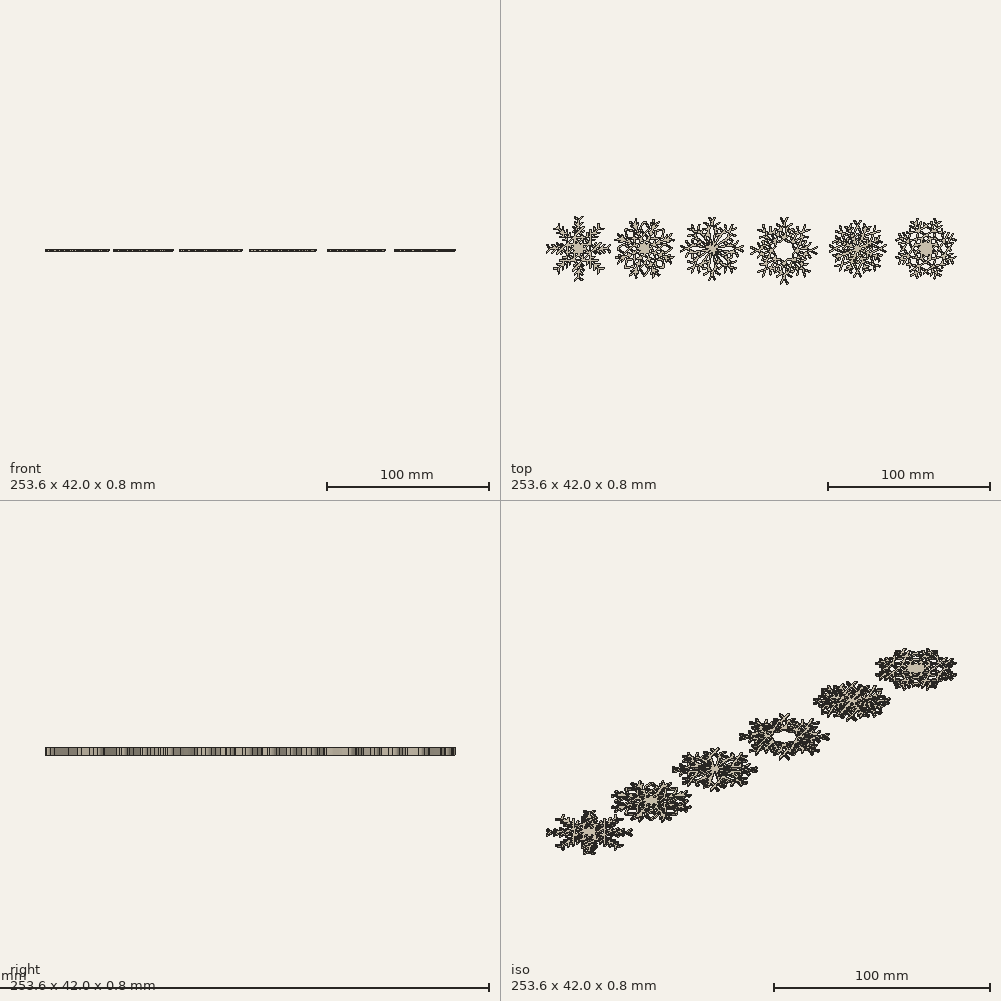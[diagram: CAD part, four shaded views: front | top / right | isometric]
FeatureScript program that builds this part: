
annotation { "Feature Type Name" : "Feature", "Feature Type Description" : "" }
export const myFeature = defineFeature(function(context is Context, id is Id, definition is map)
    precondition{}
    {
        {
            var Q0;
            Q0=qCreatedBy(makeId("Top.planeOp"),FACE);
            var sketch = newSketch(context, id + "F0", { "sketchPlane" : qUnion([Q0])});
            skFitSpline(sketch, "E0", {"points": [v(9.25, 5.53) * mm, v(8.92, 5.5) * mm, v(7.79, 5.23) * mm, v(7.5, 5.1) * mm]});
            skFitSpline(sketch, "E1", {"points": [v(7.5, 5.1) * mm, v(7.78, 4.57) * mm, v(8.1, 4.08) * mm, v(8.43, 3.59) * mm]});
            skFitSpline(sketch, "E2", {"points": [v(8.43, 3.59) * mm, v(8.94, 3.76) * mm, v(9.43, 3.93) * mm, v(9.95, 4.1) * mm]});
            skFitSpline(sketch, "E3", {"points": [v(9.95, 4.1) * mm, v(9.7, 4.6) * mm, v(9.47, 5.07) * mm, v(9.25, 5.53) * mm]});
            skFitSpline(sketch, "E4", {"points": [v(15.97, -10.43) * mm, v(15.7, -10.56) * mm, v(15.46, -10.66) * mm, v(15.23, -10.77) * mm]});
            skFitSpline(sketch, "E5", {"points": [v(15.23, -10.77) * mm, v(15, -10.88) * mm, v(14.77, -11.01) * mm, v(14.52, -11.14) * mm]});
            skFitSpline(sketch, "E6", {"points": [v(14.52, -11.14) * mm, v(14.65, -11.71) * mm, v(14.75, -12.3) * mm, v(14.96, -12.89) * mm]});
            skFitSpline(sketch, "E7", {"points": [v(14.96, -12.89) * mm, v(15.5, -12.56) * mm, v(15.99, -12.25) * mm, v(16.48, -11.95) * mm]});
            skFitSpline(sketch, "E8", {"points": [v(16.48, -11.95) * mm, v(16.3, -11.43) * mm, v(16.14, -10.94) * mm, v(15.97, -10.43) * mm]});
            skFitSpline(sketch, "E9", {"points": [v(32, 3.59) * mm, v(32.33, 4.1) * mm, v(32.66, 4.58) * mm, v(32.95, 5.14) * mm]});
            skFitSpline(sketch, "E10", {"points": [v(32.95, 5.14) * mm, v(32.34, 5.29) * mm, v(31.77, 5.42) * mm, v(31.2, 5.56) * mm]});
            skFitSpline(sketch, "E11", {"points": [v(31.2, 5.56) * mm, v(30.96, 5.06) * mm, v(30.73, 4.6) * mm, v(30.49, 4.1) * mm]});
            skFitSpline(sketch, "E12", {"points": [v(30.49, 4.1) * mm, v(31, 3.93) * mm, v(31.5, 3.76) * mm, v(32, 3.59) * mm]});
            skFitSpline(sketch, "E13", {"points": [v(32.98, -5.43) * mm, v(32.63, -4.88) * mm, v(32.33, -4.39) * mm, v(32.02, -3.88) * mm]});
            skFitSpline(sketch, "E14", {"points": [v(32.02, -3.88) * mm, v(31.5, -4.06) * mm, v(31.01, -4.22) * mm, v(30.49, -4.4) * mm]});
            skFitSpline(sketch, "E15", {"points": [v(30.49, -4.4) * mm, v(30.73, -4.9) * mm, v(30.96, -5.36) * mm, v(31.2, -5.85) * mm]});
            skFitSpline(sketch, "E16", {"points": [v(31.2, -5.85) * mm, v(31.78, -5.72) * mm, v(32.35, -5.58) * mm, v(32.98, -5.43) * mm]});
            skFitSpline(sketch, "E17", {"points": [v(25.9, 10.83) * mm, v(25.8, 11.42) * mm, v(25.67, 12) * mm, v(25.49, 12.57) * mm]});
            skFitSpline(sketch, "E18", {"points": [v(25.49, 12.57) * mm, v(24.94, 12.3) * mm, v(24.45, 11.97) * mm, v(23.96, 11.64) * mm]});
            skFitSpline(sketch, "E19", {"points": [v(23.96, 11.64) * mm, v(24.14, 11.14) * mm, v(24.24, 10.62) * mm, v(24.5, 10.14) * mm]});
            skFitSpline(sketch, "E20", {"points": [v(24.5, 10.14) * mm, v(24.97, 10.37) * mm, v(25.44, 10.6) * mm, v(25.9, 10.83) * mm]});
            skFitSpline(sketch, "E21", {"points": [v(9.23, -5.86) * mm, v(9.48, -5.36) * mm, v(9.7, -4.9) * mm, v(9.95, -4.4) * mm]});
            skFitSpline(sketch, "E22", {"points": [v(9.95, -4.4) * mm, v(9.42, -4.22) * mm, v(8.92, -4.05) * mm, v(8.42, -3.89) * mm]});
            skFitSpline(sketch, "E23", {"points": [v(8.42, -3.89) * mm, v(8.1, -4.4) * mm, v(7.76, -4.88) * mm, v(7.48, -5.44) * mm]});
            skFitSpline(sketch, "E24", {"points": [v(7.48, -5.44) * mm, v(8.09, -5.58) * mm, v(8.65, -5.72) * mm, v(9.23, -5.86) * mm]});
            skFitSpline(sketch, "E25", {"points": [v(16.48, 11.64) * mm, v(15.98, 11.96) * mm, v(15.5, 12.3) * mm, v(14.92, 12.58) * mm]});
            skFitSpline(sketch, "E26", {"points": [v(14.92, 12.58) * mm, v(14.78, 11.97) * mm, v(14.64, 11.4) * mm, v(14.51, 10.83) * mm]});
            skFitSpline(sketch, "E27", {"points": [v(14.51, 10.83) * mm, v(15, 10.6) * mm, v(15.46, 10.37) * mm, v(15.96, 10.12) * mm]});
            skFitSpline(sketch, "E28", {"points": [v(15.96, 10.12) * mm, v(16.14, 10.64) * mm, v(16.3, 11.14) * mm, v(16.48, 11.64) * mm]});
            skFitSpline(sketch, "E29", {"points": [v(25.48, -12.9) * mm, v(25.67, -12.28) * mm, v(25.8, -11.7) * mm, v(25.9, -11.13) * mm]});
            skFitSpline(sketch, "E30", {"points": [v(25.9, -11.13) * mm, v(25.42, -10.89) * mm, v(24.96, -10.66) * mm, v(24.47, -10.42) * mm]});
            skFitSpline(sketch, "E31", {"points": [v(24.47, -10.42) * mm, v(24.3, -10.95) * mm, v(24.12, -11.44) * mm, v(23.95, -11.95) * mm]});
            skFitSpline(sketch, "E32", {"points": [v(23.95, -11.95) * mm, v(24.46, -12.26) * mm, v(24.95, -12.57) * mm, v(25.48, -12.9) * mm]});
            skLineSegment(sketch, "E33", {"start": v(31, -7.7) * mm, "end": v(31.03, -7.68) * mm});
            skFitSpline(sketch, "E34", {"points": [v(31.03, -7.68) * mm, v(30.53, -6.7) * mm, v(30.04, -5.7) * mm, v(29.54, -4.7) * mm]});
            skFitSpline(sketch, "E35", {"points": [v(29.54, -4.7) * mm, v(28.68, -4.98) * mm, v(27.82, -5.24) * mm, v(26.95, -5.5) * mm]});
            skFitSpline(sketch, "E36", {"points": [v(26.95, -5.5) * mm, v(28.31, -6.25) * mm, v(29.65, -6.98) * mm, v(31, -7.7) * mm]});
            skFitSpline(sketch, "E37", {"points": [v(30.04, -3.52) * mm, v(31.1, -3.16) * mm, v(32.16, -2.81) * mm, v(33.26, -2.45) * mm]});
            skFitSpline(sketch, "E38", {"points": [v(33.26, -2.45) * mm, v(31.74, -2) * mm, v(30.27, -1.56) * mm, v(28.77, -1.12) * mm]});
            skFitSpline(sketch, "E39", {"points": [v(28.77, -1.12) * mm, v(29.2, -1.94) * mm, v(29.61, -2.72) * mm, v(30.04, -3.52) * mm]});
            skFitSpline(sketch, "E40", {"points": [v(7.17, -2.45) * mm, v(8.28, -2.82) * mm, v(9.34, -3.17) * mm, v(10.4, -3.52) * mm]});
            skFitSpline(sketch, "E41", {"points": [v(10.4, -3.52) * mm, v(10.82, -2.73) * mm, v(11.23, -1.94) * mm, v(11.66, -1.12) * mm]});
            skFitSpline(sketch, "E42", {"points": [v(11.66, -1.12) * mm, v(10.16, -1.57) * mm, v(8.69, -2) * mm, v(7.17, -2.45) * mm]});
            skFitSpline(sketch, "E43", {"points": [v(25.58, 6.58) * mm, v(26.33, 7.96) * mm, v(27.06, 9.3) * mm, v(27.81, 10.7) * mm]});
            skFitSpline(sketch, "E44", {"points": [v(27.81, 10.7) * mm, v(26.77, 10.17) * mm, v(25.77, 9.68) * mm, v(24.78, 9.18) * mm]});
            skFitSpline(sketch, "E45", {"points": [v(24.78, 9.18) * mm, v(25.04, 8.32) * mm, v(25.3, 7.47) * mm, v(25.58, 6.58) * mm]});
            skFitSpline(sketch, "E46", {"points": [v(23.59, 9.67) * mm, v(23.23, 10.73) * mm, v(22.88, 11.79) * mm, v(22.51, 12.9) * mm]});
            skFitSpline(sketch, "E47", {"points": [v(22.51, 12.9) * mm, v(22.06, 11.37) * mm, v(21.63, 9.9) * mm, v(21.19, 8.4) * mm]});
            skFitSpline(sketch, "E48", {"points": [v(21.19, 8.4) * mm, v(22, 8.83) * mm, v(22.8, 9.25) * mm, v(23.59, 9.67) * mm]});
            skFitSpline(sketch, "E49", {"points": [v(15.66, -9.47) * mm, v(15.39, -8.61) * mm, v(15.13, -7.76) * mm, v(14.86, -6.88) * mm]});
            skFitSpline(sketch, "E50", {"points": [v(14.86, -6.88) * mm, v(14.1, -8.26) * mm, v(13.38, -9.6) * mm, v(12.62, -11) * mm]});
            skFitSpline(sketch, "E51", {"points": [v(12.62, -11) * mm, v(13.67, -10.47) * mm, v(14.66, -9.97) * mm, v(15.66, -9.47) * mm]});
            skFitSpline(sketch, "E52", {"points": [v(28.76, 0.8) * mm, v(29.1, 0.9) * mm, v(29.4, 1) * mm, v(29.7, 1.09) * mm]});
            skFitSpline(sketch, "E53", {"points": [v(29.7, 1.09) * mm, v(29.99, 1.18) * mm, v(30.28, 1.28) * mm, v(30.58, 1.36) * mm]});
            skFitSpline(sketch, "E54", {"points": [v(30.58, 1.36) * mm, v(30.87, 1.45) * mm, v(31.16, 1.53) * mm, v(31.46, 1.61) * mm]});
            skFitSpline(sketch, "E55", {"points": [v(31.46, 1.61) * mm, v(31.75, 1.7) * mm, v(32.05, 1.78) * mm, v(32.35, 1.87) * mm]});
            skFitSpline(sketch, "E56", {"points": [v(32.35, 1.87) * mm, v(32.64, 1.96) * mm, v(32.93, 2.05) * mm, v(33.25, 2.15) * mm]});
            skFitSpline(sketch, "E57", {"points": [v(33.25, 2.15) * mm, v(32.15, 2.52) * mm, v(31.1, 2.87) * mm, v(30.04, 3.22) * mm]});
            skFitSpline(sketch, "E58", {"points": [v(30.04, 3.22) * mm, v(29.62, 2.43) * mm, v(29.2, 1.65) * mm, v(28.76, 0.8) * mm]});
            skFitSpline(sketch, "E59", {"points": [v(13.49, 5.21) * mm, v(12.1, 5.96) * mm, v(10.76, 6.7) * mm, v(9.37, 7.45) * mm]});
            skFitSpline(sketch, "E60", {"points": [v(9.37, 7.45) * mm, v(9.9, 6.4) * mm, v(10.4, 5.4) * mm, v(10.9, 4.41) * mm]});
            skFitSpline(sketch, "E61", {"points": [v(10.9, 4.41) * mm, v(11.76, 4.68) * mm, v(12.6, 4.94) * mm, v(13.49, 5.21) * mm]});
            skFitSpline(sketch, "E62", {"points": [v(31.03, 7.38) * mm, v(31.02, 7.4) * mm, v(31, 7.4) * mm, v(31, 7.41) * mm]});
            skFitSpline(sketch, "E63", {"points": [v(31, 7.41) * mm, v(29.66, 6.68) * mm, v(28.32, 5.95) * mm, v(26.95, 5.2) * mm]});
            skFitSpline(sketch, "E64", {"points": [v(26.95, 5.2) * mm, v(27.83, 4.94) * mm, v(28.68, 4.68) * mm, v(29.54, 4.41) * mm]});
            skFitSpline(sketch, "E65", {"points": [v(29.54, 4.41) * mm, v(30.04, 5.4) * mm, v(30.53, 6.4) * mm, v(31.03, 7.38) * mm]});
            skFitSpline(sketch, "E66", {"points": [v(17.9, -13.13) * mm, v(17.91, -13.13) * mm, v(17.93, -13.13) * mm, v(17.94, -13.13) * mm]});
            skFitSpline(sketch, "E67", {"points": [v(17.94, -13.13) * mm, v(18.16, -12.4) * mm, v(18.37, -11.67) * mm, v(18.58, -10.94) * mm]});
            skFitSpline(sketch, "E68", {"points": [v(18.58, -10.94) * mm, v(18.8, -10.2) * mm, v(19.02, -9.47) * mm, v(19.25, -8.7) * mm]});
            skFitSpline(sketch, "E69", {"points": [v(19.25, -8.7) * mm, v(18.42, -9.14) * mm, v(17.63, -9.56) * mm, v(16.85, -9.97) * mm]});
            skFitSpline(sketch, "E70", {"points": [v(16.85, -9.97) * mm, v(17.2, -11.03) * mm, v(17.55, -12.08) * mm, v(17.9, -13.13) * mm]});
            skFitSpline(sketch, "E71", {"points": [v(13.48, -5.5) * mm, v(12.6, -5.24) * mm, v(11.75, -4.97) * mm, v(10.9, -4.7) * mm]});
            skFitSpline(sketch, "E72", {"points": [v(10.9, -4.7) * mm, v(10.39, -5.71) * mm, v(9.9, -6.7) * mm, v(9.37, -7.75) * mm]});
            skFitSpline(sketch, "E73", {"points": [v(9.37, -7.75) * mm, v(10.77, -6.99) * mm, v(12.1, -6.26) * mm, v(13.48, -5.5) * mm]});
            skFitSpline(sketch, "E74", {"points": [v(15.66, 9.18) * mm, v(14.66, 9.68) * mm, v(13.66, 10.17) * mm, v(12.62, 10.7) * mm]});
            skFitSpline(sketch, "E75", {"points": [v(12.62, 10.7) * mm, v(13.38, 9.3) * mm, v(14.1, 7.96) * mm, v(14.86, 6.58) * mm]});
            skFitSpline(sketch, "E76", {"points": [v(14.86, 6.58) * mm, v(15.13, 7.46) * mm, v(15.39, 8.3) * mm, v(15.66, 9.18) * mm]});
            skFitSpline(sketch, "E77", {"points": [v(22.51, -13.19) * mm, v(22.88, -12.08) * mm, v(23.23, -11.02) * mm, v(23.59, -9.97) * mm]});
            skFitSpline(sketch, "E78", {"points": [v(23.59, -9.97) * mm, v(22.79, -9.55) * mm, v(22, -9.13) * mm, v(21.19, -8.7) * mm]});
            skFitSpline(sketch, "E79", {"points": [v(21.19, -8.7) * mm, v(21.63, -10.2) * mm, v(22.07, -11.67) * mm, v(22.51, -13.19) * mm]});
            skFitSpline(sketch, "E80", {"points": [v(7.22, 2.16) * mm, v(7.22, 2.15) * mm, v(7.22, 2.14) * mm, v(7.22, 2.13) * mm]});
            skFitSpline(sketch, "E81", {"points": [v(7.22, 2.13) * mm, v(7.95, 1.91) * mm, v(8.7, 1.7) * mm, v(9.42, 1.49) * mm]});
            skFitSpline(sketch, "E82", {"points": [v(9.42, 1.49) * mm, v(10.16, 1.27) * mm, v(10.9, 1.05) * mm, v(11.67, 0.81) * mm]});
            skFitSpline(sketch, "E83", {"points": [v(11.67, 0.81) * mm, v(11.23, 1.65) * mm, v(10.81, 2.44) * mm, v(10.4, 3.22) * mm]});
            skFitSpline(sketch, "E84", {"points": [v(10.4, 3.22) * mm, v(9.33, 2.87) * mm, v(8.28, 2.52) * mm, v(7.22, 2.16) * mm]});
            skFitSpline(sketch, "E85", {"points": [v(27.81, -11) * mm, v(27.05, -9.6) * mm, v(26.32, -8.25) * mm, v(25.58, -6.88) * mm]});
            skFitSpline(sketch, "E86", {"points": [v(25.58, -6.88) * mm, v(25.3, -7.77) * mm, v(25.04, -8.62) * mm, v(24.78, -9.47) * mm]});
            skFitSpline(sketch, "E87", {"points": [v(24.78, -9.47) * mm, v(25.78, -9.98) * mm, v(26.77, -10.47) * mm, v(27.81, -11) * mm]});
            skFitSpline(sketch, "E88", {"points": [v(17.94, 12.83) * mm, v(17.92, 12.83) * mm, v(17.91, 12.83) * mm, v(17.9, 12.83) * mm]});
            skFitSpline(sketch, "E89", {"points": [v(17.9, 12.83) * mm, v(17.55, 11.78) * mm, v(17.2, 10.72) * mm, v(16.85, 9.67) * mm]});
            skFitSpline(sketch, "E90", {"points": [v(16.85, 9.67) * mm, v(17.64, 9.25) * mm, v(18.43, 8.84) * mm, v(19.25, 8.4) * mm]});
            skFitSpline(sketch, "E91", {"points": [v(19.25, 8.4) * mm, v(18.8, 9.9) * mm, v(18.37, 11.37) * mm, v(17.94, 12.83) * mm]});
            skFitSpline(sketch, "E92", {"points": [v(12.85, 0.75) * mm, v(13.06, 1) * mm, v(13.24, 1.21) * mm, v(13.4, 1.44) * mm]});
            skFitSpline(sketch, "E93", {"points": [v(13.4, 1.44) * mm, v(13.61, 1.73) * mm, v(13.83, 2.02) * mm, v(14.1, 2.26) * mm]});
            skFitSpline(sketch, "E94", {"points": [v(14.1, 2.26) * mm, v(14.18, 2.33) * mm, v(14.19, 2.42) * mm, v(14.2, 2.51) * mm]});
            skFitSpline(sketch, "E95", {"points": [v(14.2, 2.51) * mm, v(14.2, 2.77) * mm, v(14.21, 3.02) * mm, v(14.23, 3.28) * mm]});
            skFitSpline(sketch, "E96", {"points": [v(14.23, 3.28) * mm, v(14.25, 3.45) * mm, v(14.3, 3.62) * mm, v(14.31, 3.8) * mm]});
            skFitSpline(sketch, "E97", {"points": [v(14.31, 3.8) * mm, v(14.33, 4) * mm, v(14.34, 4.2) * mm, v(14.36, 4.42) * mm]});
            skFitSpline(sketch, "E98", {"points": [v(14.36, 4.42) * mm, v(13.34, 4.14) * mm, v(12.35, 3.88) * mm, v(11.36, 3.52) * mm]});
            skFitSpline(sketch, "E99", {"points": [v(11.36, 3.52) * mm, v(11.81, 2.56) * mm, v(12.33, 1.67) * mm, v(12.85, 0.75) * mm]});
            skFitSpline(sketch, "E100", {"points": [v(15.68, -6) * mm, v(15.7, -6.37) * mm, v(16.4, -8.68) * mm, v(16.58, -8.99) * mm]});
            skFitSpline(sketch, "E101", {"points": [v(16.58, -8.99) * mm, v(17.5, -8.55) * mm, v(18.4, -8.04) * mm, v(19.31, -7.51) * mm]});
            skFitSpline(sketch, "E102", {"points": [v(19.31, -7.51) * mm, v(19.1, -7.34) * mm, v(18.93, -7.2) * mm, v(18.74, -7.05) * mm]});
            skFitSpline(sketch, "E103", {"points": [v(18.74, -7.05) * mm, v(18.41, -6.8) * mm, v(18.07, -6.57) * mm, v(17.8, -6.25) * mm]});
            skFitSpline(sketch, "E104", {"points": [v(17.8, -6.25) * mm, v(17.72, -6.16) * mm, v(17.63, -6.17) * mm, v(17.53, -6.17) * mm]});
            skFitSpline(sketch, "E105", {"points": [v(17.53, -6.17) * mm, v(17.19, -6.18) * mm, v(16.85, -6.15) * mm, v(16.5, -6.09) * mm]});
            skFitSpline(sketch, "E106", {"points": [v(16.5, -6.09) * mm, v(16.24, -6.03) * mm, v(15.96, -6.03) * mm, v(15.68, -6) * mm]});
            skFitSpline(sketch, "E107", {"points": [v(11.39, -3.82) * mm, v(12.36, -4.18) * mm, v(13.35, -4.44) * mm, v(14.37, -4.72) * mm]});
            skFitSpline(sketch, "E108", {"points": [v(14.37, -4.72) * mm, v(14.34, -4.49) * mm, v(14.33, -4.27) * mm, v(14.3, -4.06) * mm]});
            skFitSpline(sketch, "E109", {"points": [v(14.3, -4.06) * mm, v(14.25, -3.65) * mm, v(14.16, -3.24) * mm, v(14.2, -2.83) * mm]});
            skFitSpline(sketch, "E110", {"points": [v(14.2, -2.83) * mm, v(14.2, -2.7) * mm, v(14.14, -2.6) * mm, v(14.06, -2.52) * mm]});
            skFitSpline(sketch, "E111", {"points": [v(14.06, -2.52) * mm, v(13.85, -2.28) * mm, v(13.64, -2.03) * mm, v(13.44, -1.78) * mm]});
            skFitSpline(sketch, "E112", {"points": [v(13.44, -1.78) * mm, v(13.25, -1.55) * mm, v(13.06, -1.3) * mm, v(12.86, -1.06) * mm]});
            skFitSpline(sketch, "E113", {"points": [v(12.86, -1.06) * mm, v(12.52, -1.56) * mm, v(11.5, -3.47) * mm, v(11.39, -3.82) * mm]});
            skFitSpline(sketch, "E114", {"points": [v(27.58, 0.75) * mm, v(28.1, 1.67) * mm, v(28.62, 2.56) * mm, v(29.07, 3.52) * mm]});
            skFitSpline(sketch, "E115", {"points": [v(29.07, 3.52) * mm, v(28.08, 3.88) * mm, v(27.09, 4.15) * mm, v(26.07, 4.42) * mm]});
            skFitSpline(sketch, "E116", {"points": [v(26.07, 4.42) * mm, v(26.09, 4.2) * mm, v(26.1, 4.02) * mm, v(26.12, 3.84) * mm]});
            skFitSpline(sketch, "E117", {"points": [v(26.12, 3.84) * mm, v(26.17, 3.4) * mm, v(26.27, 2.97) * mm, v(26.23, 2.53) * mm]});
            skFitSpline(sketch, "E118", {"points": [v(26.23, 2.53) * mm, v(26.22, 2.4) * mm, v(26.27, 2.33) * mm, v(26.36, 2.24) * mm]});
            skFitSpline(sketch, "E119", {"points": [v(26.36, 2.24) * mm, v(26.56, 2) * mm, v(26.77, 1.77) * mm, v(26.96, 1.53) * mm]});
            skFitSpline(sketch, "E120", {"points": [v(26.96, 1.53) * mm, v(27.16, 1.29) * mm, v(27.35, 1.03) * mm, v(27.58, 0.75) * mm]});
            skFitSpline(sketch, "E121", {"points": [v(23.88, 8.7) * mm, v(22.91, 8.25) * mm, v(22.03, 7.74) * mm, v(21.12, 7.22) * mm]});
            skFitSpline(sketch, "E122", {"points": [v(21.12, 7.22) * mm, v(21.31, 7.06) * mm, v(21.47, 6.92) * mm, v(21.64, 6.79) * mm]});
            skFitSpline(sketch, "E123", {"points": [v(21.64, 6.79) * mm, v(21.98, 6.53) * mm, v(22.35, 6.3) * mm, v(22.63, 5.96) * mm]});
            skFitSpline(sketch, "E124", {"points": [v(22.63, 5.96) * mm, v(22.7, 5.88) * mm, v(22.8, 5.87) * mm, v(22.9, 5.87) * mm]});
            skFitSpline(sketch, "E125", {"points": [v(22.9, 5.87) * mm, v(23.23, 5.88) * mm, v(23.56, 5.85) * mm, v(23.9, 5.8) * mm]});
            skFitSpline(sketch, "E126", {"points": [v(23.9, 5.8) * mm, v(24.18, 5.74) * mm, v(24.47, 5.73) * mm, v(24.79, 5.7) * mm]});
            skFitSpline(sketch, "E127", {"points": [v(24.79, 5.7) * mm, v(24.51, 6.71) * mm, v(24.25, 7.7) * mm, v(23.88, 8.7) * mm]});
            skFitSpline(sketch, "E128", {"points": [v(24.79, -6) * mm, v(24.57, -6.02) * mm, v(24.38, -6.03) * mm, v(24.2, -6.05) * mm]});
            skFitSpline(sketch, "E129", {"points": [v(24.2, -6.05) * mm, v(23.76, -6.1) * mm, v(23.33, -6.2) * mm, v(22.88, -6.17) * mm]});
            skFitSpline(sketch, "E130", {"points": [v(22.88, -6.17) * mm, v(22.77, -6.16) * mm, v(22.7, -6.2) * mm, v(22.61, -6.28) * mm]});
            skFitSpline(sketch, "E131", {"points": [v(22.61, -6.28) * mm, v(22.36, -6.5) * mm, v(22.1, -6.72) * mm, v(21.85, -6.93) * mm]});
            skFitSpline(sketch, "E132", {"points": [v(21.85, -6.93) * mm, v(21.61, -7.12) * mm, v(21.38, -7.3) * mm, v(21.14, -7.5) * mm]});
            skFitSpline(sketch, "E133", {"points": [v(21.14, -7.5) * mm, v(21.53, -7.81) * mm, v(23.61, -8.92) * mm, v(23.9, -8.96) * mm]});
            skFitSpline(sketch, "E134", {"points": [v(23.9, -8.96) * mm, v(24.24, -8) * mm, v(24.51, -7.01) * mm, v(24.79, -6) * mm]});
            skFitSpline(sketch, "E135", {"points": [v(26.05, -4.7) * mm, v(26.82, -4.57) * mm, v(28.83, -3.95) * mm, v(29.05, -3.77) * mm]});
            skFitSpline(sketch, "E136", {"points": [v(29.05, -3.77) * mm, v(28.6, -2.85) * mm, v(28.11, -1.96) * mm, v(27.58, -1.06) * mm]});
            skFitSpline(sketch, "E137", {"points": [v(27.58, -1.06) * mm, v(27.42, -1.25) * mm, v(27.28, -1.4) * mm, v(27.15, -1.58) * mm]});
            skFitSpline(sketch, "E138", {"points": [v(27.15, -1.58) * mm, v(26.9, -1.92) * mm, v(26.65, -2.28) * mm, v(26.33, -2.57) * mm]});
            skFitSpline(sketch, "E139", {"points": [v(26.33, -2.57) * mm, v(26.24, -2.64) * mm, v(26.24, -2.73) * mm, v(26.23, -2.83) * mm]});
            skFitSpline(sketch, "E140", {"points": [v(26.23, -2.83) * mm, v(26.22, -3.14) * mm, v(26.2, -3.45) * mm, v(26.17, -3.75) * mm]});
            skFitSpline(sketch, "E141", {"points": [v(26.17, -3.75) * mm, v(26.14, -4.06) * mm, v(26.1, -4.37) * mm, v(26.05, -4.7) * mm]});
            skFitSpline(sketch, "E142", {"points": [v(16.58, 8.7) * mm, v(16.37, 8.34) * mm, v(15.67, 5.97) * mm, v(15.7, 5.7) * mm]});
            skFitSpline(sketch, "E143", {"points": [v(15.7, 5.7) * mm, v(15.9, 5.72) * mm, v(16.1, 5.74) * mm, v(16.3, 5.76) * mm]});
            skFitSpline(sketch, "E144", {"points": [v(16.3, 5.76) * mm, v(16.72, 5.81) * mm, v(17.13, 5.9) * mm, v(17.54, 5.87) * mm]});
            skFitSpline(sketch, "E145", {"points": [v(17.54, 5.87) * mm, v(17.67, 5.86) * mm, v(17.75, 5.92) * mm, v(17.83, 6) * mm]});
            skFitSpline(sketch, "E146", {"points": [v(17.83, 6) * mm, v(18.08, 6.21) * mm, v(18.33, 6.42) * mm, v(18.58, 6.63) * mm]});
            skFitSpline(sketch, "E147", {"points": [v(18.58, 6.63) * mm, v(18.82, 6.82) * mm, v(19.06, 7.01) * mm, v(19.32, 7.22) * mm]});
            skFitSpline(sketch, "E148", {"points": [v(19.32, 7.22) * mm, v(18.39, 7.74) * mm, v(17.5, 8.26) * mm, v(16.58, 8.7) * mm]});
            skFitSpline(sketch, "E149", {"points": [v(9.52, 10.58) * mm, v(9.5, 10.54) * mm, v(9.5, 10.53) * mm, v(9.5, 10.53) * mm]});
            skFitSpline(sketch, "E150", {"points": [v(9.5, 10.53) * mm, v(9.81, 9.7) * mm, v(10.12, 8.89) * mm, v(10.43, 8.07) * mm]});
            skFitSpline(sketch, "E151", {"points": [v(10.43, 8.07) * mm, v(10.46, 8) * mm, v(10.52, 7.95) * mm, v(10.57, 7.92) * mm]});
            skFitSpline(sketch, "E152", {"points": [v(10.57, 7.92) * mm, v(11.48, 7.45) * mm, v(12.33, 6.88) * mm, v(13.27, 6.46) * mm]});
            skFitSpline(sketch, "E153", {"points": [v(13.27, 6.46) * mm, v(13.36, 6.42) * mm, v(13.45, 6.36) * mm, v(13.54, 6.3) * mm]});
            skFitSpline(sketch, "E154", {"points": [v(13.54, 6.3) * mm, v(13.67, 6.23) * mm, v(13.81, 6.16) * mm, v(14, 6.07) * mm]});
            skFitSpline(sketch, "E155", {"points": [v(14, 6.07) * mm, v(13.95, 6.16) * mm, v(13.94, 6.2) * mm, v(13.92, 6.23) * mm]});
            skFitSpline(sketch, "E156", {"points": [v(13.92, 6.23) * mm, v(13.75, 6.57) * mm, v(13.58, 6.91) * mm, v(13.41, 7.25) * mm]});
            skFitSpline(sketch, "E157", {"points": [v(13.41, 7.25) * mm, v(13.4, 7.29) * mm, v(13.37, 7.32) * mm, v(13.35, 7.36) * mm]});
            skFitSpline(sketch, "E158", {"points": [v(13.35, 7.36) * mm, v(12.97, 8.04) * mm, v(12.58, 8.72) * mm, v(12.2, 9.4) * mm]});
            skFitSpline(sketch, "E159", {"points": [v(12.2, 9.4) * mm, v(12.13, 9.55) * mm, v(12.03, 9.64) * mm, v(11.88, 9.7) * mm]});
            skFitSpline(sketch, "E160", {"points": [v(11.88, 9.7) * mm, v(11.41, 9.86) * mm, v(10.95, 10.03) * mm, v(10.49, 10.2) * mm]});
            skFitSpline(sketch, "E161", {"points": [v(10.49, 10.2) * mm, v(10.17, 10.33) * mm, v(9.85, 10.45) * mm, v(9.52, 10.58) * mm]});
            skFitSpline(sketch, "E162", {"points": [v(29.01, -0.14) * mm, v(29.09, -0.17) * mm, v(29.13, -0.2) * mm, v(29.17, -0.2) * mm]});
            skFitSpline(sketch, "E163", {"points": [v(29.17, -0.2) * mm, v(29.69, -0.37) * mm, v(30.2, -0.53) * mm, v(30.72, -0.69) * mm]});
            skFitSpline(sketch, "E164", {"points": [v(30.72, -0.69) * mm, v(31.36, -0.87) * mm, v(32, -1.04) * mm, v(32.63, -1.24) * mm]});
            skFitSpline(sketch, "E165", {"points": [v(32.63, -1.24) * mm, v(32.8, -1.3) * mm, v(32.94, -1.28) * mm, v(33.09, -1.2) * mm]});
            skFitSpline(sketch, "E166", {"points": [v(33.09, -1.2) * mm, v(33.46, -1.02) * mm, v(33.84, -0.85) * mm, v(34.22, -0.68) * mm]});
            skFitSpline(sketch, "E167", {"points": [v(34.22, -0.68) * mm, v(34.55, -0.53) * mm, v(34.89, -0.38) * mm, v(35.22, -0.24) * mm]});
            skFitSpline(sketch, "E168", {"points": [v(35.22, -0.24) * mm, v(35.28, -0.21) * mm, v(35.32, -0.18) * mm, v(35.4, -0.14) * mm]});
            skFitSpline(sketch, "E169", {"points": [v(35.4, -0.14) * mm, v(35.29, -0.1) * mm, v(35.22, -0.06) * mm, v(35.15, -0.03) * mm]});
            skFitSpline(sketch, "E170", {"points": [v(35.15, -0.03) * mm, v(34.7, 0.17) * mm, v(34.27, 0.35) * mm, v(33.83, 0.55) * mm]});
            skFitSpline(sketch, "E171", {"points": [v(33.83, 0.55) * mm, v(33.55, 0.67) * mm, v(33.28, 0.81) * mm, v(33, 0.93) * mm]});
            skFitSpline(sketch, "E172", {"points": [v(33, 0.93) * mm, v(32.92, 0.97) * mm, v(32.81, 0.99) * mm, v(32.73, 0.96) * mm]});
            skFitSpline(sketch, "E173", {"points": [v(32.73, 0.96) * mm, v(31.77, 0.66) * mm, v(30.77, 0.46) * mm, v(29.82, 0.1) * mm]});
            skFitSpline(sketch, "E174", {"points": [v(29.82, 0.1) * mm, v(29.74, 0.07) * mm, v(29.64, 0.05) * mm, v(29.55, 0.02) * mm]});
            skFitSpline(sketch, "E175", {"points": [v(29.55, 0.02) * mm, v(29.38, -0.03) * mm, v(29.21, -0.08) * mm, v(29.01, -0.14) * mm]});
            skFitSpline(sketch, "E176", {"points": [v(5.06, -0.14) * mm, v(5.09, -0.17) * mm, v(5.1, -0.19) * mm, v(5.12, -0.2) * mm]});
            skFitSpline(sketch, "E177", {"points": [v(5.12, -0.2) * mm, v(5.9, -0.55) * mm, v(6.68, -0.9) * mm, v(7.46, -1.25) * mm]});
            skFitSpline(sketch, "E178", {"points": [v(7.46, -1.25) * mm, v(7.53, -1.28) * mm, v(7.63, -1.28) * mm, v(7.71, -1.26) * mm]});
            skFitSpline(sketch, "E179", {"points": [v(7.71, -1.26) * mm, v(8.68, -0.95) * mm, v(9.67, -0.76) * mm, v(10.62, -0.4) * mm]});
            skFitSpline(sketch, "E180", {"points": [v(10.62, -0.4) * mm, v(10.72, -0.36) * mm, v(10.82, -0.34) * mm, v(10.92, -0.31) * mm]});
            skFitSpline(sketch, "E181", {"points": [v(10.92, -0.31) * mm, v(11.07, -0.26) * mm, v(11.23, -0.21) * mm, v(11.38, -0.16) * mm]});
            skFitSpline(sketch, "E182", {"points": [v(11.38, -0.16) * mm, v(11.12, -0.05) * mm, v(10.87, 0.02) * mm, v(10.62, 0.1) * mm]});
            skFitSpline(sketch, "E183", {"points": [v(10.62, 0.1) * mm, v(10.44, 0.15) * mm, v(10.27, 0.25) * mm, v(10.08, 0.3) * mm]});
            skFitSpline(sketch, "E184", {"points": [v(10.08, 0.3) * mm, v(9.32, 0.52) * mm, v(8.56, 0.72) * mm, v(7.8, 0.94) * mm]});
            skFitSpline(sketch, "E185", {"points": [v(7.8, 0.94) * mm, v(7.64, 0.99) * mm, v(7.5, 0.98) * mm, v(7.35, 0.9) * mm]});
            skFitSpline(sketch, "E186", {"points": [v(7.35, 0.9) * mm, v(6.64, 0.58) * mm, v(5.94, 0.27) * mm, v(5.23, -0.05) * mm]});
            skFitSpline(sketch, "E187", {"points": [v(5.23, -0.05) * mm, v(5.17, -0.08) * mm, v(5.12, -0.1) * mm, v(5.06, -0.14) * mm]});
            skFitSpline(sketch, "E188", {"points": [v(30.95, 10.59) * mm, v(30.86, 10.56) * mm, v(30.8, 10.54) * mm, v(30.77, 10.53) * mm]});
            skFitSpline(sketch, "E189", {"points": [v(30.77, 10.53) * mm, v(30.3, 10.34) * mm, v(29.82, 10.15) * mm, v(29.34, 9.97) * mm]});
            skFitSpline(sketch, "E190", {"points": [v(29.34, 9.97) * mm, v(29.07, 9.86) * mm, v(28.79, 9.77) * mm, v(28.5, 9.67) * mm]});
            skFitSpline(sketch, "E191", {"points": [v(28.5, 9.67) * mm, v(28.39, 9.63) * mm, v(28.3, 9.56) * mm, v(28.25, 9.44) * mm]});
            skFitSpline(sketch, "E192", {"points": [v(28.25, 9.44) * mm, v(27.92, 8.84) * mm, v(27.59, 8.24) * mm, v(27.26, 7.64) * mm]});
            skFitSpline(sketch, "E193", {"points": [v(27.26, 7.64) * mm, v(27.16, 7.46) * mm, v(27.06, 7.3) * mm, v(26.97, 7.12) * mm]});
            skFitSpline(sketch, "E194", {"points": [v(26.97, 7.12) * mm, v(26.86, 6.92) * mm, v(26.76, 6.72) * mm, v(26.66, 6.52) * mm]});
            skFitSpline(sketch, "E195", {"points": [v(26.66, 6.52) * mm, v(26.6, 6.39) * mm, v(26.5, 6.26) * mm, v(26.47, 6.1) * mm]});
            skFitSpline(sketch, "E196", {"points": [v(26.47, 6.1) * mm, v(26.5, 6.1) * mm, v(26.52, 6.1) * mm, v(26.54, 6.12) * mm]});
            skFitSpline(sketch, "E197", {"points": [v(26.54, 6.12) * mm, v(26.9, 6.3) * mm, v(27.26, 6.48) * mm, v(27.63, 6.66) * mm]});
            skFitSpline(sketch, "E198", {"points": [v(27.63, 6.66) * mm, v(27.66, 6.68) * mm, v(27.7, 6.7) * mm, v(27.73, 6.72) * mm]});
            skFitSpline(sketch, "E199", {"points": [v(27.73, 6.72) * mm, v(28.41, 7.1) * mm, v(29.1, 7.5) * mm, v(29.78, 7.87) * mm]});
            skFitSpline(sketch, "E200", {"points": [v(29.78, 7.87) * mm, v(29.92, 7.95) * mm, v(30, 8.05) * mm, v(30.06, 8.2) * mm]});
            skFitSpline(sketch, "E201", {"points": [v(30.06, 8.2) * mm, v(30.33, 8.92) * mm, v(30.6, 9.64) * mm, v(30.88, 10.37) * mm]});
            skFitSpline(sketch, "E202", {"points": [v(30.88, 10.37) * mm, v(30.9, 10.43) * mm, v(30.92, 10.48) * mm, v(30.95, 10.59) * mm]});
            skFitSpline(sketch, "E203", {"points": [v(30.94, -10.88) * mm, v(30.91, -10.78) * mm, v(30.9, -10.71) * mm, v(30.87, -10.65) * mm]});
            skFitSpline(sketch, "E204", {"points": [v(30.87, -10.65) * mm, v(30.62, -9.97) * mm, v(30.36, -9.3) * mm, v(30.1, -8.61) * mm]});
            skFitSpline(sketch, "E205", {"points": [v(30.1, -8.61) * mm, v(30.07, -8.53) * mm, v(30.05, -8.44) * mm, v(30, -8.37) * mm]});
            skFitSpline(sketch, "E206", {"points": [v(30, -8.37) * mm, v(29.97, -8.31) * mm, v(29.92, -8.25) * mm, v(29.86, -8.22) * mm]});
            skFitSpline(sketch, "E207", {"points": [v(29.86, -8.22) * mm, v(28.97, -7.75) * mm, v(28.12, -7.18) * mm, v(27.2, -6.77) * mm]});
            skFitSpline(sketch, "E208", {"points": [v(27.2, -6.77) * mm, v(27.09, -6.72) * mm, v(26.99, -6.65) * mm, v(26.88, -6.6) * mm]});
            skFitSpline(sketch, "E209", {"points": [v(26.88, -6.6) * mm, v(26.75, -6.53) * mm, v(26.62, -6.46) * mm, v(26.46, -6.38) * mm]});
            skFitSpline(sketch, "E210", {"points": [v(26.46, -6.38) * mm, v(26.48, -6.45) * mm, v(26.48, -6.47) * mm, v(26.5, -6.5) * mm]});
            skFitSpline(sketch, "E211", {"points": [v(26.5, -6.5) * mm, v(26.75, -6.97) * mm, v(27, -7.45) * mm, v(27.25, -7.93) * mm]});
            skFitSpline(sketch, "E212", {"points": [v(27.25, -7.93) * mm, v(27.58, -8.53) * mm, v(27.92, -9.11) * mm, v(28.23, -9.71) * mm]});
            skFitSpline(sketch, "E213", {"points": [v(28.23, -9.71) * mm, v(28.31, -9.86) * mm, v(28.42, -9.94) * mm, v(28.56, -10) * mm]});
            skFitSpline(sketch, "E214", {"points": [v(28.56, -10) * mm, v(29.3, -10.27) * mm, v(30.03, -10.55) * mm, v(30.76, -10.82) * mm]});
            skFitSpline(sketch, "E215", {"points": [v(30.76, -10.82) * mm, v(30.8, -10.84) * mm, v(30.86, -10.85) * mm, v(30.94, -10.88) * mm]});
            skFitSpline(sketch, "E216", {"points": [v(20.2, 8.64) * mm, v(20.24, 8.73) * mm, v(20.26, 8.77) * mm, v(20.27, 8.8) * mm]});
            skFitSpline(sketch, "E217", {"points": [v(20.27, 8.8) * mm, v(20.36, 9.07) * mm, v(20.43, 9.34) * mm, v(20.52, 9.6) * mm]});
            skFitSpline(sketch, "E218", {"points": [v(20.52, 9.6) * mm, v(20.56, 9.74) * mm, v(20.63, 9.87) * mm, v(20.67, 10) * mm]});
            skFitSpline(sketch, "E219", {"points": [v(20.67, 10) * mm, v(20.88, 10.76) * mm, v(21.08, 11.51) * mm, v(21.3, 12.26) * mm]});
            skFitSpline(sketch, "E220", {"points": [v(21.3, 12.26) * mm, v(21.36, 12.43) * mm, v(21.34, 12.56) * mm, v(21.27, 12.71) * mm]});
            skFitSpline(sketch, "E221", {"points": [v(21.27, 12.71) * mm, v(21.04, 13.22) * mm, v(20.8, 13.73) * mm, v(20.58, 14.24) * mm]});
            skFitSpline(sketch, "E222", {"points": [v(20.58, 14.24) * mm, v(20.48, 14.45) * mm, v(20.4, 14.66) * mm, v(20.3, 14.87) * mm]});
            skFitSpline(sketch, "E223", {"points": [v(20.3, 14.87) * mm, v(20.28, 14.92) * mm, v(20.24, 14.95) * mm, v(20.2, 15) * mm]});
            skFitSpline(sketch, "E224", {"points": [v(20.2, 15) * mm, v(19.83, 14.18) * mm, v(19.47, 13.39) * mm, v(19.11, 12.59) * mm]});
            skFitSpline(sketch, "E225", {"points": [v(19.11, 12.59) * mm, v(19.08, 12.52) * mm, v(19.1, 12.41) * mm, v(19.11, 12.34) * mm]});
            skFitSpline(sketch, "E226", {"points": [v(19.11, 12.34) * mm, v(19.41, 11.36) * mm, v(19.63, 10.35) * mm, v(20, 9.38) * mm]});
            skFitSpline(sketch, "E227", {"points": [v(20, 9.38) * mm, v(20.07, 9.16) * mm, v(20.12, 8.93) * mm, v(20.2, 8.64) * mm]});
            skFitSpline(sketch, "E228", {"points": [v(20.22, -8.96) * mm, v(20.06, -9.42) * mm, v(19.92, -9.84) * mm, v(19.77, -10.27) * mm]});
            skFitSpline(sketch, "E229", {"points": [v(19.77, -10.27) * mm, v(19.77, -10.28) * mm, v(19.76, -10.3) * mm, v(19.76, -10.31) * mm]});
            skFitSpline(sketch, "E230", {"points": [v(19.76, -10.31) * mm, v(19.55, -11.06) * mm, v(19.35, -11.82) * mm, v(19.12, -12.57) * mm]});
            skFitSpline(sketch, "E231", {"points": [v(19.12, -12.57) * mm, v(19.07, -12.73) * mm, v(19.1, -12.87) * mm, v(19.16, -13.02) * mm]});
            skFitSpline(sketch, "E232", {"points": [v(19.16, -13.02) * mm, v(19.5, -13.74) * mm, v(19.81, -14.46) * mm, v(20.14, -15.18) * mm]});
            skFitSpline(sketch, "E233", {"points": [v(20.14, -15.18) * mm, v(20.16, -15.22) * mm, v(20.18, -15.26) * mm, v(20.22, -15.32) * mm]});
            skFitSpline(sketch, "E234", {"points": [v(20.22, -15.32) * mm, v(20.26, -15.25) * mm, v(20.29, -15.2) * mm, v(20.3, -15.15) * mm]});
            skFitSpline(sketch, "E235", {"points": [v(20.3, -15.15) * mm, v(20.6, -14.48) * mm, v(20.91, -13.81) * mm, v(21.21, -13.14) * mm]});
            skFitSpline(sketch, "E236", {"points": [v(21.21, -13.14) * mm, v(21.25, -13.07) * mm, v(21.28, -13) * mm, v(21.31, -12.93) * mm]});
            skFitSpline(sketch, "E237", {"points": [v(21.31, -12.93) * mm, v(21.36, -12.83) * mm, v(21.36, -12.73) * mm, v(21.33, -12.63) * mm]});
            skFitSpline(sketch, "E238", {"points": [v(21.33, -12.63) * mm, v(21.24, -12.38) * mm, v(21.16, -12.13) * mm, v(21.1, -11.87) * mm]});
            skFitSpline(sketch, "E239", {"points": [v(21.1, -11.87) * mm, v(20.87, -10.96) * mm, v(20.57, -10.07) * mm, v(20.3, -9.17) * mm]});
            skFitSpline(sketch, "E240", {"points": [v(20.3, -9.17) * mm, v(20.27, -9.11) * mm, v(20.25, -9.05) * mm, v(20.22, -8.96) * mm]});
            skFitSpline(sketch, "E241", {"points": [v(9.49, -10.84) * mm, v(9.5, -10.85) * mm, v(9.52, -10.86) * mm, v(9.53, -10.88) * mm]});
            skFitSpline(sketch, "E242", {"points": [v(9.53, -10.88) * mm, v(9.65, -10.83) * mm, v(9.78, -10.78) * mm, v(9.9, -10.73) * mm]});
            skFitSpline(sketch, "E243", {"points": [v(9.9, -10.73) * mm, v(10.56, -10.48) * mm, v(11.22, -10.24) * mm, v(11.87, -9.99) * mm]});
            skFitSpline(sketch, "E244", {"points": [v(11.87, -9.99) * mm, v(11.98, -9.95) * mm, v(12.1, -9.92) * mm, v(12.16, -9.8) * mm]});
            skFitSpline(sketch, "E245", {"points": [v(12.16, -9.8) * mm, v(12.62, -8.88) * mm, v(13.2, -8.03) * mm, v(13.6, -7.1) * mm]});
            skFitSpline(sketch, "E246", {"points": [v(13.6, -7.1) * mm, v(13.65, -7) * mm, v(13.7, -6.93) * mm, v(13.75, -6.85) * mm]});
            skFitSpline(sketch, "E247", {"points": [v(13.75, -6.85) * mm, v(13.83, -6.7) * mm, v(13.9, -6.56) * mm, v(13.98, -6.42) * mm]});
            skFitSpline(sketch, "E248", {"points": [v(13.98, -6.42) * mm, v(13.9, -6.41) * mm, v(13.87, -6.43) * mm, v(13.84, -6.45) * mm]});
            skFitSpline(sketch, "E249", {"points": [v(13.84, -6.45) * mm, v(13.5, -6.62) * mm, v(13.15, -6.78) * mm, v(12.81, -6.95) * mm]});
            skFitSpline(sketch, "E250", {"points": [v(12.81, -6.95) * mm, v(12.78, -6.97) * mm, v(12.74, -7) * mm, v(12.7, -7.01) * mm]});
            skFitSpline(sketch, "E251", {"points": [v(12.7, -7.01) * mm, v(12.02, -7.4) * mm, v(11.33, -7.8) * mm, v(10.64, -8.17) * mm]});
            skFitSpline(sketch, "E252", {"points": [v(10.64, -8.17) * mm, v(10.5, -8.24) * mm, v(10.43, -8.33) * mm, v(10.39, -8.47) * mm]});
            skFitSpline(sketch, "E253", {"points": [v(10.39, -8.47) * mm, v(10.2, -8.98) * mm, v(10, -9.5) * mm, v(9.8, -10.01) * mm]});
            skFitSpline(sketch, "E254", {"points": [v(9.8, -10.01) * mm, v(9.7, -10.29) * mm, v(9.6, -10.56) * mm, v(9.49, -10.84) * mm]});
            skFitSpline(sketch, "E255", {"points": [v(20.2, 6.64) * mm, v(19.93, 6.43) * mm, v(19.66, 6.23) * mm, v(19.4, 6.03) * mm]});
            skFitSpline(sketch, "E256", {"points": [v(19.4, 6.03) * mm, v(19.03, 5.75) * mm, v(18.64, 5.49) * mm, v(18.34, 5.12) * mm]});
            skFitSpline(sketch, "E257", {"points": [v(18.34, 5.12) * mm, v(18.23, 4.98) * mm, v(18.06, 4.9) * mm, v(17.88, 4.92) * mm]});
            skFitSpline(sketch, "E258", {"points": [v(17.88, 4.92) * mm, v(17.43, 4.93) * mm, v(16.98, 4.89) * mm, v(16.54, 4.82) * mm]});
            skFitSpline(sketch, "E259", {"points": [v(16.54, 4.82) * mm, v(16.23, 4.77) * mm, v(15.91, 4.72) * mm, v(15.6, 4.68) * mm]});
            skFitSpline(sketch, "E260", {"points": [v(15.6, 4.68) * mm, v(15.46, 4.66) * mm, v(15.4, 4.6) * mm, v(15.39, 4.47) * mm]});
            skFitSpline(sketch, "E261", {"points": [v(15.39, 4.47) * mm, v(15.35, 4.2) * mm, v(15.32, 3.93) * mm, v(15.28, 3.67) * mm]});
            skFitSpline(sketch, "E262", {"points": [v(15.28, 3.67) * mm, v(15.2, 3.19) * mm, v(15.12, 2.7) * mm, v(15.15, 2.22) * mm]});
            skFitSpline(sketch, "E263", {"points": [v(15.15, 2.22) * mm, v(15.16, 2.02) * mm, v(15.09, 1.85) * mm, v(14.94, 1.72) * mm]});
            skFitSpline(sketch, "E264", {"points": [v(14.94, 1.72) * mm, v(14.58, 1.42) * mm, v(14.32, 1.04) * mm, v(14.04, 0.67) * mm]});
            skFitSpline(sketch, "E265", {"points": [v(14.04, 0.67) * mm, v(13.84, 0.4) * mm, v(13.64, 0.14) * mm, v(13.44, -0.12) * mm]});
            skFitSpline(sketch, "E266", {"points": [v(13.44, -0.12) * mm, v(13.47, -0.19) * mm, v(13.5, -0.23) * mm, v(13.52, -0.27) * mm]});
            skFitSpline(sketch, "E267", {"points": [v(13.52, -0.27) * mm, v(13.73, -0.55) * mm, v(13.94, -0.82) * mm, v(14.14, -1.1) * mm]});
            skFitSpline(sketch, "E268", {"points": [v(14.14, -1.1) * mm, v(14.38, -1.43) * mm, v(14.63, -1.76) * mm, v(14.95, -2.03) * mm]});
            skFitSpline(sketch, "E269", {"points": [v(14.95, -2.03) * mm, v(15.08, -2.14) * mm, v(15.15, -2.3) * mm, v(15.15, -2.48) * mm]});
            skFitSpline(sketch, "E270", {"points": [v(15.15, -2.48) * mm, v(15.14, -2.91) * mm, v(15.17, -3.34) * mm, v(15.24, -3.77) * mm]});
            skFitSpline(sketch, "E271", {"points": [v(15.24, -3.77) * mm, v(15.3, -4.1) * mm, v(15.34, -4.43) * mm, v(15.38, -4.76) * mm]});
            skFitSpline(sketch, "E272", {"points": [v(15.38, -4.76) * mm, v(15.4, -4.9) * mm, v(15.46, -4.97) * mm, v(15.6, -4.98) * mm]});
            skFitSpline(sketch, "E273", {"points": [v(15.6, -4.98) * mm, v(15.87, -5) * mm, v(16.13, -5.06) * mm, v(16.39, -5.1) * mm]});
            skFitSpline(sketch, "E274", {"points": [v(16.39, -5.1) * mm, v(16.86, -5.16) * mm, v(17.32, -5.24) * mm, v(17.8, -5.21) * mm]});
            skFitSpline(sketch, "E275", {"points": [v(17.8, -5.21) * mm, v(18.04, -5.2) * mm, v(18.23, -5.3) * mm, v(18.4, -5.48) * mm]});
            skFitSpline(sketch, "E276", {"points": [v(18.4, -5.48) * mm, v(18.61, -5.69) * mm, v(18.84, -5.88) * mm, v(19.06, -6.07) * mm]});
            skFitSpline(sketch, "E277", {"points": [v(19.06, -6.07) * mm, v(19.27, -6.25) * mm, v(19.49, -6.41) * mm, v(19.7, -6.58) * mm]});
            skFitSpline(sketch, "E278", {"points": [v(19.7, -6.58) * mm, v(19.87, -6.7) * mm, v(20.04, -6.8) * mm, v(20.23, -6.94) * mm]});
            skFitSpline(sketch, "E279", {"points": [v(20.23, -6.94) * mm, v(20.52, -6.72) * mm, v(20.8, -6.5) * mm, v(21.08, -6.3) * mm]});
            skFitSpline(sketch, "E280", {"points": [v(21.08, -6.3) * mm, v(21.4, -6.04) * mm, v(21.76, -5.82) * mm, v(22.03, -5.49) * mm]});
            skFitSpline(sketch, "E281", {"points": [v(22.03, -5.49) * mm, v(22.19, -5.29) * mm, v(22.4, -5.2) * mm, v(22.66, -5.2) * mm]});
            skFitSpline(sketch, "E282", {"points": [v(22.66, -5.2) * mm, v(23.03, -5.22) * mm, v(23.4, -5.2) * mm, v(23.78, -5.12) * mm]});
            skFitSpline(sketch, "E283", {"points": [v(23.78, -5.12) * mm, v(23.94, -5.09) * mm, v(24.1, -5.09) * mm, v(24.27, -5.06) * mm]});
            skFitSpline(sketch, "E284", {"points": [v(24.27, -5.06) * mm, v(24.52, -5.03) * mm, v(24.76, -5) * mm, v(25.03, -4.95) * mm]});
            skFitSpline(sketch, "E285", {"points": [v(25.03, -4.95) * mm, v(25.07, -4.62) * mm, v(25.11, -4.32) * mm, v(25.15, -4.01) * mm]});
            skFitSpline(sketch, "E286", {"points": [v(25.15, -4.01) * mm, v(25.22, -3.54) * mm, v(25.3, -3.07) * mm, v(25.28, -2.58) * mm]});
            skFitSpline(sketch, "E287", {"points": [v(25.28, -2.58) * mm, v(25.26, -2.33) * mm, v(25.37, -2.13) * mm, v(25.56, -1.95) * mm]});
            skFitSpline(sketch, "E288", {"points": [v(25.56, -1.95) * mm, v(25.76, -1.76) * mm, v(25.94, -1.55) * mm, v(26.12, -1.33) * mm]});
            skFitSpline(sketch, "E289", {"points": [v(26.12, -1.33) * mm, v(26.3, -1.11) * mm, v(26.48, -0.88) * mm, v(26.65, -0.65) * mm]});
            skFitSpline(sketch, "E290", {"points": [v(26.65, -0.65) * mm, v(26.77, -0.49) * mm, v(26.88, -0.31) * mm, v(27, -0.13) * mm]});
            skFitSpline(sketch, "E291", {"points": [v(27, -0.13) * mm, v(26.74, 0.21) * mm, v(26.48, 0.54) * mm, v(26.24, 0.87) * mm]});
            skFitSpline(sketch, "E292", {"points": [v(26.24, 0.87) * mm, v(26.04, 1.15) * mm, v(25.83, 1.43) * mm, v(25.57, 1.65) * mm]});
            skFitSpline(sketch, "E293", {"points": [v(25.57, 1.65) * mm, v(25.36, 1.82) * mm, v(25.27, 2.03) * mm, v(25.27, 2.3) * mm]});
            skFitSpline(sketch, "E294", {"points": [v(25.27, 2.3) * mm, v(25.28, 2.67) * mm, v(25.28, 3.05) * mm, v(25.19, 3.42) * mm]});
            skFitSpline(sketch, "E295", {"points": [v(25.19, 3.42) * mm, v(25.15, 3.59) * mm, v(25.15, 3.77) * mm, v(25.13, 3.94) * mm]});
            skFitSpline(sketch, "E296", {"points": [v(25.13, 3.94) * mm, v(25.1, 4.17) * mm, v(25.06, 4.4) * mm, v(25.02, 4.63) * mm]});
            skFitSpline(sketch, "E297", {"points": [v(25.02, 4.63) * mm, v(24.95, 4.65) * mm, v(24.91, 4.67) * mm, v(24.87, 4.67) * mm]});
            skFitSpline(sketch, "E298", {"points": [v(24.87, 4.67) * mm, v(24.57, 4.72) * mm, v(24.27, 4.76) * mm, v(23.98, 4.8) * mm]});
            skFitSpline(sketch, "E299", {"points": [v(23.98, 4.8) * mm, v(23.53, 4.87) * mm, v(23.1, 4.94) * mm, v(22.64, 4.91) * mm]});
            skFitSpline(sketch, "E300", {"points": [v(22.64, 4.91) * mm, v(22.38, 4.9) * mm, v(22.2, 5.01) * mm, v(22.01, 5.2) * mm]});
            skFitSpline(sketch, "E301", {"points": [v(22.01, 5.2) * mm, v(21.81, 5.4) * mm, v(21.6, 5.59) * mm, v(21.37, 5.77) * mm]});
            skFitSpline(sketch, "E302", {"points": [v(21.37, 5.77) * mm, v(21.16, 5.95) * mm, v(20.95, 6.11) * mm, v(20.73, 6.27) * mm]});
            skFitSpline(sketch, "E303", {"points": [v(20.73, 6.27) * mm, v(20.57, 6.4) * mm, v(20.4, 6.51) * mm, v(20.2, 6.64) * mm]});
            skFitSpline(sketch, "E304", {"points": [v(6.1, 1.4) * mm, v(5.9, 1.51) * mm, v(5.71, 1.56) * mm, v(5.52, 1.6) * mm]});
            skFitSpline(sketch, "E305", {"points": [v(5.52, 1.6) * mm, v(5.26, 1.65) * mm, v(5.08, 1.77) * mm, v(5, 2.03) * mm]});
            skFitSpline(sketch, "E306", {"points": [v(5, 2.03) * mm, v(4.98, 2.1) * mm, v(4.93, 2.14) * mm, v(4.9, 2.2) * mm]});
            skFitSpline(sketch, "E307", {"points": [v(4.9, 2.2) * mm, v(4.53, 2.72) * mm, v(4.16, 3.24) * mm, v(3.8, 3.76) * mm]});
            skFitSpline(sketch, "E308", {"points": [v(3.8, 3.76) * mm, v(3.72, 3.86) * mm, v(3.66, 3.96) * mm, v(3.6, 4.06) * mm]});
            skFitSpline(sketch, "E309", {"points": [v(3.6, 4.06) * mm, v(3.43, 4.35) * mm, v(3.5, 4.64) * mm, v(3.76, 4.78) * mm]});
            skFitSpline(sketch, "E310", {"points": [v(3.76, 4.78) * mm, v(4.02, 4.92) * mm, v(4.3, 4.8) * mm, v(4.47, 4.54) * mm]});
            skFitSpline(sketch, "E311", {"points": [v(4.47, 4.54) * mm, v(4.86, 3.93) * mm, v(5.28, 3.34) * mm, v(5.7, 2.73) * mm]});
            skFitSpline(sketch, "E312", {"points": [v(5.7, 2.73) * mm, v(6.3, 2.85) * mm, v(6.85, 3.1) * mm, v(7.45, 3.26) * mm]});
            skFitSpline(sketch, "E313", {"points": [v(7.45, 3.26) * mm, v(7.41, 3.33) * mm, v(7.4, 3.39) * mm, v(7.36, 3.44) * mm]});
            skFitSpline(sketch, "E314", {"points": [v(7.36, 3.44) * mm, v(7.01, 3.98) * mm, v(6.68, 4.52) * mm, v(6.42, 5.1) * mm]});
            skFitSpline(sketch, "E315", {"points": [v(6.42, 5.1) * mm, v(6.26, 5.45) * mm, v(6.42, 5.78) * mm, v(6.74, 5.9) * mm]});
            skFitSpline(sketch, "E316", {"points": [v(6.74, 5.9) * mm, v(7.34, 6.1) * mm, v(7.94, 6.27) * mm, v(8.56, 6.4) * mm]});
            skFitSpline(sketch, "E317", {"points": [v(8.56, 6.4) * mm, v(8.62, 6.41) * mm, v(8.68, 6.43) * mm, v(8.78, 6.46) * mm]});
            skFitSpline(sketch, "E318", {"points": [v(8.78, 6.46) * mm, v(8.5, 7) * mm, v(8.22, 7.54) * mm, v(7.95, 8.08) * mm]});
            skFitSpline(sketch, "E319", {"points": [v(7.95, 8.08) * mm, v(7.53, 8) * mm, v(7.15, 7.94) * mm, v(6.76, 7.87) * mm]});
            skFitSpline(sketch, "E320", {"points": [v(6.76, 7.87) * mm, v(6.4, 7.8) * mm, v(6.03, 7.72) * mm, v(5.67, 7.64) * mm]});
            skFitSpline(sketch, "E321", {"points": [v(5.67, 7.64) * mm, v(5.43, 7.6) * mm, v(5.16, 7.76) * mm, v(5.09, 8) * mm]});
            skFitSpline(sketch, "E322", {"points": [v(5.09, 8) * mm, v(5.02, 8.25) * mm, v(5.15, 8.52) * mm, v(5.4, 8.6) * mm]});
            skFitSpline(sketch, "E323", {"points": [v(5.4, 8.6) * mm, v(5.65, 8.67) * mm, v(5.9, 8.72) * mm, v(6.15, 8.76) * mm]});
            skFitSpline(sketch, "E324", {"points": [v(6.15, 8.76) * mm, v(6.7, 8.86) * mm, v(7.25, 8.95) * mm, v(7.8, 9.04) * mm]});
            skFitSpline(sketch, "E325", {"points": [v(7.8, 9.04) * mm, v(7.85, 9.05) * mm, v(7.9, 9.06) * mm, v(7.94, 9.08) * mm]});
            skFitSpline(sketch, "E326", {"points": [v(7.94, 9.08) * mm, v(8.17, 9.2) * mm, v(8.36, 9.15) * mm, v(8.57, 9.02) * mm]});
            skFitSpline(sketch, "E327", {"points": [v(8.57, 9.02) * mm, v(8.73, 8.9) * mm, v(8.92, 8.83) * mm, v(9.13, 8.71) * mm]});
            skFitSpline(sketch, "E328", {"points": [v(9.13, 8.71) * mm, v(9.11, 8.8) * mm, v(9.1, 8.85) * mm, v(9.09, 8.9) * mm]});
            skFitSpline(sketch, "E329", {"points": [v(9.09, 8.9) * mm, v(8.85, 9.55) * mm, v(8.6, 10.2) * mm, v(8.36, 10.85) * mm]});
            skFitSpline(sketch, "E330", {"points": [v(8.36, 10.85) * mm, v(8.31, 10.97) * mm, v(8.24, 11.04) * mm, v(8.12, 11.08) * mm]});
            skFitSpline(sketch, "E331", {"points": [v(8.12, 11.08) * mm, v(7.41, 11.31) * mm, v(6.7, 11.55) * mm, v(6, 11.78) * mm]});
            skFitSpline(sketch, "E332", {"points": [v(6, 11.78) * mm, v(5.48, 11.95) * mm, v(4.95, 12.12) * mm, v(4.43, 12.29) * mm]});
            skFitSpline(sketch, "E333", {"points": [v(4.43, 12.29) * mm, v(4.35, 12.31) * mm, v(4.27, 12.35) * mm, v(4.2, 12.4) * mm]});
            skFitSpline(sketch, "E334", {"points": [v(4.2, 12.4) * mm, v(4, 12.53) * mm, v(3.93, 12.76) * mm, v(4, 12.97) * mm]});
            skFitSpline(sketch, "E335", {"points": [v(4, 12.97) * mm, v(4.08, 13.18) * mm, v(4.28, 13.3) * mm, v(4.51, 13.27) * mm]});
            skFitSpline(sketch, "E336", {"points": [v(4.51, 13.27) * mm, v(4.58, 13.27) * mm, v(4.64, 13.25) * mm, v(4.7, 13.23) * mm]});
            skFitSpline(sketch, "E337", {"points": [v(4.7, 13.23) * mm, v(5.69, 12.9) * mm, v(6.67, 12.58) * mm, v(7.66, 12.26) * mm]});
            skFitSpline(sketch, "E338", {"points": [v(7.66, 12.26) * mm, v(7.71, 12.24) * mm, v(7.76, 12.23) * mm, v(7.86, 12.2) * mm]});
            skFitSpline(sketch, "E339", {"points": [v(7.86, 12.2) * mm, v(7.83, 12.3) * mm, v(7.82, 12.38) * mm, v(7.8, 12.46) * mm]});
            skFitSpline(sketch, "E340", {"points": [v(7.8, 12.46) * mm, v(7.59, 13.07) * mm, v(7.38, 13.67) * mm, v(7.18, 14.28) * mm]});
            skFitSpline(sketch, "E341", {"points": [v(7.18, 14.28) * mm, v(7.05, 14.66) * mm, v(6.93, 15.05) * mm, v(6.81, 15.44) * mm]});
            skFitSpline(sketch, "E342", {"points": [v(6.81, 15.44) * mm, v(6.7, 15.81) * mm, v(6.97, 16.15) * mm, v(7.34, 16.09) * mm]});
            skFitSpline(sketch, "E343", {"points": [v(7.34, 16.09) * mm, v(7.55, 16.05) * mm, v(7.68, 15.91) * mm, v(7.75, 15.72) * mm]});
            skFitSpline(sketch, "E344", {"points": [v(7.75, 15.72) * mm, v(7.83, 15.5) * mm, v(7.9, 15.27) * mm, v(7.97, 15.04) * mm]});
            skFitSpline(sketch, "E345", {"points": [v(7.97, 15.04) * mm, v(8.26, 14.15) * mm, v(8.55, 13.27) * mm, v(8.84, 12.38) * mm]});
            skFitSpline(sketch, "E346", {"points": [v(8.84, 12.38) * mm, v(8.9, 12.22) * mm, v(8.94, 12.06) * mm, v(9, 11.9) * mm]});
            skFitSpline(sketch, "E347", {"points": [v(9, 11.9) * mm, v(9.04, 11.84) * mm, v(9.1, 11.76) * mm, v(9.16, 11.74) * mm]});
            skFitSpline(sketch, "E348", {"points": [v(9.16, 11.74) * mm, v(9.84, 11.48) * mm, v(10.53, 11.22) * mm, v(11.22, 10.96) * mm]});
            skFitSpline(sketch, "E349", {"points": [v(11.22, 10.96) * mm, v(11.24, 10.95) * mm, v(11.27, 10.96) * mm, v(11.32, 10.95) * mm]});
            skFitSpline(sketch, "E350", {"points": [v(11.32, 10.95) * mm, v(11.26, 11.16) * mm, v(11.16, 11.33) * mm, v(11.06, 11.5) * mm]});
            skFitSpline(sketch, "E351", {"points": [v(11.06, 11.5) * mm, v(10.91, 11.7) * mm, v(10.9, 11.9) * mm, v(10.99, 12.14) * mm]});
            skFitSpline(sketch, "E352", {"points": [v(10.99, 12.14) * mm, v(11.09, 12.43) * mm, v(11.1, 12.75) * mm, v(11.17, 13.06) * mm]});
            skFitSpline(sketch, "E353", {"points": [v(11.17, 13.06) * mm, v(11.26, 13.56) * mm, v(11.34, 14.08) * mm, v(11.45, 14.58) * mm]});
            skFitSpline(sketch, "E354", {"points": [v(11.45, 14.58) * mm, v(11.51, 14.88) * mm, v(11.73, 15.02) * mm, v(12, 14.99) * mm]});
            skFitSpline(sketch, "E355", {"points": [v(12, 14.99) * mm, v(12.28, 14.96) * mm, v(12.48, 14.65) * mm, v(12.43, 14.4) * mm]});
            skFitSpline(sketch, "E356", {"points": [v(12.43, 14.4) * mm, v(12.34, 13.98) * mm, v(12.25, 13.57) * mm, v(12.17, 13.15) * mm]});
            skFitSpline(sketch, "E357", {"points": [v(12.17, 13.15) * mm, v(12.1, 12.82) * mm, v(12.05, 12.5) * mm, v(11.99, 12.15) * mm]});
            skFitSpline(sketch, "E358", {"points": [v(11.99, 12.15) * mm, v(12.5, 11.8) * mm, v(13.07, 11.6) * mm, v(13.61, 11.29) * mm]});
            skFitSpline(sketch, "E359", {"points": [v(13.61, 11.29) * mm, v(13.67, 11.55) * mm, v(13.72, 11.78) * mm, v(13.79, 12) * mm]});
            skFitSpline(sketch, "E360", {"points": [v(13.79, 12) * mm, v(13.91, 12.44) * mm, v(14.04, 12.88) * mm, v(14.18, 13.31) * mm]});
            skFitSpline(sketch, "E361", {"points": [v(14.18, 13.31) * mm, v(14.3, 13.7) * mm, v(14.61, 13.83) * mm, v(14.97, 13.64) * mm]});
            skFitSpline(sketch, "E362", {"points": [v(14.97, 13.64) * mm, v(15.48, 13.37) * mm, v(15.98, 13.09) * mm, v(16.48, 12.8) * mm]});
            skFitSpline(sketch, "E363", {"points": [v(16.48, 12.8) * mm, v(16.57, 12.75) * mm, v(16.66, 12.69) * mm, v(16.79, 12.6) * mm]});
            skFitSpline(sketch, "E364", {"points": [v(16.79, 12.6) * mm, v(16.98, 13.2) * mm, v(17.2, 13.75) * mm, v(17.35, 14.34) * mm]});
            skFitSpline(sketch, "E365", {"points": [v(17.35, 14.34) * mm, v(17.27, 14.4) * mm, v(17.2, 14.46) * mm, v(17.12, 14.51) * mm]});
            skFitSpline(sketch, "E366", {"points": [v(17.12, 14.51) * mm, v(16.68, 14.83) * mm, v(16.23, 15.14) * mm, v(15.79, 15.45) * mm]});
            skFitSpline(sketch, "E367", {"points": [v(15.79, 15.45) * mm, v(15.69, 15.51) * mm, v(15.58, 15.57) * mm, v(15.48, 15.63) * mm]});
            skFitSpline(sketch, "E368", {"points": [v(15.48, 15.63) * mm, v(15.27, 15.75) * mm, v(15.2, 15.93) * mm, v(15.23, 16.16) * mm]});
            skFitSpline(sketch, "E369", {"points": [v(15.23, 16.16) * mm, v(15.26, 16.35) * mm, v(15.4, 16.5) * mm, v(15.6, 16.55) * mm]});
            skFitSpline(sketch, "E370", {"points": [v(15.6, 16.55) * mm, v(15.75, 16.6) * mm, v(15.87, 16.55) * mm, v(16, 16.47) * mm]});
            skFitSpline(sketch, "E371", {"points": [v(16, 16.47) * mm, v(16.2, 16.35) * mm, v(16.4, 16.22) * mm, v(16.6, 16.08) * mm]});
            skFitSpline(sketch, "E372", {"points": [v(16.6, 16.08) * mm, v(17.04, 15.77) * mm, v(17.48, 15.45) * mm, v(17.92, 15.14) * mm]});
            skFitSpline(sketch, "E373", {"points": [v(17.92, 15.14) * mm, v(17.98, 15.1) * mm, v(18.04, 15.06) * mm, v(18.11, 15.04) * mm]});
            skFitSpline(sketch, "E374", {"points": [v(18.11, 15.04) * mm, v(18.3, 14.97) * mm, v(18.4, 14.83) * mm, v(18.45, 14.63) * mm]});
            skFitSpline(sketch, "E375", {"points": [v(18.45, 14.63) * mm, v(18.5, 14.42) * mm, v(18.57, 14.2) * mm, v(18.64, 13.94) * mm]});
            skFitSpline(sketch, "E376", {"points": [v(18.64, 13.94) * mm, v(18.7, 14.03) * mm, v(18.72, 14.07) * mm, v(18.74, 14.12) * mm]});
            skFitSpline(sketch, "E377", {"points": [v(18.74, 14.12) * mm, v(19.03, 14.75) * mm, v(19.31, 15.38) * mm, v(19.6, 16.01) * mm]});
            skFitSpline(sketch, "E378", {"points": [v(19.6, 16.01) * mm, v(19.66, 16.13) * mm, v(19.66, 16.23) * mm, v(19.6, 16.35) * mm]});
            skFitSpline(sketch, "E379", {"points": [v(19.6, 16.35) * mm, v(19.26, 17.03) * mm, v(18.92, 17.7) * mm, v(18.57, 18.38) * mm]});
            skFitSpline(sketch, "E380", {"points": [v(18.57, 18.38) * mm, v(18.33, 18.87) * mm, v(18.08, 19.35) * mm, v(17.84, 19.83) * mm]});
            skFitSpline(sketch, "E381", {"points": [v(17.84, 19.83) * mm, v(17.76, 19.98) * mm, v(17.71, 20.12) * mm, v(17.77, 20.3) * mm]});
            skFitSpline(sketch, "E382", {"points": [v(17.77, 20.3) * mm, v(17.84, 20.5) * mm, v(17.97, 20.6) * mm, v(18.16, 20.64) * mm]});
            skFitSpline(sketch, "E383", {"points": [v(18.16, 20.64) * mm, v(18.35, 20.67) * mm, v(18.5, 20.58) * mm, v(18.62, 20.43) * mm]});
            skFitSpline(sketch, "E384", {"points": [v(18.62, 20.43) * mm, v(18.66, 20.38) * mm, v(18.69, 20.3) * mm, v(18.72, 20.24) * mm]});
            skFitSpline(sketch, "E385", {"points": [v(18.72, 20.24) * mm, v(19.19, 19.32) * mm, v(19.65, 18.4) * mm, v(20.12, 17.49) * mm]});
            skFitSpline(sketch, "E386", {"points": [v(20.12, 17.49) * mm, v(20.15, 17.44) * mm, v(20.18, 17.4) * mm, v(20.22, 17.32) * mm]});
            skFitSpline(sketch, "E387", {"points": [v(20.22, 17.32) * mm, v(20.28, 17.43) * mm, v(20.33, 17.51) * mm, v(20.37, 17.6) * mm]});
            skFitSpline(sketch, "E388", {"points": [v(20.37, 17.6) * mm, v(20.83, 18.5) * mm, v(21.28, 19.4) * mm, v(21.74, 20.31) * mm]});
            skFitSpline(sketch, "E389", {"points": [v(21.74, 20.31) * mm, v(21.9, 20.62) * mm, v(22.17, 20.72) * mm, v(22.43, 20.58) * mm]});
            skFitSpline(sketch, "E390", {"points": [v(22.43, 20.58) * mm, v(22.66, 20.46) * mm, v(22.75, 20.2) * mm, v(22.64, 19.94) * mm]});
            skFitSpline(sketch, "E391", {"points": [v(22.64, 19.94) * mm, v(22.57, 19.75) * mm, v(22.47, 19.58) * mm, v(22.38, 19.4) * mm]});
            skFitSpline(sketch, "E392", {"points": [v(22.38, 19.4) * mm, v(21.88, 18.41) * mm, v(21.38, 17.42) * mm, v(20.87, 16.43) * mm]});
            skFitSpline(sketch, "E393", {"points": [v(20.87, 16.43) * mm, v(20.77, 16.25) * mm, v(20.78, 16.1) * mm, v(20.87, 15.92) * mm]});
            skFitSpline(sketch, "E394", {"points": [v(20.87, 15.92) * mm, v(21.14, 15.36) * mm, v(21.39, 14.8) * mm, v(21.64, 14.22) * mm]});
            skFitSpline(sketch, "E395", {"points": [v(21.64, 14.22) * mm, v(21.68, 14.15) * mm, v(21.72, 14.07) * mm, v(21.8, 14) * mm]});
            skFitSpline(sketch, "E396", {"points": [v(21.8, 14) * mm, v(21.86, 14.2) * mm, v(21.94, 14.42) * mm, v(22, 14.64) * mm]});
            skFitSpline(sketch, "E397", {"points": [v(22, 14.64) * mm, v(22.04, 14.84) * mm, v(22.14, 14.97) * mm, v(22.33, 15.04) * mm]});
            skFitSpline(sketch, "E398", {"points": [v(22.33, 15.04) * mm, v(22.38, 15.06) * mm, v(22.44, 15.09) * mm, v(22.48, 15.12) * mm]});
            skFitSpline(sketch, "E399", {"points": [v(22.48, 15.12) * mm, v(22.92, 15.43) * mm, v(23.35, 15.74) * mm, v(23.8, 16.05) * mm]});
            skFitSpline(sketch, "E400", {"points": [v(23.8, 16.05) * mm, v(24, 16.2) * mm, v(24.23, 16.34) * mm, v(24.45, 16.48) * mm]});
            skFitSpline(sketch, "E401", {"points": [v(24.45, 16.48) * mm, v(24.72, 16.64) * mm, v(25.02, 16.56) * mm, v(25.15, 16.3) * mm]});
            skFitSpline(sketch, "E402", {"points": [v(25.15, 16.3) * mm, v(25.29, 16.05) * mm, v(25.19, 15.76) * mm, v(24.93, 15.61) * mm]});
            skFitSpline(sketch, "E403", {"points": [v(24.93, 15.61) * mm, v(24.7, 15.48) * mm, v(24.48, 15.33) * mm, v(24.27, 15.18) * mm]});
            skFitSpline(sketch, "E404", {"points": [v(24.27, 15.18) * mm, v(24, 15) * mm, v(23.74, 14.82) * mm, v(23.48, 14.63) * mm]});
            skFitSpline(sketch, "E405", {"points": [v(23.48, 14.63) * mm, v(23.36, 14.55) * mm, v(23.23, 14.46) * mm, v(23.1, 14.36) * mm]});
            skFitSpline(sketch, "E406", {"points": [v(23.1, 14.36) * mm, v(23.22, 13.76) * mm, v(23.46, 13.2) * mm, v(23.64, 12.6) * mm]});
            skFitSpline(sketch, "E407", {"points": [v(23.64, 12.6) * mm, v(23.88, 12.76) * mm, v(24.1, 12.9) * mm, v(24.33, 13.04) * mm]});
            skFitSpline(sketch, "E408", {"points": [v(24.33, 13.04) * mm, v(24.72, 13.25) * mm, v(25.1, 13.46) * mm, v(25.5, 13.66) * mm]});
            skFitSpline(sketch, "E409", {"points": [v(25.5, 13.66) * mm, v(25.82, 13.82) * mm, v(26.13, 13.68) * mm, v(26.26, 13.33) * mm]});
            skFitSpline(sketch, "E410", {"points": [v(26.26, 13.33) * mm, v(26.48, 12.74) * mm, v(26.63, 12.14) * mm, v(26.76, 11.53) * mm]});
            skFitSpline(sketch, "E411", {"points": [v(26.76, 11.53) * mm, v(26.77, 11.46) * mm, v(26.8, 11.4) * mm, v(26.82, 11.3) * mm]});
            skFitSpline(sketch, "E412", {"points": [v(26.82, 11.3) * mm, v(27.36, 11.57) * mm, v(27.9, 11.84) * mm, v(28.44, 12.1) * mm]});
            skFitSpline(sketch, "E413", {"points": [v(28.44, 12.1) * mm, v(28.41, 12.27) * mm, v(28.4, 12.42) * mm, v(28.37, 12.57) * mm]});
            skFitSpline(sketch, "E414", {"points": [v(28.37, 12.57) * mm, v(28.29, 13.06) * mm, v(28.2, 13.54) * mm, v(28.1, 14.03) * mm]});
            skFitSpline(sketch, "E415", {"points": [v(28.1, 14.03) * mm, v(28.09, 14.13) * mm, v(28.06, 14.23) * mm, v(28.03, 14.33) * mm]});
            skFitSpline(sketch, "E416", {"points": [v(28.03, 14.33) * mm, v(27.95, 14.6) * mm, v(28.08, 14.88) * mm, v(28.34, 14.97) * mm]});
            skFitSpline(sketch, "E417", {"points": [v(28.34, 14.97) * mm, v(28.6, 15.06) * mm, v(28.88, 14.93) * mm, v(28.96, 14.64) * mm]});
            skFitSpline(sketch, "E418", {"points": [v(28.96, 14.64) * mm, v(29.04, 14.36) * mm, v(29.1, 14.07) * mm, v(29.14, 13.78) * mm]});
            skFitSpline(sketch, "E419", {"points": [v(29.14, 13.78) * mm, v(29.24, 13.26) * mm, v(29.32, 12.74) * mm, v(29.41, 12.22) * mm]});
            skFitSpline(sketch, "E420", {"points": [v(29.41, 12.22) * mm, v(29.41, 12.22) * mm, v(29.42, 12.2) * mm, v(29.42, 12.2) * mm]});
            skFitSpline(sketch, "E421", {"points": [v(29.42, 12.2) * mm, v(29.58, 11.92) * mm, v(29.52, 11.67) * mm, v(29.34, 11.42) * mm]});
            skFitSpline(sketch, "E422", {"points": [v(29.34, 11.42) * mm, v(29.24, 11.29) * mm, v(29.18, 11.12) * mm, v(29.07, 10.92) * mm]});
            skFitSpline(sketch, "E423", {"points": [v(29.07, 10.92) * mm, v(29.2, 10.96) * mm, v(29.26, 10.98) * mm, v(29.33, 11) * mm]});
            skFitSpline(sketch, "E424", {"points": [v(29.33, 11) * mm, v(29.94, 11.24) * mm, v(30.55, 11.47) * mm, v(31.17, 11.7) * mm]});
            skFitSpline(sketch, "E425", {"points": [v(31.17, 11.7) * mm, v(31.32, 11.75) * mm, v(31.41, 11.83) * mm, v(31.47, 12) * mm]});
            skFitSpline(sketch, "E426", {"points": [v(31.47, 12) * mm, v(31.7, 12.73) * mm, v(31.94, 13.47) * mm, v(32.18, 14.2) * mm]});
            skFitSpline(sketch, "E427", {"points": [v(32.18, 14.2) * mm, v(32.34, 14.68) * mm, v(32.5, 15.16) * mm, v(32.65, 15.64) * mm]});
            skFitSpline(sketch, "E428", {"points": [v(32.65, 15.64) * mm, v(32.68, 15.72) * mm, v(32.71, 15.8) * mm, v(32.76, 15.87) * mm]});
            skFitSpline(sketch, "E429", {"points": [v(32.76, 15.87) * mm, v(32.9, 16.07) * mm, v(33.14, 16.15) * mm, v(33.35, 16.06) * mm]});
            skFitSpline(sketch, "E430", {"points": [v(33.35, 16.06) * mm, v(33.58, 15.96) * mm, v(33.7, 15.73) * mm, v(33.63, 15.49) * mm]});
            skFitSpline(sketch, "E431", {"points": [v(33.63, 15.49) * mm, v(33.5, 15.04) * mm, v(33.35, 14.59) * mm, v(33.2, 14.14) * mm]});
            skFitSpline(sketch, "E432", {"points": [v(33.2, 14.14) * mm, v(33, 13.53) * mm, v(32.8, 12.93) * mm, v(32.6, 12.32) * mm]});
            skFitSpline(sketch, "E433", {"points": [v(32.6, 12.32) * mm, v(32.6, 12.3) * mm, v(32.59, 12.26) * mm, v(32.57, 12.2) * mm]});
            skFitSpline(sketch, "E434", {"points": [v(32.57, 12.2) * mm, v(32.67, 12.23) * mm, v(32.75, 12.25) * mm, v(32.82, 12.27) * mm]});
            skFitSpline(sketch, "E435", {"points": [v(32.82, 12.27) * mm, v(33.8, 12.6) * mm, v(34.78, 12.91) * mm, v(35.75, 13.24) * mm]});
            skFitSpline(sketch, "E436", {"points": [v(35.75, 13.24) * mm, v(35.9, 13.29) * mm, v(36.05, 13.3) * mm, v(36.2, 13.23) * mm]});
            skFitSpline(sketch, "E437", {"points": [v(36.2, 13.23) * mm, v(36.52, 13.07) * mm, v(36.55, 12.6) * mm, v(36.24, 12.4) * mm]});
            skFitSpline(sketch, "E438", {"points": [v(36.24, 12.4) * mm, v(36.14, 12.33) * mm, v(36.02, 12.3) * mm, v(35.91, 12.26) * mm]});
            skFitSpline(sketch, "E439", {"points": [v(35.91, 12.26) * mm, v(34.74, 11.87) * mm, v(33.58, 11.49) * mm, v(32.4, 11.12) * mm]});
            skFitSpline(sketch, "E440", {"points": [v(32.4, 11.12) * mm, v(32.2, 11.05) * mm, v(32.11, 10.95) * mm, v(32.04, 10.76) * mm]});
            skFitSpline(sketch, "E441", {"points": [v(32.04, 10.76) * mm, v(31.83, 10.16) * mm, v(31.6, 9.57) * mm, v(31.38, 8.98) * mm]});
            skFitSpline(sketch, "E442", {"points": [v(31.38, 8.98) * mm, v(31.35, 8.91) * mm, v(31.33, 8.84) * mm, v(31.34, 8.74) * mm]});
            skFitSpline(sketch, "E443", {"points": [v(31.34, 8.74) * mm, v(31.53, 8.84) * mm, v(31.72, 8.93) * mm, v(31.9, 9.04) * mm]});
            skFitSpline(sketch, "E444", {"points": [v(31.9, 9.04) * mm, v(32.08, 9.16) * mm, v(32.26, 9.18) * mm, v(32.47, 9.1) * mm]});
            skFitSpline(sketch, "E445", {"points": [v(32.47, 9.1) * mm, v(32.6, 9.04) * mm, v(32.76, 9.02) * mm, v(32.9, 9) * mm]});
            skFitSpline(sketch, "E446", {"points": [v(32.9, 9) * mm, v(33.54, 8.88) * mm, v(34.18, 8.77) * mm, v(34.82, 8.65) * mm]});
            skFitSpline(sketch, "E447", {"points": [v(34.82, 8.65) * mm, v(34.88, 8.64) * mm, v(34.94, 8.63) * mm, v(35, 8.6) * mm]});
            skFitSpline(sketch, "E448", {"points": [v(35, 8.6) * mm, v(35.31, 8.5) * mm, v(35.4, 8.27) * mm, v(35.33, 7.98) * mm]});
            skFitSpline(sketch, "E449", {"points": [v(35.33, 7.98) * mm, v(35.27, 7.73) * mm, v(34.95, 7.58) * mm, v(34.7, 7.65) * mm]});
            skFitSpline(sketch, "E450", {"points": [v(34.7, 7.65) * mm, v(34.37, 7.75) * mm, v(34.03, 7.8) * mm, v(33.7, 7.86) * mm]});
            skFitSpline(sketch, "E451", {"points": [v(33.7, 7.86) * mm, v(33.3, 7.94) * mm, v(32.91, 8) * mm, v(32.5, 8.08) * mm]});
            skFitSpline(sketch, "E452", {"points": [v(32.5, 8.08) * mm, v(32.18, 7.57) * mm, v(31.97, 7) * mm, v(31.65, 6.46) * mm]});
            skFitSpline(sketch, "E453", {"points": [v(31.65, 6.46) * mm, v(31.74, 6.44) * mm, v(31.8, 6.42) * mm, v(31.87, 6.4) * mm]});
            skFitSpline(sketch, "E454", {"points": [v(31.87, 6.4) * mm, v(32.49, 6.27) * mm, v(33.1, 6.1) * mm, v(33.7, 5.9) * mm]});
            skFitSpline(sketch, "E455", {"points": [v(33.7, 5.9) * mm, v(34.03, 5.78) * mm, v(34.18, 5.4) * mm, v(34.02, 5.1) * mm]});
            skFitSpline(sketch, "E456", {"points": [v(34.02, 5.1) * mm, v(33.73, 4.6) * mm, v(33.45, 4.1) * mm, v(33.17, 3.58) * mm]});
            skFitSpline(sketch, "E457", {"points": [v(33.17, 3.58) * mm, v(33.11, 3.49) * mm, v(33.05, 3.4) * mm, v(32.97, 3.27) * mm]});
            skFitSpline(sketch, "E458", {"points": [v(32.97, 3.27) * mm, v(33.57, 3.1) * mm, v(34.12, 2.86) * mm, v(34.71, 2.72) * mm]});
            skFitSpline(sketch, "E459", {"points": [v(34.71, 2.72) * mm, v(34.78, 2.81) * mm, v(34.83, 2.88) * mm, v(34.88, 2.95) * mm]});
            skFitSpline(sketch, "E460", {"points": [v(34.88, 2.95) * mm, v(35.2, 3.4) * mm, v(35.5, 3.84) * mm, v(35.82, 4.29) * mm]});
            skFitSpline(sketch, "E461", {"points": [v(35.82, 4.29) * mm, v(35.88, 4.38) * mm, v(35.93, 4.48) * mm, v(35.98, 4.58) * mm]});
            skFitSpline(sketch, "E462", {"points": [v(35.98, 4.58) * mm, v(36.12, 4.82) * mm, v(36.42, 4.91) * mm, v(36.67, 4.79) * mm]});
            skFitSpline(sketch, "E463", {"points": [v(36.67, 4.79) * mm, v(36.91, 4.66) * mm, v(37, 4.37) * mm, v(36.86, 4.11) * mm]});
            skFitSpline(sketch, "E464", {"points": [v(36.86, 4.11) * mm, v(36.74, 3.9) * mm, v(36.6, 3.69) * mm, v(36.46, 3.49) * mm]});
            skFitSpline(sketch, "E465", {"points": [v(36.46, 3.49) * mm, v(36.15, 3.04) * mm, v(35.83, 2.6) * mm, v(35.51, 2.16) * mm]});
            skFitSpline(sketch, "E466", {"points": [v(35.51, 2.16) * mm, v(35.47, 2.1) * mm, v(35.43, 2.04) * mm, v(35.4, 1.97) * mm]});
            skFitSpline(sketch, "E467", {"points": [v(35.4, 1.97) * mm, v(35.34, 1.77) * mm, v(35.2, 1.67) * mm, v(34.99, 1.62) * mm]});
            skFitSpline(sketch, "E468", {"points": [v(34.99, 1.62) * mm, v(34.78, 1.57) * mm, v(34.57, 1.5) * mm, v(34.3, 1.42) * mm]});
            skFitSpline(sketch, "E469", {"points": [v(34.3, 1.42) * mm, v(34.42, 1.36) * mm, v(34.5, 1.32) * mm, v(34.56, 1.3) * mm]});
            skFitSpline(sketch, "E470", {"points": [v(34.56, 1.3) * mm, v(35.15, 1.02) * mm, v(35.74, 0.77) * mm, v(36.33, 0.49) * mm]});
            skFitSpline(sketch, "E471", {"points": [v(36.33, 0.49) * mm, v(36.49, 0.4) * mm, v(36.61, 0.4) * mm, v(36.77, 0.5) * mm]});
            skFitSpline(sketch, "E472", {"points": [v(36.77, 0.5) * mm, v(37.45, 0.84) * mm, v(38.12, 1.18) * mm, v(38.8, 1.52) * mm]});
            skFitSpline(sketch, "E473", {"points": [v(38.8, 1.52) * mm, v(39.26, 1.75) * mm, v(39.7, 1.99) * mm, v(40.17, 2.22) * mm]});
            skFitSpline(sketch, "E474", {"points": [v(40.17, 2.22) * mm, v(40.24, 2.26) * mm, v(40.33, 2.3) * mm, v(40.41, 2.31) * mm]});
            skFitSpline(sketch, "E475", {"points": [v(40.41, 2.31) * mm, v(40.64, 2.36) * mm, v(40.86, 2.24) * mm, v(40.96, 2.03) * mm]});
            skFitSpline(sketch, "E476", {"points": [v(40.96, 2.03) * mm, v(41.06, 1.82) * mm, v(41, 1.6) * mm, v(40.8, 1.45) * mm]});
            skFitSpline(sketch, "E477", {"points": [v(40.8, 1.45) * mm, v(40.79, 1.44) * mm, v(40.77, 1.42) * mm, v(40.75, 1.41) * mm]});
            skFitSpline(sketch, "E478", {"points": [v(40.75, 1.41) * mm, v(40.31, 1.2) * mm, v(39.88, 0.97) * mm, v(39.44, 0.75) * mm]});
            skFitSpline(sketch, "E479", {"points": [v(39.44, 0.75) * mm, v(38.87, 0.46) * mm, v(38.3, 0.17) * mm, v(37.69, -0.14) * mm]});
            skFitSpline(sketch, "E480", {"points": [v(37.69, -0.14) * mm, v(37.76, -0.19) * mm, v(37.82, -0.23) * mm, v(37.88, -0.26) * mm]});
            skFitSpline(sketch, "E481", {"points": [v(37.88, -0.26) * mm, v(38.8, -0.73) * mm, v(39.73, -1.2) * mm, v(40.65, -1.66) * mm]});
            skFitSpline(sketch, "E482", {"points": [v(40.65, -1.66) * mm, v(40.9, -1.79) * mm, v(41.03, -1.97) * mm, v(41, -2.18) * mm]});
            skFitSpline(sketch, "E483", {"points": [v(41, -2.18) * mm, v(40.97, -2.5) * mm, v(40.66, -2.7) * mm, v(40.35, -2.59) * mm]});
            skFitSpline(sketch, "E484", {"points": [v(40.35, -2.59) * mm, v(40.16, -2.52) * mm, v(39.97, -2.42) * mm, v(39.79, -2.32) * mm]});
            skFitSpline(sketch, "E485", {"points": [v(39.79, -2.32) * mm, v(38.8, -1.82) * mm, v(37.8, -1.31) * mm, v(36.8, -0.8) * mm]});
            skFitSpline(sketch, "E486", {"points": [v(36.8, -0.8) * mm, v(36.62, -0.7) * mm, v(36.47, -0.71) * mm, v(36.29, -0.8) * mm]});
            skFitSpline(sketch, "E487", {"points": [v(36.29, -0.8) * mm, v(35.72, -1.07) * mm, v(35.14, -1.32) * mm, v(34.57, -1.58) * mm]});
            skFitSpline(sketch, "E488", {"points": [v(34.57, -1.58) * mm, v(34.5, -1.62) * mm, v(34.43, -1.65) * mm, v(34.3, -1.71) * mm]});
            skFitSpline(sketch, "E489", {"points": [v(34.3, -1.71) * mm, v(34.56, -1.8) * mm, v(34.76, -1.87) * mm, v(34.96, -1.91) * mm]});
            skFitSpline(sketch, "E490", {"points": [v(34.96, -1.91) * mm, v(35.18, -1.96) * mm, v(35.34, -2.06) * mm, v(35.42, -2.29) * mm]});
            skFitSpline(sketch, "E491", {"points": [v(35.42, -2.29) * mm, v(35.43, -2.33) * mm, v(35.46, -2.37) * mm, v(35.48, -2.41) * mm]});
            skFitSpline(sketch, "E492", {"points": [v(35.48, -2.41) * mm, v(35.8, -2.85) * mm, v(36.1, -3.28) * mm, v(36.41, -3.72) * mm]});
            skFitSpline(sketch, "E493", {"points": [v(36.41, -3.72) * mm, v(36.56, -3.94) * mm, v(36.7, -4.16) * mm, v(36.84, -4.38) * mm]});
            skFitSpline(sketch, "E494", {"points": [v(36.84, -4.38) * mm, v(37, -4.66) * mm, v(36.93, -4.95) * mm, v(36.67, -5.08) * mm]});
            skFitSpline(sketch, "E495", {"points": [v(36.67, -5.08) * mm, v(36.42, -5.22) * mm, v(36.13, -5.1) * mm, v(35.97, -4.86) * mm]});
            skFitSpline(sketch, "E496", {"points": [v(35.97, -4.86) * mm, v(35.57, -4.24) * mm, v(35.15, -3.64) * mm, v(34.74, -3.02) * mm]});
            skFitSpline(sketch, "E497", {"points": [v(34.74, -3.02) * mm, v(34.12, -3.15) * mm, v(33.57, -3.4) * mm, v(32.97, -3.56) * mm]});
            skFitSpline(sketch, "E498", {"points": [v(32.97, -3.56) * mm, v(33.12, -3.81) * mm, v(33.27, -4.03) * mm, v(33.39, -4.25) * mm]});
            skFitSpline(sketch, "E499", {"points": [v(33.39, -4.25) * mm, v(33.6, -4.63) * mm, v(33.8, -5.02) * mm, v(34.02, -5.4) * mm]});
            skFitSpline(sketch, "E500", {"points": [v(34.02, -5.4) * mm, v(34.17, -5.67) * mm, v(34.06, -6.07) * mm, v(33.7, -6.2) * mm]});
            skFitSpline(sketch, "E501", {"points": [v(33.7, -6.2) * mm, v(33.1, -6.4) * mm, v(32.5, -6.56) * mm, v(31.9, -6.7) * mm]});
            skFitSpline(sketch, "E502", {"points": [v(31.9, -6.7) * mm, v(31.83, -6.7) * mm, v(31.76, -6.73) * mm, v(31.66, -6.75) * mm]});
            skFitSpline(sketch, "E503", {"points": [v(31.66, -6.75) * mm, v(31.94, -7.3) * mm, v(32.21, -7.84) * mm, v(32.49, -8.38) * mm]});
            skFitSpline(sketch, "E504", {"points": [v(32.49, -8.38) * mm, v(32.9, -8.3) * mm, v(33.27, -8.24) * mm, v(33.65, -8.17) * mm]});
            skFitSpline(sketch, "E505", {"points": [v(33.65, -8.17) * mm, v(34.01, -8.1) * mm, v(34.38, -8.02) * mm, v(34.74, -7.94) * mm]});
            skFitSpline(sketch, "E506", {"points": [v(34.74, -7.94) * mm, v(34.98, -7.9) * mm, v(35.26, -8.03) * mm, v(35.33, -8.26) * mm]});
            skFitSpline(sketch, "E507", {"points": [v(35.33, -8.26) * mm, v(35.4, -8.5) * mm, v(35.36, -8.74) * mm, v(35.07, -8.88) * mm]});
            skFitSpline(sketch, "E508", {"points": [v(35.07, -8.88) * mm, v(34.94, -8.93) * mm, v(34.8, -8.97) * mm, v(34.65, -9) * mm]});
            skFitSpline(sketch, "E509", {"points": [v(34.65, -9) * mm, v(34.02, -9.1) * mm, v(33.38, -9.2) * mm, v(32.74, -9.32) * mm]});
            skFitSpline(sketch, "E510", {"points": [v(32.74, -9.32) * mm, v(32.64, -9.34) * mm, v(32.54, -9.36) * mm, v(32.45, -9.4) * mm]});
            skFitSpline(sketch, "E511", {"points": [v(32.45, -9.4) * mm, v(32.26, -9.49) * mm, v(32.1, -9.45) * mm, v(31.92, -9.35) * mm]});
            skFitSpline(sketch, "E512", {"points": [v(31.92, -9.35) * mm, v(31.74, -9.24) * mm, v(31.54, -9.14) * mm, v(31.3, -9) * mm]});
            skFitSpline(sketch, "E513", {"points": [v(31.3, -9) * mm, v(31.33, -9.12) * mm, v(31.34, -9.17) * mm, v(31.36, -9.23) * mm]});
            skFitSpline(sketch, "E514", {"points": [v(31.36, -9.23) * mm, v(31.6, -9.87) * mm, v(31.84, -10.5) * mm, v(32.07, -11.14) * mm]});
            skFitSpline(sketch, "E515", {"points": [v(32.07, -11.14) * mm, v(32.12, -11.27) * mm, v(32.2, -11.35) * mm, v(32.33, -11.39) * mm]});
            skFitSpline(sketch, "E516", {"points": [v(32.33, -11.39) * mm, v(33.04, -11.62) * mm, v(33.76, -11.85) * mm, v(34.47, -12.09) * mm]});
            skFitSpline(sketch, "E517", {"points": [v(34.47, -12.09) * mm, v(35, -12.26) * mm, v(35.52, -12.42) * mm, v(36.04, -12.6) * mm]});
            skFitSpline(sketch, "E518", {"points": [v(36.04, -12.6) * mm, v(36.33, -12.7) * mm, v(36.46, -12.87) * mm, v(36.45, -13.12) * mm]});
            skFitSpline(sketch, "E519", {"points": [v(36.45, -13.12) * mm, v(36.45, -13.38) * mm, v(36.24, -13.58) * mm, v(35.97, -13.58) * mm]});
            skFitSpline(sketch, "E520", {"points": [v(35.97, -13.58) * mm, v(35.92, -13.58) * mm, v(35.86, -13.57) * mm, v(35.8, -13.55) * mm]});
            skFitSpline(sketch, "E521", {"points": [v(35.8, -13.55) * mm, v(35.34, -13.4) * mm, v(34.88, -13.25) * mm, v(34.42, -13.1) * mm]});
            skFitSpline(sketch, "E522", {"points": [v(34.42, -13.1) * mm, v(33.83, -12.9) * mm, v(33.24, -12.71) * mm, v(32.65, -12.52) * mm]});
            skFitSpline(sketch, "E523", {"points": [v(32.65, -12.52) * mm, v(32.63, -12.51) * mm, v(32.62, -12.52) * mm, v(32.58, -12.53) * mm]});
            skFitSpline(sketch, "E524", {"points": [v(32.58, -12.53) * mm, v(32.6, -12.6) * mm, v(32.62, -12.68) * mm, v(32.64, -12.75) * mm]});
            skFitSpline(sketch, "E525", {"points": [v(32.64, -12.75) * mm, v(32.96, -13.73) * mm, v(33.28, -14.7) * mm, v(33.6, -15.68) * mm]});
            skFitSpline(sketch, "E526", {"points": [v(33.6, -15.68) * mm, v(33.63, -15.78) * mm, v(33.65, -15.89) * mm, v(33.64, -15.99) * mm]});
            skFitSpline(sketch, "E527", {"points": [v(33.64, -15.99) * mm, v(33.61, -16.19) * mm, v(33.49, -16.32) * mm, v(33.3, -16.38) * mm]});
            skFitSpline(sketch, "E528", {"points": [v(33.3, -16.38) * mm, v(33.1, -16.43) * mm, v(32.88, -16.35) * mm, v(32.77, -16.18) * mm]});
            skFitSpline(sketch, "E529", {"points": [v(32.77, -16.18) * mm, v(32.7, -16.08) * mm, v(32.67, -15.98) * mm, v(32.63, -15.87) * mm]});
            skFitSpline(sketch, "E530", {"points": [v(32.63, -15.87) * mm, v(32.26, -14.74) * mm, v(31.89, -13.6) * mm, v(31.52, -12.46) * mm]});
            skFitSpline(sketch, "E531", {"points": [v(31.52, -12.46) * mm, v(31.5, -12.38) * mm, v(31.46, -12.3) * mm, v(31.44, -12.23) * mm]});
            skFitSpline(sketch, "E532", {"points": [v(31.44, -12.23) * mm, v(31.41, -12.1) * mm, v(31.33, -12.05) * mm, v(31.22, -12.01) * mm]});
            skFitSpline(sketch, "E533", {"points": [v(31.22, -12.01) * mm, v(30.57, -11.77) * mm, v(29.92, -11.52) * mm, v(29.27, -11.28) * mm]});
            skFitSpline(sketch, "E534", {"points": [v(29.27, -11.28) * mm, v(29.22, -11.26) * mm, v(29.18, -11.25) * mm, v(29.1, -11.23) * mm]});
            skFitSpline(sketch, "E535", {"points": [v(29.1, -11.23) * mm, v(29.18, -11.46) * mm, v(29.28, -11.64) * mm, v(29.4, -11.82) * mm]});
            skFitSpline(sketch, "E536", {"points": [v(29.4, -11.82) * mm, v(29.52, -12) * mm, v(29.54, -12.18) * mm, v(29.46, -12.4) * mm]});
            skFitSpline(sketch, "E537", {"points": [v(29.46, -12.4) * mm, v(29.37, -12.66) * mm, v(29.35, -12.93) * mm, v(29.3, -13.2) * mm]});
            skFitSpline(sketch, "E538", {"points": [v(29.3, -13.2) * mm, v(29.2, -13.73) * mm, v(29.1, -14.27) * mm, v(29, -14.8) * mm]});
            skFitSpline(sketch, "E539", {"points": [v(29, -14.8) * mm, v(29, -14.87) * mm, v(28.97, -14.94) * mm, v(28.95, -15) * mm]});
            skFitSpline(sketch, "E540", {"points": [v(28.95, -15) * mm, v(28.84, -15.23) * mm, v(28.58, -15.35) * mm, v(28.34, -15.27) * mm]});
            skFitSpline(sketch, "E541", {"points": [v(28.34, -15.27) * mm, v(28.12, -15.2) * mm, v(27.93, -14.92) * mm, v(28, -14.7) * mm]});
            skFitSpline(sketch, "E542", {"points": [v(28, -14.7) * mm, v(28.18, -14.23) * mm, v(28.2, -13.73) * mm, v(28.3, -13.25) * mm]});
            skFitSpline(sketch, "E543", {"points": [v(28.3, -13.25) * mm, v(28.35, -12.98) * mm, v(28.4, -12.72) * mm, v(28.44, -12.44) * mm]});
            skFitSpline(sketch, "E544", {"points": [v(28.44, -12.44) * mm, v(27.93, -12.1) * mm, v(27.37, -11.9) * mm, v(26.83, -11.59) * mm]});
            skFitSpline(sketch, "E545", {"points": [v(26.83, -11.59) * mm, v(26.8, -11.68) * mm, v(26.77, -11.75) * mm, v(26.76, -11.82) * mm]});
            skFitSpline(sketch, "E546", {"points": [v(26.76, -11.82) * mm, v(26.63, -12.43) * mm, v(26.48, -13.04) * mm, v(26.26, -13.62) * mm]});
            skFitSpline(sketch, "E547", {"points": [v(26.26, -13.62) * mm, v(26.13, -13.98) * mm, v(25.82, -14.12) * mm, v(25.48, -13.95) * mm]});
            skFitSpline(sketch, "E548", {"points": [v(25.48, -13.95) * mm, v(24.96, -13.67) * mm, v(24.46, -13.38) * mm, v(23.95, -13.1) * mm]});
            skFitSpline(sketch, "E549", {"points": [v(23.95, -13.1) * mm, v(23.85, -13.05) * mm, v(23.76, -12.98) * mm, v(23.64, -12.9) * mm]});
            skFitSpline(sketch, "E550", {"points": [v(23.64, -12.9) * mm, v(23.46, -13.5) * mm, v(23.23, -14.06) * mm, v(23.09, -14.64) * mm]});
            skFitSpline(sketch, "E551", {"points": [v(23.09, -14.64) * mm, v(23.18, -14.71) * mm, v(23.25, -14.77) * mm, v(23.32, -14.82) * mm]});
            skFitSpline(sketch, "E552", {"points": [v(23.32, -14.82) * mm, v(23.76, -15.13) * mm, v(24.2, -15.44) * mm, v(24.65, -15.75) * mm]});
            skFitSpline(sketch, "E553", {"points": [v(24.65, -15.75) * mm, v(24.75, -15.82) * mm, v(24.86, -15.87) * mm, v(24.96, -15.93) * mm]});
            skFitSpline(sketch, "E554", {"points": [v(24.96, -15.93) * mm, v(25.15, -16.05) * mm, v(25.23, -16.22) * mm, v(25.2, -16.44) * mm]});
            skFitSpline(sketch, "E555", {"points": [v(25.2, -16.44) * mm, v(25.18, -16.65) * mm, v(25.05, -16.78) * mm, v(24.85, -16.85) * mm]});
            skFitSpline(sketch, "E556", {"points": [v(24.85, -16.85) * mm, v(24.7, -16.9) * mm, v(24.56, -16.85) * mm, v(24.44, -16.77) * mm]});
            skFitSpline(sketch, "E557", {"points": [v(24.44, -16.77) * mm, v(24.24, -16.65) * mm, v(24.04, -16.52) * mm, v(23.85, -16.4) * mm]});
            skFitSpline(sketch, "E558", {"points": [v(23.85, -16.4) * mm, v(23.4, -16.08) * mm, v(22.97, -15.76) * mm, v(22.53, -15.45) * mm]});
            skFitSpline(sketch, "E559", {"points": [v(22.53, -15.45) * mm, v(22.45, -15.4) * mm, v(22.37, -15.36) * mm, v(22.3, -15.33) * mm]});
            skFitSpline(sketch, "E560", {"points": [v(22.3, -15.33) * mm, v(22.14, -15.25) * mm, v(22.04, -15.14) * mm, v(22, -14.97) * mm]});
            skFitSpline(sketch, "E561", {"points": [v(22, -14.97) * mm, v(21.94, -14.74) * mm, v(21.87, -14.52) * mm, v(21.79, -14.24) * mm]});
            skFitSpline(sketch, "E562", {"points": [v(21.79, -14.24) * mm, v(21.73, -14.35) * mm, v(21.7, -14.4) * mm, v(21.67, -14.47) * mm]});
            skFitSpline(sketch, "E563", {"points": [v(21.67, -14.47) * mm, v(21.39, -15.08) * mm, v(21.12, -15.7) * mm, v(20.83, -16.3) * mm]});
            skFitSpline(sketch, "E564", {"points": [v(20.83, -16.3) * mm, v(20.77, -16.43) * mm, v(20.77, -16.53) * mm, v(20.84, -16.66) * mm]});
            skFitSpline(sketch, "E565", {"points": [v(20.84, -16.66) * mm, v(21.19, -17.34) * mm, v(21.53, -18.03) * mm, v(21.87, -18.7) * mm]});
            skFitSpline(sketch, "E566", {"points": [v(21.87, -18.7) * mm, v(22.11, -19.18) * mm, v(22.36, -19.65) * mm, v(22.59, -20.12) * mm]});
            skFitSpline(sketch, "E567", {"points": [v(22.59, -20.12) * mm, v(22.64, -20.22) * mm, v(22.67, -20.35) * mm, v(22.68, -20.46) * mm]});
            skFitSpline(sketch, "E568", {"points": [v(22.68, -20.46) * mm, v(22.69, -20.68) * mm, v(22.56, -20.83) * mm, v(22.35, -20.91) * mm]});
            skFitSpline(sketch, "E569", {"points": [v(22.35, -20.91) * mm, v(22.17, -20.98) * mm, v(21.97, -20.92) * mm, v(21.83, -20.76) * mm]});
            skFitSpline(sketch, "E570", {"points": [v(21.83, -20.76) * mm, v(21.81, -20.73) * mm, v(21.8, -20.7) * mm, v(21.78, -20.68) * mm]});
            skFitSpline(sketch, "E571", {"points": [v(21.78, -20.68) * mm, v(21.56, -20.25) * mm, v(21.34, -19.83) * mm, v(21.13, -19.4) * mm]});
            skFitSpline(sketch, "E572", {"points": [v(21.13, -19.4) * mm, v(20.84, -18.83) * mm, v(20.55, -18.26) * mm, v(20.26, -17.69) * mm]});
            skFitSpline(sketch, "E573", {"points": [v(20.26, -17.69) * mm, v(20.25, -17.68) * mm, v(20.24, -17.67) * mm, v(20.2, -17.65) * mm]});
            skFitSpline(sketch, "E574", {"points": [v(20.2, -17.65) * mm, v(20.17, -17.71) * mm, v(20.13, -17.77) * mm, v(20.1, -17.84) * mm]});
            skFitSpline(sketch, "E575", {"points": [v(20.1, -17.84) * mm, v(19.63, -18.76) * mm, v(19.16, -19.68) * mm, v(18.7, -20.6) * mm]});
            skFitSpline(sketch, "E576", {"points": [v(18.7, -20.6) * mm, v(18.54, -20.9) * mm, v(18.28, -21.02) * mm, v(18.01, -20.88) * mm]});
            skFitSpline(sketch, "E577", {"points": [v(18.01, -20.88) * mm, v(17.8, -20.78) * mm, v(17.7, -20.54) * mm, v(17.77, -20.32) * mm]});
            skFitSpline(sketch, "E578", {"points": [v(17.77, -20.32) * mm, v(17.84, -20.11) * mm, v(17.95, -19.91) * mm, v(18.05, -19.71) * mm]});
            skFitSpline(sketch, "E579", {"points": [v(18.05, -19.71) * mm, v(18.55, -18.72) * mm, v(19.05, -17.73) * mm, v(19.56, -16.74) * mm]});
            skFitSpline(sketch, "E580", {"points": [v(19.56, -16.74) * mm, v(19.66, -16.55) * mm, v(19.65, -16.4) * mm, v(19.56, -16.2) * mm]});
            skFitSpline(sketch, "E581", {"points": [v(19.56, -16.2) * mm, v(19.29, -15.65) * mm, v(19.04, -15.08) * mm, v(18.78, -14.5) * mm]});
            skFitSpline(sketch, "E582", {"points": [v(18.78, -14.5) * mm, v(18.75, -14.44) * mm, v(18.72, -14.36) * mm, v(18.67, -14.26) * mm]});
            skFitSpline(sketch, "E583", {"points": [v(18.67, -14.26) * mm, v(18.55, -14.47) * mm, v(18.5, -14.67) * mm, v(18.46, -14.88) * mm]});
            skFitSpline(sketch, "E584", {"points": [v(18.46, -14.88) * mm, v(18.4, -15.1) * mm, v(18.31, -15.28) * mm, v(18.07, -15.35) * mm]});
            skFitSpline(sketch, "E585", {"points": [v(18.07, -15.35) * mm, v(18.04, -15.36) * mm, v(18, -15.38) * mm, v(17.97, -15.4) * mm]});
            skFitSpline(sketch, "E586", {"points": [v(17.97, -15.4) * mm, v(17.55, -15.7) * mm, v(17.13, -16) * mm, v(16.71, -16.29) * mm]});
            skFitSpline(sketch, "E587", {"points": [v(16.71, -16.29) * mm, v(16.48, -16.45) * mm, v(16.24, -16.62) * mm, v(16, -16.77) * mm]});
            skFitSpline(sketch, "E588", {"points": [v(16, -16.77) * mm, v(15.71, -16.94) * mm, v(15.42, -16.86) * mm, v(15.28, -16.6) * mm]});
            skFitSpline(sketch, "E589", {"points": [v(15.28, -16.6) * mm, v(15.14, -16.33) * mm, v(15.25, -16.05) * mm, v(15.53, -15.9) * mm]});
            skFitSpline(sketch, "E590", {"points": [v(15.53, -15.9) * mm, v(15.66, -15.83) * mm, v(15.78, -15.75) * mm, v(15.9, -15.67) * mm]});
            skFitSpline(sketch, "E591", {"points": [v(15.9, -15.67) * mm, v(15.95, -15.64) * mm, v(16, -15.61) * mm, v(16.04, -15.58) * mm]});
            skFitSpline(sketch, "E592", {"points": [v(16.04, -15.58) * mm, v(16.47, -15.27) * mm, v(16.9, -14.97) * mm, v(17.34, -14.65) * mm]});
            skFitSpline(sketch, "E593", {"points": [v(17.34, -14.65) * mm, v(17.22, -14.06) * mm, v(16.97, -13.52) * mm, v(16.8, -12.9) * mm]});
            skFitSpline(sketch, "E594", {"points": [v(16.8, -12.9) * mm, v(16.71, -12.96) * mm, v(16.64, -13) * mm, v(16.57, -13.05) * mm]});
            skFitSpline(sketch, "E595", {"points": [v(16.57, -13.05) * mm, v(16.06, -13.38) * mm, v(15.54, -13.69) * mm, v(14.98, -13.94) * mm]});
            skFitSpline(sketch, "E596", {"points": [v(14.98, -13.94) * mm, v(14.6, -14.11) * mm, v(14.32, -13.99) * mm, v(14.17, -13.6) * mm]});
            skFitSpline(sketch, "E597", {"points": [v(14.17, -13.6) * mm, v(13.94, -13) * mm, v(13.8, -12.38) * mm, v(13.66, -11.76) * mm]});
            skFitSpline(sketch, "E598", {"points": [v(13.66, -11.76) * mm, v(13.65, -11.71) * mm, v(13.63, -11.67) * mm, v(13.61, -11.6) * mm]});
            skFitSpline(sketch, "E599", {"points": [v(13.61, -11.6) * mm, v(13.07, -11.87) * mm, v(12.54, -12.14) * mm, v(11.99, -12.41) * mm]});
            skFitSpline(sketch, "E600", {"points": [v(11.99, -12.41) * mm, v(12.03, -12.67) * mm, v(12.07, -12.9) * mm, v(12.11, -13.13) * mm]});
            skFitSpline(sketch, "E601", {"points": [v(12.11, -13.13) * mm, v(12.18, -13.52) * mm, v(12.25, -13.9) * mm, v(12.32, -14.29) * mm]});
            skFitSpline(sketch, "E602", {"points": [v(12.32, -14.29) * mm, v(12.34, -14.4) * mm, v(12.35, -14.51) * mm, v(12.4, -14.6) * mm]});
            skFitSpline(sketch, "E603", {"points": [v(12.4, -14.6) * mm, v(12.53, -14.86) * mm, v(12.33, -15.2) * mm, v(12.09, -15.27) * mm]});
            skFitSpline(sketch, "E604", {"points": [v(12.09, -15.27) * mm, v(11.77, -15.35) * mm, v(11.54, -15.21) * mm, v(11.46, -14.91) * mm]});
            skFitSpline(sketch, "E605", {"points": [v(11.46, -14.91) * mm, v(11.4, -14.68) * mm, v(11.34, -14.45) * mm, v(11.3, -14.21) * mm]});
            skFitSpline(sketch, "E606", {"points": [v(11.3, -14.21) * mm, v(11.2, -13.66) * mm, v(11.12, -13.11) * mm, v(11.02, -12.56) * mm]});
            skFitSpline(sketch, "E607", {"points": [v(11.02, -12.56) * mm, v(11.01, -12.5) * mm, v(11, -12.45) * mm, v(10.98, -12.4) * mm]});
            skFitSpline(sketch, "E608", {"points": [v(10.98, -12.4) * mm, v(10.88, -12.2) * mm, v(10.9, -12.02) * mm, v(11.03, -11.84) * mm]});
            skFitSpline(sketch, "E609", {"points": [v(11.03, -11.84) * mm, v(11.14, -11.66) * mm, v(11.23, -11.46) * mm, v(11.35, -11.24) * mm]});
            skFitSpline(sketch, "E610", {"points": [v(11.35, -11.24) * mm, v(11.28, -11.25) * mm, v(11.23, -11.25) * mm, v(11.2, -11.27) * mm]});
            skFitSpline(sketch, "E611", {"points": [v(11.2, -11.27) * mm, v(10.53, -11.52) * mm, v(9.87, -11.77) * mm, v(9.2, -12.02) * mm]});
            skFitSpline(sketch, "E612", {"points": [v(9.2, -12.02) * mm, v(9.08, -12.06) * mm, v(9.02, -12.13) * mm, v(8.99, -12.25) * mm]});
            skFitSpline(sketch, "E613", {"points": [v(8.99, -12.25) * mm, v(8.75, -12.95) * mm, v(8.52, -13.66) * mm, v(8.29, -14.36) * mm]});
            skFitSpline(sketch, "E614", {"points": [v(8.29, -14.36) * mm, v(8.11, -14.9) * mm, v(7.95, -15.43) * mm, v(7.77, -15.96) * mm]});
            skFitSpline(sketch, "E615", {"points": [v(7.77, -15.96) * mm, v(7.7, -16.2) * mm, v(7.56, -16.37) * mm, v(7.29, -16.39) * mm]});
            skFitSpline(sketch, "E616", {"points": [v(7.29, -16.39) * mm, v(6.95, -16.4) * mm, v(6.7, -16.1) * mm, v(6.8, -15.76) * mm]});
            skFitSpline(sketch, "E617", {"points": [v(6.8, -15.76) * mm, v(6.94, -15.32) * mm, v(7.08, -14.89) * mm, v(7.23, -14.46) * mm]});
            skFitSpline(sketch, "E618", {"points": [v(7.23, -14.46) * mm, v(7.43, -13.84) * mm, v(7.63, -13.23) * mm, v(7.84, -12.62) * mm]});
            skFitSpline(sketch, "E619", {"points": [v(7.84, -12.62) * mm, v(7.85, -12.59) * mm, v(7.84, -12.56) * mm, v(7.85, -12.5) * mm]});
            skFitSpline(sketch, "E620", {"points": [v(7.85, -12.5) * mm, v(7.75, -12.53) * mm, v(7.67, -12.56) * mm, v(7.59, -12.58) * mm]});
            skFitSpline(sketch, "E621", {"points": [v(7.59, -12.58) * mm, v(6.61, -12.9) * mm, v(5.64, -13.22) * mm, v(4.67, -13.54) * mm]});
            skFitSpline(sketch, "E622", {"points": [v(4.67, -13.54) * mm, v(4.53, -13.59) * mm, v(4.38, -13.6) * mm, v(4.23, -13.53) * mm]});
            skFitSpline(sketch, "E623", {"points": [v(4.23, -13.53) * mm, v(4.07, -13.44) * mm, v(3.98, -13.3) * mm, v(3.98, -13.12) * mm]});
            skFitSpline(sketch, "E624", {"points": [v(3.98, -13.12) * mm, v(3.97, -12.92) * mm, v(4.06, -12.76) * mm, v(4.24, -12.67) * mm]});
            skFitSpline(sketch, "E625", {"points": [v(4.24, -12.67) * mm, v(4.42, -12.58) * mm, v(4.6, -12.52) * mm, v(4.8, -12.46) * mm]});
            skFitSpline(sketch, "E626", {"points": [v(4.8, -12.46) * mm, v(5.87, -12.11) * mm, v(6.94, -11.76) * mm, v(8, -11.42) * mm]});
            skFitSpline(sketch, "E627", {"points": [v(8, -11.42) * mm, v(8.22, -11.36) * mm, v(8.33, -11.24) * mm, v(8.4, -11.03) * mm]});
            skFitSpline(sketch, "E628", {"points": [v(8.4, -11.03) * mm, v(8.6, -10.45) * mm, v(8.83, -9.88) * mm, v(9.05, -9.3) * mm]});
            skFitSpline(sketch, "E629", {"points": [v(9.05, -9.3) * mm, v(9.08, -9.22) * mm, v(9.1, -9.14) * mm, v(9.16, -9) * mm]});
            skFitSpline(sketch, "E630", {"points": [v(9.16, -9) * mm, v(8.93, -9.12) * mm, v(8.74, -9.2) * mm, v(8.57, -9.31) * mm]});
            skFitSpline(sketch, "E631", {"points": [v(8.57, -9.31) * mm, v(8.36, -9.45) * mm, v(8.17, -9.5) * mm, v(7.94, -9.38) * mm]});
            skFitSpline(sketch, "E632", {"points": [v(7.94, -9.38) * mm, v(7.9, -9.36) * mm, v(7.87, -9.35) * mm, v(7.83, -9.34) * mm]});
            skFitSpline(sketch, "E633", {"points": [v(7.83, -9.34) * mm, v(7.3, -9.25) * mm, v(6.79, -9.17) * mm, v(6.27, -9.08) * mm]});
            skFitSpline(sketch, "E634", {"points": [v(6.27, -9.08) * mm, v(5.99, -9.03) * mm, v(5.7, -8.97) * mm, v(5.43, -8.9) * mm]});
            skFitSpline(sketch, "E635", {"points": [v(5.43, -8.9) * mm, v(5.2, -8.84) * mm, v(5.07, -8.65) * mm, v(5.08, -8.42) * mm]});
            skFitSpline(sketch, "E636", {"points": [v(5.08, -8.42) * mm, v(5.08, -8.2) * mm, v(5.23, -8) * mm, v(5.45, -7.95) * mm]});
            skFitSpline(sketch, "E637", {"points": [v(5.45, -7.95) * mm, v(5.52, -7.93) * mm, v(5.6, -7.92) * mm, v(5.66, -7.94) * mm]});
            skFitSpline(sketch, "E638", {"points": [v(5.66, -7.94) * mm, v(6.16, -8.11) * mm, v(6.68, -8.14) * mm, v(7.19, -8.24) * mm]});
            skFitSpline(sketch, "E639", {"points": [v(7.19, -8.24) * mm, v(7.43, -8.29) * mm, v(7.67, -8.33) * mm, v(7.95, -8.38) * mm]});
            skFitSpline(sketch, "E640", {"points": [v(7.95, -8.38) * mm, v(8.22, -7.84) * mm, v(8.5, -7.31) * mm, v(8.78, -6.76) * mm]});
            skFitSpline(sketch, "E641", {"points": [v(8.78, -6.76) * mm, v(8.68, -6.73) * mm, v(8.61, -6.71) * mm, v(8.54, -6.7) * mm]});
            skFitSpline(sketch, "E642", {"points": [v(8.54, -6.7) * mm, v(7.93, -6.56) * mm, v(7.33, -6.41) * mm, v(6.74, -6.19) * mm]});
            skFitSpline(sketch, "E643", {"points": [v(6.74, -6.19) * mm, v(6.38, -6.05) * mm, v(6.24, -5.75) * mm, v(6.42, -5.4) * mm]});
            skFitSpline(sketch, "E644", {"points": [v(6.42, -5.4) * mm, v(6.7, -4.9) * mm, v(6.98, -4.39) * mm, v(7.27, -3.88) * mm]});
            skFitSpline(sketch, "E645", {"points": [v(7.27, -3.88) * mm, v(7.32, -3.78) * mm, v(7.39, -3.7) * mm, v(7.46, -3.57) * mm]});
            skFitSpline(sketch, "E646", {"points": [v(7.46, -3.57) * mm, v(6.87, -3.38) * mm, v(6.3, -3.2) * mm, v(5.74, -3) * mm]});
            skFitSpline(sketch, "E647", {"points": [v(5.74, -3) * mm, v(5.67, -3.1) * mm, v(5.6, -3.16) * mm, v(5.56, -3.23) * mm]});
            skFitSpline(sketch, "E648", {"points": [v(5.56, -3.23) * mm, v(5.25, -3.68) * mm, v(4.93, -4.12) * mm, v(4.63, -4.57) * mm]});
            skFitSpline(sketch, "E649", {"points": [v(4.63, -4.57) * mm, v(4.56, -4.67) * mm, v(4.5, -4.78) * mm, v(4.44, -4.88) * mm]});
            skFitSpline(sketch, "E650", {"points": [v(4.44, -4.88) * mm, v(4.33, -5.07) * mm, v(4.14, -5.17) * mm, v(3.92, -5.13) * mm]});
            skFitSpline(sketch, "E651", {"points": [v(3.92, -5.13) * mm, v(3.71, -5.1) * mm, v(3.57, -4.96) * mm, v(3.51, -4.75) * mm]});
            skFitSpline(sketch, "E652", {"points": [v(3.51, -4.75) * mm, v(3.48, -4.61) * mm, v(3.52, -4.5) * mm, v(3.59, -4.38) * mm]});
            skFitSpline(sketch, "E653", {"points": [v(3.59, -4.38) * mm, v(3.7, -4.18) * mm, v(3.83, -3.99) * mm, v(3.96, -3.8) * mm]});
            skFitSpline(sketch, "E654", {"points": [v(3.96, -3.8) * mm, v(4.28, -3.35) * mm, v(4.6, -2.91) * mm, v(4.9, -2.47) * mm]});
            skFitSpline(sketch, "E655", {"points": [v(4.9, -2.47) * mm, v(4.96, -2.4) * mm, v(5, -2.34) * mm, v(5.02, -2.26) * mm]});
            skFitSpline(sketch, "E656", {"points": [v(5.02, -2.26) * mm, v(5.1, -2.08) * mm, v(5.23, -1.97) * mm, v(5.43, -1.92) * mm]});
            skFitSpline(sketch, "E657", {"points": [v(5.43, -1.92) * mm, v(5.64, -1.87) * mm, v(5.85, -1.8) * mm, v(6.1, -1.72) * mm]});
            skFitSpline(sketch, "E658", {"points": [v(6.1, -1.72) * mm, v(6.03, -1.67) * mm, v(6, -1.64) * mm, v(5.95, -1.62) * mm]});
            skFitSpline(sketch, "E659", {"points": [v(5.95, -1.62) * mm, v(5.32, -1.33) * mm, v(4.68, -1.05) * mm, v(4.05, -0.76) * mm]});
            skFitSpline(sketch, "E660", {"points": [v(4.05, -0.76) * mm, v(3.93, -0.7) * mm, v(3.83, -0.7) * mm, v(3.71, -0.76) * mm]});
            skFitSpline(sketch, "E661", {"points": [v(3.71, -0.76) * mm, v(3.03, -1.12) * mm, v(2.33, -1.46) * mm, v(1.64, -1.81) * mm]});
            skFitSpline(sketch, "E662", {"points": [v(1.64, -1.81) * mm, v(1.17, -2.05) * mm, v(0.7, -2.3) * mm, v(0.23, -2.53) * mm]});
            skFitSpline(sketch, "E663", {"points": [v(0.23, -2.53) * mm, v(0.16, -2.56) * mm, v(0.09, -2.6) * mm, v(0, -2.6) * mm]});
            skFitSpline(sketch, "E664", {"points": [v(0, -2.6) * mm, v(-0.22, -2.66) * mm, v(-0.44, -2.53) * mm, v(-0.54, -2.31) * mm]});
            skFitSpline(sketch, "E665", {"points": [v(-0.54, -2.31) * mm, v(-0.62, -2.11) * mm, v(-0.55, -1.88) * mm, v(-0.36, -1.74) * mm]});
            skFitSpline(sketch, "E666", {"points": [v(-0.36, -1.74) * mm, v(-0.31, -1.7) * mm, v(-0.25, -1.68) * mm, v(-0.2, -1.65) * mm]});
            skFitSpline(sketch, "E667", {"points": [v(-0.2, -1.65) * mm, v(0.73, -1.18) * mm, v(1.66, -0.71) * mm, v(2.58, -0.24) * mm]});
            skFitSpline(sketch, "E668", {"points": [v(2.58, -0.24) * mm, v(2.63, -0.22) * mm, v(2.67, -0.19) * mm, v(2.74, -0.14) * mm]});
            skFitSpline(sketch, "E669", {"points": [v(2.74, -0.14) * mm, v(2.65, -0.1) * mm, v(2.59, -0.06) * mm, v(2.52, -0.02) * mm]});
            skFitSpline(sketch, "E670", {"points": [v(2.52, -0.02) * mm, v(1.6, 0.44) * mm, v(0.68, 0.9) * mm, v(-0.24, 1.37) * mm]});
            skFitSpline(sketch, "E671", {"points": [v(-0.24, 1.37) * mm, v(-0.51, 1.51) * mm, v(-0.63, 1.74) * mm, v(-0.55, 1.97) * mm]});
            skFitSpline(sketch, "E672", {"points": [v(-0.55, 1.97) * mm, v(-0.46, 2.25) * mm, v(-0.2, 2.4) * mm, v(0.08, 2.29) * mm]});
            skFitSpline(sketch, "E673", {"points": [v(0.08, 2.29) * mm, v(0.3, 2.21) * mm, v(0.5, 2.1) * mm, v(0.7, 2) * mm]});
            skFitSpline(sketch, "E674", {"points": [v(0.7, 2) * mm, v(1.7, 1.5) * mm, v(2.68, 1) * mm, v(3.67, 0.49) * mm]});
            skFitSpline(sketch, "E675", {"points": [v(3.67, 0.49) * mm, v(3.82, 0.41) * mm, v(3.94, 0.4) * mm, v(4.1, 0.48) * mm]});
            skFitSpline(sketch, "E676", {"points": [v(4.1, 0.48) * mm, v(4.69, 0.76) * mm, v(5.29, 1.03) * mm, v(5.88, 1.3) * mm]});
            skFitSpline(sketch, "E677", {"points": [v(5.88, 1.3) * mm, v(5.95, 1.32) * mm, v(6, 1.36) * mm, v(6.1, 1.4) * mm]});
            skFitSpline(sketch, "E678", {"points": [v(-95.17, 0.2) * mm, v(-94.8, 0.48) * mm, v(-94.45, 0.75) * mm, v(-94.15, 1.1) * mm]});
            skFitSpline(sketch, "E679", {"points": [v(-94.15, 1.1) * mm, v(-94.5, 1.39) * mm, v(-94.82, 1.67) * mm, v(-95.16, 1.96) * mm]});
            skFitSpline(sketch, "E680", {"points": [v(-95.16, 1.96) * mm, v(-95.43, 1.62) * mm, v(-95.78, 1.4) * mm, v(-96.03, 1.05) * mm]});
            skFitSpline(sketch, "E681", {"points": [v(-96.03, 1.05) * mm, v(-95.74, 0.76) * mm, v(-95.46, 0.5) * mm, v(-95.17, 0.2) * mm]});
            skFitSpline(sketch, "E682", {"points": [v(-106.01, -10.67) * mm, v(-106.27, -10.4) * mm, v(-106.5, -10.16) * mm, v(-106.73, -9.92) * mm]});
            skFitSpline(sketch, "E683", {"points": [v(-106.73, -9.92) * mm, v(-106.77, -9.87) * mm, v(-106.83, -9.84) * mm, v(-106.9, -9.79) * mm]});
            skFitSpline(sketch, "E684", {"points": [v(-106.9, -9.79) * mm, v(-107.19, -10.08) * mm, v(-107.47, -10.36) * mm, v(-107.76, -10.66) * mm]});
            skFitSpline(sketch, "E685", {"points": [v(-107.76, -10.66) * mm, v(-107.47, -11) * mm, v(-107.19, -11.33) * mm, v(-106.89, -11.68) * mm]});
            skFitSpline(sketch, "E686", {"points": [v(-106.89, -11.68) * mm, v(-106.58, -11.33) * mm, v(-106.3, -11) * mm, v(-106.01, -10.67) * mm]});
            skFitSpline(sketch, "E687", {"points": [v(-118.63, 0.2) * mm, v(-118.37, 0.45) * mm, v(-118.13, 0.67) * mm, v(-117.9, 0.9) * mm]});
            skFitSpline(sketch, "E688", {"points": [v(-117.9, 0.9) * mm, v(-117.85, 0.95) * mm, v(-117.8, 1.01) * mm, v(-117.74, 1.1) * mm]});
            skFitSpline(sketch, "E689", {"points": [v(-117.74, 1.1) * mm, v(-118.04, 1.38) * mm, v(-118.32, 1.66) * mm, v(-118.62, 1.95) * mm]});
            skFitSpline(sketch, "E690", {"points": [v(-118.62, 1.95) * mm, v(-118.97, 1.66) * mm, v(-119.3, 1.38) * mm, v(-119.64, 1.07) * mm]});
            skFitSpline(sketch, "E691", {"points": [v(-119.64, 1.07) * mm, v(-119.3, 0.77) * mm, v(-118.97, 0.5) * mm, v(-118.63, 0.2) * mm]});
            skFitSpline(sketch, "E692", {"points": [v(-114.57, 8.75) * mm, v(-114.56, 8.89) * mm, v(-114.54, 9) * mm, v(-114.54, 9.12) * mm]});
            skFitSpline(sketch, "E693", {"points": [v(-114.54, 9.12) * mm, v(-114.54, 9.35) * mm, v(-114.55, 9.57) * mm, v(-114.57, 9.79) * mm]});
            skFitSpline(sketch, "E694", {"points": [v(-114.57, 9.79) * mm, v(-114.57, 9.85) * mm, v(-114.58, 9.91) * mm, v(-114.59, 10) * mm]});
            skFitSpline(sketch, "E695", {"points": [v(-114.59, 10) * mm, v(-115.03, 10.03) * mm, v(-115.46, 10.06) * mm, v(-115.9, 10.1) * mm]});
            skFitSpline(sketch, "E696", {"points": [v(-115.9, 10.1) * mm, v(-115.87, 9.63) * mm, v(-115.84, 9.2) * mm, v(-115.8, 8.75) * mm]});
            skLineSegment(sketch, "E697", {"start": v(-115.8, 8.75) * mm, "end": v(-114.57, 8.75) * mm});
            skFitSpline(sketch, "E698", {"points": [v(-107.76, 12.8) * mm, v(-107.44, 12.53) * mm, v(-107.21, 12.19) * mm, v(-106.87, 11.93) * mm]});
            skFitSpline(sketch, "E699", {"points": [v(-106.87, 11.93) * mm, v(-106.58, 12.23) * mm, v(-106.3, 12.51) * mm, v(-106.03, 12.8) * mm]});
            skFitSpline(sketch, "E700", {"points": [v(-106.03, 12.8) * mm, v(-106.29, 13.17) * mm, v(-106.56, 13.5) * mm, v(-106.9, 13.81) * mm]});
            skFitSpline(sketch, "E701", {"points": [v(-106.9, 13.81) * mm, v(-107.2, 13.47) * mm, v(-107.48, 13.15) * mm, v(-107.76, 12.8) * mm]});
            skFitSpline(sketch, "E702", {"points": [v(-115.9, -7.95) * mm, v(-115.45, -7.92) * mm, v(-115.02, -7.88) * mm, v(-114.56, -7.85) * mm]});
            skFitSpline(sketch, "E703", {"points": [v(-114.56, -7.85) * mm, v(-114.61, -7.42) * mm, v(-114.49, -7.02) * mm, v(-114.58, -6.6) * mm]});
            skLineSegment(sketch, "E704", {"start": v(-114.58, -6.6) * mm, "end": v(-115.8, -6.6) * mm});
            skFitSpline(sketch, "E705", {"points": [v(-115.8, -6.6) * mm, v(-115.84, -7.05) * mm, v(-115.87, -7.48) * mm, v(-115.9, -7.95) * mm]});
            skLineSegment(sketch, "E706", {"start": v(-99.2, 8.76) * mm, "end": v(-98, 8.76) * mm});
            skFitSpline(sketch, "E707", {"points": [v(-98, 8.76) * mm, v(-97.9, 9.21) * mm, v(-97.86, 9.65) * mm, v(-97.89, 10.08) * mm]});
            skFitSpline(sketch, "E708", {"points": [v(-97.89, 10.08) * mm, v(-98.33, 10.06) * mm, v(-98.77, 10.08) * mm, v(-99.2, 9.96) * mm]});
            skFitSpline(sketch, "E709", {"points": [v(-99.2, 9.96) * mm, v(-99.21, 9.64) * mm, v(-99.22, 9.32) * mm, v(-99.23, 9) * mm]});
            skFitSpline(sketch, "E710", {"points": [v(-99.23, 9) * mm, v(-99.23, 8.92) * mm, v(-99.2, 8.85) * mm, v(-99.2, 8.76) * mm]});
            skFitSpline(sketch, "E711", {"points": [v(-99.2, -7.82) * mm, v(-98.74, -7.9) * mm, v(-98.31, -7.95) * mm, v(-97.86, -7.92) * mm]});
            skFitSpline(sketch, "E712", {"points": [v(-97.86, -7.92) * mm, v(-97.9, -7.48) * mm, v(-97.93, -7.05) * mm, v(-97.96, -6.6) * mm]});
            skFitSpline(sketch, "E713", {"points": [v(-97.96, -6.6) * mm, v(-98.4, -6.62) * mm, v(-98.8, -6.55) * mm, v(-99.2, -6.61) * mm]});
            skLineSegment(sketch, "E714", {"start": v(-99.2, -6.61) * mm, "end": v(-99.2, -7.82) * mm});
            skLineSegment(sketch, "E715", {"start": v(-109.99, 3.2) * mm, "end": v(-112.07, 3.2) * mm});
            skFitSpline(sketch, "E716", {"points": [v(-112.07, 3.2) * mm, v(-111.51, 2.75) * mm, v(-111.1, 2.2) * mm, v(-110.54, 1.78) * mm]});
            skFitSpline(sketch, "E717", {"points": [v(-110.54, 1.78) * mm, v(-110.25, 1.93) * mm, v(-109.97, 2.08) * mm, v(-109.68, 2.23) * mm]});
            skFitSpline(sketch, "E718", {"points": [v(-109.68, 2.23) * mm, v(-109.78, 2.56) * mm, v(-109.88, 2.86) * mm, v(-109.99, 3.2) * mm]});
            skFitSpline(sketch, "E719", {"points": [v(-107.58, 4.76) * mm, v(-108.06, 5.25) * mm, v(-108.54, 5.74) * mm, v(-109.03, 6.25) * mm]});
            skFitSpline(sketch, "E720", {"points": [v(-109.03, 6.25) * mm, v(-109.02, 5.53) * mm, v(-109.01, 4.84) * mm, v(-109, 4.16) * mm]});
            skFitSpline(sketch, "E721", {"points": [v(-109, 4.16) * mm, v(-108.66, 4.1) * mm, v(-108.38, 3.9) * mm, v(-108.02, 3.9) * mm]});
            skFitSpline(sketch, "E722", {"points": [v(-108.02, 3.9) * mm, v(-107.88, 4.18) * mm, v(-107.74, 4.45) * mm, v(-107.58, 4.76) * mm]});
            skFitSpline(sketch, "E723", {"points": [v(-103.2, 1.77) * mm, v(-102.7, 2.25) * mm, v(-102.22, 2.73) * mm, v(-101.73, 3.2) * mm]});
            skLineSegment(sketch, "E724", {"start": v(-101.73, 3.2) * mm, "end": v(-103.79, 3.2) * mm});
            skFitSpline(sketch, "E725", {"points": [v(-103.79, 3.2) * mm, v(-103.9, 2.86) * mm, v(-103.99, 2.56) * mm, v(-104.1, 2.23) * mm]});
            skFitSpline(sketch, "E726", {"points": [v(-104.1, 2.23) * mm, v(-103.8, 2.08) * mm, v(-103.51, 1.93) * mm, v(-103.2, 1.77) * mm]});
            skFitSpline(sketch, "E727", {"points": [v(-104.76, -2) * mm, v(-105.12, -1.96) * mm, v(-105.4, -1.75) * mm, v(-105.75, -1.75) * mm]});
            skFitSpline(sketch, "E728", {"points": [v(-105.75, -1.75) * mm, v(-105.9, -2.03) * mm, v(-106.04, -2.31) * mm, v(-106.19, -2.6) * mm]});
            skFitSpline(sketch, "E729", {"points": [v(-106.19, -2.6) * mm, v(-105.71, -3.1) * mm, v(-105.24, -3.58) * mm, v(-104.76, -4.07) * mm]});
            skLineSegment(sketch, "E730", {"start": v(-104.76, -4.07) * mm, "end": v(-104.76, -2) * mm});
            skLineSegment(sketch, "E731", {"start": v(-109.01, -2.02) * mm, "end": v(-109.01, -4.08) * mm});
            skFitSpline(sketch, "E732", {"points": [v(-109.01, -4.08) * mm, v(-108.53, -3.59) * mm, v(-108.06, -3.1) * mm, v(-107.58, -2.6) * mm]});
            skFitSpline(sketch, "E733", {"points": [v(-107.58, -2.6) * mm, v(-107.74, -2.3) * mm, v(-107.88, -2.03) * mm, v(-108.04, -1.72) * mm]});
            skFitSpline(sketch, "E734", {"points": [v(-108.04, -1.72) * mm, v(-108.37, -1.82) * mm, v(-108.68, -1.92) * mm, v(-109.01, -2.02) * mm]});
            skFitSpline(sketch, "E735", {"points": [v(-104.76, 6.23) * mm, v(-105.25, 5.73) * mm, v(-105.72, 5.24) * mm, v(-106.2, 4.75) * mm]});
            skFitSpline(sketch, "E736", {"points": [v(-106.2, 4.75) * mm, v(-106.03, 4.45) * mm, v(-105.88, 4.17) * mm, v(-105.73, 3.87) * mm]});
            skFitSpline(sketch, "E737", {"points": [v(-105.73, 3.87) * mm, v(-105.4, 3.97) * mm, v(-105.1, 4.07) * mm, v(-104.76, 4.17) * mm]});
            skLineSegment(sketch, "E738", {"start": v(-104.76, 4.17) * mm, "end": v(-104.76, 6.23) * mm});
            skFitSpline(sketch, "E739", {"points": [v(-101.73, -1.05) * mm, v(-102.23, -0.56) * mm, v(-102.72, -0.1) * mm, v(-103.2, 0.38) * mm]});
            skFitSpline(sketch, "E740", {"points": [v(-103.2, 0.38) * mm, v(-103.52, 0.22) * mm, v(-103.8, 0.07) * mm, v(-104.1, -0.08) * mm]});
            skFitSpline(sketch, "E741", {"points": [v(-104.1, -0.08) * mm, v(-103.99, -0.42) * mm, v(-103.89, -0.72) * mm, v(-103.78, -1.05) * mm]});
            skLineSegment(sketch, "E742", {"start": v(-103.78, -1.05) * mm, "end": v(-101.73, -1.05) * mm});
            skFitSpline(sketch, "E743", {"points": [v(-110.57, 0.38) * mm, v(-111.06, -0.1) * mm, v(-111.55, -0.57) * mm, v(-112.04, -1.05) * mm]});
            skLineSegment(sketch, "E744", {"start": v(-112.04, -1.05) * mm, "end": v(-109.99, -1.05) * mm});
            skFitSpline(sketch, "E745", {"points": [v(-109.99, -1.05) * mm, v(-109.88, -0.7) * mm, v(-109.78, -0.4) * mm, v(-109.68, -0.08) * mm]});
            skFitSpline(sketch, "E746", {"points": [v(-109.68, -0.08) * mm, v(-109.98, 0.08) * mm, v(-110.26, 0.22) * mm, v(-110.57, 0.38) * mm]});
            skFitSpline(sketch, "E747", {"points": [v(-108.71, -6.52) * mm, v(-108.08, -7.17) * mm, v(-107.5, -7.78) * mm, v(-106.88, -8.41) * mm]});
            skFitSpline(sketch, "E748", {"points": [v(-106.88, -8.41) * mm, v(-106.3, -7.76) * mm, v(-105.65, -7.2) * mm, v(-105.08, -6.52) * mm]});
            skFitSpline(sketch, "E749", {"points": [v(-105.08, -6.52) * mm, v(-105.44, -6.5) * mm, v(-105.76, -6.5) * mm, v(-106.07, -6.45) * mm]});
            skFitSpline(sketch, "E750", {"points": [v(-106.07, -6.45) * mm, v(-106.61, -6.36) * mm, v(-107.15, -6.36) * mm, v(-107.7, -6.45) * mm]});
            skFitSpline(sketch, "E751", {"points": [v(-107.7, -6.45) * mm, v(-108.01, -6.5) * mm, v(-108.33, -6.5) * mm, v(-108.71, -6.52) * mm]});
            skFitSpline(sketch, "E752", {"points": [v(-114.5, -0.75) * mm, v(-114.46, -0.3) * mm, v(-114.45, 0.1) * mm, v(-114.38, 0.5) * mm]});
            skFitSpline(sketch, "E753", {"points": [v(-114.38, 0.5) * mm, v(-114.3, 0.94) * mm, v(-114.33, 1.37) * mm, v(-114.41, 1.8) * mm]});
            skFitSpline(sketch, "E754", {"points": [v(-114.41, 1.8) * mm, v(-114.42, 1.84) * mm, v(-114.42, 1.9) * mm, v(-114.42, 1.94) * mm]});
            skFitSpline(sketch, "E755", {"points": [v(-114.42, 1.94) * mm, v(-114.44, 2.24) * mm, v(-114.46, 2.54) * mm, v(-114.48, 2.84) * mm]});
            skFitSpline(sketch, "E756", {"points": [v(-114.48, 2.84) * mm, v(-114.67, 2.74) * mm, v(-116.25, 1.21) * mm, v(-116.34, 1.05) * mm]});
            skFitSpline(sketch, "E757", {"points": [v(-116.34, 1.05) * mm, v(-115.74, 0.46) * mm, v(-115.13, -0.12) * mm, v(-114.5, -0.75) * mm]});
            skFitSpline(sketch, "E758", {"points": [v(-110.98, 7.74) * mm, v(-111.86, 7.76) * mm, v(-112.73, 7.77) * mm, v(-113.6, 7.78) * mm]});
            skFitSpline(sketch, "E759", {"points": [v(-113.6, 7.78) * mm, v(-113.58, 6.9) * mm, v(-113.57, 6.05) * mm, v(-113.55, 5.15) * mm]});
            skFitSpline(sketch, "E760", {"points": [v(-113.55, 5.15) * mm, v(-113.48, 5.2) * mm, v(-113.44, 5.24) * mm, v(-113.4, 5.27) * mm]});
            skFitSpline(sketch, "E761", {"points": [v(-113.4, 5.27) * mm, v(-113.08, 5.55) * mm, v(-112.77, 5.84) * mm, v(-112.43, 6.1) * mm]});
            skFitSpline(sketch, "E762", {"points": [v(-112.43, 6.1) * mm, v(-112.23, 6.25) * mm, v(-112.05, 6.42) * mm, v(-111.9, 6.63) * mm]});
            skFitSpline(sketch, "E763", {"points": [v(-111.9, 6.63) * mm, v(-111.61, 7) * mm, v(-111.3, 7.35) * mm, v(-110.98, 7.74) * mm]});
            skFitSpline(sketch, "E764", {"points": [v(-99.25, 2.87) * mm, v(-99.27, 2.86) * mm, v(-99.28, 2.85) * mm, v(-99.3, 2.84) * mm]});
            skFitSpline(sketch, "E765", {"points": [v(-99.3, 2.84) * mm, v(-99.3, 2.8) * mm, v(-99.3, 2.78) * mm, v(-99.3, 2.75) * mm]});
            skFitSpline(sketch, "E766", {"points": [v(-99.3, 2.75) * mm, v(-99.34, 2.33) * mm, v(-99.37, 1.92) * mm, v(-99.4, 1.5) * mm]});
            skFitSpline(sketch, "E767", {"points": [v(-99.4, 1.5) * mm, v(-99.42, 1.32) * mm, v(-99.46, 1.13) * mm, v(-99.45, 0.94) * mm]});
            skFitSpline(sketch, "E768", {"points": [v(-99.45, 0.94) * mm, v(-99.42, 0.57) * mm, v(-99.36, 0.2) * mm, v(-99.33, -0.17) * mm]});
            skFitSpline(sketch, "E769", {"points": [v(-99.33, -0.17) * mm, v(-99.3, -0.35) * mm, v(-99.3, -0.52) * mm, v(-99.3, -0.74) * mm]});
            skFitSpline(sketch, "E770", {"points": [v(-99.3, -0.74) * mm, v(-98.62, -0.16) * mm, v(-98.05, 0.49) * mm, v(-97.4, 1.07) * mm]});
            skFitSpline(sketch, "E771", {"points": [v(-97.4, 1.07) * mm, v(-98.03, 1.68) * mm, v(-98.64, 2.28) * mm, v(-99.25, 2.87) * mm]});
            skFitSpline(sketch, "E772", {"points": [v(-102.8, 7.74) * mm, v(-102.77, 7.7) * mm, v(-102.77, 7.67) * mm, v(-102.75, 7.66) * mm]});
            skFitSpline(sketch, "E773", {"points": [v(-102.75, 7.66) * mm, v(-102.35, 7.27) * mm, v(-102, 6.84) * mm, v(-101.68, 6.37) * mm]});
            skFitSpline(sketch, "E774", {"points": [v(-101.68, 6.37) * mm, v(-101.65, 6.32) * mm, v(-101.6, 6.28) * mm, v(-101.54, 6.25) * mm]});
            skFitSpline(sketch, "E775", {"points": [v(-101.54, 6.25) * mm, v(-101.13, 5.96) * mm, v(-100.74, 5.65) * mm, v(-100.38, 5.29) * mm]});
            skFitSpline(sketch, "E776", {"points": [v(-100.38, 5.29) * mm, v(-100.34, 5.25) * mm, v(-100.3, 5.21) * mm, v(-100.22, 5.16) * mm]});
            skFitSpline(sketch, "E777", {"points": [v(-100.22, 5.16) * mm, v(-100.22, 5.62) * mm, v(-100.24, 6.05) * mm, v(-100.21, 6.48) * mm]});
            skFitSpline(sketch, "E778", {"points": [v(-100.21, 6.48) * mm, v(-100.19, 6.91) * mm, v(-100.18, 7.35) * mm, v(-100.18, 7.79) * mm]});
            skFitSpline(sketch, "E779", {"points": [v(-100.18, 7.79) * mm, v(-101.07, 7.77) * mm, v(-101.92, 7.76) * mm, v(-102.8, 7.74) * mm]});
            skFitSpline(sketch, "E780", {"points": [v(-108.68, 8.71) * mm, v(-108.67, 8.7) * mm, v(-108.66, 8.67) * mm, v(-108.64, 8.65) * mm]});
            skFitSpline(sketch, "E781", {"points": [v(-108.64, 8.65) * mm, v(-108.52, 8.65) * mm, v(-108.39, 8.66) * mm, v(-108.26, 8.65) * mm]});
            skFitSpline(sketch, "E782", {"points": [v(-108.26, 8.65) * mm, v(-107.54, 8.61) * mm, v(-106.81, 8.4) * mm, v(-106.08, 8.6) * mm]});
            skFitSpline(sketch, "E783", {"points": [v(-106.08, 8.6) * mm, v(-106.07, 8.61) * mm, v(-106.05, 8.6) * mm, v(-106.04, 8.6) * mm]});
            skFitSpline(sketch, "E784", {"points": [v(-106.04, 8.6) * mm, v(-105.73, 8.63) * mm, v(-105.42, 8.65) * mm, v(-105.08, 8.67) * mm]});
            skFitSpline(sketch, "E785", {"points": [v(-105.08, 8.67) * mm, v(-105.66, 9.34) * mm, v(-106.3, 9.91) * mm, v(-106.88, 10.56) * mm]});
            skFitSpline(sketch, "E786", {"points": [v(-106.88, 10.56) * mm, v(-107.5, 9.93) * mm, v(-108.09, 9.32) * mm, v(-108.68, 8.71) * mm]});
            skFitSpline(sketch, "E787", {"points": [v(-113.55, -3) * mm, v(-113.57, -3.9) * mm, v(-113.58, -4.76) * mm, v(-113.6, -5.64) * mm]});
            skFitSpline(sketch, "E788", {"points": [v(-113.6, -5.64) * mm, v(-112.71, -5.62) * mm, v(-111.85, -5.6) * mm, v(-110.97, -5.6) * mm]});
            skFitSpline(sketch, "E789", {"points": [v(-110.97, -5.6) * mm, v(-111, -5.54) * mm, v(-111.01, -5.51) * mm, v(-111.03, -5.5) * mm]});
            skFitSpline(sketch, "E790", {"points": [v(-111.03, -5.5) * mm, v(-111.42, -5.1) * mm, v(-111.77, -4.69) * mm, v(-112.08, -4.23) * mm]});
            skFitSpline(sketch, "E791", {"points": [v(-112.08, -4.23) * mm, v(-112.12, -4.17) * mm, v(-112.19, -4.13) * mm, v(-112.24, -4.09) * mm]});
            skFitSpline(sketch, "E792", {"points": [v(-112.24, -4.09) * mm, v(-112.62, -3.78) * mm, v(-113, -3.47) * mm, v(-113.36, -3.16) * mm]});
            skFitSpline(sketch, "E793", {"points": [v(-113.36, -3.16) * mm, v(-113.42, -3.12) * mm, v(-113.47, -3.07) * mm, v(-113.55, -3) * mm]});
            skFitSpline(sketch, "E794", {"points": [v(-102.82, -5.6) * mm, v(-101.91, -5.6) * mm, v(-101.05, -5.62) * mm, v(-100.17, -5.64) * mm]});
            skFitSpline(sketch, "E795", {"points": [v(-100.17, -5.64) * mm, v(-100.19, -4.76) * mm, v(-100.2, -3.9) * mm, v(-100.22, -3) * mm]});
            skFitSpline(sketch, "E796", {"points": [v(-100.22, -3) * mm, v(-100.32, -3.08) * mm, v(-100.37, -3.13) * mm, v(-100.43, -3.18) * mm]});
            skFitSpline(sketch, "E797", {"points": [v(-100.43, -3.18) * mm, v(-100.67, -3.4) * mm, v(-100.9, -3.62) * mm, v(-101.16, -3.8) * mm]});
            skFitSpline(sketch, "E798", {"points": [v(-101.16, -3.8) * mm, v(-101.5, -4.04) * mm, v(-101.78, -4.31) * mm, v(-102, -4.66) * mm]});
            skFitSpline(sketch, "E799", {"points": [v(-102, -4.66) * mm, v(-102.1, -4.8) * mm, v(-102.21, -4.92) * mm, v(-102.32, -5.05) * mm]});
            skFitSpline(sketch, "E800", {"points": [v(-102.32, -5.05) * mm, v(-102.47, -5.22) * mm, v(-102.63, -5.39) * mm, v(-102.82, -5.6) * mm]});
            skFitSpline(sketch, "E801", {"points": [v(-108.99, 7.72) * mm, v(-109, 7.7) * mm, v(-109, 7.67) * mm, v(-109.02, 7.64) * mm]});
            skFitSpline(sketch, "E802", {"points": [v(-109.02, 7.64) * mm, v(-108.3, 6.9) * mm, v(-107.6, 6.18) * mm, v(-106.89, 5.44) * mm]});
            skFitSpline(sketch, "E803", {"points": [v(-106.89, 5.44) * mm, v(-106.16, 6.19) * mm, v(-105.45, 6.92) * mm, v(-104.73, 7.66) * mm]});
            skFitSpline(sketch, "E804", {"points": [v(-104.73, 7.66) * mm, v(-104.78, 7.68) * mm, v(-104.8, 7.7) * mm, v(-104.82, 7.7) * mm]});
            skFitSpline(sketch, "E805", {"points": [v(-104.82, 7.7) * mm, v(-105.25, 7.67) * mm, v(-105.69, 7.68) * mm, v(-106.11, 7.62) * mm]});
            skFitSpline(sketch, "E806", {"points": [v(-106.11, 7.62) * mm, v(-106.62, 7.54) * mm, v(-107.12, 7.53) * mm, v(-107.63, 7.61) * mm]});
            skFitSpline(sketch, "E807", {"points": [v(-107.63, 7.61) * mm, v(-108.08, 7.68) * mm, v(-108.53, 7.69) * mm, v(-108.99, 7.72) * mm]});
            skFitSpline(sketch, "E808", {"points": [v(-103.76, -5.1) * mm, v(-103.71, -5.07) * mm, v(-103.69, -5.07) * mm, v(-103.67, -5.05) * mm]});
            skFitSpline(sketch, "E809", {"points": [v(-103.67, -5.05) * mm, v(-103.24, -4.64) * mm, v(-102.84, -4.2) * mm, v(-102.5, -3.7) * mm]});
            skFitSpline(sketch, "E810", {"points": [v(-102.5, -3.7) * mm, v(-102.41, -3.56) * mm, v(-102.3, -3.43) * mm, v(-102.16, -3.34) * mm]});
            skFitSpline(sketch, "E811", {"points": [v(-102.16, -3.34) * mm, v(-101.67, -3) * mm, v(-101.22, -2.62) * mm, v(-100.81, -2.2) * mm]});
            skFitSpline(sketch, "E812", {"points": [v(-100.81, -2.2) * mm, v(-100.78, -2.16) * mm, v(-100.75, -2.12) * mm, v(-100.7, -2.05) * mm]});
            skFitSpline(sketch, "E813", {"points": [v(-100.7, -2.05) * mm, v(-101.76, -2.04) * mm, v(-102.78, -2.02) * mm, v(-103.8, -2.01) * mm]});
            skFitSpline(sketch, "E814", {"points": [v(-103.8, -2.01) * mm, v(-103.79, -3.05) * mm, v(-103.78, -4.06) * mm, v(-103.76, -5.1) * mm]});
            skFitSpline(sketch, "E815", {"points": [v(-113.07, -2.05) * mm, v(-112.78, -2.42) * mm, v(-112.15, -2.97) * mm, v(-111.68, -3.29) * mm]});
            skFitSpline(sketch, "E816", {"points": [v(-111.68, -3.29) * mm, v(-111.54, -3.39) * mm, v(-111.4, -3.5) * mm, v(-111.3, -3.65) * mm]});
            skFitSpline(sketch, "E817", {"points": [v(-111.3, -3.65) * mm, v(-110.97, -4.14) * mm, v(-110.59, -4.58) * mm, v(-110.16, -5) * mm]});
            skFitSpline(sketch, "E818", {"points": [v(-110.16, -5) * mm, v(-110.12, -5.03) * mm, v(-110.08, -5.05) * mm, v(-110.02, -5.1) * mm]});
            skFitSpline(sketch, "E819", {"points": [v(-110.02, -5.1) * mm, v(-110, -4.05) * mm, v(-109.98, -3.03) * mm, v(-109.96, -2) * mm]});
            skFitSpline(sketch, "E820", {"points": [v(-109.96, -2) * mm, v(-111, -2.02) * mm, v(-112.02, -2.04) * mm, v(-113.07, -2.05) * mm]});
            skFitSpline(sketch, "E821", {"points": [v(-100.3, -1.07) * mm, v(-100.29, -1.02) * mm, v(-100.27, -0.98) * mm, v(-100.27, -0.95) * mm]});
            skFitSpline(sketch, "E822", {"points": [v(-100.27, -0.95) * mm, v(-100.3, -0.5) * mm, v(-100.32, -0.04) * mm, v(-100.36, 0.4) * mm]});
            skFitSpline(sketch, "E823", {"points": [v(-100.36, 0.4) * mm, v(-100.39, 0.73) * mm, v(-100.46, 1.04) * mm, v(-100.42, 1.36) * mm]});
            skFitSpline(sketch, "E824", {"points": [v(-100.42, 1.36) * mm, v(-100.36, 1.79) * mm, v(-100.3, 2.21) * mm, v(-100.27, 2.64) * mm]});
            skFitSpline(sketch, "E825", {"points": [v(-100.27, 2.64) * mm, v(-100.26, 2.82) * mm, v(-100.24, 3.01) * mm, v(-100.3, 3.22) * mm]});
            skFitSpline(sketch, "E826", {"points": [v(-100.3, 3.22) * mm, v(-101.05, 2.5) * mm, v(-101.78, 1.79) * mm, v(-102.52, 1.07) * mm]});
            skFitSpline(sketch, "E827", {"points": [v(-102.52, 1.07) * mm, v(-101.78, 0.36) * mm, v(-101.05, -0.35) * mm, v(-100.3, -1.07) * mm]});
            skFitSpline(sketch, "E828", {"points": [v(-113.5, -1.03) * mm, v(-113.5, -1.04) * mm, v(-113.47, -1.05) * mm, v(-113.45, -1.06) * mm]});
            skFitSpline(sketch, "E829", {"points": [v(-113.45, -1.06) * mm, v(-112.72, -0.35) * mm, v(-111.99, 0.36) * mm, v(-111.25, 1.08) * mm]});
            skFitSpline(sketch, "E830", {"points": [v(-111.25, 1.08) * mm, v(-111.44, 1.26) * mm, v(-111.62, 1.43) * mm, v(-111.79, 1.6) * mm]});
            skFitSpline(sketch, "E831", {"points": [v(-111.79, 1.6) * mm, v(-112.3, 2.1) * mm, v(-112.83, 2.6) * mm, v(-113.35, 3.11) * mm]});
            skFitSpline(sketch, "E832", {"points": [v(-113.35, 3.11) * mm, v(-113.38, 3.15) * mm, v(-113.43, 3.17) * mm, v(-113.5, 3.21) * mm]});
            skFitSpline(sketch, "E833", {"points": [v(-113.5, 3.21) * mm, v(-113.5, 3.13) * mm, v(-113.5, 3.07) * mm, v(-113.5, 3.02) * mm]});
            skFitSpline(sketch, "E834", {"points": [v(-113.5, 3.02) * mm, v(-113.5, 2.46) * mm, v(-113.46, 1.9) * mm, v(-113.36, 1.36) * mm]});
            skFitSpline(sketch, "E835", {"points": [v(-113.36, 1.36) * mm, v(-113.34, 1.2) * mm, v(-113.33, 1.02) * mm, v(-113.34, 0.86) * mm]});
            skFitSpline(sketch, "E836", {"points": [v(-113.34, 0.86) * mm, v(-113.39, 0.42) * mm, v(-113.46, -0.02) * mm, v(-113.5, -0.47) * mm]});
            skFitSpline(sketch, "E837", {"points": [v(-113.5, -0.47) * mm, v(-113.53, -0.65) * mm, v(-113.5, -0.85) * mm, v(-113.5, -1.03) * mm]});
            skFitSpline(sketch, "E838", {"points": [v(-103.76, 7.27) * mm, v(-103.78, 6.2) * mm, v(-103.79, 5.18) * mm, v(-103.8, 4.15) * mm]});
            skFitSpline(sketch, "E839", {"points": [v(-103.8, 4.15) * mm, v(-102.77, 4.17) * mm, v(-101.75, 4.19) * mm, v(-100.72, 4.2) * mm]});
            skFitSpline(sketch, "E840", {"points": [v(-100.72, 4.2) * mm, v(-100.74, 4.25) * mm, v(-100.74, 4.27) * mm, v(-100.75, 4.28) * mm]});
            skFitSpline(sketch, "E841", {"points": [v(-100.75, 4.28) * mm, v(-101.17, 4.71) * mm, v(-101.61, 5.12) * mm, v(-102.11, 5.46) * mm]});
            skFitSpline(sketch, "E842", {"points": [v(-102.11, 5.46) * mm, v(-102.25, 5.55) * mm, v(-102.38, 5.67) * mm, v(-102.47, 5.8) * mm]});
            skFitSpline(sketch, "E843", {"points": [v(-102.47, 5.8) * mm, v(-102.8, 6.3) * mm, v(-103.2, 6.74) * mm, v(-103.62, 7.15) * mm]});
            skFitSpline(sketch, "E844", {"points": [v(-103.62, 7.15) * mm, v(-103.65, 7.18) * mm, v(-103.69, 7.2) * mm, v(-103.76, 7.27) * mm]});
            skFitSpline(sketch, "E845", {"points": [v(-104.77, -5.56) * mm, v(-104.76, -5.53) * mm, v(-104.76, -5.51) * mm, v(-104.75, -5.5) * mm]});
            skFitSpline(sketch, "E846", {"points": [v(-104.75, -5.5) * mm, v(-105.46, -4.76) * mm, v(-106.17, -4.03) * mm, v(-106.89, -3.29) * mm]});
            skFitSpline(sketch, "E847", {"points": [v(-106.89, -3.29) * mm, v(-107, -3.41) * mm, v(-107.1, -3.53) * mm, v(-107.22, -3.64) * mm]});
            skFitSpline(sketch, "E848", {"points": [v(-107.22, -3.64) * mm, v(-107.79, -4.23) * mm, v(-108.36, -4.8) * mm, v(-108.93, -5.4) * mm]});
            skFitSpline(sketch, "E849", {"points": [v(-108.93, -5.4) * mm, v(-108.96, -5.43) * mm, v(-108.98, -5.47) * mm, v(-109.03, -5.54) * mm]});
            skFitSpline(sketch, "E850", {"points": [v(-109.03, -5.54) * mm, v(-108.52, -5.57) * mm, v(-108.06, -5.53) * mm, v(-107.6, -5.47) * mm]});
            skFitSpline(sketch, "E851", {"points": [v(-107.6, -5.47) * mm, v(-107.28, -5.43) * mm, v(-106.96, -5.34) * mm, v(-106.64, -5.4) * mm]});
            skFitSpline(sketch, "E852", {"points": [v(-106.64, -5.4) * mm, v(-106.36, -5.43) * mm, v(-106.07, -5.48) * mm, v(-105.79, -5.5) * mm]});
            skFitSpline(sketch, "E853", {"points": [v(-105.79, -5.5) * mm, v(-105.45, -5.54) * mm, v(-105.1, -5.54) * mm, v(-104.77, -5.56) * mm]});
            skFitSpline(sketch, "E854", {"points": [v(-113.09, 4.2) * mm, v(-112.01, 4.19) * mm, v(-111, 4.17) * mm, v(-109.98, 4.15) * mm]});
            skFitSpline(sketch, "E855", {"points": [v(-109.98, 4.15) * mm, v(-109.98, 4.3) * mm, v(-109.97, 4.42) * mm, v(-109.98, 4.55) * mm]});
            skFitSpline(sketch, "E856", {"points": [v(-109.98, 4.55) * mm, v(-109.99, 5.4) * mm, v(-110, 6.24) * mm, v(-110, 7.09) * mm]});
            skFitSpline(sketch, "E857", {"points": [v(-110, 7.09) * mm, v(-110, 7.14) * mm, v(-110.03, 7.19) * mm, v(-110.04, 7.25) * mm]});
            skFitSpline(sketch, "E858", {"points": [v(-110.04, 7.25) * mm, v(-110.5, 6.82) * mm, v(-110.9, 6.38) * mm, v(-111.24, 5.88) * mm]});
            skFitSpline(sketch, "E859", {"points": [v(-111.24, 5.88) * mm, v(-111.36, 5.7) * mm, v(-111.51, 5.55) * mm, v(-111.7, 5.43) * mm]});
            skFitSpline(sketch, "E860", {"points": [v(-111.7, 5.43) * mm, v(-112.2, 5.1) * mm, v(-112.64, 4.7) * mm, v(-113.09, 4.2) * mm]});
            skFitSpline(sketch, "E861", {"points": [v(-106.89, -17.16) * mm, v(-107.1, -17.35) * mm, v(-107.3, -17.54) * mm, v(-107.53, -17.71) * mm]});
            skFitSpline(sketch, "E862", {"points": [v(-107.53, -17.71) * mm, v(-107.96, -18.04) * mm, v(-108.4, -18.36) * mm, v(-108.83, -18.69) * mm]});
            skFitSpline(sketch, "E863", {"points": [v(-108.83, -18.69) * mm, v(-109.1, -18.89) * mm, v(-109.53, -18.8) * mm, v(-109.6, -18.38) * mm]});
            skFitSpline(sketch, "E864", {"points": [v(-109.6, -18.38) * mm, v(-109.66, -18.15) * mm, v(-109.53, -17.98) * mm, v(-109.35, -17.86) * mm]});
            skFitSpline(sketch, "E865", {"points": [v(-109.35, -17.86) * mm, v(-109.16, -17.72) * mm, v(-108.96, -17.61) * mm, v(-108.78, -17.47) * mm]});
            skFitSpline(sketch, "E866", {"points": [v(-108.78, -17.47) * mm, v(-108.37, -17.14) * mm, v(-107.98, -16.8) * mm, v(-107.58, -16.47) * mm]});
            skFitSpline(sketch, "E867", {"points": [v(-107.58, -16.47) * mm, v(-107.49, -16.4) * mm, v(-107.51, -16.3) * mm, v(-107.5, -16.2) * mm]});
            skFitSpline(sketch, "E868", {"points": [v(-107.5, -16.2) * mm, v(-107.49, -15.94) * mm, v(-107.47, -15.68) * mm, v(-107.47, -15.42) * mm]});
            skFitSpline(sketch, "E869", {"points": [v(-107.47, -15.42) * mm, v(-107.45, -14.9) * mm, v(-107.43, -14.38) * mm, v(-107.42, -13.87) * mm]});
            skFitSpline(sketch, "E870", {"points": [v(-107.42, -13.87) * mm, v(-107.42, -13.82) * mm, v(-107.42, -13.77) * mm, v(-107.43, -13.68) * mm]});
            skFitSpline(sketch, "E871", {"points": [v(-107.43, -13.68) * mm, v(-107.49, -13.75) * mm, v(-107.52, -13.79) * mm, v(-107.55, -13.82) * mm]});
            skFitSpline(sketch, "E872", {"points": [v(-107.55, -13.82) * mm, v(-108, -14.3) * mm, v(-108.43, -14.8) * mm, v(-108.88, -15.27) * mm]});
            skFitSpline(sketch, "E873", {"points": [v(-108.88, -15.27) * mm, v(-109.16, -15.57) * mm, v(-109.6, -15.43) * mm, v(-109.7, -15.04) * mm]});
            skFitSpline(sketch, "E874", {"points": [v(-109.7, -15.04) * mm, v(-109.75, -14.85) * mm, v(-109.66, -14.7) * mm, v(-109.54, -14.57) * mm]});
            skFitSpline(sketch, "E875", {"points": [v(-109.54, -14.57) * mm, v(-109.36, -14.38) * mm, v(-109.18, -14.2) * mm, v(-109, -14.01) * mm]});
            skFitSpline(sketch, "E876", {"points": [v(-109, -14.01) * mm, v(-108.73, -13.7) * mm, v(-108.46, -13.36) * mm, v(-108.19, -13.04) * mm]});
            skFitSpline(sketch, "E877", {"points": [v(-108.19, -13.04) * mm, v(-108, -12.82) * mm, v(-107.8, -12.6) * mm, v(-107.59, -12.36) * mm]});
            skFitSpline(sketch, "E878", {"points": [v(-107.59, -12.36) * mm, v(-107.87, -12.04) * mm, v(-108.15, -11.72) * mm, v(-108.44, -11.38) * mm]});
            skFitSpline(sketch, "E879", {"points": [v(-108.44, -11.38) * mm, v(-108.7, -11.56) * mm, v(-108.88, -11.81) * mm, v(-109.1, -12.03) * mm]});
            skFitSpline(sketch, "E880", {"points": [v(-109.1, -12.03) * mm, v(-109.3, -12.24) * mm, v(-109.5, -12.47) * mm, v(-109.7, -12.67) * mm]});
            skFitSpline(sketch, "E881", {"points": [v(-109.7, -12.67) * mm, v(-110, -12.95) * mm, v(-110.45, -12.8) * mm, v(-110.52, -12.4) * mm]});
            skFitSpline(sketch, "E882", {"points": [v(-110.52, -12.4) * mm, v(-110.55, -12.24) * mm, v(-110.5, -12.1) * mm, v(-110.39, -11.98) * mm]});
            skFitSpline(sketch, "E883", {"points": [v(-110.39, -11.98) * mm, v(-110.26, -11.83) * mm, v(-110.12, -11.68) * mm, v(-109.99, -11.54) * mm]});
            skFitSpline(sketch, "E884", {"points": [v(-109.99, -11.54) * mm, v(-109.61, -11.15) * mm, v(-109.24, -10.75) * mm, v(-108.86, -10.37) * mm]});
            skFitSpline(sketch, "E885", {"points": [v(-108.86, -10.37) * mm, v(-108.44, -9.95) * mm, v(-108.02, -9.54) * mm, v(-107.58, -9.1) * mm]});
            skFitSpline(sketch, "E886", {"points": [v(-107.58, -9.1) * mm, v(-107.72, -8.95) * mm, v(-107.85, -8.82) * mm, v(-108, -8.67) * mm]});
            skFitSpline(sketch, "E887", {"points": [v(-108, -8.67) * mm, v(-108.04, -8.7) * mm, v(-108.1, -8.73) * mm, v(-108.14, -8.77) * mm]});
            skFitSpline(sketch, "E888", {"points": [v(-108.14, -8.77) * mm, v(-108.35, -8.94) * mm, v(-108.53, -9.13) * mm, v(-108.75, -9.28) * mm]});
            skFitSpline(sketch, "E889", {"points": [v(-108.75, -9.28) * mm, v(-109.06, -9.5) * mm, v(-109.37, -9.73) * mm, v(-109.7, -9.92) * mm]});
            skFitSpline(sketch, "E890", {"points": [v(-109.7, -9.92) * mm, v(-110, -10.1) * mm, v(-110.33, -9.93) * mm, v(-110.42, -9.6) * mm]});
            skFitSpline(sketch, "E891", {"points": [v(-110.42, -9.6) * mm, v(-110.46, -9.42) * mm, v(-110.4, -9.27) * mm, v(-110.27, -9.15) * mm]});
            skFitSpline(sketch, "E892", {"points": [v(-110.27, -9.15) * mm, v(-110.22, -9.1) * mm, v(-110.15, -9.06) * mm, v(-110.1, -9.03) * mm]});
            skFitSpline(sketch, "E893", {"points": [v(-110.1, -9.03) * mm, v(-109.6, -8.77) * mm, v(-109.2, -8.4) * mm, v(-108.8, -8.05) * mm]});
            skFitSpline(sketch, "E894", {"points": [v(-108.8, -8.05) * mm, v(-108.76, -8.02) * mm, v(-108.73, -8) * mm, v(-108.68, -7.98) * mm]});
            skFitSpline(sketch, "E895", {"points": [v(-108.68, -7.98) * mm, v(-108.97, -7.67) * mm, v(-109.22, -7.4) * mm, v(-109.47, -7.12) * mm]});
            skFitSpline(sketch, "E896", {"points": [v(-109.47, -7.12) * mm, v(-109.59, -7) * mm, v(-109.7, -6.88) * mm, v(-109.82, -6.76) * mm]});
            skFitSpline(sketch, "E897", {"points": [v(-109.82, -6.76) * mm, v(-109.96, -6.6) * mm, v(-110.11, -6.53) * mm, v(-110.32, -6.54) * mm]});
            skFitSpline(sketch, "E898", {"points": [v(-110.32, -6.54) * mm, v(-110.86, -6.56) * mm, v(-111.39, -6.57) * mm, v(-111.92, -6.59) * mm]});
            skFitSpline(sketch, "E899", {"points": [v(-111.92, -6.59) * mm, v(-111.94, -6.59) * mm, v(-111.95, -6.6) * mm, v(-111.97, -6.61) * mm]});
            skFitSpline(sketch, "E900", {"points": [v(-111.97, -6.61) * mm, v(-111.97, -6.73) * mm, v(-111.98, -6.86) * mm, v(-111.97, -6.98) * mm]});
            skFitSpline(sketch, "E901", {"points": [v(-111.97, -6.98) * mm, v(-111.94, -7.44) * mm, v(-111.9, -7.9) * mm, v(-111.76, -8.35) * mm]});
            skFitSpline(sketch, "E902", {"points": [v(-111.76, -8.35) * mm, v(-111.74, -8.42) * mm, v(-111.74, -8.5) * mm, v(-111.73, -8.56) * mm]});
            skFitSpline(sketch, "E903", {"points": [v(-111.73, -8.56) * mm, v(-111.7, -8.77) * mm, v(-111.87, -8.98) * mm, v(-112.1, -9.04) * mm]});
            skFitSpline(sketch, "E904", {"points": [v(-112.1, -9.04) * mm, v(-112.33, -9.1) * mm, v(-112.57, -8.98) * mm, v(-112.65, -8.74) * mm]});
            skFitSpline(sketch, "E905", {"points": [v(-112.65, -8.74) * mm, v(-112.73, -8.5) * mm, v(-112.8, -8.25) * mm, v(-112.84, -8) * mm]});
            skFitSpline(sketch, "E906", {"points": [v(-112.84, -8) * mm, v(-112.9, -7.61) * mm, v(-112.91, -7.22) * mm, v(-112.95, -6.83) * mm]});
            skFitSpline(sketch, "E907", {"points": [v(-112.95, -6.83) * mm, v(-112.96, -6.76) * mm, v(-112.97, -6.7) * mm, v(-112.98, -6.61) * mm]});
            skLineSegment(sketch, "E908", {"start": v(-112.98, -6.61) * mm, "end": v(-113.58, -6.61) * mm});
            skFitSpline(sketch, "E909", {"points": [v(-113.58, -6.61) * mm, v(-113.58, -6.82) * mm, v(-113.58, -7.02) * mm, v(-113.58, -7.22) * mm]});
            skFitSpline(sketch, "E910", {"points": [v(-113.58, -7.22) * mm, v(-113.59, -7.47) * mm, v(-113.6, -7.72) * mm, v(-113.6, -7.98) * mm]});
            skFitSpline(sketch, "E911", {"points": [v(-113.6, -7.98) * mm, v(-113.6, -8.2) * mm, v(-113.6, -8.42) * mm, v(-113.6, -8.64) * mm]});
            skFitSpline(sketch, "E912", {"points": [v(-113.6, -8.64) * mm, v(-113.61, -9.26) * mm, v(-113.62, -9.87) * mm, v(-113.63, -10.49) * mm]});
            skFitSpline(sketch, "E913", {"points": [v(-113.63, -10.49) * mm, v(-113.63, -10.59) * mm, v(-113.64, -10.7) * mm, v(-113.67, -10.8) * mm]});
            skFitSpline(sketch, "E914", {"points": [v(-113.67, -10.8) * mm, v(-113.74, -11.01) * mm, v(-113.96, -11.14) * mm, v(-114.2, -11.1) * mm]});
            skFitSpline(sketch, "E915", {"points": [v(-114.2, -11.1) * mm, v(-114.42, -11.08) * mm, v(-114.6, -10.9) * mm, v(-114.6, -10.67) * mm]});
            skFitSpline(sketch, "E916", {"points": [v(-114.6, -10.67) * mm, v(-114.62, -10.51) * mm, v(-114.6, -10.35) * mm, v(-114.6, -10.2) * mm]});
            skFitSpline(sketch, "E917", {"points": [v(-114.6, -10.2) * mm, v(-114.59, -9.84) * mm, v(-114.57, -9.5) * mm, v(-114.57, -9.14) * mm]});
            skFitSpline(sketch, "E918", {"points": [v(-114.57, -9.14) * mm, v(-114.56, -9.04) * mm, v(-114.58, -8.93) * mm, v(-114.59, -8.83) * mm]});
            skFitSpline(sketch, "E919", {"points": [v(-114.59, -8.83) * mm, v(-115.02, -8.86) * mm, v(-115.45, -8.89) * mm, v(-115.9, -8.92) * mm]});
            skFitSpline(sketch, "E920", {"points": [v(-115.9, -8.92) * mm, v(-115.9, -9.08) * mm, v(-115.92, -9.23) * mm, v(-115.93, -9.4) * mm]});
            skFitSpline(sketch, "E921", {"points": [v(-115.93, -9.4) * mm, v(-115.94, -9.57) * mm, v(-115.94, -9.74) * mm, v(-115.96, -9.92) * mm]});
            skFitSpline(sketch, "E922", {"points": [v(-115.96, -9.92) * mm, v(-116.04, -10.48) * mm, v(-116.07, -11.04) * mm, v(-116.07, -11.6) * mm]});
            skFitSpline(sketch, "E923", {"points": [v(-116.07, -11.6) * mm, v(-116.07, -11.71) * mm, v(-116.06, -11.82) * mm, v(-116.07, -11.92) * mm]});
            skFitSpline(sketch, "E924", {"points": [v(-116.07, -11.92) * mm, v(-116.1, -12.2) * mm, v(-116.3, -12.4) * mm, v(-116.58, -12.38) * mm]});
            skFitSpline(sketch, "E925", {"points": [v(-116.58, -12.38) * mm, v(-116.85, -12.37) * mm, v(-117.02, -12.2) * mm, v(-117.03, -11.9) * mm]});
            skFitSpline(sketch, "E926", {"points": [v(-117.03, -11.9) * mm, v(-117.06, -11.22) * mm, v(-117, -10.55) * mm, v(-116.93, -9.87) * mm]});
            skFitSpline(sketch, "E927", {"points": [v(-116.93, -9.87) * mm, v(-116.93, -9.84) * mm, v(-116.93, -9.8) * mm, v(-116.93, -9.73) * mm]});
            skFitSpline(sketch, "E928", {"points": [v(-116.93, -9.73) * mm, v(-117.15, -9.96) * mm, v(-117.35, -10.16) * mm, v(-117.54, -10.37) * mm]});
            skFitSpline(sketch, "E929", {"points": [v(-117.54, -10.37) * mm, v(-117.9, -10.75) * mm, v(-118.26, -11.14) * mm, v(-118.62, -11.52) * mm]});
            skFitSpline(sketch, "E930", {"points": [v(-118.62, -11.52) * mm, v(-118.74, -11.65) * mm, v(-118.8, -11.77) * mm, v(-118.8, -11.96) * mm]});
            skFitSpline(sketch, "E931", {"points": [v(-118.8, -11.96) * mm, v(-118.75, -12.65) * mm, v(-118.7, -13.33) * mm, v(-118.54, -14) * mm]});
            skFitSpline(sketch, "E932", {"points": [v(-118.54, -14) * mm, v(-118.51, -14.12) * mm, v(-118.52, -14.27) * mm, v(-118.56, -14.4) * mm]});
            skFitSpline(sketch, "E933", {"points": [v(-118.56, -14.4) * mm, v(-118.62, -14.6) * mm, v(-118.83, -14.72) * mm, v(-119.02, -14.7) * mm]});
            skFitSpline(sketch, "E934", {"points": [v(-119.02, -14.7) * mm, v(-119.23, -14.7) * mm, v(-119.42, -14.53) * mm, v(-119.47, -14.33) * mm]});
            skFitSpline(sketch, "E935", {"points": [v(-119.47, -14.33) * mm, v(-119.6, -13.78) * mm, v(-119.68, -13.22) * mm, v(-119.72, -12.65) * mm]});
            skFitSpline(sketch, "E936", {"points": [v(-119.72, -12.65) * mm, v(-119.73, -12.38) * mm, v(-119.75, -12.11) * mm, v(-119.77, -11.82) * mm]});
            skFitSpline(sketch, "E937", {"points": [v(-119.77, -11.82) * mm, v(-119.88, -11.8) * mm, v(-119.98, -11.8) * mm, v(-120.08, -11.78) * mm]});
            skFitSpline(sketch, "E938", {"points": [v(-120.08, -11.78) * mm, v(-120.64, -11.73) * mm, v(-121.2, -11.68) * mm, v(-121.75, -11.62) * mm]});
            skFitSpline(sketch, "E939", {"points": [v(-121.75, -11.62) * mm, v(-121.94, -11.6) * mm, v(-122.13, -11.55) * mm, v(-122.3, -11.5) * mm]});
            skFitSpline(sketch, "E940", {"points": [v(-122.3, -11.5) * mm, v(-122.53, -11.44) * mm, v(-122.7, -11.2) * mm, v(-122.67, -11) * mm]});
            skFitSpline(sketch, "E941", {"points": [v(-122.67, -11) * mm, v(-122.63, -10.76) * mm, v(-122.45, -10.58) * mm, v(-122.22, -10.57) * mm]});
            skFitSpline(sketch, "E942", {"points": [v(-122.22, -10.57) * mm, v(-122.1, -10.56) * mm, v(-122, -10.57) * mm, v(-121.89, -10.6) * mm]});
            skFitSpline(sketch, "E943", {"points": [v(-121.89, -10.6) * mm, v(-121.27, -10.74) * mm, v(-120.64, -10.77) * mm, v(-120.01, -10.83) * mm]});
            skFitSpline(sketch, "E944", {"points": [v(-120.01, -10.83) * mm, v(-119.72, -10.86) * mm, v(-119.57, -10.74) * mm, v(-119.38, -10.56) * mm]});
            skFitSpline(sketch, "E945", {"points": [v(-119.38, -10.56) * mm, v(-119.06, -10.23) * mm, v(-118.7, -9.92) * mm, v(-118.37, -9.61) * mm]});
            skFitSpline(sketch, "E946", {"points": [v(-118.37, -9.61) * mm, v(-118.14, -9.4) * mm, v(-117.92, -9.19) * mm, v(-117.7, -8.98) * mm]});
            skFitSpline(sketch, "E947", {"points": [v(-117.7, -8.98) * mm, v(-118.3, -9.02) * mm, v(-118.9, -9.06) * mm, v(-119.49, -9.1) * mm]});
            skFitSpline(sketch, "E948", {"points": [v(-119.49, -9.1) * mm, v(-119.63, -9.1) * mm, v(-119.78, -9.08) * mm, v(-119.92, -9.07) * mm]});
            skFitSpline(sketch, "E949", {"points": [v(-119.92, -9.07) * mm, v(-120.16, -9.05) * mm, v(-120.33, -8.87) * mm, v(-120.34, -8.63) * mm]});
            skFitSpline(sketch, "E950", {"points": [v(-120.34, -8.63) * mm, v(-120.35, -8.37) * mm, v(-120.2, -8.17) * mm, v(-119.96, -8.13) * mm]});
            skFitSpline(sketch, "E951", {"points": [v(-119.96, -8.13) * mm, v(-119.89, -8.11) * mm, v(-119.82, -8.12) * mm, v(-119.74, -8.12) * mm]});
            skFitSpline(sketch, "E952", {"points": [v(-119.74, -8.12) * mm, v(-119.1, -8.1) * mm, v(-118.47, -8.08) * mm, v(-117.83, -8) * mm]});
            skFitSpline(sketch, "E953", {"points": [v(-117.83, -8) * mm, v(-117.53, -7.95) * mm, v(-117.21, -7.96) * mm, v(-116.88, -7.94) * mm]});
            skFitSpline(sketch, "E954", {"points": [v(-116.88, -7.94) * mm, v(-116.85, -7.5) * mm, v(-116.82, -7.08) * mm, v(-116.79, -6.63) * mm]});
            skFitSpline(sketch, "E955", {"points": [v(-116.79, -6.63) * mm, v(-116.92, -6.62) * mm, v(-117.06, -6.6) * mm, v(-117.2, -6.6) * mm]});
            skFitSpline(sketch, "E956", {"points": [v(-117.2, -6.6) * mm, v(-117.65, -6.61) * mm, v(-118.1, -6.64) * mm, v(-118.56, -6.65) * mm]});
            skFitSpline(sketch, "E957", {"points": [v(-118.56, -6.65) * mm, v(-118.86, -6.65) * mm, v(-119.06, -6.46) * mm, v(-119.07, -6.2) * mm]});
            skFitSpline(sketch, "E958", {"points": [v(-119.07, -6.2) * mm, v(-119.09, -5.92) * mm, v(-118.9, -5.72) * mm, v(-118.6, -5.69) * mm]});
            skFitSpline(sketch, "E959", {"points": [v(-118.6, -5.69) * mm, v(-118.47, -5.67) * mm, v(-118.34, -5.67) * mm, v(-118.2, -5.67) * mm]});
            skFitSpline(sketch, "E960", {"points": [v(-118.2, -5.67) * mm, v(-117.7, -5.66) * mm, v(-117.21, -5.65) * mm, v(-116.72, -5.64) * mm]});
            skFitSpline(sketch, "E961", {"points": [v(-116.72, -5.64) * mm, v(-116.05, -5.63) * mm, v(-115.38, -5.63) * mm, v(-114.7, -5.62) * mm]});
            skFitSpline(sketch, "E962", {"points": [v(-114.7, -5.62) * mm, v(-114.67, -5.62) * mm, v(-114.63, -5.61) * mm, v(-114.58, -5.6) * mm]});
            skLineSegment(sketch, "E963", {"start": v(-114.58, -5.6) * mm, "end": v(-114.58, -5.01) * mm});
            skFitSpline(sketch, "E964", {"points": [v(-114.58, -5.01) * mm, v(-114.83, -5) * mm, v(-115.08, -4.96) * mm, v(-115.33, -4.95) * mm]});
            skFitSpline(sketch, "E965", {"points": [v(-115.33, -4.95) * mm, v(-115.78, -4.94) * mm, v(-116.2, -4.83) * mm, v(-116.62, -4.72) * mm]});
            skFitSpline(sketch, "E966", {"points": [v(-116.62, -4.72) * mm, v(-116.8, -4.68) * mm, v(-116.92, -4.57) * mm, v(-116.98, -4.4) * mm]});
            skFitSpline(sketch, "E967", {"points": [v(-116.98, -4.4) * mm, v(-117.09, -4.1) * mm, v(-116.88, -3.78) * mm, v(-116.56, -3.77) * mm]});
            skFitSpline(sketch, "E968", {"points": [v(-116.56, -3.77) * mm, v(-116.42, -3.77) * mm, v(-116.27, -3.8) * mm, v(-116.13, -3.84) * mm]});
            skFitSpline(sketch, "E969", {"points": [v(-116.13, -3.84) * mm, v(-115.73, -3.97) * mm, v(-115.3, -3.98) * mm, v(-114.88, -4) * mm]});
            skFitSpline(sketch, "E970", {"points": [v(-114.88, -4) * mm, v(-114.77, -4.02) * mm, v(-114.67, -4.02) * mm, v(-114.54, -4.03) * mm]});
            skFitSpline(sketch, "E971", {"points": [v(-114.54, -4.03) * mm, v(-114.53, -3.77) * mm, v(-114.52, -3.54) * mm, v(-114.52, -3.31) * mm]});
            skFitSpline(sketch, "E972", {"points": [v(-114.52, -3.31) * mm, v(-114.51, -2.95) * mm, v(-114.52, -2.58) * mm, v(-114.51, -2.22) * mm]});
            skFitSpline(sketch, "E973", {"points": [v(-114.51, -2.22) * mm, v(-114.51, -2.11) * mm, v(-114.55, -2.04) * mm, v(-114.63, -1.97) * mm]});
            skFitSpline(sketch, "E974", {"points": [v(-114.63, -1.97) * mm, v(-114.93, -1.68) * mm, v(-115.24, -1.38) * mm, v(-115.54, -1.09) * mm]});
            skFitSpline(sketch, "E975", {"points": [v(-115.54, -1.09) * mm, v(-115.66, -0.98) * mm, v(-115.78, -0.87) * mm, v(-115.9, -0.75) * mm]});
            skFitSpline(sketch, "E976", {"points": [v(-115.9, -0.75) * mm, v(-115.95, -0.79) * mm, v(-116, -0.83) * mm, v(-116.04, -0.87) * mm]});
            skFitSpline(sketch, "E977", {"points": [v(-116.04, -0.87) * mm, v(-116.4, -1.29) * mm, v(-116.76, -1.7) * mm, v(-117.03, -2.2) * mm]});
            skFitSpline(sketch, "E978", {"points": [v(-117.03, -2.2) * mm, v(-117.17, -2.46) * mm, v(-117.42, -2.53) * mm, v(-117.66, -2.42) * mm]});
            skFitSpline(sketch, "E979", {"points": [v(-117.66, -2.42) * mm, v(-117.92, -2.3) * mm, v(-118.04, -2) * mm, v(-117.88, -1.74) * mm]});
            skFitSpline(sketch, "E980", {"points": [v(-117.88, -1.74) * mm, v(-117.68, -1.4) * mm, v(-117.46, -1.08) * mm, v(-117.23, -0.77) * mm]});
            skFitSpline(sketch, "E981", {"points": [v(-117.23, -0.77) * mm, v(-117.04, -0.52) * mm, v(-116.83, -0.3) * mm, v(-116.63, -0.07) * mm]});
            skFitSpline(sketch, "E982", {"points": [v(-116.63, -0.07) * mm, v(-116.78, 0.09) * mm, v(-116.9, 0.23) * mm, v(-117.04, 0.38) * mm]});
            skFitSpline(sketch, "E983", {"points": [v(-117.04, 0.38) * mm, v(-117.29, 0.14) * mm, v(-117.53, -0.09) * mm, v(-117.76, -0.32) * mm]});
            skFitSpline(sketch, "E984", {"points": [v(-117.76, -0.32) * mm, v(-118.28, -0.83) * mm, v(-118.8, -1.35) * mm, v(-119.33, -1.86) * mm]});
            skFitSpline(sketch, "E985", {"points": [v(-119.33, -1.86) * mm, v(-119.5, -2.03) * mm, v(-119.68, -2.19) * mm, v(-119.85, -2.35) * mm]});
            skFitSpline(sketch, "E986", {"points": [v(-119.85, -2.35) * mm, v(-120, -2.5) * mm, v(-120.17, -2.6) * mm, v(-120.39, -2.56) * mm]});
            skFitSpline(sketch, "E987", {"points": [v(-120.39, -2.56) * mm, v(-120.76, -2.47) * mm, v(-120.9, -2.03) * mm, v(-120.63, -1.75) * mm]});
            skFitSpline(sketch, "E988", {"points": [v(-120.63, -1.75) * mm, v(-120.43, -1.54) * mm, v(-120.21, -1.35) * mm, v(-120, -1.15) * mm]});
            skFitSpline(sketch, "E989", {"points": [v(-120, -1.15) * mm, v(-119.78, -0.94) * mm, v(-119.56, -0.72) * mm, v(-119.32, -0.5) * mm]});
            skFitSpline(sketch, "E990", {"points": [v(-119.32, -0.5) * mm, v(-119.66, -0.2) * mm, v(-119.98, 0.08) * mm, v(-120.31, 0.37) * mm]});
            skFitSpline(sketch, "E991", {"points": [v(-120.31, 0.37) * mm, v(-120.36, 0.33) * mm, v(-120.41, 0.3) * mm, v(-120.46, 0.25) * mm]});
            skFitSpline(sketch, "E992", {"points": [v(-120.46, 0.25) * mm, v(-121, -0.2) * mm, v(-121.52, -0.66) * mm, v(-122.05, -1.12) * mm]});
            skFitSpline(sketch, "E993", {"points": [v(-122.05, -1.12) * mm, v(-122.22, -1.27) * mm, v(-122.37, -1.44) * mm, v(-122.54, -1.59) * mm]});
            skFitSpline(sketch, "E994", {"points": [v(-122.54, -1.59) * mm, v(-122.7, -1.73) * mm, v(-122.87, -1.8) * mm, v(-123.08, -1.71) * mm]});
            skFitSpline(sketch, "E995", {"points": [v(-123.08, -1.71) * mm, v(-123.42, -1.57) * mm, v(-123.5, -1.19) * mm, v(-123.24, -0.92) * mm]});
            skFitSpline(sketch, "E996", {"points": [v(-123.24, -0.92) * mm, v(-122.96, -0.64) * mm, v(-122.67, -0.37) * mm, v(-122.37, -0.1) * mm]});
            skFitSpline(sketch, "E997", {"points": [v(-122.37, -0.1) * mm, v(-122.14, 0.11) * mm, v(-121.9, 0.3) * mm, v(-121.64, 0.53) * mm]});
            skFitSpline(sketch, "E998", {"points": [v(-121.64, 0.53) * mm, v(-121.71, 0.54) * mm, v(-121.76, 0.55) * mm, v(-121.8, 0.55) * mm]});
            skFitSpline(sketch, "E999", {"points": [v(-121.8, 0.55) * mm, v(-122.32, 0.53) * mm, v(-122.83, 0.52) * mm, v(-123.34, 0.5) * mm]});
            skFitSpline(sketch, "E1000", {"points": [v(-123.34, 0.5) * mm, v(-123.65, 0.49) * mm, v(-123.96, 0.47) * mm, v(-124.27, 0.45) * mm]});
            skFitSpline(sketch, "E1001", {"points": [v(-124.27, 0.45) * mm, v(-124.32, 0.44) * mm, v(-124.4, 0.41) * mm, v(-124.43, 0.37) * mm]});
            skFitSpline(sketch, "E1002", {"points": [v(-124.43, 0.37) * mm, v(-124.9, -0.17) * mm, v(-125.4, -0.7) * mm, v(-125.77, -1.32) * mm]});
            skFitSpline(sketch, "E1003", {"points": [v(-125.77, -1.32) * mm, v(-125.82, -1.4) * mm, v(-125.9, -1.49) * mm, v(-125.97, -1.55) * mm]});
            skFitSpline(sketch, "E1004", {"points": [v(-125.97, -1.55) * mm, v(-126.16, -1.7) * mm, v(-126.4, -1.7) * mm, v(-126.59, -1.53) * mm]});
            skFitSpline(sketch, "E1005", {"points": [v(-126.59, -1.53) * mm, v(-126.76, -1.38) * mm, v(-126.81, -1.13) * mm, v(-126.68, -0.93) * mm]});
            skFitSpline(sketch, "E1006", {"points": [v(-126.68, -0.93) * mm, v(-126.47, -0.6) * mm, v(-126.25, -0.29) * mm, v(-126.02, 0.01) * mm]});
            skFitSpline(sketch, "E1007", {"points": [v(-126.02, 0.01) * mm, v(-125.74, 0.37) * mm, v(-125.43, 0.71) * mm, v(-125.12, 1.08) * mm]});
            skFitSpline(sketch, "E1008", {"points": [v(-125.12, 1.08) * mm, v(-125.17, 1.14) * mm, v(-125.23, 1.2) * mm, v(-125.28, 1.27) * mm]});
            skFitSpline(sketch, "E1009", {"points": [v(-125.28, 1.27) * mm, v(-125.65, 1.73) * mm, v(-126.03, 2.18) * mm, v(-126.4, 2.65) * mm]});
            skFitSpline(sketch, "E1010", {"points": [v(-126.4, 2.65) * mm, v(-126.5, 2.78) * mm, v(-126.59, 2.92) * mm, v(-126.68, 3.07) * mm]});
            skFitSpline(sketch, "E1011", {"points": [v(-126.68, 3.07) * mm, v(-126.8, 3.28) * mm, v(-126.76, 3.54) * mm, v(-126.57, 3.7) * mm]});
            skFitSpline(sketch, "E1012", {"points": [v(-126.57, 3.7) * mm, v(-126.4, 3.84) * mm, v(-126.14, 3.85) * mm, v(-125.95, 3.7) * mm]});
            skFitSpline(sketch, "E1013", {"points": [v(-125.95, 3.7) * mm, v(-125.88, 3.63) * mm, v(-125.82, 3.55) * mm, v(-125.77, 3.47) * mm]});
            skFitSpline(sketch, "E1014", {"points": [v(-125.77, 3.47) * mm, v(-125.4, 2.85) * mm, v(-124.91, 2.32) * mm, v(-124.43, 1.79) * mm]});
            skFitSpline(sketch, "E1015", {"points": [v(-124.43, 1.79) * mm, v(-124.4, 1.74) * mm, v(-124.31, 1.7) * mm, v(-124.25, 1.7) * mm]});
            skFitSpline(sketch, "E1016", {"points": [v(-124.25, 1.7) * mm, v(-123.9, 1.68) * mm, v(-123.55, 1.67) * mm, v(-123.2, 1.65) * mm]});
            skFitSpline(sketch, "E1017", {"points": [v(-123.2, 1.65) * mm, v(-122.75, 1.63) * mm, v(-122.3, 1.62) * mm, v(-121.86, 1.6) * mm]});
            skFitSpline(sketch, "E1018", {"points": [v(-121.86, 1.6) * mm, v(-121.8, 1.6) * mm, v(-121.74, 1.6) * mm, v(-121.62, 1.6) * mm]});
            skFitSpline(sketch, "E1019", {"points": [v(-121.62, 1.6) * mm, v(-121.85, 1.8) * mm, v(-122.04, 1.95) * mm, v(-122.23, 2.12) * mm]});
            skFitSpline(sketch, "E1020", {"points": [v(-122.23, 2.12) * mm, v(-122.57, 2.43) * mm, v(-122.9, 2.75) * mm, v(-123.24, 3.07) * mm]});
            skFitSpline(sketch, "E1021", {"points": [v(-123.24, 3.07) * mm, v(-123.38, 3.2) * mm, v(-123.43, 3.36) * mm, v(-123.37, 3.55) * mm]});
            skFitSpline(sketch, "E1022", {"points": [v(-123.37, 3.55) * mm, v(-123.3, 3.75) * mm, v(-123.16, 3.86) * mm, v(-122.97, 3.9) * mm]});
            skFitSpline(sketch, "E1023", {"points": [v(-122.97, 3.9) * mm, v(-122.78, 3.93) * mm, v(-122.64, 3.83) * mm, v(-122.5, 3.7) * mm]});
            skFitSpline(sketch, "E1024", {"points": [v(-122.5, 3.7) * mm, v(-122.13, 3.36) * mm, v(-121.76, 3) * mm, v(-121.37, 2.67) * mm]});
            skFitSpline(sketch, "E1025", {"points": [v(-121.37, 2.67) * mm, v(-121.03, 2.37) * mm, v(-120.67, 2.09) * mm, v(-120.3, 1.79) * mm]});
            skFitSpline(sketch, "E1026", {"points": [v(-120.3, 1.79) * mm, v(-120, 2.06) * mm, v(-119.67, 2.34) * mm, v(-119.33, 2.64) * mm]});
            skFitSpline(sketch, "E1027", {"points": [v(-119.33, 2.64) * mm, v(-119.43, 2.74) * mm, v(-119.53, 2.85) * mm, v(-119.64, 2.96) * mm]});
            skFitSpline(sketch, "E1028", {"points": [v(-119.64, 2.96) * mm, v(-119.94, 3.24) * mm, v(-120.25, 3.52) * mm, v(-120.55, 3.8) * mm]});
            skFitSpline(sketch, "E1029", {"points": [v(-120.55, 3.8) * mm, v(-120.58, 3.84) * mm, v(-120.62, 3.87) * mm, v(-120.65, 3.91) * mm]});
            skFitSpline(sketch, "E1030", {"points": [v(-120.65, 3.91) * mm, v(-120.8, 4.1) * mm, v(-120.8, 4.37) * mm, v(-120.65, 4.55) * mm]});
            skFitSpline(sketch, "E1031", {"points": [v(-120.65, 4.55) * mm, v(-120.5, 4.73) * mm, v(-120.23, 4.78) * mm, v(-120.02, 4.63) * mm]});
            skFitSpline(sketch, "E1032", {"points": [v(-120.02, 4.63) * mm, v(-119.85, 4.5) * mm, v(-119.7, 4.36) * mm, v(-119.54, 4.21) * mm]});
            skFitSpline(sketch, "E1033", {"points": [v(-119.54, 4.21) * mm, v(-119.11, 3.8) * mm, v(-118.7, 3.4) * mm, v(-118.27, 3) * mm]});
            skFitSpline(sketch, "E1034", {"points": [v(-118.27, 3) * mm, v(-117.9, 2.64) * mm, v(-117.54, 2.27) * mm, v(-117.17, 1.9) * mm]});
            skFitSpline(sketch, "E1035", {"points": [v(-117.17, 1.9) * mm, v(-117.13, 1.86) * mm, v(-117.1, 1.82) * mm, v(-117.04, 1.77) * mm]});
            skFitSpline(sketch, "E1036", {"points": [v(-117.04, 1.77) * mm, v(-116.9, 1.92) * mm, v(-116.78, 2.06) * mm, v(-116.64, 2.22) * mm]});
            skFitSpline(sketch, "E1037", {"points": [v(-116.64, 2.22) * mm, v(-116.82, 2.43) * mm, v(-117.02, 2.65) * mm, v(-117.2, 2.88) * mm]});
            skFitSpline(sketch, "E1038", {"points": [v(-117.2, 2.88) * mm, v(-117.43, 3.2) * mm, v(-117.66, 3.53) * mm, v(-117.87, 3.87) * mm]});
            skFitSpline(sketch, "E1039", {"points": [v(-117.87, 3.87) * mm, v(-118.05, 4.17) * mm, v(-117.9, 4.5) * mm, v(-117.59, 4.6) * mm]});
            skFitSpline(sketch, "E1040", {"points": [v(-117.59, 4.6) * mm, v(-117.4, 4.66) * mm, v(-117.26, 4.6) * mm, v(-117.13, 4.47) * mm]});
            skFitSpline(sketch, "E1041", {"points": [v(-117.13, 4.47) * mm, v(-117.07, 4.42) * mm, v(-117.02, 4.35) * mm, v(-116.99, 4.28) * mm]});
            skFitSpline(sketch, "E1042", {"points": [v(-116.99, 4.28) * mm, v(-116.73, 3.79) * mm, v(-116.35, 3.39) * mm, v(-115.99, 2.97) * mm]});
            skFitSpline(sketch, "E1043", {"points": [v(-115.99, 2.97) * mm, v(-115.97, 2.94) * mm, v(-115.94, 2.92) * mm, v(-115.91, 2.9) * mm]});
            skFitSpline(sketch, "E1044", {"points": [v(-115.91, 2.9) * mm, v(-115.63, 3.15) * mm, v(-115.36, 3.4) * mm, v(-115.08, 3.66) * mm]});
            skFitSpline(sketch, "E1045", {"points": [v(-115.08, 3.66) * mm, v(-114.95, 3.79) * mm, v(-114.83, 3.93) * mm, v(-114.69, 4.04) * mm]});
            skFitSpline(sketch, "E1046", {"points": [v(-114.69, 4.04) * mm, v(-114.51, 4.19) * mm, v(-114.5, 4.38) * mm, v(-114.5, 4.58) * mm]});
            skFitSpline(sketch, "E1047", {"points": [v(-114.5, 4.58) * mm, v(-114.5, 5.02) * mm, v(-114.52, 5.46) * mm, v(-114.53, 5.9) * mm]});
            skFitSpline(sketch, "E1048", {"points": [v(-114.53, 5.9) * mm, v(-114.54, 5.98) * mm, v(-114.53, 6.07) * mm, v(-114.53, 6.18) * mm]});
            skFitSpline(sketch, "E1049", {"points": [v(-114.53, 6.18) * mm, v(-114.82, 6.16) * mm, v(-115.07, 6.16) * mm, v(-115.32, 6.12) * mm]});
            skFitSpline(sketch, "E1050", {"points": [v(-115.32, 6.12) * mm, v(-115.65, 6.08) * mm, v(-115.98, 6) * mm, v(-116.3, 5.95) * mm]});
            skFitSpline(sketch, "E1051", {"points": [v(-116.3, 5.95) * mm, v(-116.44, 5.93) * mm, v(-116.58, 5.92) * mm, v(-116.7, 5.95) * mm]});
            skFitSpline(sketch, "E1052", {"points": [v(-116.7, 5.95) * mm, v(-116.9, 6) * mm, v(-117, 6.17) * mm, v(-117.01, 6.37) * mm]});
            skFitSpline(sketch, "E1053", {"points": [v(-117.01, 6.37) * mm, v(-117.02, 6.56) * mm, v(-116.91, 6.75) * mm, v(-116.73, 6.83) * mm]});
            skFitSpline(sketch, "E1054", {"points": [v(-116.73, 6.83) * mm, v(-116.63, 6.87) * mm, v(-116.53, 6.9) * mm, v(-116.43, 6.92) * mm]});
            skFitSpline(sketch, "E1055", {"points": [v(-116.43, 6.92) * mm, v(-115.88, 7.09) * mm, v(-115.31, 7.09) * mm, v(-114.75, 7.14) * mm]});
            skFitSpline(sketch, "E1056", {"points": [v(-114.75, 7.14) * mm, v(-114.7, 7.15) * mm, v(-114.64, 7.16) * mm, v(-114.57, 7.17) * mm]});
            skLineSegment(sketch, "E1057", {"start": v(-114.57, 7.17) * mm, "end": v(-114.57, 7.76) * mm});
            skFitSpline(sketch, "E1058", {"points": [v(-114.57, 7.76) * mm, v(-114.8, 7.76) * mm, v(-115, 7.77) * mm, v(-115.22, 7.77) * mm]});
            skFitSpline(sketch, "E1059", {"points": [v(-115.22, 7.77) * mm, v(-116.03, 7.78) * mm, v(-116.84, 7.79) * mm, v(-117.66, 7.8) * mm]});
            skFitSpline(sketch, "E1060", {"points": [v(-117.66, 7.8) * mm, v(-117.94, 7.8) * mm, v(-118.21, 7.8) * mm, v(-118.5, 7.82) * mm]});
            skFitSpline(sketch, "E1061", {"points": [v(-118.5, 7.82) * mm, v(-118.56, 7.82) * mm, v(-118.62, 7.83) * mm, v(-118.68, 7.84) * mm]});
            skFitSpline(sketch, "E1062", {"points": [v(-118.68, 7.84) * mm, v(-118.94, 7.9) * mm, v(-119.1, 8.11) * mm, v(-119.07, 8.37) * mm]});
            skFitSpline(sketch, "E1063", {"points": [v(-119.07, 8.37) * mm, v(-119.05, 8.6) * mm, v(-118.86, 8.8) * mm, v(-118.6, 8.8) * mm]});
            skFitSpline(sketch, "E1064", {"points": [v(-118.6, 8.8) * mm, v(-118.28, 8.8) * mm, v(-117.95, 8.77) * mm, v(-117.63, 8.76) * mm]});
            skFitSpline(sketch, "E1065", {"points": [v(-117.63, 8.76) * mm, v(-117.35, 8.76) * mm, v(-117.07, 8.76) * mm, v(-116.79, 8.76) * mm]});
            skFitSpline(sketch, "E1066", {"points": [v(-116.79, 8.76) * mm, v(-116.82, 9.2) * mm, v(-116.85, 9.64) * mm, v(-116.88, 10.08) * mm]});
            skFitSpline(sketch, "E1067", {"points": [v(-116.88, 10.08) * mm, v(-117.02, 10.1) * mm, v(-117.14, 10.1) * mm, v(-117.27, 10.11) * mm]});
            skFitSpline(sketch, "E1068", {"points": [v(-117.27, 10.11) * mm, v(-118.12, 10.15) * mm, v(-118.97, 10.29) * mm, v(-119.83, 10.26) * mm]});
            skFitSpline(sketch, "E1069", {"points": [v(-119.83, 10.26) * mm, v(-120.15, 10.26) * mm, v(-120.34, 10.46) * mm, v(-120.34, 10.76) * mm]});
            skFitSpline(sketch, "E1070", {"points": [v(-120.34, 10.76) * mm, v(-120.33, 11.02) * mm, v(-120.17, 11.2) * mm, v(-119.9, 11.22) * mm]});
            skFitSpline(sketch, "E1071", {"points": [v(-119.9, 11.22) * mm, v(-119.64, 11.23) * mm, v(-119.37, 11.23) * mm, v(-119.1, 11.22) * mm]});
            skFitSpline(sketch, "E1072", {"points": [v(-119.1, 11.22) * mm, v(-118.64, 11.2) * mm, v(-118.18, 11.16) * mm, v(-117.71, 11.13) * mm]});
            skFitSpline(sketch, "E1073", {"points": [v(-117.71, 11.13) * mm, v(-117.72, 11.14) * mm, v(-117.72, 11.16) * mm, v(-117.73, 11.18) * mm]});
            skFitSpline(sketch, "E1074", {"points": [v(-117.73, 11.18) * mm, v(-118.15, 11.56) * mm, v(-118.56, 11.95) * mm, v(-118.98, 12.34) * mm]});
            skFitSpline(sketch, "E1075", {"points": [v(-118.98, 12.34) * mm, v(-119.18, 12.53) * mm, v(-119.39, 12.72) * mm, v(-119.6, 12.9) * mm]});
            skFitSpline(sketch, "E1076", {"points": [v(-119.6, 12.9) * mm, v(-119.64, 12.95) * mm, v(-119.72, 12.99) * mm, v(-119.78, 12.98) * mm]});
            skFitSpline(sketch, "E1077", {"points": [v(-119.78, 12.98) * mm, v(-120.3, 12.94) * mm, v(-120.83, 12.9) * mm, v(-121.35, 12.84) * mm]});
            skFitSpline(sketch, "E1078", {"points": [v(-121.35, 12.84) * mm, v(-121.54, 12.82) * mm, v(-121.73, 12.77) * mm, v(-121.92, 12.74) * mm]});
            skFitSpline(sketch, "E1079", {"points": [v(-121.92, 12.74) * mm, v(-122, 12.72) * mm, v(-122.1, 12.7) * mm, v(-122.18, 12.7) * mm]});
            skFitSpline(sketch, "E1080", {"points": [v(-122.18, 12.7) * mm, v(-122.45, 12.72) * mm, v(-122.66, 12.92) * mm, v(-122.67, 13.17) * mm]});
            skFitSpline(sketch, "E1081", {"points": [v(-122.67, 13.17) * mm, v(-122.68, 13.4) * mm, v(-122.5, 13.6) * mm, v(-122.26, 13.66) * mm]});
            skFitSpline(sketch, "E1082", {"points": [v(-122.26, 13.66) * mm, v(-121.71, 13.8) * mm, v(-121.16, 13.87) * mm, v(-120.6, 13.9) * mm]});
            skFitSpline(sketch, "E1083", {"points": [v(-120.6, 13.9) * mm, v(-120.33, 13.92) * mm, v(-120.06, 13.94) * mm, v(-119.78, 13.96) * mm]});
            skFitSpline(sketch, "E1084", {"points": [v(-119.78, 13.96) * mm, v(-119.77, 14.06) * mm, v(-119.75, 14.15) * mm, v(-119.75, 14.23) * mm]});
            skFitSpline(sketch, "E1085", {"points": [v(-119.75, 14.23) * mm, v(-119.74, 14.84) * mm, v(-119.67, 15.44) * mm, v(-119.57, 16.04) * mm]});
            skFitSpline(sketch, "E1086", {"points": [v(-119.57, 16.04) * mm, v(-119.54, 16.2) * mm, v(-119.5, 16.37) * mm, v(-119.46, 16.53) * mm]});
            skFitSpline(sketch, "E1087", {"points": [v(-119.46, 16.53) * mm, v(-119.4, 16.72) * mm, v(-119.17, 16.87) * mm, v(-118.97, 16.86) * mm]});
            skFitSpline(sketch, "E1088", {"points": [v(-118.97, 16.86) * mm, v(-118.75, 16.84) * mm, v(-118.55, 16.66) * mm, v(-118.52, 16.43) * mm]});
            skFitSpline(sketch, "E1089", {"points": [v(-118.52, 16.43) * mm, v(-118.51, 16.34) * mm, v(-118.51, 16.25) * mm, v(-118.53, 16.17) * mm]});
            skFitSpline(sketch, "E1090", {"points": [v(-118.53, 16.17) * mm, v(-118.71, 15.47) * mm, v(-118.76, 14.75) * mm, v(-118.8, 14.04) * mm]});
            skFitSpline(sketch, "E1091", {"points": [v(-118.8, 14.04) * mm, v(-118.8, 13.92) * mm, v(-118.78, 13.84) * mm, v(-118.7, 13.76) * mm]});
            skFitSpline(sketch, "E1092", {"points": [v(-118.7, 13.76) * mm, v(-118.24, 13.28) * mm, v(-117.8, 12.8) * mm, v(-117.34, 12.31) * mm]});
            skFitSpline(sketch, "E1093", {"points": [v(-117.34, 12.31) * mm, v(-117.21, 12.17) * mm, v(-117.08, 12.03) * mm, v(-116.93, 11.88) * mm]});
            skFitSpline(sketch, "E1094", {"points": [v(-116.93, 11.88) * mm, v(-116.95, 12.15) * mm, v(-116.97, 12.38) * mm, v(-116.98, 12.62) * mm]});
            skFitSpline(sketch, "E1095", {"points": [v(-116.98, 12.62) * mm, v(-117, 12.85) * mm, v(-117.02, 13.08) * mm, v(-117.03, 13.31) * mm]});
            skFitSpline(sketch, "E1096", {"points": [v(-117.03, 13.31) * mm, v(-117.03, 13.56) * mm, v(-117.03, 13.8) * mm, v(-117.03, 14.05) * mm]});
            skFitSpline(sketch, "E1097", {"points": [v(-117.03, 14.05) * mm, v(-117.02, 14.34) * mm, v(-116.85, 14.52) * mm, v(-116.58, 14.53) * mm]});
            skFitSpline(sketch, "E1098", {"points": [v(-116.58, 14.53) * mm, v(-116.3, 14.54) * mm, v(-116.1, 14.35) * mm, v(-116.07, 14.07) * mm]});
            skFitSpline(sketch, "E1099", {"points": [v(-116.07, 14.07) * mm, v(-116.07, 14) * mm, v(-116.07, 13.94) * mm, v(-116.07, 13.87) * mm]});
            skFitSpline(sketch, "E1100", {"points": [v(-116.07, 13.87) * mm, v(-116.07, 13.21) * mm, v(-116.04, 12.55) * mm, v(-115.94, 11.9) * mm]});
            skFitSpline(sketch, "E1101", {"points": [v(-115.94, 11.9) * mm, v(-115.9, 11.63) * mm, v(-115.91, 11.35) * mm, v(-115.9, 11.06) * mm]});
            skFitSpline(sketch, "E1102", {"points": [v(-115.9, 11.06) * mm, v(-115.46, 11.04) * mm, v(-115.04, 11) * mm, v(-114.6, 10.98) * mm]});
            skFitSpline(sketch, "E1103", {"points": [v(-114.6, 10.98) * mm, v(-114.6, 11.02) * mm, v(-114.58, 11.06) * mm, v(-114.58, 11.1) * mm]});
            skFitSpline(sketch, "E1104", {"points": [v(-114.58, 11.1) * mm, v(-114.58, 11.53) * mm, v(-114.6, 11.95) * mm, v(-114.6, 12.37) * mm]});
            skFitSpline(sketch, "E1105", {"points": [v(-114.6, 12.37) * mm, v(-114.6, 12.53) * mm, v(-114.62, 12.68) * mm, v(-114.6, 12.83) * mm]});
            skFitSpline(sketch, "E1106", {"points": [v(-114.6, 12.83) * mm, v(-114.59, 13.08) * mm, v(-114.39, 13.25) * mm, v(-114.15, 13.26) * mm]});
            skFitSpline(sketch, "E1107", {"points": [v(-114.15, 13.26) * mm, v(-113.9, 13.27) * mm, v(-113.7, 13.12) * mm, v(-113.66, 12.86) * mm]});
            skFitSpline(sketch, "E1108", {"points": [v(-113.66, 12.86) * mm, v(-113.63, 12.7) * mm, v(-113.63, 12.52) * mm, v(-113.62, 12.34) * mm]});
            skFitSpline(sketch, "E1109", {"points": [v(-113.62, 12.34) * mm, v(-113.61, 11.86) * mm, v(-113.61, 11.38) * mm, v(-113.6, 10.9) * mm]});
            skFitSpline(sketch, "E1110", {"points": [v(-113.6, 10.9) * mm, v(-113.6, 10.57) * mm, v(-113.58, 10.24) * mm, v(-113.58, 9.9) * mm]});
            skFitSpline(sketch, "E1111", {"points": [v(-113.58, 9.9) * mm, v(-113.57, 9.53) * mm, v(-113.58, 9.16) * mm, v(-113.58, 8.77) * mm]});
            skLineSegment(sketch, "E1112", {"start": v(-113.58, 8.77) * mm, "end": v(-112.98, 8.77) * mm});
            skFitSpline(sketch, "E1113", {"points": [v(-112.98, 8.77) * mm, v(-112.97, 8.83) * mm, v(-112.96, 8.9) * mm, v(-112.95, 8.97) * mm]});
            skFitSpline(sketch, "E1114", {"points": [v(-112.95, 8.97) * mm, v(-112.91, 9.36) * mm, v(-112.89, 9.76) * mm, v(-112.84, 10.16) * mm]});
            skFitSpline(sketch, "E1115", {"points": [v(-112.84, 10.16) * mm, v(-112.8, 10.4) * mm, v(-112.74, 10.63) * mm, v(-112.66, 10.85) * mm]});
            skFitSpline(sketch, "E1116", {"points": [v(-112.66, 10.85) * mm, v(-112.57, 11.15) * mm, v(-112.28, 11.28) * mm, v(-112.01, 11.16) * mm]});
            skFitSpline(sketch, "E1117", {"points": [v(-112.01, 11.16) * mm, v(-111.84, 11.08) * mm, v(-111.72, 10.95) * mm, v(-111.74, 10.75) * mm]});
            skFitSpline(sketch, "E1118", {"points": [v(-111.74, 10.75) * mm, v(-111.75, 10.58) * mm, v(-111.8, 10.4) * mm, v(-111.82, 10.23) * mm]});
            skFitSpline(sketch, "E1119", {"points": [v(-111.82, 10.23) * mm, v(-111.86, 9.96) * mm, v(-111.9, 9.68) * mm, v(-111.94, 9.4) * mm]});
            skFitSpline(sketch, "E1120", {"points": [v(-111.94, 9.4) * mm, v(-111.97, 9.2) * mm, v(-111.98, 8.98) * mm, v(-112, 8.74) * mm]});
            skFitSpline(sketch, "E1121", {"points": [v(-112, 8.74) * mm, v(-111.79, 8.73) * mm, v(-111.6, 8.72) * mm, v(-111.41, 8.71) * mm]});
            skFitSpline(sketch, "E1122", {"points": [v(-111.41, 8.71) * mm, v(-111, 8.7) * mm, v(-110.59, 8.7) * mm, v(-110.17, 8.7) * mm]});
            skFitSpline(sketch, "E1123", {"points": [v(-110.17, 8.7) * mm, v(-110.07, 8.7) * mm, v(-110, 8.73) * mm, v(-109.94, 8.8) * mm]});
            skFitSpline(sketch, "E1124", {"points": [v(-109.94, 8.8) * mm, v(-109.64, 9.11) * mm, v(-109.34, 9.42) * mm, v(-109.05, 9.74) * mm]});
            skFitSpline(sketch, "E1125", {"points": [v(-109.05, 9.74) * mm, v(-108.94, 9.85) * mm, v(-108.83, 9.97) * mm, v(-108.7, 10.1) * mm]});
            skFitSpline(sketch, "E1126", {"points": [v(-108.7, 10.1) * mm, v(-108.75, 10.14) * mm, v(-108.8, 10.2) * mm, v(-108.84, 10.23) * mm]});
            skFitSpline(sketch, "E1127", {"points": [v(-108.84, 10.23) * mm, v(-109.25, 10.59) * mm, v(-109.66, 10.94) * mm, v(-110.14, 11.2) * mm]});
            skFitSpline(sketch, "E1128", {"points": [v(-110.14, 11.2) * mm, v(-110.37, 11.33) * mm, v(-110.47, 11.54) * mm, v(-110.42, 11.74) * mm]});
            skFitSpline(sketch, "E1129", {"points": [v(-110.42, 11.74) * mm, v(-110.34, 12.08) * mm, v(-110, 12.24) * mm, v(-109.7, 12.06) * mm]});
            skFitSpline(sketch, "E1130", {"points": [v(-109.7, 12.06) * mm, v(-109.36, 11.87) * mm, v(-109.04, 11.64) * mm, v(-108.72, 11.41) * mm]});
            skFitSpline(sketch, "E1131", {"points": [v(-108.72, 11.41) * mm, v(-108.48, 11.23) * mm, v(-108.26, 11.02) * mm, v(-108.02, 10.81) * mm]});
            skFitSpline(sketch, "E1132", {"points": [v(-108.02, 10.81) * mm, v(-107.87, 10.95) * mm, v(-107.74, 11.1) * mm, v(-107.6, 11.23) * mm]});
            skFitSpline(sketch, "E1133", {"points": [v(-107.6, 11.23) * mm, v(-107.82, 11.48) * mm, v(-108.04, 11.7) * mm, v(-108.26, 11.94) * mm]});
            skFitSpline(sketch, "E1134", {"points": [v(-108.26, 11.94) * mm, v(-108.78, 12.47) * mm, v(-109.3, 13) * mm, v(-109.82, 13.53) * mm]});
            skFitSpline(sketch, "E1135", {"points": [v(-109.82, 13.53) * mm, v(-110, 13.7) * mm, v(-110.15, 13.87) * mm, v(-110.32, 14.05) * mm]});
            skFitSpline(sketch, "E1136", {"points": [v(-110.32, 14.05) * mm, v(-110.45, 14.18) * mm, v(-110.55, 14.34) * mm, v(-110.52, 14.54) * mm]});
            skFitSpline(sketch, "E1137", {"points": [v(-110.52, 14.54) * mm, v(-110.5, 14.72) * mm, v(-110.4, 14.87) * mm, v(-110.2, 14.93) * mm]});
            skFitSpline(sketch, "E1138", {"points": [v(-110.2, 14.93) * mm, v(-110.02, 15) * mm, v(-109.84, 14.96) * mm, v(-109.7, 14.82) * mm]});
            skFitSpline(sketch, "E1139", {"points": [v(-109.7, 14.82) * mm, v(-109.5, 14.61) * mm, v(-109.3, 14.4) * mm, v(-109.1, 14.19) * mm]});
            skFitSpline(sketch, "E1140", {"points": [v(-109.1, 14.19) * mm, v(-108.9, 13.96) * mm, v(-108.68, 13.74) * mm, v(-108.46, 13.51) * mm]});
            skFitSpline(sketch, "E1141", {"points": [v(-108.46, 13.51) * mm, v(-108.16, 13.86) * mm, v(-107.87, 14.18) * mm, v(-107.6, 14.5) * mm]});
            skFitSpline(sketch, "E1142", {"points": [v(-107.6, 14.5) * mm, v(-107.61, 14.53) * mm, v(-107.62, 14.55) * mm, v(-107.64, 14.57) * mm]});
            skFitSpline(sketch, "E1143", {"points": [v(-107.64, 14.57) * mm, v(-108.13, 15.15) * mm, v(-108.62, 15.72) * mm, v(-109.12, 16.3) * mm]});
            skFitSpline(sketch, "E1144", {"points": [v(-109.12, 16.3) * mm, v(-109.26, 16.45) * mm, v(-109.42, 16.59) * mm, v(-109.56, 16.74) * mm]});
            skFitSpline(sketch, "E1145", {"points": [v(-109.56, 16.74) * mm, v(-109.7, 16.89) * mm, v(-109.77, 17.06) * mm, v(-109.68, 17.27) * mm]});
            skFitSpline(sketch, "E1146", {"points": [v(-109.68, 17.27) * mm, v(-109.53, 17.6) * mm, v(-109.15, 17.7) * mm, v(-108.89, 17.44) * mm]});
            skFitSpline(sketch, "E1147", {"points": [v(-108.89, 17.44) * mm, v(-108.6, 17.16) * mm, v(-108.34, 16.88) * mm, v(-108.08, 16.59) * mm]});
            skFitSpline(sketch, "E1148", {"points": [v(-108.08, 16.59) * mm, v(-107.86, 16.35) * mm, v(-107.66, 16.1) * mm, v(-107.44, 15.84) * mm]});
            skFitSpline(sketch, "E1149", {"points": [v(-107.44, 15.84) * mm, v(-107.43, 15.9) * mm, v(-107.42, 15.96) * mm, v(-107.42, 16) * mm]});
            skFitSpline(sketch, "E1150", {"points": [v(-107.42, 16) * mm, v(-107.43, 16.53) * mm, v(-107.45, 17.04) * mm, v(-107.47, 17.56) * mm]});
            skFitSpline(sketch, "E1151", {"points": [v(-107.47, 17.56) * mm, v(-107.48, 17.86) * mm, v(-107.5, 18.15) * mm, v(-107.51, 18.44) * mm]});
            skFitSpline(sketch, "E1152", {"points": [v(-107.51, 18.44) * mm, v(-107.51, 18.53) * mm, v(-107.55, 18.59) * mm, v(-107.61, 18.64) * mm]});
            skFitSpline(sketch, "E1153", {"points": [v(-107.61, 18.64) * mm, v(-108.06, 19.01) * mm, v(-108.51, 19.39) * mm, v(-108.96, 19.75) * mm]});
            skFitSpline(sketch, "E1154", {"points": [v(-108.96, 19.75) * mm, v(-109.04, 19.81) * mm, v(-109.13, 19.86) * mm, v(-109.2, 19.91) * mm]});
            skFitSpline(sketch, "E1155", {"points": [v(-109.2, 19.91) * mm, v(-109.3, 19.98) * mm, v(-109.4, 20.04) * mm, v(-109.49, 20.13) * mm]});
            skFitSpline(sketch, "E1156", {"points": [v(-109.49, 20.13) * mm, v(-109.66, 20.32) * mm, v(-109.66, 20.57) * mm, v(-109.5, 20.76) * mm]});
            skFitSpline(sketch, "E1157", {"points": [v(-109.5, 20.76) * mm, v(-109.35, 20.95) * mm, v(-109.09, 21) * mm, v(-108.88, 20.86) * mm]});
            skFitSpline(sketch, "E1158", {"points": [v(-108.88, 20.86) * mm, v(-108.58, 20.67) * mm, v(-108.28, 20.47) * mm, v(-108, 20.25) * mm]});
            skFitSpline(sketch, "E1159", {"points": [v(-108, 20.25) * mm, v(-107.68, 20) * mm, v(-107.39, 19.73) * mm, v(-107.08, 19.47) * mm]});
            skFitSpline(sketch, "E1160", {"points": [v(-107.08, 19.47) * mm, v(-107.02, 19.42) * mm, v(-106.96, 19.37) * mm, v(-106.89, 19.31) * mm]});
            skFitSpline(sketch, "E1161", {"points": [v(-106.89, 19.31) * mm, v(-106.82, 19.36) * mm, v(-106.76, 19.4) * mm, v(-106.7, 19.46) * mm]});
            skFitSpline(sketch, "E1162", {"points": [v(-106.7, 19.46) * mm, v(-106.25, 19.83) * mm, v(-105.8, 20.2) * mm, v(-105.35, 20.57) * mm]});
            skFitSpline(sketch, "E1163", {"points": [v(-105.35, 20.57) * mm, v(-105.2, 20.68) * mm, v(-105.04, 20.77) * mm, v(-104.89, 20.87) * mm]});
            skFitSpline(sketch, "E1164", {"points": [v(-104.89, 20.87) * mm, v(-104.68, 21) * mm, v(-104.43, 20.95) * mm, v(-104.28, 20.77) * mm]});
            skFitSpline(sketch, "E1165", {"points": [v(-104.28, 20.77) * mm, v(-104.12, 20.6) * mm, v(-104.11, 20.33) * mm, v(-104.27, 20.14) * mm]});
            skFitSpline(sketch, "E1166", {"points": [v(-104.27, 20.14) * mm, v(-104.33, 20.07) * mm, v(-104.4, 20.01) * mm, v(-104.47, 19.97) * mm]});
            skFitSpline(sketch, "E1167", {"points": [v(-104.47, 19.97) * mm, v(-105.1, 19.6) * mm, v(-105.63, 19.11) * mm, v(-106.17, 18.64) * mm]});
            skFitSpline(sketch, "E1168", {"points": [v(-106.17, 18.64) * mm, v(-106.25, 18.56) * mm, v(-106.27, 18.48) * mm, v(-106.27, 18.38) * mm]});
            skFitSpline(sketch, "E1169", {"points": [v(-106.27, 18.38) * mm, v(-106.29, 17.72) * mm, v(-106.3, 17.06) * mm, v(-106.33, 16.4) * mm]});
            skFitSpline(sketch, "E1170", {"points": [v(-106.33, 16.4) * mm, v(-106.34, 16.22) * mm, v(-106.35, 16.04) * mm, v(-106.37, 15.8) * mm]});
            skFitSpline(sketch, "E1171", {"points": [v(-106.37, 15.8) * mm, v(-106.17, 16.03) * mm, v(-106.01, 16.23) * mm, v(-105.84, 16.41) * mm]});
            skFitSpline(sketch, "E1172", {"points": [v(-105.84, 16.41) * mm, v(-105.53, 16.76) * mm, v(-105.22, 17.1) * mm, v(-104.9, 17.43) * mm]});
            skFitSpline(sketch, "E1173", {"points": [v(-104.9, 17.43) * mm, v(-104.68, 17.64) * mm, v(-104.38, 17.63) * mm, v(-104.2, 17.42) * mm]});
            skFitSpline(sketch, "E1174", {"points": [v(-104.2, 17.42) * mm, v(-104, 17.22) * mm, v(-104.02, 16.95) * mm, v(-104.22, 16.73) * mm]});
            skFitSpline(sketch, "E1175", {"points": [v(-104.22, 16.73) * mm, v(-104.4, 16.53) * mm, v(-104.6, 16.34) * mm, v(-104.78, 16.14) * mm]});
            skFitSpline(sketch, "E1176", {"points": [v(-104.78, 16.14) * mm, v(-105.05, 15.83) * mm, v(-105.3, 15.51) * mm, v(-105.57, 15.2) * mm]});
            skFitSpline(sketch, "E1177", {"points": [v(-105.57, 15.2) * mm, v(-105.77, 14.97) * mm, v(-105.97, 14.75) * mm, v(-106.18, 14.5) * mm]});
            skFitSpline(sketch, "E1178", {"points": [v(-106.18, 14.5) * mm, v(-105.9, 14.19) * mm, v(-105.62, 13.86) * mm, v(-105.32, 13.51) * mm]});
            skFitSpline(sketch, "E1179", {"points": [v(-105.32, 13.51) * mm, v(-105.1, 13.74) * mm, v(-104.88, 13.97) * mm, v(-104.66, 14.2) * mm]});
            skFitSpline(sketch, "E1180", {"points": [v(-104.66, 14.2) * mm, v(-104.46, 14.4) * mm, v(-104.28, 14.6) * mm, v(-104.08, 14.8) * mm]});
            skFitSpline(sketch, "E1181", {"points": [v(-104.08, 14.8) * mm, v(-103.96, 14.93) * mm, v(-103.82, 14.97) * mm, v(-103.65, 14.95) * mm]});
            skFitSpline(sketch, "E1182", {"points": [v(-103.65, 14.95) * mm, v(-103.3, 14.9) * mm, v(-103.13, 14.5) * mm, v(-103.34, 14.2) * mm]});
            skFitSpline(sketch, "E1183", {"points": [v(-103.34, 14.2) * mm, v(-103.45, 14.03) * mm, v(-103.6, 13.89) * mm, v(-103.73, 13.74) * mm]});
            skFitSpline(sketch, "E1184", {"points": [v(-103.73, 13.74) * mm, v(-104.15, 13.3) * mm, v(-104.56, 12.87) * mm, v(-104.98, 12.45) * mm]});
            skFitSpline(sketch, "E1185", {"points": [v(-104.98, 12.45) * mm, v(-105.37, 12.05) * mm, v(-105.77, 11.66) * mm, v(-106.18, 11.24) * mm]});
            skFitSpline(sketch, "E1186", {"points": [v(-106.18, 11.24) * mm, v(-106.05, 11.1) * mm, v(-105.91, 10.96) * mm, v(-105.76, 10.8) * mm]});
            skFitSpline(sketch, "E1187", {"points": [v(-105.76, 10.8) * mm, v(-105.54, 11) * mm, v(-105.33, 11.16) * mm, v(-105.12, 11.35) * mm]});
            skFitSpline(sketch, "E1188", {"points": [v(-105.12, 11.35) * mm, v(-104.82, 11.64) * mm, v(-104.47, 11.84) * mm, v(-104.12, 12.05) * mm]});
            skFitSpline(sketch, "E1189", {"points": [v(-104.12, 12.05) * mm, v(-103.84, 12.2) * mm, v(-103.55, 12.14) * mm, v(-103.4, 11.9) * mm]});
            skFitSpline(sketch, "E1190", {"points": [v(-103.4, 11.9) * mm, v(-103.27, 11.65) * mm, v(-103.34, 11.37) * mm, v(-103.62, 11.22) * mm]});
            skFitSpline(sketch, "E1191", {"points": [v(-103.62, 11.22) * mm, v(-104.1, 10.95) * mm, v(-104.51, 10.6) * mm, v(-104.92, 10.24) * mm]});
            skFitSpline(sketch, "E1192", {"points": [v(-104.92, 10.24) * mm, v(-104.97, 10.2) * mm, v(-105.01, 10.16) * mm, v(-105.07, 10.1) * mm]});
            skFitSpline(sketch, "E1193", {"points": [v(-105.07, 10.1) * mm, v(-104.96, 9.98) * mm, v(-104.85, 9.87) * mm, v(-104.74, 9.75) * mm]});
            skFitSpline(sketch, "E1194", {"points": [v(-104.74, 9.75) * mm, v(-104.47, 9.47) * mm, v(-104.2, 9.19) * mm, v(-103.94, 8.9) * mm]});
            skFitSpline(sketch, "E1195", {"points": [v(-103.94, 8.9) * mm, v(-103.78, 8.72) * mm, v(-103.6, 8.68) * mm, v(-103.38, 8.68) * mm]});
            skFitSpline(sketch, "E1196", {"points": [v(-103.38, 8.68) * mm, v(-102.9, 8.7) * mm, v(-102.43, 8.71) * mm, v(-101.95, 8.73) * mm]});
            skFitSpline(sketch, "E1197", {"points": [v(-101.95, 8.73) * mm, v(-101.9, 8.73) * mm, v(-101.85, 8.73) * mm, v(-101.78, 8.74) * mm]});
            skFitSpline(sketch, "E1198", {"points": [v(-101.78, 8.74) * mm, v(-101.79, 8.85) * mm, v(-101.8, 8.96) * mm, v(-101.8, 9.07) * mm]});
            skFitSpline(sketch, "E1199", {"points": [v(-101.8, 9.07) * mm, v(-101.83, 9.5) * mm, v(-101.85, 9.94) * mm, v(-101.98, 10.37) * mm]});
            skFitSpline(sketch, "E1200", {"points": [v(-101.98, 10.37) * mm, v(-102.02, 10.48) * mm, v(-102.04, 10.6) * mm, v(-102.04, 10.72) * mm]});
            skFitSpline(sketch, "E1201", {"points": [v(-102.04, 10.72) * mm, v(-102.05, 10.94) * mm, v(-101.9, 11.13) * mm, v(-101.7, 11.18) * mm]});
            skFitSpline(sketch, "E1202", {"points": [v(-101.7, 11.18) * mm, v(-101.48, 11.24) * mm, v(-101.25, 11.15) * mm, v(-101.15, 10.95) * mm]});
            skFitSpline(sketch, "E1203", {"points": [v(-101.15, 10.95) * mm, v(-101.1, 10.87) * mm, v(-101.08, 10.79) * mm, v(-101.06, 10.7) * mm]});
            skFitSpline(sketch, "E1204", {"points": [v(-101.06, 10.7) * mm, v(-100.93, 10.24) * mm, v(-100.87, 9.76) * mm, v(-100.85, 9.29) * mm]});
            skFitSpline(sketch, "E1205", {"points": [v(-100.85, 9.29) * mm, v(-100.84, 9.12) * mm, v(-100.82, 8.95) * mm, v(-100.8, 8.77) * mm]});
            skLineSegment(sketch, "E1206", {"start": v(-100.8, 8.77) * mm, "end": v(-100.19, 8.77) * mm});
            skFitSpline(sketch, "E1207", {"points": [v(-100.19, 8.77) * mm, v(-100.19, 8.97) * mm, v(-100.19, 9.15) * mm, v(-100.19, 9.34) * mm]});
            skFitSpline(sketch, "E1208", {"points": [v(-100.19, 9.34) * mm, v(-100.18, 10.05) * mm, v(-100.18, 10.75) * mm, v(-100.17, 11.45) * mm]});
            skFitSpline(sketch, "E1209", {"points": [v(-100.17, 11.45) * mm, v(-100.17, 11.87) * mm, v(-100.15, 12.3) * mm, v(-100.14, 12.72) * mm]});
            skFitSpline(sketch, "E1210", {"points": [v(-100.14, 12.72) * mm, v(-100.12, 13.06) * mm, v(-99.92, 13.27) * mm, v(-99.63, 13.26) * mm]});
            skFitSpline(sketch, "E1211", {"points": [v(-99.63, 13.26) * mm, v(-99.38, 13.26) * mm, v(-99.17, 13.08) * mm, v(-99.17, 12.83) * mm]});
            skFitSpline(sketch, "E1212", {"points": [v(-99.17, 12.83) * mm, v(-99.17, 12.49) * mm, v(-99.2, 12.14) * mm, v(-99.2, 11.8) * mm]});
            skFitSpline(sketch, "E1213", {"points": [v(-99.2, 11.8) * mm, v(-99.2, 11.53) * mm, v(-99.2, 11.26) * mm, v(-99.2, 10.98) * mm]});
            skFitSpline(sketch, "E1214", {"points": [v(-99.2, 10.98) * mm, v(-98.76, 11) * mm, v(-98.33, 11.03) * mm, v(-97.89, 11.06) * mm]});
            skFitSpline(sketch, "E1215", {"points": [v(-97.89, 11.06) * mm, v(-97.87, 11.21) * mm, v(-97.85, 11.35) * mm, v(-97.84, 11.5) * mm]});
            skFitSpline(sketch, "E1216", {"points": [v(-97.84, 11.5) * mm, v(-97.8, 11.95) * mm, v(-97.76, 12.4) * mm, v(-97.74, 12.85) * mm]});
            skFitSpline(sketch, "E1217", {"points": [v(-97.74, 12.85) * mm, v(-97.71, 13.25) * mm, v(-97.7, 13.65) * mm, v(-97.7, 14.05) * mm]});
            skFitSpline(sketch, "E1218", {"points": [v(-97.7, 14.05) * mm, v(-97.68, 14.36) * mm, v(-97.47, 14.55) * mm, v(-97.16, 14.53) * mm]});
            skFitSpline(sketch, "E1219", {"points": [v(-97.16, 14.53) * mm, v(-96.94, 14.51) * mm, v(-96.74, 14.34) * mm, v(-96.74, 14.12) * mm]});
            skFitSpline(sketch, "E1220", {"points": [v(-96.74, 14.12) * mm, v(-96.73, 13.8) * mm, v(-96.75, 13.48) * mm, v(-96.76, 13.16) * mm]});
            skFitSpline(sketch, "E1221", {"points": [v(-96.76, 13.16) * mm, v(-96.76, 13) * mm, v(-96.77, 12.83) * mm, v(-96.78, 12.66) * mm]});
            skFitSpline(sketch, "E1222", {"points": [v(-96.78, 12.66) * mm, v(-96.8, 12.4) * mm, v(-96.82, 12.15) * mm, v(-96.84, 11.88) * mm]});
            skFitSpline(sketch, "E1223", {"points": [v(-96.84, 11.88) * mm, v(-96.8, 11.91) * mm, v(-96.78, 11.93) * mm, v(-96.75, 11.96) * mm]});
            skFitSpline(sketch, "E1224", {"points": [v(-96.75, 11.96) * mm, v(-96.38, 12.36) * mm, v(-96, 12.76) * mm, v(-95.62, 13.17) * mm]});
            skFitSpline(sketch, "E1225", {"points": [v(-95.62, 13.17) * mm, v(-95.43, 13.38) * mm, v(-95.23, 13.59) * mm, v(-95.04, 13.8) * mm]});
            skFitSpline(sketch, "E1226", {"points": [v(-95.04, 13.8) * mm, v(-95, 13.85) * mm, v(-94.97, 13.93) * mm, v(-94.97, 13.99) * mm]});
            skFitSpline(sketch, "E1227", {"points": [v(-94.97, 13.99) * mm, v(-95, 14.35) * mm, v(-95.01, 14.72) * mm, v(-95.06, 15.08) * mm]});
            skFitSpline(sketch, "E1228", {"points": [v(-95.06, 15.08) * mm, v(-95.1, 15.4) * mm, v(-95.16, 15.73) * mm, v(-95.21, 16.05) * mm]});
            skFitSpline(sketch, "E1229", {"points": [v(-95.21, 16.05) * mm, v(-95.23, 16.16) * mm, v(-95.25, 16.27) * mm, v(-95.24, 16.38) * mm]});
            skFitSpline(sketch, "E1230", {"points": [v(-95.24, 16.38) * mm, v(-95.24, 16.63) * mm, v(-95.06, 16.82) * mm, v(-94.82, 16.86) * mm]});
            skFitSpline(sketch, "E1231", {"points": [v(-94.82, 16.86) * mm, v(-94.6, 16.88) * mm, v(-94.34, 16.71) * mm, v(-94.3, 16.48) * mm]});
            skFitSpline(sketch, "E1232", {"points": [v(-94.3, 16.48) * mm, v(-94.22, 16) * mm, v(-94.14, 15.54) * mm, v(-94.08, 15.06) * mm]});
            skFitSpline(sketch, "E1233", {"points": [v(-94.08, 15.06) * mm, v(-94.04, 14.7) * mm, v(-94.02, 14.35) * mm, v(-94, 13.98) * mm]});
            skFitSpline(sketch, "E1234", {"points": [v(-94, 13.98) * mm, v(-93.9, 13.96) * mm, v(-93.82, 13.94) * mm, v(-93.74, 13.94) * mm]});
            skFitSpline(sketch, "E1235", {"points": [v(-93.74, 13.94) * mm, v(-93.37, 13.9) * mm, v(-93, 13.9) * mm, v(-92.64, 13.85) * mm]});
            skFitSpline(sketch, "E1236", {"points": [v(-92.64, 13.85) * mm, v(-92.24, 13.8) * mm, v(-91.85, 13.73) * mm, v(-91.46, 13.65) * mm]});
            skFitSpline(sketch, "E1237", {"points": [v(-91.46, 13.65) * mm, v(-91.24, 13.6) * mm, v(-91.1, 13.38) * mm, v(-91.1, 13.17) * mm]});
            skFitSpline(sketch, "E1238", {"points": [v(-91.1, 13.17) * mm, v(-91.12, 12.95) * mm, v(-91.27, 12.76) * mm, v(-91.48, 12.73) * mm]});
            skFitSpline(sketch, "E1239", {"points": [v(-91.48, 12.73) * mm, v(-91.6, 12.7) * mm, v(-91.72, 12.7) * mm, v(-91.84, 12.74) * mm]});
            skFitSpline(sketch, "E1240", {"points": [v(-91.84, 12.74) * mm, v(-92.32, 12.85) * mm, v(-92.81, 12.9) * mm, v(-93.3, 12.94) * mm]});
            skFitSpline(sketch, "E1241", {"points": [v(-93.3, 12.94) * mm, v(-93.53, 12.96) * mm, v(-93.75, 12.98) * mm, v(-93.97, 12.98) * mm]});
            skFitSpline(sketch, "E1242", {"points": [v(-93.97, 12.98) * mm, v(-94.04, 12.98) * mm, v(-94.13, 12.95) * mm, v(-94.18, 12.9) * mm]});
            skFitSpline(sketch, "E1243", {"points": [v(-94.18, 12.9) * mm, v(-94.44, 12.67) * mm, v(-94.7, 12.43) * mm, v(-94.96, 12.19) * mm]});
            skFitSpline(sketch, "E1244", {"points": [v(-94.96, 12.19) * mm, v(-95.33, 11.84) * mm, v(-95.7, 11.49) * mm, v(-96.08, 11.12) * mm]});
            skFitSpline(sketch, "E1245", {"points": [v(-96.08, 11.12) * mm, v(-95.8, 11.14) * mm, v(-95.55, 11.16) * mm, v(-95.3, 11.18) * mm]});
            skFitSpline(sketch, "E1246", {"points": [v(-95.3, 11.18) * mm, v(-94.83, 11.2) * mm, v(-94.36, 11.26) * mm, v(-93.89, 11.22) * mm]});
            skFitSpline(sketch, "E1247", {"points": [v(-93.89, 11.22) * mm, v(-93.63, 11.2) * mm, v(-93.44, 11.04) * mm, v(-93.42, 10.8) * mm]});
            skFitSpline(sketch, "E1248", {"points": [v(-93.42, 10.8) * mm, v(-93.4, 10.54) * mm, v(-93.57, 10.32) * mm, v(-93.82, 10.27) * mm]});
            skFitSpline(sketch, "E1249", {"points": [v(-93.82, 10.27) * mm, v(-93.9, 10.26) * mm, v(-93.98, 10.26) * mm, v(-94.06, 10.26) * mm]});
            skFitSpline(sketch, "E1250", {"points": [v(-94.06, 10.26) * mm, v(-94.71, 10.25) * mm, v(-95.37, 10.23) * mm, v(-96.02, 10.13) * mm]});
            skFitSpline(sketch, "E1251", {"points": [v(-96.02, 10.13) * mm, v(-96.3, 10.1) * mm, v(-96.59, 10.1) * mm, v(-96.9, 10.09) * mm]});
            skFitSpline(sketch, "E1252", {"points": [v(-96.9, 10.09) * mm, v(-96.92, 9.65) * mm, v(-96.95, 9.21) * mm, v(-96.98, 8.76) * mm]});
            skFitSpline(sketch, "E1253", {"points": [v(-96.98, 8.76) * mm, v(-96.7, 8.76) * mm, v(-96.42, 8.76) * mm, v(-96.14, 8.76) * mm]});
            skFitSpline(sketch, "E1254", {"points": [v(-96.14, 8.76) * mm, v(-95.83, 8.77) * mm, v(-95.51, 8.8) * mm, v(-95.2, 8.8) * mm]});
            skFitSpline(sketch, "E1255", {"points": [v(-95.2, 8.8) * mm, v(-94.92, 8.8) * mm, v(-94.73, 8.63) * mm, v(-94.7, 8.38) * mm]});
            skFitSpline(sketch, "E1256", {"points": [v(-94.7, 8.38) * mm, v(-94.68, 8.1) * mm, v(-94.83, 7.9) * mm, v(-95.12, 7.84) * mm]});
            skFitSpline(sketch, "E1257", {"points": [v(-95.12, 7.84) * mm, v(-95.23, 7.82) * mm, v(-95.34, 7.83) * mm, v(-95.45, 7.82) * mm]});
            skFitSpline(sketch, "E1258", {"points": [v(-95.45, 7.82) * mm, v(-95.99, 7.81) * mm, v(-96.52, 7.8) * mm, v(-97.06, 7.8) * mm]});
            skFitSpline(sketch, "E1259", {"points": [v(-97.06, 7.8) * mm, v(-97.39, 7.79) * mm, v(-97.71, 7.77) * mm, v(-98.04, 7.77) * mm]});
            skFitSpline(sketch, "E1260", {"points": [v(-98.04, 7.77) * mm, v(-98.36, 7.76) * mm, v(-98.69, 7.77) * mm, v(-99.01, 7.76) * mm]});
            skFitSpline(sketch, "E1261", {"points": [v(-99.01, 7.76) * mm, v(-99.07, 7.76) * mm, v(-99.12, 7.76) * mm, v(-99.2, 7.75) * mm]});
            skLineSegment(sketch, "E1262", {"start": v(-99.2, 7.75) * mm, "end": v(-99.2, 7.16) * mm});
            skFitSpline(sketch, "E1263", {"points": [v(-99.2, 7.16) * mm, v(-98.96, 7.14) * mm, v(-98.73, 7.1) * mm, v(-98.5, 7.1) * mm]});
            skFitSpline(sketch, "E1264", {"points": [v(-98.5, 7.1) * mm, v(-98.04, 7.1) * mm, v(-97.6, 7) * mm, v(-97.17, 6.88) * mm]});
            skFitSpline(sketch, "E1265", {"points": [v(-97.17, 6.88) * mm, v(-96.88, 6.8) * mm, v(-96.73, 6.6) * mm, v(-96.77, 6.31) * mm]});
            skFitSpline(sketch, "E1266", {"points": [v(-96.77, 6.31) * mm, v(-96.8, 6.1) * mm, v(-96.97, 5.92) * mm, v(-97.19, 5.93) * mm]});
            skFitSpline(sketch, "E1267", {"points": [v(-97.19, 5.93) * mm, v(-97.36, 5.93) * mm, v(-97.54, 5.96) * mm, v(-97.7, 6) * mm]});
            skFitSpline(sketch, "E1268", {"points": [v(-97.7, 6) * mm, v(-98.2, 6.15) * mm, v(-98.7, 6.13) * mm, v(-99.2, 6.18) * mm]});
            skFitSpline(sketch, "E1269", {"points": [v(-99.2, 6.18) * mm, v(-99.23, 5.94) * mm, v(-99.25, 5.72) * mm, v(-99.26, 5.5) * mm]});
            skFitSpline(sketch, "E1270", {"points": [v(-99.26, 5.5) * mm, v(-99.27, 5.13) * mm, v(-99.26, 4.75) * mm, v(-99.26, 4.38) * mm]});
            skFitSpline(sketch, "E1271", {"points": [v(-99.26, 4.38) * mm, v(-99.27, 4.27) * mm, v(-99.23, 4.2) * mm, v(-99.15, 4.13) * mm]});
            skFitSpline(sketch, "E1272", {"points": [v(-99.15, 4.13) * mm, v(-98.84, 3.83) * mm, v(-98.53, 3.53) * mm, v(-98.22, 3.23) * mm]});
            skFitSpline(sketch, "E1273", {"points": [v(-98.22, 3.23) * mm, v(-98.1, 3.12) * mm, v(-97.99, 3.01) * mm, v(-97.85, 2.88) * mm]});
            skFitSpline(sketch, "E1274", {"points": [v(-97.85, 2.88) * mm, v(-97.55, 3.27) * mm, v(-97.2, 3.59) * mm, v(-96.95, 4) * mm]});
            skFitSpline(sketch, "E1275", {"points": [v(-96.95, 4) * mm, v(-96.88, 4.13) * mm, v(-96.8, 4.25) * mm, v(-96.73, 4.37) * mm]});
            skFitSpline(sketch, "E1276", {"points": [v(-96.73, 4.37) * mm, v(-96.56, 4.62) * mm, v(-96.3, 4.69) * mm, v(-96.06, 4.55) * mm]});
            skFitSpline(sketch, "E1277", {"points": [v(-96.06, 4.55) * mm, v(-95.83, 4.41) * mm, v(-95.75, 4.13) * mm, v(-95.9, 3.88) * mm]});
            skFitSpline(sketch, "E1278", {"points": [v(-95.9, 3.88) * mm, v(-96.1, 3.55) * mm, v(-96.32, 3.22) * mm, v(-96.55, 2.91) * mm]});
            skFitSpline(sketch, "E1279", {"points": [v(-96.55, 2.91) * mm, v(-96.73, 2.67) * mm, v(-96.94, 2.45) * mm, v(-97.15, 2.2) * mm]});
            skFitSpline(sketch, "E1280", {"points": [v(-97.15, 2.2) * mm, v(-97, 2.07) * mm, v(-96.86, 1.93) * mm, v(-96.72, 1.79) * mm]});
            skFitSpline(sketch, "E1281", {"points": [v(-96.72, 1.79) * mm, v(-96.48, 2.01) * mm, v(-96.25, 2.23) * mm, v(-96.03, 2.45) * mm]});
            skFitSpline(sketch, "E1282", {"points": [v(-96.03, 2.45) * mm, v(-95.5, 2.97) * mm, v(-94.98, 3.48) * mm, v(-94.45, 4) * mm]});
            skFitSpline(sketch, "E1283", {"points": [v(-94.45, 4) * mm, v(-94.27, 4.17) * mm, v(-94.08, 4.35) * mm, v(-93.9, 4.52) * mm]});
            skFitSpline(sketch, "E1284", {"points": [v(-93.9, 4.52) * mm, v(-93.75, 4.66) * mm, v(-93.59, 4.76) * mm, v(-93.38, 4.7) * mm]});
            skFitSpline(sketch, "E1285", {"points": [v(-93.38, 4.7) * mm, v(-93, 4.6) * mm, v(-92.87, 4.18) * mm, v(-93.14, 3.9) * mm]});
            skFitSpline(sketch, "E1286", {"points": [v(-93.14, 3.9) * mm, v(-93.34, 3.68) * mm, v(-93.56, 3.5) * mm, v(-93.77, 3.3) * mm]});
            skFitSpline(sketch, "E1287", {"points": [v(-93.77, 3.3) * mm, v(-94, 3.09) * mm, v(-94.22, 2.87) * mm, v(-94.45, 2.65) * mm]});
            skFitSpline(sketch, "E1288", {"points": [v(-94.45, 2.65) * mm, v(-94.1, 2.35) * mm, v(-93.79, 2.07) * mm, v(-93.46, 1.78) * mm]});
            skFitSpline(sketch, "E1289", {"points": [v(-93.46, 1.78) * mm, v(-93.4, 1.82) * mm, v(-93.35, 1.86) * mm, v(-93.3, 1.9) * mm]});
            skFitSpline(sketch, "E1290", {"points": [v(-93.3, 1.9) * mm, v(-92.77, 2.36) * mm, v(-92.24, 2.82) * mm, v(-91.7, 3.28) * mm]});
            skFitSpline(sketch, "E1291", {"points": [v(-91.7, 3.28) * mm, v(-91.54, 3.43) * mm, v(-91.39, 3.6) * mm, v(-91.22, 3.74) * mm]});
            skFitSpline(sketch, "E1292", {"points": [v(-91.22, 3.74) * mm, v(-91.08, 3.87) * mm, v(-90.92, 3.94) * mm, v(-90.72, 3.87) * mm]});
            skFitSpline(sketch, "E1293", {"points": [v(-90.72, 3.87) * mm, v(-90.37, 3.75) * mm, v(-90.26, 3.35) * mm, v(-90.52, 3.08) * mm]});
            skFitSpline(sketch, "E1294", {"points": [v(-90.52, 3.08) * mm, v(-90.8, 2.8) * mm, v(-91.1, 2.52) * mm, v(-91.39, 2.25) * mm]});
            skFitSpline(sketch, "E1295", {"points": [v(-91.39, 2.25) * mm, v(-91.62, 2.04) * mm, v(-91.87, 1.84) * mm, v(-92.11, 1.63) * mm]});
            skFitSpline(sketch, "E1296", {"points": [v(-92.11, 1.63) * mm, v(-91.8, 1.63) * mm, v(-91.51, 1.63) * mm, v(-91.21, 1.63) * mm]});
            skFitSpline(sketch, "E1297", {"points": [v(-91.21, 1.63) * mm, v(-91.1, 1.63) * mm, v(-91, 1.65) * mm, v(-90.9, 1.65) * mm]});
            skFitSpline(sketch, "E1298", {"points": [v(-90.9, 1.65) * mm, v(-90.45, 1.67) * mm, v(-90, 1.69) * mm, v(-89.54, 1.7) * mm]});
            skFitSpline(sketch, "E1299", {"points": [v(-89.54, 1.7) * mm, v(-89.44, 1.7) * mm, v(-89.38, 1.73) * mm, v(-89.32, 1.8) * mm]});
            skFitSpline(sketch, "E1300", {"points": [v(-89.32, 1.8) * mm, v(-88.96, 2.24) * mm, v(-88.6, 2.68) * mm, v(-88.24, 3.12) * mm]});
            skFitSpline(sketch, "E1301", {"points": [v(-88.24, 3.12) * mm, v(-88.17, 3.2) * mm, v(-88.11, 3.3) * mm, v(-88.05, 3.4) * mm]});
            skFitSpline(sketch, "E1302", {"points": [v(-88.05, 3.4) * mm, v(-87.98, 3.5) * mm, v(-87.92, 3.6) * mm, v(-87.83, 3.68) * mm]});
            skFitSpline(sketch, "E1303", {"points": [v(-87.83, 3.68) * mm, v(-87.64, 3.85) * mm, v(-87.38, 3.85) * mm, v(-87.2, 3.7) * mm]});
            skFitSpline(sketch, "E1304", {"points": [v(-87.2, 3.7) * mm, v(-87.01, 3.54) * mm, v(-86.96, 3.27) * mm, v(-87.1, 3.06) * mm]});
            skFitSpline(sketch, "E1305", {"points": [v(-87.1, 3.06) * mm, v(-87.33, 2.72) * mm, v(-87.56, 2.39) * mm, v(-87.8, 2.07) * mm]});
            skFitSpline(sketch, "E1306", {"points": [v(-87.8, 2.07) * mm, v(-88.02, 1.8) * mm, v(-88.26, 1.54) * mm, v(-88.5, 1.27) * mm]});
            skFitSpline(sketch, "E1307", {"points": [v(-88.5, 1.27) * mm, v(-88.55, 1.2) * mm, v(-88.6, 1.14) * mm, v(-88.65, 1.07) * mm]});
            skFitSpline(sketch, "E1308", {"points": [v(-88.65, 1.07) * mm, v(-88.58, 1) * mm, v(-88.53, 0.92) * mm, v(-88.46, 0.85) * mm]});
            skFitSpline(sketch, "E1309", {"points": [v(-88.46, 0.85) * mm, v(-87.96, 0.3) * mm, v(-87.5, -0.27) * mm, v(-87.11, -0.9) * mm]});
            skFitSpline(sketch, "E1310", {"points": [v(-87.11, -0.9) * mm, v(-86.97, -1.11) * mm, v(-87, -1.38) * mm, v(-87.2, -1.54) * mm]});
            skFitSpline(sketch, "E1311", {"points": [v(-87.2, -1.54) * mm, v(-87.39, -1.7) * mm, v(-87.65, -1.7) * mm, v(-87.85, -1.51) * mm]});
            skFitSpline(sketch, "E1312", {"points": [v(-87.85, -1.51) * mm, v(-87.91, -1.45) * mm, v(-87.97, -1.38) * mm, v(-88.01, -1.3) * mm]});
            skFitSpline(sketch, "E1313", {"points": [v(-88.01, -1.3) * mm, v(-88.33, -0.77) * mm, v(-88.74, -0.3) * mm, v(-89.16, 0.16) * mm]});
            skFitSpline(sketch, "E1314", {"points": [v(-89.16, 0.16) * mm, v(-89.18, 0.2) * mm, v(-89.22, 0.22) * mm, v(-89.24, 0.25) * mm]});
            skFitSpline(sketch, "E1315", {"points": [v(-89.24, 0.25) * mm, v(-89.34, 0.44) * mm, v(-89.51, 0.46) * mm, v(-89.7, 0.46) * mm]});
            skFitSpline(sketch, "E1316", {"points": [v(-89.7, 0.46) * mm, v(-90.2, 0.48) * mm, v(-90.7, 0.5) * mm, v(-91.2, 0.51) * mm]});
            skFitSpline(sketch, "E1317", {"points": [v(-91.2, 0.51) * mm, v(-91.5, 0.52) * mm, v(-91.8, 0.51) * mm, v(-92.11, 0.51) * mm]});
            skFitSpline(sketch, "E1318", {"points": [v(-92.11, 0.51) * mm, v(-91.93, 0.36) * mm, v(-91.74, 0.2) * mm, v(-91.56, 0.04) * mm]});
            skFitSpline(sketch, "E1319", {"points": [v(-91.56, 0.04) * mm, v(-91.2, -0.28) * mm, v(-90.86, -0.6) * mm, v(-90.53, -0.93) * mm]});
            skFitSpline(sketch, "E1320", {"points": [v(-90.53, -0.93) * mm, v(-90.25, -1.2) * mm, v(-90.38, -1.64) * mm, v(-90.76, -1.74) * mm]});
            skFitSpline(sketch, "E1321", {"points": [v(-90.76, -1.74) * mm, v(-90.95, -1.8) * mm, v(-91.1, -1.71) * mm, v(-91.24, -1.59) * mm]});
            skFitSpline(sketch, "E1322", {"points": [v(-91.24, -1.59) * mm, v(-91.43, -1.4) * mm, v(-91.61, -1.21) * mm, v(-91.8, -1.04) * mm]});
            skFitSpline(sketch, "E1323", {"points": [v(-91.8, -1.04) * mm, v(-92.12, -0.77) * mm, v(-92.44, -0.5) * mm, v(-92.76, -0.24) * mm]});
            skFitSpline(sketch, "E1324", {"points": [v(-92.76, -0.24) * mm, v(-92.99, -0.04) * mm, v(-93.21, 0.16) * mm, v(-93.45, 0.37) * mm]});
            skFitSpline(sketch, "E1325", {"points": [v(-93.45, 0.37) * mm, v(-93.78, 0.09) * mm, v(-94.1, -0.2) * mm, v(-94.44, -0.49) * mm]});
            skFitSpline(sketch, "E1326", {"points": [v(-94.44, -0.49) * mm, v(-94.34, -0.6) * mm, v(-94.24, -0.7) * mm, v(-94.14, -0.8) * mm]});
            skFitSpline(sketch, "E1327", {"points": [v(-94.14, -0.8) * mm, v(-93.82, -1.1) * mm, v(-93.5, -1.4) * mm, v(-93.18, -1.7) * mm]});
            skFitSpline(sketch, "E1328", {"points": [v(-93.18, -1.7) * mm, v(-93.05, -1.82) * mm, v(-92.98, -1.97) * mm, v(-93, -2.15) * mm]});
            skFitSpline(sketch, "E1329", {"points": [v(-93, -2.15) * mm, v(-93.06, -2.52) * mm, v(-93.46, -2.69) * mm, v(-93.77, -2.47) * mm]});
            skFitSpline(sketch, "E1330", {"points": [v(-93.77, -2.47) * mm, v(-93.92, -2.36) * mm, v(-94.06, -2.23) * mm, v(-94.19, -2.1) * mm]});
            skFitSpline(sketch, "E1331", {"points": [v(-94.19, -2.1) * mm, v(-94.65, -1.67) * mm, v(-95.1, -1.23) * mm, v(-95.55, -0.8) * mm]});
            skFitSpline(sketch, "E1332", {"points": [v(-95.55, -0.8) * mm, v(-95.94, -0.41) * mm, v(-96.32, -0.03) * mm, v(-96.73, 0.38) * mm]});
            skFitSpline(sketch, "E1333", {"points": [v(-96.73, 0.38) * mm, v(-96.86, 0.23) * mm, v(-96.99, 0.08) * mm, v(-97.13, -0.08) * mm]});
            skFitSpline(sketch, "E1334", {"points": [v(-97.13, -0.08) * mm, v(-96.95, -0.28) * mm, v(-96.75, -0.5) * mm, v(-96.57, -0.74) * mm]});
            skFitSpline(sketch, "E1335", {"points": [v(-96.57, -0.74) * mm, v(-96.34, -1.06) * mm, v(-96.1, -1.38) * mm, v(-95.9, -1.72) * mm]});
            skFitSpline(sketch, "E1336", {"points": [v(-95.9, -1.72) * mm, v(-95.74, -1.99) * mm, v(-95.84, -2.29) * mm, v(-96.1, -2.42) * mm]});
            skFitSpline(sketch, "E1337", {"points": [v(-96.1, -2.42) * mm, v(-96.29, -2.51) * mm, v(-96.51, -2.47) * mm, v(-96.66, -2.3) * mm]});
            skFitSpline(sketch, "E1338", {"points": [v(-96.66, -2.3) * mm, v(-96.71, -2.25) * mm, v(-96.75, -2.2) * mm, v(-96.78, -2.13) * mm]});
            skFitSpline(sketch, "E1339", {"points": [v(-96.78, -2.13) * mm, v(-97.06, -1.6) * mm, v(-97.46, -1.19) * mm, v(-97.85, -0.74) * mm]});
            skFitSpline(sketch, "E1340", {"points": [v(-97.85, -0.74) * mm, v(-98.14, -1) * mm, v(-98.42, -1.27) * mm, v(-98.7, -1.53) * mm]});
            skFitSpline(sketch, "E1341", {"points": [v(-98.7, -1.53) * mm, v(-98.81, -1.63) * mm, v(-98.92, -1.75) * mm, v(-99.03, -1.84) * mm]});
            skFitSpline(sketch, "E1342", {"points": [v(-99.03, -1.84) * mm, v(-99.21, -2) * mm, v(-99.29, -2.18) * mm, v(-99.28, -2.4) * mm]});
            skFitSpline(sketch, "E1343", {"points": [v(-99.28, -2.4) * mm, v(-99.26, -2.92) * mm, v(-99.24, -3.43) * mm, v(-99.23, -3.94) * mm]});
            skFitSpline(sketch, "E1344", {"points": [v(-99.23, -3.94) * mm, v(-99.23, -3.96) * mm, v(-99.22, -3.98) * mm, v(-99.2, -4.03) * mm]});
            skFitSpline(sketch, "E1345", {"points": [v(-99.2, -4.03) * mm, v(-98.95, -4.01) * mm, v(-98.69, -4.01) * mm, v(-98.43, -3.98) * mm]});
            skFitSpline(sketch, "E1346", {"points": [v(-98.43, -3.98) * mm, v(-98.1, -3.93) * mm, v(-97.79, -3.86) * mm, v(-97.47, -3.8) * mm]});
            skFitSpline(sketch, "E1347", {"points": [v(-97.47, -3.8) * mm, v(-97.4, -3.79) * mm, v(-97.33, -3.78) * mm, v(-97.25, -3.77) * mm]});
            skFitSpline(sketch, "E1348", {"points": [v(-97.25, -3.77) * mm, v(-97, -3.74) * mm, v(-96.8, -3.96) * mm, v(-96.77, -4.15) * mm]});
            skFitSpline(sketch, "E1349", {"points": [v(-96.77, -4.15) * mm, v(-96.73, -4.4) * mm, v(-96.84, -4.62) * mm, v(-97.09, -4.7) * mm]});
            skFitSpline(sketch, "E1350", {"points": [v(-97.09, -4.7) * mm, v(-97.3, -4.77) * mm, v(-97.53, -4.83) * mm, v(-97.76, -4.87) * mm]});
            skFitSpline(sketch, "E1351", {"points": [v(-97.76, -4.87) * mm, v(-98.08, -4.92) * mm, v(-98.4, -4.94) * mm, v(-98.73, -4.97) * mm]});
            skFitSpline(sketch, "E1352", {"points": [v(-98.73, -4.97) * mm, v(-98.88, -4.98) * mm, v(-99.03, -5) * mm, v(-99.2, -5.01) * mm]});
            skLineSegment(sketch, "E1353", {"start": v(-99.2, -5.01) * mm, "end": v(-99.2, -5.59) * mm});
            skFitSpline(sketch, "E1354", {"points": [v(-99.2, -5.59) * mm, v(-99.18, -5.6) * mm, v(-99.17, -5.61) * mm, v(-99.16, -5.61) * mm]});
            skFitSpline(sketch, "E1355", {"points": [v(-99.16, -5.61) * mm, v(-98.64, -5.62) * mm, v(-98.12, -5.62) * mm, v(-97.6, -5.62) * mm]});
            skFitSpline(sketch, "E1356", {"points": [v(-97.6, -5.62) * mm, v(-97.18, -5.63) * mm, v(-96.76, -5.65) * mm, v(-96.34, -5.66) * mm]});
            skFitSpline(sketch, "E1357", {"points": [v(-96.34, -5.66) * mm, v(-96.02, -5.67) * mm, v(-95.7, -5.67) * mm, v(-95.38, -5.68) * mm]});
            skFitSpline(sketch, "E1358", {"points": [v(-95.38, -5.68) * mm, v(-95.29, -5.68) * mm, v(-95.2, -5.68) * mm, v(-95.12, -5.7) * mm]});
            skFitSpline(sketch, "E1359", {"points": [v(-95.12, -5.7) * mm, v(-94.84, -5.73) * mm, v(-94.69, -5.94) * mm, v(-94.7, -6.22) * mm]});
            skFitSpline(sketch, "E1360", {"points": [v(-94.7, -6.22) * mm, v(-94.72, -6.46) * mm, v(-94.9, -6.65) * mm, v(-95.16, -6.65) * mm]});
            skFitSpline(sketch, "E1361", {"points": [v(-95.16, -6.65) * mm, v(-95.62, -6.64) * mm, v(-96.09, -6.62) * mm, v(-96.55, -6.6) * mm]});
            skFitSpline(sketch, "E1362", {"points": [v(-96.55, -6.6) * mm, v(-96.7, -6.6) * mm, v(-96.83, -6.6) * mm, v(-96.98, -6.6) * mm]});
            skFitSpline(sketch, "E1363", {"points": [v(-96.98, -6.6) * mm, v(-96.95, -7.07) * mm, v(-96.92, -7.5) * mm, v(-96.9, -7.93) * mm]});
            skFitSpline(sketch, "E1364", {"points": [v(-96.9, -7.93) * mm, v(-96.75, -7.94) * mm, v(-96.6, -7.96) * mm, v(-96.47, -7.97) * mm]});
            skFitSpline(sketch, "E1365", {"points": [v(-96.47, -7.97) * mm, v(-95.83, -8.02) * mm, v(-95.2, -8.07) * mm, v(-94.56, -8.11) * mm]});
            skFitSpline(sketch, "E1366", {"points": [v(-94.56, -8.11) * mm, v(-94.34, -8.13) * mm, v(-94.11, -8.1) * mm, v(-93.89, -8.12) * mm]});
            skFitSpline(sketch, "E1367", {"points": [v(-93.89, -8.12) * mm, v(-93.62, -8.13) * mm, v(-93.43, -8.32) * mm, v(-93.42, -8.58) * mm]});
            skFitSpline(sketch, "E1368", {"points": [v(-93.42, -8.58) * mm, v(-93.41, -8.85) * mm, v(-93.6, -9.06) * mm, v(-93.87, -9.07) * mm]});
            skFitSpline(sketch, "E1369", {"points": [v(-93.87, -9.07) * mm, v(-94.13, -9.08) * mm, v(-94.4, -9.09) * mm, v(-94.66, -9.07) * mm]});
            skFitSpline(sketch, "E1370", {"points": [v(-94.66, -9.07) * mm, v(-95.13, -9.05) * mm, v(-95.6, -9) * mm, v(-96.08, -8.98) * mm]});
            skFitSpline(sketch, "E1371", {"points": [v(-96.08, -8.98) * mm, v(-95.86, -9.18) * mm, v(-95.64, -9.39) * mm, v(-95.43, -9.6) * mm]});
            skFitSpline(sketch, "E1372", {"points": [v(-95.43, -9.6) * mm, v(-95.05, -9.95) * mm, v(-94.67, -10.3) * mm, v(-94.3, -10.66) * mm]});
            skFitSpline(sketch, "E1373", {"points": [v(-94.3, -10.66) * mm, v(-94.17, -10.78) * mm, v(-94.05, -10.86) * mm, v(-93.85, -10.83) * mm]});
            skFitSpline(sketch, "E1374", {"points": [v(-93.85, -10.83) * mm, v(-93.3, -10.76) * mm, v(-92.76, -10.72) * mm, v(-92.21, -10.67) * mm]});
            skFitSpline(sketch, "E1375", {"points": [v(-92.21, -10.67) * mm, v(-92.12, -10.66) * mm, v(-92.03, -10.62) * mm, v(-91.93, -10.6) * mm]});
            skFitSpline(sketch, "E1376", {"points": [v(-91.93, -10.6) * mm, v(-91.81, -10.59) * mm, v(-91.7, -10.56) * mm, v(-91.58, -10.57) * mm]});
            skFitSpline(sketch, "E1377", {"points": [v(-91.58, -10.57) * mm, v(-91.32, -10.57) * mm, v(-91.13, -10.75) * mm, v(-91.1, -11) * mm]});
            skFitSpline(sketch, "E1378", {"points": [v(-91.1, -11) * mm, v(-91.09, -11.23) * mm, v(-91.24, -11.46) * mm, v(-91.48, -11.5) * mm]});
            skFitSpline(sketch, "E1379", {"points": [v(-91.48, -11.5) * mm, v(-91.96, -11.6) * mm, v(-92.44, -11.67) * mm, v(-92.92, -11.73) * mm]});
            skFitSpline(sketch, "E1380", {"points": [v(-92.92, -11.73) * mm, v(-93.27, -11.77) * mm, v(-93.62, -11.79) * mm, v(-94, -11.82) * mm]});
            skFitSpline(sketch, "E1381", {"points": [v(-94, -11.82) * mm, v(-94, -11.97) * mm, v(-94.02, -12.12) * mm, v(-94.03, -12.27) * mm]});
            skFitSpline(sketch, "E1382", {"points": [v(-94.03, -12.27) * mm, v(-94.07, -12.9) * mm, v(-94.11, -13.53) * mm, v(-94.27, -14.14) * mm]});
            skFitSpline(sketch, "E1383", {"points": [v(-94.27, -14.14) * mm, v(-94.28, -14.2) * mm, v(-94.28, -14.27) * mm, v(-94.3, -14.33) * mm]});
            skFitSpline(sketch, "E1384", {"points": [v(-94.3, -14.33) * mm, v(-94.36, -14.56) * mm, v(-94.6, -14.73) * mm, v(-94.82, -14.7) * mm]});
            skFitSpline(sketch, "E1385", {"points": [v(-94.82, -14.7) * mm, v(-95.06, -14.67) * mm, v(-95.24, -14.48) * mm, v(-95.24, -14.23) * mm]});
            skFitSpline(sketch, "E1386", {"points": [v(-95.24, -14.23) * mm, v(-95.25, -14.14) * mm, v(-95.25, -14.04) * mm, v(-95.22, -13.95) * mm]});
            skFitSpline(sketch, "E1387", {"points": [v(-95.22, -13.95) * mm, v(-95.07, -13.32) * mm, v(-95.03, -12.67) * mm, v(-94.98, -12.03) * mm]});
            skFitSpline(sketch, "E1388", {"points": [v(-94.98, -12.03) * mm, v(-94.96, -11.76) * mm, v(-95.06, -11.6) * mm, v(-95.24, -11.44) * mm]});
            skFitSpline(sketch, "E1389", {"points": [v(-95.24, -11.44) * mm, v(-95.4, -11.3) * mm, v(-95.53, -11.12) * mm, v(-95.67, -10.96) * mm]});
            skFitSpline(sketch, "E1390", {"points": [v(-95.67, -10.96) * mm, v(-96.04, -10.57) * mm, v(-96.4, -10.18) * mm, v(-96.77, -9.8) * mm]});
            skFitSpline(sketch, "E1391", {"points": [v(-96.77, -9.8) * mm, v(-96.79, -9.77) * mm, v(-96.82, -9.76) * mm, v(-96.83, -9.75) * mm]});
            skFitSpline(sketch, "E1392", {"points": [v(-96.83, -9.75) * mm, v(-96.81, -10.13) * mm, v(-96.78, -10.5) * mm, v(-96.77, -10.9) * mm]});
            skFitSpline(sketch, "E1393", {"points": [v(-96.77, -10.9) * mm, v(-96.75, -11.23) * mm, v(-96.74, -11.56) * mm, v(-96.74, -11.9) * mm]});
            skFitSpline(sketch, "E1394", {"points": [v(-96.74, -11.9) * mm, v(-96.74, -12.2) * mm, v(-96.93, -12.38) * mm, v(-97.2, -12.38) * mm]});
            skFitSpline(sketch, "E1395", {"points": [v(-97.2, -12.38) * mm, v(-97.49, -12.38) * mm, v(-97.68, -12.2) * mm, v(-97.7, -11.9) * mm]});
            skFitSpline(sketch, "E1396", {"points": [v(-97.7, -11.9) * mm, v(-97.7, -11.44) * mm, v(-97.72, -10.97) * mm, v(-97.74, -10.51) * mm]});
            skFitSpline(sketch, "E1397", {"points": [v(-97.74, -10.51) * mm, v(-97.75, -10.4) * mm, v(-97.76, -10.3) * mm, v(-97.77, -10.18) * mm]});
            skFitSpline(sketch, "E1398", {"points": [v(-97.77, -10.18) * mm, v(-97.81, -9.77) * mm, v(-97.85, -9.35) * mm, v(-97.89, -8.92) * mm]});
            skFitSpline(sketch, "E1399", {"points": [v(-97.89, -8.92) * mm, v(-98.31, -8.89) * mm, v(-98.74, -8.86) * mm, v(-99.2, -8.83) * mm]});
            skFitSpline(sketch, "E1400", {"points": [v(-99.2, -8.83) * mm, v(-99.2, -9.09) * mm, v(-99.21, -9.36) * mm, v(-99.2, -9.62) * mm]});
            skFitSpline(sketch, "E1401", {"points": [v(-99.2, -9.62) * mm, v(-99.2, -9.97) * mm, v(-99.17, -10.3) * mm, v(-99.17, -10.65) * mm]});
            skFitSpline(sketch, "E1402", {"points": [v(-99.17, -10.65) * mm, v(-99.17, -10.89) * mm, v(-99.34, -11.07) * mm, v(-99.55, -11.1) * mm]});
            skFitSpline(sketch, "E1403", {"points": [v(-99.55, -11.1) * mm, v(-99.8, -11.15) * mm, v(-100, -11.03) * mm, v(-100.09, -10.8) * mm]});
            skFitSpline(sketch, "E1404", {"points": [v(-100.09, -10.8) * mm, v(-100.13, -10.7) * mm, v(-100.13, -10.57) * mm, v(-100.14, -10.46) * mm]});
            skFitSpline(sketch, "E1405", {"points": [v(-100.14, -10.46) * mm, v(-100.16, -9.78) * mm, v(-100.18, -9.11) * mm, v(-100.19, -8.44) * mm]});
            skFitSpline(sketch, "E1406", {"points": [v(-100.19, -8.44) * mm, v(-100.2, -7.9) * mm, v(-100.19, -7.36) * mm, v(-100.19, -6.82) * mm]});
            skFitSpline(sketch, "E1407", {"points": [v(-100.19, -6.82) * mm, v(-100.19, -6.75) * mm, v(-100.19, -6.7) * mm, v(-100.19, -6.62) * mm]});
            skLineSegment(sketch, "E1408", {"start": v(-100.19, -6.62) * mm, "end": v(-100.8, -6.62) * mm});
            skFitSpline(sketch, "E1409", {"points": [v(-100.8, -6.62) * mm, v(-100.8, -6.76) * mm, v(-100.84, -6.9) * mm, v(-100.84, -7.06) * mm]});
            skFitSpline(sketch, "E1410", {"points": [v(-100.84, -7.06) * mm, v(-100.86, -7.56) * mm, v(-100.92, -8.06) * mm, v(-101.06, -8.54) * mm]});
            skFitSpline(sketch, "E1411", {"points": [v(-101.06, -8.54) * mm, v(-101.08, -8.64) * mm, v(-101.1, -8.73) * mm, v(-101.15, -8.81) * mm]});
            skFitSpline(sketch, "E1412", {"points": [v(-101.15, -8.81) * mm, v(-101.26, -9) * mm, v(-101.48, -9.09) * mm, v(-101.7, -9.04) * mm]});
            skFitSpline(sketch, "E1413", {"points": [v(-101.7, -9.04) * mm, v(-101.9, -8.98) * mm, v(-102.04, -8.8) * mm, v(-102.04, -8.58) * mm]});
            skFitSpline(sketch, "E1414", {"points": [v(-102.04, -8.58) * mm, v(-102.04, -8.46) * mm, v(-102.02, -8.34) * mm, v(-101.99, -8.22) * mm]});
            skFitSpline(sketch, "E1415", {"points": [v(-101.99, -8.22) * mm, v(-101.86, -7.82) * mm, v(-101.83, -7.4) * mm, v(-101.8, -6.97) * mm]});
            skFitSpline(sketch, "E1416", {"points": [v(-101.8, -6.97) * mm, v(-101.8, -6.86) * mm, v(-101.79, -6.74) * mm, v(-101.78, -6.62) * mm]});
            skFitSpline(sketch, "E1417", {"points": [v(-101.78, -6.62) * mm, v(-101.8, -6.6) * mm, v(-101.83, -6.59) * mm, v(-101.85, -6.59) * mm]});
            skFitSpline(sketch, "E1418", {"points": [v(-101.85, -6.59) * mm, v(-102.43, -6.57) * mm, v(-103.01, -6.57) * mm, v(-103.6, -6.55) * mm]});
            skFitSpline(sketch, "E1419", {"points": [v(-103.6, -6.55) * mm, v(-103.7, -6.55) * mm, v(-103.76, -6.58) * mm, v(-103.83, -6.65) * mm]});
            skFitSpline(sketch, "E1420", {"points": [v(-103.83, -6.65) * mm, v(-104.12, -6.96) * mm, v(-104.42, -7.27) * mm, v(-104.72, -7.58) * mm]});
            skFitSpline(sketch, "E1421", {"points": [v(-104.72, -7.58) * mm, v(-104.84, -7.7) * mm, v(-104.95, -7.83) * mm, v(-105.07, -7.96) * mm]});
            skFitSpline(sketch, "E1422", {"points": [v(-105.07, -7.96) * mm, v(-104.63, -8.33) * mm, v(-104.23, -8.73) * mm, v(-103.72, -9) * mm]});
            skFitSpline(sketch, "E1423", {"points": [v(-103.72, -9) * mm, v(-103.67, -9.03) * mm, v(-103.62, -9.06) * mm, v(-103.58, -9.09) * mm]});
            skFitSpline(sketch, "E1424", {"points": [v(-103.58, -9.09) * mm, v(-103.34, -9.25) * mm, v(-103.28, -9.5) * mm, v(-103.4, -9.74) * mm]});
            skFitSpline(sketch, "E1425", {"points": [v(-103.4, -9.74) * mm, v(-103.54, -9.97) * mm, v(-103.82, -10.07) * mm, v(-104.07, -9.92) * mm]});
            skFitSpline(sketch, "E1426", {"points": [v(-104.07, -9.92) * mm, v(-104.4, -9.72) * mm, v(-104.72, -9.51) * mm, v(-105.02, -9.28) * mm]});
            skFitSpline(sketch, "E1427", {"points": [v(-105.02, -9.28) * mm, v(-105.28, -9.1) * mm, v(-105.51, -8.87) * mm, v(-105.75, -8.67) * mm]});
            skFitSpline(sketch, "E1428", {"points": [v(-105.75, -8.67) * mm, v(-105.9, -8.81) * mm, v(-106.03, -8.94) * mm, v(-106.18, -9.09) * mm]});
            skFitSpline(sketch, "E1429", {"points": [v(-106.18, -9.09) * mm, v(-105.95, -9.32) * mm, v(-105.73, -9.56) * mm, v(-105.5, -9.8) * mm]});
            skFitSpline(sketch, "E1430", {"points": [v(-105.5, -9.8) * mm, v(-104.98, -10.32) * mm, v(-104.46, -10.85) * mm, v(-103.94, -11.38) * mm]});
            skFitSpline(sketch, "E1431", {"points": [v(-103.94, -11.38) * mm, v(-103.78, -11.55) * mm, v(-103.62, -11.72) * mm, v(-103.46, -11.89) * mm]});
            skFitSpline(sketch, "E1432", {"points": [v(-103.46, -11.89) * mm, v(-103.41, -11.94) * mm, v(-103.37, -12) * mm, v(-103.33, -12.06) * mm]});
            skFitSpline(sketch, "E1433", {"points": [v(-103.33, -12.06) * mm, v(-103.2, -12.27) * mm, v(-103.23, -12.53) * mm, v(-103.4, -12.69) * mm]});
            skFitSpline(sketch, "E1434", {"points": [v(-103.4, -12.69) * mm, v(-103.6, -12.85) * mm, v(-103.87, -12.86) * mm, v(-104.06, -12.67) * mm]});
            skFitSpline(sketch, "E1435", {"points": [v(-104.06, -12.67) * mm, v(-104.27, -12.47) * mm, v(-104.46, -12.26) * mm, v(-104.65, -12.05) * mm]});
            skFitSpline(sketch, "E1436", {"points": [v(-104.65, -12.05) * mm, v(-104.87, -11.82) * mm, v(-105.1, -11.6) * mm, v(-105.31, -11.36) * mm]});
            skFitSpline(sketch, "E1437", {"points": [v(-105.31, -11.36) * mm, v(-105.61, -11.7) * mm, v(-105.9, -12.02) * mm, v(-106.18, -12.35) * mm]});
            skFitSpline(sketch, "E1438", {"points": [v(-106.18, -12.35) * mm, v(-106.14, -12.4) * mm, v(-106.1, -12.45) * mm, v(-106.07, -12.5) * mm]});
            skFitSpline(sketch, "E1439", {"points": [v(-106.07, -12.5) * mm, v(-105.6, -13.03) * mm, v(-105.15, -13.56) * mm, v(-104.7, -14.1) * mm]});
            skFitSpline(sketch, "E1440", {"points": [v(-104.7, -14.1) * mm, v(-104.54, -14.26) * mm, v(-104.38, -14.41) * mm, v(-104.22, -14.57) * mm]});
            skFitSpline(sketch, "E1441", {"points": [v(-104.22, -14.57) * mm, v(-104.08, -14.72) * mm, v(-104.02, -14.9) * mm, v(-104.1, -15.1) * mm]});
            skFitSpline(sketch, "E1442", {"points": [v(-104.1, -15.1) * mm, v(-104.21, -15.45) * mm, v(-104.62, -15.54) * mm, v(-104.89, -15.28) * mm]});
            skFitSpline(sketch, "E1443", {"points": [v(-104.89, -15.28) * mm, v(-105.17, -15) * mm, v(-105.45, -14.7) * mm, v(-105.71, -14.41) * mm]});
            skFitSpline(sketch, "E1444", {"points": [v(-105.71, -14.41) * mm, v(-105.91, -14.2) * mm, v(-106.1, -13.96) * mm, v(-106.28, -13.73) * mm]});
            skFitSpline(sketch, "E1445", {"points": [v(-106.28, -13.73) * mm, v(-106.3, -13.72) * mm, v(-106.32, -13.71) * mm, v(-106.33, -13.7) * mm]});
            skFitSpline(sketch, "E1446", {"points": [v(-106.33, -13.7) * mm, v(-106.33, -14) * mm, v(-106.33, -14.3) * mm, v(-106.33, -14.6) * mm]});
            skFitSpline(sketch, "E1447", {"points": [v(-106.33, -14.6) * mm, v(-106.32, -14.7) * mm, v(-106.32, -14.8) * mm, v(-106.31, -14.91) * mm]});
            skFitSpline(sketch, "E1448", {"points": [v(-106.31, -14.91) * mm, v(-106.3, -15.36) * mm, v(-106.28, -15.8) * mm, v(-106.27, -16.25) * mm]});
            skFitSpline(sketch, "E1449", {"points": [v(-106.27, -16.25) * mm, v(-106.27, -16.36) * mm, v(-106.24, -16.43) * mm, v(-106.15, -16.5) * mm]});
            skFitSpline(sketch, "E1450", {"points": [v(-106.15, -16.5) * mm, v(-105.7, -16.86) * mm, v(-105.27, -17.23) * mm, v(-104.82, -17.6) * mm]});
            skFitSpline(sketch, "E1451", {"points": [v(-104.82, -17.6) * mm, v(-104.74, -17.66) * mm, v(-104.65, -17.7) * mm, v(-104.56, -17.76) * mm]});
            skFitSpline(sketch, "E1452", {"points": [v(-104.56, -17.76) * mm, v(-104.47, -17.83) * mm, v(-104.36, -17.9) * mm, v(-104.28, -17.98) * mm]});
            skFitSpline(sketch, "E1453", {"points": [v(-104.28, -17.98) * mm, v(-104.11, -18.17) * mm, v(-104.12, -18.44) * mm, v(-104.27, -18.62) * mm]});
            skFitSpline(sketch, "E1454", {"points": [v(-104.27, -18.62) * mm, v(-104.43, -18.8) * mm, v(-104.7, -18.85) * mm, v(-104.9, -18.7) * mm]});
            skFitSpline(sketch, "E1455", {"points": [v(-104.9, -18.7) * mm, v(-105.22, -18.5) * mm, v(-105.54, -18.28) * mm, v(-105.84, -18.05) * mm]});
            skFitSpline(sketch, "E1456", {"points": [v(-105.84, -18.05) * mm, v(-106.13, -17.82) * mm, v(-106.4, -17.56) * mm, v(-106.7, -17.31) * mm]});
            skFitSpline(sketch, "E1457", {"points": [v(-106.7, -17.31) * mm, v(-106.75, -17.26) * mm, v(-106.82, -17.22) * mm, v(-106.89, -17.16) * mm]});
            skFitSpline(sketch, "E1458", {"points": [v(104.5, 3.37) * mm, v(103.88, 3.35) * mm, v(103.25, 3.34) * mm, v(102.62, 3.33) * mm]});
            skFitSpline(sketch, "E1459", {"points": [v(102.62, 3.33) * mm, v(103.03, 2.88) * mm, v(103.44, 2.44) * mm, v(103.85, 2) * mm]});
            skFitSpline(sketch, "E1460", {"points": [v(103.85, 2) * mm, v(103.86, 1.98) * mm, v(103.88, 1.96) * mm, v(103.9, 1.95) * mm]});
            skFitSpline(sketch, "E1461", {"points": [v(103.9, 1.95) * mm, v(103.9, 1.95) * mm, v(103.92, 1.95) * mm, v(103.92, 1.95) * mm]});
            skFitSpline(sketch, "E1462", {"points": [v(103.92, 1.95) * mm, v(103.93, 1.95) * mm, v(103.94, 1.95) * mm, v(103.92, 1.95) * mm, v(103.92, 1.95) * mm]});
            skFitSpline(sketch, "E1463", {"points": [v(103.92, 1.95) * mm, v(104.12, 2.43) * mm, v(104.31, 2.9) * mm, v(104.5, 3.37) * mm]});
            skFitSpline(sketch, "E1464", {"points": [v(113.46, 3.33) * mm, v(112.82, 3.34) * mm, v(112.19, 3.35) * mm, v(111.56, 3.37) * mm]});
            skFitSpline(sketch, "E1465", {"points": [v(111.56, 3.37) * mm, v(111.75, 2.9) * mm, v(111.95, 2.42) * mm, v(112.15, 1.95) * mm]});
            skFitSpline(sketch, "E1466", {"points": [v(112.15, 1.95) * mm, v(112.58, 2.4) * mm, v(113.02, 2.86) * mm, v(113.46, 3.33) * mm]});
            skFitSpline(sketch, "E1467", {"points": [v(108.9, -3.04) * mm, v(109.36, -3.47) * mm, v(109.82, -3.91) * mm, v(110.29, -4.36) * mm]});
            skFitSpline(sketch, "E1468", {"points": [v(110.29, -4.36) * mm, v(110.3, -3.7) * mm, v(110.31, -3.08) * mm, v(110.33, -2.45) * mm]});
            skFitSpline(sketch, "E1469", {"points": [v(110.33, -2.45) * mm, v(109.86, -2.64) * mm, v(109.38, -2.84) * mm, v(108.9, -3.04) * mm]});
            skFitSpline(sketch, "E1470", {"points": [v(110.3, 6.51) * mm, v(109.82, 6.06) * mm, v(109.36, 5.61) * mm, v(108.9, 5.19) * mm]});
            skFitSpline(sketch, "E1471", {"points": [v(108.9, 5.19) * mm, v(109.38, 5) * mm, v(109.86, 4.8) * mm, v(110.32, 4.6) * mm]});
            skFitSpline(sketch, "E1472", {"points": [v(110.32, 4.6) * mm, v(110.31, 5.23) * mm, v(110.3, 5.86) * mm, v(110.3, 6.51) * mm]});
            skFitSpline(sketch, "E1473", {"points": [v(105.74, 4.6) * mm, v(106.2, 4.8) * mm, v(106.68, 5) * mm, v(107.16, 5.19) * mm]});
            skFitSpline(sketch, "E1474", {"points": [v(107.16, 5.19) * mm, v(106.7, 5.62) * mm, v(106.24, 6.06) * mm, v(105.77, 6.51) * mm]});
            skFitSpline(sketch, "E1475", {"points": [v(105.77, 6.51) * mm, v(105.76, 5.86) * mm, v(105.75, 5.23) * mm, v(105.74, 4.6) * mm]});
            skFitSpline(sketch, "E1476", {"points": [v(111.55, -1.24) * mm, v(111.87, -1.22) * mm, v(112.2, -1.2) * mm, v(112.5, -1.18) * mm]});
            skFitSpline(sketch, "E1477", {"points": [v(112.5, -1.18) * mm, v(112.82, -1.15) * mm, v(113.14, -1.24) * mm, v(113.48, -1.19) * mm]});
            skFitSpline(sketch, "E1478", {"points": [v(113.48, -1.19) * mm, v(113.01, -0.7) * mm, v(112.57, -0.25) * mm, v(112.14, 0.2) * mm]});
            skFitSpline(sketch, "E1479", {"points": [v(112.14, 0.2) * mm, v(111.95, -0.28) * mm, v(111.75, -0.75) * mm, v(111.55, -1.24) * mm]});
            skFitSpline(sketch, "E1480", {"points": [v(105.71, -2.44) * mm, v(105.73, -2.76) * mm, v(105.76, -3.08) * mm, v(105.77, -3.4) * mm]});
            skFitSpline(sketch, "E1481", {"points": [v(105.77, -3.4) * mm, v(105.78, -3.71) * mm, v(105.78, -4.03) * mm, v(105.78, -4.33) * mm]});
            skFitSpline(sketch, "E1482", {"points": [v(105.78, -4.33) * mm, v(105.89, -4.23) * mm, v(106.01, -4.13) * mm, v(106.13, -4.02) * mm]});
            skFitSpline(sketch, "E1483", {"points": [v(106.13, -4.02) * mm, v(106.25, -3.92) * mm, v(106.35, -3.8) * mm, v(106.47, -3.69) * mm]});
            skFitSpline(sketch, "E1484", {"points": [v(106.47, -3.69) * mm, v(106.59, -3.57) * mm, v(106.7, -3.46) * mm, v(106.83, -3.34) * mm]});
            skFitSpline(sketch, "E1485", {"points": [v(106.83, -3.34) * mm, v(106.94, -3.23) * mm, v(107.1, -3.17) * mm, v(107.17, -3.04) * mm]});
            skFitSpline(sketch, "E1486", {"points": [v(107.17, -3.04) * mm, v(106.68, -2.84) * mm, v(106.2, -2.64) * mm, v(105.71, -2.44) * mm]});
            skFitSpline(sketch, "E1487", {"points": [v(104.5, -1.22) * mm, v(104.31, -0.75) * mm, v(104.12, -0.27) * mm, v(103.92, 0.2) * mm]});
            skFitSpline(sketch, "E1488", {"points": [v(103.92, 0.2) * mm, v(103.48, -0.26) * mm, v(103.04, -0.72) * mm, v(102.6, -1.18) * mm]});
            skFitSpline(sketch, "E1489", {"points": [v(102.6, -1.18) * mm, v(103.25, -1.2) * mm, v(103.88, -1.2) * mm, v(104.5, -1.22) * mm]});
            skFitSpline(sketch, "E1490", {"points": [v(101.62, -11.62) * mm, v(101.78, -12.21) * mm, v(101.92, -12.77) * mm, v(102.07, -13.33) * mm]});
            skFitSpline(sketch, "E1491", {"points": [v(102.07, -13.33) * mm, v(102.58, -13.03) * mm, v(103.08, -12.73) * mm, v(103.59, -12.43) * mm]});
            skFitSpline(sketch, "E1492", {"points": [v(103.59, -12.43) * mm, v(103.44, -11.86) * mm, v(103.3, -11.3) * mm, v(103.15, -10.71) * mm]});
            skFitSpline(sketch, "E1493", {"points": [v(103.15, -10.71) * mm, v(102.62, -11.03) * mm, v(102.12, -11.32) * mm, v(101.62, -11.62) * mm]});
            skFitSpline(sketch, "E1494", {"points": [v(94.52, -3.37) * mm, v(94.22, -3.9) * mm, v(93.93, -4.39) * mm, v(93.63, -4.9) * mm]});
            skFitSpline(sketch, "E1495", {"points": [v(93.63, -4.9) * mm, v(94.2, -5.04) * mm, v(94.76, -5.18) * mm, v(95.34, -5.34) * mm]});
            skFitSpline(sketch, "E1496", {"points": [v(95.34, -5.34) * mm, v(95.63, -4.84) * mm, v(95.93, -4.33) * mm, v(96.25, -3.8) * mm]});
            skFitSpline(sketch, "E1497", {"points": [v(96.25, -3.8) * mm, v(95.66, -3.66) * mm, v(95.09, -3.51) * mm, v(94.52, -3.37) * mm]});
            skFitSpline(sketch, "E1498", {"points": [v(114, 15.48) * mm, v(113.49, 15.18) * mm, v(112.99, 14.88) * mm, v(112.48, 14.58) * mm]});
            skFitSpline(sketch, "E1499", {"points": [v(112.48, 14.58) * mm, v(112.62, 14.01) * mm, v(112.77, 13.45) * mm, v(112.92, 12.86) * mm]});
            skFitSpline(sketch, "E1500", {"points": [v(112.92, 12.86) * mm, v(113.44, 13.17) * mm, v(113.94, 13.47) * mm, v(114.44, 13.77) * mm]});
            skFitSpline(sketch, "E1501", {"points": [v(114.44, 13.77) * mm, v(114.3, 14.34) * mm, v(114.15, 14.9) * mm, v(114, 15.48) * mm]});
            skFitSpline(sketch, "E1502", {"points": [v(112.91, -10.71) * mm, v(112.76, -11.31) * mm, v(112.62, -11.88) * mm, v(112.48, -12.44) * mm]});
            skFitSpline(sketch, "E1503", {"points": [v(112.48, -12.44) * mm, v(113, -12.75) * mm, v(113.5, -13.03) * mm, v(114, -13.33) * mm]});
            skFitSpline(sketch, "E1504", {"points": [v(114, -13.33) * mm, v(114.15, -12.74) * mm, v(114.3, -12.2) * mm, v(114.44, -11.62) * mm]});
            skFitSpline(sketch, "E1505", {"points": [v(114.44, -11.62) * mm, v(113.94, -11.32) * mm, v(113.44, -11.02) * mm, v(112.91, -10.71) * mm]});
            skFitSpline(sketch, "E1506", {"points": [v(121.54, 5.52) * mm, v(121.85, 6.04) * mm, v(122.14, 6.54) * mm, v(122.44, 7.04) * mm]});
            skFitSpline(sketch, "E1507", {"points": [v(122.44, 7.04) * mm, v(121.86, 7.2) * mm, v(121.3, 7.33) * mm, v(120.73, 7.48) * mm]});
            skFitSpline(sketch, "E1508", {"points": [v(120.73, 7.48) * mm, v(120.42, 6.97) * mm, v(120.13, 6.48) * mm, v(119.82, 5.96) * mm]});
            skFitSpline(sketch, "E1509", {"points": [v(119.82, 5.96) * mm, v(120.4, 5.8) * mm, v(120.97, 5.66) * mm, v(121.54, 5.52) * mm]});
            skFitSpline(sketch, "E1510", {"points": [v(94.52, 5.52) * mm, v(95.1, 5.66) * mm, v(95.66, 5.8) * mm, v(96.25, 5.96) * mm]});
            skFitSpline(sketch, "E1511", {"points": [v(96.25, 5.96) * mm, v(95.93, 6.48) * mm, v(95.63, 6.99) * mm, v(95.34, 7.48) * mm]});
            skFitSpline(sketch, "E1512", {"points": [v(95.34, 7.48) * mm, v(94.75, 7.33) * mm, v(94.2, 7.2) * mm, v(93.63, 7.04) * mm]});
            skFitSpline(sketch, "E1513", {"points": [v(93.63, 7.04) * mm, v(93.92, 6.54) * mm, v(94.21, 6.05) * mm, v(94.52, 5.52) * mm]});
            skFitSpline(sketch, "E1514", {"points": [v(103.15, 12.86) * mm, v(103.3, 13.46) * mm, v(103.45, 14.03) * mm, v(103.59, 14.59) * mm]});
            skFitSpline(sketch, "E1515", {"points": [v(103.59, 14.59) * mm, v(103.07, 14.9) * mm, v(102.57, 15.18) * mm, v(102.07, 15.48) * mm]});
            skFitSpline(sketch, "E1516", {"points": [v(102.07, 15.48) * mm, v(101.92, 14.9) * mm, v(101.77, 14.35) * mm, v(101.62, 13.77) * mm]});
            skFitSpline(sketch, "E1517", {"points": [v(101.62, 13.77) * mm, v(102.12, 13.47) * mm, v(102.62, 13.18) * mm, v(103.15, 12.86) * mm]});
            skFitSpline(sketch, "E1518", {"points": [v(121.55, -3.39) * mm, v(121.14, -3.45) * mm, v(119.96, -3.76) * mm, v(119.84, -3.85) * mm]});
            skFitSpline(sketch, "E1519", {"points": [v(119.84, -3.85) * mm, v(120.14, -4.34) * mm, v(120.44, -4.84) * mm, v(120.73, -5.34) * mm]});
            skFitSpline(sketch, "E1520", {"points": [v(120.73, -5.34) * mm, v(121.31, -5.18) * mm, v(121.87, -5.04) * mm, v(122.44, -4.9) * mm]});
            skFitSpline(sketch, "E1521", {"points": [v(122.44, -4.9) * mm, v(122.14, -4.38) * mm, v(121.85, -3.9) * mm, v(121.55, -3.39) * mm]});
            skFitSpline(sketch, "E1522", {"points": [v(102.1, -2.17) * mm, v(102.1, -2.24) * mm, v(102.1, -2.28) * mm, v(102.11, -2.31) * mm]});
            skFitSpline(sketch, "E1523", {"points": [v(102.11, -2.31) * mm, v(102.27, -2.9) * mm, v(102.43, -3.48) * mm, v(102.51, -4.09) * mm]});
            skFitSpline(sketch, "E1524", {"points": [v(102.51, -4.09) * mm, v(102.56, -4.39) * mm, v(102.59, -4.41) * mm, v(102.9, -4.45) * mm]});
            skFitSpline(sketch, "E1525", {"points": [v(102.9, -4.45) * mm, v(103.46, -4.52) * mm, v(104, -4.68) * mm, v(104.55, -4.82) * mm]});
            skFitSpline(sketch, "E1526", {"points": [v(104.55, -4.82) * mm, v(104.62, -4.84) * mm, v(104.7, -4.85) * mm, v(104.79, -4.86) * mm]});
            skFitSpline(sketch, "E1527", {"points": [v(104.79, -4.86) * mm, v(104.79, -3.97) * mm, v(104.84, -3.1) * mm, v(104.71, -2.24) * mm]});
            skFitSpline(sketch, "E1528", {"points": [v(104.71, -2.24) * mm, v(103.85, -2.12) * mm, v(102.99, -2.17) * mm, v(102.1, -2.17) * mm]});
            skFitSpline(sketch, "E1529", {"points": [v(114.52, 3) * mm, v(113.9, 2.34) * mm, v(113.23, 1.78) * mm, v(112.74, 1.08) * mm]});
            skFitSpline(sketch, "E1530", {"points": [v(112.74, 1.08) * mm, v(113.24, 0.35) * mm, v(113.91, -0.2) * mm, v(114.52, -0.84) * mm]});
            skFitSpline(sketch, "E1531", {"points": [v(114.52, -0.84) * mm, v(114.58, -0.75) * mm, v(114.63, -0.68) * mm, v(114.68, -0.6) * mm]});
            skFitSpline(sketch, "E1532", {"points": [v(114.68, -0.6) * mm, v(114.96, -0.13) * mm, v(115.23, 0.36) * mm, v(115.57, 0.8) * mm]});
            skFitSpline(sketch, "E1533", {"points": [v(115.57, 0.8) * mm, v(115.77, 1.07) * mm, v(115.78, 1.07) * mm, v(115.57, 1.35) * mm]});
            skFitSpline(sketch, "E1534", {"points": [v(115.57, 1.35) * mm, v(115.23, 1.79) * mm, v(114.97, 2.26) * mm, v(114.7, 2.73) * mm]});
            skFitSpline(sketch, "E1535", {"points": [v(114.7, 2.73) * mm, v(114.65, 2.8) * mm, v(114.6, 2.88) * mm, v(114.52, 3) * mm]});
            skFitSpline(sketch, "E1536", {"points": [v(109.94, 7.56) * mm, v(109.87, 7.62) * mm, v(109.82, 7.66) * mm, v(109.76, 7.7) * mm]});
            skFitSpline(sketch, "E1537", {"points": [v(109.76, 7.7) * mm, v(109.26, 8) * mm, v(108.74, 8.27) * mm, v(108.27, 8.64) * mm]});
            skFitSpline(sketch, "E1538", {"points": [v(108.27, 8.64) * mm, v(108.07, 8.8) * mm, v(107.99, 8.8) * mm, v(107.76, 8.62) * mm]});
            skFitSpline(sketch, "E1539", {"points": [v(107.76, 8.62) * mm, v(107.33, 8.27) * mm, v(106.83, 8) * mm, v(106.35, 7.72) * mm]});
            skFitSpline(sketch, "E1540", {"points": [v(106.35, 7.72) * mm, v(106.28, 7.68) * mm, v(106.2, 7.63) * mm, v(106.12, 7.57) * mm]});
            skFitSpline(sketch, "E1541", {"points": [v(106.12, 7.57) * mm, v(106.76, 6.95) * mm, v(107.32, 6.27) * mm, v(108.03, 5.78) * mm]});
            skFitSpline(sketch, "E1542", {"points": [v(108.03, 5.78) * mm, v(108.75, 6.29) * mm, v(109.3, 6.95) * mm, v(109.94, 7.56) * mm]});
            skFitSpline(sketch, "E1543", {"points": [v(106.12, -5.41) * mm, v(106.19, -5.46) * mm, v(106.23, -5.5) * mm, v(106.29, -5.53) * mm]});
            skFitSpline(sketch, "E1544", {"points": [v(106.29, -5.53) * mm, v(106.8, -5.84) * mm, v(107.33, -6.12) * mm, v(107.8, -6.5) * mm]});
            skFitSpline(sketch, "E1545", {"points": [v(107.8, -6.5) * mm, v(108, -6.65) * mm, v(108.07, -6.65) * mm, v(108.3, -6.48) * mm]});
            skFitSpline(sketch, "E1546", {"points": [v(108.3, -6.48) * mm, v(108.74, -6.12) * mm, v(109.25, -5.85) * mm, v(109.74, -5.55) * mm]});
            skFitSpline(sketch, "E1547", {"points": [v(109.74, -5.55) * mm, v(109.8, -5.51) * mm, v(109.87, -5.47) * mm, v(109.94, -5.41) * mm]});
            skFitSpline(sketch, "E1548", {"points": [v(109.94, -5.41) * mm, v(109.3, -4.8) * mm, v(108.74, -4.12) * mm, v(108.03, -3.63) * mm]});
            skFitSpline(sketch, "E1549", {"points": [v(108.03, -3.63) * mm, v(107.31, -4.13) * mm, v(106.76, -4.8) * mm, v(106.12, -5.41) * mm]});
            skFitSpline(sketch, "E1550", {"points": [v(111.35, -2.24) * mm, v(111.26, -2.61) * mm, v(111.22, -4.47) * mm, v(111.3, -4.86) * mm]});
            skFitSpline(sketch, "E1551", {"points": [v(111.3, -4.86) * mm, v(111.34, -4.86) * mm, v(111.39, -4.85) * mm, v(111.44, -4.84) * mm]});
            skFitSpline(sketch, "E1552", {"points": [v(111.44, -4.84) * mm, v(112.03, -4.69) * mm, v(112.62, -4.52) * mm, v(113.23, -4.44) * mm]});
            skFitSpline(sketch, "E1553", {"points": [v(113.23, -4.44) * mm, v(113.48, -4.4) * mm, v(113.51, -4.34) * mm, v(113.56, -4.07) * mm]});
            skFitSpline(sketch, "E1554", {"points": [v(113.56, -4.07) * mm, v(113.65, -3.64) * mm, v(113.74, -3.2) * mm, v(113.84, -2.76) * mm]});
            skFitSpline(sketch, "E1555", {"points": [v(113.84, -2.76) * mm, v(113.88, -2.57) * mm, v(113.93, -2.38) * mm, v(113.98, -2.17) * mm]});
            skFitSpline(sketch, "E1556", {"points": [v(113.98, -2.17) * mm, v(113.08, -2.17) * mm, v(112.21, -2.12) * mm, v(111.35, -2.24) * mm]});
            skFitSpline(sketch, "E1557", {"points": [v(103.36, 1.03) * mm, v(102.83, 1.8) * mm, v(102.16, 2.35) * mm, v(101.54, 2.99) * mm]});
            skFitSpline(sketch, "E1558", {"points": [v(101.54, 2.99) * mm, v(101.48, 2.9) * mm, v(101.43, 2.82) * mm, v(101.38, 2.74) * mm]});
            skFitSpline(sketch, "E1559", {"points": [v(101.38, 2.74) * mm, v(101.1, 2.27) * mm, v(100.84, 1.78) * mm, v(100.5, 1.35) * mm]});
            skFitSpline(sketch, "E1560", {"points": [v(100.5, 1.35) * mm, v(100.3, 1.11) * mm, v(100.3, 1.03) * mm, v(100.5, 0.8) * mm]});
            skFitSpline(sketch, "E1561", {"points": [v(100.5, 0.8) * mm, v(100.84, 0.37) * mm, v(101.09, -0.11) * mm, v(101.37, -0.58) * mm]});
            skFitSpline(sketch, "E1562", {"points": [v(101.37, -0.58) * mm, v(101.42, -0.66) * mm, v(101.48, -0.74) * mm, v(101.55, -0.85) * mm]});
            skFitSpline(sketch, "E1563", {"points": [v(101.55, -0.85) * mm, v(102.17, -0.21) * mm, v(102.76, 0.4) * mm, v(103.36, 1.03) * mm]});
            skFitSpline(sketch, "E1564", {"points": [v(104.79, 7.02) * mm, v(104.67, 7) * mm, v(104.57, 6.97) * mm, v(104.48, 6.95) * mm]});
            skFitSpline(sketch, "E1565", {"points": [v(104.48, 6.95) * mm, v(103.96, 6.82) * mm, v(103.44, 6.66) * mm, v(102.9, 6.6) * mm]});
            skFitSpline(sketch, "E1566", {"points": [v(102.9, 6.6) * mm, v(102.85, 6.6) * mm, v(102.8, 6.58) * mm, v(102.76, 6.57) * mm]});
            skFitSpline(sketch, "E1567", {"points": [v(102.76, 6.57) * mm, v(102.63, 6.55) * mm, v(102.56, 6.48) * mm, v(102.54, 6.35) * mm]});
            skFitSpline(sketch, "E1568", {"points": [v(102.54, 6.35) * mm, v(102.5, 6.19) * mm, v(102.5, 6.02) * mm, v(102.46, 5.86) * mm]});
            skFitSpline(sketch, "E1569", {"points": [v(102.46, 5.86) * mm, v(102.36, 5.44) * mm, v(102.25, 5.02) * mm, v(102.15, 4.6) * mm]});
            skFitSpline(sketch, "E1570", {"points": [v(102.15, 4.6) * mm, v(102.13, 4.51) * mm, v(102.1, 4.42) * mm, v(102.09, 4.31) * mm]});
            skFitSpline(sketch, "E1571", {"points": [v(102.09, 4.31) * mm, v(102.99, 4.31) * mm, v(103.86, 4.26) * mm, v(104.72, 4.39) * mm]});
            skFitSpline(sketch, "E1572", {"points": [v(104.72, 4.39) * mm, v(104.83, 5.26) * mm, v(104.8, 6.12) * mm, v(104.79, 7.02) * mm]});
            skFitSpline(sketch, "E1573", {"points": [v(111.27, 7.02) * mm, v(111.27, 6.13) * mm, v(111.23, 5.25) * mm, v(111.34, 4.39) * mm]});
            skFitSpline(sketch, "E1574", {"points": [v(111.34, 4.39) * mm, v(111.83, 4.3) * mm, v(113.63, 4.27) * mm, v(113.97, 4.35) * mm]});
            skFitSpline(sketch, "E1575", {"points": [v(113.97, 4.35) * mm, v(113.95, 4.44) * mm, v(113.93, 4.53) * mm, v(113.9, 4.62) * mm]});
            skFitSpline(sketch, "E1576", {"points": [v(113.9, 4.62) * mm, v(113.78, 5.15) * mm, v(113.62, 5.67) * mm, v(113.56, 6.2) * mm]});
            skFitSpline(sketch, "E1577", {"points": [v(113.56, 6.2) * mm, v(113.53, 6.5) * mm, v(113.46, 6.57) * mm, v(113.17, 6.6) * mm]});
            skFitSpline(sketch, "E1578", {"points": [v(113.17, 6.6) * mm, v(112.63, 6.66) * mm, v(112.11, 6.82) * mm, v(111.59, 6.95) * mm]});
            skFitSpline(sketch, "E1579", {"points": [v(111.59, 6.95) * mm, v(111.49, 6.97) * mm, v(111.38, 7) * mm, v(111.27, 7.02) * mm]});
            skFitSpline(sketch, "E1580", {"points": [v(101.54, 6.28) * mm, v(100.25, 5.96) * mm, v(99, 5.65) * mm, v(97.74, 5.34) * mm]});
            skFitSpline(sketch, "E1581", {"points": [v(97.74, 5.34) * mm, v(98.41, 4.22) * mm, v(99.08, 3.12) * mm, v(99.76, 1.98) * mm]});
            skFitSpline(sketch, "E1582", {"points": [v(99.76, 1.98) * mm, v(99.87, 2.14) * mm, v(99.96, 2.26) * mm, v(100.04, 2.4) * mm]});
            skFitSpline(sketch, "E1583", {"points": [v(100.04, 2.4) * mm, v(100.25, 2.75) * mm, v(100.46, 3.1) * mm, v(100.68, 3.46) * mm]});
            skFitSpline(sketch, "E1584", {"points": [v(100.68, 3.46) * mm, v(100.78, 3.61) * mm, v(100.9, 3.75) * mm, v(100.92, 3.94) * mm]});
            skFitSpline(sketch, "E1585", {"points": [v(100.92, 3.94) * mm, v(100.92, 4) * mm, v(100.96, 4.07) * mm, v(101, 4.11) * mm]});
            skFitSpline(sketch, "E1586", {"points": [v(101, 4.11) * mm, v(101.09, 4.22) * mm, v(101.1, 4.34) * mm, v(101.13, 4.46) * mm]});
            skFitSpline(sketch, "E1587", {"points": [v(101.13, 4.46) * mm, v(101.15, 4.58) * mm, v(101.17, 4.7) * mm, v(101.2, 4.82) * mm]});
            skFitSpline(sketch, "E1588", {"points": [v(101.2, 4.82) * mm, v(101.28, 5.16) * mm, v(101.38, 5.5) * mm, v(101.46, 5.83) * mm]});
            skFitSpline(sketch, "E1589", {"points": [v(101.46, 5.83) * mm, v(101.5, 5.97) * mm, v(101.5, 6.11) * mm, v(101.54, 6.28) * mm]});
            skFitSpline(sketch, "E1590", {"points": [v(113.24, -5.43) * mm, v(113.1, -5.45) * mm, v(112.98, -5.46) * mm, v(112.86, -5.48) * mm]});
            skFitSpline(sketch, "E1591", {"points": [v(112.86, -5.48) * mm, v(112.51, -5.57) * mm, v(112.16, -5.65) * mm, v(111.82, -5.75) * mm]});
            skFitSpline(sketch, "E1592", {"points": [v(111.82, -5.75) * mm, v(111.52, -5.83) * mm, v(111.18, -5.83) * mm, v(110.92, -6.03) * mm]});
            skFitSpline(sketch, "E1593", {"points": [v(110.92, -6.03) * mm, v(110.88, -6.06) * mm, v(110.83, -6.06) * mm, v(110.78, -6.07) * mm]});
            skFitSpline(sketch, "E1594", {"points": [v(110.78, -6.07) * mm, v(110.73, -6.09) * mm, v(110.67, -6.1) * mm, v(110.63, -6.13) * mm]});
            skFitSpline(sketch, "E1595", {"points": [v(110.63, -6.13) * mm, v(110.18, -6.4) * mm, v(109.73, -6.68) * mm, v(109.28, -6.96) * mm]});
            skFitSpline(sketch, "E1596", {"points": [v(109.28, -6.96) * mm, v(109.17, -7.03) * mm, v(109.07, -7.11) * mm, v(108.95, -7.2) * mm]});
            skFitSpline(sketch, "E1597", {"points": [v(108.95, -7.2) * mm, v(110.08, -7.88) * mm, v(111.18, -8.55) * mm, v(112.3, -9.22) * mm]});
            skFitSpline(sketch, "E1598", {"points": [v(112.3, -9.22) * mm, v(112.61, -7.95) * mm, v(112.92, -6.7) * mm, v(113.24, -5.43) * mm]});
            skFitSpline(sketch, "E1599", {"points": [v(114.52, 6.28) * mm, v(114.56, 6.05) * mm, v(114.6, 5.88) * mm, v(114.64, 5.71) * mm]});
            skFitSpline(sketch, "E1600", {"points": [v(114.64, 5.71) * mm, v(114.73, 5.31) * mm, v(114.84, 4.9) * mm, v(114.93, 4.5) * mm]});
            skFitSpline(sketch, "E1601", {"points": [v(114.93, 4.5) * mm, v(114.96, 4.36) * mm, v(114.97, 4.2) * mm, v(115.08, 4.09) * mm]});
            skFitSpline(sketch, "E1602", {"points": [v(115.08, 4.09) * mm, v(115.12, 4.04) * mm, v(115.15, 3.97) * mm, v(115.15, 3.91) * mm]});
            skFitSpline(sketch, "E1603", {"points": [v(115.15, 3.91) * mm, v(115.17, 3.75) * mm, v(115.26, 3.63) * mm, v(115.35, 3.5) * mm]});
            skFitSpline(sketch, "E1604", {"points": [v(115.35, 3.5) * mm, v(115.42, 3.41) * mm, v(115.48, 3.3) * mm, v(115.54, 3.2) * mm]});
            skFitSpline(sketch, "E1605", {"points": [v(115.54, 3.2) * mm, v(115.72, 2.91) * mm, v(115.89, 2.61) * mm, v(116.07, 2.32) * mm]});
            skFitSpline(sketch, "E1606", {"points": [v(116.07, 2.32) * mm, v(116.14, 2.21) * mm, v(116.22, 2.11) * mm, v(116.31, 2) * mm]});
            skFitSpline(sketch, "E1607", {"points": [v(116.31, 2) * mm, v(117, 3.13) * mm, v(117.66, 4.22) * mm, v(118.33, 5.34) * mm]});
            skFitSpline(sketch, "E1608", {"points": [v(118.33, 5.34) * mm, v(117.06, 5.65) * mm, v(115.81, 5.96) * mm, v(114.52, 6.28) * mm]});
            skFitSpline(sketch, "E1609", {"points": [v(107.11, -7.2) * mm, v(107.04, -7.15) * mm, v(107, -7.1) * mm, v(106.95, -7.08) * mm]});
            skFitSpline(sketch, "E1610", {"points": [v(106.95, -7.08) * mm, v(106.63, -6.88) * mm, v(106.3, -6.67) * mm, v(105.97, -6.48) * mm]});
            skFitSpline(sketch, "E1611", {"points": [v(105.97, -6.48) * mm, v(105.68, -6.32) * mm, v(105.43, -6.05) * mm, v(105.07, -6) * mm]});
            skFitSpline(sketch, "E1612", {"points": [v(105.07, -6) * mm, v(105.05, -6) * mm, v(105.03, -6) * mm, v(105.01, -5.97) * mm]});
            skFitSpline(sketch, "E1613", {"points": [v(105.01, -5.97) * mm, v(104.9, -5.86) * mm, v(104.75, -5.84) * mm, v(104.6, -5.82) * mm]});
            skFitSpline(sketch, "E1614", {"points": [v(104.6, -5.82) * mm, v(104.48, -5.8) * mm, v(104.36, -5.77) * mm, v(104.24, -5.75) * mm]});
            skFitSpline(sketch, "E1615", {"points": [v(104.24, -5.75) * mm, v(103.9, -5.66) * mm, v(103.55, -5.57) * mm, v(103.2, -5.48) * mm]});
            skFitSpline(sketch, "E1616", {"points": [v(103.2, -5.48) * mm, v(103.09, -5.46) * mm, v(102.97, -5.45) * mm, v(102.83, -5.43) * mm]});
            skFitSpline(sketch, "E1617", {"points": [v(102.83, -5.43) * mm, v(103.14, -6.7) * mm, v(103.45, -7.95) * mm, v(103.77, -9.22) * mm]});
            skFitSpline(sketch, "E1618", {"points": [v(103.77, -9.22) * mm, v(104.9, -8.54) * mm, v(105.99, -7.88) * mm, v(107.11, -7.2) * mm]});
            skFitSpline(sketch, "E1619", {"points": [v(113.24, 7.55) * mm, v(112.92, 8.86) * mm, v(112.61, 10.1) * mm, v(112.3, 11.37) * mm]});
            skFitSpline(sketch, "E1620", {"points": [v(112.3, 11.37) * mm, v(111.18, 10.7) * mm, v(110.07, 10.03) * mm, v(108.94, 9.35) * mm]});
            skFitSpline(sketch, "E1621", {"points": [v(108.94, 9.35) * mm, v(109.09, 9.25) * mm, v(109.2, 9.16) * mm, v(109.33, 9.08) * mm]});
            skFitSpline(sketch, "E1622", {"points": [v(109.33, 9.08) * mm, v(109.7, 8.85) * mm, v(110.07, 8.64) * mm, v(110.44, 8.4) * mm]});
            skFitSpline(sketch, "E1623", {"points": [v(110.44, 8.4) * mm, v(110.58, 8.32) * mm, v(110.7, 8.21) * mm, v(110.88, 8.2) * mm]});
            skFitSpline(sketch, "E1624", {"points": [v(110.88, 8.2) * mm, v(110.97, 8.18) * mm, v(111.04, 8.12) * mm, v(111.12, 8.08) * mm]});
            skFitSpline(sketch, "E1625", {"points": [v(111.12, 8.08) * mm, v(111.18, 8.05) * mm, v(111.25, 8.01) * mm, v(111.31, 8) * mm]});
            skFitSpline(sketch, "E1626", {"points": [v(111.31, 8) * mm, v(111.66, 7.91) * mm, v(112.01, 7.83) * mm, v(112.36, 7.75) * mm]});
            skFitSpline(sketch, "E1627", {"points": [v(112.36, 7.75) * mm, v(112.64, 7.69) * mm, v(112.92, 7.63) * mm, v(113.24, 7.55) * mm]});
            skFitSpline(sketch, "E1628", {"points": [v(114.51, -4.07) * mm, v(114.53, -4.1) * mm, v(114.55, -4.1) * mm, v(114.57, -4.12) * mm]});
            skFitSpline(sketch, "E1629", {"points": [v(114.57, -4.12) * mm, v(115.81, -3.81) * mm, v(117.06, -3.5) * mm, v(118.33, -3.19) * mm]});
            skFitSpline(sketch, "E1630", {"points": [v(118.33, -3.19) * mm, v(117.65, -2.07) * mm, v(116.99, -0.97) * mm, v(116.32, 0.15) * mm]});
            skFitSpline(sketch, "E1631", {"points": [v(116.32, 0.15) * mm, v(116.25, 0.07) * mm, v(116.2, 0.02) * mm, v(116.16, -0.04) * mm]});
            skFitSpline(sketch, "E1632", {"points": [v(116.16, -0.04) * mm, v(115.97, -0.34) * mm, v(115.78, -0.63) * mm, v(115.62, -0.94) * mm]});
            skFitSpline(sketch, "E1633", {"points": [v(115.62, -0.94) * mm, v(115.45, -1.25) * mm, v(115.18, -1.5) * mm, v(115.13, -1.86) * mm]});
            skFitSpline(sketch, "E1634", {"points": [v(115.13, -1.86) * mm, v(115.12, -1.88) * mm, v(115.1, -1.9) * mm, v(115.1, -1.92) * mm]});
            skFitSpline(sketch, "E1635", {"points": [v(115.1, -1.92) * mm, v(114.95, -2.07) * mm, v(114.95, -2.26) * mm, v(114.91, -2.43) * mm]});
            skFitSpline(sketch, "E1636", {"points": [v(114.91, -2.43) * mm, v(114.9, -2.53) * mm, v(114.87, -2.64) * mm, v(114.85, -2.74) * mm]});
            skFitSpline(sketch, "E1637", {"points": [v(114.85, -2.74) * mm, v(114.74, -3.18) * mm, v(114.63, -3.63) * mm, v(114.51, -4.07) * mm]});
            skFitSpline(sketch, "E1638", {"points": [v(97.74, -3.19) * mm, v(99, -3.5) * mm, v(100.26, -3.81) * mm, v(101.54, -4.13) * mm]});
            skFitSpline(sketch, "E1639", {"points": [v(101.54, -4.13) * mm, v(101.5, -3.95) * mm, v(101.49, -3.8) * mm, v(101.45, -3.65) * mm]});
            skFitSpline(sketch, "E1640", {"points": [v(101.45, -3.65) * mm, v(101.36, -3.28) * mm, v(101.26, -2.91) * mm, v(101.17, -2.54) * mm]});
            skFitSpline(sketch, "E1641", {"points": [v(101.17, -2.54) * mm, v(101.12, -2.31) * mm, v(101.1, -2.07) * mm, v(100.95, -1.87) * mm]});
            skFitSpline(sketch, "E1642", {"points": [v(100.95, -1.87) * mm, v(100.91, -1.83) * mm, v(100.91, -1.75) * mm, v(100.9, -1.7) * mm]});
            skFitSpline(sketch, "E1643", {"points": [v(100.9, -1.7) * mm, v(100.87, -1.64) * mm, v(100.87, -1.58) * mm, v(100.84, -1.54) * mm]});
            skFitSpline(sketch, "E1644", {"points": [v(100.84, -1.54) * mm, v(100.56, -1.07) * mm, v(100.27, -0.61) * mm, v(99.98, -0.15) * mm]});
            skFitSpline(sketch, "E1645", {"points": [v(99.98, -0.15) * mm, v(99.92, -0.05) * mm, v(99.84, 0.04) * mm, v(99.75, 0.16) * mm]});
            skFitSpline(sketch, "E1646", {"points": [v(99.75, 0.16) * mm, v(99.08, -0.97) * mm, v(98.41, -2.07) * mm, v(97.74, -3.19) * mm]});
            skFitSpline(sketch, "E1647", {"points": [v(107.13, 9.34) * mm, v(105.98, 10.04) * mm, v(104.88, 10.7) * mm, v(103.77, 11.37) * mm]});
            skFitSpline(sketch, "E1648", {"points": [v(103.77, 11.37) * mm, v(103.45, 10.09) * mm, v(103.14, 8.85) * mm, v(102.83, 7.59) * mm]});
            skFitSpline(sketch, "E1649", {"points": [v(102.83, 7.59) * mm, v(102.9, 7.59) * mm, v(102.93, 7.59) * mm, v(102.97, 7.6) * mm]});
            skFitSpline(sketch, "E1650", {"points": [v(102.97, 7.6) * mm, v(103.36, 7.69) * mm, v(103.76, 7.77) * mm, v(104.15, 7.87) * mm]});
            skFitSpline(sketch, "E1651", {"points": [v(104.15, 7.87) * mm, v(104.49, 7.96) * mm, v(104.85, 7.97) * mm, v(105.15, 8.18) * mm]});
            skFitSpline(sketch, "E1652", {"points": [v(105.15, 8.18) * mm, v(105.18, 8.2) * mm, v(105.24, 8.2) * mm, v(105.28, 8.22) * mm]});
            skFitSpline(sketch, "E1653", {"points": [v(105.28, 8.22) * mm, v(105.34, 8.24) * mm, v(105.4, 8.26) * mm, v(105.45, 8.3) * mm]});
            skFitSpline(sketch, "E1654", {"points": [v(105.45, 8.3) * mm, v(105.77, 8.48) * mm, v(106.08, 8.67) * mm, v(106.4, 8.87) * mm]});
            skFitSpline(sketch, "E1655", {"points": [v(106.4, 8.87) * mm, v(106.63, 9.02) * mm, v(106.86, 9.17) * mm, v(107.13, 9.34) * mm]});
            skFitSpline(sketch, "E1656", {"points": [v(111.62, -9.95) * mm, v(110.39, -9.2) * mm, v(109.2, -8.5) * mm, v(108.03, -7.8) * mm]});
            skFitSpline(sketch, "E1657", {"points": [v(108.03, -7.8) * mm, v(106.84, -8.5) * mm, v(105.67, -9.21) * mm, v(104.44, -9.95) * mm]});
            skFitSpline(sketch, "E1658", {"points": [v(104.44, -9.95) * mm, v(105.65, -10.73) * mm, v(106.81, -11.47) * mm, v(108.04, -12.12) * mm]});
            skFitSpline(sketch, "E1659", {"points": [v(108.04, -12.12) * mm, v(109.26, -11.45) * mm, v(110.43, -10.73) * mm, v(111.62, -9.95) * mm]});
            skFitSpline(sketch, "E1660", {"points": [v(119.07, 4.63) * mm, v(119.04, 4.59) * mm, v(119.02, 4.57) * mm, v(119, 4.55) * mm]});
            skFitSpline(sketch, "E1661", {"points": [v(119, 4.55) * mm, v(118.6, 3.9) * mm, v(118.19, 3.24) * mm, v(117.79, 2.58) * mm]});
            skFitSpline(sketch, "E1662", {"points": [v(117.79, 2.58) * mm, v(117.52, 2.14) * mm, v(117.28, 1.7) * mm, v(117, 1.26) * mm]});
            skFitSpline(sketch, "E1663", {"points": [v(117, 1.26) * mm, v(116.92, 1.13) * mm, v(116.92, 1.04) * mm, v(117, 0.9) * mm]});
            skFitSpline(sketch, "E1664", {"points": [v(117, 0.9) * mm, v(117.58, -0.05) * mm, v(118.14, -1) * mm, v(118.7, -1.96) * mm]});
            skFitSpline(sketch, "E1665", {"points": [v(118.7, -1.96) * mm, v(118.81, -2.13) * mm, v(118.93, -2.3) * mm, v(119.06, -2.49) * mm]});
            skFitSpline(sketch, "E1666", {"points": [v(119.06, -2.49) * mm, v(119.19, -2.3) * mm, v(119.3, -2.15) * mm, v(119.4, -2) * mm]});
            skFitSpline(sketch, "E1667", {"points": [v(119.4, -2) * mm, v(119.77, -1.4) * mm, v(120.12, -0.8) * mm, v(120.48, -0.21) * mm]});
            skFitSpline(sketch, "E1668", {"points": [v(120.48, -0.21) * mm, v(120.67, 0.09) * mm, v(120.86, 0.38) * mm, v(121.03, 0.69) * mm]});
            skFitSpline(sketch, "E1669", {"points": [v(121.03, 0.69) * mm, v(121.22, 1.02) * mm, v(121.23, 1.12) * mm, v(121.03, 1.45) * mm]});
            skFitSpline(sketch, "E1670", {"points": [v(121.03, 1.45) * mm, v(120.73, 1.98) * mm, v(120.43, 2.5) * mm, v(120.11, 3.02) * mm]});
            skFitSpline(sketch, "E1671", {"points": [v(120.11, 3.02) * mm, v(119.88, 3.4) * mm, v(119.63, 3.8) * mm, v(119.38, 4.17) * mm]});
            skFitSpline(sketch, "E1672", {"points": [v(119.38, 4.17) * mm, v(119.28, 4.32) * mm, v(119.18, 4.47) * mm, v(119.07, 4.63) * mm]});
            skFitSpline(sketch, "E1673", {"points": [v(118.37, -4.2) * mm, v(117.53, -4.39) * mm, v(116.76, -4.57) * mm, v(115.99, -4.76) * mm]});
            skFitSpline(sketch, "E1674", {"points": [v(115.99, -4.76) * mm, v(115.5, -4.89) * mm, v(115, -5.03) * mm, v(114.5, -5.14) * mm]});
            skFitSpline(sketch, "E1675", {"points": [v(114.5, -5.14) * mm, v(114.34, -5.18) * mm, v(114.28, -5.25) * mm, v(114.25, -5.4) * mm]});
            skFitSpline(sketch, "E1676", {"points": [v(114.25, -5.4) * mm, v(113.98, -6.48) * mm, v(113.7, -7.56) * mm, v(113.43, -8.65) * mm]});
            skFitSpline(sketch, "E1677", {"points": [v(113.43, -8.65) * mm, v(113.38, -8.83) * mm, v(113.36, -9.03) * mm, v(113.31, -9.24) * mm]});
            skFitSpline(sketch, "E1678", {"points": [v(113.31, -9.24) * mm, v(113.5, -9.21) * mm, v(113.65, -9.2) * mm, v(113.8, -9.16) * mm]});
            skFitSpline(sketch, "E1679", {"points": [v(113.8, -9.16) * mm, v(114.56, -8.97) * mm, v(115.33, -8.78) * mm, v(116.1, -8.6) * mm]});
            skFitSpline(sketch, "E1680", {"points": [v(116.1, -8.6) * mm, v(116.38, -8.53) * mm, v(116.67, -8.47) * mm, v(116.95, -8.39) * mm]});
            skFitSpline(sketch, "E1681", {"points": [v(116.95, -8.39) * mm, v(117.34, -8.28) * mm, v(117.4, -8.23) * mm, v(117.5, -7.84) * mm]});
            skFitSpline(sketch, "E1682", {"points": [v(117.5, -7.84) * mm, v(117.66, -7.25) * mm, v(117.8, -6.66) * mm, v(117.96, -6.06) * mm]});
            skFitSpline(sketch, "E1683", {"points": [v(117.96, -6.06) * mm, v(118.01, -5.85) * mm, v(118.05, -5.63) * mm, v(118.1, -5.4) * mm]});
            skFitSpline(sketch, "E1684", {"points": [v(118.1, -5.4) * mm, v(118.18, -5.02) * mm, v(118.27, -4.63) * mm, v(118.37, -4.2) * mm]});
            skFitSpline(sketch, "E1685", {"points": [v(104.45, 12.1) * mm, v(105.67, 11.36) * mm, v(106.85, 10.65) * mm, v(108.03, 9.94) * mm]});
            skFitSpline(sketch, "E1686", {"points": [v(108.03, 9.94) * mm, v(108.64, 10.3) * mm, v(109.24, 10.64) * mm, v(109.81, 11.01) * mm]});
            skFitSpline(sketch, "E1687", {"points": [v(109.81, 11.01) * mm, v(110.39, 11.39) * mm, v(111.02, 11.67) * mm, v(111.57, 12.1) * mm]});
            skFitSpline(sketch, "E1688", {"points": [v(111.57, 12.1) * mm, v(111.12, 12.49) * mm, v(108.46, 14.08) * mm, v(108, 14.25) * mm]});
            skFitSpline(sketch, "E1689", {"points": [v(108, 14.25) * mm, v(106.8, 13.6) * mm, v(105.64, 12.88) * mm, v(104.45, 12.1) * mm]});
            skFitSpline(sketch, "E1690", {"points": [v(99.16, 1.07) * mm, v(98.8, 1.67) * mm, v(98.47, 2.27) * mm, v(98.1, 2.85) * mm]});
            skFitSpline(sketch, "E1691", {"points": [v(98.1, 2.85) * mm, v(97.72, 3.43) * mm, v(97.44, 4.07) * mm, v(97, 4.61) * mm]});
            skFitSpline(sketch, "E1692", {"points": [v(97, 4.61) * mm, v(96.62, 4.14) * mm, v(95.12, 1.67) * mm, v(94.85, 1.04) * mm]});
            skFitSpline(sketch, "E1693", {"points": [v(94.85, 1.04) * mm, v(95.5, -0.14) * mm, v(96.22, -1.31) * mm, v(97.01, -2.5) * mm]});
            skFitSpline(sketch, "E1694", {"points": [v(97.01, -2.5) * mm, v(97.75, -1.3) * mm, v(98.45, -0.12) * mm, v(99.16, 1.07) * mm]});
            skFitSpline(sketch, "E1695", {"points": [v(118.35, 6.33) * mm, v(118.32, 6.51) * mm, v(118.3, 6.64) * mm, v(118.28, 6.76) * mm]});
            skFitSpline(sketch, "E1696", {"points": [v(118.28, 6.76) * mm, v(118.1, 7.54) * mm, v(117.9, 8.33) * mm, v(117.71, 9.1) * mm]});
            skFitSpline(sketch, "E1697", {"points": [v(117.71, 9.1) * mm, v(117.64, 9.4) * mm, v(117.58, 9.7) * mm, v(117.5, 10) * mm]});
            skFitSpline(sketch, "E1698", {"points": [v(117.5, 10) * mm, v(117.4, 10.38) * mm, v(117.34, 10.43) * mm, v(116.96, 10.54) * mm]});
            skFitSpline(sketch, "E1699", {"points": [v(116.96, 10.54) * mm, v(116.42, 10.68) * mm, v(115.88, 10.83) * mm, v(115.34, 10.96) * mm]});
            skFitSpline(sketch, "E1700", {"points": [v(115.34, 10.96) * mm, v(114.85, 11.08) * mm, v(114.36, 11.18) * mm, v(113.87, 11.3) * mm]});
            skFitSpline(sketch, "E1701", {"points": [v(113.87, 11.3) * mm, v(113.7, 11.33) * mm, v(113.52, 11.35) * mm, v(113.3, 11.4) * mm]});
            skFitSpline(sketch, "E1702", {"points": [v(113.3, 11.4) * mm, v(113.64, 10.02) * mm, v(113.97, 8.68) * mm, v(114.3, 7.34) * mm]});
            skFitSpline(sketch, "E1703", {"points": [v(114.3, 7.34) * mm, v(115.65, 7) * mm, v(116.98, 6.68) * mm, v(118.35, 6.33) * mm]});
            skFitSpline(sketch, "E1704", {"points": [v(97.71, -4.18) * mm, v(97.75, -4.38) * mm, v(97.76, -4.54) * mm, v(97.8, -4.69) * mm]});
            skFitSpline(sketch, "E1705", {"points": [v(97.8, -4.69) * mm, v(97.97, -5.41) * mm, v(98.15, -6.14) * mm, v(98.33, -6.87) * mm]});
            skFitSpline(sketch, "E1706", {"points": [v(98.33, -6.87) * mm, v(98.4, -7.17) * mm, v(98.47, -7.47) * mm, v(98.55, -7.77) * mm]});
            skFitSpline(sketch, "E1707", {"points": [v(98.55, -7.77) * mm, v(98.67, -8.22) * mm, v(98.73, -8.29) * mm, v(99.18, -8.4) * mm]});
            skFitSpline(sketch, "E1708", {"points": [v(99.18, -8.4) * mm, v(99.68, -8.54) * mm, v(100.2, -8.68) * mm, v(100.7, -8.8) * mm]});
            skFitSpline(sketch, "E1709", {"points": [v(100.7, -8.8) * mm, v(101.25, -8.94) * mm, v(101.8, -9.06) * mm, v(102.36, -9.18) * mm]});
            skFitSpline(sketch, "E1710", {"points": [v(102.36, -9.18) * mm, v(102.48, -9.2) * mm, v(102.6, -9.22) * mm, v(102.75, -9.24) * mm]});
            skFitSpline(sketch, "E1711", {"points": [v(102.75, -9.24) * mm, v(102.74, -9.19) * mm, v(102.74, -9.16) * mm, v(102.73, -9.13) * mm]});
            skFitSpline(sketch, "E1712", {"points": [v(102.73, -9.13) * mm, v(102.56, -8.4) * mm, v(102.39, -7.66) * mm, v(102.2, -6.92) * mm]});
            skFitSpline(sketch, "E1713", {"points": [v(102.2, -6.92) * mm, v(102.08, -6.42) * mm, v(101.93, -5.92) * mm, v(101.82, -5.42) * mm]});
            skFitSpline(sketch, "E1714", {"points": [v(101.82, -5.42) * mm, v(101.78, -5.24) * mm, v(101.7, -5.17) * mm, v(101.53, -5.13) * mm]});
            skFitSpline(sketch, "E1715", {"points": [v(101.53, -5.13) * mm, v(100.68, -4.93) * mm, v(99.83, -4.71) * mm, v(98.98, -4.5) * mm]});
            skFitSpline(sketch, "E1716", {"points": [v(98.98, -4.5) * mm, v(98.57, -4.4) * mm, v(98.16, -4.3) * mm, v(97.71, -4.18) * mm]});
            skFitSpline(sketch, "E1717", {"points": [v(102.77, 11.4) * mm, v(102.59, 11.36) * mm, v(102.45, 11.35) * mm, v(102.32, 11.32) * mm]});
            skFitSpline(sketch, "E1718", {"points": [v(102.32, 11.32) * mm, v(101.54, 11.13) * mm, v(100.76, 10.94) * mm, v(99.97, 10.75) * mm]});
            skFitSpline(sketch, "E1719", {"points": [v(99.97, 10.75) * mm, v(99.7, 10.68) * mm, v(99.41, 10.62) * mm, v(99.14, 10.54) * mm]});
            skFitSpline(sketch, "E1720", {"points": [v(99.14, 10.54) * mm, v(98.73, 10.43) * mm, v(98.67, 10.36) * mm, v(98.56, 9.95) * mm]});
            skFitSpline(sketch, "E1721", {"points": [v(98.56, 9.95) * mm, v(98.42, 9.45) * mm, v(98.29, 8.95) * mm, v(98.16, 8.45) * mm]});
            skFitSpline(sketch, "E1722", {"points": [v(98.16, 8.45) * mm, v(98.03, 7.9) * mm, v(97.9, 7.35) * mm, v(97.79, 6.8) * mm]});
            skFitSpline(sketch, "E1723", {"points": [v(97.79, 6.8) * mm, v(97.76, 6.66) * mm, v(97.75, 6.52) * mm, v(97.73, 6.38) * mm]});
            skFitSpline(sketch, "E1724", {"points": [v(97.73, 6.38) * mm, v(97.77, 6.37) * mm, v(97.78, 6.36) * mm, v(97.8, 6.37) * mm]});
            skFitSpline(sketch, "E1725", {"points": [v(97.8, 6.37) * mm, v(98.55, 6.54) * mm, v(99.3, 6.72) * mm, v(100.05, 6.9) * mm]});
            skFitSpline(sketch, "E1726", {"points": [v(100.05, 6.9) * mm, v(100.56, 7.02) * mm, v(101.05, 7.17) * mm, v(101.56, 7.29) * mm]});
            skFitSpline(sketch, "E1727", {"points": [v(101.56, 7.29) * mm, v(101.71, 7.33) * mm, v(101.78, 7.39) * mm, v(101.82, 7.54) * mm]});
            skFitSpline(sketch, "E1728", {"points": [v(101.82, 7.54) * mm, v(102.01, 8.37) * mm, v(102.22, 9.2) * mm, v(102.43, 10.03) * mm]});
            skFitSpline(sketch, "E1729", {"points": [v(102.43, 10.03) * mm, v(102.54, 10.47) * mm, v(102.65, 10.9) * mm, v(102.77, 11.4) * mm]});
            skFitSpline(sketch, "E1730", {"points": [v(97.66, -8.26) * mm, v(97.38, -7.1) * mm, v(97.1, -5.95) * mm, v(96.82, -4.8) * mm]});
            skFitSpline(sketch, "E1731", {"points": [v(96.82, -4.8) * mm, v(96.79, -4.82) * mm, v(96.77, -4.82) * mm, v(96.76, -4.83) * mm]});
            skFitSpline(sketch, "E1732", {"points": [v(96.76, -4.83) * mm, v(96.52, -5.25) * mm, v(96.28, -5.66) * mm, v(96.04, -6.08) * mm]});
            skFitSpline(sketch, "E1733", {"points": [v(96.04, -6.08) * mm, v(95.96, -6.21) * mm, v(95.88, -6.35) * mm, v(95.8, -6.49) * mm]});
            skFitSpline(sketch, "E1734", {"points": [v(95.8, -6.49) * mm, v(95.4, -7.19) * mm, v(95, -7.88) * mm, v(94.58, -8.58) * mm]});
            skFitSpline(sketch, "E1735", {"points": [v(94.58, -8.58) * mm, v(94.52, -8.68) * mm, v(94.44, -8.77) * mm, v(94.35, -8.84) * mm]});
            skFitSpline(sketch, "E1736", {"points": [v(94.35, -8.84) * mm, v(94.16, -8.97) * mm, v(93.93, -8.95) * mm, v(93.77, -8.81) * mm]});
            skFitSpline(sketch, "E1737", {"points": [v(93.77, -8.81) * mm, v(93.6, -8.67) * mm, v(93.54, -8.44) * mm, v(93.65, -8.23) * mm]});
            skFitSpline(sketch, "E1738", {"points": [v(93.65, -8.23) * mm, v(93.78, -7.96) * mm, v(93.94, -7.71) * mm, v(94.09, -7.46) * mm]});
            skFitSpline(sketch, "E1739", {"points": [v(94.09, -7.46) * mm, v(94.32, -7.05) * mm, v(94.56, -6.64) * mm, v(94.8, -6.23) * mm]});
            skFitSpline(sketch, "E1740", {"points": [v(94.8, -6.23) * mm, v(94.28, -6) * mm, v(93.73, -5.96) * mm, v(93.23, -5.8) * mm]});
            skFitSpline(sketch, "E1741", {"points": [v(93.23, -5.8) * mm, v(92.7, -6.5) * mm, v(92.35, -7.26) * mm, v(92, -8.03) * mm]});
            skFitSpline(sketch, "E1742", {"points": [v(92, -8.03) * mm, v(91.96, -8.1) * mm, v(91.94, -8.18) * mm, v(91.91, -8.25) * mm]});
            skFitSpline(sketch, "E1743", {"points": [v(91.91, -8.25) * mm, v(91.8, -8.55) * mm, v(91.53, -8.68) * mm, v(91.26, -8.57) * mm]});
            skFitSpline(sketch, "E1744", {"points": [v(91.26, -8.57) * mm, v(90.98, -8.45) * mm, v(90.84, -8.16) * mm, v(90.98, -7.88) * mm]});
            skFitSpline(sketch, "E1745", {"points": [v(90.98, -7.88) * mm, v(91.36, -7.13) * mm, v(91.66, -6.33) * mm, v(92.16, -5.64) * mm]});
            skFitSpline(sketch, "E1746", {"points": [v(92.16, -5.64) * mm, v(92.2, -5.59) * mm, v(92.23, -5.53) * mm, v(92.28, -5.45) * mm]});
            skFitSpline(sketch, "E1747", {"points": [v(92.28, -5.45) * mm, v(92.15, -5.42) * mm, v(92.03, -5.39) * mm, v(91.92, -5.37) * mm]});
            skFitSpline(sketch, "E1748", {"points": [v(91.92, -5.37) * mm, v(91.4, -5.28) * mm, v(90.9, -5.1) * mm, v(90.4, -4.92) * mm]});
            skFitSpline(sketch, "E1749", {"points": [v(90.4, -4.92) * mm, v(90.19, -4.85) * mm, v(89.97, -4.77) * mm, v(89.75, -4.69) * mm]});
            skFitSpline(sketch, "E1750", {"points": [v(89.75, -4.69) * mm, v(89.68, -4.66) * mm, v(89.6, -4.64) * mm, v(89.53, -4.6) * mm]});
            skFitSpline(sketch, "E1751", {"points": [v(89.53, -4.6) * mm, v(89.31, -4.45) * mm, v(89.24, -4.18) * mm, v(89.37, -3.94) * mm]});
            skFitSpline(sketch, "E1752", {"points": [v(89.37, -3.94) * mm, v(89.49, -3.7) * mm, v(89.74, -3.61) * mm, v(90, -3.71) * mm]});
            skFitSpline(sketch, "E1753", {"points": [v(90, -3.71) * mm, v(90.8, -4.04) * mm, v(91.6, -4.35) * mm, v(92.46, -4.48) * mm]});
            skFitSpline(sketch, "E1754", {"points": [v(92.46, -4.48) * mm, v(92.53, -4.5) * mm, v(92.6, -4.52) * mm, v(92.68, -4.55) * mm]});
            skFitSpline(sketch, "E1755", {"points": [v(92.68, -4.55) * mm, v(92.95, -4.07) * mm, v(93.3, -3.65) * mm, v(93.51, -3.11) * mm]});
            skFitSpline(sketch, "E1756", {"points": [v(93.51, -3.11) * mm, v(92.8, -2.93) * mm, v(92.1, -2.75) * mm, v(91.42, -2.57) * mm]});
            skFitSpline(sketch, "E1757", {"points": [v(91.42, -2.57) * mm, v(91.2, -2.5) * mm, v(91, -2.4) * mm, v(90.96, -2.16) * mm]});
            skFitSpline(sketch, "E1758", {"points": [v(90.96, -2.16) * mm, v(90.9, -1.79) * mm, v(91.23, -1.48) * mm, v(91.6, -1.58) * mm]});
            skFitSpline(sketch, "E1759", {"points": [v(91.6, -1.58) * mm, v(92.19, -1.74) * mm, v(92.76, -1.9) * mm, v(93.34, -2.06) * mm]});
            skFitSpline(sketch, "E1760", {"points": [v(93.34, -2.06) * mm, v(93.52, -2.11) * mm, v(93.71, -2.15) * mm, v(93.9, -2.2) * mm]});
            skFitSpline(sketch, "E1761", {"points": [v(93.9, -2.2) * mm, v(94.5, -2.35) * mm, v(95.1, -2.51) * mm, v(95.7, -2.67) * mm]});
            skFitSpline(sketch, "E1762", {"points": [v(95.7, -2.67) * mm, v(95.78, -2.69) * mm, v(95.85, -2.7) * mm, v(95.97, -2.73) * mm]});
            skFitSpline(sketch, "E1763", {"points": [v(95.97, -2.73) * mm, v(95.33, -1.69) * mm, v(94.72, -0.68) * mm, v(94.09, 0.35) * mm]});
            skFitSpline(sketch, "E1764", {"points": [v(94.09, 0.35) * mm, v(93.85, 0.13) * mm, v(93.6, -0.09) * mm, v(93.36, -0.3) * mm]});
            skFitSpline(sketch, "E1765", {"points": [v(93.36, -0.3) * mm, v(93.25, -0.4) * mm, v(93.15, -0.52) * mm, v(93.04, -0.63) * mm]});
            skFitSpline(sketch, "E1766", {"points": [v(93.04, -0.63) * mm, v(92.88, -0.78) * mm, v(92.69, -0.82) * mm, v(92.49, -0.73) * mm]});
            skFitSpline(sketch, "E1767", {"points": [v(92.49, -0.73) * mm, v(92.27, -0.63) * mm, v(92.17, -0.44) * mm, v(92.16, -0.2) * mm]});
            skFitSpline(sketch, "E1768", {"points": [v(92.16, -0.2) * mm, v(92.15, 0.01) * mm, v(92.27, 0.17) * mm, v(92.48, 0.25) * mm]});
            skFitSpline(sketch, "E1769", {"points": [v(92.48, 0.25) * mm, v(92.51, 0.27) * mm, v(92.56, 0.28) * mm, v(92.58, 0.3) * mm]});
            skFitSpline(sketch, "E1770", {"points": [v(92.58, 0.3) * mm, v(92.86, 0.55) * mm, v(93.14, 0.8) * mm, v(93.43, 1.08) * mm]});
            skFitSpline(sketch, "E1771", {"points": [v(93.43, 1.08) * mm, v(93.27, 1.22) * mm, v(93.13, 1.36) * mm, v(92.98, 1.48) * mm]});
            skFitSpline(sketch, "E1772", {"points": [v(92.98, 1.48) * mm, v(92.78, 1.64) * mm, v(92.62, 1.84) * mm, v(92.38, 1.95) * mm]});
            skFitSpline(sketch, "E1773", {"points": [v(92.38, 1.95) * mm, v(92.13, 2.08) * mm, v(92.09, 2.42) * mm, v(92.26, 2.69) * mm]});
            skFitSpline(sketch, "E1774", {"points": [v(92.26, 2.69) * mm, v(92.42, 2.92) * mm, v(92.72, 3) * mm, v(92.96, 2.84) * mm]});
            skFitSpline(sketch, "E1775", {"points": [v(92.96, 2.84) * mm, v(93.05, 2.78) * mm, v(93.12, 2.7) * mm, v(93.2, 2.61) * mm]});
            skFitSpline(sketch, "E1776", {"points": [v(93.2, 2.61) * mm, v(93.5, 2.34) * mm, v(93.79, 2.07) * mm, v(94.09, 1.8) * mm]});
            skFitSpline(sketch, "E1777", {"points": [v(94.09, 1.8) * mm, v(94.71, 2.82) * mm, v(95.33, 3.83) * mm, v(95.96, 4.87) * mm]});
            skFitSpline(sketch, "E1778", {"points": [v(95.96, 4.87) * mm, v(95.87, 4.85) * mm, v(95.82, 4.85) * mm, v(95.76, 4.83) * mm]});
            skFitSpline(sketch, "E1779", {"points": [v(95.76, 4.83) * mm, v(95.05, 4.66) * mm, v(94.34, 4.48) * mm, v(93.63, 4.3) * mm]});
            skFitSpline(sketch, "E1780", {"points": [v(93.63, 4.3) * mm, v(92.98, 4.12) * mm, v(92.34, 3.94) * mm, v(91.7, 3.75) * mm]});
            skFitSpline(sketch, "E1781", {"points": [v(91.7, 3.75) * mm, v(91.54, 3.71) * mm, v(91.4, 3.7) * mm, v(91.27, 3.76) * mm]});
            skFitSpline(sketch, "E1782", {"points": [v(91.27, 3.76) * mm, v(91.1, 3.83) * mm, v(90.98, 3.96) * mm, v(90.96, 4.15) * mm]});
            skFitSpline(sketch, "E1783", {"points": [v(90.96, 4.15) * mm, v(90.94, 4.35) * mm, v(91, 4.51) * mm, v(91.18, 4.62) * mm]});
            skFitSpline(sketch, "E1784", {"points": [v(91.18, 4.62) * mm, v(91.25, 4.66) * mm, v(91.33, 4.7) * mm, v(91.4, 4.71) * mm]});
            skFitSpline(sketch, "E1785", {"points": [v(91.4, 4.71) * mm, v(92.1, 4.9) * mm, v(92.8, 5.07) * mm, v(93.5, 5.26) * mm]});
            skFitSpline(sketch, "E1786", {"points": [v(93.5, 5.26) * mm, v(93.31, 5.8) * mm, v(92.94, 6.2) * mm, v(92.7, 6.67) * mm]});
            skFitSpline(sketch, "E1787", {"points": [v(92.7, 6.67) * mm, v(91.82, 6.56) * mm, v(91.01, 6.26) * mm, v(90.2, 5.96) * mm]});
            skFitSpline(sketch, "E1788", {"points": [v(90.2, 5.96) * mm, v(90.14, 5.94) * mm, v(90.08, 5.9) * mm, v(90.01, 5.87) * mm]});
            skFitSpline(sketch, "E1789", {"points": [v(90.01, 5.87) * mm, v(89.75, 5.76) * mm, v(89.48, 5.85) * mm, v(89.36, 6.1) * mm]});
            skFitSpline(sketch, "E1790", {"points": [v(89.36, 6.1) * mm, v(89.24, 6.36) * mm, v(89.33, 6.64) * mm, v(89.58, 6.77) * mm]});
            skFitSpline(sketch, "E1791", {"points": [v(89.58, 6.77) * mm, v(89.6, 6.79) * mm, v(89.62, 6.8) * mm, v(89.65, 6.8) * mm]});
            skFitSpline(sketch, "E1792", {"points": [v(89.65, 6.8) * mm, v(90.23, 7) * mm, v(90.8, 7.2) * mm, v(91.4, 7.4) * mm]});
            skFitSpline(sketch, "E1793", {"points": [v(91.4, 7.4) * mm, v(91.63, 7.47) * mm, v(91.87, 7.5) * mm, v(92.12, 7.55) * mm]});
            skFitSpline(sketch, "E1794", {"points": [v(92.12, 7.55) * mm, v(92.16, 7.56) * mm, v(92.2, 7.58) * mm, v(92.28, 7.6) * mm]});
            skFitSpline(sketch, "E1795", {"points": [v(92.28, 7.6) * mm, v(92.21, 7.71) * mm, v(92.16, 7.8) * mm, v(92.1, 7.9) * mm]});
            skFitSpline(sketch, "E1796", {"points": [v(92.1, 7.9) * mm, v(91.78, 8.34) * mm, v(91.56, 8.84) * mm, v(91.32, 9.32) * mm]});
            skFitSpline(sketch, "E1797", {"points": [v(91.32, 9.32) * mm, v(91.2, 9.54) * mm, v(91.1, 9.77) * mm, v(91, 10) * mm]});
            skFitSpline(sketch, "E1798", {"points": [v(91, 10) * mm, v(90.91, 10.16) * mm, v(90.9, 10.33) * mm, v(91, 10.5) * mm]});
            skFitSpline(sketch, "E1799", {"points": [v(91, 10.5) * mm, v(91.1, 10.67) * mm, v(91.26, 10.77) * mm, v(91.45, 10.76) * mm]});
            skFitSpline(sketch, "E1800", {"points": [v(91.45, 10.76) * mm, v(91.66, 10.75) * mm, v(91.8, 10.64) * mm, v(91.9, 10.44) * mm]});
            skFitSpline(sketch, "E1801", {"points": [v(91.9, 10.44) * mm, v(92.05, 10.1) * mm, v(92.2, 9.74) * mm, v(92.37, 9.4) * mm]});
            skFitSpline(sketch, "E1802", {"points": [v(92.37, 9.4) * mm, v(92.56, 9.04) * mm, v(92.77, 8.69) * mm, v(92.97, 8.33) * mm]});
            skFitSpline(sketch, "E1803", {"points": [v(92.97, 8.33) * mm, v(93.04, 8.21) * mm, v(93.12, 8.1) * mm, v(93.21, 7.95) * mm]});
            skFitSpline(sketch, "E1804", {"points": [v(93.21, 7.95) * mm, v(93.72, 8.1) * mm, v(94.27, 8.16) * mm, v(94.8, 8.37) * mm]});
            skFitSpline(sketch, "E1805", {"points": [v(94.8, 8.37) * mm, v(94.57, 8.78) * mm, v(94.35, 9.16) * mm, v(94.13, 9.55) * mm]});
            skFitSpline(sketch, "E1806", {"points": [v(94.13, 9.55) * mm, v(93.99, 9.8) * mm, v(93.84, 10.03) * mm, v(93.7, 10.27) * mm]});
            skFitSpline(sketch, "E1807", {"points": [v(93.7, 10.27) * mm, v(93.69, 10.28) * mm, v(93.68, 10.3) * mm, v(93.68, 10.31) * mm]});
            skFitSpline(sketch, "E1808", {"points": [v(93.68, 10.31) * mm, v(93.53, 10.6) * mm, v(93.6, 10.88) * mm, v(93.85, 11.02) * mm]});
            skFitSpline(sketch, "E1809", {"points": [v(93.85, 11.02) * mm, v(94.1, 11.15) * mm, v(94.42, 11.03) * mm, v(94.57, 10.77) * mm]});
            skFitSpline(sketch, "E1810", {"points": [v(94.57, 10.77) * mm, v(94.72, 10.49) * mm, v(94.87, 10.2) * mm, v(95.03, 9.93) * mm]});
            skFitSpline(sketch, "E1811", {"points": [v(95.03, 9.93) * mm, v(95.32, 9.45) * mm, v(95.61, 8.98) * mm, v(95.9, 8.5) * mm]});
            skFitSpline(sketch, "E1812", {"points": [v(95.9, 8.5) * mm, v(96.16, 8.04) * mm, v(96.42, 7.58) * mm, v(96.68, 7.12) * mm]});
            skFitSpline(sketch, "E1813", {"points": [v(96.68, 7.12) * mm, v(96.71, 7.07) * mm, v(96.74, 7.01) * mm, v(96.8, 6.92) * mm]});
            skFitSpline(sketch, "E1814", {"points": [v(96.8, 6.92) * mm, v(97, 7.52) * mm, v(97.08, 8.1) * mm, v(97.22, 8.68) * mm]});
            skFitSpline(sketch, "E1815", {"points": [v(97.22, 8.68) * mm, v(97.36, 9.26) * mm, v(97.52, 9.83) * mm, v(97.68, 10.43) * mm]});
            skFitSpline(sketch, "E1816", {"points": [v(97.68, 10.43) * mm, v(97.2, 10.45) * mm, v(96.76, 10.46) * mm, v(96.32, 10.48) * mm]});
            skFitSpline(sketch, "E1817", {"points": [v(96.32, 10.48) * mm, v(96.23, 10.48) * mm, v(96.14, 10.48) * mm, v(96.06, 10.5) * mm]});
            skFitSpline(sketch, "E1818", {"points": [v(96.06, 10.5) * mm, v(95.78, 10.6) * mm, v(95.66, 10.89) * mm, v(95.77, 11.17) * mm]});
            skFitSpline(sketch, "E1819", {"points": [v(95.77, 11.17) * mm, v(95.87, 11.47) * mm, v(96.14, 11.61) * mm, v(96.41, 11.5) * mm]});
            skFitSpline(sketch, "E1820", {"points": [v(96.41, 11.5) * mm, v(96.54, 11.45) * mm, v(96.67, 11.44) * mm, v(96.8, 11.44) * mm]});
            skFitSpline(sketch, "E1821", {"points": [v(96.8, 11.44) * mm, v(97.04, 11.43) * mm, v(97.27, 11.41) * mm, v(97.5, 11.4) * mm]});
            skFitSpline(sketch, "E1822", {"points": [v(97.5, 11.4) * mm, v(97.57, 11.4) * mm, v(97.64, 11.4) * mm, v(97.7, 11.4) * mm]});
            skFitSpline(sketch, "E1823", {"points": [v(97.7, 11.4) * mm, v(97.7, 11.77) * mm, v(97.69, 12.12) * mm, v(97.67, 12.47) * mm]});
            skFitSpline(sketch, "E1824", {"points": [v(97.67, 12.47) * mm, v(97.67, 12.53) * mm, v(97.64, 12.6) * mm, v(97.62, 12.65) * mm]});
            skFitSpline(sketch, "E1825", {"points": [v(97.62, 12.65) * mm, v(97.55, 12.85) * mm, v(97.55, 13.05) * mm, v(97.71, 13.2) * mm]});
            skFitSpline(sketch, "E1826", {"points": [v(97.71, 13.2) * mm, v(97.88, 13.37) * mm, v(98.09, 13.42) * mm, v(98.31, 13.35) * mm]});
            skFitSpline(sketch, "E1827", {"points": [v(98.31, 13.35) * mm, v(98.5, 13.28) * mm, v(98.63, 13.1) * mm, v(98.63, 12.86) * mm]});
            skFitSpline(sketch, "E1828", {"points": [v(98.63, 12.86) * mm, v(98.64, 12.55) * mm, v(98.64, 12.23) * mm, v(98.65, 11.92) * mm]});
            skFitSpline(sketch, "E1829", {"points": [v(98.65, 11.92) * mm, v(98.66, 11.77) * mm, v(98.68, 11.6) * mm, v(98.7, 11.45) * mm]});
            skFitSpline(sketch, "E1830", {"points": [v(98.7, 11.45) * mm, v(99.85, 11.73) * mm, v(101, 12) * mm, v(102.19, 12.3) * mm]});
            skFitSpline(sketch, "E1831", {"points": [v(102.19, 12.3) * mm, v(102.1, 12.36) * mm, v(102.04, 12.4) * mm, v(101.97, 12.44) * mm]});
            skFitSpline(sketch, "E1832", {"points": [v(101.97, 12.44) * mm, v(101.37, 12.8) * mm, v(100.77, 13.16) * mm, v(100.16, 13.51) * mm]});
            skFitSpline(sketch, "E1833", {"points": [v(100.16, 13.51) * mm, v(99.57, 13.85) * mm, v(98.98, 14.19) * mm, v(98.39, 14.51) * mm]});
            skFitSpline(sketch, "E1834", {"points": [v(98.39, 14.51) * mm, v(98.12, 14.66) * mm, v(97.97, 14.92) * mm, v(98.06, 15.18) * mm]});
            skFitSpline(sketch, "E1835", {"points": [v(98.06, 15.18) * mm, v(98.14, 15.43) * mm, v(98.4, 15.57) * mm, v(98.65, 15.5) * mm]});
            skFitSpline(sketch, "E1836", {"points": [v(98.65, 15.5) * mm, v(98.73, 15.46) * mm, v(98.81, 15.42) * mm, v(98.89, 15.38) * mm]});
            skFitSpline(sketch, "E1837", {"points": [v(98.89, 15.38) * mm, v(99.5, 15.03) * mm, v(100.1, 14.67) * mm, v(100.73, 14.3) * mm]});
            skFitSpline(sketch, "E1838", {"points": [v(100.73, 14.3) * mm, v(100.96, 14.83) * mm, v(101, 15.38) * mm, v(101.15, 15.88) * mm]});
            skFitSpline(sketch, "E1839", {"points": [v(101.15, 15.88) * mm, v(100.46, 16.4) * mm, v(99.7, 16.76) * mm, v(98.94, 17.1) * mm]});
            skFitSpline(sketch, "E1840", {"points": [v(98.94, 17.1) * mm, v(98.86, 17.14) * mm, v(98.78, 17.17) * mm, v(98.7, 17.2) * mm]});
            skFitSpline(sketch, "E1841", {"points": [v(98.7, 17.2) * mm, v(98.4, 17.31) * mm, v(98.28, 17.58) * mm, v(98.4, 17.85) * mm]});
            skFitSpline(sketch, "E1842", {"points": [v(98.4, 17.85) * mm, v(98.51, 18.14) * mm, v(98.8, 18.26) * mm, v(99.09, 18.12) * mm]});
            skFitSpline(sketch, "E1843", {"points": [v(99.09, 18.12) * mm, v(99.85, 17.74) * mm, v(100.65, 17.43) * mm, v(101.35, 16.93) * mm]});
            skFitSpline(sketch, "E1844", {"points": [v(101.35, 16.93) * mm, v(101.4, 16.9) * mm, v(101.44, 16.87) * mm, v(101.51, 16.84) * mm]});
            skFitSpline(sketch, "E1845", {"points": [v(101.51, 16.84) * mm, v(101.55, 17.03) * mm, v(101.58, 17.22) * mm, v(101.63, 17.4) * mm]});
            skFitSpline(sketch, "E1846", {"points": [v(101.63, 17.4) * mm, v(101.76, 17.83) * mm, v(101.9, 18.28) * mm, v(102.04, 18.72) * mm]});
            skFitSpline(sketch, "E1847", {"points": [v(102.04, 18.72) * mm, v(102.12, 18.95) * mm, v(102.2, 19.18) * mm, v(102.29, 19.42) * mm]});
            skFitSpline(sketch, "E1848", {"points": [v(102.29, 19.42) * mm, v(102.38, 19.69) * mm, v(102.54, 19.8) * mm, v(102.8, 19.79) * mm]});
            skFitSpline(sketch, "E1849", {"points": [v(102.8, 19.79) * mm, v(103.15, 19.78) * mm, v(103.37, 19.46) * mm, v(103.25, 19.13) * mm]});
            skFitSpline(sketch, "E1850", {"points": [v(103.25, 19.13) * mm, v(103.11, 18.76) * mm, v(102.98, 18.39) * mm, v(102.83, 18.01) * mm]});
            skFitSpline(sketch, "E1851", {"points": [v(102.83, 18.01) * mm, v(102.67, 17.6) * mm, v(102.57, 17.16) * mm, v(102.49, 16.72) * mm]});
            skFitSpline(sketch, "E1852", {"points": [v(102.49, 16.72) * mm, v(102.47, 16.62) * mm, v(102.44, 16.52) * mm, v(102.42, 16.41) * mm]});
            skFitSpline(sketch, "E1853", {"points": [v(102.42, 16.41) * mm, v(102.88, 16.14) * mm, v(103.33, 15.86) * mm, v(103.82, 15.57) * mm]});
            skFitSpline(sketch, "E1854", {"points": [v(103.82, 15.57) * mm, v(103.89, 15.8) * mm, v(103.95, 16.01) * mm, v(104, 16.21) * mm]});
            skFitSpline(sketch, "E1855", {"points": [v(104, 16.21) * mm, v(104.14, 16.7) * mm, v(104.27, 17.2) * mm, v(104.4, 17.7) * mm]});
            skFitSpline(sketch, "E1856", {"points": [v(104.4, 17.7) * mm, v(104.46, 17.97) * mm, v(104.61, 18.13) * mm, v(104.83, 18.15) * mm]});
            skFitSpline(sketch, "E1857", {"points": [v(104.83, 18.15) * mm, v(105.2, 18.2) * mm, v(105.46, 17.86) * mm, v(105.37, 17.5) * mm]});
            skFitSpline(sketch, "E1858", {"points": [v(105.37, 17.5) * mm, v(105.23, 16.93) * mm, v(105.06, 16.37) * mm, v(104.9, 15.81) * mm]});
            skFitSpline(sketch, "E1859", {"points": [v(104.9, 15.81) * mm, v(104.86, 15.62) * mm, v(104.81, 15.42) * mm, v(104.76, 15.23) * mm]});
            skFitSpline(sketch, "E1860", {"points": [v(104.76, 15.23) * mm, v(104.6, 14.62) * mm, v(104.45, 14.01) * mm, v(104.29, 13.4) * mm]});
            skFitSpline(sketch, "E1861", {"points": [v(104.29, 13.4) * mm, v(104.27, 13.33) * mm, v(104.26, 13.27) * mm, v(104.23, 13.15) * mm]});
            skFitSpline(sketch, "E1862", {"points": [v(104.23, 13.15) * mm, v(104.79, 13.45) * mm, v(105.26, 13.8) * mm, v(105.76, 14.1) * mm]});
            skFitSpline(sketch, "E1863", {"points": [v(105.76, 14.1) * mm, v(106.27, 14.4) * mm, v(106.78, 14.7) * mm, v(107.32, 15) * mm]});
            skFitSpline(sketch, "E1864", {"points": [v(107.32, 15) * mm, v(107.15, 15.2) * mm, v(107, 15.37) * mm, v(106.84, 15.54) * mm]});
            skFitSpline(sketch, "E1865", {"points": [v(106.84, 15.54) * mm, v(106.67, 15.73) * mm, v(106.49, 15.9) * mm, v(106.32, 16.08) * mm]});
            skFitSpline(sketch, "E1866", {"points": [v(106.32, 16.08) * mm, v(106.14, 16.28) * mm, v(106.14, 16.52) * mm, v(106.28, 16.72) * mm]});
            skFitSpline(sketch, "E1867", {"points": [v(106.28, 16.72) * mm, v(106.43, 16.91) * mm, v(106.74, 17.01) * mm, v(106.94, 16.9) * mm]});
            skFitSpline(sketch, "E1868", {"points": [v(106.94, 16.9) * mm, v(107.04, 16.85) * mm, v(107.12, 16.75) * mm, v(107.2, 16.66) * mm]});
            skFitSpline(sketch, "E1869", {"points": [v(107.2, 16.66) * mm, v(107.23, 16.62) * mm, v(107.24, 16.54) * mm, v(107.28, 16.5) * mm]});
            skFitSpline(sketch, "E1870", {"points": [v(107.28, 16.5) * mm, v(107.52, 16.23) * mm, v(107.77, 15.97) * mm, v(108.02, 15.7) * mm]});
            skFitSpline(sketch, "E1871", {"points": [v(108.02, 15.7) * mm, v(108.07, 15.73) * mm, v(108.11, 15.76) * mm, v(108.15, 15.8) * mm]});
            skFitSpline(sketch, "E1872", {"points": [v(108.15, 15.8) * mm, v(108.35, 16.02) * mm, v(108.55, 16.23) * mm, v(108.74, 16.46) * mm]});
            skFitSpline(sketch, "E1873", {"points": [v(108.74, 16.46) * mm, v(108.8, 16.51) * mm, v(108.83, 16.59) * mm, v(108.86, 16.66) * mm]});
            skFitSpline(sketch, "E1874", {"points": [v(108.86, 16.66) * mm, v(108.95, 16.84) * mm, v(109.1, 16.95) * mm, v(109.3, 16.95) * mm]});
            skFitSpline(sketch, "E1875", {"points": [v(109.3, 16.95) * mm, v(109.52, 16.95) * mm, v(109.72, 16.86) * mm, v(109.83, 16.64) * mm]});
            skFitSpline(sketch, "E1876", {"points": [v(109.83, 16.64) * mm, v(109.92, 16.45) * mm, v(109.9, 16.26) * mm, v(109.76, 16.1) * mm]});
            skFitSpline(sketch, "E1877", {"points": [v(109.76, 16.1) * mm, v(109.53, 15.84) * mm, v(109.28, 15.6) * mm, v(109.04, 15.33) * mm]});
            skFitSpline(sketch, "E1878", {"points": [v(109.04, 15.33) * mm, v(108.95, 15.23) * mm, v(108.86, 15.13) * mm, v(108.76, 15.02) * mm]});
            skFitSpline(sketch, "E1879", {"points": [v(108.76, 15.02) * mm, v(109.78, 14.4) * mm, v(110.8, 13.78) * mm, v(111.84, 13.14) * mm]});
            skFitSpline(sketch, "E1880", {"points": [v(111.84, 13.14) * mm, v(111.81, 13.25) * mm, v(111.8, 13.31) * mm, v(111.79, 13.38) * mm]});
            skFitSpline(sketch, "E1881", {"points": [v(111.79, 13.38) * mm, v(111.6, 14.07) * mm, v(111.44, 14.77) * mm, v(111.26, 15.46) * mm]});
            skFitSpline(sketch, "E1882", {"points": [v(111.26, 15.46) * mm, v(111.08, 16.11) * mm, v(110.9, 16.76) * mm, v(110.72, 17.4) * mm]});
            skFitSpline(sketch, "E1883", {"points": [v(110.72, 17.4) * mm, v(110.7, 17.5) * mm, v(110.68, 17.6) * mm, v(110.69, 17.68) * mm]});
            skFitSpline(sketch, "E1884", {"points": [v(110.69, 17.68) * mm, v(110.7, 17.93) * mm, v(110.87, 18.12) * mm, v(111.1, 18.15) * mm]});
            skFitSpline(sketch, "E1885", {"points": [v(111.1, 18.15) * mm, v(111.34, 18.19) * mm, v(111.55, 18.06) * mm, v(111.63, 17.81) * mm]});
            skFitSpline(sketch, "E1886", {"points": [v(111.63, 17.81) * mm, v(111.71, 17.56) * mm, v(111.77, 17.3) * mm, v(111.84, 17.05) * mm]});
            skFitSpline(sketch, "E1887", {"points": [v(111.84, 17.05) * mm, v(111.97, 16.57) * mm, v(112.1, 16.1) * mm, v(112.23, 15.6) * mm]});
            skFitSpline(sketch, "E1888", {"points": [v(112.23, 15.6) * mm, v(112.75, 15.8) * mm, v(113.17, 16.16) * mm, v(113.64, 16.4) * mm]});
            skFitSpline(sketch, "E1889", {"points": [v(113.64, 16.4) * mm, v(113.52, 17.12) * mm, v(113.33, 17.81) * mm, v(113.07, 18.48) * mm]});
            skFitSpline(sketch, "E1890", {"points": [v(113.07, 18.48) * mm, v(112.98, 18.7) * mm, v(112.9, 18.91) * mm, v(112.81, 19.13) * mm]});
            skFitSpline(sketch, "E1891", {"points": [v(112.81, 19.13) * mm, v(112.72, 19.38) * mm, v(112.83, 19.65) * mm, v(113.07, 19.75) * mm]});
            skFitSpline(sketch, "E1892", {"points": [v(113.07, 19.75) * mm, v(113.33, 19.85) * mm, v(113.58, 19.78) * mm, v(113.72, 19.55) * mm]});
            skFitSpline(sketch, "E1893", {"points": [v(113.72, 19.55) * mm, v(113.74, 19.5) * mm, v(113.76, 19.46) * mm, v(113.78, 19.42) * mm]});
            skFitSpline(sketch, "E1894", {"points": [v(113.78, 19.42) * mm, v(113.9, 19.07) * mm, v(114, 18.72) * mm, v(114.14, 18.38) * mm]});
            skFitSpline(sketch, "E1895", {"points": [v(114.14, 18.38) * mm, v(114.3, 17.92) * mm, v(114.43, 17.45) * mm, v(114.52, 16.97) * mm]});
            skFitSpline(sketch, "E1896", {"points": [v(114.52, 16.97) * mm, v(114.52, 16.94) * mm, v(114.54, 16.9) * mm, v(114.55, 16.86) * mm]});
            skFitSpline(sketch, "E1897", {"points": [v(114.55, 16.86) * mm, v(114.59, 16.86) * mm, v(114.61, 16.86) * mm, v(114.63, 16.87) * mm]});
            skFitSpline(sketch, "E1898", {"points": [v(114.63, 16.87) * mm, v(115.29, 17.34) * mm, v(116.03, 17.67) * mm, v(116.76, 18.01) * mm]});
            skFitSpline(sketch, "E1899", {"points": [v(116.76, 18.01) * mm, v(116.84, 18.05) * mm, v(116.93, 18.1) * mm, v(117.02, 18.14) * mm]});
            skFitSpline(sketch, "E1900", {"points": [v(117.02, 18.14) * mm, v(117.3, 18.24) * mm, v(117.57, 18.11) * mm, v(117.68, 17.84) * mm]});
            skFitSpline(sketch, "E1901", {"points": [v(117.68, 17.84) * mm, v(117.78, 17.58) * mm, v(117.65, 17.32) * mm, v(117.38, 17.2) * mm]});
            skFitSpline(sketch, "E1902", {"points": [v(117.38, 17.2) * mm, v(116.61, 16.88) * mm, v(115.85, 16.54) * mm, v(115.17, 16.05) * mm]});
            skFitSpline(sketch, "E1903", {"points": [v(115.17, 16.05) * mm, v(115.1, 16) * mm, v(115, 15.96) * mm, v(114.9, 15.9) * mm]});
            skFitSpline(sketch, "E1904", {"points": [v(114.9, 15.9) * mm, v(115.04, 15.38) * mm, v(115.16, 14.86) * mm, v(115.3, 14.3) * mm]});
            skFitSpline(sketch, "E1905", {"points": [v(115.3, 14.3) * mm, v(115.5, 14.41) * mm, v(115.68, 14.5) * mm, v(115.85, 14.6) * mm]});
            skFitSpline(sketch, "E1906", {"points": [v(115.85, 14.6) * mm, v(116.3, 14.86) * mm, v(116.74, 15.12) * mm, v(117.2, 15.39) * mm]});
            skFitSpline(sketch, "E1907", {"points": [v(117.2, 15.39) * mm, v(117.22, 15.4) * mm, v(117.24, 15.42) * mm, v(117.27, 15.43) * mm]});
            skFitSpline(sketch, "E1908", {"points": [v(117.27, 15.43) * mm, v(117.56, 15.58) * mm, v(117.84, 15.5) * mm, v(117.98, 15.26) * mm]});
            skFitSpline(sketch, "E1909", {"points": [v(117.98, 15.26) * mm, v(118.1, 15.01) * mm, v(118, 14.7) * mm, v(117.73, 14.54) * mm]});
            skFitSpline(sketch, "E1910", {"points": [v(117.73, 14.54) * mm, v(117.46, 14.4) * mm, v(117.2, 14.25) * mm, v(116.93, 14.1) * mm]});
            skFitSpline(sketch, "E1911", {"points": [v(116.93, 14.1) * mm, v(116.43, 13.8) * mm, v(115.93, 13.5) * mm, v(115.43, 13.2) * mm]});
            skFitSpline(sketch, "E1912", {"points": [v(115.43, 13.2) * mm, v(114.98, 12.94) * mm, v(114.52, 12.68) * mm, v(114.06, 12.42) * mm]});
            skFitSpline(sketch, "E1913", {"points": [v(114.06, 12.42) * mm, v(114.01, 12.39) * mm, v(113.97, 12.36) * mm, v(113.88, 12.3) * mm]});
            skFitSpline(sketch, "E1914", {"points": [v(113.88, 12.3) * mm, v(114.48, 12.11) * mm, v(115.07, 12.03) * mm, v(115.64, 11.89) * mm]});
            skFitSpline(sketch, "E1915", {"points": [v(115.64, 11.89) * mm, v(116.21, 11.74) * mm, v(116.78, 11.59) * mm, v(117.37, 11.43) * mm]});
            skFitSpline(sketch, "E1916", {"points": [v(117.37, 11.43) * mm, v(117.38, 11.52) * mm, v(117.39, 11.58) * mm, v(117.4, 11.65) * mm]});
            skFitSpline(sketch, "E1917", {"points": [v(117.4, 11.65) * mm, v(117.4, 12.05) * mm, v(117.44, 12.45) * mm, v(117.44, 12.85) * mm]});
            skFitSpline(sketch, "E1918", {"points": [v(117.44, 12.85) * mm, v(117.44, 13.06) * mm, v(117.55, 13.28) * mm, v(117.77, 13.35) * mm]});
            skFitSpline(sketch, "E1919", {"points": [v(117.77, 13.35) * mm, v(117.97, 13.42) * mm, v(118.24, 13.34) * mm, v(118.38, 13.18) * mm]});
            skFitSpline(sketch, "E1920", {"points": [v(118.38, 13.18) * mm, v(118.5, 13.03) * mm, v(118.52, 12.87) * mm, v(118.46, 12.68) * mm]});
            skFitSpline(sketch, "E1921", {"points": [v(118.46, 12.68) * mm, v(118.43, 12.57) * mm, v(118.41, 12.45) * mm, v(118.4, 12.34) * mm]});
            skFitSpline(sketch, "E1922", {"points": [v(118.4, 12.34) * mm, v(118.38, 12.03) * mm, v(118.37, 11.73) * mm, v(118.35, 11.42) * mm]});
            skFitSpline(sketch, "E1923", {"points": [v(118.35, 11.42) * mm, v(118.55, 11.42) * mm, v(118.74, 11.41) * mm, v(118.92, 11.42) * mm]});
            skFitSpline(sketch, "E1924", {"points": [v(118.92, 11.42) * mm, v(119.03, 11.42) * mm, v(119.14, 11.43) * mm, v(119.26, 11.44) * mm]});
            skFitSpline(sketch, "E1925", {"points": [v(119.26, 11.44) * mm, v(119.4, 11.44) * mm, v(119.52, 11.44) * mm, v(119.65, 11.5) * mm]});
            skFitSpline(sketch, "E1926", {"points": [v(119.65, 11.5) * mm, v(119.84, 11.59) * mm, v(120.03, 11.54) * mm, v(120.18, 11.38) * mm]});
            skFitSpline(sketch, "E1927", {"points": [v(120.18, 11.38) * mm, v(120.33, 11.2) * mm, v(120.39, 11) * mm, v(120.3, 10.78) * mm]});
            skFitSpline(sketch, "E1928", {"points": [v(120.3, 10.78) * mm, v(120.22, 10.58) * mm, v(120.06, 10.49) * mm, v(119.85, 10.48) * mm]});
            skFitSpline(sketch, "E1929", {"points": [v(119.85, 10.48) * mm, v(119.4, 10.46) * mm, v(118.97, 10.45) * mm, v(118.53, 10.43) * mm]});
            skFitSpline(sketch, "E1930", {"points": [v(118.53, 10.43) * mm, v(118.5, 10.43) * mm, v(118.45, 10.42) * mm, v(118.4, 10.42) * mm]});
            skFitSpline(sketch, "E1931", {"points": [v(118.4, 10.42) * mm, v(118.69, 9.26) * mm, v(118.96, 8.12) * mm, v(119.25, 6.95) * mm]});
            skFitSpline(sketch, "E1932", {"points": [v(119.25, 6.95) * mm, v(119.28, 6.98) * mm, v(119.31, 7) * mm, v(119.33, 7.02) * mm]});
            skFitSpline(sketch, "E1933", {"points": [v(119.33, 7.02) * mm, v(120.03, 8.21) * mm, v(120.72, 9.4) * mm, v(121.42, 10.6) * mm]});
            skFitSpline(sketch, "E1934", {"points": [v(121.42, 10.6) * mm, v(121.46, 10.67) * mm, v(121.49, 10.75) * mm, v(121.53, 10.81) * mm]});
            skFitSpline(sketch, "E1935", {"points": [v(121.53, 10.81) * mm, v(121.65, 11) * mm, v(121.89, 11.1) * mm, v(122.1, 11.06) * mm]});
            skFitSpline(sketch, "E1936", {"points": [v(122.1, 11.06) * mm, v(122.3, 11.02) * mm, v(122.46, 10.86) * mm, v(122.46, 10.65) * mm]});
            skFitSpline(sketch, "E1937", {"points": [v(122.46, 10.65) * mm, v(122.46, 10.52) * mm, v(122.42, 10.37) * mm, v(122.35, 10.25) * mm]});
            skFitSpline(sketch, "E1938", {"points": [v(122.35, 10.25) * mm, v(122.02, 9.65) * mm, v(121.67, 9.06) * mm, v(121.32, 8.46) * mm]});
            skFitSpline(sketch, "E1939", {"points": [v(121.32, 8.46) * mm, v(121.3, 8.44) * mm, v(121.3, 8.4) * mm, v(121.28, 8.37) * mm]});
            skFitSpline(sketch, "E1940", {"points": [v(121.28, 8.37) * mm, v(121.78, 8.15) * mm, v(122.32, 8.1) * mm, v(122.86, 7.95) * mm]});
            skFitSpline(sketch, "E1941", {"points": [v(122.86, 7.95) * mm, v(123.07, 8.3) * mm, v(123.31, 8.65) * mm, v(123.5, 9.02) * mm]});
            skFitSpline(sketch, "E1942", {"points": [v(123.5, 9.02) * mm, v(123.75, 9.48) * mm, v(123.95, 9.95) * mm, v(124.16, 10.43) * mm]});
            skFitSpline(sketch, "E1943", {"points": [v(124.16, 10.43) * mm, v(124.29, 10.7) * mm, v(124.54, 10.83) * mm, v(124.8, 10.72) * mm]});
            skFitSpline(sketch, "E1944", {"points": [v(124.8, 10.72) * mm, v(125.09, 10.6) * mm, v(125.22, 10.3) * mm, v(125.08, 10.03) * mm]});
            skFitSpline(sketch, "E1945", {"points": [v(125.08, 10.03) * mm, v(124.7, 9.26) * mm, v(124.39, 8.45) * mm, v(123.87, 7.75) * mm]});
            skFitSpline(sketch, "E1946", {"points": [v(123.87, 7.75) * mm, v(123.85, 7.7) * mm, v(123.83, 7.66) * mm, v(123.79, 7.6) * mm]});
            skFitSpline(sketch, "E1947", {"points": [v(123.79, 7.6) * mm, v(123.92, 7.57) * mm, v(124.03, 7.53) * mm, v(124.14, 7.52) * mm]});
            skFitSpline(sketch, "E1948", {"points": [v(124.14, 7.52) * mm, v(124.67, 7.43) * mm, v(125.17, 7.23) * mm, v(125.68, 7.06) * mm]});
            skFitSpline(sketch, "E1949", {"points": [v(125.68, 7.06) * mm, v(125.91, 6.99) * mm, v(126.15, 6.9) * mm, v(126.38, 6.82) * mm]});
            skFitSpline(sketch, "E1950", {"points": [v(126.38, 6.82) * mm, v(126.63, 6.73) * mm, v(126.76, 6.56) * mm, v(126.75, 6.3) * mm]});
            skFitSpline(sketch, "E1951", {"points": [v(126.75, 6.3) * mm, v(126.74, 5.95) * mm, v(126.41, 5.74) * mm, v(126.09, 5.86) * mm]});
            skFitSpline(sketch, "E1952", {"points": [v(126.09, 5.86) * mm, v(125.7, 6) * mm, v(125.3, 6.17) * mm, v(124.9, 6.3) * mm]});
            skFitSpline(sketch, "E1953", {"points": [v(124.9, 6.3) * mm, v(124.55, 6.41) * mm, v(124.2, 6.5) * mm, v(123.84, 6.59) * mm]});
            skFitSpline(sketch, "E1954", {"points": [v(123.84, 6.59) * mm, v(123.7, 6.63) * mm, v(123.54, 6.65) * mm, v(123.37, 6.69) * mm]});
            skFitSpline(sketch, "E1955", {"points": [v(123.37, 6.69) * mm, v(123.12, 6.22) * mm, v(122.76, 5.8) * mm, v(122.55, 5.26) * mm]});
            skFitSpline(sketch, "E1956", {"points": [v(122.55, 5.26) * mm, v(123.26, 5.08) * mm, v(123.96, 4.9) * mm, v(124.65, 4.72) * mm]});
            skFitSpline(sketch, "E1957", {"points": [v(124.65, 4.72) * mm, v(124.68, 4.7) * mm, v(124.71, 4.7) * mm, v(124.74, 4.68) * mm]});
            skFitSpline(sketch, "E1958", {"points": [v(124.74, 4.68) * mm, v(125.04, 4.58) * mm, v(125.18, 4.34) * mm, v(125.1, 4.07) * mm]});
            skFitSpline(sketch, "E1959", {"points": [v(125.1, 4.07) * mm, v(125.01, 3.82) * mm, v(124.73, 3.66) * mm, v(124.46, 3.73) * mm]});
            skFitSpline(sketch, "E1960", {"points": [v(124.46, 3.73) * mm, v(123.88, 3.89) * mm, v(123.3, 4.05) * mm, v(122.73, 4.21) * mm]});
            skFitSpline(sketch, "E1961", {"points": [v(122.73, 4.21) * mm, v(122.53, 4.26) * mm, v(122.34, 4.3) * mm, v(122.14, 4.35) * mm]});
            skFitSpline(sketch, "E1962", {"points": [v(122.14, 4.35) * mm, v(121.55, 4.5) * mm, v(120.96, 4.66) * mm, v(120.36, 4.82) * mm]});
            skFitSpline(sketch, "E1963", {"points": [v(120.36, 4.82) * mm, v(120.3, 4.84) * mm, v(120.22, 4.85) * mm, v(120.1, 4.88) * mm]});
            skFitSpline(sketch, "E1964", {"points": [v(120.1, 4.88) * mm, v(120.74, 3.83) * mm, v(121.35, 2.82) * mm, v(121.98, 1.8) * mm]});
            skFitSpline(sketch, "E1965", {"points": [v(121.98, 1.8) * mm, v(122.25, 2.04) * mm, v(122.51, 2.28) * mm, v(122.77, 2.53) * mm]});
            skFitSpline(sketch, "E1966", {"points": [v(122.77, 2.53) * mm, v(122.88, 2.62) * mm, v(122.97, 2.74) * mm, v(123.09, 2.82) * mm]});
            skFitSpline(sketch, "E1967", {"points": [v(123.09, 2.82) * mm, v(123.33, 3) * mm, v(123.65, 2.93) * mm, v(123.81, 2.67) * mm]});
            skFitSpline(sketch, "E1968", {"points": [v(123.81, 2.67) * mm, v(124, 2.38) * mm, v(123.91, 2.06) * mm, v(123.63, 1.91) * mm]});
            skFitSpline(sketch, "E1969", {"points": [v(123.63, 1.91) * mm, v(123.53, 1.86) * mm, v(123.43, 1.79) * mm, v(123.34, 1.71) * mm]});
            skFitSpline(sketch, "E1970", {"points": [v(123.34, 1.71) * mm, v(123.15, 1.55) * mm, v(122.96, 1.37) * mm, v(122.77, 1.2) * mm]});
            skFitSpline(sketch, "E1971", {"points": [v(122.77, 1.2) * mm, v(122.73, 1.16) * mm, v(122.67, 1.14) * mm, v(122.6, 1.1) * mm]});
            skFitSpline(sketch, "E1972", {"points": [v(122.6, 1.1) * mm, v(122.8, 0.93) * mm, v(122.93, 0.8) * mm, v(123.08, 0.68) * mm]});
            skFitSpline(sketch, "E1973", {"points": [v(123.08, 0.68) * mm, v(123.28, 0.51) * mm, v(123.44, 0.31) * mm, v(123.69, 0.2) * mm]});
            skFitSpline(sketch, "E1974", {"points": [v(123.69, 0.2) * mm, v(123.94, 0.07) * mm, v(123.97, -0.26) * mm, v(123.81, -0.52) * mm]});
            skFitSpline(sketch, "E1975", {"points": [v(123.81, -0.52) * mm, v(123.67, -0.76) * mm, v(123.38, -0.85) * mm, v(123.15, -0.7) * mm]});
            skFitSpline(sketch, "E1976", {"points": [v(123.15, -0.7) * mm, v(123.06, -0.66) * mm, v(122.98, -0.58) * mm, v(122.9, -0.51) * mm]});
            skFitSpline(sketch, "E1977", {"points": [v(122.9, -0.51) * mm, v(122.6, -0.23) * mm, v(122.3, 0.06) * mm, v(121.98, 0.36) * mm]});
            skFitSpline(sketch, "E1978", {"points": [v(121.98, 0.36) * mm, v(121.36, -0.67) * mm, v(120.74, -1.68) * mm, v(120.1, -2.73) * mm]});
            skFitSpline(sketch, "E1979", {"points": [v(120.1, -2.73) * mm, v(120.21, -2.7) * mm, v(120.28, -2.7) * mm, v(120.35, -2.67) * mm]});
            skFitSpline(sketch, "E1980", {"points": [v(120.35, -2.67) * mm, v(121.02, -2.5) * mm, v(121.7, -2.34) * mm, v(122.36, -2.16) * mm]});
            skFitSpline(sketch, "E1981", {"points": [v(122.36, -2.16) * mm, v(123.03, -1.99) * mm, v(123.69, -1.8) * mm, v(124.35, -1.61) * mm]});
            skFitSpline(sketch, "E1982", {"points": [v(124.35, -1.61) * mm, v(124.5, -1.57) * mm, v(124.63, -1.56) * mm, v(124.77, -1.6) * mm]});
            skFitSpline(sketch, "E1983", {"points": [v(124.77, -1.6) * mm, v(124.96, -1.66) * mm, v(125.1, -1.82) * mm, v(125.11, -2.02) * mm]});
            skFitSpline(sketch, "E1984", {"points": [v(125.11, -2.02) * mm, v(125.13, -2.22) * mm, v(125.05, -2.38) * mm, v(124.87, -2.48) * mm]});
            skFitSpline(sketch, "E1985", {"points": [v(124.87, -2.48) * mm, v(124.79, -2.52) * mm, v(124.7, -2.55) * mm, v(124.6, -2.57) * mm]});
            skFitSpline(sketch, "E1986", {"points": [v(124.6, -2.57) * mm, v(123.92, -2.75) * mm, v(123.25, -2.93) * mm, v(122.56, -3.12) * mm]});
            skFitSpline(sketch, "E1987", {"points": [v(122.56, -3.12) * mm, v(122.76, -3.65) * mm, v(123.12, -4.06) * mm, v(123.37, -4.53) * mm]});
            skFitSpline(sketch, "E1988", {"points": [v(123.37, -4.53) * mm, v(124.31, -4.39) * mm, v(125.19, -4.08) * mm, v(126.05, -3.72) * mm]});
            skFitSpline(sketch, "E1989", {"points": [v(126.05, -3.72) * mm, v(126.33, -3.6) * mm, v(126.6, -3.7) * mm, v(126.71, -3.97) * mm]});
            skFitSpline(sketch, "E1990", {"points": [v(126.71, -3.97) * mm, v(126.8, -4.22) * mm, v(126.75, -4.53) * mm, v(126.43, -4.64) * mm]});
            skFitSpline(sketch, "E1991", {"points": [v(126.43, -4.64) * mm, v(126.12, -4.76) * mm, v(125.8, -4.87) * mm, v(125.49, -4.98) * mm]});
            skFitSpline(sketch, "E1992", {"points": [v(125.49, -4.98) * mm, v(124.98, -5.17) * mm, v(124.46, -5.32) * mm, v(123.92, -5.41) * mm]});
            skFitSpline(sketch, "E1993", {"points": [v(123.92, -5.41) * mm, v(123.88, -5.42) * mm, v(123.85, -5.44) * mm, v(123.79, -5.46) * mm]});
            skFitSpline(sketch, "E1994", {"points": [v(123.79, -5.46) * mm, v(123.85, -5.56) * mm, v(123.9, -5.65) * mm, v(123.96, -5.73) * mm]});
            skFitSpline(sketch, "E1995", {"points": [v(123.96, -5.73) * mm, v(124.28, -6.17) * mm, v(124.5, -6.67) * mm, v(124.74, -7.16) * mm]});
            skFitSpline(sketch, "E1996", {"points": [v(124.74, -7.16) * mm, v(124.85, -7.39) * mm, v(124.96, -7.62) * mm, v(125.07, -7.85) * mm]});
            skFitSpline(sketch, "E1997", {"points": [v(125.07, -7.85) * mm, v(125.2, -8.1) * mm, v(125.13, -8.36) * mm, v(124.92, -8.5) * mm]});
            skFitSpline(sketch, "E1998", {"points": [v(124.92, -8.5) * mm, v(124.65, -8.7) * mm, v(124.31, -8.6) * mm, v(124.18, -8.3) * mm]});
            skFitSpline(sketch, "E1999", {"points": [v(124.18, -8.3) * mm, v(124.02, -7.95) * mm, v(123.86, -7.6) * mm, v(123.69, -7.24) * mm]});
            skFitSpline(sketch, "E2000", {"points": [v(123.69, -7.24) * mm, v(123.52, -6.9) * mm, v(123.32, -6.57) * mm, v(123.13, -6.24) * mm]});
            skFitSpline(sketch, "E2001", {"points": [v(123.13, -6.24) * mm, v(123.05, -6.1) * mm, v(122.95, -5.96) * mm, v(122.85, -5.8) * mm]});
            skFitSpline(sketch, "E2002", {"points": [v(122.85, -5.8) * mm, v(122.34, -5.93) * mm, v(121.81, -6.06) * mm, v(121.26, -6.2) * mm]});
            skFitSpline(sketch, "E2003", {"points": [v(121.26, -6.2) * mm, v(121.38, -6.4) * mm, v(121.47, -6.6) * mm, v(121.57, -6.77) * mm]});
            skFitSpline(sketch, "E2004", {"points": [v(121.57, -6.77) * mm, v(121.83, -7.21) * mm, v(122.1, -7.65) * mm, v(122.35, -8.1) * mm]});
            skFitSpline(sketch, "E2005", {"points": [v(122.35, -8.1) * mm, v(122.43, -8.22) * mm, v(122.5, -8.36) * mm, v(122.47, -8.52) * mm]});
            skFitSpline(sketch, "E2006", {"points": [v(122.47, -8.52) * mm, v(122.43, -8.72) * mm, v(122.29, -8.87) * mm, v(122.1, -8.91) * mm]});
            skFitSpline(sketch, "E2007", {"points": [v(122.1, -8.91) * mm, v(121.88, -8.96) * mm, v(121.64, -8.85) * mm, v(121.52, -8.65) * mm]});
            skFitSpline(sketch, "E2008", {"points": [v(121.52, -8.65) * mm, v(121.23, -8.15) * mm, v(120.95, -7.64) * mm, v(120.66, -7.13) * mm]});
            skFitSpline(sketch, "E2009", {"points": [v(120.66, -7.13) * mm, v(120.56, -6.96) * mm, v(120.46, -6.8) * mm, v(120.36, -6.64) * mm]});
            skFitSpline(sketch, "E2010", {"points": [v(120.36, -6.64) * mm, v(120.04, -6.1) * mm, v(119.72, -5.55) * mm, v(119.4, -5) * mm]});
            skFitSpline(sketch, "E2011", {"points": [v(119.4, -5) * mm, v(119.37, -4.94) * mm, v(119.32, -4.87) * mm, v(119.26, -4.76) * mm]});
            skFitSpline(sketch, "E2012", {"points": [v(119.26, -4.76) * mm, v(118.97, -5.95) * mm, v(118.69, -7.1) * mm, v(118.4, -8.27) * mm]});
            skFitSpline(sketch, "E2013", {"points": [v(118.4, -8.27) * mm, v(118.7, -8.3) * mm, v(119, -8.31) * mm, v(119.3, -8.33) * mm]});
            skFitSpline(sketch, "E2014", {"points": [v(119.3, -8.33) * mm, v(119.48, -8.33) * mm, v(119.66, -8.33) * mm, v(119.83, -8.33) * mm]});
            skFitSpline(sketch, "E2015", {"points": [v(119.83, -8.33) * mm, v(120.06, -8.33) * mm, v(120.22, -8.43) * mm, v(120.3, -8.64) * mm]});
            skFitSpline(sketch, "E2016", {"points": [v(120.3, -8.64) * mm, v(120.38, -8.86) * mm, v(120.33, -9.07) * mm, v(120.17, -9.24) * mm]});
            skFitSpline(sketch, "E2017", {"points": [v(120.17, -9.24) * mm, v(120.01, -9.4) * mm, v(119.82, -9.42) * mm, v(119.62, -9.34) * mm]});
            skFitSpline(sketch, "E2018", {"points": [v(119.62, -9.34) * mm, v(119.56, -9.32) * mm, v(119.5, -9.3) * mm, v(119.44, -9.29) * mm]});
            skFitSpline(sketch, "E2019", {"points": [v(119.44, -9.29) * mm, v(119.09, -9.27) * mm, v(118.74, -9.26) * mm, v(118.37, -9.25) * mm]});
            skFitSpline(sketch, "E2020", {"points": [v(118.37, -9.25) * mm, v(118.37, -9.44) * mm, v(118.37, -9.63) * mm, v(118.37, -9.82) * mm]});
            skFitSpline(sketch, "E2021", {"points": [v(118.37, -9.82) * mm, v(118.38, -9.95) * mm, v(118.39, -10.09) * mm, v(118.4, -10.22) * mm]});
            skFitSpline(sketch, "E2022", {"points": [v(118.4, -10.22) * mm, v(118.41, -10.32) * mm, v(118.43, -10.42) * mm, v(118.46, -10.52) * mm]});
            skFitSpline(sketch, "E2023", {"points": [v(118.46, -10.52) * mm, v(118.53, -10.74) * mm, v(118.5, -10.93) * mm, v(118.34, -11.07) * mm]});
            skFitSpline(sketch, "E2024", {"points": [v(118.34, -11.07) * mm, v(118.16, -11.22) * mm, v(117.96, -11.28) * mm, v(117.74, -11.19) * mm]});
            skFitSpline(sketch, "E2025", {"points": [v(117.74, -11.19) * mm, v(117.53, -11.1) * mm, v(117.44, -10.94) * mm, v(117.44, -10.71) * mm]});
            skFitSpline(sketch, "E2026", {"points": [v(117.44, -10.71) * mm, v(117.43, -10.24) * mm, v(117.4, -9.78) * mm, v(117.4, -9.3) * mm]});
            skFitSpline(sketch, "E2027", {"points": [v(117.4, -9.3) * mm, v(116.22, -9.58) * mm, v(115.07, -9.86) * mm, v(113.89, -10.15) * mm]});
            skFitSpline(sketch, "E2028", {"points": [v(113.89, -10.15) * mm, v(113.96, -10.2) * mm, v(114, -10.23) * mm, v(114.05, -10.26) * mm]});
            skFitSpline(sketch, "E2029", {"points": [v(114.05, -10.26) * mm, v(114.5, -10.52) * mm, v(114.95, -10.77) * mm, v(115.4, -11.03) * mm]});
            skFitSpline(sketch, "E2030", {"points": [v(115.4, -11.03) * mm, v(115.94, -11.35) * mm, v(116.47, -11.68) * mm, v(117, -12) * mm]});
            skFitSpline(sketch, "E2031", {"points": [v(117, -12) * mm, v(117.23, -12.13) * mm, v(117.47, -12.24) * mm, v(117.7, -12.38) * mm]});
            skFitSpline(sketch, "E2032", {"points": [v(117.7, -12.38) * mm, v(117.8, -12.44) * mm, v(117.9, -12.54) * mm, v(117.96, -12.64) * mm]});
            skFitSpline(sketch, "E2033", {"points": [v(117.96, -12.64) * mm, v(118.08, -12.81) * mm, v(118.05, -13.04) * mm, v(117.92, -13.2) * mm]});
            skFitSpline(sketch, "E2034", {"points": [v(117.92, -13.2) * mm, v(117.78, -13.35) * mm, v(117.57, -13.42) * mm, v(117.37, -13.32) * mm]});
            skFitSpline(sketch, "E2035", {"points": [v(117.37, -13.32) * mm, v(117.15, -13.22) * mm, v(116.94, -13.09) * mm, v(116.72, -12.97) * mm]});
            skFitSpline(sketch, "E2036", {"points": [v(116.72, -12.97) * mm, v(116.27, -12.7) * mm, v(115.81, -12.44) * mm, v(115.34, -12.16) * mm]});
            skFitSpline(sketch, "E2037", {"points": [v(115.34, -12.16) * mm, v(115.1, -12.67) * mm, v(115.07, -13.23) * mm, v(114.91, -13.73) * mm]});
            skFitSpline(sketch, "E2038", {"points": [v(114.91, -13.73) * mm, v(115.6, -14.26) * mm, v(116.39, -14.62) * mm, v(117.16, -14.98) * mm]});
            skFitSpline(sketch, "E2039", {"points": [v(117.16, -14.98) * mm, v(117.23, -15) * mm, v(117.3, -15.02) * mm, v(117.36, -15.05) * mm]});
            skFitSpline(sketch, "E2040", {"points": [v(117.36, -15.05) * mm, v(117.66, -15.16) * mm, v(117.79, -15.43) * mm, v(117.68, -15.7) * mm]});
            skFitSpline(sketch, "E2041", {"points": [v(117.68, -15.7) * mm, v(117.56, -15.98) * mm, v(117.27, -16.1) * mm, v(116.99, -15.98) * mm]});
            skFitSpline(sketch, "E2042", {"points": [v(116.99, -15.98) * mm, v(116.68, -15.84) * mm, v(116.38, -15.68) * mm, v(116.08, -15.54) * mm]});
            skFitSpline(sketch, "E2043", {"points": [v(116.08, -15.54) * mm, v(115.58, -15.3) * mm, v(115.1, -15.05) * mm, v(114.64, -14.73) * mm]});
            skFitSpline(sketch, "E2044", {"points": [v(114.64, -14.73) * mm, v(114.63, -14.71) * mm, v(114.6, -14.71) * mm, v(114.55, -14.7) * mm]});
            skFitSpline(sketch, "E2045", {"points": [v(114.55, -14.7) * mm, v(114.53, -14.8) * mm, v(114.5, -14.91) * mm, v(114.48, -15.02) * mm]});
            skFitSpline(sketch, "E2046", {"points": [v(114.48, -15.02) * mm, v(114.4, -15.55) * mm, v(114.2, -16.05) * mm, v(114.03, -16.56) * mm]});
            skFitSpline(sketch, "E2047", {"points": [v(114.03, -16.56) * mm, v(113.95, -16.8) * mm, v(113.86, -17.05) * mm, v(113.76, -17.3) * mm]});
            skFitSpline(sketch, "E2048", {"points": [v(113.76, -17.3) * mm, v(113.65, -17.6) * mm, v(113.37, -17.73) * mm, v(113.09, -17.61) * mm]});
            skFitSpline(sketch, "E2049", {"points": [v(113.09, -17.61) * mm, v(112.81, -17.5) * mm, v(112.72, -17.21) * mm, v(112.84, -16.9) * mm]});
            skFitSpline(sketch, "E2050", {"points": [v(112.84, -16.9) * mm, v(113.1, -16.29) * mm, v(113.34, -15.66) * mm, v(113.49, -15) * mm]});
            skFitSpline(sketch, "E2051", {"points": [v(113.49, -15) * mm, v(113.54, -14.77) * mm, v(113.6, -14.53) * mm, v(113.64, -14.26) * mm]});
            skFitSpline(sketch, "E2052", {"points": [v(113.64, -14.26) * mm, v(113.2, -14) * mm, v(112.73, -13.71) * mm, v(112.25, -13.42) * mm]});
            skFitSpline(sketch, "E2053", {"points": [v(112.25, -13.42) * mm, v(112.17, -13.67) * mm, v(112.1, -13.88) * mm, v(112.05, -14.1) * mm]});
            skFitSpline(sketch, "E2054", {"points": [v(112.05, -14.1) * mm, v(111.92, -14.57) * mm, v(111.8, -15.05) * mm, v(111.68, -15.53) * mm]});
            skFitSpline(sketch, "E2055", {"points": [v(111.68, -15.53) * mm, v(111.62, -15.76) * mm, v(111.52, -15.95) * mm, v(111.26, -16) * mm]});
            skFitSpline(sketch, "E2056", {"points": [v(111.26, -16) * mm, v(110.89, -16.07) * mm, v(110.6, -15.71) * mm, v(110.7, -15.32) * mm]});
            skFitSpline(sketch, "E2057", {"points": [v(110.7, -15.32) * mm, v(110.84, -14.8) * mm, v(111, -14.27) * mm, v(111.13, -13.75) * mm]});
            skFitSpline(sketch, "E2058", {"points": [v(111.13, -13.75) * mm, v(111.22, -13.41) * mm, v(111.29, -13.07) * mm, v(111.38, -12.73) * mm]});
            skFitSpline(sketch, "E2059", {"points": [v(111.38, -12.73) * mm, v(111.5, -12.23) * mm, v(111.65, -11.73) * mm, v(111.79, -11.23) * mm]});
            skFitSpline(sketch, "E2060", {"points": [v(111.79, -11.23) * mm, v(111.8, -11.17) * mm, v(111.82, -11.1) * mm, v(111.84, -11) * mm]});
            skFitSpline(sketch, "E2061", {"points": [v(111.84, -11) * mm, v(111.28, -11.3) * mm, v(110.8, -11.64) * mm, v(110.3, -11.95) * mm]});
            skFitSpline(sketch, "E2062", {"points": [v(110.3, -11.95) * mm, v(109.8, -12.26) * mm, v(109.28, -12.54) * mm, v(108.74, -12.86) * mm]});
            skFitSpline(sketch, "E2063", {"points": [v(108.74, -12.86) * mm, v(108.98, -13.12) * mm, v(109.2, -13.36) * mm, v(109.43, -13.6) * mm]});
            skFitSpline(sketch, "E2064", {"points": [v(109.43, -13.6) * mm, v(109.53, -13.72) * mm, v(109.65, -13.82) * mm, v(109.75, -13.93) * mm]});
            skFitSpline(sketch, "E2065", {"points": [v(109.75, -13.93) * mm, v(109.9, -14.1) * mm, v(109.92, -14.3) * mm, v(109.83, -14.5) * mm]});
            skFitSpline(sketch, "E2066", {"points": [v(109.83, -14.5) * mm, v(109.72, -14.7) * mm, v(109.53, -14.8) * mm, v(109.3, -14.8) * mm]});
            skFitSpline(sketch, "E2067", {"points": [v(109.3, -14.8) * mm, v(109.09, -14.8) * mm, v(108.94, -14.68) * mm, v(108.86, -14.48) * mm]});
            skFitSpline(sketch, "E2068", {"points": [v(108.86, -14.48) * mm, v(108.84, -14.45) * mm, v(108.83, -14.4) * mm, v(108.8, -14.38) * mm]});
            skFitSpline(sketch, "E2069", {"points": [v(108.8, -14.38) * mm, v(108.56, -14.1) * mm, v(108.3, -13.82) * mm, v(108.03, -13.53) * mm]});
            skFitSpline(sketch, "E2070", {"points": [v(108.03, -13.53) * mm, v(107.93, -13.64) * mm, v(107.83, -13.75) * mm, v(107.74, -13.85) * mm]});
            skFitSpline(sketch, "E2071", {"points": [v(107.74, -13.85) * mm, v(107.6, -14) * mm, v(107.46, -14.14) * mm, v(107.33, -14.3) * mm]});
            skFitSpline(sketch, "E2072", {"points": [v(107.33, -14.3) * mm, v(107.28, -14.35) * mm, v(107.24, -14.42) * mm, v(107.2, -14.5) * mm]});
            skFitSpline(sketch, "E2073", {"points": [v(107.2, -14.5) * mm, v(107.12, -14.69) * mm, v(106.97, -14.8) * mm, v(106.76, -14.8) * mm]});
            skFitSpline(sketch, "E2074", {"points": [v(106.76, -14.8) * mm, v(106.53, -14.8) * mm, v(106.34, -14.7) * mm, v(106.23, -14.48) * mm]});
            skFitSpline(sketch, "E2075", {"points": [v(106.23, -14.48) * mm, v(106.13, -14.28) * mm, v(106.18, -14.1) * mm, v(106.32, -13.93) * mm]});
            skFitSpline(sketch, "E2076", {"points": [v(106.32, -13.93) * mm, v(106.56, -13.68) * mm, v(106.8, -13.43) * mm, v(107.03, -13.18) * mm]});
            skFitSpline(sketch, "E2077", {"points": [v(107.03, -13.18) * mm, v(107.12, -13.08) * mm, v(107.21, -12.98) * mm, v(107.3, -12.87) * mm]});
            skFitSpline(sketch, "E2078", {"points": [v(107.3, -12.87) * mm, v(106.3, -12.25) * mm, v(105.29, -11.64) * mm, v(104.23, -11) * mm]});
            skFitSpline(sketch, "E2079", {"points": [v(104.23, -11) * mm, v(104.26, -11.1) * mm, v(104.27, -11.18) * mm, v(104.29, -11.25) * mm]});
            skFitSpline(sketch, "E2080", {"points": [v(104.29, -11.25) * mm, v(104.46, -11.92) * mm, v(104.62, -12.6) * mm, v(104.8, -13.27) * mm]});
            skFitSpline(sketch, "E2081", {"points": [v(104.8, -13.27) * mm, v(104.97, -13.93) * mm, v(105.16, -14.6) * mm, v(105.35, -15.25) * mm]});
            skFitSpline(sketch, "E2082", {"points": [v(105.35, -15.25) * mm, v(105.38, -15.37) * mm, v(105.4, -15.48) * mm, v(105.37, -15.6) * mm]});
            skFitSpline(sketch, "E2083", {"points": [v(105.37, -15.6) * mm, v(105.3, -15.83) * mm, v(105.16, -15.98) * mm, v(104.95, -16) * mm]});
            skFitSpline(sketch, "E2084", {"points": [v(104.95, -16) * mm, v(104.72, -16.02) * mm, v(104.52, -15.91) * mm, v(104.44, -15.68) * mm]});
            skFitSpline(sketch, "E2085", {"points": [v(104.44, -15.68) * mm, v(104.35, -15.4) * mm, v(104.29, -15.12) * mm, v(104.21, -14.83) * mm]});
            skFitSpline(sketch, "E2086", {"points": [v(104.21, -14.83) * mm, v(104.09, -14.38) * mm, v(103.97, -13.92) * mm, v(103.84, -13.45) * mm]});
            skFitSpline(sketch, "E2087", {"points": [v(103.84, -13.45) * mm, v(103.31, -13.65) * mm, v(102.9, -14.01) * mm, v(102.42, -14.26) * mm]});
            skFitSpline(sketch, "E2088", {"points": [v(102.42, -14.26) * mm, v(102.54, -14.8) * mm, v(102.62, -15.33) * mm, v(102.82, -15.84) * mm]});
            skFitSpline(sketch, "E2089", {"points": [v(102.82, -15.84) * mm, v(102.97, -16.22) * mm, v(103.1, -16.6) * mm, v(103.25, -16.98) * mm]});
            skFitSpline(sketch, "E2090", {"points": [v(103.25, -16.98) * mm, v(103.34, -17.22) * mm, v(103.25, -17.46) * mm, v(103.04, -17.58) * mm]});
            skFitSpline(sketch, "E2091", {"points": [v(103.04, -17.58) * mm, v(102.81, -17.7) * mm, v(102.54, -17.66) * mm, v(102.4, -17.46) * mm]});
            skFitSpline(sketch, "E2092", {"points": [v(102.4, -17.46) * mm, v(102.34, -17.4) * mm, v(102.3, -17.31) * mm, v(102.28, -17.23) * mm]});
            skFitSpline(sketch, "E2093", {"points": [v(102.28, -17.23) * mm, v(102, -16.42) * mm, v(101.67, -15.63) * mm, v(101.53, -14.78) * mm]});
            skFitSpline(sketch, "E2094", {"points": [v(101.53, -14.78) * mm, v(101.53, -14.76) * mm, v(101.52, -14.74) * mm, v(101.5, -14.71) * mm]});
            skFitSpline(sketch, "E2095", {"points": [v(101.5, -14.71) * mm, v(101.48, -14.71) * mm, v(101.45, -14.7) * mm, v(101.44, -14.72) * mm]});
            skFitSpline(sketch, "E2096", {"points": [v(101.44, -14.72) * mm, v(100.78, -15.2) * mm, v(100.04, -15.52) * mm, v(99.3, -15.86) * mm]});
            skFitSpline(sketch, "E2097", {"points": [v(99.3, -15.86) * mm, v(99.24, -15.9) * mm, v(99.17, -15.94) * mm, v(99.1, -15.97) * mm]});
            skFitSpline(sketch, "E2098", {"points": [v(99.1, -15.97) * mm, v(98.8, -16.1) * mm, v(98.5, -15.99) * mm, v(98.39, -15.7) * mm]});
            skFitSpline(sketch, "E2099", {"points": [v(98.39, -15.7) * mm, v(98.28, -15.42) * mm, v(98.41, -15.17) * mm, v(98.7, -15.04) * mm]});
            skFitSpline(sketch, "E2100", {"points": [v(98.7, -15.04) * mm, v(99.45, -14.73) * mm, v(100.2, -14.4) * mm, v(100.85, -13.93) * mm]});
            skFitSpline(sketch, "E2101", {"points": [v(100.85, -13.93) * mm, v(100.94, -13.87) * mm, v(101.04, -13.82) * mm, v(101.15, -13.75) * mm]});
            skFitSpline(sketch, "E2102", {"points": [v(101.15, -13.75) * mm, v(101.01, -13.23) * mm, v(100.95, -12.68) * mm, v(100.73, -12.16) * mm]});
            skFitSpline(sketch, "E2103", {"points": [v(100.73, -12.16) * mm, v(100.12, -12.5) * mm, v(99.53, -12.85) * mm, v(98.94, -13.2) * mm]});
            skFitSpline(sketch, "E2104", {"points": [v(98.94, -13.2) * mm, v(98.88, -13.23) * mm, v(98.83, -13.27) * mm, v(98.77, -13.3) * mm]});
            skFitSpline(sketch, "E2105", {"points": [v(98.77, -13.3) * mm, v(98.5, -13.43) * mm, v(98.22, -13.35) * mm, v(98.09, -13.1) * mm]});
            skFitSpline(sketch, "E2106", {"points": [v(98.09, -13.1) * mm, v(97.97, -12.88) * mm, v(98.06, -12.57) * mm, v(98.3, -12.42) * mm]});
            skFitSpline(sketch, "E2107", {"points": [v(98.3, -12.42) * mm, v(98.36, -12.38) * mm, v(98.44, -12.35) * mm, v(98.5, -12.31) * mm]});
            skFitSpline(sketch, "E2108", {"points": [v(98.5, -12.31) * mm, v(99.2, -11.9) * mm, v(99.87, -11.5) * mm, v(100.55, -11.1) * mm]});
            skFitSpline(sketch, "E2109", {"points": [v(100.55, -11.1) * mm, v(101, -10.84) * mm, v(101.46, -10.58) * mm, v(101.92, -10.31) * mm]});
            skFitSpline(sketch, "E2110", {"points": [v(101.92, -10.31) * mm, v(102, -10.27) * mm, v(102.07, -10.23) * mm, v(102.18, -10.16) * mm]});
            skFitSpline(sketch, "E2111", {"points": [v(102.18, -10.16) * mm, v(101.58, -9.96) * mm, v(101, -9.88) * mm, v(100.43, -9.74) * mm]});
            skFitSpline(sketch, "E2112", {"points": [v(100.43, -9.74) * mm, v(99.86, -9.6) * mm, v(99.3, -9.44) * mm, v(98.69, -9.28) * mm]});
            skFitSpline(sketch, "E2113", {"points": [v(98.69, -9.28) * mm, v(98.67, -9.59) * mm, v(98.65, -9.88) * mm, v(98.63, -10.16) * mm]});
            skFitSpline(sketch, "E2114", {"points": [v(98.63, -10.16) * mm, v(98.63, -10.34) * mm, v(98.63, -10.52) * mm, v(98.63, -10.7) * mm]});
            skFitSpline(sketch, "E2115", {"points": [v(98.63, -10.7) * mm, v(98.63, -10.92) * mm, v(98.54, -11.1) * mm, v(98.33, -11.19) * mm]});
            skFitSpline(sketch, "E2116", {"points": [v(98.33, -11.19) * mm, v(98.1, -11.28) * mm, v(97.9, -11.22) * mm, v(97.73, -11.07) * mm]});
            skFitSpline(sketch, "E2117", {"points": [v(97.73, -11.07) * mm, v(97.57, -10.93) * mm, v(97.54, -10.73) * mm, v(97.6, -10.52) * mm]});
            skFitSpline(sketch, "E2118", {"points": [v(97.6, -10.52) * mm, v(97.64, -10.41) * mm, v(97.67, -10.3) * mm, v(97.67, -10.2) * mm]});
            skFitSpline(sketch, "E2119", {"points": [v(97.67, -10.2) * mm, v(97.69, -9.89) * mm, v(97.7, -9.58) * mm, v(97.7, -9.27) * mm]});
            skFitSpline(sketch, "E2120", {"points": [v(97.7, -9.27) * mm, v(97.53, -9.27) * mm, v(97.36, -9.27) * mm, v(97.18, -9.27) * mm]});
            skFitSpline(sketch, "E2121", {"points": [v(97.18, -9.27) * mm, v(97.04, -9.27) * mm, v(96.9, -9.28) * mm, v(96.75, -9.29) * mm]});
            skFitSpline(sketch, "E2122", {"points": [v(96.75, -9.29) * mm, v(96.65, -9.3) * mm, v(96.54, -9.32) * mm, v(96.43, -9.35) * mm]});
            skFitSpline(sketch, "E2123", {"points": [v(96.43, -9.35) * mm, v(96.23, -9.41) * mm, v(96.05, -9.4) * mm, v(95.9, -9.24) * mm]});
            skFitSpline(sketch, "E2124", {"points": [v(95.9, -9.24) * mm, v(95.75, -9.07) * mm, v(95.67, -8.87) * mm, v(95.76, -8.65) * mm]});
            skFitSpline(sketch, "E2125", {"points": [v(95.76, -8.65) * mm, v(95.84, -8.44) * mm, v(96, -8.34) * mm, v(96.22, -8.33) * mm]});
            skFitSpline(sketch, "E2126", {"points": [v(96.22, -8.33) * mm, v(96.67, -8.31) * mm, v(97.12, -8.3) * mm, v(97.57, -8.28) * mm]});
            skFitSpline(sketch, "E2127", {"points": [v(97.57, -8.28) * mm, v(97.6, -8.28) * mm, v(97.63, -8.27) * mm, v(97.66, -8.26) * mm]});
            skFitSpline(sketch, "E2128", {"points": [v(-66.1, 0.98) * mm, v(-66.08, 1) * mm, v(-66.06, 1) * mm, v(-66.04, 1.02) * mm]});
            skFitSpline(sketch, "E2129", {"points": [v(-66.04, 1.02) * mm, v(-66.04, 1.04) * mm, v(-66.02, 1.07) * mm, v(-66.02, 1.1) * mm]});
            skFitSpline(sketch, "E2130", {"points": [v(-66.02, 1.1) * mm, v(-66.02, 1.1) * mm, v(-66.06, 1.13) * mm, v(-66.07, 1.12) * mm]});
            skFitSpline(sketch, "E2131", {"points": [v(-66.07, 1.12) * mm, v(-66.1, 1.11) * mm, v(-66.12, 1.1) * mm, v(-66.12, 1.07) * mm]});
            skFitSpline(sketch, "E2132", {"points": [v(-66.12, 1.07) * mm, v(-66.13, 1.04) * mm, v(-66.11, 1.01) * mm, v(-66.1, 0.98) * mm]});
            skFitSpline(sketch, "E2133", {"points": [v(-64.9, -1.74) * mm, v(-65.12, -2.15) * mm, v(-65.31, -2.54) * mm, v(-65.52, -2.94) * mm]});
            skFitSpline(sketch, "E2134", {"points": [v(-65.52, -2.94) * mm, v(-65.02, -3.24) * mm, v(-64.54, -3.52) * mm, v(-64.04, -3.81) * mm]});
            skFitSpline(sketch, "E2135", {"points": [v(-64.04, -3.81) * mm, v(-63.9, -3.24) * mm, v(-63.77, -2.7) * mm, v(-63.63, -2.15) * mm]});
            skFitSpline(sketch, "E2136", {"points": [v(-63.63, -2.15) * mm, v(-64.07, -2) * mm, v(-64.47, -1.88) * mm, v(-64.9, -1.74) * mm]});
            skFitSpline(sketch, "E2137", {"points": [v(-62.08, 1.64) * mm, v(-61.9, 1.9) * mm, v(-61.75, 2.11) * mm, v(-61.6, 2.34) * mm]});
            skFitSpline(sketch, "E2138", {"points": [v(-61.6, 2.34) * mm, v(-61.47, 2.58) * mm, v(-61.35, 2.83) * mm, v(-61.22, 3.08) * mm]});
            skFitSpline(sketch, "E2139", {"points": [v(-61.22, 3.08) * mm, v(-61.75, 3.26) * mm, v(-62.29, 3.42) * mm, v(-62.86, 3.5) * mm]});
            skFitSpline(sketch, "E2140", {"points": [v(-62.86, 3.5) * mm, v(-63, 3.07) * mm, v(-63.12, 2.66) * mm, v(-63.25, 2.24) * mm]});
            skFitSpline(sketch, "E2141", {"points": [v(-63.25, 2.24) * mm, v(-62.84, 2.03) * mm, v(-62.46, 1.83) * mm, v(-62.08, 1.64) * mm]});
            skFitSpline(sketch, "E2142", {"points": [v(-70.08, 1.62) * mm, v(-69.67, 1.84) * mm, v(-69.28, 2.04) * mm, v(-68.9, 2.25) * mm]});
            skFitSpline(sketch, "E2143", {"points": [v(-68.9, 2.25) * mm, v(-69.03, 2.68) * mm, v(-69.16, 3.1) * mm, v(-69.3, 3.52) * mm]});
            skFitSpline(sketch, "E2144", {"points": [v(-69.3, 3.52) * mm, v(-69.86, 3.38) * mm, v(-70.4, 3.24) * mm, v(-70.96, 3.1) * mm]});
            skFitSpline(sketch, "E2145", {"points": [v(-70.96, 3.1) * mm, v(-70.66, 2.6) * mm, v(-70.38, 2.12) * mm, v(-70.08, 1.62) * mm]});
            skFitSpline(sketch, "E2146", {"points": [v(-70.96, -0.95) * mm, v(-70.38, -1.1) * mm, v(-69.85, -1.23) * mm, v(-69.3, -1.37) * mm]});
            skFitSpline(sketch, "E2147", {"points": [v(-69.3, -1.37) * mm, v(-69.16, -0.93) * mm, v(-69.03, -0.52) * mm, v(-68.9, -0.1) * mm]});
            skFitSpline(sketch, "E2148", {"points": [v(-68.9, -0.1) * mm, v(-69.29, 0.11) * mm, v(-69.68, 0.31) * mm, v(-70.08, 0.52) * mm]});
            skFitSpline(sketch, "E2149", {"points": [v(-70.08, 0.52) * mm, v(-70.38, 0.02) * mm, v(-70.66, -0.45) * mm, v(-70.96, -0.95) * mm]});
            skFitSpline(sketch, "E2150", {"points": [v(-68.1, 5.96) * mm, v(-68.24, 5.39) * mm, v(-68.38, 4.85) * mm, v(-68.52, 4.3) * mm]});
            skFitSpline(sketch, "E2151", {"points": [v(-68.52, 4.3) * mm, v(-68.08, 4.16) * mm, v(-67.66, 4.03) * mm, v(-67.24, 3.9) * mm]});
            skFitSpline(sketch, "E2152", {"points": [v(-67.24, 3.9) * mm, v(-67.03, 4.3) * mm, v(-66.83, 4.68) * mm, v(-66.62, 5.08) * mm]});
            skFitSpline(sketch, "E2153", {"points": [v(-66.62, 5.08) * mm, v(-67.12, 5.38) * mm, v(-67.6, 5.66) * mm, v(-68.1, 5.96) * mm]});
            skFitSpline(sketch, "E2154", {"points": [v(-65.52, 5.08) * mm, v(-65.3, 4.67) * mm, v(-65.11, 4.3) * mm, v(-64.9, 3.9) * mm]});
            skFitSpline(sketch, "E2155", {"points": [v(-64.9, 3.9) * mm, v(-64.48, 4.03) * mm, v(-64.07, 4.16) * mm, v(-63.66, 4.29) * mm]});
            skFitSpline(sketch, "E2156", {"points": [v(-63.66, 4.29) * mm, v(-63.73, 4.87) * mm, v(-63.9, 5.4) * mm, v(-64.07, 5.95) * mm]});
            skFitSpline(sketch, "E2157", {"points": [v(-64.07, 5.95) * mm, v(-64.56, 5.66) * mm, v(-65.03, 5.38) * mm, v(-65.52, 5.08) * mm]});
            skFitSpline(sketch, "E2158", {"points": [v(-61.18, -0.95) * mm, v(-61.49, -0.44) * mm, v(-61.77, 0.03) * mm, v(-62.06, 0.52) * mm]});
            skFitSpline(sketch, "E2159", {"points": [v(-62.06, 0.52) * mm, v(-62.47, 0.31) * mm, v(-62.85, 0.11) * mm, v(-63.25, -0.1) * mm]});
            skFitSpline(sketch, "E2160", {"points": [v(-63.25, -0.1) * mm, v(-63.12, -0.52) * mm, v(-62.99, -0.94) * mm, v(-62.85, -1.37) * mm]});
            skFitSpline(sketch, "E2161", {"points": [v(-62.85, -1.37) * mm, v(-62.29, -1.23) * mm, v(-61.75, -1.1) * mm, v(-61.18, -0.95) * mm]});
            skFitSpline(sketch, "E2162", {"points": [v(-66.62, -2.93) * mm, v(-66.84, -2.52) * mm, v(-67.04, -2.14) * mm, v(-67.25, -1.74) * mm]});
            skFitSpline(sketch, "E2163", {"points": [v(-67.25, -1.74) * mm, v(-67.67, -1.9) * mm, v(-68.1, -2) * mm, v(-68.52, -2.16) * mm]});
            skFitSpline(sketch, "E2164", {"points": [v(-68.52, -2.16) * mm, v(-68.38, -2.72) * mm, v(-68.24, -3.26) * mm, v(-68.1, -3.81) * mm]});
            skFitSpline(sketch, "E2165", {"points": [v(-68.1, -3.81) * mm, v(-67.6, -3.51) * mm, v(-67.11, -3.23) * mm, v(-66.62, -2.93) * mm]});
            skFitSpline(sketch, "E2166", {"points": [v(-64.32, -4.8) * mm, v(-64.53, -4.67) * mm, v(-64.73, -4.54) * mm, v(-64.93, -4.42) * mm]});
            skFitSpline(sketch, "E2167", {"points": [v(-64.93, -4.42) * mm, v(-65.19, -4.26) * mm, v(-65.46, -4.1) * mm, v(-65.72, -3.94) * mm]});
            skFitSpline(sketch, "E2168", {"points": [v(-65.72, -3.94) * mm, v(-65.99, -3.76) * mm, v(-66.15, -3.75) * mm, v(-66.41, -3.93) * mm]});
            skFitSpline(sketch, "E2169", {"points": [v(-66.41, -3.93) * mm, v(-66.42, -3.94) * mm, v(-66.42, -3.94) * mm, v(-66.43, -3.95) * mm]});
            skFitSpline(sketch, "E2170", {"points": [v(-66.43, -3.95) * mm, v(-66.69, -4.1) * mm, v(-66.95, -4.26) * mm, v(-67.2, -4.42) * mm]});
            skFitSpline(sketch, "E2171", {"points": [v(-67.2, -4.42) * mm, v(-67.4, -4.54) * mm, v(-67.6, -4.67) * mm, v(-67.82, -4.8) * mm]});
            skFitSpline(sketch, "E2172", {"points": [v(-67.82, -4.8) * mm, v(-67.32, -5.67) * mm, v(-66.72, -6.44) * mm, v(-66.07, -7.2) * mm]});
            skFitSpline(sketch, "E2173", {"points": [v(-66.07, -7.2) * mm, v(-65.42, -6.45) * mm, v(-64.83, -5.68) * mm, v(-64.32, -4.8) * mm]});
            skFitSpline(sketch, "E2174", {"points": [v(-57.8, 1.08) * mm, v(-58.57, 1.73) * mm, v(-59.33, 2.33) * mm, v(-60.18, 2.82) * mm]});
            skFitSpline(sketch, "E2175", {"points": [v(-60.18, 2.82) * mm, v(-60.23, 2.75) * mm, v(-60.27, 2.7) * mm, v(-60.3, 2.65) * mm]});
            skFitSpline(sketch, "E2176", {"points": [v(-60.3, 2.65) * mm, v(-60.58, 2.21) * mm, v(-60.84, 1.78) * mm, v(-61.1, 1.35) * mm]});
            skFitSpline(sketch, "E2177", {"points": [v(-61.1, 1.35) * mm, v(-61.23, 1.16) * mm, v(-61.23, 0.98) * mm, v(-61.1, 0.8) * mm]});
            skFitSpline(sketch, "E2178", {"points": [v(-61.1, 0.8) * mm, v(-61.09, 0.77) * mm, v(-61.07, 0.74) * mm, v(-61.05, 0.72) * mm]});
            skFitSpline(sketch, "E2179", {"points": [v(-61.05, 0.72) * mm, v(-60.9, 0.46) * mm, v(-60.74, 0.2) * mm, v(-60.58, -0.06) * mm]});
            skFitSpline(sketch, "E2180", {"points": [v(-60.58, -0.06) * mm, v(-60.46, -0.26) * mm, v(-60.33, -0.46) * mm, v(-60.2, -0.68) * mm]});
            skFitSpline(sketch, "E2181", {"points": [v(-60.2, -0.68) * mm, v(-59.33, -0.17) * mm, v(-58.56, 0.42) * mm, v(-57.8, 1.08) * mm]});
            skFitSpline(sketch, "E2182", {"points": [v(-71.95, -0.68) * mm, v(-71.81, -0.46) * mm, v(-71.7, -0.28) * mm, v(-71.58, -0.09) * mm]});
            skFitSpline(sketch, "E2183", {"points": [v(-71.58, -0.09) * mm, v(-71.41, 0.18) * mm, v(-71.25, 0.46) * mm, v(-71.08, 0.73) * mm]});
            skFitSpline(sketch, "E2184", {"points": [v(-71.08, 0.73) * mm, v(-70.9, 1) * mm, v(-70.9, 1.15) * mm, v(-71.08, 1.42) * mm]});
            skFitSpline(sketch, "E2185", {"points": [v(-71.08, 1.42) * mm, v(-71.25, 1.69) * mm, v(-71.4, 1.97) * mm, v(-71.58, 2.24) * mm]});
            skFitSpline(sketch, "E2186", {"points": [v(-71.58, 2.24) * mm, v(-71.7, 2.43) * mm, v(-71.82, 2.62) * mm, v(-71.95, 2.82) * mm]});
            skFitSpline(sketch, "E2187", {"points": [v(-71.95, 2.82) * mm, v(-72.82, 2.32) * mm, v(-73.59, 1.73) * mm, v(-74.34, 1.08) * mm]});
            skFitSpline(sketch, "E2188", {"points": [v(-74.34, 1.08) * mm, v(-73.59, 0.42) * mm, v(-72.82, -0.17) * mm, v(-71.95, -0.68) * mm]});
            skFitSpline(sketch, "E2189", {"points": [v(-71.92, 6.93) * mm, v(-71.84, 5.92) * mm, v(-71.73, 4.96) * mm, v(-71.46, 4) * mm]});
            skFitSpline(sketch, "E2190", {"points": [v(-71.46, 4) * mm, v(-71.24, 4.04) * mm, v(-71.04, 4.07) * mm, v(-70.84, 4.13) * mm]});
            skFitSpline(sketch, "E2191", {"points": [v(-70.84, 4.13) * mm, v(-70.52, 4.23) * mm, v(-70.2, 4.33) * mm, v(-69.87, 4.37) * mm]});
            skFitSpline(sketch, "E2192", {"points": [v(-69.87, 4.37) * mm, v(-69.55, 4.41) * mm, v(-69.4, 4.55) * mm, v(-69.37, 4.86) * mm]});
            skFitSpline(sketch, "E2193", {"points": [v(-69.37, 4.86) * mm, v(-69.34, 5.18) * mm, v(-69.24, 5.48) * mm, v(-69.15, 5.78) * mm]});
            skFitSpline(sketch, "E2194", {"points": [v(-69.15, 5.78) * mm, v(-69.08, 6) * mm, v(-69.04, 6.23) * mm, v(-69, 6.47) * mm]});
            skFitSpline(sketch, "E2195", {"points": [v(-69, 6.47) * mm, v(-69.96, 6.73) * mm, v(-70.92, 6.84) * mm, v(-71.92, 6.93) * mm]});
            skFitSpline(sketch, "E2196", {"points": [v(-64.32, 6.95) * mm, v(-64.82, 7.82) * mm, v(-65.42, 8.6) * mm, v(-66.07, 9.34) * mm]});
            skFitSpline(sketch, "E2197", {"points": [v(-66.07, 9.34) * mm, v(-66.72, 8.58) * mm, v(-67.32, 7.82) * mm, v(-67.82, 6.95) * mm]});
            skFitSpline(sketch, "E2198", {"points": [v(-67.82, 6.95) * mm, v(-67.63, 6.83) * mm, v(-67.45, 6.7) * mm, v(-67.27, 6.6) * mm]});
            skFitSpline(sketch, "E2199", {"points": [v(-67.27, 6.6) * mm, v(-66.98, 6.42) * mm, v(-66.7, 6.26) * mm, v(-66.4, 6.08) * mm]});
            skFitSpline(sketch, "E2200", {"points": [v(-66.4, 6.08) * mm, v(-66.15, 5.91) * mm, v(-65.99, 5.9) * mm, v(-65.74, 6.08) * mm]});
            skFitSpline(sketch, "E2201", {"points": [v(-65.74, 6.08) * mm, v(-65.73, 6.08) * mm, v(-65.72, 6.09) * mm, v(-65.72, 6.1) * mm]});
            skFitSpline(sketch, "E2202", {"points": [v(-65.72, 6.1) * mm, v(-65.46, 6.25) * mm, v(-65.2, 6.4) * mm, v(-64.94, 6.56) * mm]});
            skFitSpline(sketch, "E2203", {"points": [v(-64.94, 6.56) * mm, v(-64.74, 6.69) * mm, v(-64.54, 6.81) * mm, v(-64.32, 6.95) * mm]});
            skFitSpline(sketch, "E2204", {"points": [v(-63.16, 6.46) * mm, v(-63.1, 6.19) * mm, v(-63.03, 5.93) * mm, v(-62.97, 5.68) * mm]});
            skFitSpline(sketch, "E2205", {"points": [v(-62.97, 5.68) * mm, v(-62.9, 5.43) * mm, v(-62.84, 5.17) * mm, v(-62.8, 4.91) * mm]});
            skFitSpline(sketch, "E2206", {"points": [v(-62.8, 4.91) * mm, v(-62.73, 4.57) * mm, v(-62.6, 4.43) * mm, v(-62.25, 4.36) * mm]});
            skFitSpline(sketch, "E2207", {"points": [v(-62.25, 4.36) * mm, v(-61.97, 4.3) * mm, v(-61.7, 4.23) * mm, v(-61.43, 4.17) * mm]});
            skFitSpline(sketch, "E2208", {"points": [v(-61.43, 4.17) * mm, v(-61.19, 4.1) * mm, v(-60.94, 4.05) * mm, v(-60.68, 3.99) * mm]});
            skFitSpline(sketch, "E2209", {"points": [v(-60.68, 3.99) * mm, v(-60.42, 4.96) * mm, v(-60.3, 5.93) * mm, v(-60.22, 6.93) * mm]});
            skFitSpline(sketch, "E2210", {"points": [v(-60.22, 6.93) * mm, v(-61.21, 6.84) * mm, v(-62.17, 6.73) * mm, v(-63.16, 6.46) * mm]});
            skFitSpline(sketch, "E2211", {"points": [v(-68.99, -4.3) * mm, v(-69.06, -4.02) * mm, v(-69.12, -3.76) * mm, v(-69.19, -3.5) * mm]});
            skFitSpline(sketch, "E2212", {"points": [v(-69.19, -3.5) * mm, v(-69.25, -3.25) * mm, v(-69.32, -3) * mm, v(-69.36, -2.74) * mm]});
            skFitSpline(sketch, "E2213", {"points": [v(-69.36, -2.74) * mm, v(-69.42, -2.41) * mm, v(-69.54, -2.29) * mm, v(-69.86, -2.22) * mm]});
            skFitSpline(sketch, "E2214", {"points": [v(-69.86, -2.22) * mm, v(-70.17, -2.15) * mm, v(-70.48, -2.07) * mm, v(-70.79, -2) * mm]});
            skFitSpline(sketch, "E2215", {"points": [v(-70.79, -2) * mm, v(-71, -1.94) * mm, v(-71.23, -1.9) * mm, v(-71.45, -1.85) * mm]});
            skFitSpline(sketch, "E2216", {"points": [v(-71.45, -1.85) * mm, v(-71.67, -2.43) * mm, v(-71.95, -4.34) * mm, v(-71.89, -4.76) * mm]});
            skFitSpline(sketch, "E2217", {"points": [v(-71.89, -4.76) * mm, v(-71.14, -4.76) * mm, v(-69.54, -4.5) * mm, v(-68.99, -4.3) * mm]});
            skFitSpline(sketch, "E2218", {"points": [v(-63.15, -4.3) * mm, v(-62.66, -4.5) * mm, v(-60.73, -4.8) * mm, v(-60.23, -4.75) * mm]});
            skFitSpline(sketch, "E2219", {"points": [v(-60.23, -4.75) * mm, v(-60.27, -3.68) * mm, v(-60.53, -2.15) * mm, v(-60.73, -1.84) * mm]});
            skFitSpline(sketch, "E2220", {"points": [v(-60.73, -1.84) * mm, v(-60.98, -1.9) * mm, v(-61.23, -1.97) * mm, v(-61.48, -2.04) * mm]});
            skFitSpline(sketch, "E2221", {"points": [v(-61.48, -2.04) * mm, v(-61.74, -2.1) * mm, v(-62, -2.16) * mm, v(-62.25, -2.22) * mm]});
            skFitSpline(sketch, "E2222", {"points": [v(-62.25, -2.22) * mm, v(-62.35, -2.24) * mm, v(-62.45, -2.27) * mm, v(-62.55, -2.31) * mm]});
            skFitSpline(sketch, "E2223", {"points": [v(-62.55, -2.31) * mm, v(-62.6, -2.34) * mm, v(-62.65, -2.38) * mm, v(-62.68, -2.43) * mm]});
            skFitSpline(sketch, "E2224", {"points": [v(-62.68, -2.43) * mm, v(-62.72, -2.53) * mm, v(-62.77, -2.63) * mm, v(-62.78, -2.73) * mm]});
            skFitSpline(sketch, "E2225", {"points": [v(-62.78, -2.73) * mm, v(-62.8, -3.06) * mm, v(-62.92, -3.36) * mm, v(-63.01, -3.68) * mm]});
            skFitSpline(sketch, "E2226", {"points": [v(-63.01, -3.68) * mm, v(-63.07, -3.88) * mm, v(-63.1, -4.1) * mm, v(-63.15, -4.3) * mm]});
            skFitSpline(sketch, "E2227", {"points": [v(-53.62, -1.26) * mm, v(-52.38, -0.55) * mm, v(-51.22, 0.2) * mm, v(-50.1, 1.08) * mm]});
            skFitSpline(sketch, "E2228", {"points": [v(-50.1, 1.08) * mm, v(-51.23, 1.95) * mm, v(-52.4, 2.7) * mm, v(-53.6, 3.4) * mm]});
            skFitSpline(sketch, "E2229", {"points": [v(-53.6, 3.4) * mm, v(-53.84, 3.25) * mm, v(-56.15, 1.2) * mm, v(-56.26, 1.04) * mm]});
            skFitSpline(sketch, "E2230", {"points": [v(-56.26, 1.04) * mm, v(-55.38, 0.28) * mm, v(-54.5, -0.49) * mm, v(-53.62, -1.26) * mm]});
            skFitSpline(sketch, "E2231", {"points": [v(-66.07, -8.7) * mm, v(-66.86, -9.6) * mm, v(-67.63, -10.5) * mm, v(-68.4, -11.38) * mm]});
            skFitSpline(sketch, "E2232", {"points": [v(-68.4, -11.38) * mm, v(-67.7, -12.6) * mm, v(-66.94, -13.78) * mm, v(-66.07, -14.9) * mm]});
            skFitSpline(sketch, "E2233", {"points": [v(-66.07, -14.9) * mm, v(-65.2, -13.77) * mm, v(-64.44, -12.6) * mm, v(-63.74, -11.38) * mm]});
            skFitSpline(sketch, "E2234", {"points": [v(-63.74, -11.38) * mm, v(-64.51, -10.5) * mm, v(-65.28, -9.6) * mm, v(-66.07, -8.7) * mm]});
            skFitSpline(sketch, "E2235", {"points": [v(-66.07, 17.05) * mm, v(-66.94, 15.92) * mm, v(-67.7, 14.76) * mm, v(-68.4, 13.53) * mm]});
            skFitSpline(sketch, "E2236", {"points": [v(-68.4, 13.53) * mm, v(-67.63, 12.65) * mm, v(-66.87, 11.75) * mm, v(-66.07, 10.86) * mm]});
            skFitSpline(sketch, "E2237", {"points": [v(-66.07, 10.86) * mm, v(-65.28, 11.76) * mm, v(-64.5, 12.65) * mm, v(-63.74, 13.53) * mm]});
            skFitSpline(sketch, "E2238", {"points": [v(-63.74, 13.53) * mm, v(-64.44, 14.76) * mm, v(-65.2, 15.93) * mm, v(-66.07, 17.05) * mm]});
            skFitSpline(sketch, "E2239", {"points": [v(-82.05, 1.08) * mm, v(-80.92, 0.2) * mm, v(-79.75, -0.56) * mm, v(-78.53, -1.26) * mm]});
            skFitSpline(sketch, "E2240", {"points": [v(-78.53, -1.26) * mm, v(-77.63, -0.48) * mm, v(-76.75, 0.29) * mm, v(-75.85, 1.08) * mm]});
            skFitSpline(sketch, "E2241", {"points": [v(-75.85, 1.08) * mm, v(-75.95, 1.16) * mm, v(-76.02, 1.22) * mm, v(-76.09, 1.29) * mm]});
            skFitSpline(sketch, "E2242", {"points": [v(-76.09, 1.29) * mm, v(-76.48, 1.62) * mm, v(-76.86, 1.95) * mm, v(-77.25, 2.29) * mm]});
            skFitSpline(sketch, "E2243", {"points": [v(-77.25, 2.29) * mm, v(-77.62, 2.6) * mm, v(-77.98, 2.93) * mm, v(-78.34, 3.26) * mm]});
            skFitSpline(sketch, "E2244", {"points": [v(-78.34, 3.26) * mm, v(-78.51, 3.41) * mm, v(-78.51, 3.42) * mm, v(-78.73, 3.3) * mm]});
            skFitSpline(sketch, "E2245", {"points": [v(-78.73, 3.3) * mm, v(-79.6, 2.78) * mm, v(-80.47, 2.24) * mm, v(-81.3, 1.63) * mm]});
            skFitSpline(sketch, "E2246", {"points": [v(-81.3, 1.63) * mm, v(-81.54, 1.46) * mm, v(-81.79, 1.27) * mm, v(-82.05, 1.08) * mm]});
            skFitSpline(sketch, "E2247", {"points": [v(-76.53, -6.08) * mm, v(-76.9, -7.45) * mm, v(-77.2, -8.81) * mm, v(-77.37, -10.22) * mm]});
            skFitSpline(sketch, "E2248", {"points": [v(-77.37, -10.22) * mm, v(-75.95, -10.05) * mm, v(-74.58, -9.76) * mm, v(-73.22, -9.38) * mm]});
            skFitSpline(sketch, "E2249", {"points": [v(-73.22, -9.38) * mm, v(-73.14, -8.19) * mm, v(-73.06, -7.02) * mm, v(-72.98, -5.83) * mm]});
            skFitSpline(sketch, "E2250", {"points": [v(-72.98, -5.83) * mm, v(-74.18, -5.92) * mm, v(-75.35, -6) * mm, v(-76.53, -6.08) * mm]});
            skFitSpline(sketch, "E2251", {"points": [v(-59.13, -5.84) * mm, v(-59.13, -6.06) * mm, v(-59.15, -6.26) * mm, v(-59.13, -6.47) * mm]});
            skFitSpline(sketch, "E2252", {"points": [v(-59.13, -6.47) * mm, v(-59.1, -6.92) * mm, v(-59.05, -7.37) * mm, v(-59.02, -7.82) * mm]});
            skFitSpline(sketch, "E2253", {"points": [v(-59.02, -7.82) * mm, v(-58.99, -8.27) * mm, v(-58.97, -8.72) * mm, v(-58.95, -9.16) * mm]});
            skFitSpline(sketch, "E2254", {"points": [v(-58.95, -9.16) * mm, v(-58.94, -9.37) * mm, v(-58.93, -9.38) * mm, v(-58.73, -9.44) * mm]});
            skFitSpline(sketch, "E2255", {"points": [v(-58.73, -9.44) * mm, v(-57.72, -9.7) * mm, v(-56.7, -9.94) * mm, v(-55.66, -10.1) * mm]});
            skFitSpline(sketch, "E2256", {"points": [v(-55.66, -10.1) * mm, v(-55.38, -10.14) * mm, v(-55.09, -10.18) * mm, v(-54.8, -10.22) * mm]});
            skFitSpline(sketch, "E2257", {"points": [v(-54.8, -10.22) * mm, v(-54.8, -9.52) * mm, v(-55.39, -6.7) * mm, v(-55.64, -6.07) * mm]});
            skFitSpline(sketch, "E2258", {"points": [v(-55.64, -6.07) * mm, v(-56.8, -6) * mm, v(-57.97, -5.92) * mm, v(-59.13, -5.84) * mm]});
            skFitSpline(sketch, "E2259", {"points": [v(-72.98, 7.98) * mm, v(-73.06, 9.18) * mm, v(-73.14, 10.35) * mm, v(-73.22, 11.52) * mm]});
            skFitSpline(sketch, "E2260", {"points": [v(-73.22, 11.52) * mm, v(-73.3, 11.55) * mm, v(-73.38, 11.57) * mm, v(-73.46, 11.6) * mm]});
            skFitSpline(sketch, "E2261", {"points": [v(-73.46, 11.6) * mm, v(-74.65, 11.92) * mm, v(-75.87, 12.15) * mm, v(-77.1, 12.34) * mm]});
            skFitSpline(sketch, "E2262", {"points": [v(-77.1, 12.34) * mm, v(-77.18, 12.36) * mm, v(-77.27, 12.35) * mm, v(-77.37, 12.35) * mm]});
            skFitSpline(sketch, "E2263", {"points": [v(-77.37, 12.35) * mm, v(-77.19, 10.94) * mm, v(-76.9, 9.58) * mm, v(-76.53, 8.22) * mm]});
            skFitSpline(sketch, "E2264", {"points": [v(-76.53, 8.22) * mm, v(-75.34, 8.14) * mm, v(-74.18, 8.06) * mm, v(-72.98, 7.98) * mm]});
            skFitSpline(sketch, "E2265", {"points": [v(-54.77, 12.37) * mm, v(-56.2, 12.2) * mm, v(-57.56, 11.9) * mm, v(-58.92, 11.53) * mm]});
            skFitSpline(sketch, "E2266", {"points": [v(-58.92, 11.53) * mm, v(-59, 10.35) * mm, v(-59.08, 9.18) * mm, v(-59.17, 7.98) * mm]});
            skFitSpline(sketch, "E2267", {"points": [v(-59.17, 7.98) * mm, v(-57.96, 8.06) * mm, v(-56.79, 8.14) * mm, v(-55.62, 8.22) * mm]});
            skFitSpline(sketch, "E2268", {"points": [v(-55.62, 8.22) * mm, v(-55.24, 9.6) * mm, v(-54.96, 10.95) * mm, v(-54.77, 12.37) * mm]});
            skFitSpline(sketch, "E2269", {"points": [v(-66.72, -7.98) * mm, v(-67.28, -7.26) * mm, v(-67.82, -6.56) * mm, v(-68.37, -5.85) * mm]});
            skFitSpline(sketch, "E2270", {"points": [v(-68.37, -5.85) * mm, v(-68.4, -5.9) * mm, v(-68.43, -5.97) * mm, v(-68.45, -6.03) * mm]});
            skFitSpline(sketch, "E2271", {"points": [v(-68.45, -6.03) * mm, v(-68.63, -6.44) * mm, v(-68.8, -6.86) * mm, v(-69, -7.26) * mm]});
            skFitSpline(sketch, "E2272", {"points": [v(-69, -7.26) * mm, v(-69.05, -7.4) * mm, v(-69.07, -7.5) * mm, v(-68.97, -7.63) * mm]});
            skFitSpline(sketch, "E2273", {"points": [v(-68.97, -7.63) * mm, v(-68.9, -7.7) * mm, v(-68.87, -7.82) * mm, v(-68.85, -7.91) * mm]});
            skFitSpline(sketch, "E2274", {"points": [v(-68.85, -7.91) * mm, v(-68.75, -8.34) * mm, v(-68.66, -8.77) * mm, v(-68.58, -9.2) * mm]});
            skFitSpline(sketch, "E2275", {"points": [v(-68.58, -9.2) * mm, v(-68.51, -9.54) * mm, v(-68.76, -9.82) * mm, v(-69.09, -9.8) * mm]});
            skFitSpline(sketch, "E2276", {"points": [v(-69.09, -9.8) * mm, v(-69.3, -9.78) * mm, v(-69.46, -9.64) * mm, v(-69.52, -9.43) * mm]});
            skFitSpline(sketch, "E2277", {"points": [v(-69.52, -9.43) * mm, v(-69.55, -9.3) * mm, v(-69.58, -9.17) * mm, v(-69.62, -9) * mm]});
            skFitSpline(sketch, "E2278", {"points": [v(-69.62, -9) * mm, v(-69.66, -9.07) * mm, v(-69.7, -9.1) * mm, v(-69.7, -9.14) * mm]});
            skFitSpline(sketch, "E2279", {"points": [v(-69.7, -9.14) * mm, v(-69.96, -9.9) * mm, v(-70.22, -10.65) * mm, v(-70.48, -11.4) * mm]});
            skFitSpline(sketch, "E2280", {"points": [v(-70.48, -11.4) * mm, v(-70.53, -11.53) * mm, v(-70.54, -11.63) * mm, v(-70.44, -11.75) * mm]});
            skFitSpline(sketch, "E2281", {"points": [v(-70.44, -11.75) * mm, v(-70.32, -11.9) * mm, v(-70.26, -12.07) * mm, v(-70.24, -12.26) * mm]});
            skFitSpline(sketch, "E2282", {"points": [v(-70.24, -12.26) * mm, v(-70.19, -12.82) * mm, v(-70.04, -13.36) * mm, v(-69.88, -13.9) * mm]});
            skFitSpline(sketch, "E2283", {"points": [v(-69.88, -13.9) * mm, v(-69.83, -14.03) * mm, v(-69.8, -14.17) * mm, v(-69.76, -14.3) * mm]});
            skFitSpline(sketch, "E2284", {"points": [v(-69.76, -14.3) * mm, v(-69.7, -14.6) * mm, v(-69.85, -14.84) * mm, v(-70.1, -14.9) * mm]});
            skFitSpline(sketch, "E2285", {"points": [v(-70.1, -14.9) * mm, v(-70.37, -14.97) * mm, v(-70.62, -14.84) * mm, v(-70.7, -14.55) * mm]});
            skFitSpline(sketch, "E2286", {"points": [v(-70.7, -14.55) * mm, v(-70.82, -14.16) * mm, v(-70.93, -13.75) * mm, v(-71.04, -13.36) * mm]});
            skFitSpline(sketch, "E2287", {"points": [v(-71.04, -13.36) * mm, v(-71.05, -13.32) * mm, v(-71.07, -13.28) * mm, v(-71.09, -13.2) * mm]});
            skFitSpline(sketch, "E2288", {"points": [v(-71.09, -13.2) * mm, v(-71.13, -13.27) * mm, v(-71.16, -13.31) * mm, v(-71.18, -13.35) * mm]});
            skFitSpline(sketch, "E2289", {"points": [v(-71.18, -13.35) * mm, v(-71.4, -13.79) * mm, v(-71.35, -14.24) * mm, v(-71.27, -14.7) * mm]});
            skFitSpline(sketch, "E2290", {"points": [v(-71.27, -14.7) * mm, v(-71.14, -15.36) * mm, v(-71, -16.02) * mm, v(-70.87, -16.68) * mm]});
            skFitSpline(sketch, "E2291", {"points": [v(-70.87, -16.68) * mm, v(-70.8, -16.97) * mm, v(-70.95, -17.23) * mm, v(-71.22, -17.3) * mm]});
            skFitSpline(sketch, "E2292", {"points": [v(-71.22, -17.3) * mm, v(-71.47, -17.37) * mm, v(-71.72, -17.22) * mm, v(-71.8, -16.94) * mm]});
            skFitSpline(sketch, "E2293", {"points": [v(-71.8, -16.94) * mm, v(-71.87, -16.74) * mm, v(-71.9, -16.53) * mm, v(-71.95, -16.31) * mm]});
            skFitSpline(sketch, "E2294", {"points": [v(-71.95, -16.31) * mm, v(-72.02, -15.99) * mm, v(-72.1, -15.66) * mm, v(-72.14, -15.33) * mm]});
            skFitSpline(sketch, "E2295", {"points": [v(-72.14, -15.33) * mm, v(-72.2, -14.97) * mm, v(-72.24, -14.6) * mm, v(-72.3, -14.24) * mm]});
            skFitSpline(sketch, "E2296", {"points": [v(-72.3, -14.24) * mm, v(-72.3, -14.18) * mm, v(-72.3, -14.12) * mm, v(-72.32, -14.03) * mm]});
            skFitSpline(sketch, "E2297", {"points": [v(-72.32, -14.03) * mm, v(-72.39, -14.07) * mm, v(-72.44, -14.1) * mm, v(-72.49, -14.14) * mm]});
            skFitSpline(sketch, "E2298", {"points": [v(-72.49, -14.14) * mm, v(-72.91, -14.5) * mm, v(-73.37, -14.83) * mm, v(-73.85, -15.12) * mm]});
            skFitSpline(sketch, "E2299", {"points": [v(-73.85, -15.12) * mm, v(-74.06, -15.26) * mm, v(-74.27, -15.41) * mm, v(-74.48, -15.55) * mm]});
            skFitSpline(sketch, "E2300", {"points": [v(-74.48, -15.55) * mm, v(-74.59, -15.62) * mm, v(-74.7, -15.7) * mm, v(-74.81, -15.75) * mm]});
            skFitSpline(sketch, "E2301", {"points": [v(-74.81, -15.75) * mm, v(-75.06, -15.85) * mm, v(-75.33, -15.75) * mm, v(-75.45, -15.52) * mm]});
            skFitSpline(sketch, "E2302", {"points": [v(-75.45, -15.52) * mm, v(-75.56, -15.3) * mm, v(-75.49, -15.04) * mm, v(-75.27, -14.9) * mm]});
            skFitSpline(sketch, "E2303", {"points": [v(-75.27, -14.9) * mm, v(-74.85, -14.62) * mm, v(-74.42, -14.35) * mm, v(-74, -14.06) * mm]});
            skFitSpline(sketch, "E2304", {"points": [v(-74, -14.06) * mm, v(-73.67, -13.83) * mm, v(-73.34, -13.57) * mm, v(-73.02, -13.3) * mm]});
            skFitSpline(sketch, "E2305", {"points": [v(-73.02, -13.3) * mm, v(-72.8, -13.13) * mm, v(-72.73, -12.87) * mm, v(-72.6, -12.57) * mm]});
            skFitSpline(sketch, "E2306", {"points": [v(-72.6, -12.57) * mm, v(-72.7, -12.62) * mm, v(-72.74, -12.63) * mm, v(-72.79, -12.66) * mm]});
            skFitSpline(sketch, "E2307", {"points": [v(-72.79, -12.66) * mm, v(-73.12, -12.84) * mm, v(-73.44, -13.03) * mm, v(-73.77, -13.2) * mm]});
            skFitSpline(sketch, "E2308", {"points": [v(-73.77, -13.2) * mm, v(-74.1, -13.39) * mm, v(-74.38, -13.33) * mm, v(-74.52, -13.07) * mm]});
            skFitSpline(sketch, "E2309", {"points": [v(-74.52, -13.07) * mm, v(-74.67, -12.82) * mm, v(-74.57, -12.55) * mm, v(-74.27, -12.37) * mm]});
            skFitSpline(sketch, "E2310", {"points": [v(-74.27, -12.37) * mm, v(-74.13, -12.29) * mm, v(-74, -12.2) * mm, v(-73.85, -12.14) * mm]});
            skFitSpline(sketch, "E2311", {"points": [v(-73.85, -12.14) * mm, v(-73.43, -11.92) * mm, v(-73.02, -11.68) * mm, v(-72.66, -11.38) * mm]});
            skFitSpline(sketch, "E2312", {"points": [v(-72.66, -11.38) * mm, v(-72.43, -11.2) * mm, v(-72.18, -11.07) * mm, v(-71.85, -11.05) * mm]});
            skFitSpline(sketch, "E2313", {"points": [v(-71.85, -11.05) * mm, v(-71.46, -10.26) * mm, v(-71.07, -9.45) * mm, v(-70.66, -8.6) * mm]});
            skFitSpline(sketch, "E2314", {"points": [v(-70.66, -8.6) * mm, v(-70.85, -8.63) * mm, v(-70.94, -8.72) * mm, v(-71.05, -8.78) * mm]});
            skFitSpline(sketch, "E2315", {"points": [v(-71.05, -8.78) * mm, v(-71.36, -8.96) * mm, v(-71.7, -8.82) * mm, v(-71.79, -8.48) * mm]});
            skFitSpline(sketch, "E2316", {"points": [v(-71.79, -8.48) * mm, v(-71.83, -8.32) * mm, v(-71.77, -8.18) * mm, v(-71.67, -8.06) * mm]});
            skFitSpline(sketch, "E2317", {"points": [v(-71.67, -8.06) * mm, v(-71.6, -7.98) * mm, v(-71.5, -7.92) * mm, v(-71.41, -7.85) * mm]});
            skFitSpline(sketch, "E2318", {"points": [v(-71.41, -7.85) * mm, v(-71.15, -7.68) * mm, v(-70.9, -7.5) * mm, v(-70.63, -7.35) * mm]});
            skFitSpline(sketch, "E2319", {"points": [v(-70.63, -7.35) * mm, v(-70.46, -7.25) * mm, v(-70.28, -7.18) * mm, v(-70.1, -7.12) * mm]});
            skFitSpline(sketch, "E2320", {"points": [v(-70.1, -7.12) * mm, v(-70.03, -7.09) * mm, v(-69.98, -7.07) * mm, v(-69.95, -7) * mm]});
            skFitSpline(sketch, "E2321", {"points": [v(-69.95, -7) * mm, v(-69.75, -6.47) * mm, v(-69.55, -5.96) * mm, v(-69.35, -5.44) * mm]});
            skFitSpline(sketch, "E2322", {"points": [v(-69.35, -5.44) * mm, v(-70.23, -5.56) * mm, v(-71.12, -5.67) * mm, v(-72, -5.78) * mm]});
            skFitSpline(sketch, "E2323", {"points": [v(-72, -5.78) * mm, v(-72.02, -5.99) * mm, v(-72.04, -6.19) * mm, v(-72.05, -6.38) * mm]});
            skFitSpline(sketch, "E2324", {"points": [v(-72.05, -6.38) * mm, v(-72.08, -6.86) * mm, v(-72.12, -7.34) * mm, v(-72.15, -7.81) * mm]});
            skFitSpline(sketch, "E2325", {"points": [v(-72.15, -7.81) * mm, v(-72.19, -8.4) * mm, v(-72.21, -8.98) * mm, v(-72.24, -9.56) * mm]});
            skFitSpline(sketch, "E2326", {"points": [v(-72.24, -9.56) * mm, v(-72.25, -9.6) * mm, v(-72.24, -9.66) * mm, v(-72.26, -9.7) * mm]});
            skFitSpline(sketch, "E2327", {"points": [v(-72.26, -9.7) * mm, v(-72.4, -9.95) * mm, v(-72.55, -10.21) * mm, v(-72.87, -10.3) * mm]});
            skFitSpline(sketch, "E2328", {"points": [v(-72.87, -10.3) * mm, v(-74.12, -10.63) * mm, v(-75.38, -10.92) * mm, v(-76.66, -11.1) * mm]});
            skFitSpline(sketch, "E2329", {"points": [v(-76.66, -11.1) * mm, v(-76.86, -11.14) * mm, v(-77.07, -11.18) * mm, v(-77.27, -11.21) * mm]});
            skFitSpline(sketch, "E2330", {"points": [v(-77.27, -11.21) * mm, v(-77.58, -11.26) * mm, v(-77.84, -11.21) * mm, v(-78.1, -10.97) * mm]});
            skFitSpline(sketch, "E2331", {"points": [v(-78.1, -10.97) * mm, v(-78.39, -10.68) * mm, v(-78.4, -10.39) * mm, v(-78.34, -10.03) * mm]});
            skFitSpline(sketch, "E2332", {"points": [v(-78.34, -10.03) * mm, v(-78.25, -9.55) * mm, v(-78.18, -9.07) * mm, v(-78.1, -8.6) * mm]});
            skFitSpline(sketch, "E2333", {"points": [v(-78.1, -8.6) * mm, v(-77.94, -7.62) * mm, v(-77.7, -6.66) * mm, v(-77.44, -5.7) * mm]});
            skFitSpline(sketch, "E2334", {"points": [v(-77.44, -5.7) * mm, v(-77.4, -5.55) * mm, v(-77.32, -5.44) * mm, v(-77.2, -5.35) * mm]});
            skFitSpline(sketch, "E2335", {"points": [v(-77.2, -5.35) * mm, v(-77.14, -5.31) * mm, v(-77.1, -5.25) * mm, v(-77.04, -5.22) * mm]});
            skFitSpline(sketch, "E2336", {"points": [v(-77.04, -5.22) * mm, v(-76.94, -5.17) * mm, v(-76.83, -5.11) * mm, v(-76.73, -5.1) * mm]});
            skFitSpline(sketch, "E2337", {"points": [v(-76.73, -5.1) * mm, v(-75.72, -5.03) * mm, v(-74.71, -4.97) * mm, v(-73.7, -4.9) * mm]});
            skFitSpline(sketch, "E2338", {"points": [v(-73.7, -4.9) * mm, v(-73.45, -4.89) * mm, v(-73.2, -4.88) * mm, v(-72.93, -4.87) * mm]});
            skFitSpline(sketch, "E2339", {"points": [v(-72.93, -4.87) * mm, v(-72.82, -3.98) * mm, v(-72.7, -3.1) * mm, v(-72.6, -2.2) * mm]});
            skFitSpline(sketch, "E2340", {"points": [v(-72.6, -2.2) * mm, v(-72.64, -2.22) * mm, v(-72.7, -2.24) * mm, v(-72.76, -2.26) * mm]});
            skFitSpline(sketch, "E2341", {"points": [v(-72.76, -2.26) * mm, v(-73.18, -2.42) * mm, v(-73.6, -2.6) * mm, v(-74.03, -2.76) * mm]});
            skFitSpline(sketch, "E2342", {"points": [v(-74.03, -2.76) * mm, v(-74.16, -2.8) * mm, v(-74.25, -2.86) * mm, v(-74.28, -3.03) * mm]});
            skFitSpline(sketch, "E2343", {"points": [v(-74.28, -3.03) * mm, v(-74.3, -3.27) * mm, v(-74.48, -3.46) * mm, v(-74.61, -3.66) * mm]});
            skFitSpline(sketch, "E2344", {"points": [v(-74.61, -3.66) * mm, v(-74.73, -3.83) * mm, v(-74.85, -4.02) * mm, v(-74.96, -4.2) * mm]});
            skFitSpline(sketch, "E2345", {"points": [v(-74.96, -4.2) * mm, v(-75.03, -4.3) * mm, v(-75.1, -4.42) * mm, v(-75.19, -4.5) * mm]});
            skFitSpline(sketch, "E2346", {"points": [v(-75.19, -4.5) * mm, v(-75.36, -4.68) * mm, v(-75.61, -4.7) * mm, v(-75.8, -4.56) * mm]});
            skFitSpline(sketch, "E2347", {"points": [v(-75.8, -4.56) * mm, v(-76, -4.42) * mm, v(-76.06, -4.16) * mm, v(-75.95, -3.94) * mm]});
            skFitSpline(sketch, "E2348", {"points": [v(-75.95, -3.94) * mm, v(-75.88, -3.82) * mm, v(-75.8, -3.7) * mm, v(-75.76, -3.55) * mm]});
            skFitSpline(sketch, "E2349", {"points": [v(-75.76, -3.55) * mm, v(-76.01, -3.66) * mm, v(-76.27, -3.76) * mm, v(-76.52, -3.88) * mm]});
            skFitSpline(sketch, "E2350", {"points": [v(-76.52, -3.88) * mm, v(-77.03, -4.13) * mm, v(-77.53, -4.39) * mm, v(-78.04, -4.64) * mm]});
            skFitSpline(sketch, "E2351", {"points": [v(-78.04, -4.64) * mm, v(-78.15, -4.7) * mm, v(-78.2, -4.76) * mm, v(-78.22, -4.89) * mm]});
            skFitSpline(sketch, "E2352", {"points": [v(-78.22, -4.89) * mm, v(-78.25, -5.09) * mm, v(-78.34, -5.27) * mm, v(-78.47, -5.43) * mm]});
            skFitSpline(sketch, "E2353", {"points": [v(-78.47, -5.43) * mm, v(-78.82, -5.86) * mm, v(-79.1, -6.35) * mm, v(-79.36, -6.84) * mm]});
            skFitSpline(sketch, "E2354", {"points": [v(-79.36, -6.84) * mm, v(-79.42, -6.96) * mm, v(-79.48, -7.07) * mm, v(-79.55, -7.18) * mm]});
            skFitSpline(sketch, "E2355", {"points": [v(-79.55, -7.18) * mm, v(-79.72, -7.43) * mm, v(-80, -7.5) * mm, v(-80.23, -7.37) * mm]});
            skFitSpline(sketch, "E2356", {"points": [v(-80.23, -7.37) * mm, v(-80.47, -7.23) * mm, v(-80.53, -6.95) * mm, v(-80.38, -6.67) * mm]});
            skFitSpline(sketch, "E2357", {"points": [v(-80.38, -6.67) * mm, v(-80.2, -6.34) * mm, v(-80.02, -6.02) * mm, v(-79.83, -5.69) * mm]});
            skFitSpline(sketch, "E2358", {"points": [v(-79.83, -5.69) * mm, v(-79.8, -5.62) * mm, v(-79.76, -5.55) * mm, v(-79.74, -5.47) * mm]});
            skFitSpline(sketch, "E2359", {"points": [v(-79.74, -5.47) * mm, v(-80.03, -5.6) * mm, v(-80.34, -5.68) * mm, v(-80.54, -5.96) * mm]});
            skFitSpline(sketch, "E2360", {"points": [v(-80.54, -5.96) * mm, v(-80.77, -6.28) * mm, v(-81.02, -6.6) * mm, v(-81.25, -6.92) * mm]});
            skFitSpline(sketch, "E2361", {"points": [v(-81.25, -6.92) * mm, v(-81.52, -7.3) * mm, v(-81.77, -7.7) * mm, v(-82.03, -8.1) * mm]});
            skFitSpline(sketch, "E2362", {"points": [v(-82.03, -8.1) * mm, v(-82.19, -8.34) * mm, v(-82.46, -8.42) * mm, v(-82.7, -8.29) * mm]});
            skFitSpline(sketch, "E2363", {"points": [v(-82.7, -8.29) * mm, v(-82.92, -8.16) * mm, v(-83, -7.89) * mm, v(-82.88, -7.64) * mm]});
            skFitSpline(sketch, "E2364", {"points": [v(-82.88, -7.64) * mm, v(-82.8, -7.48) * mm, v(-82.7, -7.33) * mm, v(-82.6, -7.17) * mm]});
            skFitSpline(sketch, "E2365", {"points": [v(-82.6, -7.17) * mm, v(-82.24, -6.66) * mm, v(-81.89, -6.15) * mm, v(-81.53, -5.64) * mm]});
            skFitSpline(sketch, "E2366", {"points": [v(-81.53, -5.64) * mm, v(-81.43, -5.49) * mm, v(-81.3, -5.35) * mm, v(-81.17, -5.18) * mm]});
            skFitSpline(sketch, "E2367", {"points": [v(-81.17, -5.18) * mm, v(-81.26, -5.17) * mm, v(-81.33, -5.15) * mm, v(-81.4, -5.14) * mm]});
            skFitSpline(sketch, "E2368", {"points": [v(-81.4, -5.14) * mm, v(-81.9, -5.06) * mm, v(-82.41, -5) * mm, v(-82.92, -4.9) * mm]});
            skFitSpline(sketch, "E2369", {"points": [v(-82.92, -4.9) * mm, v(-83.22, -4.86) * mm, v(-83.51, -4.8) * mm, v(-83.8, -4.73) * mm]});
            skFitSpline(sketch, "E2370", {"points": [v(-83.8, -4.73) * mm, v(-83.93, -4.7) * mm, v(-84.04, -4.68) * mm, v(-84.15, -4.64) * mm]});
            skFitSpline(sketch, "E2371", {"points": [v(-84.15, -4.64) * mm, v(-84.39, -4.54) * mm, v(-84.51, -4.3) * mm, v(-84.45, -4.07) * mm]});
            skFitSpline(sketch, "E2372", {"points": [v(-84.45, -4.07) * mm, v(-84.37, -3.81) * mm, v(-84.15, -3.66) * mm, v(-83.88, -3.71) * mm]});
            skFitSpline(sketch, "E2373", {"points": [v(-83.88, -3.71) * mm, v(-83.51, -3.78) * mm, v(-83.15, -3.86) * mm, v(-82.78, -3.94) * mm]});
            skFitSpline(sketch, "E2374", {"points": [v(-82.78, -3.94) * mm, v(-82.29, -4.05) * mm, v(-81.8, -4.13) * mm, v(-81.3, -4.19) * mm]});
            skFitSpline(sketch, "E2375", {"points": [v(-81.3, -4.19) * mm, v(-80.96, -4.22) * mm, v(-80.68, -4.09) * mm, v(-80.38, -3.94) * mm]});
            skFitSpline(sketch, "E2376", {"points": [v(-80.38, -3.94) * mm, v(-80.42, -3.93) * mm, v(-80.47, -3.9) * mm, v(-80.51, -3.9) * mm]});
            skFitSpline(sketch, "E2377", {"points": [v(-80.51, -3.9) * mm, v(-80.88, -3.79) * mm, v(-81.25, -3.68) * mm, v(-81.62, -3.58) * mm]});
            skFitSpline(sketch, "E2378", {"points": [v(-81.62, -3.58) * mm, v(-81.69, -3.56) * mm, v(-81.76, -3.54) * mm, v(-81.82, -3.5) * mm]});
            skFitSpline(sketch, "E2379", {"points": [v(-81.82, -3.5) * mm, v(-82.02, -3.4) * mm, v(-82.11, -3.17) * mm, v(-82.05, -2.95) * mm]});
            skFitSpline(sketch, "E2380", {"points": [v(-82.05, -2.95) * mm, v(-81.98, -2.73) * mm, v(-81.8, -2.59) * mm, v(-81.56, -2.6) * mm]});
            skFitSpline(sketch, "E2381", {"points": [v(-81.56, -2.6) * mm, v(-81.44, -2.62) * mm, v(-81.32, -2.64) * mm, v(-81.21, -2.68) * mm]});
            skFitSpline(sketch, "E2382", {"points": [v(-81.21, -2.68) * mm, v(-80.6, -2.87) * mm, v(-79.97, -3.04) * mm, v(-79.32, -3.12) * mm]});
            skFitSpline(sketch, "E2383", {"points": [v(-79.32, -3.12) * mm, v(-79.17, -3.13) * mm, v(-79.02, -3.22) * mm, v(-78.89, -3.3) * mm]});
            skFitSpline(sketch, "E2384", {"points": [v(-78.89, -3.3) * mm, v(-78.78, -3.37) * mm, v(-78.7, -3.4) * mm, v(-78.58, -3.35) * mm]});
            skFitSpline(sketch, "E2385", {"points": [v(-78.58, -3.35) * mm, v(-77.99, -3.14) * mm, v(-77.39, -2.94) * mm, v(-76.8, -2.74) * mm]});
            skFitSpline(sketch, "E2386", {"points": [v(-76.8, -2.74) * mm, v(-76.59, -2.67) * mm, v(-76.39, -2.6) * mm, v(-76.13, -2.5) * mm]});
            skFitSpline(sketch, "E2387", {"points": [v(-76.13, -2.5) * mm, v(-76.3, -2.45) * mm, v(-76.41, -2.4) * mm, v(-76.53, -2.38) * mm]});
            skFitSpline(sketch, "E2388", {"points": [v(-76.53, -2.38) * mm, v(-76.82, -2.31) * mm, v(-76.98, -2.09) * mm, v(-76.94, -1.82) * mm]});
            skFitSpline(sketch, "E2389", {"points": [v(-76.94, -1.82) * mm, v(-76.9, -1.57) * mm, v(-76.65, -1.4) * mm, v(-76.37, -1.42) * mm]});
            skFitSpline(sketch, "E2390", {"points": [v(-76.37, -1.42) * mm, v(-76.32, -1.43) * mm, v(-76.28, -1.44) * mm, v(-76.23, -1.45) * mm]});
            skFitSpline(sketch, "E2391", {"points": [v(-76.23, -1.45) * mm, v(-75.87, -1.53) * mm, v(-75.51, -1.6) * mm, v(-75.16, -1.68) * mm]});
            skFitSpline(sketch, "E2392", {"points": [v(-75.16, -1.68) * mm, v(-75, -1.72) * mm, v(-74.86, -1.8) * mm, v(-74.71, -1.85) * mm]});
            skFitSpline(sketch, "E2393", {"points": [v(-74.71, -1.85) * mm, v(-74.65, -1.88) * mm, v(-74.57, -1.9) * mm, v(-74.52, -1.89) * mm]});
            skFitSpline(sketch, "E2394", {"points": [v(-74.52, -1.89) * mm, v(-74, -1.67) * mm, v(-73.5, -1.44) * mm, v(-73, -1.22) * mm]});
            skFitSpline(sketch, "E2395", {"points": [v(-73, -1.22) * mm, v(-73.7, -0.68) * mm, v(-74.4, -0.14) * mm, v(-75.11, 0.41) * mm]});
            skFitSpline(sketch, "E2396", {"points": [v(-75.11, 0.41) * mm, v(-75.14, 0.4) * mm, v(-75.19, 0.36) * mm, v(-75.23, 0.33) * mm]});
            skFitSpline(sketch, "E2397", {"points": [v(-75.23, 0.33) * mm, v(-75.74, -0.11) * mm, v(-76.25, -0.55) * mm, v(-76.75, -1) * mm]});
            skFitSpline(sketch, "E2398", {"points": [v(-76.75, -1) * mm, v(-77.16, -1.35) * mm, v(-77.56, -1.72) * mm, v(-77.96, -2.08) * mm]});
            skFitSpline(sketch, "E2399", {"points": [v(-77.96, -2.08) * mm, v(-78.06, -2.17) * mm, v(-78.17, -2.21) * mm, v(-78.3, -2.24) * mm]});
            skFitSpline(sketch, "E2400", {"points": [v(-78.3, -2.24) * mm, v(-78.61, -2.3) * mm, v(-78.87, -2.2) * mm, v(-79.13, -2.04) * mm]});
            skFitSpline(sketch, "E2401", {"points": [v(-79.13, -2.04) * mm, v(-80.14, -1.44) * mm, v(-81.14, -0.82) * mm, v(-82.08, -0.12) * mm]});
            skFitSpline(sketch, "E2402", {"points": [v(-82.08, -0.12) * mm, v(-82.27, 0.03) * mm, v(-82.47, 0.16) * mm, v(-82.67, 0.3) * mm]});
            skFitSpline(sketch, "E2403", {"points": [v(-82.67, 0.3) * mm, v(-83.04, 0.55) * mm, v(-83.19, 0.96) * mm, v(-83.06, 1.38) * mm]});
            skFitSpline(sketch, "E2404", {"points": [v(-83.06, 1.38) * mm, v(-83, 1.59) * mm, v(-82.85, 1.72) * mm, v(-82.69, 1.84) * mm]});
            skFitSpline(sketch, "E2405", {"points": [v(-82.69, 1.84) * mm, v(-82.23, 2.17) * mm, v(-81.77, 2.51) * mm, v(-81.3, 2.82) * mm]});
            skFitSpline(sketch, "E2406", {"points": [v(-81.3, 2.82) * mm, v(-80.5, 3.33) * mm, v(-79.7, 3.83) * mm, v(-78.9, 4.32) * mm]});
            skFitSpline(sketch, "E2407", {"points": [v(-78.9, 4.32) * mm, v(-78.63, 4.5) * mm, v(-78.16, 4.4) * mm, v(-77.92, 4.2) * mm]});
            skFitSpline(sketch, "E2408", {"points": [v(-77.92, 4.2) * mm, v(-77.32, 3.66) * mm, v(-76.71, 3.13) * mm, v(-76.1, 2.6) * mm]});
            skFitSpline(sketch, "E2409", {"points": [v(-76.1, 2.6) * mm, v(-75.78, 2.3) * mm, v(-75.45, 2.02) * mm, v(-75.12, 1.73) * mm]});
            skFitSpline(sketch, "E2410", {"points": [v(-75.12, 1.73) * mm, v(-74.4, 2.28) * mm, v(-73.7, 2.82) * mm, v(-72.99, 3.37) * mm]});
            skFitSpline(sketch, "E2411", {"points": [v(-72.99, 3.37) * mm, v(-73.27, 3.5) * mm, v(-73.56, 3.6) * mm, v(-73.84, 3.73) * mm]});
            skFitSpline(sketch, "E2412", {"points": [v(-73.84, 3.73) * mm, v(-74.05, 3.82) * mm, v(-74.25, 3.91) * mm, v(-74.45, 4.01) * mm]});
            skFitSpline(sketch, "E2413", {"points": [v(-74.45, 4.01) * mm, v(-74.55, 4.06) * mm, v(-74.64, 4.07) * mm, v(-74.74, 4) * mm]});
            skFitSpline(sketch, "E2414", {"points": [v(-74.74, 4) * mm, v(-74.95, 3.83) * mm, v(-75.21, 3.82) * mm, v(-75.46, 3.77) * mm]});
            skFitSpline(sketch, "E2415", {"points": [v(-75.46, 3.77) * mm, v(-75.66, 3.73) * mm, v(-75.87, 3.68) * mm, v(-76.07, 3.64) * mm]});
            skFitSpline(sketch, "E2416", {"points": [v(-76.07, 3.64) * mm, v(-76.19, 3.61) * mm, v(-76.3, 3.58) * mm, v(-76.42, 3.57) * mm]});
            skFitSpline(sketch, "E2417", {"points": [v(-76.42, 3.57) * mm, v(-76.69, 3.56) * mm, v(-76.9, 3.73) * mm, v(-76.94, 3.98) * mm]});
            skFitSpline(sketch, "E2418", {"points": [v(-76.94, 3.98) * mm, v(-76.98, 4.23) * mm, v(-76.82, 4.46) * mm, v(-76.55, 4.53) * mm]});
            skFitSpline(sketch, "E2419", {"points": [v(-76.55, 4.53) * mm, v(-76.43, 4.56) * mm, v(-76.3, 4.59) * mm, v(-76.18, 4.66) * mm]});
            skFitSpline(sketch, "E2420", {"points": [v(-76.18, 4.66) * mm, v(-76.33, 4.72) * mm, v(-76.47, 4.77) * mm, v(-76.61, 4.82) * mm]});
            skFitSpline(sketch, "E2421", {"points": [v(-76.61, 4.82) * mm, v(-77.25, 5.04) * mm, v(-77.9, 5.26) * mm, v(-78.54, 5.49) * mm]});
            skFitSpline(sketch, "E2422", {"points": [v(-78.54, 5.49) * mm, v(-78.67, 5.54) * mm, v(-78.78, 5.53) * mm, v(-78.9, 5.44) * mm]});
            skFitSpline(sketch, "E2423", {"points": [v(-78.9, 5.44) * mm, v(-79.02, 5.35) * mm, v(-79.16, 5.29) * mm, v(-79.3, 5.27) * mm]});
            skFitSpline(sketch, "E2424", {"points": [v(-79.3, 5.27) * mm, v(-79.98, 5.19) * mm, v(-80.64, 5) * mm, v(-81.3, 4.8) * mm]});
            skFitSpline(sketch, "E2425", {"points": [v(-81.3, 4.8) * mm, v(-81.38, 4.79) * mm, v(-81.46, 4.77) * mm, v(-81.54, 4.76) * mm]});
            skFitSpline(sketch, "E2426", {"points": [v(-81.54, 4.76) * mm, v(-81.77, 4.73) * mm, v(-81.98, 4.87) * mm, v(-82.05, 5.1) * mm]});
            skFitSpline(sketch, "E2427", {"points": [v(-82.05, 5.1) * mm, v(-82.11, 5.31) * mm, v(-82.02, 5.54) * mm, v(-81.82, 5.65) * mm]});
            skFitSpline(sketch, "E2428", {"points": [v(-81.82, 5.65) * mm, v(-81.75, 5.69) * mm, v(-81.67, 5.71) * mm, v(-81.6, 5.73) * mm]});
            skFitSpline(sketch, "E2429", {"points": [v(-81.6, 5.73) * mm, v(-81.19, 5.85) * mm, v(-80.78, 5.97) * mm, v(-80.37, 6.1) * mm]});
            skFitSpline(sketch, "E2430", {"points": [v(-80.37, 6.1) * mm, v(-80.65, 6.22) * mm, v(-80.92, 6.36) * mm, v(-81.25, 6.33) * mm]});
            skFitSpline(sketch, "E2431", {"points": [v(-81.25, 6.33) * mm, v(-81.82, 6.29) * mm, v(-82.38, 6.18) * mm, v(-82.95, 6.05) * mm]});
            skFitSpline(sketch, "E2432", {"points": [v(-82.95, 6.05) * mm, v(-83.26, 5.98) * mm, v(-83.57, 5.92) * mm, v(-83.88, 5.86) * mm]});
            skFitSpline(sketch, "E2433", {"points": [v(-83.88, 5.86) * mm, v(-84.15, 5.81) * mm, v(-84.37, 5.96) * mm, v(-84.45, 6.22) * mm]});
            skFitSpline(sketch, "E2434", {"points": [v(-84.45, 6.22) * mm, v(-84.51, 6.44) * mm, v(-84.4, 6.7) * mm, v(-84.15, 6.78) * mm]});
            skFitSpline(sketch, "E2435", {"points": [v(-84.15, 6.78) * mm, v(-83.91, 6.86) * mm, v(-83.66, 6.9) * mm, v(-83.4, 6.96) * mm]});
            skFitSpline(sketch, "E2436", {"points": [v(-83.4, 6.96) * mm, v(-83.13, 7.02) * mm, v(-82.85, 7.08) * mm, v(-82.56, 7.12) * mm]});
            skFitSpline(sketch, "E2437", {"points": [v(-82.56, 7.12) * mm, v(-82.19, 7.18) * mm, v(-81.8, 7.23) * mm, v(-81.43, 7.29) * mm]});
            skFitSpline(sketch, "E2438", {"points": [v(-81.43, 7.29) * mm, v(-81.35, 7.3) * mm, v(-81.27, 7.31) * mm, v(-81.17, 7.33) * mm]});
            skFitSpline(sketch, "E2439", {"points": [v(-81.17, 7.33) * mm, v(-81.2, 7.38) * mm, v(-81.23, 7.41) * mm, v(-81.26, 7.45) * mm]});
            skFitSpline(sketch, "E2440", {"points": [v(-81.26, 7.45) * mm, v(-81.55, 7.84) * mm, v(-81.84, 8.23) * mm, v(-82.12, 8.63) * mm]});
            skFitSpline(sketch, "E2441", {"points": [v(-82.12, 8.63) * mm, v(-82.33, 8.91) * mm, v(-82.52, 9.2) * mm, v(-82.71, 9.5) * mm]});
            skFitSpline(sketch, "E2442", {"points": [v(-82.71, 9.5) * mm, v(-82.78, 9.6) * mm, v(-82.85, 9.72) * mm, v(-82.9, 9.83) * mm]});
            skFitSpline(sketch, "E2443", {"points": [v(-82.9, 9.83) * mm, v(-83, 10.08) * mm, v(-82.9, 10.33) * mm, v(-82.67, 10.45) * mm]});
            skFitSpline(sketch, "E2444", {"points": [v(-82.67, 10.45) * mm, v(-82.46, 10.55) * mm, v(-82.2, 10.5) * mm, v(-82.05, 10.29) * mm]});
            skFitSpline(sketch, "E2445", {"points": [v(-82.05, 10.29) * mm, v(-82.02, 10.24) * mm, v(-82, 10.18) * mm, v(-81.96, 10.13) * mm]});
            skFitSpline(sketch, "E2446", {"points": [v(-81.96, 10.13) * mm, v(-81.58, 9.57) * mm, v(-81.2, 9.01) * mm, v(-80.82, 8.46) * mm]});
            skFitSpline(sketch, "E2447", {"points": [v(-80.82, 8.46) * mm, v(-80.74, 8.34) * mm, v(-80.63, 8.23) * mm, v(-80.54, 8.1) * mm]});
            skFitSpline(sketch, "E2448", {"points": [v(-80.54, 8.1) * mm, v(-80.34, 7.83) * mm, v(-80.03, 7.75) * mm, v(-79.73, 7.64) * mm]});
            skFitSpline(sketch, "E2449", {"points": [v(-79.73, 7.64) * mm, v(-79.76, 7.7) * mm, v(-79.8, 7.77) * mm, v(-79.83, 7.84) * mm]});
            skFitSpline(sketch, "E2450", {"points": [v(-79.83, 7.84) * mm, v(-80.01, 8.16) * mm, v(-80.2, 8.48) * mm, v(-80.37, 8.8) * mm]});
            skFitSpline(sketch, "E2451", {"points": [v(-80.37, 8.8) * mm, v(-80.4, 8.85) * mm, v(-80.42, 8.9) * mm, v(-80.44, 8.95) * mm]});
            skFitSpline(sketch, "E2452", {"points": [v(-80.44, 8.95) * mm, v(-80.5, 9.18) * mm, v(-80.41, 9.42) * mm, v(-80.21, 9.53) * mm]});
            skFitSpline(sketch, "E2453", {"points": [v(-80.21, 9.53) * mm, v(-80.01, 9.64) * mm, v(-79.75, 9.59) * mm, v(-79.6, 9.4) * mm]});
            skFitSpline(sketch, "E2454", {"points": [v(-79.6, 9.4) * mm, v(-79.54, 9.31) * mm, v(-79.48, 9.22) * mm, v(-79.43, 9.12) * mm]});
            skFitSpline(sketch, "E2455", {"points": [v(-79.43, 9.12) * mm, v(-79.13, 8.54) * mm, v(-78.8, 7.99) * mm, v(-78.4, 7.47) * mm]});
            skFitSpline(sketch, "E2456", {"points": [v(-78.4, 7.47) * mm, v(-78.3, 7.35) * mm, v(-78.26, 7.19) * mm, v(-78.23, 7.03) * mm]});
            skFitSpline(sketch, "E2457", {"points": [v(-78.23, 7.03) * mm, v(-78.2, 6.93) * mm, v(-78.16, 6.85) * mm, v(-78.06, 6.8) * mm]});
            skFitSpline(sketch, "E2458", {"points": [v(-78.06, 6.8) * mm, v(-77.51, 6.53) * mm, v(-76.97, 6.26) * mm, v(-76.43, 6) * mm]});
            skFitSpline(sketch, "E2459", {"points": [v(-76.43, 6) * mm, v(-76.21, 5.88) * mm, v(-76, 5.8) * mm, v(-75.75, 5.68) * mm]});
            skFitSpline(sketch, "E2460", {"points": [v(-75.75, 5.68) * mm, v(-75.76, 5.81) * mm, v(-75.84, 5.9) * mm, v(-75.88, 5.99) * mm]});
            skFitSpline(sketch, "E2461", {"points": [v(-75.88, 5.99) * mm, v(-75.93, 6.09) * mm, v(-75.98, 6.2) * mm, v(-76, 6.3) * mm]});
            skFitSpline(sketch, "E2462", {"points": [v(-76, 6.3) * mm, v(-76.02, 6.5) * mm, v(-75.92, 6.65) * mm, v(-75.74, 6.75) * mm]});
            skFitSpline(sketch, "E2463", {"points": [v(-75.74, 6.75) * mm, v(-75.56, 6.84) * mm, v(-75.38, 6.82) * mm, v(-75.22, 6.69) * mm]});
            skFitSpline(sketch, "E2464", {"points": [v(-75.22, 6.69) * mm, v(-75.14, 6.62) * mm, v(-75.07, 6.52) * mm, v(-75.01, 6.43) * mm]});
            skFitSpline(sketch, "E2465", {"points": [v(-75.01, 6.43) * mm, v(-74.83, 6.16) * mm, v(-74.65, 5.89) * mm, v(-74.48, 5.6) * mm]});
            skFitSpline(sketch, "E2466", {"points": [v(-74.48, 5.6) * mm, v(-74.39, 5.45) * mm, v(-74.32, 5.28) * mm, v(-74.26, 5.1) * mm]});
            skFitSpline(sketch, "E2467", {"points": [v(-74.26, 5.1) * mm, v(-74.24, 5.02) * mm, v(-74.2, 4.97) * mm, v(-74.12, 4.94) * mm]});
            skFitSpline(sketch, "E2468", {"points": [v(-74.12, 4.94) * mm, v(-73.61, 4.75) * mm, v(-73.1, 4.55) * mm, v(-72.6, 4.35) * mm]});
            skFitSpline(sketch, "E2469", {"points": [v(-72.6, 4.35) * mm, v(-72.7, 5.24) * mm, v(-72.82, 6.12) * mm, v(-72.93, 7) * mm]});
            skFitSpline(sketch, "E2470", {"points": [v(-72.93, 7) * mm, v(-73.34, 7.04) * mm, v(-73.75, 7.07) * mm, v(-74.15, 7.1) * mm]});
            skFitSpline(sketch, "E2471", {"points": [v(-74.15, 7.1) * mm, v(-74.73, 7.13) * mm, v(-75.32, 7.18) * mm, v(-75.9, 7.22) * mm]});
            skFitSpline(sketch, "E2472", {"points": [v(-75.9, 7.22) * mm, v(-76.16, 7.23) * mm, v(-76.42, 7.24) * mm, v(-76.68, 7.25) * mm]});
            skFitSpline(sketch, "E2473", {"points": [v(-76.68, 7.25) * mm, v(-76.83, 7.25) * mm, v(-76.95, 7.28) * mm, v(-77.06, 7.38) * mm]});
            skFitSpline(sketch, "E2474", {"points": [v(-77.06, 7.38) * mm, v(-77.1, 7.43) * mm, v(-77.15, 7.47) * mm, v(-77.2, 7.5) * mm]});
            skFitSpline(sketch, "E2475", {"points": [v(-77.2, 7.5) * mm, v(-77.33, 7.6) * mm, v(-77.4, 7.7) * mm, v(-77.44, 7.85) * mm]});
            skFitSpline(sketch, "E2476", {"points": [v(-77.44, 7.85) * mm, v(-77.77, 9.1) * mm, v(-78.07, 10.34) * mm, v(-78.24, 11.62) * mm]});
            skFitSpline(sketch, "E2477", {"points": [v(-78.24, 11.62) * mm, v(-78.27, 11.83) * mm, v(-78.31, 12.04) * mm, v(-78.35, 12.25) * mm]});
            skFitSpline(sketch, "E2478", {"points": [v(-78.35, 12.25) * mm, v(-78.42, 12.58) * mm, v(-78.36, 12.84) * mm, v(-78.11, 13.1) * mm]});
            skFitSpline(sketch, "E2479", {"points": [v(-78.11, 13.1) * mm, v(-77.86, 13.36) * mm, v(-77.59, 13.41) * mm, v(-77.27, 13.36) * mm]});
            skFitSpline(sketch, "E2480", {"points": [v(-77.27, 13.36) * mm, v(-76.69, 13.27) * mm, v(-76.1, 13.19) * mm, v(-75.52, 13.06) * mm]});
            skFitSpline(sketch, "E2481", {"points": [v(-75.52, 13.06) * mm, v(-74.62, 12.87) * mm, v(-73.72, 12.65) * mm, v(-72.82, 12.44) * mm]});
            skFitSpline(sketch, "E2482", {"points": [v(-72.82, 12.44) * mm, v(-72.78, 12.43) * mm, v(-72.74, 12.42) * mm, v(-72.7, 12.4) * mm]});
            skFitSpline(sketch, "E2483", {"points": [v(-72.7, 12.4) * mm, v(-72.48, 12.18) * mm, v(-72.23, 12) * mm, v(-72.24, 11.63) * mm]});
            skFitSpline(sketch, "E2484", {"points": [v(-72.24, 11.63) * mm, v(-72.26, 11.29) * mm, v(-72.23, 10.95) * mm, v(-72.17, 10.6) * mm]});
            skFitSpline(sketch, "E2485", {"points": [v(-72.17, 10.6) * mm, v(-72.13, 10.37) * mm, v(-72.16, 10.11) * mm, v(-72.14, 9.87) * mm]});
            skFitSpline(sketch, "E2486", {"points": [v(-72.14, 9.87) * mm, v(-72.1, 9.22) * mm, v(-72.05, 8.58) * mm, v(-72, 7.93) * mm]});
            skFitSpline(sketch, "E2487", {"points": [v(-72, 7.93) * mm, v(-71.12, 7.82) * mm, v(-70.23, 7.7) * mm, v(-69.34, 7.59) * mm]});
            skFitSpline(sketch, "E2488", {"points": [v(-69.34, 7.59) * mm, v(-69.4, 7.73) * mm, v(-69.46, 7.88) * mm, v(-69.51, 8.02) * mm]});
            skFitSpline(sketch, "E2489", {"points": [v(-69.51, 8.02) * mm, v(-69.65, 8.36) * mm, v(-69.78, 8.7) * mm, v(-69.9, 9.03) * mm]});
            skFitSpline(sketch, "E2490", {"points": [v(-69.9, 9.03) * mm, v(-69.95, 9.17) * mm, v(-70.02, 9.25) * mm, v(-70.18, 9.28) * mm]});
            skFitSpline(sketch, "E2491", {"points": [v(-70.18, 9.28) * mm, v(-70.33, 9.32) * mm, v(-70.47, 9.4) * mm, v(-70.6, 9.48) * mm]});
            skFitSpline(sketch, "E2492", {"points": [v(-70.6, 9.48) * mm, v(-70.88, 9.65) * mm, v(-71.16, 9.84) * mm, v(-71.43, 10.01) * mm]});
            skFitSpline(sketch, "E2493", {"points": [v(-71.43, 10.01) * mm, v(-71.5, 10.06) * mm, v(-71.58, 10.11) * mm, v(-71.64, 10.17) * mm]});
            skFitSpline(sketch, "E2494", {"points": [v(-71.64, 10.17) * mm, v(-71.83, 10.36) * mm, v(-71.85, 10.6) * mm, v(-71.7, 10.8) * mm]});
            skFitSpline(sketch, "E2495", {"points": [v(-71.7, 10.8) * mm, v(-71.56, 11) * mm, v(-71.3, 11.07) * mm, v(-71.07, 10.94) * mm]});
            skFitSpline(sketch, "E2496", {"points": [v(-71.07, 10.94) * mm, v(-70.96, 10.88) * mm, v(-70.85, 10.81) * mm, v(-70.72, 10.76) * mm]});
            skFitSpline(sketch, "E2497", {"points": [v(-70.72, 10.76) * mm, v(-71.05, 11.6) * mm, v(-71.43, 12.42) * mm, v(-71.88, 13.2) * mm]});
            skFitSpline(sketch, "E2498", {"points": [v(-71.88, 13.2) * mm, v(-72.16, 13.22) * mm, v(-72.4, 13.32) * mm, v(-72.62, 13.5) * mm]});
            skFitSpline(sketch, "E2499", {"points": [v(-72.62, 13.5) * mm, v(-73.03, 13.84) * mm, v(-73.5, 14.1) * mm, v(-73.98, 14.35) * mm]});
            skFitSpline(sketch, "E2500", {"points": [v(-73.98, 14.35) * mm, v(-74.1, 14.42) * mm, v(-74.23, 14.49) * mm, v(-74.35, 14.57) * mm]});
            skFitSpline(sketch, "E2501", {"points": [v(-74.35, 14.57) * mm, v(-74.59, 14.73) * mm, v(-74.65, 14.99) * mm, v(-74.52, 15.22) * mm]});
            skFitSpline(sketch, "E2502", {"points": [v(-74.52, 15.22) * mm, v(-74.4, 15.45) * mm, v(-74.12, 15.54) * mm, v(-73.86, 15.4) * mm]});
            skFitSpline(sketch, "E2503", {"points": [v(-73.86, 15.4) * mm, v(-73.52, 15.23) * mm, v(-73.19, 15.03) * mm, v(-72.85, 14.85) * mm]});
            skFitSpline(sketch, "E2504", {"points": [v(-72.85, 14.85) * mm, v(-72.79, 14.8) * mm, v(-72.72, 14.78) * mm, v(-72.64, 14.76) * mm]});
            skFitSpline(sketch, "E2505", {"points": [v(-72.64, 14.76) * mm, v(-72.72, 15.02) * mm, v(-72.8, 15.28) * mm, v(-73.02, 15.46) * mm]});
            skFitSpline(sketch, "E2506", {"points": [v(-73.02, 15.46) * mm, v(-73.34, 15.72) * mm, v(-73.67, 15.97) * mm, v(-74, 16.21) * mm]});
            skFitSpline(sketch, "E2507", {"points": [v(-74, 16.21) * mm, v(-74.41, 16.5) * mm, v(-74.83, 16.76) * mm, v(-75.25, 17.03) * mm]});
            skFitSpline(sketch, "E2508", {"points": [v(-75.25, 17.03) * mm, v(-75.5, 17.19) * mm, v(-75.57, 17.46) * mm, v(-75.44, 17.7) * mm]});
            skFitSpline(sketch, "E2509", {"points": [v(-75.44, 17.7) * mm, v(-75.3, 17.92) * mm, v(-75.04, 18) * mm, v(-74.79, 17.88) * mm]});
            skFitSpline(sketch, "E2510", {"points": [v(-74.79, 17.88) * mm, v(-74.62, 17.8) * mm, v(-74.46, 17.7) * mm, v(-74.3, 17.58) * mm]});
            skFitSpline(sketch, "E2511", {"points": [v(-74.3, 17.58) * mm, v(-73.8, 17.24) * mm, v(-73.29, 16.89) * mm, v(-72.78, 16.53) * mm]});
            skFitSpline(sketch, "E2512", {"points": [v(-72.78, 16.53) * mm, v(-72.63, 16.43) * mm, v(-72.5, 16.3) * mm, v(-72.33, 16.16) * mm]});
            skFitSpline(sketch, "E2513", {"points": [v(-72.33, 16.16) * mm, v(-72.3, 16.37) * mm, v(-72.28, 16.55) * mm, v(-72.26, 16.72) * mm]});
            skFitSpline(sketch, "E2514", {"points": [v(-72.26, 16.72) * mm, v(-72.2, 17.1) * mm, v(-72.13, 17.48) * mm, v(-72.06, 17.86) * mm]});
            skFitSpline(sketch, "E2515", {"points": [v(-72.06, 17.86) * mm, v(-72, 18.19) * mm, v(-71.94, 18.51) * mm, v(-71.87, 18.84) * mm]});
            skFitSpline(sketch, "E2516", {"points": [v(-71.87, 18.84) * mm, v(-71.85, 18.94) * mm, v(-71.83, 19.05) * mm, v(-71.8, 19.14) * mm]});
            skFitSpline(sketch, "E2517", {"points": [v(-71.8, 19.14) * mm, v(-71.7, 19.39) * mm, v(-71.45, 19.51) * mm, v(-71.21, 19.45) * mm]});
            skFitSpline(sketch, "E2518", {"points": [v(-71.21, 19.45) * mm, v(-70.96, 19.39) * mm, v(-70.81, 19.14) * mm, v(-70.86, 18.87) * mm]});
            skFitSpline(sketch, "E2519", {"points": [v(-70.86, 18.87) * mm, v(-70.88, 18.78) * mm, v(-70.91, 18.7) * mm, v(-70.93, 18.6) * mm]});
            skFitSpline(sketch, "E2520", {"points": [v(-70.93, 18.6) * mm, v(-71.05, 18.01) * mm, v(-71.16, 17.42) * mm, v(-71.27, 16.84) * mm]});
            skFitSpline(sketch, "E2521", {"points": [v(-71.27, 16.84) * mm, v(-71.3, 16.6) * mm, v(-71.33, 16.38) * mm, v(-71.34, 16.15) * mm]});
            skFitSpline(sketch, "E2522", {"points": [v(-71.34, 16.15) * mm, v(-71.35, 15.87) * mm, v(-71.23, 15.63) * mm, v(-71.1, 15.33) * mm]});
            skFitSpline(sketch, "E2523", {"points": [v(-71.1, 15.33) * mm, v(-71.06, 15.46) * mm, v(-71.03, 15.54) * mm, v(-71, 15.62) * mm]});
            skFitSpline(sketch, "E2524", {"points": [v(-71, 15.62) * mm, v(-70.9, 15.97) * mm, v(-70.81, 16.32) * mm, v(-70.71, 16.66) * mm]});
            skFitSpline(sketch, "E2525", {"points": [v(-70.71, 16.66) * mm, v(-70.66, 16.84) * mm, v(-70.57, 16.98) * mm, v(-70.39, 17.04) * mm]});
            skFitSpline(sketch, "E2526", {"points": [v(-70.39, 17.04) * mm, v(-70.05, 17.16) * mm, v(-69.72, 16.9) * mm, v(-69.75, 16.54) * mm]});
            skFitSpline(sketch, "E2527", {"points": [v(-69.75, 16.54) * mm, v(-69.77, 16.38) * mm, v(-69.82, 16.22) * mm, v(-69.87, 16.06) * mm]});
            skFitSpline(sketch, "E2528", {"points": [v(-69.87, 16.06) * mm, v(-70.04, 15.51) * mm, v(-70.19, 14.97) * mm, v(-70.24, 14.4) * mm]});
            skFitSpline(sketch, "E2529", {"points": [v(-70.24, 14.4) * mm, v(-70.26, 14.22) * mm, v(-70.32, 14.04) * mm, v(-70.44, 13.9) * mm]});
            skFitSpline(sketch, "E2530", {"points": [v(-70.44, 13.9) * mm, v(-70.53, 13.79) * mm, v(-70.53, 13.7) * mm, v(-70.49, 13.57) * mm]});
            skFitSpline(sketch, "E2531", {"points": [v(-70.49, 13.57) * mm, v(-70.26, 12.92) * mm, v(-70.04, 12.27) * mm, v(-69.82, 11.62) * mm]});
            skFitSpline(sketch, "E2532", {"points": [v(-69.82, 11.62) * mm, v(-69.77, 11.48) * mm, v(-69.72, 11.34) * mm, v(-69.62, 11.2) * mm]});
            skFitSpline(sketch, "E2533", {"points": [v(-69.62, 11.2) * mm, v(-69.59, 11.3) * mm, v(-69.55, 11.42) * mm, v(-69.52, 11.54) * mm]});
            skFitSpline(sketch, "E2534", {"points": [v(-69.52, 11.54) * mm, v(-69.45, 11.84) * mm, v(-69.23, 11.99) * mm, v(-68.94, 11.93) * mm]});
            skFitSpline(sketch, "E2535", {"points": [v(-68.94, 11.93) * mm, v(-68.69, 11.88) * mm, v(-68.53, 11.62) * mm, v(-68.58, 11.34) * mm]});
            skFitSpline(sketch, "E2536", {"points": [v(-68.58, 11.34) * mm, v(-68.59, 11.26) * mm, v(-68.6, 11.18) * mm, v(-68.63, 11.1) * mm]});
            skFitSpline(sketch, "E2537", {"points": [v(-68.63, 11.1) * mm, v(-68.68, 10.85) * mm, v(-68.74, 10.6) * mm, v(-68.79, 10.34) * mm]});
            skFitSpline(sketch, "E2538", {"points": [v(-68.79, 10.34) * mm, v(-68.83, 10.08) * mm, v(-68.9, 9.84) * mm, v(-69.07, 9.63) * mm]});
            skFitSpline(sketch, "E2539", {"points": [v(-69.07, 9.63) * mm, v(-68.84, 9.09) * mm, v(-68.6, 8.55) * mm, v(-68.37, 8) * mm]});
            skFitSpline(sketch, "E2540", {"points": [v(-68.37, 8) * mm, v(-67.82, 8.7) * mm, v(-67.28, 9.41) * mm, v(-66.73, 10.12) * mm]});
            skFitSpline(sketch, "E2541", {"points": [v(-66.73, 10.12) * mm, v(-67.03, 10.47) * mm, v(-67.35, 10.83) * mm, v(-67.65, 11.18) * mm]});
            skFitSpline(sketch, "E2542", {"points": [v(-67.65, 11.18) * mm, v(-68.02, 11.61) * mm, v(-68.4, 12.04) * mm, v(-68.76, 12.47) * mm]});
            skFitSpline(sketch, "E2543", {"points": [v(-68.76, 12.47) * mm, v(-68.9, 12.63) * mm, v(-69.06, 12.79) * mm, v(-69.2, 12.94) * mm]});
            skFitSpline(sketch, "E2544", {"points": [v(-69.2, 12.94) * mm, v(-69.32, 13.05) * mm, v(-69.35, 13.17) * mm, v(-69.38, 13.32) * mm]});
            skFitSpline(sketch, "E2545", {"points": [v(-69.38, 13.32) * mm, v(-69.45, 13.63) * mm, v(-69.35, 13.87) * mm, v(-69.2, 14.13) * mm]});
            skFitSpline(sketch, "E2546", {"points": [v(-69.2, 14.13) * mm, v(-68.6, 15.14) * mm, v(-67.97, 16.14) * mm, v(-67.27, 17.08) * mm]});
            skFitSpline(sketch, "E2547", {"points": [v(-67.27, 17.08) * mm, v(-67.12, 17.27) * mm, v(-67, 17.47) * mm, v(-66.85, 17.67) * mm]});
            skFitSpline(sketch, "E2548", {"points": [v(-66.85, 17.67) * mm, v(-66.66, 17.92) * mm, v(-66.45, 18.09) * mm, v(-66.08, 18.09) * mm]});
            skFitSpline(sketch, "E2549", {"points": [v(-66.08, 18.09) * mm, v(-65.72, 18.09) * mm, v(-65.5, 17.95) * mm, v(-65.31, 17.7) * mm]});
            skFitSpline(sketch, "E2550", {"points": [v(-65.31, 17.7) * mm, v(-64.98, 17.24) * mm, v(-64.65, 16.8) * mm, v(-64.34, 16.32) * mm]});
            skFitSpline(sketch, "E2551", {"points": [v(-64.34, 16.32) * mm, v(-63.83, 15.53) * mm, v(-63.33, 14.72) * mm, v(-62.83, 13.9) * mm]});
            skFitSpline(sketch, "E2552", {"points": [v(-62.83, 13.9) * mm, v(-62.65, 13.62) * mm, v(-62.74, 13.17) * mm, v(-62.97, 12.91) * mm]});
            skFitSpline(sketch, "E2553", {"points": [v(-62.97, 12.91) * mm, v(-63.5, 12.32) * mm, v(-64.01, 11.73) * mm, v(-64.53, 11.13) * mm]});
            skFitSpline(sketch, "E2554", {"points": [v(-64.53, 11.13) * mm, v(-64.83, 10.8) * mm, v(-65.12, 10.46) * mm, v(-65.42, 10.12) * mm]});
            skFitSpline(sketch, "E2555", {"points": [v(-65.42, 10.12) * mm, v(-64.87, 9.42) * mm, v(-64.33, 8.71) * mm, v(-63.77, 8) * mm]});
            skFitSpline(sketch, "E2556", {"points": [v(-63.77, 8) * mm, v(-63.68, 8.2) * mm, v(-63.6, 8.42) * mm, v(-63.5, 8.63) * mm]});
            skFitSpline(sketch, "E2557", {"points": [v(-63.5, 8.63) * mm, v(-63.39, 8.9) * mm, v(-63.26, 9.18) * mm, v(-63.13, 9.46) * mm]});
            skFitSpline(sketch, "E2558", {"points": [v(-63.13, 9.46) * mm, v(-63.09, 9.56) * mm, v(-63.08, 9.64) * mm, v(-63.15, 9.74) * mm]});
            skFitSpline(sketch, "E2559", {"points": [v(-63.15, 9.74) * mm, v(-63.3, 9.94) * mm, v(-63.32, 10.18) * mm, v(-63.37, 10.42) * mm]});
            skFitSpline(sketch, "E2560", {"points": [v(-63.37, 10.42) * mm, v(-63.41, 10.65) * mm, v(-63.47, 10.87) * mm, v(-63.52, 11.1) * mm]});
            skFitSpline(sketch, "E2561", {"points": [v(-63.52, 11.1) * mm, v(-63.54, 11.21) * mm, v(-63.57, 11.33) * mm, v(-63.57, 11.45) * mm]});
            skFitSpline(sketch, "E2562", {"points": [v(-63.57, 11.45) * mm, v(-63.58, 11.71) * mm, v(-63.4, 11.9) * mm, v(-63.17, 11.93) * mm]});
            skFitSpline(sketch, "E2563", {"points": [v(-63.17, 11.93) * mm, v(-62.9, 11.97) * mm, v(-62.7, 11.83) * mm, v(-62.62, 11.57) * mm]});
            skFitSpline(sketch, "E2564", {"points": [v(-62.62, 11.57) * mm, v(-62.59, 11.45) * mm, v(-62.56, 11.33) * mm, v(-62.52, 11.16) * mm]});
            skFitSpline(sketch, "E2565", {"points": [v(-62.52, 11.16) * mm, v(-62.47, 11.23) * mm, v(-62.45, 11.26) * mm, v(-62.44, 11.3) * mm]});
            skFitSpline(sketch, "E2566", {"points": [v(-62.44, 11.3) * mm, v(-62.18, 12.03) * mm, v(-61.93, 12.77) * mm, v(-61.67, 13.5) * mm]});
            skFitSpline(sketch, "E2567", {"points": [v(-61.67, 13.5) * mm, v(-61.62, 13.66) * mm, v(-61.6, 13.78) * mm, v(-61.72, 13.92) * mm]});
            skFitSpline(sketch, "E2568", {"points": [v(-61.72, 13.92) * mm, v(-61.8, 14.01) * mm, v(-61.86, 14.15) * mm, v(-61.87, 14.27) * mm]});
            skFitSpline(sketch, "E2569", {"points": [v(-61.87, 14.27) * mm, v(-61.96, 14.97) * mm, v(-62.14, 15.65) * mm, v(-62.35, 16.32) * mm]});
            skFitSpline(sketch, "E2570", {"points": [v(-62.35, 16.32) * mm, v(-62.36, 16.38) * mm, v(-62.38, 16.44) * mm, v(-62.39, 16.5) * mm]});
            skFitSpline(sketch, "E2571", {"points": [v(-62.39, 16.5) * mm, v(-62.43, 16.73) * mm, v(-62.3, 16.97) * mm, v(-62.08, 17.04) * mm]});
            skFitSpline(sketch, "E2572", {"points": [v(-62.08, 17.04) * mm, v(-61.86, 17.12) * mm, v(-61.62, 17.04) * mm, v(-61.5, 16.83) * mm]});
            skFitSpline(sketch, "E2573", {"points": [v(-61.5, 16.83) * mm, v(-61.46, 16.76) * mm, v(-61.43, 16.67) * mm, v(-61.41, 16.59) * mm]});
            skFitSpline(sketch, "E2574", {"points": [v(-61.41, 16.59) * mm, v(-61.3, 16.18) * mm, v(-61.18, 15.77) * mm, v(-61.04, 15.31) * mm]});
            skFitSpline(sketch, "E2575", {"points": [v(-61.04, 15.31) * mm, v(-60.92, 15.64) * mm, v(-60.8, 15.9) * mm, v(-60.81, 16.22) * mm]});
            skFitSpline(sketch, "E2576", {"points": [v(-60.81, 16.22) * mm, v(-60.85, 16.81) * mm, v(-60.97, 17.39) * mm, v(-61.1, 17.97) * mm]});
            skFitSpline(sketch, "E2577", {"points": [v(-61.1, 17.97) * mm, v(-61.18, 18.27) * mm, v(-61.23, 18.57) * mm, v(-61.29, 18.88) * mm]});
            skFitSpline(sketch, "E2578", {"points": [v(-61.29, 18.88) * mm, v(-61.34, 19.11) * mm, v(-61.2, 19.36) * mm, v(-60.98, 19.44) * mm]});
            skFitSpline(sketch, "E2579", {"points": [v(-60.98, 19.44) * mm, v(-60.75, 19.52) * mm, v(-60.48, 19.42) * mm, v(-60.37, 19.18) * mm]});
            skFitSpline(sketch, "E2580", {"points": [v(-60.37, 19.18) * mm, v(-60.32, 19.08) * mm, v(-60.3, 18.96) * mm, v(-60.27, 18.84) * mm]});
            skFitSpline(sketch, "E2581", {"points": [v(-60.27, 18.84) * mm, v(-60.16, 18.29) * mm, v(-60.05, 17.73) * mm, v(-59.95, 17.17) * mm]});
            skFitSpline(sketch, "E2582", {"points": [v(-59.95, 17.17) * mm, v(-59.9, 16.94) * mm, v(-59.9, 16.7) * mm, v(-59.86, 16.46) * mm]});
            skFitSpline(sketch, "E2583", {"points": [v(-59.86, 16.46) * mm, v(-59.85, 16.37) * mm, v(-59.84, 16.29) * mm, v(-59.82, 16.18) * mm]});
            skFitSpline(sketch, "E2584", {"points": [v(-59.82, 16.18) * mm, v(-59.76, 16.22) * mm, v(-59.72, 16.25) * mm, v(-59.67, 16.28) * mm]});
            skFitSpline(sketch, "E2585", {"points": [v(-59.67, 16.28) * mm, v(-59.26, 16.58) * mm, v(-58.85, 16.89) * mm, v(-58.44, 17.18) * mm]});
            skFitSpline(sketch, "E2586", {"points": [v(-58.44, 17.18) * mm, v(-58.18, 17.37) * mm, v(-57.92, 17.54) * mm, v(-57.66, 17.7) * mm]});
            skFitSpline(sketch, "E2587", {"points": [v(-57.66, 17.7) * mm, v(-57.56, 17.77) * mm, v(-57.46, 17.84) * mm, v(-57.35, 17.89) * mm]});
            skFitSpline(sketch, "E2588", {"points": [v(-57.35, 17.89) * mm, v(-57.1, 18) * mm, v(-56.83, 17.91) * mm, v(-56.7, 17.69) * mm]});
            skFitSpline(sketch, "E2589", {"points": [v(-56.7, 17.69) * mm, v(-56.58, 17.46) * mm, v(-56.65, 17.2) * mm, v(-56.88, 17.04) * mm]});
            skFitSpline(sketch, "E2590", {"points": [v(-56.88, 17.04) * mm, v(-57.3, 16.76) * mm, v(-57.72, 16.5) * mm, v(-58.12, 16.22) * mm]});
            skFitSpline(sketch, "E2591", {"points": [v(-58.12, 16.22) * mm, v(-58.42, 16.02) * mm, v(-58.7, 15.79) * mm, v(-59, 15.58) * mm]});
            skFitSpline(sketch, "E2592", {"points": [v(-59, 15.58) * mm, v(-59.28, 15.38) * mm, v(-59.4, 15.07) * mm, v(-59.55, 14.71) * mm]});
            skFitSpline(sketch, "E2593", {"points": [v(-59.55, 14.71) * mm, v(-59.46, 14.76) * mm, v(-59.4, 14.78) * mm, v(-59.36, 14.8) * mm]});
            skFitSpline(sketch, "E2594", {"points": [v(-59.36, 14.8) * mm, v(-59.02, 15) * mm, v(-58.69, 15.18) * mm, v(-58.35, 15.37) * mm]});
            skFitSpline(sketch, "E2595", {"points": [v(-58.35, 15.37) * mm, v(-58.3, 15.4) * mm, v(-58.24, 15.43) * mm, v(-58.18, 15.44) * mm]});
            skFitSpline(sketch, "E2596", {"points": [v(-58.18, 15.44) * mm, v(-57.96, 15.51) * mm, v(-57.74, 15.42) * mm, v(-57.62, 15.23) * mm]});
            skFitSpline(sketch, "E2597", {"points": [v(-57.62, 15.23) * mm, v(-57.52, 15.04) * mm, v(-57.55, 14.8) * mm, v(-57.7, 14.65) * mm]});
            skFitSpline(sketch, "E2598", {"points": [v(-57.7, 14.65) * mm, v(-57.77, 14.59) * mm, v(-57.85, 14.53) * mm, v(-57.93, 14.49) * mm]});
            skFitSpline(sketch, "E2599", {"points": [v(-57.93, 14.49) * mm, v(-58.55, 14.16) * mm, v(-59.15, 13.8) * mm, v(-59.7, 13.39) * mm]});
            skFitSpline(sketch, "E2600", {"points": [v(-59.7, 13.39) * mm, v(-59.85, 13.27) * mm, v(-60.06, 13.24) * mm, v(-60.3, 13.15) * mm]});
            skFitSpline(sketch, "E2601", {"points": [v(-60.3, 13.15) * mm, v(-60.72, 12.42) * mm, v(-61.09, 11.6) * mm, v(-61.42, 10.74) * mm]});
            skFitSpline(sketch, "E2602", {"points": [v(-61.42, 10.74) * mm, v(-61.31, 10.8) * mm, v(-61.2, 10.87) * mm, v(-61.09, 10.93) * mm]});
            skFitSpline(sketch, "E2603", {"points": [v(-61.09, 10.93) * mm, v(-60.81, 11.09) * mm, v(-60.5, 10.99) * mm, v(-60.39, 10.71) * mm]});
            skFitSpline(sketch, "E2604", {"points": [v(-60.39, 10.71) * mm, v(-60.3, 10.52) * mm, v(-60.35, 10.35) * mm, v(-60.48, 10.2) * mm]});
            skFitSpline(sketch, "E2605", {"points": [v(-60.48, 10.2) * mm, v(-60.55, 10.13) * mm, v(-60.64, 10.07) * mm, v(-60.72, 10) * mm]});
            skFitSpline(sketch, "E2606", {"points": [v(-60.72, 10) * mm, v(-61, 9.83) * mm, v(-61.26, 9.65) * mm, v(-61.53, 9.5) * mm]});
            skFitSpline(sketch, "E2607", {"points": [v(-61.53, 9.5) * mm, v(-61.69, 9.4) * mm, v(-61.86, 9.33) * mm, v(-62.03, 9.27) * mm]});
            skFitSpline(sketch, "E2608", {"points": [v(-62.03, 9.27) * mm, v(-62.1, 9.24) * mm, v(-62.17, 9.21) * mm, v(-62.2, 9.13) * mm]});
            skFitSpline(sketch, "E2609", {"points": [v(-62.2, 9.13) * mm, v(-62.4, 8.62) * mm, v(-62.6, 8.12) * mm, v(-62.8, 7.61) * mm]});
            skFitSpline(sketch, "E2610", {"points": [v(-62.8, 7.61) * mm, v(-62.8, 7.6) * mm, v(-62.79, 7.6) * mm, v(-62.79, 7.6) * mm]});
            skFitSpline(sketch, "E2611", {"points": [v(-62.79, 7.6) * mm, v(-61.9, 7.7) * mm, v(-61.03, 7.82) * mm, v(-60.13, 7.93) * mm]});
            skFitSpline(sketch, "E2612", {"points": [v(-60.13, 7.93) * mm, v(-60.12, 8.05) * mm, v(-60.12, 8.16) * mm, v(-60.11, 8.27) * mm]});
            skFitSpline(sketch, "E2613", {"points": [v(-60.11, 8.27) * mm, v(-60.06, 9.04) * mm, v(-60.02, 9.8) * mm, v(-59.97, 10.58) * mm]});
            skFitSpline(sketch, "E2614", {"points": [v(-59.97, 10.58) * mm, v(-59.95, 10.97) * mm, v(-59.93, 11.36) * mm, v(-59.9, 11.75) * mm]});
            skFitSpline(sketch, "E2615", {"points": [v(-59.9, 11.75) * mm, v(-59.9, 11.77) * mm, v(-59.9, 11.8) * mm, v(-59.89, 11.82) * mm]});
            skFitSpline(sketch, "E2616", {"points": [v(-59.89, 11.82) * mm, v(-59.75, 12.1) * mm, v(-59.6, 12.36) * mm, v(-59.26, 12.45) * mm]});
            skFitSpline(sketch, "E2617", {"points": [v(-59.26, 12.45) * mm, v(-58, 12.8) * mm, v(-56.72, 13.08) * mm, v(-55.42, 13.26) * mm]});
            skFitSpline(sketch, "E2618", {"points": [v(-55.42, 13.26) * mm, v(-55.14, 13.3) * mm, v(-54.87, 13.35) * mm, v(-54.6, 13.37) * mm]});
            skFitSpline(sketch, "E2619", {"points": [v(-54.6, 13.37) * mm, v(-54.39, 13.4) * mm, v(-54.22, 13.31) * mm, v(-54.1, 13.14) * mm]});
            skFitSpline(sketch, "E2620", {"points": [v(-54.1, 13.14) * mm, v(-54.08, 13.13) * mm, v(-54.07, 13.1) * mm, v(-54.05, 13.1) * mm]});
            skFitSpline(sketch, "E2621", {"points": [v(-54.05, 13.1) * mm, v(-53.74, 12.9) * mm, v(-53.74, 12.58) * mm, v(-53.78, 12.28) * mm]});
            skFitSpline(sketch, "E2622", {"points": [v(-53.78, 12.28) * mm, v(-53.88, 11.65) * mm, v(-53.98, 11.02) * mm, v(-54.11, 10.4) * mm]});
            skFitSpline(sketch, "E2623", {"points": [v(-54.11, 10.4) * mm, v(-54.3, 9.54) * mm, v(-54.5, 8.68) * mm, v(-54.71, 7.83) * mm]});
            skFitSpline(sketch, "E2624", {"points": [v(-54.71, 7.83) * mm, v(-54.74, 7.72) * mm, v(-54.84, 7.62) * mm, v(-54.92, 7.52) * mm]});
            skFitSpline(sketch, "E2625", {"points": [v(-54.92, 7.52) * mm, v(-54.97, 7.46) * mm, v(-55.04, 7.4) * mm, v(-55.1, 7.37) * mm]});
            skFitSpline(sketch, "E2626", {"points": [v(-55.1, 7.37) * mm, v(-55.2, 7.32) * mm, v(-55.3, 7.26) * mm, v(-55.41, 7.25) * mm]});
            skFitSpline(sketch, "E2627", {"points": [v(-55.41, 7.25) * mm, v(-55.97, 7.21) * mm, v(-56.52, 7.2) * mm, v(-57.08, 7.17) * mm]});
            skFitSpline(sketch, "E2628", {"points": [v(-57.08, 7.17) * mm, v(-57.52, 7.14) * mm, v(-57.95, 7.09) * mm, v(-58.4, 7.06) * mm]});
            skFitSpline(sketch, "E2629", {"points": [v(-58.4, 7.06) * mm, v(-58.66, 7.04) * mm, v(-58.93, 7.03) * mm, v(-59.21, 7.02) * mm]});
            skFitSpline(sketch, "E2630", {"points": [v(-59.21, 7.02) * mm, v(-59.33, 6.13) * mm, v(-59.44, 5.25) * mm, v(-59.56, 4.35) * mm]});
            skFitSpline(sketch, "E2631", {"points": [v(-59.56, 4.35) * mm, v(-59.52, 4.36) * mm, v(-59.47, 4.37) * mm, v(-59.42, 4.4) * mm]});
            skFitSpline(sketch, "E2632", {"points": [v(-59.42, 4.4) * mm, v(-58.98, 4.57) * mm, v(-58.53, 4.74) * mm, v(-58.08, 4.92) * mm]});
            skFitSpline(sketch, "E2633", {"points": [v(-58.08, 4.92) * mm, v(-57.97, 4.96) * mm, v(-57.9, 5) * mm, v(-57.88, 5.14) * mm]});
            skFitSpline(sketch, "E2634", {"points": [v(-57.88, 5.14) * mm, v(-57.84, 5.4) * mm, v(-57.68, 5.6) * mm, v(-57.54, 5.8) * mm]});
            skFitSpline(sketch, "E2635", {"points": [v(-57.54, 5.8) * mm, v(-57.41, 5.98) * mm, v(-57.3, 6.17) * mm, v(-57.17, 6.36) * mm]});
            skFitSpline(sketch, "E2636", {"points": [v(-57.17, 6.36) * mm, v(-57.12, 6.44) * mm, v(-57.07, 6.52) * mm, v(-57.01, 6.6) * mm]});
            skFitSpline(sketch, "E2637", {"points": [v(-57.01, 6.6) * mm, v(-56.82, 6.83) * mm, v(-56.55, 6.86) * mm, v(-56.33, 6.7) * mm]});
            skFitSpline(sketch, "E2638", {"points": [v(-56.33, 6.7) * mm, v(-56.12, 6.55) * mm, v(-56.08, 6.28) * mm, v(-56.23, 6.04) * mm]});
            skFitSpline(sketch, "E2639", {"points": [v(-56.23, 6.04) * mm, v(-56.29, 5.93) * mm, v(-56.35, 5.83) * mm, v(-56.4, 5.71) * mm]});
            skFitSpline(sketch, "E2640", {"points": [v(-56.4, 5.71) * mm, v(-55.56, 6.05) * mm, v(-54.74, 6.42) * mm, v(-53.94, 6.89) * mm]});
            skFitSpline(sketch, "E2641", {"points": [v(-53.94, 6.89) * mm, v(-53.94, 7.2) * mm, v(-53.77, 7.47) * mm, v(-53.58, 7.71) * mm]});
            skFitSpline(sketch, "E2642", {"points": [v(-53.58, 7.71) * mm, v(-53.25, 8.11) * mm, v(-53.02, 8.57) * mm, v(-52.77, 9.02) * mm]});
            skFitSpline(sketch, "E2643", {"points": [v(-52.77, 9.02) * mm, v(-52.71, 9.13) * mm, v(-52.65, 9.24) * mm, v(-52.58, 9.35) * mm]});
            skFitSpline(sketch, "E2644", {"points": [v(-52.58, 9.35) * mm, v(-52.42, 9.58) * mm, v(-52.15, 9.65) * mm, v(-51.93, 9.53) * mm]});
            skFitSpline(sketch, "E2645", {"points": [v(-51.93, 9.53) * mm, v(-51.7, 9.4) * mm, v(-51.6, 9.12) * mm, v(-51.74, 8.86) * mm]});
            skFitSpline(sketch, "E2646", {"points": [v(-51.74, 8.86) * mm, v(-51.92, 8.52) * mm, v(-52.11, 8.2) * mm, v(-52.3, 7.86) * mm]});
            skFitSpline(sketch, "E2647", {"points": [v(-52.3, 7.86) * mm, v(-52.34, 7.78) * mm, v(-52.38, 7.7) * mm, v(-52.4, 7.62) * mm]});
            skFitSpline(sketch, "E2648", {"points": [v(-52.4, 7.62) * mm, v(-52.11, 7.74) * mm, v(-51.8, 7.83) * mm, v(-51.6, 8.1) * mm]});
            skFitSpline(sketch, "E2649", {"points": [v(-51.6, 8.1) * mm, v(-51.37, 8.43) * mm, v(-51.12, 8.74) * mm, v(-50.9, 9.07) * mm]});
            skFitSpline(sketch, "E2650", {"points": [v(-50.9, 9.07) * mm, v(-50.63, 9.46) * mm, v(-50.38, 9.86) * mm, v(-50.12, 10.25) * mm]});
            skFitSpline(sketch, "E2651", {"points": [v(-50.12, 10.25) * mm, v(-49.97, 10.48) * mm, v(-49.7, 10.56) * mm, v(-49.47, 10.45) * mm]});
            skFitSpline(sketch, "E2652", {"points": [v(-49.47, 10.45) * mm, v(-49.23, 10.33) * mm, v(-49.14, 10.04) * mm, v(-49.26, 9.79) * mm]});
            skFitSpline(sketch, "E2653", {"points": [v(-49.26, 9.79) * mm, v(-49.34, 9.63) * mm, v(-49.45, 9.47) * mm, v(-49.55, 9.32) * mm]});
            skFitSpline(sketch, "E2654", {"points": [v(-49.55, 9.32) * mm, v(-49.9, 8.81) * mm, v(-50.25, 8.3) * mm, v(-50.6, 7.8) * mm]});
            skFitSpline(sketch, "E2655", {"points": [v(-50.6, 7.8) * mm, v(-50.71, 7.65) * mm, v(-50.84, 7.5) * mm, v(-50.98, 7.33) * mm]});
            skFitSpline(sketch, "E2656", {"points": [v(-50.98, 7.33) * mm, v(-50.88, 7.32) * mm, v(-50.8, 7.3) * mm, v(-50.72, 7.29) * mm]});
            skFitSpline(sketch, "E2657", {"points": [v(-50.72, 7.29) * mm, v(-50.21, 7.2) * mm, v(-49.7, 7.13) * mm, v(-49.2, 7.05) * mm]});
            skFitSpline(sketch, "E2658", {"points": [v(-49.2, 7.05) * mm, v(-48.92, 7) * mm, v(-48.64, 6.94) * mm, v(-48.36, 6.88) * mm]});
            skFitSpline(sketch, "E2659", {"points": [v(-48.36, 6.88) * mm, v(-48.24, 6.86) * mm, v(-48.12, 6.84) * mm, v(-48.01, 6.8) * mm]});
            skFitSpline(sketch, "E2660", {"points": [v(-48.01, 6.8) * mm, v(-47.75, 6.7) * mm, v(-47.62, 6.44) * mm, v(-47.7, 6.2) * mm]});
            skFitSpline(sketch, "E2661", {"points": [v(-47.7, 6.2) * mm, v(-47.78, 5.95) * mm, v(-48.02, 5.81) * mm, v(-48.29, 5.87) * mm]});
            skFitSpline(sketch, "E2662", {"points": [v(-48.29, 5.87) * mm, v(-48.83, 5.98) * mm, v(-49.36, 6.1) * mm, v(-49.9, 6.2) * mm]});
            skFitSpline(sketch, "E2663", {"points": [v(-49.9, 6.2) * mm, v(-50.27, 6.27) * mm, v(-50.65, 6.32) * mm, v(-51.02, 6.34) * mm]});
            skFitSpline(sketch, "E2664", {"points": [v(-51.02, 6.34) * mm, v(-51.29, 6.36) * mm, v(-51.54, 6.23) * mm, v(-51.83, 6.1) * mm]});
            skFitSpline(sketch, "E2665", {"points": [v(-51.83, 6.1) * mm, v(-51.37, 5.97) * mm, v(-50.96, 5.85) * mm, v(-50.56, 5.74) * mm]});
            skFitSpline(sketch, "E2666", {"points": [v(-50.56, 5.74) * mm, v(-50.49, 5.72) * mm, v(-50.42, 5.7) * mm, v(-50.35, 5.67) * mm]});
            skFitSpline(sketch, "E2667", {"points": [v(-50.35, 5.67) * mm, v(-50.13, 5.56) * mm, v(-50.02, 5.31) * mm, v(-50.1, 5.08) * mm]});
            skFitSpline(sketch, "E2668", {"points": [v(-50.1, 5.08) * mm, v(-50.17, 4.87) * mm, v(-50.38, 4.72) * mm, v(-50.62, 4.76) * mm]});
            skFitSpline(sketch, "E2669", {"points": [v(-50.62, 4.76) * mm, v(-50.79, 4.79) * mm, v(-50.95, 4.83) * mm, v(-51.1, 4.88) * mm]});
            skFitSpline(sketch, "E2670", {"points": [v(-51.1, 4.88) * mm, v(-51.61, 5.04) * mm, v(-52.12, 5.18) * mm, v(-52.65, 5.23) * mm]});
            skFitSpline(sketch, "E2671", {"points": [v(-52.65, 5.23) * mm, v(-52.93, 5.26) * mm, v(-53.17, 5.35) * mm, v(-53.39, 5.54) * mm]});
            skFitSpline(sketch, "E2672", {"points": [v(-53.39, 5.54) * mm, v(-54.27, 5.32) * mm, v(-55.12, 4.98) * mm, v(-56.02, 4.64) * mm]});
            skFitSpline(sketch, "E2673", {"points": [v(-56.02, 4.64) * mm, v(-55.85, 4.6) * mm, v(-55.74, 4.56) * mm, v(-55.62, 4.53) * mm]});
            skFitSpline(sketch, "E2674", {"points": [v(-55.62, 4.53) * mm, v(-55.32, 4.46) * mm, v(-55.17, 4.25) * mm, v(-55.21, 3.96) * mm]});
            skFitSpline(sketch, "E2675", {"points": [v(-55.21, 3.96) * mm, v(-55.25, 3.7) * mm, v(-55.5, 3.54) * mm, v(-55.79, 3.57) * mm]});
            skFitSpline(sketch, "E2676", {"points": [v(-55.79, 3.57) * mm, v(-55.82, 3.58) * mm, v(-55.85, 3.58) * mm, v(-55.88, 3.6) * mm]});
            skFitSpline(sketch, "E2677", {"points": [v(-55.88, 3.6) * mm, v(-56.26, 3.67) * mm, v(-56.65, 3.75) * mm, v(-57.03, 3.84) * mm]});
            skFitSpline(sketch, "E2678", {"points": [v(-57.03, 3.84) * mm, v(-57.17, 3.87) * mm, v(-57.3, 3.94) * mm, v(-57.42, 4) * mm]});
            skFitSpline(sketch, "E2679", {"points": [v(-57.42, 4) * mm, v(-57.5, 4.05) * mm, v(-57.56, 4.07) * mm, v(-57.64, 4.03) * mm]});
            skFitSpline(sketch, "E2680", {"points": [v(-57.64, 4.03) * mm, v(-58.15, 3.8) * mm, v(-58.65, 3.59) * mm, v(-59.14, 3.37) * mm]});
            skFitSpline(sketch, "E2681", {"points": [v(-59.14, 3.37) * mm, v(-58.45, 2.83) * mm, v(-57.75, 2.29) * mm, v(-57.03, 1.74) * mm]});
            skFitSpline(sketch, "E2682", {"points": [v(-57.03, 1.74) * mm, v(-57, 1.76) * mm, v(-56.94, 1.8) * mm, v(-56.9, 1.84) * mm]});
            skFitSpline(sketch, "E2683", {"points": [v(-56.9, 1.84) * mm, v(-56.28, 2.39) * mm, v(-55.66, 2.94) * mm, v(-55.03, 3.49) * mm]});
            skFitSpline(sketch, "E2684", {"points": [v(-55.03, 3.49) * mm, v(-54.74, 3.75) * mm, v(-54.45, 4) * mm, v(-54.15, 4.26) * mm]});
            skFitSpline(sketch, "E2685", {"points": [v(-54.15, 4.26) * mm, v(-54.12, 4.3) * mm, v(-54.08, 4.33) * mm, v(-54.03, 4.34) * mm]});
            skFitSpline(sketch, "E2686", {"points": [v(-54.03, 4.34) * mm, v(-53.74, 4.4) * mm, v(-53.46, 4.46) * mm, v(-53.18, 4.29) * mm]});
            skFitSpline(sketch, "E2687", {"points": [v(-53.18, 4.29) * mm, v(-52, 3.6) * mm, v(-50.86, 2.87) * mm, v(-49.77, 2.06) * mm]});
            skFitSpline(sketch, "E2688", {"points": [v(-49.77, 2.06) * mm, v(-49.58, 1.92) * mm, v(-49.4, 1.77) * mm, v(-49.23, 1.63) * mm]});
            skFitSpline(sketch, "E2689", {"points": [v(-49.23, 1.63) * mm, v(-49.1, 1.52) * mm, v(-49.06, 1.38) * mm, v(-49.07, 1.22) * mm]});
            skFitSpline(sketch, "E2690", {"points": [v(-49.07, 1.22) * mm, v(-49.07, 1.16) * mm, v(-49.08, 1.1) * mm, v(-49.07, 1.05) * mm]});
            skFitSpline(sketch, "E2691", {"points": [v(-49.07, 1.05) * mm, v(-49, 0.7) * mm, v(-49.21, 0.49) * mm, v(-49.46, 0.31) * mm]});
            skFitSpline(sketch, "E2692", {"points": [v(-49.46, 0.31) * mm, v(-49.92, -0.03) * mm, v(-50.37, -0.36) * mm, v(-50.85, -0.67) * mm]});
            skFitSpline(sketch, "E2693", {"points": [v(-50.85, -0.67) * mm, v(-51.64, -1.19) * mm, v(-52.44, -1.68) * mm, v(-53.24, -2.17) * mm]});
            skFitSpline(sketch, "E2694", {"points": [v(-53.24, -2.17) * mm, v(-53.53, -2.35) * mm, v(-53.98, -2.26) * mm, v(-54.24, -2.03) * mm]});
            skFitSpline(sketch, "E2695", {"points": [v(-54.24, -2.03) * mm, v(-54.61, -1.68) * mm, v(-55, -1.34) * mm, v(-55.38, -1) * mm]});
            skFitSpline(sketch, "E2696", {"points": [v(-55.38, -1) * mm, v(-55.89, -0.56) * mm, v(-56.4, -0.11) * mm, v(-56.92, 0.33) * mm]});
            skFitSpline(sketch, "E2697", {"points": [v(-56.92, 0.33) * mm, v(-56.95, 0.36) * mm, v(-57, 0.39) * mm, v(-57.03, 0.42) * mm]});
            skFitSpline(sketch, "E2698", {"points": [v(-57.03, 0.42) * mm, v(-57.73, -0.13) * mm, v(-58.43, -0.67) * mm, v(-59.15, -1.22) * mm]});
            skFitSpline(sketch, "E2699", {"points": [v(-59.15, -1.22) * mm, v(-59.1, -1.24) * mm, v(-59.04, -1.28) * mm, v(-58.98, -1.3) * mm]});
            skFitSpline(sketch, "E2700", {"points": [v(-58.98, -1.3) * mm, v(-58.56, -1.48) * mm, v(-58.14, -1.66) * mm, v(-57.72, -1.85) * mm]});
            skFitSpline(sketch, "E2701", {"points": [v(-57.72, -1.85) * mm, v(-57.6, -1.9) * mm, v(-57.5, -1.92) * mm, v(-57.37, -1.83) * mm]});
            skFitSpline(sketch, "E2702", {"points": [v(-57.37, -1.83) * mm, v(-57.17, -1.68) * mm, v(-56.91, -1.67) * mm, v(-56.67, -1.62) * mm]});
            skFitSpline(sketch, "E2703", {"points": [v(-56.67, -1.62) * mm, v(-56.47, -1.58) * mm, v(-56.28, -1.53) * mm, v(-56.08, -1.5) * mm]});
            skFitSpline(sketch, "E2704", {"points": [v(-56.08, -1.5) * mm, v(-55.97, -1.47) * mm, v(-55.85, -1.43) * mm, v(-55.73, -1.42) * mm]});
            skFitSpline(sketch, "E2705", {"points": [v(-55.73, -1.42) * mm, v(-55.47, -1.4) * mm, v(-55.24, -1.58) * mm, v(-55.21, -1.82) * mm]});
            skFitSpline(sketch, "E2706", {"points": [v(-55.21, -1.82) * mm, v(-55.18, -2.1) * mm, v(-55.32, -2.3) * mm, v(-55.58, -2.38) * mm]});
            skFitSpline(sketch, "E2707", {"points": [v(-55.58, -2.38) * mm, v(-55.7, -2.4) * mm, v(-55.83, -2.44) * mm, v(-56, -2.48) * mm]});
            skFitSpline(sketch, "E2708", {"points": [v(-56, -2.48) * mm, v(-55.93, -2.52) * mm, v(-55.9, -2.54) * mm, v(-55.88, -2.55) * mm]});
            skFitSpline(sketch, "E2709", {"points": [v(-55.88, -2.55) * mm, v(-55.12, -2.81) * mm, v(-54.35, -3.08) * mm, v(-53.6, -3.34) * mm]});
            skFitSpline(sketch, "E2710", {"points": [v(-53.6, -3.34) * mm, v(-53.46, -3.39) * mm, v(-53.36, -3.38) * mm, v(-53.24, -3.29) * mm]});
            skFitSpline(sketch, "E2711", {"points": [v(-53.24, -3.29) * mm, v(-53.1, -3.17) * mm, v(-52.94, -3.12) * mm, v(-52.76, -3.1) * mm]});
            skFitSpline(sketch, "E2712", {"points": [v(-52.76, -3.1) * mm, v(-52.2, -3.04) * mm, v(-51.67, -2.9) * mm, v(-51.15, -2.74) * mm]});
            skFitSpline(sketch, "E2713", {"points": [v(-51.15, -2.74) * mm, v(-51, -2.7) * mm, v(-50.84, -2.65) * mm, v(-50.69, -2.62) * mm]});
            skFitSpline(sketch, "E2714", {"points": [v(-50.69, -2.62) * mm, v(-50.4, -2.56) * mm, v(-50.15, -2.71) * mm, v(-50.09, -2.97) * mm]});
            skFitSpline(sketch, "E2715", {"points": [v(-50.09, -2.97) * mm, v(-50.03, -3.23) * mm, v(-50.17, -3.47) * mm, v(-50.45, -3.56) * mm]});
            skFitSpline(sketch, "E2716", {"points": [v(-50.45, -3.56) * mm, v(-50.89, -3.69) * mm, v(-51.33, -3.8) * mm, v(-51.8, -3.94) * mm]});
            skFitSpline(sketch, "E2717", {"points": [v(-51.8, -3.94) * mm, v(-51.73, -3.98) * mm, v(-51.7, -4.01) * mm, v(-51.65, -4.03) * mm]});
            skFitSpline(sketch, "E2718", {"points": [v(-51.65, -4.03) * mm, v(-51.32, -4.17) * mm, v(-50.99, -4.23) * mm, v(-50.63, -4.16) * mm]});
            skFitSpline(sketch, "E2719", {"points": [v(-50.63, -4.16) * mm, v(-50.19, -4.07) * mm, v(-49.75, -4) * mm, v(-49.3, -3.92) * mm]});
            skFitSpline(sketch, "E2720", {"points": [v(-49.3, -3.92) * mm, v(-48.96, -3.86) * mm, v(-48.62, -3.78) * mm, v(-48.28, -3.72) * mm]});
            skFitSpline(sketch, "E2721", {"points": [v(-48.28, -3.72) * mm, v(-48, -3.66) * mm, v(-47.77, -3.8) * mm, v(-47.7, -4.06) * mm]});
            skFitSpline(sketch, "E2722", {"points": [v(-47.7, -4.06) * mm, v(-47.63, -4.3) * mm, v(-47.76, -4.56) * mm, v(-48.02, -4.65) * mm]});
            skFitSpline(sketch, "E2723", {"points": [v(-48.02, -4.65) * mm, v(-48.25, -4.72) * mm, v(-48.49, -4.76) * mm, v(-48.72, -4.81) * mm]});
            skFitSpline(sketch, "E2724", {"points": [v(-48.72, -4.81) * mm, v(-48.97, -4.87) * mm, v(-49.22, -4.92) * mm, v(-49.47, -4.96) * mm]});
            skFitSpline(sketch, "E2725", {"points": [v(-49.47, -4.96) * mm, v(-49.96, -5.04) * mm, v(-50.45, -5.11) * mm, v(-50.95, -5.2) * mm]});
            skFitSpline(sketch, "E2726", {"points": [v(-50.95, -5.2) * mm, v(-50.93, -5.23) * mm, v(-50.9, -5.27) * mm, v(-50.88, -5.31) * mm]});
            skFitSpline(sketch, "E2727", {"points": [v(-50.88, -5.31) * mm, v(-50.5, -5.76) * mm, v(-50.16, -6.25) * mm, v(-49.84, -6.75) * mm]});
            skFitSpline(sketch, "E2728", {"points": [v(-49.84, -6.75) * mm, v(-49.71, -6.96) * mm, v(-49.56, -7.16) * mm, v(-49.42, -7.36) * mm]});
            skFitSpline(sketch, "E2729", {"points": [v(-49.42, -7.36) * mm, v(-49.36, -7.46) * mm, v(-49.3, -7.56) * mm, v(-49.25, -7.67) * mm]});
            skFitSpline(sketch, "E2730", {"points": [v(-49.25, -7.67) * mm, v(-49.15, -7.92) * mm, v(-49.25, -8.18) * mm, v(-49.46, -8.3) * mm]});
            skFitSpline(sketch, "E2731", {"points": [v(-49.46, -8.3) * mm, v(-49.68, -8.4) * mm, v(-49.95, -8.34) * mm, v(-50.1, -8.13) * mm]});
            skFitSpline(sketch, "E2732", {"points": [v(-50.1, -8.13) * mm, v(-50.3, -7.82) * mm, v(-50.5, -7.51) * mm, v(-50.7, -7.2) * mm]});
            skFitSpline(sketch, "E2733", {"points": [v(-50.7, -7.2) * mm, v(-50.98, -6.8) * mm, v(-51.27, -6.42) * mm, v(-51.55, -6.02) * mm]});
            skFitSpline(sketch, "E2734", {"points": [v(-51.55, -6.02) * mm, v(-51.76, -5.72) * mm, v(-52.08, -5.6) * mm, v(-52.44, -5.45) * mm]});
            skFitSpline(sketch, "E2735", {"points": [v(-52.44, -5.45) * mm, v(-52.4, -5.53) * mm, v(-52.37, -5.59) * mm, v(-52.34, -5.64) * mm]});
            skFitSpline(sketch, "E2736", {"points": [v(-52.34, -5.64) * mm, v(-52.15, -5.97) * mm, v(-51.96, -6.3) * mm, v(-51.78, -6.64) * mm]});
            skFitSpline(sketch, "E2737", {"points": [v(-51.78, -6.64) * mm, v(-51.73, -6.75) * mm, v(-51.68, -6.89) * mm, v(-51.69, -7) * mm]});
            skFitSpline(sketch, "E2738", {"points": [v(-51.69, -7) * mm, v(-51.7, -7.2) * mm, v(-51.8, -7.34) * mm, v(-51.99, -7.4) * mm]});
            skFitSpline(sketch, "E2739", {"points": [v(-51.99, -7.4) * mm, v(-52.17, -7.47) * mm, v(-52.35, -7.44) * mm, v(-52.5, -7.3) * mm]});
            skFitSpline(sketch, "E2740", {"points": [v(-52.5, -7.3) * mm, v(-52.56, -7.23) * mm, v(-52.62, -7.15) * mm, v(-52.66, -7.06) * mm]});
            skFitSpline(sketch, "E2741", {"points": [v(-52.66, -7.06) * mm, v(-53, -6.45) * mm, v(-53.34, -5.85) * mm, v(-53.76, -5.3) * mm]});
            skFitSpline(sketch, "E2742", {"points": [v(-53.76, -5.3) * mm, v(-53.87, -5.15) * mm, v(-53.9, -4.95) * mm, v(-54, -4.71) * mm]});
            skFitSpline(sketch, "E2743", {"points": [v(-54, -4.71) * mm, v(-54.71, -4.28) * mm, v(-55.55, -3.92) * mm, v(-56.4, -3.57) * mm]});
            skFitSpline(sketch, "E2744", {"points": [v(-56.4, -3.57) * mm, v(-56.35, -3.68) * mm, v(-56.28, -3.79) * mm, v(-56.22, -3.9) * mm]});
            skFitSpline(sketch, "E2745", {"points": [v(-56.22, -3.9) * mm, v(-56.06, -4.18) * mm, v(-56.16, -4.5) * mm, v(-56.45, -4.62) * mm]});
            skFitSpline(sketch, "E2746", {"points": [v(-56.45, -4.62) * mm, v(-56.63, -4.69) * mm, v(-56.8, -4.65) * mm, v(-56.94, -4.52) * mm]});
            skFitSpline(sketch, "E2747", {"points": [v(-56.94, -4.52) * mm, v(-57.02, -4.45) * mm, v(-57.08, -4.35) * mm, v(-57.14, -4.26) * mm]});
            skFitSpline(sketch, "E2748", {"points": [v(-57.14, -4.26) * mm, v(-57.31, -4) * mm, v(-57.48, -3.76) * mm, v(-57.64, -3.5) * mm]});
            skFitSpline(sketch, "E2749", {"points": [v(-57.64, -3.5) * mm, v(-57.74, -3.32) * mm, v(-57.82, -3.14) * mm, v(-57.89, -2.96) * mm]});
            skFitSpline(sketch, "E2750", {"points": [v(-57.89, -2.96) * mm, v(-57.92, -2.87) * mm, v(-57.95, -2.82) * mm, v(-58.03, -2.79) * mm]});
            skFitSpline(sketch, "E2751", {"points": [v(-58.03, -2.79) * mm, v(-58.54, -2.6) * mm, v(-59.04, -2.4) * mm, v(-59.56, -2.2) * mm]});
            skFitSpline(sketch, "E2752", {"points": [v(-59.56, -2.2) * mm, v(-59.44, -3.08) * mm, v(-59.33, -3.97) * mm, v(-59.21, -4.86) * mm]});
            skFitSpline(sketch, "E2753", {"points": [v(-59.21, -4.86) * mm, v(-58.8, -4.9) * mm, v(-58.37, -4.92) * mm, v(-57.95, -4.95) * mm]});
            skFitSpline(sketch, "E2754", {"points": [v(-57.95, -4.95) * mm, v(-57.35, -5) * mm, v(-56.74, -5.04) * mm, v(-56.14, -5.08) * mm]});
            skFitSpline(sketch, "E2755", {"points": [v(-56.14, -5.08) * mm, v(-55.92, -5.1) * mm, v(-55.7, -5.1) * mm, v(-55.5, -5.1) * mm]});
            skFitSpline(sketch, "E2756", {"points": [v(-55.5, -5.1) * mm, v(-55.32, -5.1) * mm, v(-55.2, -5.16) * mm, v(-55.06, -5.26) * mm]});
            skFitSpline(sketch, "E2757", {"points": [v(-55.06, -5.26) * mm, v(-54.81, -5.42) * mm, v(-54.71, -5.65) * mm, v(-54.64, -5.92) * mm]});
            skFitSpline(sketch, "E2758", {"points": [v(-54.64, -5.92) * mm, v(-54.33, -7.13) * mm, v(-54.06, -8.34) * mm, v(-53.88, -9.58) * mm]});
            skFitSpline(sketch, "E2759", {"points": [v(-53.88, -9.58) * mm, v(-53.84, -9.86) * mm, v(-53.8, -10.14) * mm, v(-53.77, -10.43) * mm]});
            skFitSpline(sketch, "E2760", {"points": [v(-53.77, -10.43) * mm, v(-53.76, -10.62) * mm, v(-53.84, -10.77) * mm, v(-53.98, -10.89) * mm]});
            skFitSpline(sketch, "E2761", {"points": [v(-53.98, -10.89) * mm, v(-54.01, -10.91) * mm, v(-54.05, -10.94) * mm, v(-54.07, -10.97) * mm]});
            skFitSpline(sketch, "E2762", {"points": [v(-54.07, -10.97) * mm, v(-54.26, -11.24) * mm, v(-54.54, -11.27) * mm, v(-54.82, -11.22) * mm]});
            skFitSpline(sketch, "E2763", {"points": [v(-54.82, -11.22) * mm, v(-55.61, -11.09) * mm, v(-56.41, -10.96) * mm, v(-57.2, -10.8) * mm]});
            skFitSpline(sketch, "E2764", {"points": [v(-57.2, -10.8) * mm, v(-57.9, -10.65) * mm, v(-58.6, -10.46) * mm, v(-59.3, -10.3) * mm]});
            skFitSpline(sketch, "E2765", {"points": [v(-59.3, -10.3) * mm, v(-59.44, -10.26) * mm, v(-59.56, -10.18) * mm, v(-59.64, -10.06) * mm]});
            skFitSpline(sketch, "E2766", {"points": [v(-59.64, -10.06) * mm, v(-59.68, -10) * mm, v(-59.72, -9.96) * mm, v(-59.76, -9.91) * mm]});
            skFitSpline(sketch, "E2767", {"points": [v(-59.76, -9.91) * mm, v(-59.86, -9.8) * mm, v(-59.9, -9.67) * mm, v(-59.9, -9.52) * mm]});
            skFitSpline(sketch, "E2768", {"points": [v(-59.9, -9.52) * mm, v(-59.92, -9.2) * mm, v(-59.94, -8.88) * mm, v(-59.96, -8.56) * mm]});
            skFitSpline(sketch, "E2769", {"points": [v(-59.96, -8.56) * mm, v(-59.97, -8.52) * mm, v(-59.97, -8.48) * mm, v(-59.97, -8.44) * mm]});
            skFitSpline(sketch, "E2770", {"points": [v(-59.97, -8.44) * mm, v(-60, -8.02) * mm, v(-60.03, -7.6) * mm, v(-60.05, -7.18) * mm]});
            skFitSpline(sketch, "E2771", {"points": [v(-60.05, -7.18) * mm, v(-60.08, -6.75) * mm, v(-60.1, -6.32) * mm, v(-60.12, -5.89) * mm]});
            skFitSpline(sketch, "E2772", {"points": [v(-60.12, -5.89) * mm, v(-60.12, -5.86) * mm, v(-60.13, -5.83) * mm, v(-60.13, -5.79) * mm]});
            skFitSpline(sketch, "E2773", {"points": [v(-60.13, -5.79) * mm, v(-61.02, -5.67) * mm, v(-61.9, -5.56) * mm, v(-62.8, -5.44) * mm]});
            skFitSpline(sketch, "E2774", {"points": [v(-62.8, -5.44) * mm, v(-62.78, -5.5) * mm, v(-62.77, -5.54) * mm, v(-62.75, -5.59) * mm]});
            skFitSpline(sketch, "E2775", {"points": [v(-62.75, -5.59) * mm, v(-62.58, -6.03) * mm, v(-62.4, -6.47) * mm, v(-62.23, -6.9) * mm]});
            skFitSpline(sketch, "E2776", {"points": [v(-62.23, -6.9) * mm, v(-62.19, -7.03) * mm, v(-62.13, -7.1) * mm, v(-61.99, -7.13) * mm]});
            skFitSpline(sketch, "E2777", {"points": [v(-61.99, -7.13) * mm, v(-61.84, -7.16) * mm, v(-61.7, -7.23) * mm, v(-61.58, -7.3) * mm]});
            skFitSpline(sketch, "E2778", {"points": [v(-61.58, -7.3) * mm, v(-61.28, -7.49) * mm, v(-61, -7.68) * mm, v(-60.71, -7.87) * mm]});
            skFitSpline(sketch, "E2779", {"points": [v(-60.71, -7.87) * mm, v(-60.63, -7.92) * mm, v(-60.55, -7.98) * mm, v(-60.49, -8.04) * mm]});
            skFitSpline(sketch, "E2780", {"points": [v(-60.49, -8.04) * mm, v(-60.3, -8.23) * mm, v(-60.3, -8.48) * mm, v(-60.45, -8.68) * mm]});
            skFitSpline(sketch, "E2781", {"points": [v(-60.45, -8.68) * mm, v(-60.6, -8.86) * mm, v(-60.85, -8.9) * mm, v(-61.06, -8.8) * mm]});
            skFitSpline(sketch, "E2782", {"points": [v(-61.06, -8.8) * mm, v(-61.12, -8.77) * mm, v(-61.18, -8.72) * mm, v(-61.24, -8.69) * mm]});
            skFitSpline(sketch, "E2783", {"points": [v(-61.24, -8.69) * mm, v(-61.3, -8.65) * mm, v(-61.37, -8.63) * mm, v(-61.48, -8.57) * mm]});
            skFitSpline(sketch, "E2784", {"points": [v(-61.48, -8.57) * mm, v(-61.4, -8.75) * mm, v(-61.34, -8.88) * mm, v(-61.28, -9) * mm]});
            skFitSpline(sketch, "E2785", {"points": [v(-61.28, -9) * mm, v(-60.97, -9.63) * mm, v(-60.67, -10.25) * mm, v(-60.36, -10.88) * mm]});
            skFitSpline(sketch, "E2786", {"points": [v(-60.36, -10.88) * mm, v(-60.31, -10.99) * mm, v(-60.25, -11.07) * mm, v(-60.1, -11.08) * mm]});
            skFitSpline(sketch, "E2787", {"points": [v(-60.1, -11.08) * mm, v(-59.91, -11.1) * mm, v(-59.74, -11.18) * mm, v(-59.58, -11.3) * mm]});
            skFitSpline(sketch, "E2788", {"points": [v(-59.58, -11.3) * mm, v(-59.12, -11.68) * mm, v(-58.6, -11.97) * mm, v(-58.08, -12.25) * mm]});
            skFitSpline(sketch, "E2789", {"points": [v(-58.08, -12.25) * mm, v(-57.99, -12.3) * mm, v(-57.89, -12.36) * mm, v(-57.8, -12.42) * mm]});
            skFitSpline(sketch, "E2790", {"points": [v(-57.8, -12.42) * mm, v(-57.56, -12.58) * mm, v(-57.5, -12.85) * mm, v(-57.62, -13.07) * mm]});
            skFitSpline(sketch, "E2791", {"points": [v(-57.62, -13.07) * mm, v(-57.75, -13.3) * mm, v(-58.03, -13.39) * mm, v(-58.29, -13.25) * mm]});
            skFitSpline(sketch, "E2792", {"points": [v(-58.29, -13.25) * mm, v(-58.6, -13.09) * mm, v(-58.92, -12.9) * mm, v(-59.23, -12.73) * mm]});
            skFitSpline(sketch, "E2793", {"points": [v(-59.23, -12.73) * mm, v(-59.32, -12.68) * mm, v(-59.4, -12.63) * mm, v(-59.5, -12.57) * mm]});
            skFitSpline(sketch, "E2794", {"points": [v(-59.5, -12.57) * mm, v(-59.49, -12.79) * mm, v(-59.3, -13.18) * mm, v(-59.14, -13.3) * mm]});
            skFitSpline(sketch, "E2795", {"points": [v(-59.14, -13.3) * mm, v(-58.82, -13.55) * mm, v(-58.51, -13.8) * mm, v(-58.18, -14.03) * mm]});
            skFitSpline(sketch, "E2796", {"points": [v(-58.18, -14.03) * mm, v(-57.76, -14.33) * mm, v(-57.32, -14.6) * mm, v(-56.89, -14.89) * mm]});
            skFitSpline(sketch, "E2797", {"points": [v(-56.89, -14.89) * mm, v(-56.65, -15.04) * mm, v(-56.58, -15.31) * mm, v(-56.7, -15.54) * mm]});
            skFitSpline(sketch, "E2798", {"points": [v(-56.7, -15.54) * mm, v(-56.83, -15.76) * mm, v(-57.1, -15.86) * mm, v(-57.35, -15.74) * mm]});
            skFitSpline(sketch, "E2799", {"points": [v(-57.35, -15.74) * mm, v(-57.55, -15.64) * mm, v(-57.74, -15.5) * mm, v(-57.94, -15.37) * mm]});
            skFitSpline(sketch, "E2800", {"points": [v(-57.94, -15.37) * mm, v(-58.13, -15.25) * mm, v(-58.32, -15.12) * mm, v(-58.51, -14.98) * mm]});
            skFitSpline(sketch, "E2801", {"points": [v(-58.51, -14.98) * mm, v(-58.94, -14.68) * mm, v(-59.37, -14.37) * mm, v(-59.81, -14.05) * mm]});
            skFitSpline(sketch, "E2802", {"points": [v(-59.81, -14.05) * mm, v(-59.83, -14.12) * mm, v(-59.85, -14.19) * mm, v(-59.86, -14.26) * mm]});
            skFitSpline(sketch, "E2803", {"points": [v(-59.86, -14.26) * mm, v(-59.93, -14.74) * mm, v(-60, -15.22) * mm, v(-60.08, -15.7) * mm]});
            skFitSpline(sketch, "E2804", {"points": [v(-60.08, -15.7) * mm, v(-60.14, -16.07) * mm, v(-60.22, -16.44) * mm, v(-60.3, -16.8) * mm]});
            skFitSpline(sketch, "E2805", {"points": [v(-60.3, -16.8) * mm, v(-60.32, -16.89) * mm, v(-60.34, -16.97) * mm, v(-60.38, -17.05) * mm]});
            skFitSpline(sketch, "E2806", {"points": [v(-60.38, -17.05) * mm, v(-60.5, -17.27) * mm, v(-60.75, -17.37) * mm, v(-60.97, -17.29) * mm]});
            skFitSpline(sketch, "E2807", {"points": [v(-60.97, -17.29) * mm, v(-61.2, -17.2) * mm, v(-61.33, -16.96) * mm, v(-61.28, -16.71) * mm]});
            skFitSpline(sketch, "E2808", {"points": [v(-61.28, -16.71) * mm, v(-61.14, -15.98) * mm, v(-60.99, -15.24) * mm, v(-60.85, -14.5) * mm]});
            skFitSpline(sketch, "E2809", {"points": [v(-60.85, -14.5) * mm, v(-60.78, -14.1) * mm, v(-60.78, -13.71) * mm, v(-60.97, -13.34) * mm]});
            skFitSpline(sketch, "E2810", {"points": [v(-60.97, -13.34) * mm, v(-60.99, -13.3) * mm, v(-61.01, -13.26) * mm, v(-61.05, -13.18) * mm]});
            skFitSpline(sketch, "E2811", {"points": [v(-61.05, -13.18) * mm, v(-61.17, -13.61) * mm, v(-61.29, -14.01) * mm, v(-61.4, -14.4) * mm]});
            skFitSpline(sketch, "E2812", {"points": [v(-61.4, -14.4) * mm, v(-61.42, -14.48) * mm, v(-61.44, -14.56) * mm, v(-61.47, -14.63) * mm]});
            skFitSpline(sketch, "E2813", {"points": [v(-61.47, -14.63) * mm, v(-61.58, -14.87) * mm, v(-61.83, -14.98) * mm, v(-62.07, -14.9) * mm]});
            skFitSpline(sketch, "E2814", {"points": [v(-62.07, -14.9) * mm, v(-62.3, -14.82) * mm, v(-62.44, -14.58) * mm, v(-62.38, -14.34) * mm]});
            skFitSpline(sketch, "E2815", {"points": [v(-62.38, -14.34) * mm, v(-62.33, -14.1) * mm, v(-62.25, -13.86) * mm, v(-62.19, -13.62) * mm]});
            skFitSpline(sketch, "E2816", {"points": [v(-62.19, -13.62) * mm, v(-62.1, -13.23) * mm, v(-62, -12.83) * mm, v(-61.93, -12.43) * mm]});
            skFitSpline(sketch, "E2817", {"points": [v(-61.93, -12.43) * mm, v(-61.88, -12.13) * mm, v(-61.83, -11.83) * mm, v(-61.6, -11.62) * mm]});
            skFitSpline(sketch, "E2818", {"points": [v(-61.6, -11.62) * mm, v(-61.83, -10.73) * mm, v(-62.16, -9.9) * mm, v(-62.53, -9.05) * mm]});
            skFitSpline(sketch, "E2819", {"points": [v(-62.53, -9.05) * mm, v(-62.56, -9.18) * mm, v(-62.59, -9.31) * mm, v(-62.63, -9.44) * mm]});
            skFitSpline(sketch, "E2820", {"points": [v(-62.63, -9.44) * mm, v(-62.7, -9.64) * mm, v(-62.82, -9.76) * mm, v(-63.04, -9.79) * mm]});
            skFitSpline(sketch, "E2821", {"points": [v(-63.04, -9.79) * mm, v(-63.24, -9.81) * mm, v(-63.43, -9.72) * mm, v(-63.52, -9.54) * mm]});
            skFitSpline(sketch, "E2822", {"points": [v(-63.52, -9.54) * mm, v(-63.55, -9.48) * mm, v(-63.57, -9.4) * mm, v(-63.57, -9.33) * mm]});
            skFitSpline(sketch, "E2823", {"points": [v(-63.57, -9.33) * mm, v(-63.57, -9.23) * mm, v(-63.56, -9.13) * mm, v(-63.54, -9.03) * mm]});
            skFitSpline(sketch, "E2824", {"points": [v(-63.54, -9.03) * mm, v(-63.47, -8.7) * mm, v(-63.4, -8.39) * mm, v(-63.33, -8.07) * mm]});
            skFitSpline(sketch, "E2825", {"points": [v(-63.33, -8.07) * mm, v(-63.29, -7.9) * mm, v(-63.22, -7.74) * mm, v(-63.14, -7.58) * mm]});
            skFitSpline(sketch, "E2826", {"points": [v(-63.14, -7.58) * mm, v(-63.1, -7.5) * mm, v(-63.08, -7.43) * mm, v(-63.12, -7.34) * mm]});
            skFitSpline(sketch, "E2827", {"points": [v(-63.12, -7.34) * mm, v(-63.34, -6.85) * mm, v(-63.56, -6.35) * mm, v(-63.78, -5.85) * mm]});
            skFitSpline(sketch, "E2828", {"points": [v(-63.78, -5.85) * mm, v(-64.32, -6.56) * mm, v(-64.87, -7.26) * mm, v(-65.42, -7.97) * mm]});
            skFitSpline(sketch, "E2829", {"points": [v(-65.42, -7.97) * mm, v(-65.05, -8.39) * mm, v(-64.69, -8.8) * mm, v(-64.32, -9.23) * mm]});
            skFitSpline(sketch, "E2830", {"points": [v(-64.32, -9.23) * mm, v(-63.85, -9.76) * mm, v(-63.38, -10.29) * mm, v(-62.9, -10.82) * mm]});
            skFitSpline(sketch, "E2831", {"points": [v(-62.9, -10.82) * mm, v(-62.87, -10.87) * mm, v(-62.82, -10.92) * mm, v(-62.8, -10.98) * mm]});
            skFitSpline(sketch, "E2832", {"points": [v(-62.8, -10.98) * mm, v(-62.74, -11.27) * mm, v(-62.7, -11.55) * mm, v(-62.87, -11.84) * mm]});
            skFitSpline(sketch, "E2833", {"points": [v(-62.87, -11.84) * mm, v(-63.55, -13) * mm, v(-64.28, -14.14) * mm, v(-65.08, -15.22) * mm]});
            skFitSpline(sketch, "E2834", {"points": [v(-65.08, -15.22) * mm, v(-65.22, -15.42) * mm, v(-65.38, -15.6) * mm, v(-65.53, -15.78) * mm]});
            skFitSpline(sketch, "E2835", {"points": [v(-65.53, -15.78) * mm, v(-65.64, -15.9) * mm, v(-65.79, -15.94) * mm, v(-65.95, -15.93) * mm]});
            skFitSpline(sketch, "E2836", {"points": [v(-65.95, -15.93) * mm, v(-66, -15.93) * mm, v(-66.04, -15.91) * mm, v(-66.09, -15.92) * mm]});
            skFitSpline(sketch, "E2837", {"points": [v(-66.09, -15.92) * mm, v(-66.44, -16) * mm, v(-66.65, -15.79) * mm, v(-66.83, -15.55) * mm]});
            skFitSpline(sketch, "E2838", {"points": [v(-66.83, -15.55) * mm, v(-67.19, -15.06) * mm, v(-67.54, -14.58) * mm, v(-67.87, -14.08) * mm]});
            skFitSpline(sketch, "E2839", {"points": [v(-67.87, -14.08) * mm, v(-68.37, -13.31) * mm, v(-68.84, -12.52) * mm, v(-69.33, -11.74) * mm]});
            skFitSpline(sketch, "E2840", {"points": [v(-69.33, -11.74) * mm, v(-69.4, -11.62) * mm, v(-69.43, -11.48) * mm, v(-69.4, -11.33) * mm]});
            skFitSpline(sketch, "E2841", {"points": [v(-69.4, -11.33) * mm, v(-69.38, -11.27) * mm, v(-69.4, -11.2) * mm, v(-69.37, -11.14) * mm]});
            skFitSpline(sketch, "E2842", {"points": [v(-69.37, -11.14) * mm, v(-69.34, -11.03) * mm, v(-69.3, -10.9) * mm, v(-69.23, -10.82) * mm]});
            skFitSpline(sketch, "E2843", {"points": [v(-69.23, -10.82) * mm, v(-68.58, -10.07) * mm, v(-67.92, -9.32) * mm, v(-67.26, -8.57) * mm]});
            skFitSpline(sketch, "E2844", {"points": [v(-67.26, -8.57) * mm, v(-67.08, -8.37) * mm, v(-66.9, -8.18) * mm, v(-66.72, -7.98) * mm]});
            skFitSpline(sketch, "E2845", {"points": [v(64.48, 2.3) * mm, v(64.18, 3.05) * mm, v(63.9, 3.79) * mm, v(63.6, 4.54) * mm]});
            skFitSpline(sketch, "E2846", {"points": [v(63.6, 4.54) * mm, v(63.4, 4.44) * mm, v(63.2, 4.5) * mm, v(62.99, 4.54) * mm]});
            skFitSpline(sketch, "E2847", {"points": [v(62.99, 4.54) * mm, v(62.7, 4.6) * mm, v(62.42, 4.63) * mm, v(62.1, 4.68) * mm]});
            skFitSpline(sketch, "E2848", {"points": [v(62.1, 4.68) * mm, v(62.14, 4.38) * mm, v(62.17, 4.12) * mm, v(62.21, 3.87) * mm]});
            skFitSpline(sketch, "E2849", {"points": [v(62.21, 3.87) * mm, v(62.26, 3.63) * mm, v(62.35, 3.4) * mm, v(62.24, 3.18) * mm]});
            skFitSpline(sketch, "E2850", {"points": [v(62.24, 3.18) * mm, v(63, 2.88) * mm, v(63.73, 2.6) * mm, v(64.48, 2.3) * mm]});
            skFitSpline(sketch, "E2851", {"points": [v(65.7, 6.18) * mm, v(65.64, 6.1) * mm, v(65.61, 6.04) * mm, v(65.57, 5.99) * mm]});
            skFitSpline(sketch, "E2852", {"points": [v(65.57, 5.99) * mm, v(65.26, 5.68) * mm, v(65.13, 5.23) * mm, v(64.75, 5) * mm]});
            skFitSpline(sketch, "E2853", {"points": [v(64.75, 5) * mm, v(65.07, 4.26) * mm, v(65.38, 3.54) * mm, v(65.7, 2.8) * mm]});
            skFitSpline(sketch, "E2854", {"points": [v(65.7, 2.8) * mm, v(66.03, 3.54) * mm, v(66.34, 4.28) * mm, v(66.65, 4.96) * mm]});
            skFitSpline(sketch, "E2855", {"points": [v(66.65, 4.96) * mm, v(66.51, 5.12) * mm, v(66.4, 5.24) * mm, v(66.29, 5.38) * mm]});
            skFitSpline(sketch, "E2856", {"points": [v(66.29, 5.38) * mm, v(66.1, 5.63) * mm, v(65.91, 5.9) * mm, v(65.7, 6.18) * mm]});
            skFitSpline(sketch, "E2857", {"points": [v(61.77, 0.11) * mm, v(62.5, 0.44) * mm, v(63.24, 0.75) * mm, v(63.97, 1.07) * mm]});
            skFitSpline(sketch, "E2858", {"points": [v(63.97, 1.07) * mm, v(63.22, 1.4) * mm, v(62.5, 1.72) * mm, v(61.79, 2.03) * mm]});
            skFitSpline(sketch, "E2859", {"points": [v(61.79, 2.03) * mm, v(61.48, 1.6) * mm, v(60.96, 1.44) * mm, v(60.63, 1.05) * mm]});
            skFitSpline(sketch, "E2860", {"points": [v(60.63, 1.05) * mm, v(60.87, 0.88) * mm, v(61.1, 0.7) * mm, v(61.33, 0.54) * mm]});
            skFitSpline(sketch, "E2861", {"points": [v(61.33, 0.54) * mm, v(61.5, 0.42) * mm, v(61.68, 0.32) * mm, v(61.77, 0.11) * mm]});
            skFitSpline(sketch, "E2862", {"points": [v(66.65, -2.8) * mm, v(66.5, -2.47) * mm, v(66.33, -2.11) * mm, v(66.17, -1.75) * mm]});
            skFitSpline(sketch, "E2863", {"points": [v(66.17, -1.75) * mm, v(66.01, -1.39) * mm, v(65.87, -1.02) * mm, v(65.71, -0.64) * mm]});
            skFitSpline(sketch, "E2864", {"points": [v(65.71, -0.64) * mm, v(65.38, -1.4) * mm, v(65.06, -2.12) * mm, v(64.74, -2.87) * mm]});
            skFitSpline(sketch, "E2865", {"points": [v(64.74, -2.87) * mm, v(65, -2.96) * mm, v(65.1, -3.21) * mm, v(65.24, -3.4) * mm]});
            skFitSpline(sketch, "E2866", {"points": [v(65.24, -3.4) * mm, v(65.39, -3.6) * mm, v(65.54, -3.8) * mm, v(65.7, -4.02) * mm]});
            skFitSpline(sketch, "E2867", {"points": [v(65.7, -4.02) * mm, v(65.91, -3.75) * mm, v(66.1, -3.5) * mm, v(66.28, -3.25) * mm]});
            skFitSpline(sketch, "E2868", {"points": [v(66.28, -3.25) * mm, v(66.39, -3.1) * mm, v(66.5, -2.97) * mm, v(66.65, -2.8) * mm]});
            skFitSpline(sketch, "E2869", {"points": [v(69.16, 3.18) * mm, v(69.08, 3.38) * mm, v(69.13, 3.58) * mm, v(69.17, 3.79) * mm]});
            skFitSpline(sketch, "E2870", {"points": [v(69.17, 3.79) * mm, v(69.23, 4.07) * mm, v(69.26, 4.36) * mm, v(69.31, 4.68) * mm]});
            skFitSpline(sketch, "E2871", {"points": [v(69.31, 4.68) * mm, v(69, 4.64) * mm, v(68.73, 4.6) * mm, v(68.46, 4.55) * mm]});
            skFitSpline(sketch, "E2872", {"points": [v(68.46, 4.55) * mm, v(68.24, 4.51) * mm, v(68.02, 4.44) * mm, v(67.8, 4.53) * mm]});
            skFitSpline(sketch, "E2873", {"points": [v(67.8, 4.53) * mm, v(67.5, 3.78) * mm, v(67.22, 3.04) * mm, v(66.93, 2.3) * mm]});
            skFitSpline(sketch, "E2874", {"points": [v(66.93, 2.3) * mm, v(67.68, 2.6) * mm, v(68.41, 2.88) * mm, v(69.16, 3.18) * mm]});
            skFitSpline(sketch, "E2875", {"points": [v(64.48, -0.15) * mm, v(63.72, -0.45) * mm, v(62.99, -0.74) * mm, v(62.26, -1.02) * mm]});
            skFitSpline(sketch, "E2876", {"points": [v(62.26, -1.02) * mm, v(62.35, -1.54) * mm, v(62.07, -2.02) * mm, v(62.13, -2.53) * mm]});
            skFitSpline(sketch, "E2877", {"points": [v(62.13, -2.53) * mm, v(62.41, -2.49) * mm, v(62.67, -2.46) * mm, v(62.93, -2.41) * mm]});
            skFitSpline(sketch, "E2878", {"points": [v(62.93, -2.41) * mm, v(63.16, -2.37) * mm, v(63.37, -2.3) * mm, v(63.6, -2.38) * mm]});
            skFitSpline(sketch, "E2879", {"points": [v(63.6, -2.38) * mm, v(63.9, -1.63) * mm, v(64.19, -0.9) * mm, v(64.48, -0.15) * mm]});
            skFitSpline(sketch, "E2880", {"points": [v(69.12, -1) * mm, v(68.41, -0.73) * mm, v(67.67, -0.44) * mm, v(66.92, -0.15) * mm]});
            skFitSpline(sketch, "E2881", {"points": [v(66.92, -0.15) * mm, v(67.22, -0.9) * mm, v(67.51, -1.64) * mm, v(67.8, -2.37) * mm]});
            skFitSpline(sketch, "E2882", {"points": [v(67.8, -2.37) * mm, v(68.33, -2.28) * mm, v(68.8, -2.56) * mm, v(69.31, -2.5) * mm]});
            skFitSpline(sketch, "E2883", {"points": [v(69.31, -2.5) * mm, v(69.26, -2.17) * mm, v(69.2, -1.85) * mm, v(69.16, -1.54) * mm]});
            skFitSpline(sketch, "E2884", {"points": [v(69.16, -1.54) * mm, v(69.14, -1.38) * mm, v(69.13, -1.21) * mm, v(69.12, -1) * mm]});
            skFitSpline(sketch, "E2885", {"points": [v(69.65, 2.04) * mm, v(68.9, 1.71) * mm, v(68.18, 1.4) * mm, v(67.43, 1.07) * mm]});
            skFitSpline(sketch, "E2886", {"points": [v(67.43, 1.07) * mm, v(68.18, 0.75) * mm, v(68.9, 0.44) * mm, v(69.62, 0.12) * mm]});
            skFitSpline(sketch, "E2887", {"points": [v(69.62, 0.12) * mm, v(69.92, 0.54) * mm, v(70.44, 0.7) * mm, v(70.78, 1.1) * mm]});
            skFitSpline(sketch, "E2888", {"points": [v(70.78, 1.1) * mm, v(70.53, 1.28) * mm, v(70.3, 1.45) * mm, v(70.06, 1.62) * mm]});
            skFitSpline(sketch, "E2889", {"points": [v(70.06, 1.62) * mm, v(69.9, 1.74) * mm, v(69.71, 1.83) * mm, v(69.65, 2.04) * mm]});
            skFitSpline(sketch, "E2890", {"points": [v(64.34, -3.81) * mm, v(64.23, -4.05) * mm, v(64.13, -4.26) * mm, v(64.03, -4.47) * mm]});
            skFitSpline(sketch, "E2891", {"points": [v(64.03, -4.47) * mm, v(64, -4.54) * mm, v(64, -4.6) * mm, v(64.04, -4.67) * mm]});
            skFitSpline(sketch, "E2892", {"points": [v(64.04, -4.67) * mm, v(64.25, -5) * mm, v(64.44, -5.34) * mm, v(64.67, -5.66) * mm]});
            skFitSpline(sketch, "E2893", {"points": [v(64.67, -5.66) * mm, v(64.93, -6.03) * mm, v(65.21, -6.39) * mm, v(65.42, -6.8) * mm]});
            skFitSpline(sketch, "E2894", {"points": [v(65.42, -6.8) * mm, v(65.49, -6.93) * mm, v(65.6, -7.05) * mm, v(65.71, -7.21) * mm]});
            skFitSpline(sketch, "E2895", {"points": [v(65.71, -7.21) * mm, v(65.84, -7.01) * mm, v(65.95, -6.85) * mm, v(66.06, -6.68) * mm]});
            skFitSpline(sketch, "E2896", {"points": [v(66.06, -6.68) * mm, v(66.2, -6.45) * mm, v(66.34, -6.2) * mm, v(66.51, -5.98) * mm]});
            skFitSpline(sketch, "E2897", {"points": [v(66.51, -5.98) * mm, v(66.82, -5.57) * mm, v(67.11, -5.15) * mm, v(67.35, -4.7) * mm]});
            skFitSpline(sketch, "E2898", {"points": [v(67.35, -4.7) * mm, v(67.4, -4.6) * mm, v(67.41, -4.52) * mm, v(67.36, -4.43) * mm]});
            skFitSpline(sketch, "E2899", {"points": [v(67.36, -4.43) * mm, v(67.27, -4.24) * mm, v(67.18, -4.04) * mm, v(67.08, -3.85) * mm]});
            skFitSpline(sketch, "E2900", {"points": [v(67.08, -3.85) * mm, v(67.07, -3.86) * mm, v(67.05, -3.86) * mm, v(67.04, -3.87) * mm]});
            skFitSpline(sketch, "E2901", {"points": [v(67.04, -3.87) * mm, v(66.8, -4.22) * mm, v(66.54, -4.57) * mm, v(66.3, -4.92) * mm]});
            skFitSpline(sketch, "E2902", {"points": [v(66.3, -4.92) * mm, v(66.18, -5.09) * mm, v(66.04, -5.19) * mm, v(65.84, -5.19) * mm]});
            skFitSpline(sketch, "E2903", {"points": [v(65.84, -5.19) * mm, v(65.76, -5.19) * mm, v(65.68, -5.19) * mm, v(65.6, -5.19) * mm]});
            skFitSpline(sketch, "E2904", {"points": [v(65.6, -5.19) * mm, v(65.37, -5.2) * mm, v(65.22, -5.08) * mm, v(65.1, -4.9) * mm]});
            skFitSpline(sketch, "E2905", {"points": [v(65.1, -4.9) * mm, v(64.86, -4.54) * mm, v(64.6, -4.19) * mm, v(64.34, -3.81) * mm]});
            skFitSpline(sketch, "E2906", {"points": [v(60.82, -0.28) * mm, v(60.43, -0.02) * mm, v(60.07, 0.24) * mm, v(59.7, 0.49) * mm]});
            skFitSpline(sketch, "E2907", {"points": [v(59.7, 0.49) * mm, v(59.53, 0.6) * mm, v(59.44, 0.74) * mm, v(59.44, 0.95) * mm]});
            skFitSpline(sketch, "E2908", {"points": [v(59.44, 0.95) * mm, v(59.44, 1.03) * mm, v(59.44, 1.1) * mm, v(59.44, 1.19) * mm]});
            skFitSpline(sketch, "E2909", {"points": [v(59.44, 1.19) * mm, v(59.43, 1.4) * mm, v(59.54, 1.56) * mm, v(59.72, 1.68) * mm]});
            skFitSpline(sketch, "E2910", {"points": [v(59.72, 1.68) * mm, v(60.09, 1.92) * mm, v(60.44, 2.17) * mm, v(60.82, 2.43) * mm]});
            skFitSpline(sketch, "E2911", {"points": [v(60.82, 2.43) * mm, v(60.6, 2.54) * mm, v(60.4, 2.64) * mm, v(60.21, 2.73) * mm]});
            skFitSpline(sketch, "E2912", {"points": [v(60.21, 2.73) * mm, v(60.13, 2.77) * mm, v(60.06, 2.8) * mm, v(59.96, 2.74) * mm]});
            skFitSpline(sketch, "E2913", {"points": [v(59.96, 2.74) * mm, v(59.65, 2.54) * mm, v(59.33, 2.37) * mm, v(59.03, 2.16) * mm]});
            skFitSpline(sketch, "E2914", {"points": [v(59.03, 2.16) * mm, v(58.64, 1.88) * mm, v(58.27, 1.58) * mm, v(57.84, 1.36) * mm]});
            skFitSpline(sketch, "E2915", {"points": [v(57.84, 1.36) * mm, v(57.7, 1.3) * mm, v(57.58, 1.18) * mm, v(57.42, 1.07) * mm]});
            skFitSpline(sketch, "E2916", {"points": [v(57.42, 1.07) * mm, v(57.62, 0.94) * mm, v(57.78, 0.83) * mm, v(57.95, 0.72) * mm]});
            skFitSpline(sketch, "E2917", {"points": [v(57.95, 0.72) * mm, v(58.17, 0.58) * mm, v(58.4, 0.45) * mm, v(58.61, 0.3) * mm]});
            skFitSpline(sketch, "E2918", {"points": [v(58.61, 0.3) * mm, v(59.03, -0.02) * mm, v(59.46, -0.33) * mm, v(59.93, -0.57) * mm]});
            skFitSpline(sketch, "E2919", {"points": [v(59.93, -0.57) * mm, v(60.04, -0.63) * mm, v(60.12, -0.63) * mm, v(60.22, -0.58) * mm]});
            skFitSpline(sketch, "E2920", {"points": [v(60.22, -0.58) * mm, v(60.4, -0.49) * mm, v(60.59, -0.4) * mm, v(60.82, -0.28) * mm]});
            skFitSpline(sketch, "E2921", {"points": [v(71.58, 6.94) * mm, v(71.33, 6.89) * mm, v(71.14, 6.85) * mm, v(70.94, 6.8) * mm]});
            skFitSpline(sketch, "E2922", {"points": [v(70.94, 6.8) * mm, v(70.68, 6.75) * mm, v(70.42, 6.68) * mm, v(70.15, 6.64) * mm]});
            skFitSpline(sketch, "E2923", {"points": [v(70.15, 6.64) * mm, v(69.62, 6.56) * mm, v(69.1, 6.48) * mm, v(68.59, 6.3) * mm]});
            skFitSpline(sketch, "E2924", {"points": [v(68.59, 6.3) * mm, v(68.53, 6.29) * mm, v(68.47, 6.24) * mm, v(68.45, 6.2) * mm]});
            skFitSpline(sketch, "E2925", {"points": [v(68.45, 6.2) * mm, v(68.36, 5.98) * mm, v(68.3, 5.76) * mm, v(68.2, 5.49) * mm]});
            skFitSpline(sketch, "E2926", {"points": [v(68.2, 5.49) * mm, v(68.65, 5.57) * mm, v(69.06, 5.64) * mm, v(69.48, 5.72) * mm]});
            skFitSpline(sketch, "E2927", {"points": [v(69.48, 5.72) * mm, v(69.71, 5.77) * mm, v(69.92, 5.75) * mm, v(70.09, 5.56) * mm]});
            skFitSpline(sketch, "E2928", {"points": [v(70.09, 5.56) * mm, v(70.12, 5.51) * mm, v(70.16, 5.48) * mm, v(70.2, 5.44) * mm]});
            skFitSpline(sketch, "E2929", {"points": [v(70.2, 5.44) * mm, v(70.38, 5.28) * mm, v(70.4, 5.09) * mm, v(70.36, 4.87) * mm]});
            skFitSpline(sketch, "E2930", {"points": [v(70.36, 4.87) * mm, v(70.32, 4.7) * mm, v(70.27, 4.53) * mm, v(70.24, 4.36) * mm]});
            skFitSpline(sketch, "E2931", {"points": [v(70.24, 4.36) * mm, v(70.2, 4.1) * mm, v(70.18, 3.84) * mm, v(70.14, 3.58) * mm]});
            skFitSpline(sketch, "E2932", {"points": [v(70.14, 3.58) * mm, v(70.37, 3.65) * mm, v(70.57, 3.72) * mm, v(70.77, 3.8) * mm]});
            skFitSpline(sketch, "E2933", {"points": [v(70.77, 3.8) * mm, v(70.84, 3.82) * mm, v(70.92, 3.89) * mm, v(70.93, 3.95) * mm]});
            skFitSpline(sketch, "E2934", {"points": [v(70.93, 3.95) * mm, v(71.03, 4.32) * mm, v(71.11, 4.69) * mm, v(71.2, 5.06) * mm]});
            skFitSpline(sketch, "E2935", {"points": [v(71.2, 5.06) * mm, v(71.27, 5.44) * mm, v(71.33, 5.83) * mm, v(71.4, 6.21) * mm]});
            skFitSpline(sketch, "E2936", {"points": [v(71.4, 6.21) * mm, v(71.45, 6.44) * mm, v(71.51, 6.66) * mm, v(71.58, 6.94) * mm]});
            skFitSpline(sketch, "E2937", {"points": [v(71.57, -4.78) * mm, v(71.51, -4.52) * mm, v(71.46, -4.3) * mm, v(71.4, -4.07) * mm]});
            skFitSpline(sketch, "E2938", {"points": [v(71.4, -4.07) * mm, v(71.37, -3.9) * mm, v(71.31, -3.73) * mm, v(71.29, -3.56) * mm]});
            skFitSpline(sketch, "E2939", {"points": [v(71.29, -3.56) * mm, v(71.21, -2.97) * mm, v(71.12, -2.4) * mm, v(70.95, -1.83) * mm]});
            skFitSpline(sketch, "E2940", {"points": [v(70.95, -1.83) * mm, v(70.92, -1.74) * mm, v(70.88, -1.69) * mm, v(70.8, -1.66) * mm]});
            skFitSpline(sketch, "E2941", {"points": [v(70.8, -1.66) * mm, v(70.59, -1.58) * mm, v(70.37, -1.5) * mm, v(70.14, -1.43) * mm]});
            skFitSpline(sketch, "E2942", {"points": [v(70.14, -1.43) * mm, v(70.16, -1.55) * mm, v(70.17, -1.66) * mm, v(70.18, -1.77) * mm]});
            skFitSpline(sketch, "E2943", {"points": [v(70.18, -1.77) * mm, v(70.23, -2.06) * mm, v(70.25, -2.36) * mm, v(70.34, -2.64) * mm]});
            skFitSpline(sketch, "E2944", {"points": [v(70.34, -2.64) * mm, v(70.43, -2.97) * mm, v(70.32, -3.18) * mm, v(70.1, -3.4) * mm]});
            skFitSpline(sketch, "E2945", {"points": [v(70.1, -3.4) * mm, v(69.89, -3.6) * mm, v(69.68, -3.62) * mm, v(69.42, -3.56) * mm]});
            skFitSpline(sketch, "E2946", {"points": [v(69.42, -3.56) * mm, v(69.03, -3.47) * mm, v(68.62, -3.42) * mm, v(68.2, -3.35) * mm]});
            skFitSpline(sketch, "E2947", {"points": [v(68.2, -3.35) * mm, v(68.29, -3.6) * mm, v(68.35, -3.8) * mm, v(68.42, -4) * mm]});
            skFitSpline(sketch, "E2948", {"points": [v(68.42, -4) * mm, v(68.45, -4.07) * mm, v(68.48, -4.14) * mm, v(68.58, -4.16) * mm]});
            skFitSpline(sketch, "E2949", {"points": [v(68.58, -4.16) * mm, v(68.91, -4.23) * mm, v(69.24, -4.33) * mm, v(69.58, -4.4) * mm]});
            skFitSpline(sketch, "E2950", {"points": [v(69.58, -4.4) * mm, v(70.09, -4.5) * mm, v(70.6, -4.53) * mm, v(71.1, -4.7) * mm]});
            skFitSpline(sketch, "E2951", {"points": [v(71.1, -4.7) * mm, v(71.23, -4.75) * mm, v(71.38, -4.75) * mm, v(71.57, -4.78) * mm]});
            skFitSpline(sketch, "E2952", {"points": [v(59.85, -4.79) * mm, v(60.08, -4.74) * mm, v(60.27, -4.7) * mm, v(60.47, -4.66) * mm]});
            skFitSpline(sketch, "E2953", {"points": [v(60.47, -4.66) * mm, v(60.7, -4.6) * mm, v(60.93, -4.52) * mm, v(61.16, -4.5) * mm]});
            skFitSpline(sketch, "E2954", {"points": [v(61.16, -4.5) * mm, v(61.76, -4.43) * mm, v(62.35, -4.32) * mm, v(62.94, -4.12) * mm]});
            skFitSpline(sketch, "E2955", {"points": [v(62.94, -4.12) * mm, v(63.02, -3.88) * mm, v(63.1, -3.63) * mm, v(63.2, -3.36) * mm]});
            skFitSpline(sketch, "E2956", {"points": [v(63.2, -3.36) * mm, v(62.87, -3.4) * mm, v(62.56, -3.45) * mm, v(62.25, -3.5) * mm]});
            skFitSpline(sketch, "E2957", {"points": [v(62.25, -3.5) * mm, v(62.14, -3.5) * mm, v(62.02, -3.55) * mm, v(61.9, -3.58) * mm]});
            skFitSpline(sketch, "E2958", {"points": [v(61.9, -3.58) * mm, v(61.54, -3.67) * mm, v(61.05, -3.3) * mm, v(61.02, -2.93) * mm]});
            skFitSpline(sketch, "E2959", {"points": [v(61.02, -2.93) * mm, v(61.02, -2.88) * mm, v(61.03, -2.82) * mm, v(61.04, -2.77) * mm]});
            skFitSpline(sketch, "E2960", {"points": [v(61.04, -2.77) * mm, v(61.1, -2.52) * mm, v(61.15, -2.27) * mm, v(61.19, -2.02) * mm]});
            skFitSpline(sketch, "E2961", {"points": [v(61.19, -2.02) * mm, v(61.22, -1.83) * mm, v(61.24, -1.63) * mm, v(61.26, -1.43) * mm]});
            skFitSpline(sketch, "E2962", {"points": [v(61.26, -1.43) * mm, v(61.03, -1.51) * mm, v(60.82, -1.58) * mm, v(60.62, -1.66) * mm]});
            skFitSpline(sketch, "E2963", {"points": [v(60.62, -1.66) * mm, v(60.56, -1.68) * mm, v(60.5, -1.74) * mm, v(60.48, -1.8) * mm]});
            skFitSpline(sketch, "E2964", {"points": [v(60.48, -1.8) * mm, v(60.4, -2.1) * mm, v(60.3, -2.4) * mm, v(60.25, -2.72) * mm]});
            skFitSpline(sketch, "E2965", {"points": [v(60.25, -2.72) * mm, v(60.14, -3.25) * mm, v(60.11, -3.8) * mm, v(59.93, -4.31) * mm]});
            skFitSpline(sketch, "E2966", {"points": [v(59.93, -4.31) * mm, v(59.88, -4.45) * mm, v(59.88, -4.6) * mm, v(59.85, -4.79) * mm]});
            skFitSpline(sketch, "E2967", {"points": [v(70.59, 2.43) * mm, v(70.98, 2.17) * mm, v(71.33, 1.91) * mm, v(71.7, 1.67) * mm]});
            skFitSpline(sketch, "E2968", {"points": [v(71.7, 1.67) * mm, v(71.87, 1.55) * mm, v(71.97, 1.41) * mm, v(71.96, 1.2) * mm]});
            skFitSpline(sketch, "E2969", {"points": [v(71.96, 1.2) * mm, v(71.96, 1.15) * mm, v(71.96, 1.1) * mm, v(71.96, 1.05) * mm]});
            skFitSpline(sketch, "E2970", {"points": [v(71.96, 1.05) * mm, v(72, 0.75) * mm, v(71.85, 0.57) * mm, v(71.6, 0.42) * mm]});
            skFitSpline(sketch, "E2971", {"points": [v(71.6, 0.42) * mm, v(71.25, 0.21) * mm, v(70.94, -0.04) * mm, v(70.6, -0.29) * mm]});
            skFitSpline(sketch, "E2972", {"points": [v(70.6, -0.29) * mm, v(70.82, -0.4) * mm, v(71.01, -0.5) * mm, v(71.2, -0.59) * mm]});
            skFitSpline(sketch, "E2973", {"points": [v(71.2, -0.59) * mm, v(71.28, -0.62) * mm, v(71.35, -0.65) * mm, v(71.43, -0.6) * mm]});
            skFitSpline(sketch, "E2974", {"points": [v(71.43, -0.6) * mm, v(71.69, -0.44) * mm, v(71.96, -0.3) * mm, v(72.2, -0.13) * mm]});
            skFitSpline(sketch, "E2975", {"points": [v(72.2, -0.13) * mm, v(72.67, 0.2) * mm, v(73.1, 0.56) * mm, v(73.62, 0.82) * mm]});
            skFitSpline(sketch, "E2976", {"points": [v(73.62, 0.82) * mm, v(73.74, 0.88) * mm, v(73.84, 0.98) * mm, v(73.99, 1.09) * mm]});
            skFitSpline(sketch, "E2977", {"points": [v(73.99, 1.09) * mm, v(73.78, 1.22) * mm, v(73.6, 1.33) * mm, v(73.43, 1.44) * mm]});
            skFitSpline(sketch, "E2978", {"points": [v(73.43, 1.44) * mm, v(73.22, 1.58) * mm, v(73, 1.7) * mm, v(72.8, 1.85) * mm]});
            skFitSpline(sketch, "E2979", {"points": [v(72.8, 1.85) * mm, v(72.37, 2.17) * mm, v(71.94, 2.48) * mm, v(71.47, 2.72) * mm]});
            skFitSpline(sketch, "E2980", {"points": [v(71.47, 2.72) * mm, v(71.38, 2.77) * mm, v(71.3, 2.78) * mm, v(71.2, 2.74) * mm]});
            skFitSpline(sketch, "E2981", {"points": [v(71.2, 2.74) * mm, v(71.02, 2.64) * mm, v(70.82, 2.55) * mm, v(70.59, 2.43) * mm]});
            skFitSpline(sketch, "E2982", {"points": [v(67.06, 5.96) * mm, v(67.17, 6.19) * mm, v(67.26, 6.37) * mm, v(67.35, 6.56) * mm]});
            skFitSpline(sketch, "E2983", {"points": [v(67.35, 6.56) * mm, v(67.4, 6.64) * mm, v(67.43, 6.72) * mm, v(67.37, 6.8) * mm]});
            skFitSpline(sketch, "E2984", {"points": [v(67.37, 6.8) * mm, v(67.22, 7.05) * mm, v(67.09, 7.3) * mm, v(66.93, 7.55) * mm]});
            skFitSpline(sketch, "E2985", {"points": [v(66.93, 7.55) * mm, v(66.6, 8.03) * mm, v(66.22, 8.47) * mm, v(65.96, 9) * mm]});
            skFitSpline(sketch, "E2986", {"points": [v(65.96, 9) * mm, v(65.9, 9.12) * mm, v(65.8, 9.22) * mm, v(65.7, 9.35) * mm]});
            skFitSpline(sketch, "E2987", {"points": [v(65.7, 9.35) * mm, v(65.56, 9.16) * mm, v(65.46, 9) * mm, v(65.36, 8.84) * mm]});
            skFitSpline(sketch, "E2988", {"points": [v(65.36, 8.84) * mm, v(65.19, 8.58) * mm, v(65.03, 8.3) * mm, v(64.84, 8.06) * mm]});
            skFitSpline(sketch, "E2989", {"points": [v(64.84, 8.06) * mm, v(64.55, 7.66) * mm, v(64.27, 7.26) * mm, v(64.04, 6.81) * mm]});
            skFitSpline(sketch, "E2990", {"points": [v(64.04, 6.81) * mm, v(64.02, 6.76) * mm, v(64, 6.69) * mm, v(64.02, 6.64) * mm]});
            skFitSpline(sketch, "E2991", {"points": [v(64.02, 6.64) * mm, v(64.12, 6.42) * mm, v(64.22, 6.2) * mm, v(64.34, 5.96) * mm]});
            skFitSpline(sketch, "E2992", {"points": [v(64.34, 5.96) * mm, v(64.6, 6.34) * mm, v(64.86, 6.69) * mm, v(65.1, 7.05) * mm]});
            skFitSpline(sketch, "E2993", {"points": [v(65.1, 7.05) * mm, v(65.21, 7.23) * mm, v(65.36, 7.34) * mm, v(65.58, 7.33) * mm]});
            skFitSpline(sketch, "E2994", {"points": [v(65.58, 7.33) * mm, v(65.66, 7.33) * mm, v(65.74, 7.33) * mm, v(65.82, 7.33) * mm]});
            skFitSpline(sketch, "E2995", {"points": [v(65.82, 7.33) * mm, v(66.04, 7.34) * mm, v(66.19, 7.23) * mm, v(66.3, 7.05) * mm]});
            skFitSpline(sketch, "E2996", {"points": [v(66.3, 7.05) * mm, v(66.55, 6.7) * mm, v(66.8, 6.34) * mm, v(67.06, 5.96) * mm]});
            skFitSpline(sketch, "E2997", {"points": [v(63.21, 5.49) * mm, v(63.12, 5.74) * mm, v(63.06, 5.94) * mm, v(62.98, 6.14) * mm]});
            skFitSpline(sketch, "E2998", {"points": [v(62.98, 6.14) * mm, v(62.96, 6.2) * mm, v(62.9, 6.28) * mm, v(62.85, 6.3) * mm]});
            skFitSpline(sketch, "E2999", {"points": [v(62.85, 6.3) * mm, v(62.6, 6.38) * mm, v(62.36, 6.45) * mm, v(62.11, 6.5) * mm]});
            skFitSpline(sketch, "E3000", {"points": [v(62.11, 6.5) * mm, v(61.64, 6.59) * mm, v(61.15, 6.66) * mm, v(60.68, 6.75) * mm]});
            skFitSpline(sketch, "E3001", {"points": [v(60.68, 6.75) * mm, v(60.41, 6.8) * mm, v(60.15, 6.88) * mm, v(59.87, 6.95) * mm]});
            skFitSpline(sketch, "E3002", {"points": [v(59.87, 6.95) * mm, v(59.86, 6.7) * mm, v(59.92, 6.52) * mm, v(59.96, 6.33) * mm]});
            skFitSpline(sketch, "E3003", {"points": [v(59.96, 6.33) * mm, v(60.03, 6.06) * mm, v(60.1, 5.8) * mm, v(60.14, 5.53) * mm]});
            skFitSpline(sketch, "E3004", {"points": [v(60.14, 5.53) * mm, v(60.2, 5) * mm, v(60.3, 4.48) * mm, v(60.46, 3.97) * mm]});
            skFitSpline(sketch, "E3005", {"points": [v(60.46, 3.97) * mm, v(60.5, 3.88) * mm, v(60.53, 3.83) * mm, v(60.61, 3.8) * mm]});
            skFitSpline(sketch, "E3006", {"points": [v(60.61, 3.8) * mm, v(60.82, 3.73) * mm, v(61.03, 3.66) * mm, v(61.25, 3.58) * mm]});
            skFitSpline(sketch, "E3007", {"points": [v(61.25, 3.58) * mm, v(61.25, 3.62) * mm, v(61.26, 3.64) * mm, v(61.26, 3.66) * mm]});
            skFitSpline(sketch, "E3008", {"points": [v(61.26, 3.66) * mm, v(61.19, 4.07) * mm, v(61.13, 4.48) * mm, v(61.04, 4.89) * mm]});
            skFitSpline(sketch, "E3009", {"points": [v(61.04, 4.89) * mm, v(61, 5.1) * mm, v(61.04, 5.27) * mm, v(61.18, 5.42) * mm]});
            skFitSpline(sketch, "E3010", {"points": [v(61.18, 5.42) * mm, v(61.23, 5.47) * mm, v(61.29, 5.52) * mm, v(61.34, 5.57) * mm]});
            skFitSpline(sketch, "E3011", {"points": [v(61.34, 5.57) * mm, v(61.49, 5.73) * mm, v(61.67, 5.77) * mm, v(61.88, 5.73) * mm]});
            skFitSpline(sketch, "E3012", {"points": [v(61.88, 5.73) * mm, v(62.31, 5.65) * mm, v(62.74, 5.57) * mm, v(63.21, 5.49) * mm]});
            skFitSpline(sketch, "E3013", {"points": [v(63.45, -5.72) * mm, v(63.4, -5.85) * mm, v(63.34, -5.95) * mm, v(63.3, -6.06) * mm]});
            skFitSpline(sketch, "E3014", {"points": [v(63.3, -6.06) * mm, v(63.29, -6.1) * mm, v(63.28, -6.17) * mm, v(63.3, -6.22) * mm]});
            skFitSpline(sketch, "E3015", {"points": [v(63.3, -6.22) * mm, v(63.38, -6.5) * mm, v(63.46, -6.77) * mm, v(63.56, -7.04) * mm]});
            skFitSpline(sketch, "E3016", {"points": [v(63.56, -7.04) * mm, v(63.68, -7.39) * mm, v(63.82, -7.74) * mm, v(63.97, -8.08) * mm]});
            skFitSpline(sketch, "E3017", {"points": [v(63.97, -8.08) * mm, v(64.24, -8.7) * mm, v(64.52, -9.32) * mm, v(64.8, -9.94) * mm]});
            skFitSpline(sketch, "E3018", {"points": [v(64.8, -9.94) * mm, v(64.91, -10.19) * mm, v(65.05, -10.42) * mm, v(65.16, -10.67) * mm]});
            skFitSpline(sketch, "E3019", {"points": [v(65.16, -10.67) * mm, v(65.3, -10.97) * mm, v(65.44, -11.28) * mm, v(65.58, -11.58) * mm]});
            skFitSpline(sketch, "E3020", {"points": [v(65.58, -11.58) * mm, v(65.6, -11.63) * mm, v(65.65, -11.68) * mm, v(65.71, -11.77) * mm]});
            skFitSpline(sketch, "E3021", {"points": [v(65.71, -11.77) * mm, v(65.8, -11.6) * mm, v(65.88, -11.46) * mm, v(65.95, -11.3) * mm]});
            skFitSpline(sketch, "E3022", {"points": [v(65.95, -11.3) * mm, v(66.08, -11.04) * mm, v(66.19, -10.77) * mm, v(66.31, -10.5) * mm]});
            skFitSpline(sketch, "E3023", {"points": [v(66.31, -10.5) * mm, v(66.61, -9.88) * mm, v(66.93, -9.26) * mm, v(67.22, -8.63) * mm]});
            skFitSpline(sketch, "E3024", {"points": [v(67.22, -8.63) * mm, v(67.38, -8.27) * mm, v(67.51, -7.9) * mm, v(67.65, -7.53) * mm]});
            skFitSpline(sketch, "E3025", {"points": [v(67.65, -7.53) * mm, v(67.8, -7.1) * mm, v(67.96, -6.66) * mm, v(68.1, -6.23) * mm]});
            skFitSpline(sketch, "E3026", {"points": [v(68.1, -6.23) * mm, v(68.12, -6.18) * mm, v(68.12, -6.11) * mm, v(68.1, -6.07) * mm]});
            skFitSpline(sketch, "E3027", {"points": [v(68.1, -6.07) * mm, v(68.07, -5.95) * mm, v(68.01, -5.85) * mm, v(67.96, -5.72) * mm]});
            skFitSpline(sketch, "E3028", {"points": [v(67.96, -5.72) * mm, v(67.91, -5.76) * mm, v(67.88, -5.78) * mm, v(67.86, -5.81) * mm]});
            skFitSpline(sketch, "E3029", {"points": [v(67.86, -5.81) * mm, v(67.7, -6.02) * mm, v(67.53, -6.23) * mm, v(67.38, -6.44) * mm]});
            skFitSpline(sketch, "E3030", {"points": [v(67.38, -6.44) * mm, v(67.21, -6.69) * mm, v(67.06, -6.94) * mm, v(66.9, -7.18) * mm]});
            skFitSpline(sketch, "E3031", {"points": [v(66.9, -7.18) * mm, v(66.69, -7.49) * mm, v(66.49, -7.8) * mm, v(66.27, -8.1) * mm]});
            skFitSpline(sketch, "E3032", {"points": [v(66.27, -8.1) * mm, v(66.16, -8.25) * mm, v(66, -8.33) * mm, v(65.8, -8.3) * mm]});
            skFitSpline(sketch, "E3033", {"points": [v(65.8, -8.3) * mm, v(65.75, -8.3) * mm, v(65.71, -8.28) * mm, v(65.67, -8.3) * mm]});
            skFitSpline(sketch, "E3034", {"points": [v(65.67, -8.3) * mm, v(65.39, -8.35) * mm, v(65.2, -8.21) * mm, v(65.05, -7.99) * mm]});
            skFitSpline(sketch, "E3035", {"points": [v(65.05, -7.99) * mm, v(64.84, -7.66) * mm, v(64.63, -7.33) * mm, v(64.42, -7) * mm]});
            skFitSpline(sketch, "E3036", {"points": [v(64.42, -7) * mm, v(64.32, -6.85) * mm, v(64.22, -6.7) * mm, v(64.1, -6.55) * mm]});
            skFitSpline(sketch, "E3037", {"points": [v(64.1, -6.55) * mm, v(63.92, -6.3) * mm, v(63.73, -6.05) * mm, v(63.54, -5.8) * mm]});
            skFitSpline(sketch, "E3038", {"points": [v(63.54, -5.8) * mm, v(63.52, -5.78) * mm, v(63.5, -5.76) * mm, v(63.45, -5.72) * mm]});
            skFitSpline(sketch, "E3039", {"points": [v(74.8, -7.98) * mm, v(74.68, -7.65) * mm, v(74.59, -7.34) * mm, v(74.48, -7.04) * mm]});
            skFitSpline(sketch, "E3040", {"points": [v(74.48, -7.04) * mm, v(74.27, -6.48) * mm, v(74.05, -5.92) * mm, v(73.86, -5.36) * mm]});
            skFitSpline(sketch, "E3041", {"points": [v(73.86, -5.36) * mm, v(73.51, -4.34) * mm, v(73.08, -3.35) * mm, v(72.57, -2.4) * mm]});
            skFitSpline(sketch, "E3042", {"points": [v(72.57, -2.4) * mm, v(72.55, -2.36) * mm, v(72.51, -2.3) * mm, v(72.47, -2.28) * mm]});
            skFitSpline(sketch, "E3043", {"points": [v(72.47, -2.28) * mm, v(72.35, -2.23) * mm, v(72.23, -2.19) * mm, v(72.1, -2.14) * mm]});
            skFitSpline(sketch, "E3044", {"points": [v(72.1, -2.14) * mm, v(72.1, -2.2) * mm, v(72.09, -2.23) * mm, v(72.1, -2.27) * mm]});
            skFitSpline(sketch, "E3045", {"points": [v(72.1, -2.27) * mm, v(72.13, -2.52) * mm, v(72.16, -2.78) * mm, v(72.2, -3.03) * mm]});
            skFitSpline(sketch, "E3046", {"points": [v(72.2, -3.03) * mm, v(72.22, -3.2) * mm, v(72.25, -3.4) * mm, v(72.29, -3.57) * mm]});
            skFitSpline(sketch, "E3047", {"points": [v(72.29, -3.57) * mm, v(72.37, -3.96) * mm, v(72.46, -4.35) * mm, v(72.55, -4.74) * mm]});
            skFitSpline(sketch, "E3048", {"points": [v(72.55, -4.74) * mm, v(72.62, -5.05) * mm, v(72.63, -5.36) * mm, v(72.3, -5.57) * mm]});
            skFitSpline(sketch, "E3049", {"points": [v(72.3, -5.57) * mm, v(72.3, -5.57) * mm, v(72.3, -5.58) * mm, v(72.3, -5.58) * mm]});
            skFitSpline(sketch, "E3050", {"points": [v(72.3, -5.58) * mm, v(72.15, -5.8) * mm, v(71.94, -5.85) * mm, v(71.7, -5.8) * mm]});
            skFitSpline(sketch, "E3051", {"points": [v(71.7, -5.8) * mm, v(71.31, -5.72) * mm, v(70.93, -5.63) * mm, v(70.54, -5.55) * mm]});
            skFitSpline(sketch, "E3052", {"points": [v(70.54, -5.55) * mm, v(70.37, -5.52) * mm, v(70.2, -5.48) * mm, v(70.04, -5.45) * mm]});
            skFitSpline(sketch, "E3053", {"points": [v(70.04, -5.45) * mm, v(69.7, -5.4) * mm, v(69.37, -5.36) * mm, v(69.03, -5.31) * mm]});
            skFitSpline(sketch, "E3054", {"points": [v(69.03, -5.31) * mm, v(69, -5.3) * mm, v(68.97, -5.32) * mm, v(68.92, -5.32) * mm]});
            skFitSpline(sketch, "E3055", {"points": [v(68.92, -5.32) * mm, v(68.97, -5.45) * mm, v(69, -5.57) * mm, v(69.06, -5.69) * mm]});
            skFitSpline(sketch, "E3056", {"points": [v(69.06, -5.69) * mm, v(69.08, -5.73) * mm, v(69.12, -5.76) * mm, v(69.16, -5.78) * mm]});
            skFitSpline(sketch, "E3057", {"points": [v(69.16, -5.78) * mm, v(69.4, -5.92) * mm, v(69.66, -6.05) * mm, v(69.92, -6.18) * mm]});
            skFitSpline(sketch, "E3058", {"points": [v(69.92, -6.18) * mm, v(70.23, -6.32) * mm, v(70.54, -6.46) * mm, v(70.86, -6.6) * mm]});
            skFitSpline(sketch, "E3059", {"points": [v(70.86, -6.6) * mm, v(71.52, -6.85) * mm, v(72.18, -7.1) * mm, v(72.85, -7.35) * mm]});
            skFitSpline(sketch, "E3060", {"points": [v(72.85, -7.35) * mm, v(73.35, -7.54) * mm, v(73.85, -7.71) * mm, v(74.36, -7.89) * mm]});
            skFitSpline(sketch, "E3061", {"points": [v(74.36, -7.89) * mm, v(74.49, -7.93) * mm, v(74.61, -8) * mm, v(74.8, -7.98) * mm]});
            skFitSpline(sketch, "E3062", {"points": [v(59.3, -2.14) * mm, v(59.24, -2.17) * mm, v(59.17, -2.2) * mm, v(59.1, -2.21) * mm]});
            skFitSpline(sketch, "E3063", {"points": [v(59.1, -2.21) * mm, v(58.94, -2.25) * mm, v(58.84, -2.36) * mm, v(58.77, -2.52) * mm]});
            skFitSpline(sketch, "E3064", {"points": [v(58.77, -2.52) * mm, v(58.57, -2.98) * mm, v(58.33, -3.42) * mm, v(58.13, -3.88) * mm]});
            skFitSpline(sketch, "E3065", {"points": [v(58.13, -3.88) * mm, v(57.83, -4.62) * mm, v(57.55, -5.36) * mm, v(57.27, -6.11) * mm]});
            skFitSpline(sketch, "E3066", {"points": [v(57.27, -6.11) * mm, v(57.08, -6.6) * mm, v(56.91, -7.08) * mm, v(56.75, -7.57) * mm]});
            skFitSpline(sketch, "E3067", {"points": [v(56.75, -7.57) * mm, v(56.7, -7.7) * mm, v(56.62, -7.83) * mm, v(56.66, -8) * mm]});
            skFitSpline(sketch, "E3068", {"points": [v(56.66, -8) * mm, v(56.77, -7.97) * mm, v(56.87, -7.95) * mm, v(56.96, -7.92) * mm]});
            skFitSpline(sketch, "E3069", {"points": [v(56.96, -7.92) * mm, v(57.43, -7.75) * mm, v(57.9, -7.59) * mm, v(58.36, -7.42) * mm]});
            skFitSpline(sketch, "E3070", {"points": [v(58.36, -7.42) * mm, v(58.7, -7.3) * mm, v(59.05, -7.17) * mm, v(59.39, -7.04) * mm]});
            skFitSpline(sketch, "E3071", {"points": [v(59.39, -7.04) * mm, v(60.03, -6.79) * mm, v(60.66, -6.54) * mm, v(61.3, -6.27) * mm]});
            skFitSpline(sketch, "E3072", {"points": [v(61.3, -6.27) * mm, v(61.6, -6.14) * mm, v(61.9, -5.96) * mm, v(62.21, -5.8) * mm]});
            skFitSpline(sketch, "E3073", {"points": [v(62.21, -5.8) * mm, v(62.26, -5.77) * mm, v(62.32, -5.73) * mm, v(62.35, -5.68) * mm]});
            skFitSpline(sketch, "E3074", {"points": [v(62.35, -5.68) * mm, v(62.4, -5.57) * mm, v(62.44, -5.45) * mm, v(62.5, -5.3) * mm]});
            skFitSpline(sketch, "E3075", {"points": [v(62.5, -5.3) * mm, v(62.42, -5.32) * mm, v(62.37, -5.32) * mm, v(62.31, -5.33) * mm]});
            skFitSpline(sketch, "E3076", {"points": [v(62.31, -5.33) * mm, v(62.17, -5.35) * mm, v(62.02, -5.39) * mm, v(61.87, -5.4) * mm]});
            skFitSpline(sketch, "E3077", {"points": [v(61.87, -5.4) * mm, v(61.48, -5.43) * mm, v(61.1, -5.5) * mm, v(60.74, -5.59) * mm]});
            skFitSpline(sketch, "E3078", {"points": [v(60.74, -5.59) * mm, v(60.38, -5.69) * mm, v(60, -5.75) * mm, v(59.63, -5.8) * mm]});
            skFitSpline(sketch, "E3079", {"points": [v(59.63, -5.8) * mm, v(59.43, -5.84) * mm, v(59.25, -5.78) * mm, v(59.13, -5.6) * mm]});
            skFitSpline(sketch, "E3080", {"points": [v(59.13, -5.6) * mm, v(59.1, -5.57) * mm, v(59.08, -5.54) * mm, v(59.05, -5.52) * mm]});
            skFitSpline(sketch, "E3081", {"points": [v(59.05, -5.52) * mm, v(58.83, -5.37) * mm, v(58.78, -5.15) * mm, v(58.83, -4.9) * mm]});
            skFitSpline(sketch, "E3082", {"points": [v(58.83, -4.9) * mm, v(58.92, -4.5) * mm, v(59, -4.1) * mm, v(59.1, -3.7) * mm]});
            skFitSpline(sketch, "E3083", {"points": [v(59.1, -3.7) * mm, v(59.12, -3.54) * mm, v(59.16, -3.4) * mm, v(59.18, -3.25) * mm]});
            skFitSpline(sketch, "E3084", {"points": [v(59.18, -3.25) * mm, v(59.23, -2.9) * mm, v(59.28, -2.57) * mm, v(59.32, -2.23) * mm]});
            skFitSpline(sketch, "E3085", {"points": [v(59.32, -2.23) * mm, v(59.33, -2.2) * mm, v(59.31, -2.18) * mm, v(59.3, -2.14) * mm]});
            skFitSpline(sketch, "E3086", {"points": [v(52.85, 1.06) * mm, v(53.18, 0.9) * mm, v(53.47, 0.75) * mm, v(53.76, 0.6) * mm]});
            skFitSpline(sketch, "E3087", {"points": [v(53.76, 0.6) * mm, v(54.3, 0.36) * mm, v(54.84, 0.13) * mm, v(55.37, -0.13) * mm]});
            skFitSpline(sketch, "E3088", {"points": [v(55.37, -0.13) * mm, v(56.3, -0.6) * mm, v(57.25, -0.96) * mm, v(58.23, -1.28) * mm]});
            skFitSpline(sketch, "E3089", {"points": [v(58.23, -1.28) * mm, v(58.5, -1.37) * mm, v(58.68, -1.3) * mm, v(58.9, -1.17) * mm]});
            skFitSpline(sketch, "E3090", {"points": [v(58.9, -1.17) * mm, v(58.87, -1.14) * mm, v(58.85, -1.1) * mm, v(58.83, -1.09) * mm]});
            skFitSpline(sketch, "E3091", {"points": [v(58.83, -1.09) * mm, v(58.62, -0.93) * mm, v(58.4, -0.76) * mm, v(58.18, -0.6) * mm]});
            skFitSpline(sketch, "E3092", {"points": [v(58.18, -0.6) * mm, v(58.03, -0.49) * mm, v(57.88, -0.37) * mm, v(57.72, -0.27) * mm]});
            skFitSpline(sketch, "E3093", {"points": [v(57.72, -0.27) * mm, v(57.4, -0.06) * mm, v(57.08, 0.14) * mm, v(56.76, 0.33) * mm]});
            skFitSpline(sketch, "E3094", {"points": [v(56.76, 0.33) * mm, v(56.47, 0.51) * mm, v(56.25, 0.72) * mm, v(56.33, 1.1) * mm]});
            skFitSpline(sketch, "E3095", {"points": [v(56.33, 1.1) * mm, v(56.34, 1.12) * mm, v(56.33, 1.14) * mm, v(56.33, 1.15) * mm]});
            skFitSpline(sketch, "E3096", {"points": [v(56.33, 1.15) * mm, v(56.3, 1.36) * mm, v(56.38, 1.54) * mm, v(56.55, 1.65) * mm]});
            skFitSpline(sketch, "E3097", {"points": [v(56.55, 1.65) * mm, v(56.84, 1.86) * mm, v(57.14, 2.06) * mm, v(57.44, 2.26) * mm]});
            skFitSpline(sketch, "E3098", {"points": [v(57.44, 2.26) * mm, v(57.69, 2.43) * mm, v(57.95, 2.59) * mm, v(58.2, 2.76) * mm]});
            skFitSpline(sketch, "E3099", {"points": [v(58.2, 2.76) * mm, v(58.4, 2.9) * mm, v(58.62, 3.07) * mm, v(58.82, 3.23) * mm]});
            skFitSpline(sketch, "E3100", {"points": [v(58.82, 3.23) * mm, v(58.85, 3.26) * mm, v(58.87, 3.29) * mm, v(58.9, 3.32) * mm]});
            skFitSpline(sketch, "E3101", {"points": [v(58.9, 3.32) * mm, v(58.53, 3.52) * mm, v(58.53, 3.53) * mm, v(58.2, 3.41) * mm]});
            skFitSpline(sketch, "E3102", {"points": [v(58.2, 3.41) * mm, v(57.73, 3.25) * mm, v(57.27, 3.1) * mm, v(56.82, 2.91) * mm]});
            skFitSpline(sketch, "E3103", {"points": [v(56.82, 2.91) * mm, v(56.09, 2.6) * mm, v(55.36, 2.28) * mm, v(54.63, 1.95) * mm]});
            skFitSpline(sketch, "E3104", {"points": [v(54.63, 1.95) * mm, v(54.4, 1.85) * mm, v(54.2, 1.72) * mm, v(53.97, 1.62) * mm]});
            skFitSpline(sketch, "E3105", {"points": [v(53.97, 1.62) * mm, v(53.67, 1.47) * mm, v(53.36, 1.34) * mm, v(53.06, 1.2) * mm]});
            skFitSpline(sketch, "E3106", {"points": [v(53.06, 1.2) * mm, v(53, 1.17) * mm, v(52.95, 1.13) * mm, v(52.85, 1.06) * mm]});
            skFitSpline(sketch, "E3107", {"points": [v(78.57, 1.08) * mm, v(78.23, 1.25) * mm, v(77.94, 1.4) * mm, v(77.65, 1.54) * mm]});
            skFitSpline(sketch, "E3108", {"points": [v(77.65, 1.54) * mm, v(77.11, 1.8) * mm, v(76.57, 2.02) * mm, v(76.04, 2.28) * mm]});
            skFitSpline(sketch, "E3109", {"points": [v(76.04, 2.28) * mm, v(75.1, 2.74) * mm, v(74.14, 3.12) * mm, v(73.16, 3.44) * mm]});
            skFitSpline(sketch, "E3110", {"points": [v(73.16, 3.44) * mm, v(72.9, 3.52) * mm, v(72.72, 3.44) * mm, v(72.48, 3.3) * mm]});
            skFitSpline(sketch, "E3111", {"points": [v(72.48, 3.3) * mm, v(72.53, 3.26) * mm, v(72.57, 3.24) * mm, v(72.6, 3.22) * mm]});
            skFitSpline(sketch, "E3112", {"points": [v(72.6, 3.22) * mm, v(72.8, 3.08) * mm, v(72.98, 2.93) * mm, v(73.17, 2.79) * mm]});
            skFitSpline(sketch, "E3113", {"points": [v(73.17, 2.79) * mm, v(73.36, 2.65) * mm, v(73.55, 2.51) * mm, v(73.74, 2.39) * mm]});
            skFitSpline(sketch, "E3114", {"points": [v(73.74, 2.39) * mm, v(74.05, 2.18) * mm, v(74.36, 1.99) * mm, v(74.67, 1.8) * mm]});
            skFitSpline(sketch, "E3115", {"points": [v(74.67, 1.8) * mm, v(74.95, 1.62) * mm, v(75.14, 1.41) * mm, v(75.07, 1.05) * mm]});
            skFitSpline(sketch, "E3116", {"points": [v(75.07, 1.05) * mm, v(75.07, 1.02) * mm, v(75.07, 0.99) * mm, v(75.08, 0.96) * mm]});
            skFitSpline(sketch, "E3117", {"points": [v(75.08, 0.96) * mm, v(75.1, 0.77) * mm, v(75.02, 0.6) * mm, v(74.87, 0.5) * mm]});
            skFitSpline(sketch, "E3118", {"points": [v(74.87, 0.5) * mm, v(74.57, 0.29) * mm, v(74.26, 0.09) * mm, v(73.96, -0.12) * mm]});
            skFitSpline(sketch, "E3119", {"points": [v(73.96, -0.12) * mm, v(73.71, -0.28) * mm, v(73.46, -0.44) * mm, v(73.22, -0.6) * mm]});
            skFitSpline(sketch, "E3120", {"points": [v(73.22, -0.6) * mm, v(73, -0.76) * mm, v(72.8, -0.92) * mm, v(72.59, -1.08) * mm]});
            skFitSpline(sketch, "E3121", {"points": [v(72.59, -1.08) * mm, v(72.56, -1.1) * mm, v(72.54, -1.14) * mm, v(72.5, -1.18) * mm]});
            skFitSpline(sketch, "E3122", {"points": [v(72.5, -1.18) * mm, v(72.6, -1.22) * mm, v(72.69, -1.25) * mm, v(72.76, -1.3) * mm]});
            skFitSpline(sketch, "E3123", {"points": [v(72.76, -1.3) * mm, v(72.87, -1.36) * mm, v(72.97, -1.34) * mm, v(73.08, -1.3) * mm]});
            skFitSpline(sketch, "E3124", {"points": [v(73.08, -1.3) * mm, v(73.52, -1.17) * mm, v(73.96, -1.01) * mm, v(74.39, -0.85) * mm]});
            skFitSpline(sketch, "E3125", {"points": [v(74.39, -0.85) * mm, v(75.26, -0.52) * mm, v(76.09, -0.12) * mm, v(76.93, 0.27) * mm]});
            skFitSpline(sketch, "E3126", {"points": [v(76.93, 0.27) * mm, v(77.1, 0.35) * mm, v(77.25, 0.45) * mm, v(77.41, 0.53) * mm]});
            skFitSpline(sketch, "E3127", {"points": [v(77.41, 0.53) * mm, v(77.71, 0.66) * mm, v(78.01, 0.8) * mm, v(78.3, 0.93) * mm]});
            skFitSpline(sketch, "E3128", {"points": [v(78.3, 0.93) * mm, v(78.38, 0.96) * mm, v(78.44, 1) * mm, v(78.57, 1.08) * mm]});
            skFitSpline(sketch, "E3129", {"points": [v(65.69, 13.93) * mm, v(65.6, 13.74) * mm, v(65.52, 13.6) * mm, v(65.46, 13.46) * mm]});
            skFitSpline(sketch, "E3130", {"points": [v(65.46, 13.46) * mm, v(65.33, 13.18) * mm, v(65.21, 12.9) * mm, v(65.08, 12.63) * mm]});
            skFitSpline(sketch, "E3131", {"points": [v(65.08, 12.63) * mm, v(64.8, 12.05) * mm, v(64.5, 11.48) * mm, v(64.24, 10.89) * mm]});
            skFitSpline(sketch, "E3132", {"points": [v(64.24, 10.89) * mm, v(63.9, 10.1) * mm, v(63.58, 9.33) * mm, v(63.34, 8.52) * mm]});
            skFitSpline(sketch, "E3133", {"points": [v(63.34, 8.52) * mm, v(63.26, 8.25) * mm, v(63.35, 8.09) * mm, v(63.46, 7.88) * mm]});
            skFitSpline(sketch, "E3134", {"points": [v(63.46, 7.88) * mm, v(63.7, 8.17) * mm, v(63.9, 8.43) * mm, v(64.11, 8.7) * mm]});
            skFitSpline(sketch, "E3135", {"points": [v(64.11, 8.7) * mm, v(64.21, 8.84) * mm, v(64.3, 8.98) * mm, v(64.4, 9.12) * mm]});
            skFitSpline(sketch, "E3136", {"points": [v(64.4, 9.12) * mm, v(64.6, 9.43) * mm, v(64.8, 9.75) * mm, v(65, 10.07) * mm]});
            skFitSpline(sketch, "E3137", {"points": [v(65, 10.07) * mm, v(65.16, 10.33) * mm, v(65.37, 10.5) * mm, v(65.7, 10.44) * mm]});
            skFitSpline(sketch, "E3138", {"points": [v(65.7, 10.44) * mm, v(65.74, 10.43) * mm, v(65.77, 10.44) * mm, v(65.8, 10.45) * mm]});
            skFitSpline(sketch, "E3139", {"points": [v(65.8, 10.45) * mm, v(66, 10.47) * mm, v(66.17, 10.4) * mm, v(66.28, 10.23) * mm]});
            skFitSpline(sketch, "E3140", {"points": [v(66.28, 10.23) * mm, v(66.5, 9.93) * mm, v(66.7, 9.62) * mm, v(66.9, 9.32) * mm]});
            skFitSpline(sketch, "E3141", {"points": [v(66.9, 9.32) * mm, v(67.07, 9.06) * mm, v(67.24, 8.8) * mm, v(67.42, 8.54) * mm]});
            skFitSpline(sketch, "E3142", {"points": [v(67.42, 8.54) * mm, v(67.55, 8.35) * mm, v(67.7, 8.16) * mm, v(67.85, 7.97) * mm]});
            skFitSpline(sketch, "E3143", {"points": [v(67.85, 7.97) * mm, v(67.88, 7.94) * mm, v(67.92, 7.92) * mm, v(67.96, 7.88) * mm]});
            skFitSpline(sketch, "E3144", {"points": [v(67.96, 7.88) * mm, v(68.01, 8) * mm, v(68.06, 8.09) * mm, v(68.09, 8.18) * mm]});
            skFitSpline(sketch, "E3145", {"points": [v(68.09, 8.18) * mm, v(68.1, 8.26) * mm, v(68.12, 8.34) * mm, v(68.1, 8.41) * mm]});
            skFitSpline(sketch, "E3146", {"points": [v(68.1, 8.41) * mm, v(68, 8.7) * mm, v(67.92, 9) * mm, v(67.82, 9.28) * mm]});
            skFitSpline(sketch, "E3147", {"points": [v(67.82, 9.28) * mm, v(67.73, 9.52) * mm, v(67.64, 9.75) * mm, v(67.53, 9.99) * mm]});
            skFitSpline(sketch, "E3148", {"points": [v(67.53, 9.99) * mm, v(67.23, 10.7) * mm, v(66.91, 11.4) * mm, v(66.6, 12.11) * mm]});
            skFitSpline(sketch, "E3149", {"points": [v(66.6, 12.11) * mm, v(66.48, 12.36) * mm, v(66.35, 12.6) * mm, v(66.24, 12.84) * mm]});
            skFitSpline(sketch, "E3150", {"points": [v(66.24, 12.84) * mm, v(66.1, 13.14) * mm, v(65.95, 13.45) * mm, v(65.81, 13.75) * mm]});
            skFitSpline(sketch, "E3151", {"points": [v(65.81, 13.75) * mm, v(65.79, 13.8) * mm, v(65.75, 13.84) * mm, v(65.69, 13.93) * mm]});
            skFitSpline(sketch, "E3152", {"points": [v(56.62, 10.16) * mm, v(56.66, 10.01) * mm, v(56.68, 9.91) * mm, v(56.71, 9.82) * mm]});
            skFitSpline(sketch, "E3153", {"points": [v(56.71, 9.82) * mm, v(56.87, 9.35) * mm, v(57.04, 8.89) * mm, v(57.2, 8.42) * mm]});
            skFitSpline(sketch, "E3154", {"points": [v(57.2, 8.42) * mm, v(57.32, 8.12) * mm, v(57.45, 7.82) * mm, v(57.55, 7.5) * mm]});
            skFitSpline(sketch, "E3155", {"points": [v(57.55, 7.5) * mm, v(57.89, 6.48) * mm, v(58.33, 5.5) * mm, v(58.84, 4.55) * mm]});
            skFitSpline(sketch, "E3156", {"points": [v(58.84, 4.55) * mm, v(58.86, 4.5) * mm, v(58.9, 4.45) * mm, v(58.95, 4.43) * mm]});
            skFitSpline(sketch, "E3157", {"points": [v(58.95, 4.43) * mm, v(59.06, 4.38) * mm, v(59.18, 4.34) * mm, v(59.3, 4.29) * mm]});
            skFitSpline(sketch, "E3158", {"points": [v(59.3, 4.29) * mm, v(59.31, 4.34) * mm, v(59.32, 4.37) * mm, v(59.32, 4.4) * mm]});
            skFitSpline(sketch, "E3159", {"points": [v(59.32, 4.4) * mm, v(59.3, 4.6) * mm, v(59.26, 4.82) * mm, v(59.23, 5.03) * mm]});
            skFitSpline(sketch, "E3160", {"points": [v(59.23, 5.03) * mm, v(59.18, 5.34) * mm, v(59.12, 5.64) * mm, v(59.06, 5.95) * mm]});
            skFitSpline(sketch, "E3161", {"points": [v(59.06, 5.95) * mm, v(58.98, 6.34) * mm, v(58.9, 6.73) * mm, v(58.82, 7.12) * mm]});
            skFitSpline(sketch, "E3162", {"points": [v(58.82, 7.12) * mm, v(58.78, 7.33) * mm, v(58.84, 7.52) * mm, v(59.02, 7.65) * mm]});
            skFitSpline(sketch, "E3163", {"points": [v(59.02, 7.65) * mm, v(59.05, 7.67) * mm, v(59.09, 7.7) * mm, v(59.1, 7.73) * mm]});
            skFitSpline(sketch, "E3164", {"points": [v(59.1, 7.73) * mm, v(59.25, 7.94) * mm, v(59.45, 7.99) * mm, v(59.68, 7.95) * mm]});
            skFitSpline(sketch, "E3165", {"points": [v(59.68, 7.95) * mm, v(60.02, 7.9) * mm, v(60.37, 7.82) * mm, v(60.71, 7.75) * mm]});
            skFitSpline(sketch, "E3166", {"points": [v(60.71, 7.75) * mm, v(61.02, 7.69) * mm, v(61.33, 7.62) * mm, v(61.65, 7.56) * mm]});
            skFitSpline(sketch, "E3167", {"points": [v(61.65, 7.56) * mm, v(61.83, 7.53) * mm, v(62.03, 7.52) * mm, v(62.22, 7.5) * mm]});
            skFitSpline(sketch, "E3168", {"points": [v(62.22, 7.5) * mm, v(62.3, 7.5) * mm, v(62.38, 7.47) * mm, v(62.5, 7.45) * mm]});
            skFitSpline(sketch, "E3169", {"points": [v(62.5, 7.45) * mm, v(62.47, 7.53) * mm, v(62.45, 7.58) * mm, v(62.43, 7.63) * mm]});
            skFitSpline(sketch, "E3170", {"points": [v(62.43, 7.63) * mm, v(62.38, 7.81) * mm, v(62.28, 7.94) * mm, v(62.09, 8.02) * mm]});
            skFitSpline(sketch, "E3171", {"points": [v(62.09, 8.02) * mm, v(61.58, 8.24) * mm, v(61.09, 8.5) * mm, v(60.57, 8.72) * mm]});
            skFitSpline(sketch, "E3172", {"points": [v(60.57, 8.72) * mm, v(59.9, 9) * mm, v(59.2, 9.26) * mm, v(58.52, 9.51) * mm]});
            skFitSpline(sketch, "E3173", {"points": [v(58.52, 9.51) * mm, v(58.28, 9.6) * mm, v(58.03, 9.67) * mm, v(57.8, 9.75) * mm]});
            skFitSpline(sketch, "E3174", {"points": [v(57.8, 9.75) * mm, v(57.48, 9.87) * mm, v(57.17, 9.99) * mm, v(56.85, 10.1) * mm]});
            skFitSpline(sketch, "E3175", {"points": [v(56.85, 10.1) * mm, v(56.8, 10.12) * mm, v(56.73, 10.13) * mm, v(56.62, 10.16) * mm]});
            skFitSpline(sketch, "E3176", {"points": [v(74.79, 10.17) * mm, v(74.63, 10.12) * mm, v(74.52, 10.1) * mm, v(74.4, 10.05) * mm]});
            skFitSpline(sketch, "E3177", {"points": [v(74.4, 10.05) * mm, v(73.94, 9.89) * mm, v(73.47, 9.72) * mm, v(73.01, 9.56) * mm]});
            skFitSpline(sketch, "E3178", {"points": [v(73.01, 9.56) * mm, v(72.72, 9.45) * mm, v(72.43, 9.33) * mm, v(72.14, 9.23) * mm]});
            skFitSpline(sketch, "E3179", {"points": [v(72.14, 9.23) * mm, v(71.11, 8.89) * mm, v(70.13, 8.46) * mm, v(69.18, 7.94) * mm]});
            skFitSpline(sketch, "E3180", {"points": [v(69.18, 7.94) * mm, v(69.14, 7.92) * mm, v(69.08, 7.88) * mm, v(69.06, 7.84) * mm]});
            skFitSpline(sketch, "E3181", {"points": [v(69.06, 7.84) * mm, v(69, 7.73) * mm, v(68.97, 7.6) * mm, v(68.91, 7.46) * mm]});
            skFitSpline(sketch, "E3182", {"points": [v(68.91, 7.46) * mm, v(68.99, 7.47) * mm, v(69.04, 7.47) * mm, v(69.1, 7.47) * mm]});
            skFitSpline(sketch, "E3183", {"points": [v(69.1, 7.47) * mm, v(69.25, 7.5) * mm, v(69.4, 7.53) * mm, v(69.56, 7.55) * mm]});
            skFitSpline(sketch, "E3184", {"points": [v(69.56, 7.55) * mm, v(69.85, 7.6) * mm, v(70.15, 7.63) * mm, v(70.44, 7.68) * mm]});
            skFitSpline(sketch, "E3185", {"points": [v(70.44, 7.68) * mm, v(70.8, 7.75) * mm, v(71.17, 7.85) * mm, v(71.53, 7.92) * mm]});
            skFitSpline(sketch, "E3186", {"points": [v(71.53, 7.92) * mm, v(71.84, 7.99) * mm, v(72.14, 8) * mm, v(72.34, 7.68) * mm]});
            skFitSpline(sketch, "E3187", {"points": [v(72.34, 7.68) * mm, v(72.35, 7.67) * mm, v(72.37, 7.66) * mm, v(72.38, 7.65) * mm]});
            skFitSpline(sketch, "E3188", {"points": [v(72.38, 7.65) * mm, v(72.55, 7.54) * mm, v(72.6, 7.37) * mm, v(72.58, 7.17) * mm]});
            skFitSpline(sketch, "E3189", {"points": [v(72.58, 7.17) * mm, v(72.55, 6.9) * mm, v(72.5, 6.64) * mm, v(72.45, 6.37) * mm]});
            skFitSpline(sketch, "E3190", {"points": [v(72.45, 6.37) * mm, v(72.38, 6.02) * mm, v(72.29, 5.67) * mm, v(72.22, 5.32) * mm]});
            skFitSpline(sketch, "E3191", {"points": [v(72.22, 5.32) * mm, v(72.18, 5.09) * mm, v(72.16, 4.85) * mm, v(72.14, 4.61) * mm]});
            skFitSpline(sketch, "E3192", {"points": [v(72.14, 4.61) * mm, v(72.12, 4.51) * mm, v(72.1, 4.41) * mm, v(72.08, 4.28) * mm]});
            skFitSpline(sketch, "E3193", {"points": [v(72.08, 4.28) * mm, v(72.23, 4.34) * mm, v(72.35, 4.38) * mm, v(72.46, 4.43) * mm]});
            skFitSpline(sketch, "E3194", {"points": [v(72.46, 4.43) * mm, v(72.5, 4.45) * mm, v(72.55, 4.5) * mm, v(72.57, 4.55) * mm]});
            skFitSpline(sketch, "E3195", {"points": [v(72.57, 4.55) * mm, v(72.71, 4.82) * mm, v(72.86, 5.08) * mm, v(72.99, 5.36) * mm]});
            skFitSpline(sketch, "E3196", {"points": [v(72.99, 5.36) * mm, v(73.1, 5.6) * mm, v(73.22, 5.87) * mm, v(73.32, 6.12) * mm]});
            skFitSpline(sketch, "E3197", {"points": [v(73.32, 6.12) * mm, v(73.6, 6.82) * mm, v(73.86, 7.52) * mm, v(74.13, 8.22) * mm]});
            skFitSpline(sketch, "E3198", {"points": [v(74.13, 8.22) * mm, v(74.23, 8.47) * mm, v(74.3, 8.74) * mm, v(74.39, 9) * mm]});
            skFitSpline(sketch, "E3199", {"points": [v(74.39, 9) * mm, v(74.5, 9.3) * mm, v(74.62, 9.62) * mm, v(74.73, 9.93) * mm]});
            skFitSpline(sketch, "E3200", {"points": [v(74.73, 9.93) * mm, v(74.75, 9.99) * mm, v(74.76, 10.05) * mm, v(74.79, 10.17) * mm]});
            skFitSpline(sketch, "E3201", {"points": [v(61.7, -7.17) * mm, v(61.53, -7.24) * mm, v(61.37, -7.3) * mm, v(61.2, -7.36) * mm]});
            skFitSpline(sketch, "E3202", {"points": [v(61.2, -7.36) * mm, v(60.67, -7.57) * mm, v(60.14, -7.79) * mm, v(59.6, -8) * mm]});
            skFitSpline(sketch, "E3203", {"points": [v(59.6, -8) * mm, v(59.15, -8.16) * mm, v(58.7, -8.31) * mm, v(58.25, -8.47) * mm]});
            skFitSpline(sketch, "E3204", {"points": [v(58.25, -8.47) * mm, v(58.2, -8.5) * mm, v(58.15, -8.52) * mm, v(58.1, -8.56) * mm]});
            skFitSpline(sketch, "E3205", {"points": [v(58.1, -8.56) * mm, v(57.97, -8.7) * mm, v(57.8, -8.77) * mm, v(57.6, -8.82) * mm]});
            skFitSpline(sketch, "E3206", {"points": [v(57.6, -8.82) * mm, v(57.23, -8.9) * mm, v(56.85, -9) * mm, v(56.47, -9.1) * mm]});
            skFitSpline(sketch, "E3207", {"points": [v(56.47, -9.1) * mm, v(56.32, -9.13) * mm, v(56.24, -9.2) * mm, v(56.2, -9.35) * mm]});
            skFitSpline(sketch, "E3208", {"points": [v(56.2, -9.35) * mm, v(56.1, -9.9) * mm, v(55.97, -10.43) * mm, v(55.84, -10.96) * mm]});
            skFitSpline(sketch, "E3209", {"points": [v(55.84, -10.96) * mm, v(55.7, -11.49) * mm, v(55.55, -12) * mm, v(55.4, -12.53) * mm]});
            skFitSpline(sketch, "E3210", {"points": [v(55.4, -12.53) * mm, v(55.4, -12.56) * mm, v(55.39, -12.6) * mm, v(55.38, -12.62) * mm]});
            skFitSpline(sketch, "E3211", {"points": [v(55.38, -12.62) * mm, v(55.28, -12.88) * mm, v(55.03, -13.02) * mm, v(54.81, -12.97) * mm]});
            skFitSpline(sketch, "E3212", {"points": [v(54.81, -12.97) * mm, v(54.54, -12.9) * mm, v(54.38, -12.65) * mm, v(54.45, -12.36) * mm]});
            skFitSpline(sketch, "E3213", {"points": [v(54.45, -12.36) * mm, v(54.49, -12.15) * mm, v(54.54, -11.94) * mm, v(54.6, -11.73) * mm]});
            skFitSpline(sketch, "E3214", {"points": [v(54.6, -11.73) * mm, v(54.81, -11.04) * mm, v(55.01, -10.35) * mm, v(55.14, -9.65) * mm]});
            skFitSpline(sketch, "E3215", {"points": [v(55.14, -9.65) * mm, v(55.15, -9.6) * mm, v(55.15, -9.55) * mm, v(55.16, -9.48) * mm]});
            skFitSpline(sketch, "E3216", {"points": [v(55.16, -9.48) * mm, v(55.09, -9.48) * mm, v(55.02, -9.48) * mm, v(54.95, -9.5) * mm]});
            skFitSpline(sketch, "E3217", {"points": [v(54.95, -9.5) * mm, v(54.33, -9.65) * mm, v(53.7, -9.8) * mm, v(53.07, -9.97) * mm]});
            skFitSpline(sketch, "E3218", {"points": [v(53.07, -9.97) * mm, v(52.8, -10.04) * mm, v(52.55, -10.12) * mm, v(52.29, -10.18) * mm]});
            skFitSpline(sketch, "E3219", {"points": [v(52.29, -10.18) * mm, v(52, -10.25) * mm, v(51.75, -10.1) * mm, v(51.67, -9.83) * mm]});
            skFitSpline(sketch, "E3220", {"points": [v(51.67, -9.83) * mm, v(51.6, -9.6) * mm, v(51.75, -9.34) * mm, v(52.01, -9.25) * mm]});
            skFitSpline(sketch, "E3221", {"points": [v(52.01, -9.25) * mm, v(52.37, -9.14) * mm, v(52.73, -9.04) * mm, v(53.1, -8.95) * mm]});
            skFitSpline(sketch, "E3222", {"points": [v(53.1, -8.95) * mm, v(53.82, -8.77) * mm, v(54.54, -8.6) * mm, v(55.26, -8.42) * mm]});
            skFitSpline(sketch, "E3223", {"points": [v(55.26, -8.42) * mm, v(55.33, -8.4) * mm, v(55.4, -8.38) * mm, v(55.5, -8.36) * mm]});
            skFitSpline(sketch, "E3224", {"points": [v(55.5, -8.36) * mm, v(55.59, -7.97) * mm, v(55.69, -7.57) * mm, v(55.78, -7.18) * mm]});
            skFitSpline(sketch, "E3225", {"points": [v(55.78, -7.18) * mm, v(55.83, -6.93) * mm, v(55.89, -6.68) * mm, v(56.1, -6.5) * mm]});
            skFitSpline(sketch, "E3226", {"points": [v(56.1, -6.5) * mm, v(56.14, -6.45) * mm, v(56.15, -6.37) * mm, v(56.18, -6.3) * mm]});
            skFitSpline(sketch, "E3227", {"points": [v(56.18, -6.3) * mm, v(56.32, -5.91) * mm, v(56.45, -5.52) * mm, v(56.6, -5.13) * mm]});
            skFitSpline(sketch, "E3228", {"points": [v(56.6, -5.13) * mm, v(56.87, -4.4) * mm, v(57.15, -3.67) * mm, v(57.44, -2.94) * mm]});
            skFitSpline(sketch, "E3229", {"points": [v(57.44, -2.94) * mm, v(57.42, -2.93) * mm, v(57.4, -2.92) * mm, v(57.38, -2.93) * mm]});
            skFitSpline(sketch, "E3230", {"points": [v(57.38, -2.93) * mm, v(56.82, -3.16) * mm, v(56.27, -3.4) * mm, v(55.7, -3.64) * mm]});
            skFitSpline(sketch, "E3231", {"points": [v(55.7, -3.64) * mm, v(55.62, -3.67) * mm, v(55.6, -3.74) * mm, v(55.57, -3.82) * mm]});
            skFitSpline(sketch, "E3232", {"points": [v(55.57, -3.82) * mm, v(55.35, -4.33) * mm, v(55.2, -4.87) * mm, v(55.07, -5.41) * mm]});
            skFitSpline(sketch, "E3233", {"points": [v(55.07, -5.41) * mm, v(55.04, -5.54) * mm, v(55, -5.68) * mm, v(54.94, -5.8) * mm]});
            skFitSpline(sketch, "E3234", {"points": [v(54.94, -5.8) * mm, v(54.82, -6.05) * mm, v(54.57, -6.15) * mm, v(54.32, -6.06) * mm]});
            skFitSpline(sketch, "E3235", {"points": [v(54.32, -6.06) * mm, v(54.1, -5.97) * mm, v(53.97, -5.72) * mm, v(54.04, -5.47) * mm]});
            skFitSpline(sketch, "E3236", {"points": [v(54.04, -5.47) * mm, v(54.13, -5.11) * mm, v(54.23, -4.76) * mm, v(54.32, -4.4) * mm]});
            skFitSpline(sketch, "E3237", {"points": [v(54.32, -4.4) * mm, v(54.34, -4.35) * mm, v(54.35, -4.3) * mm, v(54.37, -4.2) * mm]});
            skFitSpline(sketch, "E3238", {"points": [v(54.37, -4.2) * mm, v(54.07, -4.33) * mm, v(53.8, -4.44) * mm, v(53.59, -4.53) * mm]});
            skFitSpline(sketch, "E3239", {"points": [v(53.59, -4.53) * mm, v(53.5, -4.82) * mm, v(53.44, -5.07) * mm, v(53.35, -5.32) * mm]});
            skFitSpline(sketch, "E3240", {"points": [v(53.35, -5.32) * mm, v(53.25, -5.6) * mm, v(53.13, -5.87) * mm, v(53.03, -6.15) * mm]});
            skFitSpline(sketch, "E3241", {"points": [v(53.03, -6.15) * mm, v(52.95, -6.37) * mm, v(52.88, -6.6) * mm, v(52.8, -6.83) * mm]});
            skFitSpline(sketch, "E3242", {"points": [v(52.8, -6.83) * mm, v(52.74, -7.05) * mm, v(52.55, -7.2) * mm, v(52.34, -7.22) * mm]});
            skFitSpline(sketch, "E3243", {"points": [v(52.34, -7.22) * mm, v(52.16, -7.23) * mm, v(51.94, -7.12) * mm, v(51.89, -6.93) * mm]});
            skFitSpline(sketch, "E3244", {"points": [v(51.89, -6.93) * mm, v(51.85, -6.8) * mm, v(51.84, -6.64) * mm, v(51.88, -6.51) * mm]});
            skFitSpline(sketch, "E3245", {"points": [v(51.88, -6.51) * mm, v(51.95, -6.24) * mm, v(52.06, -5.97) * mm, v(52.16, -5.7) * mm]});
            skFitSpline(sketch, "E3246", {"points": [v(52.16, -5.7) * mm, v(52.3, -5.33) * mm, v(52.43, -4.97) * mm, v(52.57, -4.6) * mm]});
            skFitSpline(sketch, "E3247", {"points": [v(52.57, -4.6) * mm, v(52.6, -4.5) * mm, v(52.66, -4.41) * mm, v(52.7, -4.32) * mm]});
            skFitSpline(sketch, "E3248", {"points": [v(52.7, -4.32) * mm, v(52.1, -4.05) * mm, v(51.5, -3.8) * mm, v(50.9, -3.52) * mm]});
            skFitSpline(sketch, "E3249", {"points": [v(50.9, -3.52) * mm, v(50.74, -3.45) * mm, v(50.59, -3.37) * mm, v(50.44, -3.26) * mm]});
            skFitSpline(sketch, "E3250", {"points": [v(50.44, -3.26) * mm, v(50.28, -3.15) * mm, v(50.2, -2.99) * mm, v(50.24, -2.79) * mm]});
            skFitSpline(sketch, "E3251", {"points": [v(50.24, -2.79) * mm, v(50.29, -2.57) * mm, v(50.42, -2.42) * mm, v(50.64, -2.4) * mm]});
            skFitSpline(sketch, "E3252", {"points": [v(50.64, -2.4) * mm, v(50.75, -2.38) * mm, v(50.88, -2.41) * mm, v(50.99, -2.46) * mm]});
            skFitSpline(sketch, "E3253", {"points": [v(50.99, -2.46) * mm, v(51.47, -2.67) * mm, v(51.94, -2.9) * mm, v(52.42, -3.12) * mm]});
            skFitSpline(sketch, "E3254", {"points": [v(52.42, -3.12) * mm, v(52.66, -3.24) * mm, v(52.92, -3.33) * mm, v(53.12, -3.54) * mm]});
            skFitSpline(sketch, "E3255", {"points": [v(53.12, -3.54) * mm, v(53.39, -3.44) * mm, v(53.66, -3.33) * mm, v(53.95, -3.22) * mm]});
            skFitSpline(sketch, "E3256", {"points": [v(53.95, -3.22) * mm, v(53.89, -3.17) * mm, v(53.84, -3.13) * mm, v(53.8, -3.1) * mm]});
            skFitSpline(sketch, "E3257", {"points": [v(53.8, -3.1) * mm, v(53.48, -2.92) * mm, v(53.17, -2.74) * mm, v(52.86, -2.57) * mm]});
            skFitSpline(sketch, "E3258", {"points": [v(52.86, -2.57) * mm, v(52.6, -2.42) * mm, v(52.5, -2.16) * mm, v(52.62, -1.92) * mm]});
            skFitSpline(sketch, "E3259", {"points": [v(52.62, -1.92) * mm, v(52.73, -1.67) * mm, v(53, -1.57) * mm, v(53.27, -1.7) * mm]});
            skFitSpline(sketch, "E3260", {"points": [v(53.27, -1.7) * mm, v(53.49, -1.79) * mm, v(53.69, -1.92) * mm, v(53.9, -2.03) * mm]});
            skFitSpline(sketch, "E3261", {"points": [v(53.9, -2.03) * mm, v(54.3, -2.24) * mm, v(54.7, -2.44) * mm, v(55.1, -2.64) * mm]});
            skFitSpline(sketch, "E3262", {"points": [v(55.1, -2.64) * mm, v(55.17, -2.68) * mm, v(55.24, -2.69) * mm, v(55.32, -2.65) * mm]});
            skFitSpline(sketch, "E3263", {"points": [v(55.32, -2.65) * mm, v(55.86, -2.43) * mm, v(56.4, -2.22) * mm, v(56.94, -2) * mm]});
            skFitSpline(sketch, "E3264", {"points": [v(56.94, -2) * mm, v(56.97, -1.99) * mm, v(57, -1.97) * mm, v(57.05, -1.94) * mm]});
            skFitSpline(sketch, "E3265", {"points": [v(57.05, -1.94) * mm, v(56.87, -1.85) * mm, v(56.71, -1.78) * mm, v(56.56, -1.7) * mm]});
            skFitSpline(sketch, "E3266", {"points": [v(56.56, -1.7) * mm, v(56.03, -1.48) * mm, v(55.5, -1.26) * mm, v(54.98, -1.02) * mm]});
            skFitSpline(sketch, "E3267", {"points": [v(54.98, -1.02) * mm, v(54.54, -0.82) * mm, v(54.11, -0.61) * mm, v(53.68, -0.4) * mm]});
            skFitSpline(sketch, "E3268", {"points": [v(53.68, -0.4) * mm, v(53.63, -0.38) * mm, v(53.57, -0.36) * mm, v(53.52, -0.37) * mm]});
            skFitSpline(sketch, "E3269", {"points": [v(53.52, -0.37) * mm, v(53.3, -0.38) * mm, v(53.1, -0.27) * mm, v(52.92, -0.16) * mm]});
            skFitSpline(sketch, "E3270", {"points": [v(52.92, -0.16) * mm, v(52.6, 0.04) * mm, v(52.26, 0.24) * mm, v(51.94, 0.44) * mm]});
            skFitSpline(sketch, "E3271", {"points": [v(51.94, 0.44) * mm, v(51.84, 0.5) * mm, v(51.75, 0.5) * mm, v(51.65, 0.44) * mm]});
            skFitSpline(sketch, "E3272", {"points": [v(51.65, 0.44) * mm, v(51.6, 0.4) * mm, v(51.53, 0.37) * mm, v(51.47, 0.33) * mm]});
            skFitSpline(sketch, "E3273", {"points": [v(51.47, 0.33) * mm, v(50.64, -0.25) * mm, v(49.75, -0.71) * mm, v(48.88, -1.22) * mm]});
            skFitSpline(sketch, "E3274", {"points": [v(48.88, -1.22) * mm, v(48.8, -1.26) * mm, v(48.72, -1.3) * mm, v(48.64, -1.33) * mm]});
            skFitSpline(sketch, "E3275", {"points": [v(48.64, -1.33) * mm, v(48.4, -1.42) * mm, v(48.17, -1.32) * mm, v(48.05, -1.1) * mm]});
            skFitSpline(sketch, "E3276", {"points": [v(48.05, -1.1) * mm, v(47.94, -0.89) * mm, v(48, -0.63) * mm, v(48.21, -0.49) * mm]});
            skFitSpline(sketch, "E3277", {"points": [v(48.21, -0.49) * mm, v(48.38, -0.37) * mm, v(48.55, -0.28) * mm, v(48.72, -0.17) * mm]});
            skFitSpline(sketch, "E3278", {"points": [v(48.72, -0.17) * mm, v(49.33, 0.18) * mm, v(49.94, 0.53) * mm, v(50.54, 0.9) * mm]});
            skFitSpline(sketch, "E3279", {"points": [v(50.54, 0.9) * mm, v(50.62, 0.94) * mm, v(50.7, 1) * mm, v(50.8, 1.07) * mm]});
            skFitSpline(sketch, "E3280", {"points": [v(50.8, 1.07) * mm, v(50.73, 1.11) * mm, v(50.7, 1.16) * mm, v(50.64, 1.2) * mm]});
            skFitSpline(sketch, "E3281", {"points": [v(50.64, 1.2) * mm, v(50.07, 1.54) * mm, v(49.49, 1.88) * mm, v(48.91, 2.22) * mm]});
            skFitSpline(sketch, "E3282", {"points": [v(48.91, 2.22) * mm, v(48.69, 2.36) * mm, v(48.45, 2.48) * mm, v(48.23, 2.62) * mm]});
            skFitSpline(sketch, "E3283", {"points": [v(48.23, 2.62) * mm, v(48.04, 2.74) * mm, v(47.97, 2.92) * mm, v(48.01, 3.14) * mm]});
            skFitSpline(sketch, "E3284", {"points": [v(48.01, 3.14) * mm, v(48.05, 3.34) * mm, v(48.2, 3.45) * mm, v(48.39, 3.5) * mm]});
            skFitSpline(sketch, "E3285", {"points": [v(48.39, 3.5) * mm, v(48.53, 3.55) * mm, v(48.66, 3.5) * mm, v(48.77, 3.43) * mm]});
            skFitSpline(sketch, "E3286", {"points": [v(48.77, 3.43) * mm, v(49.57, 2.94) * mm, v(50.42, 2.55) * mm, v(51.19, 2) * mm]});
            skFitSpline(sketch, "E3287", {"points": [v(51.19, 2) * mm, v(51.34, 1.9) * mm, v(51.51, 1.8) * mm, v(51.68, 1.7) * mm]});
            skFitSpline(sketch, "E3288", {"points": [v(51.68, 1.7) * mm, v(51.76, 1.64) * mm, v(51.83, 1.65) * mm, v(51.92, 1.7) * mm]});
            skFitSpline(sketch, "E3289", {"points": [v(51.92, 1.7) * mm, v(52.24, 1.9) * mm, v(52.56, 2.08) * mm, v(52.88, 2.28) * mm]});
            skFitSpline(sketch, "E3290", {"points": [v(52.88, 2.28) * mm, v(53.09, 2.4) * mm, v(53.29, 2.53) * mm, v(53.55, 2.52) * mm]});
            skFitSpline(sketch, "E3291", {"points": [v(53.55, 2.52) * mm, v(53.6, 2.52) * mm, v(53.67, 2.55) * mm, v(53.72, 2.58) * mm]});
            skFitSpline(sketch, "E3292", {"points": [v(53.72, 2.58) * mm, v(54.66, 3.05) * mm, v(55.6, 3.5) * mm, v(56.58, 3.87) * mm]});
            skFitSpline(sketch, "E3293", {"points": [v(56.58, 3.87) * mm, v(56.73, 3.92) * mm, v(56.88, 4) * mm, v(57.05, 4.09) * mm]});
            skFitSpline(sketch, "E3294", {"points": [v(57.05, 4.09) * mm, v(56.99, 4.12) * mm, v(56.96, 4.14) * mm, v(56.92, 4.15) * mm]});
            skFitSpline(sketch, "E3295", {"points": [v(56.92, 4.15) * mm, v(56.4, 4.36) * mm, v(55.87, 4.57) * mm, v(55.35, 4.79) * mm]});
            skFitSpline(sketch, "E3296", {"points": [v(55.35, 4.79) * mm, v(55.25, 4.83) * mm, v(55.17, 4.82) * mm, v(55.08, 4.78) * mm]});
            skFitSpline(sketch, "E3297", {"points": [v(55.08, 4.78) * mm, v(54.59, 4.58) * mm, v(54.13, 4.33) * mm, v(53.68, 4.05) * mm]});
            skFitSpline(sketch, "E3298", {"points": [v(53.68, 4.05) * mm, v(53.55, 3.98) * mm, v(53.43, 3.9) * mm, v(53.3, 3.85) * mm]});
            skFitSpline(sketch, "E3299", {"points": [v(53.3, 3.85) * mm, v(53.01, 3.72) * mm, v(52.74, 3.81) * mm, v(52.62, 4.06) * mm]});
            skFitSpline(sketch, "E3300", {"points": [v(52.62, 4.06) * mm, v(52.5, 4.31) * mm, v(52.6, 4.57) * mm, v(52.88, 4.72) * mm]});
            skFitSpline(sketch, "E3301", {"points": [v(52.88, 4.72) * mm, v(53.2, 4.9) * mm, v(53.53, 5.1) * mm, v(53.85, 5.29) * mm]});
            skFitSpline(sketch, "E3302", {"points": [v(53.85, 5.29) * mm, v(53.88, 5.3) * mm, v(53.9, 5.32) * mm, v(53.95, 5.36) * mm]});
            skFitSpline(sketch, "E3303", {"points": [v(53.95, 5.36) * mm, v(53.67, 5.48) * mm, v(53.4, 5.58) * mm, v(53.13, 5.7) * mm]});
            skFitSpline(sketch, "E3304", {"points": [v(53.13, 5.7) * mm, v(52.85, 5.44) * mm, v(52.5, 5.31) * mm, v(52.16, 5.16) * mm]});
            skFitSpline(sketch, "E3305", {"points": [v(52.16, 5.16) * mm, v(51.77, 4.98) * mm, v(51.38, 4.8) * mm, v(51, 4.6) * mm]});
            skFitSpline(sketch, "E3306", {"points": [v(51, 4.6) * mm, v(50.67, 4.45) * mm, v(50.34, 4.57) * mm, v(50.25, 4.91) * mm]});
            skFitSpline(sketch, "E3307", {"points": [v(50.25, 4.91) * mm, v(50.2, 5.12) * mm, v(50.28, 5.29) * mm, v(50.44, 5.41) * mm]});
            skFitSpline(sketch, "E3308", {"points": [v(50.44, 5.41) * mm, v(50.56, 5.5) * mm, v(50.68, 5.57) * mm, v(50.81, 5.63) * mm]});
            skFitSpline(sketch, "E3309", {"points": [v(50.81, 5.63) * mm, v(51.36, 5.88) * mm, v(51.9, 6.13) * mm, v(52.45, 6.37) * mm]});
            skFitSpline(sketch, "E3310", {"points": [v(52.45, 6.37) * mm, v(52.53, 6.4) * mm, v(52.62, 6.42) * mm, v(52.7, 6.44) * mm]});
            skFitSpline(sketch, "E3311", {"points": [v(52.7, 6.44) * mm, v(52.46, 7.06) * mm, v(52.22, 7.68) * mm, v(51.98, 8.3) * mm]});
            skFitSpline(sketch, "E3312", {"points": [v(51.98, 8.3) * mm, v(51.94, 8.43) * mm, v(51.88, 8.56) * mm, v(51.86, 8.7) * mm]});
            skFitSpline(sketch, "E3313", {"points": [v(51.86, 8.7) * mm, v(51.85, 8.82) * mm, v(51.85, 8.97) * mm, v(51.9, 9.1) * mm]});
            skFitSpline(sketch, "E3314", {"points": [v(51.9, 9.1) * mm, v(51.96, 9.28) * mm, v(52.13, 9.37) * mm, v(52.33, 9.37) * mm]});
            skFitSpline(sketch, "E3315", {"points": [v(52.33, 9.37) * mm, v(52.55, 9.36) * mm, v(52.7, 9.24) * mm, v(52.78, 9.03) * mm]});
            skFitSpline(sketch, "E3316", {"points": [v(52.78, 9.03) * mm, v(53.01, 8.41) * mm, v(53.24, 7.8) * mm, v(53.46, 7.17) * mm]});
            skFitSpline(sketch, "E3317", {"points": [v(53.46, 7.17) * mm, v(53.5, 7.02) * mm, v(53.52, 6.87) * mm, v(53.56, 6.7) * mm]});
            skFitSpline(sketch, "E3318", {"points": [v(53.56, 6.7) * mm, v(53.8, 6.6) * mm, v(54.07, 6.48) * mm, v(54.38, 6.34) * mm]});
            skFitSpline(sketch, "E3319", {"points": [v(54.38, 6.34) * mm, v(54.29, 6.7) * mm, v(54.2, 7.01) * mm, v(54.12, 7.33) * mm]});
            skFitSpline(sketch, "E3320", {"points": [v(54.12, 7.33) * mm, v(54.1, 7.43) * mm, v(54.06, 7.53) * mm, v(54.04, 7.63) * mm]});
            skFitSpline(sketch, "E3321", {"points": [v(54.04, 7.63) * mm, v(53.98, 7.88) * mm, v(54.1, 8.13) * mm, v(54.33, 8.21) * mm]});
            skFitSpline(sketch, "E3322", {"points": [v(54.33, 8.21) * mm, v(54.57, 8.3) * mm, v(54.82, 8.2) * mm, v(54.93, 7.96) * mm]});
            skFitSpline(sketch, "E3323", {"points": [v(54.93, 7.96) * mm, v(55, 7.84) * mm, v(55.03, 7.7) * mm, v(55.07, 7.58) * mm]});
            skFitSpline(sketch, "E3324", {"points": [v(55.07, 7.58) * mm, v(55.2, 7.02) * mm, v(55.35, 6.48) * mm, v(55.58, 5.96) * mm]});
            skFitSpline(sketch, "E3325", {"points": [v(55.58, 5.96) * mm, v(55.6, 5.9) * mm, v(55.64, 5.82) * mm, v(55.7, 5.8) * mm]});
            skFitSpline(sketch, "E3326", {"points": [v(55.7, 5.8) * mm, v(56.27, 5.55) * mm, v(56.84, 5.32) * mm, v(57.45, 5.07) * mm]});
            skFitSpline(sketch, "E3327", {"points": [v(57.45, 5.07) * mm, v(57.4, 5.23) * mm, v(57.36, 5.37) * mm, v(57.3, 5.51) * mm]});
            skFitSpline(sketch, "E3328", {"points": [v(57.3, 5.51) * mm, v(57.04, 6.06) * mm, v(56.8, 6.62) * mm, v(56.62, 7.2) * mm]});
            skFitSpline(sketch, "E3329", {"points": [v(56.62, 7.2) * mm, v(56.49, 7.64) * mm, v(56.32, 8.08) * mm, v(56.16, 8.51) * mm]});
            skFitSpline(sketch, "E3330", {"points": [v(56.16, 8.51) * mm, v(56.14, 8.56) * mm, v(56.12, 8.62) * mm, v(56.08, 8.66) * mm]});
            skFitSpline(sketch, "E3331", {"points": [v(56.08, 8.66) * mm, v(55.9, 8.82) * mm, v(55.84, 9.04) * mm, v(55.79, 9.27) * mm]});
            skFitSpline(sketch, "E3332", {"points": [v(55.79, 9.27) * mm, v(55.7, 9.68) * mm, v(55.6, 10.1) * mm, v(55.5, 10.51) * mm]});
            skFitSpline(sketch, "E3333", {"points": [v(55.5, 10.51) * mm, v(55.28, 10.57) * mm, v(55.08, 10.63) * mm, v(54.88, 10.67) * mm]});
            skFitSpline(sketch, "E3334", {"points": [v(54.88, 10.67) * mm, v(54.18, 10.79) * mm, v(53.5, 10.98) * mm, v(52.83, 11.17) * mm]});
            skFitSpline(sketch, "E3335", {"points": [v(52.83, 11.17) * mm, v(52.62, 11.24) * mm, v(52.4, 11.29) * mm, v(52.19, 11.35) * mm]});
            skFitSpline(sketch, "E3336", {"points": [v(52.19, 11.35) * mm, v(52.1, 11.37) * mm, v(52.03, 11.4) * mm, v(51.96, 11.42) * mm]});
            skFitSpline(sketch, "E3337", {"points": [v(51.96, 11.42) * mm, v(51.71, 11.54) * mm, v(51.6, 11.79) * mm, v(51.68, 12.01) * mm]});
            skFitSpline(sketch, "E3338", {"points": [v(51.68, 12.01) * mm, v(51.77, 12.27) * mm, v(52, 12.4) * mm, v(52.27, 12.33) * mm]});
            skFitSpline(sketch, "E3339", {"points": [v(52.27, 12.33) * mm, v(52.53, 12.27) * mm, v(52.78, 12.2) * mm, v(53.04, 12.13) * mm]});
            skFitSpline(sketch, "E3340", {"points": [v(53.04, 12.13) * mm, v(53.65, 11.97) * mm, v(54.27, 11.81) * mm, v(54.9, 11.66) * mm]});
            skFitSpline(sketch, "E3341", {"points": [v(54.9, 11.66) * mm, v(54.97, 11.64) * mm, v(55.05, 11.63) * mm, v(55.15, 11.61) * mm]});
            skFitSpline(sketch, "E3342", {"points": [v(55.15, 11.61) * mm, v(55.15, 11.67) * mm, v(55.16, 11.73) * mm, v(55.14, 11.78) * mm]});
            skFitSpline(sketch, "E3343", {"points": [v(55.14, 11.78) * mm, v(54.98, 12.43) * mm, v(54.82, 13.08) * mm, v(54.65, 13.73) * mm]});
            skFitSpline(sketch, "E3344", {"points": [v(54.65, 13.73) * mm, v(54.59, 13.98) * mm, v(54.5, 14.23) * mm, v(54.45, 14.5) * mm]});
            skFitSpline(sketch, "E3345", {"points": [v(54.45, 14.5) * mm, v(54.36, 14.88) * mm, v(54.63, 15.17) * mm, v(55.02, 15.1) * mm]});
            skFitSpline(sketch, "E3346", {"points": [v(55.02, 15.1) * mm, v(55.24, 15.06) * mm, v(55.35, 14.9) * mm, v(55.4, 14.69) * mm]});
            skFitSpline(sketch, "E3347", {"points": [v(55.4, 14.69) * mm, v(55.5, 14.34) * mm, v(55.6, 14) * mm, v(55.69, 13.65) * mm]});
            skFitSpline(sketch, "E3348", {"points": [v(55.69, 13.65) * mm, v(55.86, 12.94) * mm, v(56.04, 12.22) * mm, v(56.2, 11.5) * mm]});
            skFitSpline(sketch, "E3349", {"points": [v(56.2, 11.5) * mm, v(56.24, 11.36) * mm, v(56.3, 11.28) * mm, v(56.46, 11.24) * mm]});
            skFitSpline(sketch, "E3350", {"points": [v(56.46, 11.24) * mm, v(56.78, 11.18) * mm, v(57.1, 11.08) * mm, v(57.41, 11.01) * mm]});
            skFitSpline(sketch, "E3351", {"points": [v(57.41, 11.01) * mm, v(57.68, 10.95) * mm, v(57.94, 10.9) * mm, v(58.14, 10.68) * mm]});
            skFitSpline(sketch, "E3352", {"points": [v(58.14, 10.68) * mm, v(58.18, 10.64) * mm, v(58.25, 10.62) * mm, v(58.31, 10.6) * mm]});
            skFitSpline(sketch, "E3353", {"points": [v(58.31, 10.6) * mm, v(59.28, 10.29) * mm, v(60.25, 9.95) * mm, v(61.18, 9.53) * mm]});
            skFitSpline(sketch, "E3354", {"points": [v(61.18, 9.53) * mm, v(61.34, 9.45) * mm, v(61.51, 9.4) * mm, v(61.73, 9.31) * mm]});
            skFitSpline(sketch, "E3355", {"points": [v(61.73, 9.31) * mm, v(61.69, 9.4) * mm, v(61.67, 9.46) * mm, v(61.64, 9.52) * mm]});
            skFitSpline(sketch, "E3356", {"points": [v(61.64, 9.52) * mm, v(61.44, 10) * mm, v(61.22, 10.5) * mm, v(61.02, 11) * mm]});
            skFitSpline(sketch, "E3357", {"points": [v(61.02, 11) * mm, v(60.97, 11.1) * mm, v(60.92, 11.17) * mm, v(60.8, 11.22) * mm]});
            skFitSpline(sketch, "E3358", {"points": [v(60.8, 11.22) * mm, v(60.27, 11.44) * mm, v(59.71, 11.58) * mm, v(59.15, 11.73) * mm]});
            skFitSpline(sketch, "E3359", {"points": [v(59.15, 11.73) * mm, v(59.05, 11.75) * mm, v(58.94, 11.79) * mm, v(58.84, 11.83) * mm]});
            skFitSpline(sketch, "E3360", {"points": [v(58.84, 11.83) * mm, v(58.59, 11.94) * mm, v(58.48, 12.18) * mm, v(58.56, 12.42) * mm]});
            skFitSpline(sketch, "E3361", {"points": [v(58.56, 12.42) * mm, v(58.64, 12.67) * mm, v(58.87, 12.8) * mm, v(59.15, 12.74) * mm]});
            skFitSpline(sketch, "E3362", {"points": [v(59.15, 12.74) * mm, v(59.43, 12.67) * mm, v(59.7, 12.59) * mm, v(59.98, 12.51) * mm]});
            skFitSpline(sketch, "E3363", {"points": [v(59.98, 12.51) * mm, v(60.12, 12.48) * mm, v(60.26, 12.45) * mm, v(60.43, 12.4) * mm]});
            skFitSpline(sketch, "E3364", {"points": [v(60.43, 12.4) * mm, v(60.3, 12.7) * mm, v(60.2, 12.96) * mm, v(60.08, 13.23) * mm]});
            skFitSpline(sketch, "E3365", {"points": [v(60.08, 13.23) * mm, v(59.8, 13.23) * mm, v(59.55, 13.33) * mm, v(59.3, 13.43) * mm]});
            skFitSpline(sketch, "E3366", {"points": [v(59.3, 13.43) * mm, v(59.1, 13.5) * mm, v(58.9, 13.59) * mm, v(58.7, 13.66) * mm]});
            skFitSpline(sketch, "E3367", {"points": [v(58.7, 13.66) * mm, v(58.4, 13.77) * mm, v(58.1, 13.88) * mm, v(57.8, 13.98) * mm]});
            skFitSpline(sketch, "E3368", {"points": [v(57.8, 13.98) * mm, v(57.56, 14.06) * mm, v(57.4, 14.24) * mm, v(57.4, 14.47) * mm]});
            skFitSpline(sketch, "E3369", {"points": [v(57.4, 14.47) * mm, v(57.41, 14.68) * mm, v(57.56, 14.88) * mm, v(57.77, 14.92) * mm]});
            skFitSpline(sketch, "E3370", {"points": [v(57.77, 14.92) * mm, v(57.87, 14.94) * mm, v(58, 14.94) * mm, v(58.1, 14.9) * mm]});
            skFitSpline(sketch, "E3371", {"points": [v(58.1, 14.9) * mm, v(58.48, 14.78) * mm, v(58.87, 14.64) * mm, v(59.25, 14.5) * mm]});
            skFitSpline(sketch, "E3372", {"points": [v(59.25, 14.5) * mm, v(59.51, 14.4) * mm, v(59.77, 14.3) * mm, v(60.03, 14.2) * mm]});
            skFitSpline(sketch, "E3373", {"points": [v(60.03, 14.2) * mm, v(60.13, 14.17) * mm, v(60.22, 14.12) * mm, v(60.3, 14.07) * mm]});
            skFitSpline(sketch, "E3374", {"points": [v(60.3, 14.07) * mm, v(60.6, 14.72) * mm, v(60.88, 15.37) * mm, v(61.18, 16.02) * mm]});
            skFitSpline(sketch, "E3375", {"points": [v(61.18, 16.02) * mm, v(61.22, 16.12) * mm, v(61.28, 16.22) * mm, v(61.34, 16.3) * mm]});
            skFitSpline(sketch, "E3376", {"points": [v(61.34, 16.3) * mm, v(61.5, 16.54) * mm, v(61.77, 16.6) * mm, v(62, 16.48) * mm]});
            skFitSpline(sketch, "E3377", {"points": [v(62, 16.48) * mm, v(62.23, 16.35) * mm, v(62.3, 16.08) * mm, v(62.19, 15.82) * mm]});
            skFitSpline(sketch, "E3378", {"points": [v(62.19, 15.82) * mm, v(62.11, 15.67) * mm, v(62.02, 15.52) * mm, v(61.95, 15.37) * mm]});
            skFitSpline(sketch, "E3379", {"points": [v(61.95, 15.37) * mm, v(61.75, 14.93) * mm, v(61.56, 14.48) * mm, v(61.35, 14.04) * mm]});
            skFitSpline(sketch, "E3380", {"points": [v(61.35, 14.04) * mm, v(61.29, 13.9) * mm, v(61.2, 13.79) * mm, v(61.1, 13.63) * mm]});
            skFitSpline(sketch, "E3381", {"points": [v(61.1, 13.63) * mm, v(61.2, 13.39) * mm, v(61.3, 13.12) * mm, v(61.42, 12.8) * mm]});
            skFitSpline(sketch, "E3382", {"points": [v(61.42, 12.8) * mm, v(61.64, 13.18) * mm, v(61.84, 13.53) * mm, v(62.04, 13.87) * mm]});
            skFitSpline(sketch, "E3383", {"points": [v(62.04, 13.87) * mm, v(62.12, 14.02) * mm, v(62.21, 14.15) * mm, v(62.38, 14.18) * mm]});
            skFitSpline(sketch, "E3384", {"points": [v(62.38, 14.18) * mm, v(62.56, 14.22) * mm, v(62.73, 14.2) * mm, v(62.86, 14.05) * mm]});
            skFitSpline(sketch, "E3385", {"points": [v(62.86, 14.05) * mm, v(63, 13.9) * mm, v(63.02, 13.73) * mm, v(62.96, 13.55) * mm]});
            skFitSpline(sketch, "E3386", {"points": [v(62.96, 13.55) * mm, v(62.9, 13.42) * mm, v(62.84, 13.3) * mm, v(62.76, 13.17) * mm]});
            skFitSpline(sketch, "E3387", {"points": [v(62.76, 13.17) * mm, v(62.45, 12.66) * mm, v(62.16, 12.13) * mm, v(61.95, 11.56) * mm]});
            skFitSpline(sketch, "E3388", {"points": [v(61.95, 11.56) * mm, v(62.19, 10.97) * mm, v(62.43, 10.37) * mm, v(62.69, 9.72) * mm]});
            skFitSpline(sketch, "E3389", {"points": [v(62.69, 9.72) * mm, v(62.78, 9.91) * mm, v(62.85, 10.07) * mm, v(62.93, 10.24) * mm]});
            skFitSpline(sketch, "E3390", {"points": [v(62.93, 10.24) * mm, v(63.15, 10.76) * mm, v(63.37, 11.28) * mm, v(63.6, 11.8) * mm]});
            skFitSpline(sketch, "E3391", {"points": [v(63.6, 11.8) * mm, v(63.8, 12.23) * mm, v(64.02, 12.66) * mm, v(64.22, 13.1) * mm]});
            skFitSpline(sketch, "E3392", {"points": [v(64.22, 13.1) * mm, v(64.25, 13.15) * mm, v(64.27, 13.21) * mm, v(64.27, 13.27) * mm]});
            skFitSpline(sketch, "E3393", {"points": [v(64.27, 13.27) * mm, v(64.26, 13.49) * mm, v(64.35, 13.66) * mm, v(64.46, 13.83) * mm]});
            skFitSpline(sketch, "E3394", {"points": [v(64.46, 13.83) * mm, v(64.69, 14.2) * mm, v(64.92, 14.58) * mm, v(65.16, 14.97) * mm]});
            skFitSpline(sketch, "E3395", {"points": [v(65.16, 14.97) * mm, v(65.04, 15.16) * mm, v(64.94, 15.35) * mm, v(64.82, 15.52) * mm]});
            skFitSpline(sketch, "E3396", {"points": [v(64.82, 15.52) * mm, v(64.4, 16.14) * mm, v(64.03, 16.78) * mm, v(63.68, 17.44) * mm]});
            skFitSpline(sketch, "E3397", {"points": [v(63.68, 17.44) * mm, v(63.6, 17.58) * mm, v(63.5, 17.73) * mm, v(63.43, 17.87) * mm]});
            skFitSpline(sketch, "E3398", {"points": [v(63.43, 17.87) * mm, v(63.38, 17.95) * mm, v(63.33, 18.04) * mm, v(63.3, 18.13) * mm]});
            skFitSpline(sketch, "E3399", {"points": [v(63.3, 18.13) * mm, v(63.21, 18.36) * mm, v(63.3, 18.6) * mm, v(63.52, 18.72) * mm]});
            skFitSpline(sketch, "E3400", {"points": [v(63.52, 18.72) * mm, v(63.73, 18.84) * mm, v(64, 18.78) * mm, v(64.14, 18.57) * mm]});
            skFitSpline(sketch, "E3401", {"points": [v(64.14, 18.57) * mm, v(64.26, 18.39) * mm, v(64.37, 18.2) * mm, v(64.48, 18) * mm]});
            skFitSpline(sketch, "E3402", {"points": [v(64.48, 18) * mm, v(64.85, 17.38) * mm, v(65.22, 16.76) * mm, v(65.58, 16.14) * mm]});
            skFitSpline(sketch, "E3403", {"points": [v(65.58, 16.14) * mm, v(65.61, 16.1) * mm, v(65.65, 16.05) * mm, v(65.7, 15.99) * mm]});
            skFitSpline(sketch, "E3404", {"points": [v(65.7, 15.99) * mm, v(65.74, 16.04) * mm, v(65.79, 16.08) * mm, v(65.82, 16.13) * mm]});
            skFitSpline(sketch, "E3405", {"points": [v(65.82, 16.13) * mm, v(66.16, 16.7) * mm, v(66.5, 17.27) * mm, v(66.84, 17.84) * mm]});
            skFitSpline(sketch, "E3406", {"points": [v(66.84, 17.84) * mm, v(66.97, 18.07) * mm, v(67.1, 18.31) * mm, v(67.25, 18.54) * mm]});
            skFitSpline(sketch, "E3407", {"points": [v(67.25, 18.54) * mm, v(67.36, 18.73) * mm, v(67.57, 18.82) * mm, v(67.76, 18.77) * mm]});
            skFitSpline(sketch, "E3408", {"points": [v(67.76, 18.77) * mm, v(67.97, 18.72) * mm, v(68.1, 18.58) * mm, v(68.13, 18.38) * mm]});
            skFitSpline(sketch, "E3409", {"points": [v(68.13, 18.38) * mm, v(68.14, 18.26) * mm, v(68.12, 18.12) * mm, v(68.06, 18.01) * mm]});
            skFitSpline(sketch, "E3410", {"points": [v(68.06, 18.01) * mm, v(67.62, 17.25) * mm, v(67.17, 16.5) * mm, v(66.73, 15.74) * mm]});
            skFitSpline(sketch, "E3411", {"points": [v(66.73, 15.74) * mm, v(66.61, 15.55) * mm, v(66.5, 15.36) * mm, v(66.37, 15.17) * mm]});
            skFitSpline(sketch, "E3412", {"points": [v(66.37, 15.17) * mm, v(66.28, 15.05) * mm, v(66.27, 14.94) * mm, v(66.36, 14.8) * mm]});
            skFitSpline(sketch, "E3413", {"points": [v(66.36, 14.8) * mm, v(66.56, 14.5) * mm, v(66.74, 14.18) * mm, v(66.93, 13.86) * mm]});
            skFitSpline(sketch, "E3414", {"points": [v(66.93, 13.86) * mm, v(67.05, 13.67) * mm, v(67.16, 13.48) * mm, v(67.15, 13.24) * mm]});
            skFitSpline(sketch, "E3415", {"points": [v(67.15, 13.24) * mm, v(67.15, 13.18) * mm, v(67.18, 13.11) * mm, v(67.2, 13.06) * mm]});
            skFitSpline(sketch, "E3416", {"points": [v(67.2, 13.06) * mm, v(67.69, 12.12) * mm, v(68.14, 11.17) * mm, v(68.5, 10.18) * mm]});
            skFitSpline(sketch, "E3417", {"points": [v(68.5, 10.18) * mm, v(68.56, 10.03) * mm, v(68.64, 9.9) * mm, v(68.71, 9.73) * mm]});
            skFitSpline(sketch, "E3418", {"points": [v(68.71, 9.73) * mm, v(68.75, 9.79) * mm, v(68.77, 9.83) * mm, v(68.79, 9.87) * mm]});
            skFitSpline(sketch, "E3419", {"points": [v(68.79, 9.87) * mm, v(69, 10.38) * mm, v(69.2, 10.9) * mm, v(69.41, 11.42) * mm]});
            skFitSpline(sketch, "E3420", {"points": [v(69.41, 11.42) * mm, v(69.46, 11.53) * mm, v(69.45, 11.6) * mm, v(69.4, 11.71) * mm]});
            skFitSpline(sketch, "E3421", {"points": [v(69.4, 11.71) * mm, v(69.2, 12.21) * mm, v(68.94, 12.69) * mm, v(68.65, 13.15) * mm]});
            skFitSpline(sketch, "E3422", {"points": [v(68.65, 13.15) * mm, v(68.57, 13.28) * mm, v(68.5, 13.42) * mm, v(68.45, 13.56) * mm]});
            skFitSpline(sketch, "E3423", {"points": [v(68.45, 13.56) * mm, v(68.36, 13.8) * mm, v(68.48, 14.07) * mm, v(68.7, 14.16) * mm]});
            skFitSpline(sketch, "E3424", {"points": [v(68.7, 14.16) * mm, v(68.94, 14.26) * mm, v(69.2, 14.17) * mm, v(69.34, 13.93) * mm]});
            skFitSpline(sketch, "E3425", {"points": [v(69.34, 13.93) * mm, v(69.5, 13.64) * mm, v(69.67, 13.35) * mm, v(69.84, 13.06) * mm]});
            skFitSpline(sketch, "E3426", {"points": [v(69.84, 13.06) * mm, v(69.88, 13) * mm, v(69.92, 12.92) * mm, v(69.99, 12.82) * mm]});
            skFitSpline(sketch, "E3427", {"points": [v(69.99, 12.82) * mm, v(70.1, 13.12) * mm, v(70.21, 13.39) * mm, v(70.3, 13.61) * mm]});
            skFitSpline(sketch, "E3428", {"points": [v(70.3, 13.61) * mm, v(70.17, 13.86) * mm, v(70.04, 14.07) * mm, v(69.93, 14.29) * mm]});
            skFitSpline(sketch, "E3429", {"points": [v(69.93, 14.29) * mm, v(69.8, 14.55) * mm, v(69.7, 14.82) * mm, v(69.59, 15.08) * mm]});
            skFitSpline(sketch, "E3430", {"points": [v(69.59, 15.08) * mm, v(69.48, 15.3) * mm, v(69.36, 15.54) * mm, v(69.25, 15.76) * mm]});
            skFitSpline(sketch, "E3431", {"points": [v(69.25, 15.76) * mm, v(69.23, 15.8) * mm, v(69.2, 15.85) * mm, v(69.2, 15.9) * mm]});
            skFitSpline(sketch, "E3432", {"points": [v(69.2, 15.9) * mm, v(69.11, 16.14) * mm, v(69.2, 16.38) * mm, v(69.43, 16.49) * mm]});
            skFitSpline(sketch, "E3433", {"points": [v(69.43, 16.49) * mm, v(69.63, 16.6) * mm, v(69.88, 16.55) * mm, v(70.03, 16.35) * mm]});
            skFitSpline(sketch, "E3434", {"points": [v(70.03, 16.35) * mm, v(70.12, 16.23) * mm, v(70.2, 16.1) * mm, v(70.26, 15.96) * mm]});
            skFitSpline(sketch, "E3435", {"points": [v(70.26, 15.96) * mm, v(70.5, 15.42) * mm, v(70.76, 14.87) * mm, v(71, 14.33) * mm]});
            skFitSpline(sketch, "E3436", {"points": [v(71, 14.33) * mm, v(71.03, 14.25) * mm, v(71.04, 14.16) * mm, v(71.07, 14.07) * mm]});
            skFitSpline(sketch, "E3437", {"points": [v(71.07, 14.07) * mm, v(71.67, 14.3) * mm, v(72.29, 14.55) * mm, v(72.9, 14.78) * mm]});
            skFitSpline(sketch, "E3438", {"points": [v(72.9, 14.78) * mm, v(73.06, 14.84) * mm, v(73.22, 14.9) * mm, v(73.38, 14.93) * mm]});
            skFitSpline(sketch, "E3439", {"points": [v(73.38, 14.93) * mm, v(73.67, 15) * mm, v(73.91, 14.84) * mm, v(73.98, 14.55) * mm]});
            skFitSpline(sketch, "E3440", {"points": [v(73.98, 14.55) * mm, v(74.05, 14.32) * mm, v(73.9, 14.08) * mm, v(73.63, 13.98) * mm]});
            skFitSpline(sketch, "E3441", {"points": [v(73.63, 13.98) * mm, v(73.13, 13.8) * mm, v(72.63, 13.61) * mm, v(72.12, 13.43) * mm]});
            skFitSpline(sketch, "E3442", {"points": [v(72.12, 13.43) * mm, v(71.87, 13.34) * mm, v(71.62, 13.22) * mm, v(71.34, 13.24) * mm]});
            skFitSpline(sketch, "E3443", {"points": [v(71.34, 13.24) * mm, v(71.22, 12.97) * mm, v(71.1, 12.71) * mm, v(70.98, 12.41) * mm]});
            skFitSpline(sketch, "E3444", {"points": [v(70.98, 12.41) * mm, v(71.08, 12.43) * mm, v(71.15, 12.44) * mm, v(71.22, 12.46) * mm]});
            skFitSpline(sketch, "E3445", {"points": [v(71.22, 12.46) * mm, v(71.55, 12.55) * mm, v(71.87, 12.64) * mm, v(72.2, 12.73) * mm]});
            skFitSpline(sketch, "E3446", {"points": [v(72.2, 12.73) * mm, v(72.4, 12.78) * mm, v(72.6, 12.76) * mm, v(72.76, 12.58) * mm]});
            skFitSpline(sketch, "E3447", {"points": [v(72.76, 12.58) * mm, v(72.95, 12.35) * mm, v(72.9, 12) * mm, v(72.62, 11.86) * mm]});
            skFitSpline(sketch, "E3448", {"points": [v(72.62, 11.86) * mm, v(72.5, 11.8) * mm, v(72.37, 11.76) * mm, v(72.24, 11.72) * mm]});
            skFitSpline(sketch, "E3449", {"points": [v(72.24, 11.72) * mm, v(71.68, 11.58) * mm, v(71.13, 11.44) * mm, v(70.6, 11.2) * mm]});
            skFitSpline(sketch, "E3450", {"points": [v(70.6, 11.2) * mm, v(70.51, 11.17) * mm, v(70.45, 11.14) * mm, v(70.4, 11.05) * mm]});
            skFitSpline(sketch, "E3451", {"points": [v(70.4, 11.05) * mm, v(70.19, 10.5) * mm, v(69.95, 9.98) * mm, v(69.73, 9.44) * mm]});
            skFitSpline(sketch, "E3452", {"points": [v(69.73, 9.44) * mm, v(69.71, 9.41) * mm, v(69.7, 9.38) * mm, v(69.7, 9.32) * mm]});
            skFitSpline(sketch, "E3453", {"points": [v(69.7, 9.32) * mm, v(69.88, 9.4) * mm, v(70.04, 9.45) * mm, v(70.2, 9.51) * mm]});
            skFitSpline(sketch, "E3454", {"points": [v(70.2, 9.51) * mm, v(70.74, 9.72) * mm, v(71.27, 9.94) * mm, v(71.8, 10.14) * mm]});
            skFitSpline(sketch, "E3455", {"points": [v(71.8, 10.14) * mm, v(72.25, 10.31) * mm, v(72.7, 10.46) * mm, v(73.16, 10.62) * mm]});
            skFitSpline(sketch, "E3456", {"points": [v(73.16, 10.62) * mm, v(73.2, 10.64) * mm, v(73.26, 10.67) * mm, v(73.3, 10.7) * mm]});
            skFitSpline(sketch, "E3457", {"points": [v(73.3, 10.7) * mm, v(73.44, 10.86) * mm, v(73.61, 10.92) * mm, v(73.8, 10.97) * mm]});
            skFitSpline(sketch, "E3458", {"points": [v(73.8, 10.97) * mm, v(74.24, 11.07) * mm, v(74.69, 11.18) * mm, v(75.15, 11.29) * mm]});
            skFitSpline(sketch, "E3459", {"points": [v(75.15, 11.29) * mm, v(75.2, 11.55) * mm, v(75.26, 11.8) * mm, v(75.32, 12.06) * mm]});
            skFitSpline(sketch, "E3460", {"points": [v(75.32, 12.06) * mm, v(75.48, 12.7) * mm, v(75.65, 13.33) * mm, v(75.8, 13.96) * mm]});
            skFitSpline(sketch, "E3461", {"points": [v(75.8, 13.96) * mm, v(75.86, 14.17) * mm, v(75.92, 14.38) * mm, v(75.98, 14.59) * mm]});
            skFitSpline(sketch, "E3462", {"points": [v(75.98, 14.59) * mm, v(76, 14.68) * mm, v(76.03, 14.77) * mm, v(76.07, 14.86) * mm]});
            skFitSpline(sketch, "E3463", {"points": [v(76.07, 14.86) * mm, v(76.2, 15.08) * mm, v(76.46, 15.17) * mm, v(76.7, 15.08) * mm]});
            skFitSpline(sketch, "E3464", {"points": [v(76.7, 15.08) * mm, v(76.9, 15) * mm, v(77.02, 14.75) * mm, v(76.96, 14.52) * mm]});
            skFitSpline(sketch, "E3465", {"points": [v(76.96, 14.52) * mm, v(76.84, 14.04) * mm, v(76.7, 13.57) * mm, v(76.57, 13.1) * mm]});
            skFitSpline(sketch, "E3466", {"points": [v(76.57, 13.1) * mm, v(76.45, 12.61) * mm, v(76.34, 12.13) * mm, v(76.21, 11.6) * mm]});
            skFitSpline(sketch, "E3467", {"points": [v(76.21, 11.6) * mm, v(76.42, 11.64) * mm, v(76.58, 11.66) * mm, v(76.74, 11.7) * mm]});
            skFitSpline(sketch, "E3468", {"points": [v(76.74, 11.7) * mm, v(77.28, 11.84) * mm, v(77.8, 11.98) * mm, v(78.34, 12.12) * mm]});
            skFitSpline(sketch, "E3469", {"points": [v(78.34, 12.12) * mm, v(78.6, 12.19) * mm, v(78.85, 12.26) * mm, v(79.1, 12.32) * mm]});
            skFitSpline(sketch, "E3470", {"points": [v(79.1, 12.32) * mm, v(79.39, 12.4) * mm, v(79.67, 12.27) * mm, v(79.72, 12.02) * mm]});
            skFitSpline(sketch, "E3471", {"points": [v(79.72, 12.02) * mm, v(79.77, 11.76) * mm, v(79.74, 11.52) * mm, v(79.38, 11.4) * mm]});
            skFitSpline(sketch, "E3472", {"points": [v(79.38, 11.4) * mm, v(79.03, 11.28) * mm, v(78.67, 11.2) * mm, v(78.32, 11.1) * mm]});
            skFitSpline(sketch, "E3473", {"points": [v(78.32, 11.1) * mm, v(77.6, 10.92) * mm, v(76.88, 10.75) * mm, v(76.16, 10.58) * mm]});
            skFitSpline(sketch, "E3474", {"points": [v(76.16, 10.58) * mm, v(75.98, 10.54) * mm, v(75.9, 10.46) * mm, v(75.86, 10.3) * mm]});
            skFitSpline(sketch, "E3475", {"points": [v(75.86, 10.3) * mm, v(75.8, 9.94) * mm, v(75.7, 9.6) * mm, v(75.61, 9.25) * mm]});
            skFitSpline(sketch, "E3476", {"points": [v(75.61, 9.25) * mm, v(75.56, 9.02) * mm, v(75.5, 8.81) * mm, v(75.32, 8.65) * mm]});
            skFitSpline(sketch, "E3477", {"points": [v(75.32, 8.65) * mm, v(75.28, 8.61) * mm, v(75.26, 8.55) * mm, v(75.24, 8.49) * mm]});
            skFitSpline(sketch, "E3478", {"points": [v(75.24, 8.49) * mm, v(74.92, 7.48) * mm, v(74.57, 6.5) * mm, v(74.12, 5.53) * mm]});
            skFitSpline(sketch, "E3479", {"points": [v(74.12, 5.53) * mm, v(74.06, 5.4) * mm, v(74.02, 5.26) * mm, v(73.97, 5.13) * mm]});
            skFitSpline(sketch, "E3480", {"points": [v(73.97, 5.13) * mm, v(73.97, 5.12) * mm, v(73.98, 5.1) * mm, v(73.99, 5.07) * mm]});
            skFitSpline(sketch, "E3481", {"points": [v(73.99, 5.07) * mm, v(74.04, 5.09) * mm, v(74.09, 5.1) * mm, v(74.13, 5.13) * mm]});
            skFitSpline(sketch, "E3482", {"points": [v(74.13, 5.13) * mm, v(74.63, 5.34) * mm, v(75.13, 5.56) * mm, v(75.63, 5.76) * mm]});
            skFitSpline(sketch, "E3483", {"points": [v(75.63, 5.76) * mm, v(75.75, 5.81) * mm, v(75.8, 5.88) * mm, v(75.85, 5.99) * mm]});
            skFitSpline(sketch, "E3484", {"points": [v(75.85, 5.99) * mm, v(76.05, 6.47) * mm, v(76.2, 6.97) * mm, v(76.31, 7.47) * mm]});
            skFitSpline(sketch, "E3485", {"points": [v(76.31, 7.47) * mm, v(76.35, 7.62) * mm, v(76.4, 7.77) * mm, v(76.45, 7.9) * mm]});
            skFitSpline(sketch, "E3486", {"points": [v(76.45, 7.9) * mm, v(76.56, 8.18) * mm, v(76.8, 8.3) * mm, v(77.06, 8.22) * mm]});
            skFitSpline(sketch, "E3487", {"points": [v(77.06, 8.22) * mm, v(77.32, 8.13) * mm, v(77.44, 7.86) * mm, v(77.36, 7.57) * mm]});
            skFitSpline(sketch, "E3488", {"points": [v(77.36, 7.57) * mm, v(77.26, 7.2) * mm, v(77.16, 6.84) * mm, v(77.06, 6.48) * mm]});
            skFitSpline(sketch, "E3489", {"points": [v(77.06, 6.48) * mm, v(77.05, 6.45) * mm, v(77.05, 6.42) * mm, v(77.04, 6.35) * mm]});
            skFitSpline(sketch, "E3490", {"points": [v(77.04, 6.35) * mm, v(77.33, 6.47) * mm, v(77.6, 6.59) * mm, v(77.86, 6.7) * mm]});
            skFitSpline(sketch, "E3491", {"points": [v(77.86, 6.7) * mm, v(77.86, 6.99) * mm, v(77.97, 7.24) * mm, v(78.06, 7.49) * mm]});
            skFitSpline(sketch, "E3492", {"points": [v(78.06, 7.49) * mm, v(78.2, 7.84) * mm, v(78.34, 8.19) * mm, v(78.47, 8.54) * mm]});
            skFitSpline(sketch, "E3493", {"points": [v(78.47, 8.54) * mm, v(78.53, 8.69) * mm, v(78.56, 8.84) * mm, v(78.61, 9) * mm]});
            skFitSpline(sketch, "E3494", {"points": [v(78.61, 9) * mm, v(78.72, 9.32) * mm, v(79.03, 9.46) * mm, v(79.31, 9.3) * mm]});
            skFitSpline(sketch, "E3495", {"points": [v(79.31, 9.3) * mm, v(79.5, 9.2) * mm, v(79.61, 8.99) * mm, v(79.56, 8.76) * mm]});
            skFitSpline(sketch, "E3496", {"points": [v(79.56, 8.76) * mm, v(79.52, 8.6) * mm, v(79.47, 8.44) * mm, v(79.41, 8.28) * mm]});
            skFitSpline(sketch, "E3497", {"points": [v(79.41, 8.28) * mm, v(79.22, 7.76) * mm, v(79.02, 7.23) * mm, v(78.82, 6.71) * mm]});
            skFitSpline(sketch, "E3498", {"points": [v(78.82, 6.71) * mm, v(78.79, 6.62) * mm, v(78.74, 6.54) * mm, v(78.7, 6.47) * mm]});
            skFitSpline(sketch, "E3499", {"points": [v(78.7, 6.47) * mm, v(79.3, 6.2) * mm, v(79.88, 5.95) * mm, v(80.47, 5.68) * mm]});
            skFitSpline(sketch, "E3500", {"points": [v(80.47, 5.68) * mm, v(80.64, 5.6) * mm, v(80.81, 5.52) * mm, v(80.97, 5.4) * mm]});
            skFitSpline(sketch, "E3501", {"points": [v(80.97, 5.4) * mm, v(81.14, 5.3) * mm, v(81.2, 5.11) * mm, v(81.16, 4.9) * mm]});
            skFitSpline(sketch, "E3502", {"points": [v(81.16, 4.9) * mm, v(81.1, 4.7) * mm, v(80.98, 4.57) * mm, v(80.78, 4.55) * mm]});
            skFitSpline(sketch, "E3503", {"points": [v(80.78, 4.55) * mm, v(80.67, 4.53) * mm, v(80.54, 4.56) * mm, v(80.43, 4.6) * mm]});
            skFitSpline(sketch, "E3504", {"points": [v(80.43, 4.6) * mm, v(79.93, 4.83) * mm, v(79.43, 5.06) * mm, v(78.93, 5.3) * mm]});
            skFitSpline(sketch, "E3505", {"points": [v(78.93, 5.3) * mm, v(78.71, 5.4) * mm, v(78.5, 5.53) * mm, v(78.24, 5.67) * mm]});
            skFitSpline(sketch, "E3506", {"points": [v(78.24, 5.67) * mm, v(78.02, 5.59) * mm, v(77.75, 5.48) * mm, v(77.45, 5.37) * mm]});
            skFitSpline(sketch, "E3507", {"points": [v(77.45, 5.37) * mm, v(77.53, 5.31) * mm, v(77.59, 5.27) * mm, v(77.65, 5.23) * mm]});
            skFitSpline(sketch, "E3508", {"points": [v(77.65, 5.23) * mm, v(77.94, 5.06) * mm, v(78.24, 4.89) * mm, v(78.54, 4.72) * mm]});
            skFitSpline(sketch, "E3509", {"points": [v(78.54, 4.72) * mm, v(78.8, 4.57) * mm, v(78.9, 4.3) * mm, v(78.78, 4.05) * mm]});
            skFitSpline(sketch, "E3510", {"points": [v(78.78, 4.05) * mm, v(78.66, 3.81) * mm, v(78.4, 3.72) * mm, v(78.12, 3.85) * mm]});
            skFitSpline(sketch, "E3511", {"points": [v(78.12, 3.85) * mm, v(77.9, 3.95) * mm, v(77.7, 4.08) * mm, v(77.5, 4.2) * mm]});
            skFitSpline(sketch, "E3512", {"points": [v(77.5, 4.2) * mm, v(77.1, 4.4) * mm, v(76.7, 4.59) * mm, v(76.32, 4.79) * mm]});
            skFitSpline(sketch, "E3513", {"points": [v(76.32, 4.79) * mm, v(76.24, 4.82) * mm, v(76.18, 4.84) * mm, v(76.1, 4.8) * mm]});
            skFitSpline(sketch, "E3514", {"points": [v(76.1, 4.8) * mm, v(75.54, 4.58) * mm, v(74.98, 4.36) * mm, v(74.43, 4.13) * mm]});
            skFitSpline(sketch, "E3515", {"points": [v(74.43, 4.13) * mm, v(74.41, 4.13) * mm, v(74.4, 4.11) * mm, v(74.37, 4.08) * mm]});
            skFitSpline(sketch, "E3516", {"points": [v(74.37, 4.08) * mm, v(74.53, 4) * mm, v(74.68, 3.93) * mm, v(74.84, 3.86) * mm]});
            skFitSpline(sketch, "E3517", {"points": [v(74.84, 3.86) * mm, v(75.37, 3.63) * mm, v(75.9, 3.4) * mm, v(76.44, 3.17) * mm]});
            skFitSpline(sketch, "E3518", {"points": [v(76.44, 3.17) * mm, v(76.87, 2.97) * mm, v(77.3, 2.76) * mm, v(77.74, 2.55) * mm]});
            skFitSpline(sketch, "E3519", {"points": [v(77.74, 2.55) * mm, v(77.78, 2.53) * mm, v(77.83, 2.51) * mm, v(77.87, 2.52) * mm]});
            skFitSpline(sketch, "E3520", {"points": [v(77.87, 2.52) * mm, v(78.11, 2.53) * mm, v(78.3, 2.42) * mm, v(78.5, 2.3) * mm]});
            skFitSpline(sketch, "E3521", {"points": [v(78.5, 2.3) * mm, v(78.8, 2.1) * mm, v(79.13, 1.93) * mm, v(79.44, 1.73) * mm]});
            skFitSpline(sketch, "E3522", {"points": [v(79.44, 1.73) * mm, v(79.56, 1.65) * mm, v(79.66, 1.64) * mm, v(79.78, 1.73) * mm]});
            skFitSpline(sketch, "E3523", {"points": [v(79.78, 1.73) * mm, v(80, 1.88) * mm, v(80.23, 2.03) * mm, v(80.47, 2.17) * mm]});
            skFitSpline(sketch, "E3524", {"points": [v(80.47, 2.17) * mm, v(80.93, 2.45) * mm, v(81.4, 2.72) * mm, v(81.87, 3) * mm]});
            skFitSpline(sketch, "E3525", {"points": [v(81.87, 3) * mm, v(82.1, 3.13) * mm, v(82.33, 3.26) * mm, v(82.56, 3.39) * mm]});
            skFitSpline(sketch, "E3526", {"points": [v(82.56, 3.39) * mm, v(82.7, 3.47) * mm, v(82.84, 3.55) * mm, v(83, 3.5) * mm]});
            skFitSpline(sketch, "E3527", {"points": [v(83, 3.5) * mm, v(83.21, 3.46) * mm, v(83.35, 3.34) * mm, v(83.4, 3.13) * mm]});
            skFitSpline(sketch, "E3528", {"points": [v(83.4, 3.13) * mm, v(83.44, 2.92) * mm, v(83.36, 2.75) * mm, v(83.19, 2.63) * mm]});
            skFitSpline(sketch, "E3529", {"points": [v(83.19, 2.63) * mm, v(82.97, 2.49) * mm, v(82.73, 2.36) * mm, v(82.5, 2.23) * mm]});
            skFitSpline(sketch, "E3530", {"points": [v(82.5, 2.23) * mm, v(81.94, 1.9) * mm, v(81.38, 1.56) * mm, v(80.82, 1.23) * mm]});
            skFitSpline(sketch, "E3531", {"points": [v(80.82, 1.23) * mm, v(80.75, 1.19) * mm, v(80.7, 1.13) * mm, v(80.61, 1.08) * mm]});
            skFitSpline(sketch, "E3532", {"points": [v(80.61, 1.08) * mm, v(80.7, 1.02) * mm, v(80.75, 0.96) * mm, v(80.81, 0.93) * mm]});
            skFitSpline(sketch, "E3533", {"points": [v(80.81, 0.93) * mm, v(81.38, 0.59) * mm, v(81.94, 0.26) * mm, v(82.5, -0.08) * mm]});
            skFitSpline(sketch, "E3534", {"points": [v(82.5, -0.08) * mm, v(82.73, -0.21) * mm, v(82.96, -0.34) * mm, v(83.18, -0.48) * mm]});
            skFitSpline(sketch, "E3535", {"points": [v(83.18, -0.48) * mm, v(83.36, -0.6) * mm, v(83.44, -0.77) * mm, v(83.4, -0.98) * mm]});
            skFitSpline(sketch, "E3536", {"points": [v(83.4, -0.98) * mm, v(83.35, -1.19) * mm, v(83.22, -1.33) * mm, v(83.01, -1.35) * mm]});
            skFitSpline(sketch, "E3537", {"points": [v(83.01, -1.35) * mm, v(82.9, -1.37) * mm, v(82.75, -1.34) * mm, v(82.65, -1.28) * mm]});
            skFitSpline(sketch, "E3538", {"points": [v(82.65, -1.28) * mm, v(81.88, -0.84) * mm, v(81.13, -0.4) * mm, v(80.37, 0.05) * mm]});
            skFitSpline(sketch, "E3539", {"points": [v(80.37, 0.05) * mm, v(80.16, 0.18) * mm, v(79.95, 0.3) * mm, v(79.74, 0.45) * mm]});
            skFitSpline(sketch, "E3540", {"points": [v(79.74, 0.45) * mm, v(79.65, 0.5) * mm, v(79.58, 0.5) * mm, v(79.48, 0.45) * mm]});
            skFitSpline(sketch, "E3541", {"points": [v(79.48, 0.45) * mm, v(79.16, 0.24) * mm, v(78.82, 0.05) * mm, v(78.5, -0.15) * mm]});
            skFitSpline(sketch, "E3542", {"points": [v(78.5, -0.15) * mm, v(78.3, -0.27) * mm, v(78.11, -0.38) * mm, v(77.88, -0.37) * mm]});
            skFitSpline(sketch, "E3543", {"points": [v(77.88, -0.37) * mm, v(77.82, -0.36) * mm, v(77.75, -0.4) * mm, v(77.7, -0.42) * mm]});
            skFitSpline(sketch, "E3544", {"points": [v(77.7, -0.42) * mm, v(76.75, -0.9) * mm, v(75.8, -1.36) * mm, v(74.8, -1.73) * mm]});
            skFitSpline(sketch, "E3545", {"points": [v(74.8, -1.73) * mm, v(74.66, -1.78) * mm, v(74.52, -1.86) * mm, v(74.36, -1.93) * mm]});
            skFitSpline(sketch, "E3546", {"points": [v(74.36, -1.93) * mm, v(74.43, -1.97) * mm, v(74.47, -2) * mm, v(74.52, -2.02) * mm]});
            skFitSpline(sketch, "E3547", {"points": [v(74.52, -2.02) * mm, v(75.03, -2.22) * mm, v(75.54, -2.42) * mm, v(76.05, -2.63) * mm]});
            skFitSpline(sketch, "E3548", {"points": [v(76.05, -2.63) * mm, v(76.16, -2.68) * mm, v(76.23, -2.67) * mm, v(76.34, -2.63) * mm]});
            skFitSpline(sketch, "E3549", {"points": [v(76.34, -2.63) * mm, v(76.84, -2.42) * mm, v(77.32, -2.16) * mm, v(77.78, -1.87) * mm]});
            skFitSpline(sketch, "E3550", {"points": [v(77.78, -1.87) * mm, v(77.89, -1.8) * mm, v(78, -1.75) * mm, v(78.12, -1.7) * mm]});
            skFitSpline(sketch, "E3551", {"points": [v(78.12, -1.7) * mm, v(78.4, -1.58) * mm, v(78.66, -1.66) * mm, v(78.78, -1.9) * mm]});
            skFitSpline(sketch, "E3552", {"points": [v(78.78, -1.9) * mm, v(78.9, -2.15) * mm, v(78.8, -2.42) * mm, v(78.54, -2.57) * mm]});
            skFitSpline(sketch, "E3553", {"points": [v(78.54, -2.57) * mm, v(78.24, -2.74) * mm, v(77.94, -2.91) * mm, v(77.65, -3.08) * mm]});
            skFitSpline(sketch, "E3554", {"points": [v(77.65, -3.08) * mm, v(77.59, -3.12) * mm, v(77.53, -3.16) * mm, v(77.45, -3.21) * mm]});
            skFitSpline(sketch, "E3555", {"points": [v(77.45, -3.21) * mm, v(77.74, -3.33) * mm, v(78, -3.43) * mm, v(78.23, -3.52) * mm]});
            skFitSpline(sketch, "E3556", {"points": [v(78.23, -3.52) * mm, v(78.5, -3.38) * mm, v(78.74, -3.25) * mm, v(78.98, -3.13) * mm]});
            skFitSpline(sketch, "E3557", {"points": [v(78.98, -3.13) * mm, v(79.24, -3) * mm, v(79.52, -2.9) * mm, v(79.79, -2.77) * mm]});
            skFitSpline(sketch, "E3558", {"points": [v(79.79, -2.77) * mm, v(80, -2.68) * mm, v(80.18, -2.56) * mm, v(80.39, -2.48) * mm]});
            skFitSpline(sketch, "E3559", {"points": [v(80.39, -2.48) * mm, v(80.5, -2.43) * mm, v(80.65, -2.39) * mm, v(80.78, -2.4) * mm]});
            skFitSpline(sketch, "E3560", {"points": [v(80.78, -2.4) * mm, v(80.97, -2.42) * mm, v(81.1, -2.56) * mm, v(81.16, -2.75) * mm]});
            skFitSpline(sketch, "E3561", {"points": [v(81.16, -2.75) * mm, v(81.2, -2.96) * mm, v(81.14, -3.14) * mm, v(80.97, -3.26) * mm]});
            skFitSpline(sketch, "E3562", {"points": [v(80.97, -3.26) * mm, v(80.84, -3.35) * mm, v(80.7, -3.43) * mm, v(80.55, -3.5) * mm]});
            skFitSpline(sketch, "E3563", {"points": [v(80.55, -3.5) * mm, v(80.03, -3.74) * mm, v(79.5, -3.98) * mm, v(78.96, -4.22) * mm]});
            skFitSpline(sketch, "E3564", {"points": [v(78.96, -4.22) * mm, v(78.88, -4.26) * mm, v(78.78, -4.28) * mm, v(78.71, -4.3) * mm]});
            skFitSpline(sketch, "E3565", {"points": [v(78.71, -4.3) * mm, v(78.8, -4.52) * mm, v(78.87, -4.73) * mm, v(78.95, -4.95) * mm]});
            skFitSpline(sketch, "E3566", {"points": [v(78.95, -4.95) * mm, v(79.1, -5.34) * mm, v(79.26, -5.74) * mm, v(79.41, -6.13) * mm]});
            skFitSpline(sketch, "E3567", {"points": [v(79.41, -6.13) * mm, v(79.47, -6.29) * mm, v(79.52, -6.45) * mm, v(79.56, -6.61) * mm]});
            skFitSpline(sketch, "E3568", {"points": [v(79.56, -6.61) * mm, v(79.62, -6.89) * mm, v(79.46, -7.13) * mm, v(79.2, -7.2) * mm]});
            skFitSpline(sketch, "E3569", {"points": [v(79.2, -7.2) * mm, v(78.97, -7.27) * mm, v(78.72, -7.13) * mm, v(78.63, -6.89) * mm]});
            skFitSpline(sketch, "E3570", {"points": [v(78.63, -6.89) * mm, v(78.57, -6.75) * mm, v(78.55, -6.6) * mm, v(78.5, -6.45) * mm]});
            skFitSpline(sketch, "E3571", {"points": [v(78.5, -6.45) * mm, v(78.35, -6.09) * mm, v(78.2, -5.72) * mm, v(78.07, -5.36) * mm]});
            skFitSpline(sketch, "E3572", {"points": [v(78.07, -5.36) * mm, v(78, -5.2) * mm, v(77.95, -5.04) * mm, v(77.9, -4.88) * mm]});
            skFitSpline(sketch, "E3573", {"points": [v(77.9, -4.88) * mm, v(77.88, -4.78) * mm, v(77.87, -4.67) * mm, v(77.85, -4.55) * mm]});
            skFitSpline(sketch, "E3574", {"points": [v(77.85, -4.55) * mm, v(77.6, -4.44) * mm, v(77.33, -4.32) * mm, v(77.04, -4.2) * mm]});
            skFitSpline(sketch, "E3575", {"points": [v(77.04, -4.2) * mm, v(77.06, -4.3) * mm, v(77.07, -4.39) * mm, v(77.1, -4.47) * mm]});
            skFitSpline(sketch, "E3576", {"points": [v(77.1, -4.47) * mm, v(77.18, -4.8) * mm, v(77.28, -5.11) * mm, v(77.36, -5.44) * mm]});
            skFitSpline(sketch, "E3577", {"points": [v(77.36, -5.44) * mm, v(77.41, -5.64) * mm, v(77.39, -5.82) * mm, v(77.23, -5.97) * mm]});
            skFitSpline(sketch, "E3578", {"points": [v(77.23, -5.97) * mm, v(77.09, -6.1) * mm, v(76.93, -6.12) * mm, v(76.76, -6.07) * mm]});
            skFitSpline(sketch, "E3579", {"points": [v(76.76, -6.07) * mm, v(76.6, -6.02) * mm, v(76.49, -5.9) * mm, v(76.44, -5.74) * mm]});
            skFitSpline(sketch, "E3580", {"points": [v(76.44, -5.74) * mm, v(76.36, -5.5) * mm, v(76.3, -5.26) * mm, v(76.23, -5.02) * mm]});
            skFitSpline(sketch, "E3581", {"points": [v(76.23, -5.02) * mm, v(76.1, -4.61) * mm, v(75.96, -4.2) * mm, v(75.83, -3.8) * mm]});
            skFitSpline(sketch, "E3582", {"points": [v(75.83, -3.8) * mm, v(75.8, -3.72) * mm, v(75.76, -3.66) * mm, v(75.68, -3.63) * mm]});
            skFitSpline(sketch, "E3583", {"points": [v(75.68, -3.63) * mm, v(75.14, -3.4) * mm, v(74.6, -3.18) * mm, v(74.07, -2.95) * mm]});
            skFitSpline(sketch, "E3584", {"points": [v(74.07, -2.95) * mm, v(74.04, -2.94) * mm, v(74.02, -2.93) * mm, v(73.95, -2.9) * mm]});
            skFitSpline(sketch, "E3585", {"points": [v(73.95, -2.9) * mm, v(74.02, -3.1) * mm, v(74.08, -3.26) * mm, v(74.14, -3.42) * mm]});
            skFitSpline(sketch, "E3586", {"points": [v(74.14, -3.42) * mm, v(74.35, -3.96) * mm, v(74.57, -4.49) * mm, v(74.77, -5.03) * mm]});
            skFitSpline(sketch, "E3587", {"points": [v(74.77, -5.03) * mm, v(74.94, -5.47) * mm, v(75.1, -5.93) * mm, v(75.25, -6.38) * mm]});
            skFitSpline(sketch, "E3588", {"points": [v(75.25, -6.38) * mm, v(75.27, -6.43) * mm, v(75.3, -6.48) * mm, v(75.34, -6.52) * mm]});
            skFitSpline(sketch, "E3589", {"points": [v(75.34, -6.52) * mm, v(75.5, -6.66) * mm, v(75.55, -6.85) * mm, v(75.6, -7.04) * mm]});
            skFitSpline(sketch, "E3590", {"points": [v(75.6, -7.04) * mm, v(75.7, -7.42) * mm, v(75.8, -7.8) * mm, v(75.88, -8.18) * mm]});
            skFitSpline(sketch, "E3591", {"points": [v(75.88, -8.18) * mm, v(75.9, -8.33) * mm, v(75.99, -8.4) * mm, v(76.13, -8.42) * mm]});
            skFitSpline(sketch, "E3592", {"points": [v(76.13, -8.42) * mm, v(76.47, -8.5) * mm, v(76.82, -8.56) * mm, v(77.16, -8.65) * mm]});
            skFitSpline(sketch, "E3593", {"points": [v(77.16, -8.65) * mm, v(77.68, -8.78) * mm, v(78.2, -8.93) * mm, v(78.7, -9.06) * mm]});
            skFitSpline(sketch, "E3594", {"points": [v(78.7, -9.06) * mm, v(78.92, -9.12) * mm, v(79.14, -9.17) * mm, v(79.35, -9.24) * mm]});
            skFitSpline(sketch, "E3595", {"points": [v(79.35, -9.24) * mm, v(79.61, -9.32) * mm, v(79.71, -9.47) * mm, v(79.74, -9.7) * mm]});
            skFitSpline(sketch, "E3596", {"points": [v(79.74, -9.7) * mm, v(79.76, -10) * mm, v(79.48, -10.26) * mm, v(79.15, -10.19) * mm]});
            skFitSpline(sketch, "E3597", {"points": [v(79.15, -10.19) * mm, v(78.94, -10.14) * mm, v(78.73, -10.08) * mm, v(78.53, -10.03) * mm]});
            skFitSpline(sketch, "E3598", {"points": [v(78.53, -10.03) * mm, v(77.85, -9.85) * mm, v(77.17, -9.68) * mm, v(76.49, -9.5) * mm]});
            skFitSpline(sketch, "E3599", {"points": [v(76.49, -9.5) * mm, v(76.42, -9.49) * mm, v(76.35, -9.48) * mm, v(76.24, -9.46) * mm]});
            skFitSpline(sketch, "E3600", {"points": [v(76.24, -9.46) * mm, v(76.27, -9.65) * mm, v(76.3, -9.82) * mm, v(76.33, -9.98) * mm]});
            skFitSpline(sketch, "E3601", {"points": [v(76.33, -9.98) * mm, v(76.47, -10.53) * mm, v(76.62, -11.08) * mm, v(76.77, -11.63) * mm]});
            skFitSpline(sketch, "E3602", {"points": [v(76.77, -11.63) * mm, v(76.83, -11.87) * mm, v(76.9, -12.12) * mm, v(76.96, -12.37) * mm]});
            skFitSpline(sketch, "E3603", {"points": [v(76.96, -12.37) * mm, v(77.03, -12.63) * mm, v(76.9, -12.86) * mm, v(76.63, -12.95) * mm]});
            skFitSpline(sketch, "E3604", {"points": [v(76.63, -12.95) * mm, v(76.42, -13.02) * mm, v(76.19, -12.92) * mm, v(76.07, -12.7) * mm]});
            skFitSpline(sketch, "E3605", {"points": [v(76.07, -12.7) * mm, v(76.04, -12.65) * mm, v(76.01, -12.59) * mm, v(76, -12.53) * mm]});
            skFitSpline(sketch, "E3606", {"points": [v(76, -12.53) * mm, v(75.77, -11.59) * mm, v(75.44, -10.68) * mm, v(75.3, -9.72) * mm]});
            skFitSpline(sketch, "E3607", {"points": [v(75.3, -9.72) * mm, v(75.26, -9.54) * mm, v(75.2, -9.36) * mm, v(75.14, -9.15) * mm]});
            skFitSpline(sketch, "E3608", {"points": [v(75.14, -9.15) * mm, v(74.84, -9.07) * mm, v(74.51, -8.98) * mm, v(74.2, -8.9) * mm]});
            skFitSpline(sketch, "E3609", {"points": [v(74.2, -8.9) * mm, v(74.04, -8.87) * mm, v(73.9, -8.85) * mm, v(73.75, -8.8) * mm]});
            skFitSpline(sketch, "E3610", {"points": [v(73.75, -8.8) * mm, v(73.62, -8.76) * mm, v(73.48, -8.72) * mm, v(73.39, -8.63) * mm]});
            skFitSpline(sketch, "E3611", {"points": [v(73.39, -8.63) * mm, v(73.26, -8.51) * mm, v(73.12, -8.47) * mm, v(72.97, -8.42) * mm]});
            skFitSpline(sketch, "E3612", {"points": [v(72.97, -8.42) * mm, v(72.62, -8.3) * mm, v(72.28, -8.17) * mm, v(71.93, -8.04) * mm]});
            skFitSpline(sketch, "E3613", {"points": [v(71.93, -8.04) * mm, v(71.68, -7.95) * mm, v(71.42, -7.88) * mm, v(71.16, -7.77) * mm]});
            skFitSpline(sketch, "E3614", {"points": [v(71.16, -7.77) * mm, v(70.68, -7.58) * mm, v(70.2, -7.38) * mm, v(69.72, -7.17) * mm]});
            skFitSpline(sketch, "E3615", {"points": [v(69.72, -7.17) * mm, v(69.71, -7.21) * mm, v(69.7, -7.24) * mm, v(69.71, -7.25) * mm]});
            skFitSpline(sketch, "E3616", {"points": [v(69.71, -7.25) * mm, v(69.95, -7.81) * mm, v(70.18, -8.37) * mm, v(70.42, -8.92) * mm]});
            skFitSpline(sketch, "E3617", {"points": [v(70.42, -8.92) * mm, v(70.45, -8.98) * mm, v(70.52, -9.02) * mm, v(70.58, -9.05) * mm]});
            skFitSpline(sketch, "E3618", {"points": [v(70.58, -9.05) * mm, v(71.1, -9.29) * mm, v(71.66, -9.43) * mm, v(72.22, -9.57) * mm]});
            skFitSpline(sketch, "E3619", {"points": [v(72.22, -9.57) * mm, v(72.32, -9.6) * mm, v(72.42, -9.62) * mm, v(72.52, -9.66) * mm]});
            skFitSpline(sketch, "E3620", {"points": [v(72.52, -9.66) * mm, v(72.8, -9.78) * mm, v(72.94, -10.03) * mm, v(72.84, -10.3) * mm]});
            skFitSpline(sketch, "E3621", {"points": [v(72.84, -10.3) * mm, v(72.75, -10.54) * mm, v(72.5, -10.66) * mm, v(72.21, -10.58) * mm]});
            skFitSpline(sketch, "E3622", {"points": [v(72.21, -10.58) * mm, v(71.88, -10.5) * mm, v(71.55, -10.4) * mm, v(71.22, -10.31) * mm]});
            skFitSpline(sketch, "E3623", {"points": [v(71.22, -10.31) * mm, v(71.15, -10.3) * mm, v(71.08, -10.28) * mm, v(70.98, -10.25) * mm]});
            skFitSpline(sketch, "E3624", {"points": [v(70.98, -10.25) * mm, v(71.1, -10.55) * mm, v(71.22, -10.81) * mm, v(71.33, -11.09) * mm]});
            skFitSpline(sketch, "E3625", {"points": [v(71.33, -11.09) * mm, v(71.65, -11.1) * mm, v(71.93, -11.21) * mm, v(72.22, -11.32) * mm]});
            skFitSpline(sketch, "E3626", {"points": [v(72.22, -11.32) * mm, v(72.7, -11.5) * mm, v(73.16, -11.67) * mm, v(73.64, -11.83) * mm]});
            skFitSpline(sketch, "E3627", {"points": [v(73.64, -11.83) * mm, v(73.88, -11.92) * mm, v(74.04, -12.16) * mm, v(73.99, -12.4) * mm]});
            skFitSpline(sketch, "E3628", {"points": [v(73.99, -12.4) * mm, v(73.93, -12.66) * mm, v(73.72, -12.82) * mm, v(73.45, -12.78) * mm]});
            skFitSpline(sketch, "E3629", {"points": [v(73.45, -12.78) * mm, v(73.29, -12.77) * mm, v(73.13, -12.72) * mm, v(72.98, -12.66) * mm]});
            skFitSpline(sketch, "E3630", {"points": [v(72.98, -12.66) * mm, v(72.43, -12.46) * mm, v(71.88, -12.25) * mm, v(71.33, -12.04) * mm]});
            skFitSpline(sketch, "E3631", {"points": [v(71.33, -12.04) * mm, v(71.24, -12) * mm, v(71.16, -11.95) * mm, v(71.1, -11.92) * mm]});
            skFitSpline(sketch, "E3632", {"points": [v(71.1, -11.92) * mm, v(71.03, -12.07) * mm, v(70.97, -12.21) * mm, v(70.9, -12.36) * mm]});
            skFitSpline(sketch, "E3633", {"points": [v(70.9, -12.36) * mm, v(70.71, -12.8) * mm, v(70.52, -13.25) * mm, v(70.31, -13.7) * mm]});
            skFitSpline(sketch, "E3634", {"points": [v(70.31, -13.7) * mm, v(70.24, -13.84) * mm, v(70.17, -14) * mm, v(70.08, -14.14) * mm]});
            skFitSpline(sketch, "E3635", {"points": [v(70.08, -14.14) * mm, v(69.91, -14.4) * mm, v(69.64, -14.47) * mm, v(69.4, -14.32) * mm]});
            skFitSpline(sketch, "E3636", {"points": [v(69.4, -14.32) * mm, v(69.17, -14.19) * mm, v(69.1, -13.91) * mm, v(69.23, -13.65) * mm]});
            skFitSpline(sketch, "E3637", {"points": [v(69.23, -13.65) * mm, v(69.46, -13.15) * mm, v(69.69, -12.65) * mm, v(69.93, -12.15) * mm]});
            skFitSpline(sketch, "E3638", {"points": [v(69.93, -12.15) * mm, v(70.03, -11.93) * mm, v(70.16, -11.72) * mm, v(70.3, -11.46) * mm]});
            skFitSpline(sketch, "E3639", {"points": [v(70.3, -11.46) * mm, v(70.22, -11.25) * mm, v(70.11, -10.98) * mm, v(70, -10.67) * mm]});
            skFitSpline(sketch, "E3640", {"points": [v(70, -10.67) * mm, v(69.93, -10.77) * mm, v(69.88, -10.83) * mm, v(69.84, -10.9) * mm]});
            skFitSpline(sketch, "E3641", {"points": [v(69.84, -10.9) * mm, v(69.67, -11.2) * mm, v(69.5, -11.5) * mm, v(69.33, -11.8) * mm]});
            skFitSpline(sketch, "E3642", {"points": [v(69.33, -11.8) * mm, v(69.2, -12) * mm, v(69, -12.09) * mm, v(68.78, -12.04) * mm]});
            skFitSpline(sketch, "E3643", {"points": [v(68.78, -12.04) * mm, v(68.6, -12) * mm, v(68.43, -11.84) * mm, v(68.43, -11.64) * mm]});
            skFitSpline(sketch, "E3644", {"points": [v(68.43, -11.64) * mm, v(68.42, -11.52) * mm, v(68.45, -11.38) * mm, v(68.5, -11.27) * mm]});
            skFitSpline(sketch, "E3645", {"points": [v(68.5, -11.27) * mm, v(68.64, -11.01) * mm, v(68.8, -10.78) * mm, v(68.93, -10.52) * mm]});
            skFitSpline(sketch, "E3646", {"points": [v(68.93, -10.52) * mm, v(69.1, -10.19) * mm, v(69.27, -9.85) * mm, v(69.42, -9.5) * mm]});
            skFitSpline(sketch, "E3647", {"points": [v(69.42, -9.5) * mm, v(69.45, -9.46) * mm, v(69.46, -9.38) * mm, v(69.43, -9.33) * mm]});
            skFitSpline(sketch, "E3648", {"points": [v(69.43, -9.33) * mm, v(69.2, -8.76) * mm, v(68.98, -8.2) * mm, v(68.74, -7.62) * mm]});
            skFitSpline(sketch, "E3649", {"points": [v(68.74, -7.62) * mm, v(68.74, -7.62) * mm, v(68.73, -7.61) * mm, v(68.7, -7.59) * mm]});
            skFitSpline(sketch, "E3650", {"points": [v(68.7, -7.59) * mm, v(68.63, -7.76) * mm, v(68.56, -7.92) * mm, v(68.49, -8.08) * mm]});
            skFitSpline(sketch, "E3651", {"points": [v(68.49, -8.08) * mm, v(68.26, -8.6) * mm, v(68.03, -9.14) * mm, v(67.8, -9.66) * mm]});
            skFitSpline(sketch, "E3652", {"points": [v(67.8, -9.66) * mm, v(67.6, -10.09) * mm, v(67.4, -10.5) * mm, v(67.2, -10.93) * mm]});
            skFitSpline(sketch, "E3653", {"points": [v(67.2, -10.93) * mm, v(67.17, -10.98) * mm, v(67.15, -11.04) * mm, v(67.15, -11.1) * mm]});
            skFitSpline(sketch, "E3654", {"points": [v(67.15, -11.1) * mm, v(67.16, -11.32) * mm, v(67.06, -11.51) * mm, v(66.94, -11.7) * mm]});
            skFitSpline(sketch, "E3655", {"points": [v(66.94, -11.7) * mm, v(66.74, -12.02) * mm, v(66.55, -12.35) * mm, v(66.34, -12.68) * mm]});
            skFitSpline(sketch, "E3656", {"points": [v(66.34, -12.68) * mm, v(66.28, -12.79) * mm, v(66.26, -12.88) * mm, v(66.35, -12.98) * mm]});
            skFitSpline(sketch, "E3657", {"points": [v(66.35, -12.98) * mm, v(66.37, -13.02) * mm, v(66.38, -13.05) * mm, v(66.4, -13.09) * mm]});
            skFitSpline(sketch, "E3658", {"points": [v(66.4, -13.09) * mm, v(67, -13.94) * mm, v(67.48, -14.86) * mm, v(68, -15.76) * mm]});
            skFitSpline(sketch, "E3659", {"points": [v(68, -15.76) * mm, v(68.09, -15.9) * mm, v(68.17, -16.04) * mm, v(68.14, -16.2) * mm]});
            skFitSpline(sketch, "E3660", {"points": [v(68.14, -16.2) * mm, v(68.11, -16.42) * mm, v(67.95, -16.59) * mm, v(67.76, -16.62) * mm]});
            skFitSpline(sketch, "E3661", {"points": [v(67.76, -16.62) * mm, v(67.54, -16.66) * mm, v(67.36, -16.58) * mm, v(67.24, -16.39) * mm]});
            skFitSpline(sketch, "E3662", {"points": [v(67.24, -16.39) * mm, v(67.1, -16.17) * mm, v(66.99, -15.95) * mm, v(66.86, -15.73) * mm]});
            skFitSpline(sketch, "E3663", {"points": [v(66.86, -15.73) * mm, v(66.52, -15.16) * mm, v(66.18, -14.59) * mm, v(65.84, -14.02) * mm]});
            skFitSpline(sketch, "E3664", {"points": [v(65.84, -14.02) * mm, v(65.8, -13.96) * mm, v(65.76, -13.9) * mm, v(65.7, -13.83) * mm]});
            skFitSpline(sketch, "E3665", {"points": [v(65.7, -13.83) * mm, v(65.57, -14.02) * mm, v(65.45, -14.18) * mm, v(65.34, -14.36) * mm]});
            skFitSpline(sketch, "E3666", {"points": [v(65.34, -14.36) * mm, v(65.08, -14.8) * mm, v(64.82, -15.25) * mm, v(64.56, -15.7) * mm]});
            skFitSpline(sketch, "E3667", {"points": [v(64.56, -15.7) * mm, v(64.43, -15.93) * mm, v(64.31, -16.15) * mm, v(64.18, -16.37) * mm]});
            skFitSpline(sketch, "E3668", {"points": [v(64.18, -16.37) * mm, v(64.02, -16.62) * mm, v(63.75, -16.7) * mm, v(63.52, -16.57) * mm]});
            skFitSpline(sketch, "E3669", {"points": [v(63.52, -16.57) * mm, v(63.28, -16.44) * mm, v(63.2, -16.17) * mm, v(63.32, -15.9) * mm]});
            skFitSpline(sketch, "E3670", {"points": [v(63.32, -15.9) * mm, v(63.43, -15.69) * mm, v(63.57, -15.48) * mm, v(63.7, -15.26) * mm]});
            skFitSpline(sketch, "E3671", {"points": [v(63.7, -15.26) * mm, v(64.07, -14.64) * mm, v(64.44, -14.02) * mm, v(64.81, -13.4) * mm]});
            skFitSpline(sketch, "E3672", {"points": [v(64.81, -13.4) * mm, v(64.92, -13.2) * mm, v(65.03, -13.03) * mm, v(65.16, -12.82) * mm]});
            skFitSpline(sketch, "E3673", {"points": [v(65.16, -12.82) * mm, v(64.93, -12.46) * mm, v(64.71, -12.1) * mm, v(64.5, -11.74) * mm]});
            skFitSpline(sketch, "E3674", {"points": [v(64.5, -11.74) * mm, v(64.37, -11.54) * mm, v(64.25, -11.34) * mm, v(64.26, -11.1) * mm]});
            skFitSpline(sketch, "E3675", {"points": [v(64.26, -11.1) * mm, v(64.27, -11.04) * mm, v(64.24, -10.97) * mm, v(64.2, -10.92) * mm]});
            skFitSpline(sketch, "E3676", {"points": [v(64.2, -10.92) * mm, v(63.71, -9.98) * mm, v(63.27, -9.01) * mm, v(62.9, -8.02) * mm]});
            skFitSpline(sketch, "E3677", {"points": [v(62.9, -8.02) * mm, v(62.84, -7.88) * mm, v(62.77, -7.75) * mm, v(62.69, -7.58) * mm]});
            skFitSpline(sketch, "E3678", {"points": [v(62.69, -7.58) * mm, v(62.43, -8.2) * mm, v(62.2, -8.8) * mm, v(61.94, -9.43) * mm]});
            skFitSpline(sketch, "E3679", {"points": [v(61.94, -9.43) * mm, v(62.08, -9.72) * mm, v(62.22, -10.05) * mm, v(62.39, -10.37) * mm]});
            skFitSpline(sketch, "E3680", {"points": [v(62.39, -10.37) * mm, v(62.5, -10.6) * mm, v(62.64, -10.8) * mm, v(62.77, -11.03) * mm]});
            skFitSpline(sketch, "E3681", {"points": [v(62.77, -11.03) * mm, v(62.83, -11.12) * mm, v(62.88, -11.21) * mm, v(62.92, -11.3) * mm]});
            skFitSpline(sketch, "E3682", {"points": [v(62.92, -11.3) * mm, v(63.06, -11.6) * mm, v(62.97, -11.89) * mm, v(62.72, -12) * mm]});
            skFitSpline(sketch, "E3683", {"points": [v(62.72, -12) * mm, v(62.47, -12.13) * mm, v(62.2, -12.01) * mm, v(62.04, -11.73) * mm]});
            skFitSpline(sketch, "E3684", {"points": [v(62.04, -11.73) * mm, v(61.86, -11.4) * mm, v(61.67, -11.08) * mm, v(61.48, -10.76) * mm]});
            skFitSpline(sketch, "E3685", {"points": [v(61.48, -10.76) * mm, v(61.47, -10.74) * mm, v(61.45, -10.72) * mm, v(61.41, -10.68) * mm]});
            skFitSpline(sketch, "E3686", {"points": [v(61.41, -10.68) * mm, v(61.3, -10.97) * mm, v(61.2, -11.24) * mm, v(61.1, -11.46) * mm]});
            skFitSpline(sketch, "E3687", {"points": [v(61.1, -11.46) * mm, v(61.25, -11.72) * mm, v(61.38, -11.95) * mm, v(61.5, -12.18) * mm]});
            skFitSpline(sketch, "E3688", {"points": [v(61.5, -12.18) * mm, v(61.63, -12.47) * mm, v(61.74, -12.77) * mm, v(61.88, -13.06) * mm]});
            skFitSpline(sketch, "E3689", {"points": [v(61.88, -13.06) * mm, v(61.96, -13.24) * mm, v(62.07, -13.41) * mm, v(62.14, -13.6) * mm]});
            skFitSpline(sketch, "E3690", {"points": [v(62.14, -13.6) * mm, v(62.2, -13.72) * mm, v(62.24, -13.85) * mm, v(62.23, -13.98) * mm]});
            skFitSpline(sketch, "E3691", {"points": [v(62.23, -13.98) * mm, v(62.22, -14.19) * mm, v(62.08, -14.33) * mm, v(61.87, -14.38) * mm]});
            skFitSpline(sketch, "E3692", {"points": [v(61.87, -14.38) * mm, v(61.67, -14.43) * mm, v(61.5, -14.36) * mm, v(61.38, -14.2) * mm]});
            skFitSpline(sketch, "E3693", {"points": [v(61.38, -14.2) * mm, v(61.28, -14.07) * mm, v(61.2, -13.92) * mm, v(61.13, -13.77) * mm]});
            skFitSpline(sketch, "E3694", {"points": [v(61.13, -13.77) * mm, v(60.88, -13.24) * mm, v(60.65, -12.71) * mm, v(60.4, -12.18) * mm]});
            skFitSpline(sketch, "E3695", {"points": [v(60.4, -12.18) * mm, v(60.37, -12.1) * mm, v(60.35, -12) * mm, v(60.33, -11.93) * mm]});
            skFitSpline(sketch, "E3696", {"points": [v(60.33, -11.93) * mm, v(60.18, -11.99) * mm, v(60.03, -12.05) * mm, v(59.89, -12.1) * mm]});
            skFitSpline(sketch, "E3697", {"points": [v(59.89, -12.1) * mm, v(59.44, -12.28) * mm, v(59, -12.45) * mm, v(58.54, -12.62) * mm]});
            skFitSpline(sketch, "E3698", {"points": [v(58.54, -12.62) * mm, v(58.38, -12.68) * mm, v(58.21, -12.74) * mm, v(58.04, -12.78) * mm]});
            skFitSpline(sketch, "E3699", {"points": [v(58.04, -12.78) * mm, v(57.82, -12.83) * mm, v(57.63, -12.77) * mm, v(57.5, -12.58) * mm]});
            skFitSpline(sketch, "E3700", {"points": [v(57.5, -12.58) * mm, v(57.38, -12.4) * mm, v(57.37, -12.2) * mm, v(57.5, -12.04) * mm]});
            skFitSpline(sketch, "E3701", {"points": [v(57.5, -12.04) * mm, v(57.57, -11.95) * mm, v(57.68, -11.88) * mm, v(57.79, -11.83) * mm]});
            skFitSpline(sketch, "E3702", {"points": [v(57.79, -11.83) * mm, v(58.25, -11.66) * mm, v(58.71, -11.5) * mm, v(59.18, -11.32) * mm]});
            skFitSpline(sketch, "E3703", {"points": [v(59.18, -11.32) * mm, v(59.47, -11.22) * mm, v(59.76, -11.1) * mm, v(60.07, -11.09) * mm]});
            skFitSpline(sketch, "E3704", {"points": [v(60.07, -11.09) * mm, v(60.19, -10.82) * mm, v(60.3, -10.56) * mm, v(60.43, -10.26) * mm]});
            skFitSpline(sketch, "E3705", {"points": [v(60.43, -10.26) * mm, v(60.2, -10.31) * mm, v(60.02, -10.35) * mm, v(59.83, -10.4) * mm]});
            skFitSpline(sketch, "E3706", {"points": [v(59.83, -10.4) * mm, v(59.6, -10.46) * mm, v(59.38, -10.53) * mm, v(59.16, -10.59) * mm]});
            skFitSpline(sketch, "E3707", {"points": [v(59.16, -10.59) * mm, v(58.9, -10.65) * mm, v(58.66, -10.53) * mm, v(58.57, -10.3) * mm]});
            skFitSpline(sketch, "E3708", {"points": [v(58.57, -10.3) * mm, v(58.48, -10.07) * mm, v(58.57, -9.83) * mm, v(58.8, -9.7) * mm]});
            skFitSpline(sketch, "E3709", {"points": [v(58.8, -9.7) * mm, v(58.9, -9.65) * mm, v(59.04, -9.6) * mm, v(59.17, -9.57) * mm]});
            skFitSpline(sketch, "E3710", {"points": [v(59.17, -9.57) * mm, v(59.73, -9.43) * mm, v(60.29, -9.29) * mm, v(60.82, -9.06) * mm]});
            skFitSpline(sketch, "E3711", {"points": [v(60.82, -9.06) * mm, v(60.9, -9.03) * mm, v(60.95, -9) * mm, v(61, -8.92) * mm]});
            skFitSpline(sketch, "E3712", {"points": [v(61, -8.92) * mm, v(61.22, -8.36) * mm, v(61.46, -7.81) * mm, v(61.7, -7.26) * mm]});
            skFitSpline(sketch, "E3713", {"points": [v(61.7, -7.26) * mm, v(61.7, -7.24) * mm, v(61.7, -7.22) * mm, v(61.7, -7.17) * mm]});
            skFitSpline(sketch, "E3714", {"points": [v(-19.93, -6.3) * mm, v(-19.95, -6.31) * mm, v(-19.97, -6.32) * mm, v(-20, -6.32) * mm]});
            skFitSpline(sketch, "E3715", {"points": [v(-20, -6.32) * mm, v(-20.06, -6.54) * mm, v(-20.13, -6.76) * mm, v(-20.2, -7) * mm]});
            skFitSpline(sketch, "E3716", {"points": [v(-20.2, -7) * mm, v(-19.88, -7.11) * mm, v(-19.57, -7.22) * mm, v(-19.27, -7.33) * mm]});
            skFitSpline(sketch, "E3717", {"points": [v(-19.27, -7.33) * mm, v(-19.26, -7.32) * mm, v(-19.25, -7.3) * mm, v(-19.24, -7.3) * mm]});
            skFitSpline(sketch, "E3718", {"points": [v(-19.24, -7.3) * mm, v(-19.47, -6.96) * mm, v(-19.7, -6.63) * mm, v(-19.93, -6.3) * mm]});
            skFitSpline(sketch, "E3719", {"points": [v(-16.06, -1.03) * mm, v(-15.93, -1.29) * mm, v(-15.82, -1.5) * mm, v(-15.7, -1.72) * mm]});
            skFitSpline(sketch, "E3720", {"points": [v(-15.7, -1.72) * mm, v(-15.4, -1.57) * mm, v(-15.1, -1.44) * mm, v(-14.82, -1.3) * mm]});
            skFitSpline(sketch, "E3721", {"points": [v(-14.82, -1.3) * mm, v(-14.82, -1.29) * mm, v(-14.82, -1.27) * mm, v(-14.82, -1.25) * mm]});
            skFitSpline(sketch, "E3722", {"points": [v(-14.82, -1.25) * mm, v(-15.22, -1.18) * mm, v(-15.61, -1.11) * mm, v(-16.06, -1.03) * mm]});
            skFitSpline(sketch, "E3723", {"points": [v(-19.24, 9.44) * mm, v(-19.25, 9.45) * mm, v(-19.27, 9.47) * mm, v(-19.28, 9.48) * mm]});
            skFitSpline(sketch, "E3724", {"points": [v(-19.28, 9.48) * mm, v(-19.58, 9.37) * mm, v(-19.9, 9.25) * mm, v(-20.2, 9.13) * mm]});
            skFitSpline(sketch, "E3725", {"points": [v(-20.2, 9.13) * mm, v(-20.12, 8.89) * mm, v(-20.05, 8.67) * mm, v(-19.97, 8.4) * mm]});
            skFitSpline(sketch, "E3726", {"points": [v(-19.97, 8.4) * mm, v(-19.7, 8.78) * mm, v(-19.48, 9.1) * mm, v(-19.24, 9.44) * mm]});
            skFitSpline(sketch, "E3727", {"points": [v(-27.11, -7.54) * mm, v(-26.97, -7.85) * mm, v(-26.83, -8.14) * mm, v(-26.7, -8.44) * mm]});
            skFitSpline(sketch, "E3728", {"points": [v(-26.7, -8.44) * mm, v(-26.58, -8.03) * mm, v(-26.47, -7.64) * mm, v(-26.45, -7.2) * mm]});
            skFitSpline(sketch, "E3729", {"points": [v(-26.45, -7.2) * mm, v(-26.69, -7.32) * mm, v(-26.88, -7.42) * mm, v(-27.11, -7.54) * mm]});
            skFitSpline(sketch, "E3730", {"points": [v(-16.98, -3.28) * mm, v(-16.6, -3.54) * mm, v(-16.28, -3.77) * mm, v(-15.94, -4) * mm]});
            skFitSpline(sketch, "E3731", {"points": [v(-15.94, -4) * mm, v(-15.93, -4) * mm, v(-15.92, -3.98) * mm, v(-15.9, -3.97) * mm]});
            skFitSpline(sketch, "E3732", {"points": [v(-15.9, -3.97) * mm, v(-16.02, -3.66) * mm, v(-16.14, -3.36) * mm, v(-16.26, -3.04) * mm]});
            skFitSpline(sketch, "E3733", {"points": [v(-16.26, -3.04) * mm, v(-16.5, -3.12) * mm, v(-16.71, -3.19) * mm, v(-16.98, -3.28) * mm]});
            skFitSpline(sketch, "E3734", {"points": [v(-31.65, 5.42) * mm, v(-32.03, 5.7) * mm, v(-32.36, 5.92) * mm, v(-32.69, 6.15) * mm]});
            skFitSpline(sketch, "E3735", {"points": [v(-32.69, 6.15) * mm, v(-32.7, 6.14) * mm, v(-32.71, 6.14) * mm, v(-32.73, 6.13) * mm]});
            skFitSpline(sketch, "E3736", {"points": [v(-32.73, 6.13) * mm, v(-32.61, 5.82) * mm, v(-32.5, 5.51) * mm, v(-32.38, 5.19) * mm]});
            skFitSpline(sketch, "E3737", {"points": [v(-32.38, 5.19) * mm, v(-32.14, 5.27) * mm, v(-31.92, 5.34) * mm, v(-31.65, 5.42) * mm]});
            skFitSpline(sketch, "E3738", {"points": [v(-32.93, -1.72) * mm, v(-32.8, -1.49) * mm, v(-32.7, -1.28) * mm, v(-32.58, -1.03) * mm]});
            skFitSpline(sketch, "E3739", {"points": [v(-32.58, -1.03) * mm, v(-33.03, -1.11) * mm, v(-33.43, -1.18) * mm, v(-33.82, -1.25) * mm]});
            skFitSpline(sketch, "E3740", {"points": [v(-33.82, -1.25) * mm, v(-33.82, -1.27) * mm, v(-33.82, -1.29) * mm, v(-33.82, -1.3) * mm]});
            skFitSpline(sketch, "E3741", {"points": [v(-33.82, -1.3) * mm, v(-33.53, -1.44) * mm, v(-33.24, -1.58) * mm, v(-32.93, -1.72) * mm]});
            skFitSpline(sketch, "E3742", {"points": [v(-22.2, -7.2) * mm, v(-22.17, -7.37) * mm, v(-22.16, -7.5) * mm, v(-22.14, -7.62) * mm]});
            skFitSpline(sketch, "E3743", {"points": [v(-22.14, -7.62) * mm, v(-22.1, -7.9) * mm, v(-22.04, -8.16) * mm, v(-21.99, -8.43) * mm]});
            skFitSpline(sketch, "E3744", {"points": [v(-21.99, -8.43) * mm, v(-21.97, -8.43) * mm, v(-21.96, -8.44) * mm, v(-21.94, -8.44) * mm]});
            skFitSpline(sketch, "E3745", {"points": [v(-21.94, -8.44) * mm, v(-21.8, -8.14) * mm, v(-21.67, -7.84) * mm, v(-21.52, -7.54) * mm]});
            skFitSpline(sketch, "E3746", {"points": [v(-21.52, -7.54) * mm, v(-21.75, -7.42) * mm, v(-21.95, -7.32) * mm, v(-22.2, -7.2) * mm]});
            skFitSpline(sketch, "E3747", {"points": [v(-28.43, -6.99) * mm, v(-28.51, -6.74) * mm, v(-28.58, -6.52) * mm, v(-28.67, -6.26) * mm]});
            skFitSpline(sketch, "E3748", {"points": [v(-28.67, -6.26) * mm, v(-28.93, -6.64) * mm, v(-29.16, -6.96) * mm, v(-29.4, -7.3) * mm]});
            skFitSpline(sketch, "E3749", {"points": [v(-29.4, -7.3) * mm, v(-29.38, -7.3) * mm, v(-29.37, -7.32) * mm, v(-29.36, -7.33) * mm]});
            skFitSpline(sketch, "E3750", {"points": [v(-29.36, -7.33) * mm, v(-29.05, -7.22) * mm, v(-28.75, -7.1) * mm, v(-28.43, -6.99) * mm]});
            skFitSpline(sketch, "E3751", {"points": [v(-32.38, -3.04) * mm, v(-32.5, -3.36) * mm, v(-32.61, -3.67) * mm, v(-32.72, -3.98) * mm]});
            skFitSpline(sketch, "E3752", {"points": [v(-32.72, -3.98) * mm, v(-32.36, -3.75) * mm, v(-32, -3.56) * mm, v(-31.68, -3.27) * mm]});
            skFitSpline(sketch, "E3753", {"points": [v(-31.68, -3.27) * mm, v(-31.93, -3.19) * mm, v(-32.14, -3.12) * mm, v(-32.38, -3.04) * mm]});
            skFitSpline(sketch, "E3754", {"points": [v(-15.9, 6.12) * mm, v(-15.92, 6.13) * mm, v(-15.94, 6.14) * mm, v(-15.95, 6.16) * mm]});
            skFitSpline(sketch, "E3755", {"points": [v(-15.95, 6.16) * mm, v(-16.27, 5.9) * mm, v(-16.64, 5.71) * mm, v(-16.96, 5.41) * mm]});
            skFitSpline(sketch, "E3756", {"points": [v(-16.96, 5.41) * mm, v(-16.7, 5.34) * mm, v(-16.49, 5.27) * mm, v(-16.25, 5.2) * mm]});
            skFitSpline(sketch, "E3757", {"points": [v(-16.25, 5.2) * mm, v(-16.13, 5.52) * mm, v(-16.02, 5.82) * mm, v(-15.9, 6.12) * mm]});
            skFitSpline(sketch, "E3758", {"points": [v(-21.94, 10.6) * mm, v(-21.96, 10.59) * mm, v(-21.98, 10.58) * mm, v(-22, 10.58) * mm]});
            skFitSpline(sketch, "E3759", {"points": [v(-22, 10.58) * mm, v(-22.04, 10.18) * mm, v(-22.16, 9.8) * mm, v(-22.18, 9.35) * mm]});
            skFitSpline(sketch, "E3760", {"points": [v(-22.18, 9.35) * mm, v(-21.94, 9.47) * mm, v(-21.74, 9.58) * mm, v(-21.52, 9.69) * mm]});
            skFitSpline(sketch, "E3761", {"points": [v(-21.52, 9.69) * mm, v(-21.67, 10) * mm, v(-21.8, 10.3) * mm, v(-21.94, 10.6) * mm]});
            skFitSpline(sketch, "E3762", {"points": [v(-28.7, 8.46) * mm, v(-28.69, 8.46) * mm, v(-28.67, 8.47) * mm, v(-28.65, 8.47) * mm]});
            skFitSpline(sketch, "E3763", {"points": [v(-28.65, 8.47) * mm, v(-28.58, 8.68) * mm, v(-28.5, 8.9) * mm, v(-28.43, 9.14) * mm]});
            skFitSpline(sketch, "E3764", {"points": [v(-28.43, 9.14) * mm, v(-28.75, 9.25) * mm, v(-29.06, 9.37) * mm, v(-29.36, 9.48) * mm]});
            skFitSpline(sketch, "E3765", {"points": [v(-29.36, 9.48) * mm, v(-29.37, 9.47) * mm, v(-29.38, 9.46) * mm, v(-29.4, 9.44) * mm]});
            skLineSegment(sketch, "E3766", {"start": v(-29.4, 9.44) * mm, "end": v(-28.7, 8.46) * mm});
            skFitSpline(sketch, "E3767", {"points": [v(-26.5, 9.37) * mm, v(-26.48, 9.38) * mm, v(-26.46, 9.39) * mm, v(-26.44, 9.4) * mm]});
            skFitSpline(sketch, "E3768", {"points": [v(-26.44, 9.4) * mm, v(-26.5, 9.79) * mm, v(-26.58, 10.19) * mm, v(-26.65, 10.58) * mm]});
            skFitSpline(sketch, "E3769", {"points": [v(-26.65, 10.58) * mm, v(-26.66, 10.58) * mm, v(-26.68, 10.59) * mm, v(-26.7, 10.59) * mm]});
            skFitSpline(sketch, "E3770", {"points": [v(-26.7, 10.59) * mm, v(-26.83, 10.29) * mm, v(-26.97, 10) * mm, v(-27.1, 9.69) * mm]});
            skFitSpline(sketch, "E3771", {"points": [v(-27.1, 9.69) * mm, v(-26.89, 9.57) * mm, v(-26.7, 9.47) * mm, v(-26.5, 9.37) * mm]});
            skFitSpline(sketch, "E3772", {"points": [v(-32.6, 3.2) * mm, v(-32.7, 3.43) * mm, v(-32.81, 3.64) * mm, v(-32.93, 3.87) * mm]});
            skFitSpline(sketch, "E3773", {"points": [v(-32.93, 3.87) * mm, v(-33.23, 3.72) * mm, v(-33.54, 3.6) * mm, v(-33.87, 3.4) * mm]});
            skFitSpline(sketch, "E3774", {"points": [v(-33.87, 3.4) * mm, v(-33.44, 3.33) * mm, v(-33.08, 3.27) * mm, v(-32.7, 3.2) * mm]});
            skFitSpline(sketch, "E3775", {"points": [v(-32.7, 3.2) * mm, v(-32.68, 3.2) * mm, v(-32.65, 3.2) * mm, v(-32.6, 3.2) * mm]});
            skFitSpline(sketch, "E3776", {"points": [v(-16.06, 3.18) * mm, v(-15.61, 3.26) * mm, v(-15.21, 3.33) * mm, v(-14.81, 3.4) * mm]});
            skFitSpline(sketch, "E3777", {"points": [v(-14.81, 3.4) * mm, v(-14.8, 3.42) * mm, v(-14.8, 3.43) * mm, v(-14.8, 3.45) * mm]});
            skFitSpline(sketch, "E3778", {"points": [v(-14.8, 3.45) * mm, v(-15.1, 3.59) * mm, v(-15.4, 3.73) * mm, v(-15.7, 3.87) * mm]});
            skFitSpline(sketch, "E3779", {"points": [v(-15.7, 3.87) * mm, v(-15.82, 3.64) * mm, v(-15.93, 3.43) * mm, v(-16.06, 3.18) * mm]});
            skFitSpline(sketch, "E3780", {"points": [v(-21.14, -0.22) * mm, v(-21.15, -0.23) * mm, v(-21.15, -0.24) * mm, v(-21.16, -0.26) * mm]});
            skFitSpline(sketch, "E3781", {"points": [v(-21.16, -0.26) * mm, v(-20.06, -1.05) * mm, v(-18.96, -1.84) * mm, v(-17.9, -2.6) * mm]});
            skFitSpline(sketch, "E3782", {"points": [v(-17.9, -2.6) * mm, v(-17.45, -2.43) * mm, v(-17.04, -2.27) * mm, v(-16.6, -2.1) * mm]});
            skFitSpline(sketch, "E3783", {"points": [v(-16.6, -2.1) * mm, v(-16.66, -2) * mm, v(-16.71, -1.9) * mm, v(-16.75, -1.81) * mm]});
            skFitSpline(sketch, "E3784", {"points": [v(-16.75, -1.81) * mm, v(-16.87, -1.54) * mm, v(-17, -1.26) * mm, v(-17.1, -0.98) * mm]});
            skFitSpline(sketch, "E3785", {"points": [v(-17.1, -0.98) * mm, v(-17.14, -0.88) * mm, v(-17.2, -0.86) * mm, v(-17.28, -0.85) * mm]});
            skFitSpline(sketch, "E3786", {"points": [v(-17.28, -0.85) * mm, v(-17.57, -0.8) * mm, v(-17.86, -0.75) * mm, v(-18.15, -0.7) * mm]});
            skFitSpline(sketch, "E3787", {"points": [v(-18.15, -0.7) * mm, v(-19, -0.56) * mm, v(-19.86, -0.42) * mm, v(-20.72, -0.28) * mm]});
            skFitSpline(sketch, "E3788", {"points": [v(-20.72, -0.28) * mm, v(-20.86, -0.25) * mm, v(-21, -0.24) * mm, v(-21.14, -0.22) * mm]});
            skFitSpline(sketch, "E3789", {"points": [v(-32.02, -2.1) * mm, v(-31.58, -2.27) * mm, v(-31.18, -2.43) * mm, v(-30.74, -2.6) * mm]});
            skFitSpline(sketch, "E3790", {"points": [v(-30.74, -2.6) * mm, v(-29.67, -1.83) * mm, v(-28.57, -1.04) * mm, v(-27.47, -0.25) * mm]});
            skFitSpline(sketch, "E3791", {"points": [v(-27.47, -0.25) * mm, v(-27.72, -0.25) * mm, v(-27.95, -0.28) * mm, v(-28.17, -0.32) * mm]});
            skFitSpline(sketch, "E3792", {"points": [v(-28.17, -0.32) * mm, v(-28.74, -0.42) * mm, v(-29.3, -0.51) * mm, v(-29.87, -0.6) * mm]});
            skFitSpline(sketch, "E3793", {"points": [v(-29.87, -0.6) * mm, v(-30.37, -0.7) * mm, v(-30.86, -0.77) * mm, v(-31.36, -0.85) * mm]});
            skFitSpline(sketch, "E3794", {"points": [v(-31.36, -0.85) * mm, v(-31.45, -0.86) * mm, v(-31.51, -0.9) * mm, v(-31.54, -1) * mm]});
            skFitSpline(sketch, "E3795", {"points": [v(-31.54, -1) * mm, v(-31.58, -1.14) * mm, v(-31.63, -1.28) * mm, v(-31.69, -1.4) * mm]});
            skFitSpline(sketch, "E3796", {"points": [v(-31.69, -1.4) * mm, v(-31.8, -1.64) * mm, v(-31.9, -1.87) * mm, v(-32.02, -2.1) * mm]});
            skFitSpline(sketch, "E3797", {"points": [v(-25.6, -2.1) * mm, v(-25.62, -2.09) * mm, v(-25.63, -2.08) * mm, v(-25.65, -2.08) * mm]});
            skFitSpline(sketch, "E3798", {"points": [v(-25.65, -2.08) * mm, v(-26.44, -3.18) * mm, v(-27.22, -4.28) * mm, v(-28, -5.35) * mm]});
            skFitSpline(sketch, "E3799", {"points": [v(-28, -5.35) * mm, v(-27.82, -5.8) * mm, v(-27.66, -6.2) * mm, v(-27.5, -6.62) * mm]});
            skFitSpline(sketch, "E3800", {"points": [v(-27.5, -6.62) * mm, v(-27.09, -6.43) * mm, v(-26.69, -6.25) * mm, v(-26.26, -6.06) * mm]});
            skFitSpline(sketch, "E3801", {"points": [v(-26.26, -6.06) * mm, v(-26.05, -4.76) * mm, v(-25.83, -3.43) * mm, v(-25.6, -2.1) * mm]});
            skFitSpline(sketch, "E3802", {"points": [v(-22.36, 8.22) * mm, v(-22.5, 7.7) * mm, v(-23.01, 4.42) * mm, v(-22.98, 4.24) * mm]});
            skFitSpline(sketch, "E3803", {"points": [v(-22.98, 4.24) * mm, v(-22.19, 5.35) * mm, v(-21.4, 6.44) * mm, v(-20.64, 7.5) * mm]});
            skFitSpline(sketch, "E3804", {"points": [v(-20.64, 7.5) * mm, v(-20.81, 7.94) * mm, v(-20.97, 8.35) * mm, v(-21.13, 8.77) * mm]});
            skFitSpline(sketch, "E3805", {"points": [v(-21.13, 8.77) * mm, v(-21.55, 8.58) * mm, v(-21.95, 8.4) * mm, v(-22.36, 8.22) * mm]});
            skFitSpline(sketch, "E3806", {"points": [v(-21.13, -6.62) * mm, v(-20.97, -6.2) * mm, v(-20.81, -5.79) * mm, v(-20.65, -5.36) * mm]});
            skFitSpline(sketch, "E3807", {"points": [v(-20.65, -5.36) * mm, v(-20.97, -4.83) * mm, v(-22.88, -2.2) * mm, v(-23.03, -2.1) * mm]});
            skFitSpline(sketch, "E3808", {"points": [v(-23.03, -2.1) * mm, v(-22.8, -3.45) * mm, v(-22.59, -4.77) * mm, v(-22.38, -6.06) * mm]});
            skFitSpline(sketch, "E3809", {"points": [v(-22.38, -6.06) * mm, v(-21.95, -6.25) * mm, v(-21.55, -6.43) * mm, v(-21.13, -6.62) * mm]});
            skFitSpline(sketch, "E3810", {"points": [v(-25.64, 4.22) * mm, v(-25.63, 4.23) * mm, v(-25.62, 4.23) * mm, v(-25.6, 4.24) * mm]});
            skFitSpline(sketch, "E3811", {"points": [v(-25.6, 4.24) * mm, v(-25.83, 5.58) * mm, v(-26.05, 6.92) * mm, v(-26.26, 8.2) * mm]});
            skFitSpline(sketch, "E3812", {"points": [v(-26.26, 8.2) * mm, v(-26.7, 8.4) * mm, v(-27.1, 8.59) * mm, v(-27.5, 8.77) * mm]});
            skFitSpline(sketch, "E3813", {"points": [v(-27.5, 8.77) * mm, v(-27.67, 8.34) * mm, v(-27.82, 7.93) * mm, v(-28, 7.5) * mm]});
            skFitSpline(sketch, "E3814", {"points": [v(-28, 7.5) * mm, v(-27.22, 6.42) * mm, v(-26.43, 5.32) * mm, v(-25.64, 4.22) * mm]});
            skFitSpline(sketch, "E3815", {"points": [v(-31.45, 3.01) * mm, v(-30.16, 2.8) * mm, v(-28.83, 2.58) * mm, v(-27.5, 2.37) * mm]});
            skFitSpline(sketch, "E3816", {"points": [v(-27.5, 2.37) * mm, v(-27.5, 2.38) * mm, v(-27.49, 2.4) * mm, v(-27.48, 2.41) * mm]});
            skFitSpline(sketch, "E3817", {"points": [v(-27.48, 2.41) * mm, v(-28.58, 3.2) * mm, v(-29.68, 3.99) * mm, v(-30.74, 4.75) * mm]});
            skFitSpline(sketch, "E3818", {"points": [v(-30.74, 4.75) * mm, v(-31.2, 4.57) * mm, v(-31.6, 4.42) * mm, v(-32.01, 4.26) * mm]});
            skFitSpline(sketch, "E3819", {"points": [v(-32.01, 4.26) * mm, v(-31.82, 3.84) * mm, v(-31.64, 3.44) * mm, v(-31.45, 3.01) * mm]});
            skFitSpline(sketch, "E3820", {"points": [v(-17.9, 4.75) * mm, v(-18.96, 3.99) * mm, v(-20.06, 3.2) * mm, v(-21.17, 2.4) * mm]});
            skFitSpline(sketch, "E3821", {"points": [v(-21.17, 2.4) * mm, v(-20.9, 2.4) * mm, v(-20.65, 2.44) * mm, v(-20.4, 2.48) * mm]});
            skFitSpline(sketch, "E3822", {"points": [v(-20.4, 2.48) * mm, v(-19.8, 2.58) * mm, v(-19.19, 2.68) * mm, v(-18.58, 2.78) * mm]});
            skFitSpline(sketch, "E3823", {"points": [v(-18.58, 2.78) * mm, v(-18.13, 2.85) * mm, v(-17.69, 2.93) * mm, v(-17.24, 3) * mm]});
            skFitSpline(sketch, "E3824", {"points": [v(-17.24, 3) * mm, v(-17.2, 3.02) * mm, v(-17.13, 3.07) * mm, v(-17.11, 3.12) * mm]});
            skFitSpline(sketch, "E3825", {"points": [v(-17.11, 3.12) * mm, v(-16.98, 3.41) * mm, v(-16.86, 3.7) * mm, v(-16.73, 4) * mm]});
            skFitSpline(sketch, "E3826", {"points": [v(-16.73, 4) * mm, v(-16.7, 4.08) * mm, v(-16.65, 4.17) * mm, v(-16.61, 4.26) * mm]});
            skFitSpline(sketch, "E3827", {"points": [v(-16.61, 4.26) * mm, v(-17.04, 4.42) * mm, v(-17.45, 4.58) * mm, v(-17.9, 4.75) * mm]});
            skFitSpline(sketch, "E3828", {"points": [v(-14.52, -4.9) * mm, v(-14.38, -4.82) * mm, v(-14.25, -4.75) * mm, v(-14.11, -4.69) * mm]});
            skFitSpline(sketch, "E3829", {"points": [v(-14.11, -4.69) * mm, v(-13.64, -4.46) * mm, v(-13.16, -4.23) * mm, v(-12.69, -4) * mm]});
            skFitSpline(sketch, "E3830", {"points": [v(-12.69, -4) * mm, v(-12.59, -3.96) * mm, v(-12.5, -3.9) * mm, v(-12.4, -3.85) * mm]});
            skFitSpline(sketch, "E3831", {"points": [v(-12.4, -3.85) * mm, v(-12.65, -3.1) * mm, v(-12.91, -2.37) * mm, v(-13.17, -1.62) * mm]});
            skFitSpline(sketch, "E3832", {"points": [v(-13.17, -1.62) * mm, v(-13.89, -1.98) * mm, v(-14.63, -2.27) * mm, v(-15.36, -2.65) * mm]});
            skFitSpline(sketch, "E3833", {"points": [v(-15.36, -2.65) * mm, v(-15.07, -3.41) * mm, v(-14.8, -4.16) * mm, v(-14.52, -4.9) * mm]});
            skFitSpline(sketch, "E3834", {"points": [v(-15.36, 4.78) * mm, v(-14.6, 4.44) * mm, v(-13.89, 4.1) * mm, v(-13.18, 3.78) * mm]});
            skFitSpline(sketch, "E3835", {"points": [v(-13.18, 3.78) * mm, v(-13.04, 4.15) * mm, v(-12.9, 4.51) * mm, v(-12.78, 4.88) * mm]});
            skFitSpline(sketch, "E3836", {"points": [v(-12.78, 4.88) * mm, v(-12.64, 5.25) * mm, v(-12.52, 5.63) * mm, v(-12.4, 6.02) * mm]});
            skFitSpline(sketch, "E3837", {"points": [v(-12.4, 6.02) * mm, v(-13.11, 6.37) * mm, v(-13.81, 6.7) * mm, v(-14.52, 7.04) * mm]});
            skFitSpline(sketch, "E3838", {"points": [v(-14.52, 7.04) * mm, v(-14.8, 6.3) * mm, v(-15.08, 5.56) * mm, v(-15.36, 4.78) * mm]});
            skFitSpline(sketch, "E3839", {"points": [v(-35.45, 3.78) * mm, v(-34.74, 4.11) * mm, v(-34, 4.45) * mm, v(-33.27, 4.79) * mm]});
            skFitSpline(sketch, "E3840", {"points": [v(-33.27, 4.79) * mm, v(-33.56, 5.56) * mm, v(-33.84, 6.3) * mm, v(-34.11, 7.04) * mm]});
            skFitSpline(sketch, "E3841", {"points": [v(-34.11, 7.04) * mm, v(-34.83, 6.7) * mm, v(-35.54, 6.36) * mm, v(-36.24, 6.02) * mm]});
            skFitSpline(sketch, "E3842", {"points": [v(-36.24, 6.02) * mm, v(-36.1, 5.62) * mm, v(-36, 5.25) * mm, v(-35.86, 4.88) * mm]});
            skFitSpline(sketch, "E3843", {"points": [v(-35.86, 4.88) * mm, v(-35.73, 4.51) * mm, v(-35.6, 4.15) * mm, v(-35.45, 3.78) * mm]});
            skFitSpline(sketch, "E3844", {"points": [v(-30.29, -8.72) * mm, v(-29.94, -9.44) * mm, v(-29.6, -10.14) * mm, v(-29.26, -10.86) * mm]});
            skFitSpline(sketch, "E3845", {"points": [v(-29.26, -10.86) * mm, v(-28.5, -10.6) * mm, v(-27.76, -10.33) * mm, v(-27.02, -10.07) * mm]});
            skFitSpline(sketch, "E3846", {"points": [v(-27.02, -10.07) * mm, v(-27.35, -9.35) * mm, v(-27.69, -8.62) * mm, v(-28.03, -7.88) * mm]});
            skFitSpline(sketch, "E3847", {"points": [v(-28.03, -7.88) * mm, v(-28.8, -8.17) * mm, v(-29.54, -8.44) * mm, v(-30.29, -8.72) * mm]});
            skFitSpline(sketch, "E3848", {"points": [v(-19.37, 13) * mm, v(-20.13, 12.74) * mm, v(-20.87, 12.48) * mm, v(-21.61, 12.22) * mm]});
            skFitSpline(sketch, "E3849", {"points": [v(-21.61, 12.22) * mm, v(-21.28, 11.5) * mm, v(-20.95, 10.78) * mm, v(-20.6, 10.03) * mm]});
            skFitSpline(sketch, "E3850", {"points": [v(-20.6, 10.03) * mm, v(-19.83, 10.32) * mm, v(-19.08, 10.6) * mm, v(-18.35, 10.87) * mm]});
            skFitSpline(sketch, "E3851", {"points": [v(-18.35, 10.87) * mm, v(-18.69, 11.58) * mm, v(-19.02, 12.28) * mm, v(-19.37, 13) * mm]});
            skFitSpline(sketch, "E3852", {"points": [v(-33.27, -2.63) * mm, v(-34.02, -2.3) * mm, v(-34.74, -1.96) * mm, v(-35.46, -1.63) * mm]});
            skFitSpline(sketch, "E3853", {"points": [v(-35.46, -1.63) * mm, v(-35.73, -2.38) * mm, v(-35.99, -3.12) * mm, v(-36.25, -3.87) * mm]});
            skFitSpline(sketch, "E3854", {"points": [v(-36.25, -3.87) * mm, v(-35.52, -4.22) * mm, v(-34.82, -4.55) * mm, v(-34.11, -4.9) * mm]});
            skFitSpline(sketch, "E3855", {"points": [v(-34.11, -4.9) * mm, v(-33.84, -4.15) * mm, v(-33.56, -3.4) * mm, v(-33.27, -2.63) * mm]});
            skFitSpline(sketch, "E3856", {"points": [v(-18.34, -8.72) * mm, v(-19.09, -8.44) * mm, v(-19.84, -8.17) * mm, v(-20.6, -7.88) * mm]});
            skFitSpline(sketch, "E3857", {"points": [v(-20.6, -7.88) * mm, v(-20.95, -8.63) * mm, v(-21.28, -9.35) * mm, v(-21.61, -10.07) * mm]});
            skFitSpline(sketch, "E3858", {"points": [v(-21.61, -10.07) * mm, v(-20.86, -10.34) * mm, v(-20.13, -10.6) * mm, v(-19.37, -10.86) * mm]});
            skFitSpline(sketch, "E3859", {"points": [v(-19.37, -10.86) * mm, v(-19.1, -10.27) * mm, v(-18.82, -9.7) * mm, v(-18.55, -9.12) * mm]});
            skFitSpline(sketch, "E3860", {"points": [v(-18.55, -9.12) * mm, v(-18.49, -8.99) * mm, v(-18.42, -8.86) * mm, v(-18.34, -8.72) * mm]});
            skFitSpline(sketch, "E3861", {"points": [v(-30.29, 10.87) * mm, v(-29.54, 10.59) * mm, v(-28.79, 10.31) * mm, v(-28.03, 10.03) * mm]});
            skFitSpline(sketch, "E3862", {"points": [v(-28.03, 10.03) * mm, v(-27.68, 10.79) * mm, v(-27.35, 11.5) * mm, v(-27.02, 12.22) * mm]});
            skFitSpline(sketch, "E3863", {"points": [v(-27.02, 12.22) * mm, v(-27.16, 12.27) * mm, v(-27.3, 12.3) * mm, v(-27.44, 12.35) * mm]});
            skFitSpline(sketch, "E3864", {"points": [v(-27.44, 12.35) * mm, v(-27.9, 12.52) * mm, v(-28.38, 12.7) * mm, v(-28.85, 12.86) * mm]});
            skFitSpline(sketch, "E3865", {"points": [v(-28.85, 12.86) * mm, v(-28.99, 12.9) * mm, v(-29.12, 12.95) * mm, v(-29.27, 13) * mm]});
            skFitSpline(sketch, "E3866", {"points": [v(-29.27, 13) * mm, v(-29.61, 12.28) * mm, v(-29.94, 11.58) * mm, v(-30.29, 10.87) * mm]});
            skFitSpline(sketch, "E3867", {"points": [v(-23.05, 2.36) * mm, v(-23.04, 2.35) * mm, v(-23.03, 2.34) * mm, v(-23.02, 2.33) * mm]});
            skFitSpline(sketch, "E3868", {"points": [v(-23.02, 2.33) * mm, v(-22.68, 2.57) * mm, v(-22.34, 2.8) * mm, v(-22, 3.03) * mm]});
            skFitSpline(sketch, "E3869", {"points": [v(-22, 3.03) * mm, v(-21.6, 3.31) * mm, v(-21.19, 3.58) * mm, v(-20.8, 3.87) * mm]});
            skFitSpline(sketch, "E3870", {"points": [v(-20.8, 3.87) * mm, v(-20.3, 4.22) * mm, v(-19.82, 4.59) * mm, v(-19.32, 4.94) * mm]});
            skFitSpline(sketch, "E3871", {"points": [v(-19.32, 4.94) * mm, v(-18.36, 5.63) * mm, v(-17.39, 6.32) * mm, v(-16.42, 7.02) * mm]});
            skFitSpline(sketch, "E3872", {"points": [v(-16.42, 7.02) * mm, v(-16.13, 7.23) * mm, v(-15.86, 7.46) * mm, v(-15.57, 7.68) * mm]});
            skFitSpline(sketch, "E3873", {"points": [v(-15.57, 7.68) * mm, v(-15.31, 7.86) * mm, v(-15.18, 8.1) * mm, v(-15.09, 8.4) * mm]});
            skFitSpline(sketch, "E3874", {"points": [v(-15.09, 8.4) * mm, v(-14.88, 9) * mm, v(-14.65, 9.6) * mm, v(-14.44, 10.2) * mm]});
            skFitSpline(sketch, "E3875", {"points": [v(-14.44, 10.2) * mm, v(-14.3, 10.57) * mm, v(-14.18, 10.94) * mm, v(-14.04, 11.35) * mm]});
            skFitSpline(sketch, "E3876", {"points": [v(-14.04, 11.35) * mm, v(-14.14, 11.32) * mm, v(-14.2, 11.3) * mm, v(-14.26, 11.28) * mm]});
            skFitSpline(sketch, "E3877", {"points": [v(-14.26, 11.28) * mm, v(-15.22, 10.94) * mm, v(-16.18, 10.59) * mm, v(-17.14, 10.25) * mm]});
            skFitSpline(sketch, "E3878", {"points": [v(-17.14, 10.25) * mm, v(-17.36, 10.18) * mm, v(-17.52, 10.07) * mm, v(-17.66, 9.89) * mm]});
            skFitSpline(sketch, "E3879", {"points": [v(-17.66, 9.89) * mm, v(-18.28, 9.07) * mm, v(-18.9, 8.25) * mm, v(-19.51, 7.42) * mm]});
            skFitSpline(sketch, "E3880", {"points": [v(-19.51, 7.42) * mm, v(-20.05, 6.68) * mm, v(-20.58, 5.92) * mm, v(-21.1, 5.17) * mm]});
            skFitSpline(sketch, "E3881", {"points": [v(-21.1, 5.17) * mm, v(-21.62, 4.44) * mm, v(-22.14, 3.71) * mm, v(-22.65, 2.98) * mm]});
            skFitSpline(sketch, "E3882", {"points": [v(-22.65, 2.98) * mm, v(-22.8, 2.78) * mm, v(-22.92, 2.57) * mm, v(-23.05, 2.36) * mm]});
            skFitSpline(sketch, "E3883", {"points": [v(-34.6, -9.2) * mm, v(-34.5, -9.17) * mm, v(-34.46, -9.16) * mm, v(-34.42, -9.14) * mm]});
            skFitSpline(sketch, "E3884", {"points": [v(-34.42, -9.14) * mm, v(-33.4, -8.78) * mm, v(-32.38, -8.41) * mm, v(-31.35, -8.05) * mm]});
            skFitSpline(sketch, "E3885", {"points": [v(-31.35, -8.05) * mm, v(-31.2, -8) * mm, v(-31.1, -7.9) * mm, v(-31.02, -7.8) * mm]});
            skFitSpline(sketch, "E3886", {"points": [v(-31.02, -7.8) * mm, v(-30.38, -6.94) * mm, v(-29.73, -6.09) * mm, v(-29.1, -5.22) * mm]});
            skFitSpline(sketch, "E3887", {"points": [v(-29.1, -5.22) * mm, v(-28.71, -4.7) * mm, v(-28.35, -4.17) * mm, v(-27.97, -3.64) * mm]});
            skFitSpline(sketch, "E3888", {"points": [v(-27.97, -3.64) * mm, v(-27.75, -3.33) * mm, v(-27.51, -3.03) * mm, v(-27.3, -2.72) * mm]});
            skFitSpline(sketch, "E3889", {"points": [v(-27.3, -2.72) * mm, v(-26.86, -2.11) * mm, v(-26.44, -1.5) * mm, v(-26.02, -0.89) * mm]});
            skFitSpline(sketch, "E3890", {"points": [v(-26.02, -0.89) * mm, v(-25.87, -0.66) * mm, v(-25.72, -0.43) * mm, v(-25.57, -0.2) * mm]});
            skFitSpline(sketch, "E3891", {"points": [v(-25.57, -0.2) * mm, v(-25.62, -0.2) * mm, v(-25.65, -0.2) * mm, v(-25.67, -0.23) * mm]});
            skFitSpline(sketch, "E3892", {"points": [v(-25.67, -0.23) * mm, v(-26, -0.45) * mm, v(-26.33, -0.67) * mm, v(-26.66, -0.9) * mm]});
            skFitSpline(sketch, "E3893", {"points": [v(-26.66, -0.9) * mm, v(-27.05, -1.17) * mm, v(-27.44, -1.43) * mm, v(-27.82, -1.7) * mm]});
            skFitSpline(sketch, "E3894", {"points": [v(-27.82, -1.7) * mm, v(-28.32, -2.06) * mm, v(-28.8, -2.42) * mm, v(-29.3, -2.78) * mm]});
            skFitSpline(sketch, "E3895", {"points": [v(-29.3, -2.78) * mm, v(-29.95, -3.25) * mm, v(-30.62, -3.72) * mm, v(-31.27, -4.2) * mm]});
            skFitSpline(sketch, "E3896", {"points": [v(-31.27, -4.2) * mm, v(-31.86, -4.63) * mm, v(-32.44, -5.07) * mm, v(-33.03, -5.5) * mm]});
            skFitSpline(sketch, "E3897", {"points": [v(-33.03, -5.5) * mm, v(-33.31, -5.7) * mm, v(-33.46, -5.97) * mm, v(-33.56, -6.29) * mm]});
            skFitSpline(sketch, "E3898", {"points": [v(-33.56, -6.29) * mm, v(-33.74, -6.83) * mm, v(-33.94, -7.37) * mm, v(-34.14, -7.91) * mm]});
            skFitSpline(sketch, "E3899", {"points": [v(-34.14, -7.91) * mm, v(-34.29, -8.32) * mm, v(-34.44, -8.74) * mm, v(-34.6, -9.2) * mm]});
            skFitSpline(sketch, "E3900", {"points": [v(-25.6, 2.33) * mm, v(-25.6, 2.34) * mm, v(-25.58, 2.35) * mm, v(-25.57, 2.36) * mm]});
            skFitSpline(sketch, "E3901", {"points": [v(-25.57, 2.36) * mm, v(-25.72, 2.58) * mm, v(-25.86, 2.82) * mm, v(-26.02, 3.04) * mm]});
            skFitSpline(sketch, "E3902", {"points": [v(-26.02, 3.04) * mm, v(-26.54, 3.78) * mm, v(-27.06, 4.51) * mm, v(-27.58, 5.25) * mm]});
            skFitSpline(sketch, "E3903", {"points": [v(-27.58, 5.25) * mm, v(-27.96, 5.79) * mm, v(-28.35, 6.33) * mm, v(-28.74, 6.86) * mm]});
            skFitSpline(sketch, "E3904", {"points": [v(-28.74, 6.86) * mm, v(-29.2, 7.5) * mm, v(-29.65, 8.14) * mm, v(-30.11, 8.77) * mm]});
            skFitSpline(sketch, "E3905", {"points": [v(-30.11, 8.77) * mm, v(-30.38, 9.13) * mm, v(-30.67, 9.48) * mm, v(-30.94, 9.85) * mm]});
            skFitSpline(sketch, "E3906", {"points": [v(-30.94, 9.85) * mm, v(-31.1, 10.08) * mm, v(-31.33, 10.21) * mm, v(-31.6, 10.3) * mm]});
            skFitSpline(sketch, "E3907", {"points": [v(-31.6, 10.3) * mm, v(-31.93, 10.39) * mm, v(-32.25, 10.5) * mm, v(-32.57, 10.62) * mm]});
            skFitSpline(sketch, "E3908", {"points": [v(-32.57, 10.62) * mm, v(-33.19, 10.84) * mm, v(-33.8, 11.07) * mm, v(-34.42, 11.3) * mm]});
            skFitSpline(sketch, "E3909", {"points": [v(-34.42, 11.3) * mm, v(-34.46, 11.3) * mm, v(-34.51, 11.32) * mm, v(-34.58, 11.33) * mm]});
            skFitSpline(sketch, "E3910", {"points": [v(-34.58, 11.33) * mm, v(-34.56, 11.27) * mm, v(-34.55, 11.23) * mm, v(-34.54, 11.2) * mm]});
            skFitSpline(sketch, "E3911", {"points": [v(-34.54, 11.2) * mm, v(-34.34, 10.63) * mm, v(-34.14, 10.07) * mm, v(-33.94, 9.5) * mm]});
            skFitSpline(sketch, "E3912", {"points": [v(-33.94, 9.5) * mm, v(-33.78, 9.06) * mm, v(-33.62, 8.62) * mm, v(-33.47, 8.17) * mm]});
            skFitSpline(sketch, "E3913", {"points": [v(-33.47, 8.17) * mm, v(-33.42, 8.03) * mm, v(-33.35, 7.91) * mm, v(-33.23, 7.82) * mm]});
            skFitSpline(sketch, "E3914", {"points": [v(-33.23, 7.82) * mm, v(-33.02, 7.64) * mm, v(-32.8, 7.46) * mm, v(-32.58, 7.3) * mm]});
            skFitSpline(sketch, "E3915", {"points": [v(-32.58, 7.3) * mm, v(-31.86, 6.76) * mm, v(-31.13, 6.23) * mm, v(-30.4, 5.7) * mm]});
            skFitSpline(sketch, "E3916", {"points": [v(-30.4, 5.7) * mm, v(-29.75, 5.23) * mm, v(-29.1, 4.77) * mm, v(-28.45, 4.3) * mm]});
            skFitSpline(sketch, "E3917", {"points": [v(-28.45, 4.3) * mm, v(-28.01, 4) * mm, v(-27.58, 3.68) * mm, v(-27.14, 3.37) * mm]});
            skFitSpline(sketch, "E3918", {"points": [v(-27.14, 3.37) * mm, v(-26.84, 3.15) * mm, v(-26.53, 2.94) * mm, v(-26.22, 2.73) * mm]});
            skFitSpline(sketch, "E3919", {"points": [v(-26.22, 2.73) * mm, v(-26.01, 2.6) * mm, v(-25.8, 2.47) * mm, v(-25.6, 2.33) * mm]});
            skFitSpline(sketch, "E3920", {"points": [v(-23.03, -0.19) * mm, v(-23.04, -0.2) * mm, v(-23.05, -0.2) * mm, v(-23.05, -0.2) * mm]});
            skFitSpline(sketch, "E3921", {"points": [v(-23.05, -0.2) * mm, v(-23.04, -0.24) * mm, v(-23.02, -0.27) * mm, v(-23, -0.3) * mm]});
            skFitSpline(sketch, "E3922", {"points": [v(-23, -0.3) * mm, v(-22.8, -0.61) * mm, v(-22.58, -0.92) * mm, v(-22.37, -1.23) * mm]});
            skFitSpline(sketch, "E3923", {"points": [v(-22.37, -1.23) * mm, v(-22.09, -1.64) * mm, v(-21.8, -2.05) * mm, v(-21.52, -2.45) * mm]});
            skFitSpline(sketch, "E3924", {"points": [v(-21.52, -2.45) * mm, v(-21.43, -2.58) * mm, v(-21.34, -2.72) * mm, v(-21.25, -2.85) * mm]});
            skFitSpline(sketch, "E3925", {"points": [v(-21.25, -2.85) * mm, v(-20.93, -3.28) * mm, v(-20.62, -3.7) * mm, v(-20.3, -4.14) * mm]});
            skFitSpline(sketch, "E3926", {"points": [v(-20.3, -4.14) * mm, v(-20, -4.57) * mm, v(-19.7, -5) * mm, v(-19.39, -5.43) * mm]});
            skFitSpline(sketch, "E3927", {"points": [v(-19.39, -5.43) * mm, v(-19.16, -5.75) * mm, v(-18.93, -6.06) * mm, v(-18.7, -6.38) * mm]});
            skFitSpline(sketch, "E3928", {"points": [v(-18.7, -6.38) * mm, v(-18.35, -6.83) * mm, v(-18, -7.28) * mm, v(-17.67, -7.73) * mm]});
            skFitSpline(sketch, "E3929", {"points": [v(-17.67, -7.73) * mm, v(-17.52, -7.93) * mm, v(-17.34, -8.05) * mm, v(-17.1, -8.12) * mm]});
            skFitSpline(sketch, "E3930", {"points": [v(-17.1, -8.12) * mm, v(-16.76, -8.23) * mm, v(-16.4, -8.35) * mm, v(-16.06, -8.47) * mm]});
            skFitSpline(sketch, "E3931", {"points": [v(-16.06, -8.47) * mm, v(-15.46, -8.7) * mm, v(-14.85, -8.92) * mm, v(-14.24, -9.14) * mm]});
            skFitSpline(sketch, "E3932", {"points": [v(-14.24, -9.14) * mm, v(-14.19, -9.16) * mm, v(-14.13, -9.17) * mm, v(-14.05, -9.19) * mm]});
            skFitSpline(sketch, "E3933", {"points": [v(-14.05, -9.19) * mm, v(-14.07, -9.1) * mm, v(-14.09, -9.05) * mm, v(-14.1, -9) * mm]});
            skFitSpline(sketch, "E3934", {"points": [v(-14.1, -9) * mm, v(-14.46, -8.02) * mm, v(-14.81, -7.04) * mm, v(-15.16, -6.05) * mm]});
            skFitSpline(sketch, "E3935", {"points": [v(-15.16, -6.05) * mm, v(-15.22, -5.87) * mm, v(-15.32, -5.72) * mm, v(-15.47, -5.61) * mm]});
            skFitSpline(sketch, "E3936", {"points": [v(-15.47, -5.61) * mm, v(-16.3, -5) * mm, v(-17.11, -4.36) * mm, v(-17.94, -3.75) * mm]});
            skFitSpline(sketch, "E3937", {"points": [v(-17.94, -3.75) * mm, v(-18.78, -3.14) * mm, v(-19.62, -2.54) * mm, v(-20.47, -1.94) * mm]});
            skFitSpline(sketch, "E3938", {"points": [v(-20.47, -1.94) * mm, v(-21.1, -1.48) * mm, v(-21.75, -1.04) * mm, v(-22.4, -0.6) * mm]});
            skFitSpline(sketch, "E3939", {"points": [v(-22.4, -0.6) * mm, v(-22.6, -0.45) * mm, v(-22.82, -0.32) * mm, v(-23.03, -0.19) * mm]});
            skFitSpline(sketch, "E3940", {"points": [v(-26.13, 1.05) * mm, v(-26.13, 1.06) * mm, v(-26.13, 1.08) * mm, v(-26.13, 1.09) * mm]});
            skFitSpline(sketch, "E3941", {"points": [v(-26.13, 1.09) * mm, v(-26.17, 1.1) * mm, v(-26.2, 1.12) * mm, v(-26.23, 1.12) * mm]});
            skFitSpline(sketch, "E3942", {"points": [v(-26.23, 1.12) * mm, v(-26.6, 1.2) * mm, v(-26.97, 1.26) * mm, v(-27.34, 1.33) * mm]});
            skFitSpline(sketch, "E3943", {"points": [v(-27.34, 1.33) * mm, v(-28, 1.45) * mm, v(-28.67, 1.57) * mm, v(-29.34, 1.69) * mm]});
            skFitSpline(sketch, "E3944", {"points": [v(-29.34, 1.69) * mm, v(-29.87, 1.78) * mm, v(-30.4, 1.86) * mm, v(-30.92, 1.94) * mm]});
            skFitSpline(sketch, "E3945", {"points": [v(-30.92, 1.94) * mm, v(-31.6, 2.05) * mm, v(-32.26, 2.15) * mm, v(-32.93, 2.26) * mm]});
            skFitSpline(sketch, "E3946", {"points": [v(-32.93, 2.26) * mm, v(-33.7, 2.37) * mm, v(-34.46, 2.49) * mm, v(-35.23, 2.6) * mm]});
            skFitSpline(sketch, "E3947", {"points": [v(-35.23, 2.6) * mm, v(-35.45, 2.63) * mm, v(-35.67, 2.6) * mm, v(-35.87, 2.5) * mm]});
            skFitSpline(sketch, "E3948", {"points": [v(-35.87, 2.5) * mm, v(-36.21, 2.32) * mm, v(-36.56, 2.15) * mm, v(-36.9, 2) * mm]});
            skFitSpline(sketch, "E3949", {"points": [v(-36.9, 2) * mm, v(-37.5, 1.71) * mm, v(-38.1, 1.44) * mm, v(-38.68, 1.16) * mm]});
            skFitSpline(sketch, "E3950", {"points": [v(-38.68, 1.16) * mm, v(-38.73, 1.14) * mm, v(-38.77, 1.1) * mm, v(-38.83, 1.07) * mm]});
            skFitSpline(sketch, "E3951", {"points": [v(-38.83, 1.07) * mm, v(-38.76, 1.03) * mm, v(-38.7, 1) * mm, v(-38.66, 0.98) * mm]});
            skFitSpline(sketch, "E3952", {"points": [v(-38.66, 0.98) * mm, v(-37.72, 0.53) * mm, v(-36.78, 0.1) * mm, v(-35.85, -0.36) * mm]});
            skFitSpline(sketch, "E3953", {"points": [v(-35.85, -0.36) * mm, v(-35.64, -0.46) * mm, v(-35.42, -0.48) * mm, v(-35.2, -0.45) * mm]});
            skFitSpline(sketch, "E3954", {"points": [v(-35.2, -0.45) * mm, v(-34.6, -0.37) * mm, v(-34, -0.27) * mm, v(-33.4, -0.19) * mm]});
            skFitSpline(sketch, "E3955", {"points": [v(-33.4, -0.19) * mm, v(-32.98, -0.12) * mm, v(-32.55, -0.07) * mm, v(-32.12, 0) * mm]});
            skFitSpline(sketch, "E3956", {"points": [v(-32.12, 0) * mm, v(-31.54, 0.1) * mm, v(-30.96, 0.21) * mm, v(-30.38, 0.3) * mm]});
            skFitSpline(sketch, "E3957", {"points": [v(-30.38, 0.3) * mm, v(-29.75, 0.41) * mm, v(-29.12, 0.5) * mm, v(-28.5, 0.6) * mm]});
            skFitSpline(sketch, "E3958", {"points": [v(-28.5, 0.6) * mm, v(-28.02, 0.68) * mm, v(-27.55, 0.77) * mm, v(-27.08, 0.86) * mm]});
            skFitSpline(sketch, "E3959", {"points": [v(-27.08, 0.86) * mm, v(-26.76, 0.92) * mm, v(-26.45, 0.99) * mm, v(-26.13, 1.05) * mm]});
            skFitSpline(sketch, "E3960", {"points": [v(-24.33, -13.47) * mm, v(-24.28, -13.37) * mm, v(-24.25, -13.33) * mm, v(-24.23, -13.28) * mm]});
            skFitSpline(sketch, "E3961", {"points": [v(-24.23, -13.28) * mm, v(-24.02, -12.84) * mm, v(-23.82, -12.4) * mm, v(-23.62, -11.98) * mm]});
            skFitSpline(sketch, "E3962", {"points": [v(-23.62, -11.98) * mm, v(-23.37, -11.46) * mm, v(-23.13, -10.94) * mm, v(-22.87, -10.42) * mm]});
            skFitSpline(sketch, "E3963", {"points": [v(-22.87, -10.42) * mm, v(-22.78, -10.25) * mm, v(-22.76, -10.07) * mm, v(-22.78, -9.9) * mm]});
            skFitSpline(sketch, "E3964", {"points": [v(-22.78, -9.9) * mm, v(-22.87, -9.26) * mm, v(-22.96, -8.63) * mm, v(-23.06, -8) * mm]});
            skFitSpline(sketch, "E3965", {"points": [v(-23.06, -8) * mm, v(-23.13, -7.49) * mm, v(-23.21, -6.98) * mm, v(-23.3, -6.47) * mm]});
            skFitSpline(sketch, "E3966", {"points": [v(-23.3, -6.47) * mm, v(-23.37, -6) * mm, v(-23.46, -5.54) * mm, v(-23.54, -5.08) * mm]});
            skFitSpline(sketch, "E3967", {"points": [v(-23.54, -5.08) * mm, v(-23.66, -4.38) * mm, v(-23.76, -3.68) * mm, v(-23.88, -2.98) * mm]});
            skFitSpline(sketch, "E3968", {"points": [v(-23.88, -2.98) * mm, v(-24, -2.28) * mm, v(-24.13, -1.58) * mm, v(-24.26, -0.89) * mm]});
            skFitSpline(sketch, "E3969", {"points": [v(-24.26, -0.89) * mm, v(-24.27, -0.83) * mm, v(-24.3, -0.77) * mm, v(-24.31, -0.71) * mm]});
            skFitSpline(sketch, "E3970", {"points": [v(-24.31, -0.71) * mm, v(-24.43, -1.16) * mm, v(-24.51, -1.6) * mm, v(-24.6, -2.05) * mm]});
            skFitSpline(sketch, "E3971", {"points": [v(-24.6, -2.05) * mm, v(-24.68, -2.48) * mm, v(-24.76, -2.91) * mm, v(-24.83, -3.34) * mm]});
            skFitSpline(sketch, "E3972", {"points": [v(-24.83, -3.34) * mm, v(-24.93, -3.93) * mm, v(-25.01, -4.52) * mm, v(-25.1, -5.11) * mm]});
            skFitSpline(sketch, "E3973", {"points": [v(-25.1, -5.11) * mm, v(-25.2, -5.7) * mm, v(-25.32, -6.3) * mm, v(-25.42, -6.9) * mm]});
            skFitSpline(sketch, "E3974", {"points": [v(-25.42, -6.9) * mm, v(-25.48, -7.27) * mm, v(-25.53, -7.64) * mm, v(-25.58, -8.01) * mm]});
            skFitSpline(sketch, "E3975", {"points": [v(-25.58, -8.01) * mm, v(-25.67, -8.62) * mm, v(-25.76, -9.23) * mm, v(-25.84, -9.83) * mm]});
            skFitSpline(sketch, "E3976", {"points": [v(-25.84, -9.83) * mm, v(-25.88, -10.09) * mm, v(-25.83, -10.32) * mm, v(-25.7, -10.55) * mm]});
            skFitSpline(sketch, "E3977", {"points": [v(-25.7, -10.55) * mm, v(-25.52, -10.9) * mm, v(-25.35, -11.28) * mm, v(-25.18, -11.65) * mm]});
            skFitSpline(sketch, "E3978", {"points": [v(-25.18, -11.65) * mm, v(-24.9, -12.24) * mm, v(-24.62, -12.83) * mm, v(-24.33, -13.47) * mm]});
            skFitSpline(sketch, "E3979", {"points": [v(-24.32, 15.62) * mm, v(-24.8, 14.59) * mm, v(-25.27, 13.6) * mm, v(-25.74, 12.63) * mm]});
            skFitSpline(sketch, "E3980", {"points": [v(-25.74, 12.63) * mm, v(-25.83, 12.44) * mm, v(-25.86, 12.25) * mm, v(-25.85, 12.05) * mm]});
            skFitSpline(sketch, "E3981", {"points": [v(-25.85, 12.05) * mm, v(-25.83, 11.8) * mm, v(-25.81, 11.57) * mm, v(-25.78, 11.33) * mm]});
            skFitSpline(sketch, "E3982", {"points": [v(-25.78, 11.33) * mm, v(-25.64, 10.46) * mm, v(-25.5, 9.59) * mm, v(-25.36, 8.71) * mm]});
            skFitSpline(sketch, "E3983", {"points": [v(-25.36, 8.71) * mm, v(-25.23, 7.95) * mm, v(-25.1, 7.19) * mm, v(-24.98, 6.42) * mm]});
            skFitSpline(sketch, "E3984", {"points": [v(-24.98, 6.42) * mm, v(-24.91, 6.02) * mm, v(-24.85, 5.6) * mm, v(-24.78, 5.2) * mm]});
            skFitSpline(sketch, "E3985", {"points": [v(-24.78, 5.2) * mm, v(-24.7, 4.75) * mm, v(-24.62, 4.3) * mm, v(-24.54, 3.86) * mm]});
            skFitSpline(sketch, "E3986", {"points": [v(-24.54, 3.86) * mm, v(-24.47, 3.53) * mm, v(-24.4, 3.2) * mm, v(-24.33, 2.83) * mm]});
            skFitSpline(sketch, "E3987", {"points": [v(-24.33, 2.83) * mm, v(-24.3, 2.9) * mm, v(-24.28, 2.93) * mm, v(-24.27, 2.96) * mm]});
            skFitSpline(sketch, "E3988", {"points": [v(-24.27, 2.96) * mm, v(-24.12, 3.77) * mm, v(-23.96, 4.59) * mm, v(-23.82, 5.4) * mm]});
            skFitSpline(sketch, "E3989", {"points": [v(-23.82, 5.4) * mm, v(-23.69, 6.18) * mm, v(-23.56, 6.96) * mm, v(-23.44, 7.74) * mm]});
            skFitSpline(sketch, "E3990", {"points": [v(-23.44, 7.74) * mm, v(-23.33, 8.4) * mm, v(-23.22, 9.08) * mm, v(-23.12, 9.75) * mm]});
            skFitSpline(sketch, "E3991", {"points": [v(-23.12, 9.75) * mm, v(-23.01, 10.47) * mm, v(-22.92, 11.2) * mm, v(-22.8, 11.92) * mm]});
            skFitSpline(sketch, "E3992", {"points": [v(-22.8, 11.92) * mm, v(-22.75, 12.2) * mm, v(-22.8, 12.45) * mm, v(-22.93, 12.7) * mm]});
            skFitSpline(sketch, "E3993", {"points": [v(-22.93, 12.7) * mm, v(-23.23, 13.32) * mm, v(-23.5, 13.94) * mm, v(-23.8, 14.55) * mm]});
            skFitSpline(sketch, "E3994", {"points": [v(-23.8, 14.55) * mm, v(-23.96, 14.9) * mm, v(-24.13, 15.23) * mm, v(-24.32, 15.62) * mm]});
            skFitSpline(sketch, "E3995", {"points": [v(-9.78, 1.07) * mm, v(-9.88, 1.12) * mm, v(-9.93, 1.15) * mm, v(-9.98, 1.17) * mm]});
            skFitSpline(sketch, "E3996", {"points": [v(-9.98, 1.17) * mm, v(-10.92, 1.62) * mm, v(-11.86, 2.06) * mm, v(-12.8, 2.51) * mm]});
            skFitSpline(sketch, "E3997", {"points": [v(-12.8, 2.51) * mm, v(-12.96, 2.59) * mm, v(-13.12, 2.63) * mm, v(-13.3, 2.61) * mm]});
            skFitSpline(sketch, "E3998", {"points": [v(-13.3, 2.61) * mm, v(-13.51, 2.6) * mm, v(-13.73, 2.58) * mm, v(-13.94, 2.54) * mm]});
            skFitSpline(sketch, "E3999", {"points": [v(-13.94, 2.54) * mm, v(-14.91, 2.4) * mm, v(-15.88, 2.24) * mm, v(-16.85, 2.08) * mm]});
            skFitSpline(sketch, "E4000", {"points": [v(-16.85, 2.08) * mm, v(-17.54, 1.97) * mm, v(-18.23, 1.86) * mm, v(-18.93, 1.74) * mm]});
            skFitSpline(sketch, "E4001", {"points": [v(-18.93, 1.74) * mm, v(-19.5, 1.65) * mm, v(-20.1, 1.56) * mm, v(-20.67, 1.45) * mm]});
            skFitSpline(sketch, "E4002", {"points": [v(-20.67, 1.45) * mm, v(-21.25, 1.35) * mm, v(-21.82, 1.24) * mm, v(-22.39, 1.12) * mm]});
            skFitSpline(sketch, "E4003", {"points": [v(-22.39, 1.12) * mm, v(-22.43, 1.12) * mm, v(-22.46, 1.1) * mm, v(-22.54, 1.06) * mm]});
            skFitSpline(sketch, "E4004", {"points": [v(-22.54, 1.06) * mm, v(-21.97, 0.94) * mm, v(-21.45, 0.83) * mm, v(-20.92, 0.74) * mm]});
            skFitSpline(sketch, "E4005", {"points": [v(-20.92, 0.74) * mm, v(-20.3, 0.63) * mm, v(-19.7, 0.54) * mm, v(-19.08, 0.44) * mm]});
            skFitSpline(sketch, "E4006", {"points": [v(-19.08, 0.44) * mm, v(-18.54, 0.35) * mm, v(-18.01, 0.25) * mm, v(-17.48, 0.17) * mm]});
            skFitSpline(sketch, "E4007", {"points": [v(-17.48, 0.17) * mm, v(-16.78, 0.05) * mm, v(-16.07, -0.06) * mm, v(-15.37, -0.16) * mm]});
            skFitSpline(sketch, "E4008", {"points": [v(-15.37, -0.16) * mm, v(-14.75, -0.26) * mm, v(-14.13, -0.35) * mm, v(-13.5, -0.44) * mm]});
            skFitSpline(sketch, "E4009", {"points": [v(-13.5, -0.44) * mm, v(-13.18, -0.5) * mm, v(-12.9, -0.42) * mm, v(-12.6, -0.27) * mm]});
            skFitSpline(sketch, "E4010", {"points": [v(-12.6, -0.27) * mm, v(-12.04, 0.01) * mm, v(-11.45, 0.27) * mm, v(-10.88, 0.54) * mm]});
            skFitSpline(sketch, "E4011", {"points": [v(-10.88, 0.54) * mm, v(-10.52, 0.7) * mm, v(-10.18, 0.88) * mm, v(-9.78, 1.07) * mm]});
            skFitSpline(sketch, "E4012", {"points": [v(-13.8, -6.95) * mm, v(-13.74, -7.13) * mm, v(-13.68, -7.31) * mm, v(-13.62, -7.49) * mm]});
            skFitSpline(sketch, "E4013", {"points": [v(-13.62, -7.49) * mm, v(-13.53, -7.72) * mm, v(-13.44, -7.95) * mm, v(-13.36, -8.18) * mm]});
            skFitSpline(sketch, "E4014", {"points": [v(-13.36, -8.18) * mm, v(-13.19, -8.64) * mm, v(-13.02, -9.1) * mm, v(-12.84, -9.55) * mm]});
            skFitSpline(sketch, "E4015", {"points": [v(-12.84, -9.55) * mm, v(-12.82, -9.6) * mm, v(-12.76, -9.67) * mm, v(-12.7, -9.7) * mm]});
            skFitSpline(sketch, "E4016", {"points": [v(-12.7, -9.7) * mm, v(-12.18, -9.9) * mm, v(-11.66, -10.1) * mm, v(-11.14, -10.3) * mm]});
            skFitSpline(sketch, "E4017", {"points": [v(-11.14, -10.3) * mm, v(-10.8, -10.42) * mm, v(-10.46, -10.54) * mm, v(-10.12, -10.66) * mm]});
            skFitSpline(sketch, "E4018", {"points": [v(-10.12, -10.66) * mm, v(-9.92, -10.73) * mm, v(-9.7, -10.78) * mm, v(-9.51, -10.86) * mm]});
            skFitSpline(sketch, "E4019", {"points": [v(-9.51, -10.86) * mm, v(-9.24, -10.98) * mm, v(-9.14, -11.27) * mm, v(-9.26, -11.52) * mm]});
            skFitSpline(sketch, "E4020", {"points": [v(-9.26, -11.52) * mm, v(-9.36, -11.73) * mm, v(-9.6, -11.84) * mm, v(-9.85, -11.77) * mm]});
            skFitSpline(sketch, "E4021", {"points": [v(-9.85, -11.77) * mm, v(-10.23, -11.65) * mm, v(-10.6, -11.52) * mm, v(-10.98, -11.4) * mm]});
            skFitSpline(sketch, "E4022", {"points": [v(-10.98, -11.4) * mm, v(-11.42, -11.24) * mm, v(-11.86, -11.08) * mm, v(-12.3, -10.92) * mm]});
            skFitSpline(sketch, "E4023", {"points": [v(-12.3, -10.92) * mm, v(-12.31, -10.95) * mm, v(-12.32, -10.97) * mm, v(-12.32, -10.98) * mm]});
            skFitSpline(sketch, "E4024", {"points": [v(-12.32, -10.98) * mm, v(-12.16, -11.41) * mm, v(-12, -11.84) * mm, v(-11.84, -12.28) * mm]});
            skFitSpline(sketch, "E4025", {"points": [v(-11.84, -12.28) * mm, v(-11.71, -12.66) * mm, v(-11.58, -13.03) * mm, v(-11.47, -13.42) * mm]});
            skFitSpline(sketch, "E4026", {"points": [v(-11.47, -13.42) * mm, v(-11.4, -13.68) * mm, v(-11.53, -13.91) * mm, v(-11.79, -14) * mm]});
            skFitSpline(sketch, "E4027", {"points": [v(-11.79, -14) * mm, v(-12.02, -14.09) * mm, v(-12.27, -13.98) * mm, v(-12.38, -13.73) * mm]});
            skFitSpline(sketch, "E4028", {"points": [v(-12.38, -13.73) * mm, v(-12.48, -13.5) * mm, v(-12.55, -13.24) * mm, v(-12.64, -12.99) * mm]});
            skFitSpline(sketch, "E4029", {"points": [v(-12.64, -12.99) * mm, v(-12.83, -12.43) * mm, v(-13.03, -11.88) * mm, v(-13.24, -11.32) * mm]});
            skFitSpline(sketch, "E4030", {"points": [v(-13.24, -11.32) * mm, v(-13.33, -11.07) * mm, v(-13.43, -10.82) * mm, v(-13.54, -10.57) * mm]});
            skFitSpline(sketch, "E4031", {"points": [v(-13.54, -10.57) * mm, v(-13.57, -10.5) * mm, v(-13.63, -10.42) * mm, v(-13.7, -10.4) * mm]});
            skFitSpline(sketch, "E4032", {"points": [v(-13.7, -10.4) * mm, v(-14.55, -10.08) * mm, v(-15.41, -9.76) * mm, v(-16.27, -9.45) * mm]});
            skFitSpline(sketch, "E4033", {"points": [v(-16.27, -9.45) * mm, v(-16.28, -9.44) * mm, v(-16.29, -9.45) * mm, v(-16.32, -9.45) * mm]});
            skFitSpline(sketch, "E4034", {"points": [v(-16.32, -9.45) * mm, v(-16.28, -9.51) * mm, v(-16.25, -9.57) * mm, v(-16.21, -9.63) * mm]});
            skFitSpline(sketch, "E4035", {"points": [v(-16.21, -9.63) * mm, v(-15.93, -10.03) * mm, v(-15.64, -10.44) * mm, v(-15.35, -10.84) * mm]});
            skFitSpline(sketch, "E4036", {"points": [v(-15.35, -10.84) * mm, v(-15.2, -11.05) * mm, v(-15.15, -11.26) * mm, v(-15.26, -11.52) * mm]});
            skFitSpline(sketch, "E4037", {"points": [v(-15.26, -11.52) * mm, v(-15.39, -11.82) * mm, v(-15.43, -12.15) * mm, v(-15.53, -12.47) * mm]});
            skFitSpline(sketch, "E4038", {"points": [v(-15.53, -12.47) * mm, v(-15.65, -12.86) * mm, v(-15.77, -13.26) * mm, v(-15.91, -13.65) * mm]});
            skFitSpline(sketch, "E4039", {"points": [v(-15.91, -13.65) * mm, v(-15.95, -13.76) * mm, v(-16.06, -13.86) * mm, v(-16.16, -13.93) * mm]});
            skFitSpline(sketch, "E4040", {"points": [v(-16.16, -13.93) * mm, v(-16.32, -14.04) * mm, v(-16.54, -14) * mm, v(-16.7, -13.88) * mm]});
            skFitSpline(sketch, "E4041", {"points": [v(-16.7, -13.88) * mm, v(-16.85, -13.76) * mm, v(-16.91, -13.56) * mm, v(-16.85, -13.36) * mm]});
            skFitSpline(sketch, "E4042", {"points": [v(-16.85, -13.36) * mm, v(-16.83, -13.3) * mm, v(-16.8, -13.23) * mm, v(-16.77, -13.16) * mm]});
            skFitSpline(sketch, "E4043", {"points": [v(-16.77, -13.16) * mm, v(-16.54, -12.63) * mm, v(-16.45, -12.06) * mm, v(-16.28, -11.51) * mm]});
            skFitSpline(sketch, "E4044", {"points": [v(-16.28, -11.51) * mm, v(-16.23, -11.35) * mm, v(-16.26, -11.23) * mm, v(-16.36, -11.1) * mm]});
            skFitSpline(sketch, "E4045", {"points": [v(-16.36, -11.1) * mm, v(-16.73, -10.6) * mm, v(-17.08, -10.08) * mm, v(-17.44, -9.57) * mm]});
            skFitSpline(sketch, "E4046", {"points": [v(-17.44, -9.57) * mm, v(-17.48, -9.5) * mm, v(-17.52, -9.45) * mm, v(-17.58, -9.37) * mm]});
            skFitSpline(sketch, "E4047", {"points": [v(-17.58, -9.37) * mm, v(-17.62, -9.44) * mm, v(-17.65, -9.5) * mm, v(-17.67, -9.54) * mm]});
            skFitSpline(sketch, "E4048", {"points": [v(-17.67, -9.54) * mm, v(-17.93, -10.1) * mm, v(-18.2, -10.64) * mm, v(-18.45, -11.19) * mm]});
            skFitSpline(sketch, "E4049", {"points": [v(-18.45, -11.19) * mm, v(-18.54, -11.36) * mm, v(-18.68, -11.46) * mm, v(-18.88, -11.45) * mm]});
            skFitSpline(sketch, "E4050", {"points": [v(-18.88, -11.45) * mm, v(-18.96, -11.44) * mm, v(-19.05, -11.42) * mm, v(-19.15, -11.4) * mm]});
            skFitSpline(sketch, "E4051", {"points": [v(-19.15, -11.4) * mm, v(-19.19, -11.46) * mm, v(-19.22, -11.53) * mm, v(-19.27, -11.6) * mm]});
            skFitSpline(sketch, "E4052", {"points": [v(-19.27, -11.6) * mm, v(-19.4, -11.76) * mm, v(-19.6, -11.8) * mm, v(-19.8, -11.74) * mm]});
            skFitSpline(sketch, "E4053", {"points": [v(-19.8, -11.74) * mm, v(-20.4, -11.52) * mm, v(-21, -11.3) * mm, v(-21.6, -11.1) * mm]});
            skFitSpline(sketch, "E4054", {"points": [v(-21.6, -11.1) * mm, v(-21.63, -11.08) * mm, v(-21.65, -11.08) * mm, v(-21.7, -11.08) * mm]});
            skFitSpline(sketch, "E4055", {"points": [v(-21.7, -11.08) * mm, v(-21.63, -11.44) * mm, v(-21.57, -11.8) * mm, v(-21.51, -12.14) * mm]});
            skFitSpline(sketch, "E4056", {"points": [v(-21.51, -12.14) * mm, v(-21.45, -12.49) * mm, v(-21.38, -12.83) * mm, v(-21.34, -13.18) * mm]});
            skFitSpline(sketch, "E4057", {"points": [v(-21.34, -13.18) * mm, v(-21.32, -13.34) * mm, v(-21.25, -13.43) * mm, v(-21.12, -13.5) * mm]});
            skFitSpline(sketch, "E4058", {"points": [v(-21.12, -13.5) * mm, v(-20.58, -13.8) * mm, v(-20.06, -14.16) * mm, v(-19.48, -14.37) * mm]});
            skFitSpline(sketch, "E4059", {"points": [v(-19.48, -14.37) * mm, v(-19.29, -14.44) * mm, v(-19.16, -14.57) * mm, v(-19.13, -14.77) * mm]});
            skFitSpline(sketch, "E4060", {"points": [v(-19.13, -14.77) * mm, v(-19.09, -15.11) * mm, v(-19.4, -15.4) * mm, v(-19.74, -15.32) * mm]});
            skFitSpline(sketch, "E4061", {"points": [v(-19.74, -15.32) * mm, v(-19.78, -15.32) * mm, v(-19.82, -15.3) * mm, v(-19.85, -15.29) * mm]});
            skFitSpline(sketch, "E4062", {"points": [v(-19.85, -15.29) * mm, v(-20.23, -15.08) * mm, v(-20.64, -14.94) * mm, v(-21, -14.7) * mm]});
            skFitSpline(sketch, "E4063", {"points": [v(-21, -14.7) * mm, v(-21.3, -14.5) * mm, v(-21.6, -14.35) * mm, v(-21.92, -14.2) * mm]});
            skFitSpline(sketch, "E4064", {"points": [v(-21.92, -14.2) * mm, v(-22.12, -14.1) * mm, v(-22.2, -13.93) * mm, v(-22.23, -13.74) * mm]});
            skFitSpline(sketch, "E4065", {"points": [v(-22.23, -13.74) * mm, v(-22.28, -13.43) * mm, v(-22.33, -13.12) * mm, v(-22.38, -12.82) * mm]});
            skFitSpline(sketch, "E4066", {"points": [v(-22.38, -12.82) * mm, v(-22.42, -12.6) * mm, v(-22.45, -12.37) * mm, v(-22.5, -12.15) * mm]});
            skFitSpline(sketch, "E4067", {"points": [v(-22.5, -12.15) * mm, v(-22.5, -12.12) * mm, v(-22.52, -12.08) * mm, v(-22.54, -12) * mm]});
            skFitSpline(sketch, "E4068", {"points": [v(-22.54, -12) * mm, v(-22.64, -12.21) * mm, v(-22.73, -12.38) * mm, v(-22.8, -12.55) * mm]});
            skFitSpline(sketch, "E4069", {"points": [v(-22.8, -12.55) * mm, v(-22.9, -12.75) * mm, v(-22.99, -12.96) * mm, v(-23.08, -13.16) * mm]});
            skFitSpline(sketch, "E4070", {"points": [v(-23.08, -13.16) * mm, v(-23.3, -13.62) * mm, v(-23.5, -14.08) * mm, v(-23.71, -14.53) * mm]});
            skFitSpline(sketch, "E4071", {"points": [v(-23.71, -14.53) * mm, v(-23.75, -14.61) * mm, v(-23.76, -14.68) * mm, v(-23.72, -14.76) * mm]});
            skFitSpline(sketch, "E4072", {"points": [v(-23.72, -14.76) * mm, v(-23.49, -15.28) * mm, v(-23.27, -15.8) * mm, v(-23.03, -16.31) * mm]});
            skFitSpline(sketch, "E4073", {"points": [v(-23.03, -16.31) * mm, v(-22.81, -16.77) * mm, v(-22.58, -17.23) * mm, v(-22.35, -17.68) * mm]});
            skFitSpline(sketch, "E4074", {"points": [v(-22.35, -17.68) * mm, v(-22.32, -17.74) * mm, v(-22.3, -17.79) * mm, v(-22.28, -17.84) * mm]});
            skFitSpline(sketch, "E4075", {"points": [v(-22.28, -17.84) * mm, v(-22.2, -18.1) * mm, v(-22.3, -18.35) * mm, v(-22.54, -18.46) * mm]});
            skFitSpline(sketch, "E4076", {"points": [v(-22.54, -18.46) * mm, v(-22.77, -18.56) * mm, v(-23.02, -18.48) * mm, v(-23.16, -18.25) * mm]});
            skFitSpline(sketch, "E4077", {"points": [v(-23.16, -18.25) * mm, v(-23.2, -18.18) * mm, v(-23.24, -18.1) * mm, v(-23.28, -18.02) * mm]});
            skFitSpline(sketch, "E4078", {"points": [v(-23.28, -18.02) * mm, v(-23.6, -17.36) * mm, v(-23.92, -16.7) * mm, v(-24.24, -16.03) * mm]});
            skFitSpline(sketch, "E4079", {"points": [v(-24.24, -16.03) * mm, v(-24.26, -15.98) * mm, v(-24.28, -15.94) * mm, v(-24.32, -15.86) * mm]});
            skFitSpline(sketch, "E4080", {"points": [v(-24.32, -15.86) * mm, v(-24.54, -16.33) * mm, v(-24.74, -16.78) * mm, v(-24.95, -17.23) * mm]});
            skFitSpline(sketch, "E4081", {"points": [v(-24.95, -17.23) * mm, v(-25.12, -17.58) * mm, v(-25.3, -17.93) * mm, v(-25.49, -18.27) * mm]});
            skFitSpline(sketch, "E4082", {"points": [v(-25.49, -18.27) * mm, v(-25.62, -18.5) * mm, v(-25.89, -18.57) * mm, v(-26.11, -18.45) * mm]});
            skFitSpline(sketch, "E4083", {"points": [v(-26.11, -18.45) * mm, v(-26.35, -18.34) * mm, v(-26.45, -18.08) * mm, v(-26.34, -17.82) * mm]});
            skFitSpline(sketch, "E4084", {"points": [v(-26.34, -17.82) * mm, v(-26.24, -17.58) * mm, v(-26.1, -17.36) * mm, v(-26, -17.13) * mm]});
            skFitSpline(sketch, "E4085", {"points": [v(-26, -17.13) * mm, v(-25.74, -16.59) * mm, v(-25.48, -16.04) * mm, v(-25.23, -15.49) * mm]});
            skFitSpline(sketch, "E4086", {"points": [v(-25.23, -15.49) * mm, v(-25.12, -15.25) * mm, v(-25.02, -15.02) * mm, v(-24.93, -14.78) * mm]});
            skFitSpline(sketch, "E4087", {"points": [v(-24.93, -14.78) * mm, v(-24.9, -14.71) * mm, v(-24.89, -14.62) * mm, v(-24.92, -14.56) * mm]});
            skFitSpline(sketch, "E4088", {"points": [v(-24.92, -14.56) * mm, v(-25.28, -13.74) * mm, v(-25.66, -12.93) * mm, v(-26.03, -12.12) * mm]});
            skFitSpline(sketch, "E4089", {"points": [v(-26.03, -12.12) * mm, v(-26.05, -12.1) * mm, v(-26.07, -12.07) * mm, v(-26.11, -12) * mm]});
            skFitSpline(sketch, "E4090", {"points": [v(-26.11, -12) * mm, v(-26.17, -12.3) * mm, v(-26.22, -12.57) * mm, v(-26.26, -12.84) * mm]});
            skFitSpline(sketch, "E4091", {"points": [v(-26.26, -12.84) * mm, v(-26.32, -13.15) * mm, v(-26.37, -13.46) * mm, v(-26.41, -13.76) * mm]});
            skFitSpline(sketch, "E4092", {"points": [v(-26.41, -13.76) * mm, v(-26.45, -14) * mm, v(-26.58, -14.12) * mm, v(-26.78, -14.22) * mm]});
            skFitSpline(sketch, "E4093", {"points": [v(-26.78, -14.22) * mm, v(-27.08, -14.37) * mm, v(-27.37, -14.55) * mm, v(-27.66, -14.7) * mm]});
            skFitSpline(sketch, "E4094", {"points": [v(-27.66, -14.7) * mm, v(-28.03, -14.9) * mm, v(-28.4, -15.11) * mm, v(-28.79, -15.28) * mm]});
            skFitSpline(sketch, "E4095", {"points": [v(-28.79, -15.28) * mm, v(-29.18, -15.45) * mm, v(-29.54, -15.18) * mm, v(-29.5, -14.76) * mm]});
            skFitSpline(sketch, "E4096", {"points": [v(-29.5, -14.76) * mm, v(-29.48, -14.6) * mm, v(-29.38, -14.49) * mm, v(-29.24, -14.41) * mm]});
            skFitSpline(sketch, "E4097", {"points": [v(-29.24, -14.41) * mm, v(-29.16, -14.37) * mm, v(-29.08, -14.34) * mm, v(-29, -14.3) * mm]});
            skFitSpline(sketch, "E4098", {"points": [v(-29, -14.3) * mm, v(-28.48, -14.11) * mm, v(-28.03, -13.77) * mm, v(-27.55, -13.52) * mm]});
            skFitSpline(sketch, "E4099", {"points": [v(-27.55, -13.52) * mm, v(-27.4, -13.45) * mm, v(-27.32, -13.35) * mm, v(-27.3, -13.17) * mm]});
            skFitSpline(sketch, "E4100", {"points": [v(-27.3, -13.17) * mm, v(-27.19, -12.5) * mm, v(-27.07, -11.84) * mm, v(-26.95, -11.17) * mm]});
            skFitSpline(sketch, "E4101", {"points": [v(-26.95, -11.17) * mm, v(-26.95, -11.15) * mm, v(-26.95, -11.12) * mm, v(-26.95, -11.07) * mm]});
            skFitSpline(sketch, "E4102", {"points": [v(-26.95, -11.07) * mm, v(-27.04, -11.1) * mm, v(-27.13, -11.13) * mm, v(-27.21, -11.16) * mm]});
            skFitSpline(sketch, "E4103", {"points": [v(-27.21, -11.16) * mm, v(-27.77, -11.36) * mm, v(-28.32, -11.56) * mm, v(-28.88, -11.76) * mm]});
            skFitSpline(sketch, "E4104", {"points": [v(-28.88, -11.76) * mm, v(-29.04, -11.82) * mm, v(-29.25, -11.74) * mm, v(-29.37, -11.59) * mm]});
            skFitSpline(sketch, "E4105", {"points": [v(-29.37, -11.59) * mm, v(-29.41, -11.53) * mm, v(-29.44, -11.47) * mm, v(-29.49, -11.4) * mm]});
            skFitSpline(sketch, "E4106", {"points": [v(-29.49, -11.4) * mm, v(-29.54, -11.41) * mm, v(-29.6, -11.43) * mm, v(-29.65, -11.44) * mm]});
            skFitSpline(sketch, "E4107", {"points": [v(-29.65, -11.44) * mm, v(-29.91, -11.48) * mm, v(-30.1, -11.38) * mm, v(-30.2, -11.14) * mm]});
            skFitSpline(sketch, "E4108", {"points": [v(-30.2, -11.14) * mm, v(-30.47, -10.57) * mm, v(-30.74, -10) * mm, v(-31.01, -9.43) * mm]});
            skFitSpline(sketch, "E4109", {"points": [v(-31.01, -9.43) * mm, v(-31.02, -9.41) * mm, v(-31.04, -9.4) * mm, v(-31.06, -9.38) * mm]});
            skFitSpline(sketch, "E4110", {"points": [v(-31.06, -9.38) * mm, v(-31.2, -9.56) * mm, v(-31.32, -9.75) * mm, v(-31.44, -9.93) * mm]});
            skFitSpline(sketch, "E4111", {"points": [v(-31.44, -9.93) * mm, v(-31.72, -10.32) * mm, v(-32, -10.72) * mm, v(-32.28, -11.1) * mm]});
            skFitSpline(sketch, "E4112", {"points": [v(-32.28, -11.1) * mm, v(-32.38, -11.24) * mm, v(-32.4, -11.36) * mm, v(-32.36, -11.52) * mm]});
            skFitSpline(sketch, "E4113", {"points": [v(-32.36, -11.52) * mm, v(-32.18, -12.1) * mm, v(-32.08, -12.71) * mm, v(-31.82, -13.28) * mm]});
            skFitSpline(sketch, "E4114", {"points": [v(-31.82, -13.28) * mm, v(-31.78, -13.37) * mm, v(-31.76, -13.48) * mm, v(-31.77, -13.58) * mm]});
            skFitSpline(sketch, "E4115", {"points": [v(-31.77, -13.58) * mm, v(-31.8, -13.77) * mm, v(-31.91, -13.91) * mm, v(-32.1, -13.97) * mm]});
            skFitSpline(sketch, "E4116", {"points": [v(-32.1, -13.97) * mm, v(-32.3, -14.03) * mm, v(-32.47, -13.97) * mm, v(-32.61, -13.83) * mm]});
            skFitSpline(sketch, "E4117", {"points": [v(-32.61, -13.83) * mm, v(-32.66, -13.78) * mm, v(-32.7, -13.72) * mm, v(-32.73, -13.65) * mm]});
            skFitSpline(sketch, "E4118", {"points": [v(-32.73, -13.65) * mm, v(-32.85, -13.28) * mm, v(-32.98, -12.91) * mm, v(-33.1, -12.54) * mm]});
            skFitSpline(sketch, "E4119", {"points": [v(-33.1, -12.54) * mm, v(-33.2, -12.16) * mm, v(-33.3, -11.77) * mm, v(-33.42, -11.4) * mm]});
            skFitSpline(sketch, "E4120", {"points": [v(-33.42, -11.4) * mm, v(-33.48, -11.2) * mm, v(-33.43, -11.05) * mm, v(-33.33, -10.9) * mm]});
            skFitSpline(sketch, "E4121", {"points": [v(-33.33, -10.9) * mm, v(-33.08, -10.55) * mm, v(-32.82, -10.2) * mm, v(-32.57, -9.84) * mm]});
            skFitSpline(sketch, "E4122", {"points": [v(-32.57, -9.84) * mm, v(-32.49, -9.72) * mm, v(-32.4, -9.6) * mm, v(-32.34, -9.44) * mm]});
            skFitSpline(sketch, "E4123", {"points": [v(-32.34, -9.44) * mm, v(-32.53, -9.5) * mm, v(-32.72, -9.57) * mm, v(-32.91, -9.64) * mm]});
            skFitSpline(sketch, "E4124", {"points": [v(-32.91, -9.64) * mm, v(-33.1, -9.7) * mm, v(-33.27, -9.78) * mm, v(-33.45, -9.85) * mm]});
            skFitSpline(sketch, "E4125", {"points": [v(-33.45, -9.85) * mm, v(-33.94, -10.03) * mm, v(-34.44, -10.2) * mm, v(-34.93, -10.4) * mm]});
            skFitSpline(sketch, "E4126", {"points": [v(-34.93, -10.4) * mm, v(-35, -10.42) * mm, v(-35.06, -10.49) * mm, v(-35.09, -10.55) * mm]});
            skFitSpline(sketch, "E4127", {"points": [v(-35.09, -10.55) * mm, v(-35.31, -11.12) * mm, v(-35.52, -11.68) * mm, v(-35.74, -12.25) * mm]});
            skFitSpline(sketch, "E4128", {"points": [v(-35.74, -12.25) * mm, v(-35.85, -12.55) * mm, v(-35.95, -12.85) * mm, v(-36.06, -13.15) * mm]});
            skFitSpline(sketch, "E4129", {"points": [v(-36.06, -13.15) * mm, v(-36.13, -13.35) * mm, v(-36.17, -13.55) * mm, v(-36.26, -13.74) * mm]});
            skFitSpline(sketch, "E4130", {"points": [v(-36.26, -13.74) * mm, v(-36.4, -14.06) * mm, v(-36.76, -14.13) * mm, v(-37.02, -13.91) * mm]});
            skFitSpline(sketch, "E4131", {"points": [v(-37.02, -13.91) * mm, v(-37.19, -13.77) * mm, v(-37.2, -13.57) * mm, v(-37.15, -13.38) * mm]});
            skFitSpline(sketch, "E4132", {"points": [v(-37.15, -13.38) * mm, v(-37.04, -13.01) * mm, v(-36.92, -12.64) * mm, v(-36.79, -12.27) * mm]});
            skFitSpline(sketch, "E4133", {"points": [v(-36.79, -12.27) * mm, v(-36.63, -11.83) * mm, v(-36.47, -11.39) * mm, v(-36.3, -10.9) * mm]});
            skFitSpline(sketch, "E4134", {"points": [v(-36.3, -10.9) * mm, v(-36.5, -10.97) * mm, v(-36.66, -11.04) * mm, v(-36.82, -11.1) * mm]});
            skFitSpline(sketch, "E4135", {"points": [v(-36.82, -11.1) * mm, v(-37.47, -11.32) * mm, v(-38.12, -11.55) * mm, v(-38.77, -11.76) * mm]});
            skFitSpline(sketch, "E4136", {"points": [v(-38.77, -11.76) * mm, v(-39.06, -11.85) * mm, v(-39.3, -11.73) * mm, v(-39.4, -11.47) * mm]});
            skFitSpline(sketch, "E4137", {"points": [v(-39.4, -11.47) * mm, v(-39.49, -11.22) * mm, v(-39.37, -10.96) * mm, v(-39.1, -10.85) * mm]});
            skFitSpline(sketch, "E4138", {"points": [v(-39.1, -10.85) * mm, v(-38.85, -10.75) * mm, v(-38.6, -10.69) * mm, v(-38.34, -10.6) * mm]});
            skFitSpline(sketch, "E4139", {"points": [v(-38.34, -10.6) * mm, v(-37.54, -10.3) * mm, v(-36.74, -10) * mm, v(-35.95, -9.7) * mm]});
            skFitSpline(sketch, "E4140", {"points": [v(-35.95, -9.7) * mm, v(-35.88, -9.67) * mm, v(-35.81, -9.6) * mm, v(-35.79, -9.54) * mm]});
            skFitSpline(sketch, "E4141", {"points": [v(-35.79, -9.54) * mm, v(-35.48, -8.73) * mm, v(-35.18, -7.91) * mm, v(-34.88, -7.1) * mm]});
            skFitSpline(sketch, "E4142", {"points": [v(-34.88, -7.1) * mm, v(-34.86, -7.05) * mm, v(-34.85, -7) * mm, v(-34.82, -6.9) * mm]});
            skFitSpline(sketch, "E4143", {"points": [v(-34.82, -6.9) * mm, v(-34.92, -6.97) * mm, v(-35, -7) * mm, v(-35.05, -7.05) * mm]});
            skFitSpline(sketch, "E4144", {"points": [v(-35.05, -7.05) * mm, v(-35.43, -7.32) * mm, v(-35.81, -7.59) * mm, v(-36.19, -7.86) * mm]});
            skFitSpline(sketch, "E4145", {"points": [v(-36.19, -7.86) * mm, v(-36.42, -8.04) * mm, v(-36.63, -8.1) * mm, v(-36.93, -7.97) * mm]});
            skFitSpline(sketch, "E4146", {"points": [v(-36.93, -7.97) * mm, v(-37.24, -7.83) * mm, v(-37.6, -7.8) * mm, v(-37.93, -7.7) * mm]});
            skFitSpline(sketch, "E4147", {"points": [v(-37.93, -7.7) * mm, v(-38.3, -7.59) * mm, v(-38.69, -7.47) * mm, v(-39.06, -7.32) * mm]});
            skFitSpline(sketch, "E4148", {"points": [v(-39.06, -7.32) * mm, v(-39.3, -7.23) * mm, v(-39.4, -7.03) * mm, v(-39.37, -6.79) * mm]});
            skFitSpline(sketch, "E4149", {"points": [v(-39.37, -6.79) * mm, v(-39.35, -6.59) * mm, v(-39.2, -6.42) * mm, v(-39, -6.38) * mm]});
            skFitSpline(sketch, "E4150", {"points": [v(-39, -6.38) * mm, v(-38.9, -6.37) * mm, v(-38.8, -6.37) * mm, v(-38.72, -6.4) * mm]});
            skFitSpline(sketch, "E4151", {"points": [v(-38.72, -6.4) * mm, v(-38.14, -6.67) * mm, v(-37.53, -6.79) * mm, v(-36.94, -6.96) * mm]});
            skFitSpline(sketch, "E4152", {"points": [v(-36.94, -6.96) * mm, v(-36.77, -7) * mm, v(-36.64, -7) * mm, v(-36.49, -6.89) * mm]});
            skFitSpline(sketch, "E4153", {"points": [v(-36.49, -6.89) * mm, v(-35.98, -6.51) * mm, v(-35.46, -6.16) * mm, v(-34.94, -5.8) * mm]});
            skFitSpline(sketch, "E4154", {"points": [v(-34.94, -5.8) * mm, v(-34.89, -5.75) * mm, v(-34.83, -5.7) * mm, v(-34.77, -5.66) * mm]});
            skFitSpline(sketch, "E4155", {"points": [v(-34.77, -5.66) * mm, v(-34.8, -5.64) * mm, v(-34.83, -5.61) * mm, v(-34.86, -5.6) * mm]});
            skFitSpline(sketch, "E4156", {"points": [v(-34.86, -5.6) * mm, v(-35.42, -5.34) * mm, v(-35.98, -5.07) * mm, v(-36.55, -4.8) * mm]});
            skFitSpline(sketch, "E4157", {"points": [v(-36.55, -4.8) * mm, v(-36.75, -4.71) * mm, v(-36.86, -4.56) * mm, v(-36.83, -4.33) * mm]});
            skFitSpline(sketch, "E4158", {"points": [v(-36.83, -4.33) * mm, v(-36.83, -4.25) * mm, v(-36.8, -4.17) * mm, v(-36.8, -4.09) * mm]});
            skFitSpline(sketch, "E4159", {"points": [v(-36.8, -4.09) * mm, v(-36.83, -4.07) * mm, v(-36.87, -4.05) * mm, v(-36.91, -4.02) * mm]});
            skFitSpline(sketch, "E4160", {"points": [v(-36.91, -4.02) * mm, v(-37.15, -3.87) * mm, v(-37.21, -3.67) * mm, v(-37.12, -3.4) * mm]});
            skFitSpline(sketch, "E4161", {"points": [v(-37.12, -3.4) * mm, v(-36.9, -2.81) * mm, v(-36.7, -2.22) * mm, v(-36.48, -1.62) * mm]});
            skFitSpline(sketch, "E4162", {"points": [v(-36.48, -1.62) * mm, v(-36.48, -1.61) * mm, v(-36.48, -1.6) * mm, v(-36.48, -1.55) * mm]});
            skFitSpline(sketch, "E4163", {"points": [v(-36.48, -1.55) * mm, v(-36.71, -1.59) * mm, v(-36.94, -1.63) * mm, v(-37.16, -1.67) * mm]});
            skFitSpline(sketch, "E4164", {"points": [v(-37.16, -1.67) * mm, v(-37.62, -1.74) * mm, v(-38.07, -1.83) * mm, v(-38.53, -1.9) * mm]});
            skFitSpline(sketch, "E4165", {"points": [v(-38.53, -1.9) * mm, v(-38.7, -1.92) * mm, v(-38.82, -1.97) * mm, v(-38.9, -2.12) * mm]});
            skFitSpline(sketch, "E4166", {"points": [v(-38.9, -2.12) * mm, v(-39.19, -2.67) * mm, v(-39.55, -3.18) * mm, v(-39.77, -3.77) * mm]});
            skFitSpline(sketch, "E4167", {"points": [v(-39.77, -3.77) * mm, v(-39.88, -4.08) * mm, v(-40.14, -4.17) * mm, v(-40.4, -4.08) * mm]});
            skFitSpline(sketch, "E4168", {"points": [v(-40.4, -4.08) * mm, v(-40.67, -4) * mm, v(-40.8, -3.68) * mm, v(-40.68, -3.4) * mm]});
            skFitSpline(sketch, "E4169", {"points": [v(-40.68, -3.4) * mm, v(-40.52, -3.05) * mm, v(-40.34, -2.7) * mm, v(-40.16, -2.36) * mm]});
            skFitSpline(sketch, "E4170", {"points": [v(-40.16, -2.36) * mm, v(-39.97, -2) * mm, v(-39.77, -1.66) * mm, v(-39.58, -1.31) * mm]});
            skFitSpline(sketch, "E4171", {"points": [v(-39.58, -1.31) * mm, v(-39.5, -1.15) * mm, v(-39.37, -1.06) * mm, v(-39.19, -1.03) * mm]});
            skFitSpline(sketch, "E4172", {"points": [v(-39.19, -1.03) * mm, v(-38.64, -0.94) * mm, v(-38.09, -0.84) * mm, v(-37.54, -0.75) * mm]});
            skFitSpline(sketch, "E4173", {"points": [v(-37.54, -0.75) * mm, v(-37.5, -0.74) * mm, v(-37.48, -0.73) * mm, v(-37.38, -0.71) * mm]});
            skFitSpline(sketch, "E4174", {"points": [v(-37.38, -0.71) * mm, v(-37.6, -0.6) * mm, v(-37.75, -0.52) * mm, v(-37.9, -0.45) * mm]});
            skFitSpline(sketch, "E4175", {"points": [v(-37.9, -0.45) * mm, v(-38.56, -0.15) * mm, v(-39.22, 0.14) * mm, v(-39.87, 0.44) * mm]});
            skFitSpline(sketch, "E4176", {"points": [v(-39.87, 0.44) * mm, v(-39.99, 0.5) * mm, v(-40.08, 0.51) * mm, v(-40.2, 0.46) * mm]});
            skFitSpline(sketch, "E4177", {"points": [v(-40.2, 0.46) * mm, v(-40.76, 0.2) * mm, v(-41.33, -0.05) * mm, v(-41.88, -0.31) * mm]});
            skFitSpline(sketch, "E4178", {"points": [v(-41.88, -0.31) * mm, v(-42.3, -0.5) * mm, v(-42.7, -0.71) * mm, v(-43.1, -0.9) * mm]});
            skFitSpline(sketch, "E4179", {"points": [v(-43.1, -0.9) * mm, v(-43.2, -0.95) * mm, v(-43.3, -0.98) * mm, v(-43.4, -0.98) * mm]});
            skFitSpline(sketch, "E4180", {"points": [v(-43.4, -0.98) * mm, v(-43.62, -1) * mm, v(-43.82, -0.85) * mm, v(-43.87, -0.65) * mm]});
            skFitSpline(sketch, "E4181", {"points": [v(-43.87, -0.65) * mm, v(-43.93, -0.44) * mm, v(-43.86, -0.22) * mm, v(-43.68, -0.1) * mm]});
            skFitSpline(sketch, "E4182", {"points": [v(-43.68, -0.1) * mm, v(-43.58, -0.04) * mm, v(-43.48, 0) * mm, v(-43.38, 0.05) * mm]});
            skFitSpline(sketch, "E4183", {"points": [v(-43.38, 0.05) * mm, v(-42.77, 0.34) * mm, v(-42.16, 0.64) * mm, v(-41.55, 0.93) * mm]});
            skFitSpline(sketch, "E4184", {"points": [v(-41.55, 0.93) * mm, v(-41.46, 0.97) * mm, v(-41.38, 1.02) * mm, v(-41.26, 1.07) * mm]});
            skFitSpline(sketch, "E4185", {"points": [v(-41.26, 1.07) * mm, v(-41.34, 1.12) * mm, v(-41.4, 1.15) * mm, v(-41.45, 1.17) * mm]});
            skFitSpline(sketch, "E4186", {"points": [v(-41.45, 1.17) * mm, v(-41.87, 1.36) * mm, v(-42.3, 1.55) * mm, v(-42.71, 1.75) * mm]});
            skFitSpline(sketch, "E4187", {"points": [v(-42.71, 1.75) * mm, v(-43.02, 1.9) * mm, v(-43.32, 2.06) * mm, v(-43.63, 2.22) * mm]});
            skFitSpline(sketch, "E4188", {"points": [v(-43.63, 2.22) * mm, v(-43.87, 2.36) * mm, v(-43.96, 2.62) * mm, v(-43.85, 2.86) * mm]});
            skFitSpline(sketch, "E4189", {"points": [v(-43.85, 2.86) * mm, v(-43.74, 3.1) * mm, v(-43.48, 3.2) * mm, v(-43.23, 3.1) * mm]});
            skFitSpline(sketch, "E4190", {"points": [v(-43.23, 3.1) * mm, v(-43.03, 3.02) * mm, v(-42.84, 2.9) * mm, v(-42.65, 2.82) * mm]});
            skFitSpline(sketch, "E4191", {"points": [v(-42.65, 2.82) * mm, v(-41.99, 2.5) * mm, v(-41.32, 2.2) * mm, v(-40.65, 1.9) * mm]});
            skFitSpline(sketch, "E4192", {"points": [v(-40.65, 1.9) * mm, v(-40.5, 1.82) * mm, v(-40.33, 1.75) * mm, v(-40.17, 1.68) * mm]});
            skFitSpline(sketch, "E4193", {"points": [v(-40.17, 1.68) * mm, v(-40.08, 1.64) * mm, v(-40, 1.64) * mm, v(-39.92, 1.68) * mm]});
            skFitSpline(sketch, "E4194", {"points": [v(-39.92, 1.68) * mm, v(-39.17, 2.03) * mm, v(-38.43, 2.37) * mm, v(-37.68, 2.7) * mm]});
            skFitSpline(sketch, "E4195", {"points": [v(-37.68, 2.7) * mm, v(-37.6, 2.74) * mm, v(-37.52, 2.79) * mm, v(-37.45, 2.87) * mm]});
            skFitSpline(sketch, "E4196", {"points": [v(-37.45, 2.87) * mm, v(-37.56, 2.9) * mm, v(-37.67, 2.93) * mm, v(-37.78, 2.94) * mm]});
            skFitSpline(sketch, "E4197", {"points": [v(-37.78, 2.94) * mm, v(-38.22, 3.02) * mm, v(-38.66, 3.1) * mm, v(-39.1, 3.16) * mm]});
            skFitSpline(sketch, "E4198", {"points": [v(-39.1, 3.16) * mm, v(-39.36, 3.2) * mm, v(-39.52, 3.32) * mm, v(-39.63, 3.58) * mm]});
            skFitSpline(sketch, "E4199", {"points": [v(-39.63, 3.58) * mm, v(-39.74, 3.87) * mm, v(-39.94, 4.13) * mm, v(-40.1, 4.41) * mm]});
            skFitSpline(sketch, "E4200", {"points": [v(-40.1, 4.41) * mm, v(-40.3, 4.78) * mm, v(-40.5, 5.16) * mm, v(-40.67, 5.54) * mm]});
            skFitSpline(sketch, "E4201", {"points": [v(-40.67, 5.54) * mm, v(-40.84, 5.92) * mm, v(-40.58, 6.28) * mm, v(-40.19, 6.26) * mm]});
            skFitSpline(sketch, "E4202", {"points": [v(-40.19, 6.26) * mm, v(-40, 6.24) * mm, v(-39.87, 6.14) * mm, v(-39.8, 5.98) * mm]});
            skFitSpline(sketch, "E4203", {"points": [v(-39.8, 5.98) * mm, v(-39.75, 5.88) * mm, v(-39.7, 5.78) * mm, v(-39.66, 5.68) * mm]});
            skFitSpline(sketch, "E4204", {"points": [v(-39.66, 5.68) * mm, v(-39.48, 5.18) * mm, v(-39.14, 4.76) * mm, v(-38.9, 4.29) * mm]});
            skFitSpline(sketch, "E4205", {"points": [v(-38.9, 4.29) * mm, v(-38.83, 4.14) * mm, v(-38.72, 4.08) * mm, v(-38.55, 4.05) * mm]});
            skFitSpline(sketch, "E4206", {"points": [v(-38.55, 4.05) * mm, v(-37.93, 3.95) * mm, v(-37.32, 3.84) * mm, v(-36.7, 3.73) * mm]});
            skFitSpline(sketch, "E4207", {"points": [v(-36.7, 3.73) * mm, v(-36.64, 3.72) * mm, v(-36.57, 3.72) * mm, v(-36.47, 3.7) * mm]});
            skFitSpline(sketch, "E4208", {"points": [v(-36.47, 3.7) * mm, v(-36.49, 3.77) * mm, v(-36.5, 3.81) * mm, v(-36.51, 3.85) * mm]});
            skFitSpline(sketch, "E4209", {"points": [v(-36.51, 3.85) * mm, v(-36.72, 4.44) * mm, v(-36.93, 5.02) * mm, v(-37.14, 5.6) * mm]});
            skFitSpline(sketch, "E4210", {"points": [v(-37.14, 5.6) * mm, v(-37.2, 5.8) * mm, v(-37.14, 6) * mm, v(-36.98, 6.12) * mm]});
            skFitSpline(sketch, "E4211", {"points": [v(-36.98, 6.12) * mm, v(-36.93, 6.17) * mm, v(-36.86, 6.2) * mm, v(-36.8, 6.24) * mm]});
            skFitSpline(sketch, "E4212", {"points": [v(-36.8, 6.24) * mm, v(-36.8, 6.3) * mm, v(-36.82, 6.36) * mm, v(-36.83, 6.42) * mm]});
            skFitSpline(sketch, "E4213", {"points": [v(-36.83, 6.42) * mm, v(-36.86, 6.7) * mm, v(-36.77, 6.85) * mm, v(-36.52, 6.97) * mm]});
            skFitSpline(sketch, "E4214", {"points": [v(-36.52, 6.97) * mm, v(-35.94, 7.25) * mm, v(-35.37, 7.52) * mm, v(-34.77, 7.81) * mm]});
            skFitSpline(sketch, "E4215", {"points": [v(-34.77, 7.81) * mm, v(-34.84, 7.86) * mm, v(-34.9, 7.9) * mm, v(-34.95, 7.95) * mm]});
            skFitSpline(sketch, "E4216", {"points": [v(-34.95, 7.95) * mm, v(-35.46, 8.3) * mm, v(-35.98, 8.66) * mm, v(-36.48, 9.03) * mm]});
            skFitSpline(sketch, "E4217", {"points": [v(-36.48, 9.03) * mm, v(-36.63, 9.13) * mm, v(-36.76, 9.16) * mm, v(-36.92, 9.11) * mm]});
            skFitSpline(sketch, "E4218", {"points": [v(-36.92, 9.11) * mm, v(-37.52, 8.94) * mm, v(-38.13, 8.81) * mm, v(-38.7, 8.56) * mm]});
            skFitSpline(sketch, "E4219", {"points": [v(-38.7, 8.56) * mm, v(-39.08, 8.4) * mm, v(-39.44, 8.7) * mm, v(-39.37, 9.1) * mm]});
            skFitSpline(sketch, "E4220", {"points": [v(-39.37, 9.1) * mm, v(-39.34, 9.3) * mm, v(-39.21, 9.43) * mm, v(-39.03, 9.5) * mm]});
            skFitSpline(sketch, "E4221", {"points": [v(-39.03, 9.5) * mm, v(-38.62, 9.62) * mm, v(-38.24, 9.8) * mm, v(-37.82, 9.88) * mm]});
            skFitSpline(sketch, "E4222", {"points": [v(-37.82, 9.88) * mm, v(-37.47, 9.95) * mm, v(-37.13, 10.08) * mm, v(-36.79, 10.18) * mm]});
            skFitSpline(sketch, "E4223", {"points": [v(-36.79, 10.18) * mm, v(-36.6, 10.24) * mm, v(-36.43, 10.19) * mm, v(-36.27, 10.07) * mm]});
            skFitSpline(sketch, "E4224", {"points": [v(-36.27, 10.07) * mm, v(-35.92, 9.81) * mm, v(-35.56, 9.56) * mm, v(-35.2, 9.3) * mm]});
            skFitSpline(sketch, "E4225", {"points": [v(-35.2, 9.3) * mm, v(-35.09, 9.23) * mm, v(-34.98, 9.15) * mm, v(-34.83, 9.1) * mm]});
            skFitSpline(sketch, "E4226", {"points": [v(-34.83, 9.1) * mm, v(-34.9, 9.29) * mm, v(-34.96, 9.48) * mm, v(-35.03, 9.67) * mm]});
            skFitSpline(sketch, "E4227", {"points": [v(-35.03, 9.67) * mm, v(-35.1, 9.84) * mm, v(-35.17, 10) * mm, v(-35.23, 10.18) * mm]});
            skFitSpline(sketch, "E4228", {"points": [v(-35.23, 10.18) * mm, v(-35.42, 10.68) * mm, v(-35.6, 11.18) * mm, v(-35.79, 11.68) * mm]});
            skFitSpline(sketch, "E4229", {"points": [v(-35.79, 11.68) * mm, v(-35.81, 11.75) * mm, v(-35.88, 11.82) * mm, v(-35.94, 11.84) * mm]});
            skFitSpline(sketch, "E4230", {"points": [v(-35.94, 11.84) * mm, v(-36.47, 12.05) * mm, v(-37, 12.26) * mm, v(-37.53, 12.46) * mm]});
            skFitSpline(sketch, "E4231", {"points": [v(-37.53, 12.46) * mm, v(-38, 12.63) * mm, v(-38.5, 12.78) * mm, v(-38.98, 12.95) * mm]});
            skFitSpline(sketch, "E4232", {"points": [v(-38.98, 12.95) * mm, v(-39.03, 12.97) * mm, v(-39.08, 12.99) * mm, v(-39.13, 13.01) * mm]});
            skFitSpline(sketch, "E4233", {"points": [v(-39.13, 13.01) * mm, v(-39.37, 13.14) * mm, v(-39.48, 13.38) * mm, v(-39.4, 13.6) * mm]});
            skFitSpline(sketch, "E4234", {"points": [v(-39.4, 13.6) * mm, v(-39.3, 13.86) * mm, v(-39.07, 14) * mm, v(-38.8, 13.92) * mm]});
            skFitSpline(sketch, "E4235", {"points": [v(-38.8, 13.92) * mm, v(-38.6, 13.87) * mm, v(-38.42, 13.8) * mm, v(-38.23, 13.74) * mm]});
            skFitSpline(sketch, "E4236", {"points": [v(-38.23, 13.74) * mm, v(-37.63, 13.53) * mm, v(-37.03, 13.31) * mm, v(-36.43, 13.1) * mm]});
            skFitSpline(sketch, "E4237", {"points": [v(-36.43, 13.1) * mm, v(-36.4, 13.09) * mm, v(-36.37, 13.08) * mm, v(-36.31, 13.06) * mm]});
            skFitSpline(sketch, "E4238", {"points": [v(-36.31, 13.06) * mm, v(-36.35, 13.26) * mm, v(-36.44, 13.43) * mm, v(-36.5, 13.6) * mm]});
            skFitSpline(sketch, "E4239", {"points": [v(-36.5, 13.6) * mm, v(-36.72, 14.25) * mm, v(-36.94, 14.88) * mm, v(-37.15, 15.53) * mm]});
            skFitSpline(sketch, "E4240", {"points": [v(-37.15, 15.53) * mm, v(-37.2, 15.66) * mm, v(-37.2, 15.81) * mm, v(-37.11, 15.95) * mm]});
            skFitSpline(sketch, "E4241", {"points": [v(-37.11, 15.95) * mm, v(-36.92, 16.26) * mm, v(-36.48, 16.26) * mm, v(-36.28, 15.93) * mm]});
            skFitSpline(sketch, "E4242", {"points": [v(-36.28, 15.93) * mm, v(-36.21, 15.81) * mm, v(-36.16, 15.67) * mm, v(-36.12, 15.54) * mm]});
            skFitSpline(sketch, "E4243", {"points": [v(-36.12, 15.54) * mm, v(-35.84, 14.58) * mm, v(-35.47, 13.65) * mm, v(-35.1, 12.73) * mm]});
            skFitSpline(sketch, "E4244", {"points": [v(-35.1, 12.73) * mm, v(-35.07, 12.64) * mm, v(-35.03, 12.58) * mm, v(-34.94, 12.54) * mm]});
            skFitSpline(sketch, "E4245", {"points": [v(-34.94, 12.54) * mm, v(-34.13, 12.25) * mm, v(-33.33, 11.95) * mm, v(-32.53, 11.65) * mm]});
            skFitSpline(sketch, "E4246", {"points": [v(-32.53, 11.65) * mm, v(-32.47, 11.63) * mm, v(-32.4, 11.61) * mm, v(-32.29, 11.58) * mm]});
            skFitSpline(sketch, "E4247", {"points": [v(-32.29, 11.58) * mm, v(-32.4, 11.74) * mm, v(-32.48, 11.87) * mm, v(-32.57, 11.99) * mm]});
            skFitSpline(sketch, "E4248", {"points": [v(-32.57, 11.99) * mm, v(-32.81, 12.33) * mm, v(-33.05, 12.67) * mm, v(-33.3, 13) * mm]});
            skFitSpline(sketch, "E4249", {"points": [v(-33.3, 13) * mm, v(-33.45, 13.21) * mm, v(-33.48, 13.4) * mm, v(-33.37, 13.67) * mm]});
            skFitSpline(sketch, "E4250", {"points": [v(-33.37, 13.67) * mm, v(-33.24, 14) * mm, v(-33.19, 14.38) * mm, v(-33.09, 14.73) * mm]});
            skFitSpline(sketch, "E4251", {"points": [v(-33.09, 14.73) * mm, v(-32.98, 15.1) * mm, v(-32.86, 15.46) * mm, v(-32.72, 15.81) * mm]});
            skFitSpline(sketch, "E4252", {"points": [v(-32.72, 15.81) * mm, v(-32.63, 16.05) * mm, v(-32.4, 16.17) * mm, v(-32.18, 16.14) * mm]});
            skFitSpline(sketch, "E4253", {"points": [v(-32.18, 16.14) * mm, v(-31.97, 16.1) * mm, v(-31.8, 15.95) * mm, v(-31.77, 15.73) * mm]});
            skFitSpline(sketch, "E4254", {"points": [v(-31.77, 15.73) * mm, v(-31.76, 15.64) * mm, v(-31.77, 15.54) * mm, v(-31.8, 15.45) * mm]});
            skFitSpline(sketch, "E4255", {"points": [v(-31.8, 15.45) * mm, v(-32.07, 14.9) * mm, v(-32.17, 14.28) * mm, v(-32.35, 13.7) * mm]});
            skFitSpline(sketch, "E4256", {"points": [v(-32.35, 13.7) * mm, v(-32.4, 13.53) * mm, v(-32.39, 13.39) * mm, v(-32.27, 13.23) * mm]});
            skFitSpline(sketch, "E4257", {"points": [v(-32.27, 13.23) * mm, v(-31.9, 12.74) * mm, v(-31.56, 12.23) * mm, v(-31.2, 11.73) * mm]});
            skFitSpline(sketch, "E4258", {"points": [v(-31.2, 11.73) * mm, v(-31.16, 11.66) * mm, v(-31.1, 11.6) * mm, v(-31.05, 11.52) * mm]});
            skFitSpline(sketch, "E4259", {"points": [v(-31.05, 11.52) * mm, v(-31.01, 11.6) * mm, v(-30.99, 11.65) * mm, v(-30.96, 11.7) * mm]});
            skFitSpline(sketch, "E4260", {"points": [v(-30.96, 11.7) * mm, v(-30.7, 12.24) * mm, v(-30.45, 12.79) * mm, v(-30.19, 13.32) * mm]});
            skFitSpline(sketch, "E4261", {"points": [v(-30.19, 13.32) * mm, v(-30.1, 13.51) * mm, v(-29.94, 13.62) * mm, v(-29.72, 13.6) * mm]});
            skFitSpline(sketch, "E4262", {"points": [v(-29.72, 13.6) * mm, v(-29.65, 13.59) * mm, v(-29.57, 13.57) * mm, v(-29.48, 13.55) * mm]});
            skFitSpline(sketch, "E4263", {"points": [v(-29.48, 13.55) * mm, v(-29.47, 13.58) * mm, v(-29.45, 13.6) * mm, v(-29.44, 13.63) * mm]});
            skFitSpline(sketch, "E4264", {"points": [v(-29.44, 13.63) * mm, v(-29.28, 13.9) * mm, v(-29.07, 13.97) * mm, v(-28.79, 13.87) * mm]});
            skFitSpline(sketch, "E4265", {"points": [v(-28.79, 13.87) * mm, v(-28.2, 13.67) * mm, v(-27.63, 13.46) * mm, v(-27.05, 13.25) * mm]});
            skFitSpline(sketch, "E4266", {"points": [v(-27.05, 13.25) * mm, v(-27.02, 13.24) * mm, v(-27, 13.23) * mm, v(-26.94, 13.22) * mm]});
            skFitSpline(sketch, "E4267", {"points": [v(-26.94, 13.22) * mm, v(-26.97, 13.42) * mm, v(-27, 13.6) * mm, v(-27.04, 13.8) * mm]});
            skFitSpline(sketch, "E4268", {"points": [v(-27.04, 13.8) * mm, v(-27.13, 14.3) * mm, v(-27.22, 14.82) * mm, v(-27.3, 15.33) * mm]});
            skFitSpline(sketch, "E4269", {"points": [v(-27.3, 15.33) * mm, v(-27.32, 15.47) * mm, v(-27.38, 15.58) * mm, v(-27.51, 15.65) * mm]});
            skFitSpline(sketch, "E4270", {"points": [v(-27.51, 15.65) * mm, v(-28.06, 15.95) * mm, v(-28.57, 16.3) * mm, v(-29.16, 16.52) * mm]});
            skFitSpline(sketch, "E4271", {"points": [v(-29.16, 16.52) * mm, v(-29.37, 16.6) * mm, v(-29.49, 16.75) * mm, v(-29.5, 17) * mm]});
            skFitSpline(sketch, "E4272", {"points": [v(-29.5, 17) * mm, v(-29.51, 17.27) * mm, v(-29.24, 17.52) * mm, v(-28.94, 17.48) * mm]});
            skFitSpline(sketch, "E4273", {"points": [v(-28.94, 17.48) * mm, v(-28.89, 17.47) * mm, v(-28.83, 17.46) * mm, v(-28.78, 17.43) * mm]});
            skFitSpline(sketch, "E4274", {"points": [v(-28.78, 17.43) * mm, v(-28.5, 17.3) * mm, v(-28.2, 17.17) * mm, v(-27.92, 17.02) * mm]});
            skFitSpline(sketch, "E4275", {"points": [v(-27.92, 17.02) * mm, v(-27.58, 16.84) * mm, v(-27.26, 16.63) * mm, v(-26.93, 16.43) * mm]});
            skFitSpline(sketch, "E4276", {"points": [v(-26.93, 16.43) * mm, v(-26.9, 16.41) * mm, v(-26.86, 16.39) * mm, v(-26.82, 16.38) * mm]});
            skFitSpline(sketch, "E4277", {"points": [v(-26.82, 16.38) * mm, v(-26.56, 16.3) * mm, v(-26.45, 16.12) * mm, v(-26.4, 15.86) * mm]});
            skFitSpline(sketch, "E4278", {"points": [v(-26.4, 15.86) * mm, v(-26.32, 15.33) * mm, v(-26.23, 14.8) * mm, v(-26.14, 14.28) * mm]});
            skFitSpline(sketch, "E4279", {"points": [v(-26.14, 14.28) * mm, v(-26.13, 14.25) * mm, v(-26.12, 14.22) * mm, v(-26.1, 14.14) * mm]});
            skFitSpline(sketch, "E4280", {"points": [v(-26.1, 14.14) * mm, v(-26, 14.35) * mm, v(-25.91, 14.52) * mm, v(-25.83, 14.69) * mm]});
            skFitSpline(sketch, "E4281", {"points": [v(-25.83, 14.69) * mm, v(-25.74, 14.9) * mm, v(-25.65, 15.11) * mm, v(-25.55, 15.32) * mm]});
            skFitSpline(sketch, "E4282", {"points": [v(-25.55, 15.32) * mm, v(-25.34, 15.78) * mm, v(-25.13, 16.24) * mm, v(-24.92, 16.7) * mm]});
            skFitSpline(sketch, "E4283", {"points": [v(-24.92, 16.7) * mm, v(-24.88, 16.77) * mm, v(-24.88, 16.84) * mm, v(-24.92, 16.92) * mm]});
            skFitSpline(sketch, "E4284", {"points": [v(-24.92, 16.92) * mm, v(-25.17, 17.48) * mm, v(-25.42, 18.04) * mm, v(-25.68, 18.6) * mm]});
            skFitSpline(sketch, "E4285", {"points": [v(-25.68, 18.6) * mm, v(-25.88, 19.02) * mm, v(-26.09, 19.43) * mm, v(-26.29, 19.84) * mm]});
            skFitSpline(sketch, "E4286", {"points": [v(-26.29, 19.84) * mm, v(-26.32, 19.92) * mm, v(-26.36, 20) * mm, v(-26.37, 20.07) * mm]});
            skFitSpline(sketch, "E4287", {"points": [v(-26.37, 20.07) * mm, v(-26.41, 20.32) * mm, v(-26.29, 20.54) * mm, v(-26.06, 20.62) * mm]});
            skFitSpline(sketch, "E4288", {"points": [v(-26.06, 20.62) * mm, v(-25.83, 20.7) * mm, v(-25.6, 20.62) * mm, v(-25.47, 20.4) * mm]});
            skFitSpline(sketch, "E4289", {"points": [v(-25.47, 20.4) * mm, v(-25.43, 20.31) * mm, v(-25.4, 20.23) * mm, v(-25.35, 20.15) * mm]});
            skFitSpline(sketch, "E4290", {"points": [v(-25.35, 20.15) * mm, v(-25.03, 19.48) * mm, v(-24.7, 18.8) * mm, v(-24.38, 18.13) * mm]});
            skFitSpline(sketch, "E4291", {"points": [v(-24.38, 18.13) * mm, v(-24.36, 18.1) * mm, v(-24.35, 18.07) * mm, v(-24.32, 18) * mm]});
            skFitSpline(sketch, "E4292", {"points": [v(-24.32, 18) * mm, v(-24.24, 18.18) * mm, v(-24.17, 18.33) * mm, v(-24.1, 18.47) * mm]});
            skFitSpline(sketch, "E4293", {"points": [v(-24.1, 18.47) * mm, v(-23.8, 19.1) * mm, v(-23.5, 19.74) * mm, v(-23.18, 20.37) * mm]});
            skFitSpline(sketch, "E4294", {"points": [v(-23.18, 20.37) * mm, v(-23.04, 20.63) * mm, v(-22.78, 20.72) * mm, v(-22.53, 20.6) * mm]});
            skFitSpline(sketch, "E4295", {"points": [v(-22.53, 20.6) * mm, v(-22.29, 20.5) * mm, v(-22.18, 20.23) * mm, v(-22.3, 19.96) * mm]});
            skFitSpline(sketch, "E4296", {"points": [v(-22.3, 19.96) * mm, v(-22.4, 19.72) * mm, v(-22.54, 19.5) * mm, v(-22.65, 19.25) * mm]});
            skFitSpline(sketch, "E4297", {"points": [v(-22.65, 19.25) * mm, v(-23, 18.48) * mm, v(-23.36, 17.7) * mm, v(-23.71, 16.92) * mm]});
            skFitSpline(sketch, "E4298", {"points": [v(-23.71, 16.92) * mm, v(-23.74, 16.86) * mm, v(-23.74, 16.76) * mm, v(-23.72, 16.7) * mm]});
            skFitSpline(sketch, "E4299", {"points": [v(-23.72, 16.7) * mm, v(-23.37, 15.92) * mm, v(-23, 15.15) * mm, v(-22.65, 14.37) * mm]});
            skFitSpline(sketch, "E4300", {"points": [v(-22.65, 14.37) * mm, v(-22.62, 14.31) * mm, v(-22.6, 14.26) * mm, v(-22.55, 14.17) * mm]});
            skFitSpline(sketch, "E4301", {"points": [v(-22.55, 14.17) * mm, v(-22.52, 14.24) * mm, v(-22.5, 14.27) * mm, v(-22.5, 14.31) * mm]});
            skFitSpline(sketch, "E4302", {"points": [v(-22.5, 14.31) * mm, v(-22.4, 14.82) * mm, v(-22.31, 15.32) * mm, v(-22.24, 15.82) * mm]});
            skFitSpline(sketch, "E4303", {"points": [v(-22.24, 15.82) * mm, v(-22.2, 16.1) * mm, v(-22.08, 16.28) * mm, v(-21.8, 16.39) * mm]});
            skFitSpline(sketch, "E4304", {"points": [v(-21.8, 16.39) * mm, v(-21.52, 16.5) * mm, v(-21.26, 16.7) * mm, v(-21, 16.85) * mm]});
            skFitSpline(sketch, "E4305", {"points": [v(-21, 16.85) * mm, v(-20.62, 17.05) * mm, v(-20.25, 17.25) * mm, v(-19.86, 17.43) * mm]});
            skFitSpline(sketch, "E4306", {"points": [v(-19.86, 17.43) * mm, v(-19.49, 17.6) * mm, v(-19.11, 17.34) * mm, v(-19.13, 16.96) * mm]});
            skFitSpline(sketch, "E4307", {"points": [v(-19.13, 16.96) * mm, v(-19.14, 16.76) * mm, v(-19.24, 16.61) * mm, v(-19.42, 16.55) * mm]});
            skFitSpline(sketch, "E4308", {"points": [v(-19.42, 16.55) * mm, v(-20, 16.34) * mm, v(-20.5, 16) * mm, v(-21.03, 15.7) * mm]});
            skFitSpline(sketch, "E4309", {"points": [v(-21.03, 15.7) * mm, v(-21.21, 15.6) * mm, v(-21.32, 15.48) * mm, v(-21.35, 15.25) * mm]});
            skFitSpline(sketch, "E4310", {"points": [v(-21.35, 15.25) * mm, v(-21.44, 14.58) * mm, v(-21.58, 13.92) * mm, v(-21.7, 13.22) * mm]});
            skFitSpline(sketch, "E4311", {"points": [v(-21.7, 13.22) * mm, v(-21.61, 13.25) * mm, v(-21.55, 13.27) * mm, v(-21.49, 13.29) * mm]});
            skFitSpline(sketch, "E4312", {"points": [v(-21.49, 13.29) * mm, v(-20.93, 13.49) * mm, v(-20.38, 13.7) * mm, v(-19.82, 13.88) * mm]});
            skFitSpline(sketch, "E4313", {"points": [v(-19.82, 13.88) * mm, v(-19.53, 13.98) * mm, v(-19.35, 13.88) * mm, v(-19.15, 13.55) * mm]});
            skFitSpline(sketch, "E4314", {"points": [v(-19.15, 13.55) * mm, v(-19.1, 13.56) * mm, v(-19.05, 13.58) * mm, v(-19, 13.6) * mm]});
            skFitSpline(sketch, "E4315", {"points": [v(-19, 13.6) * mm, v(-18.73, 13.64) * mm, v(-18.55, 13.54) * mm, v(-18.43, 13.3) * mm]});
            skFitSpline(sketch, "E4316", {"points": [v(-18.43, 13.3) * mm, v(-18.17, 12.72) * mm, v(-17.9, 12.15) * mm, v(-17.63, 11.58) * mm]});
            skFitSpline(sketch, "E4317", {"points": [v(-17.63, 11.58) * mm, v(-17.62, 11.57) * mm, v(-17.6, 11.56) * mm, v(-17.58, 11.54) * mm]});
            skFitSpline(sketch, "E4318", {"points": [v(-17.58, 11.54) * mm, v(-17.54, 11.59) * mm, v(-17.5, 11.63) * mm, v(-17.46, 11.68) * mm]});
            skFitSpline(sketch, "E4319", {"points": [v(-17.46, 11.68) * mm, v(-17.09, 12.21) * mm, v(-16.71, 12.75) * mm, v(-16.33, 13.29) * mm]});
            skFitSpline(sketch, "E4320", {"points": [v(-16.33, 13.29) * mm, v(-16.25, 13.4) * mm, v(-16.23, 13.5) * mm, v(-16.27, 13.62) * mm]});
            skFitSpline(sketch, "E4321", {"points": [v(-16.27, 13.62) * mm, v(-16.44, 14.22) * mm, v(-16.56, 14.84) * mm, v(-16.81, 15.42) * mm]});
            skFitSpline(sketch, "E4322", {"points": [v(-16.81, 15.42) * mm, v(-16.94, 15.71) * mm, v(-16.84, 15.98) * mm, v(-16.6, 16.1) * mm]});
            skFitSpline(sketch, "E4323", {"points": [v(-16.6, 16.1) * mm, v(-16.34, 16.21) * mm, v(-16.03, 16.1) * mm, v(-15.92, 15.82) * mm]});
            skFitSpline(sketch, "E4324", {"points": [v(-15.92, 15.82) * mm, v(-15.77, 15.43) * mm, v(-15.65, 15.04) * mm, v(-15.53, 14.64) * mm]});
            skFitSpline(sketch, "E4325", {"points": [v(-15.53, 14.64) * mm, v(-15.42, 14.28) * mm, v(-15.33, 13.92) * mm, v(-15.22, 13.56) * mm]});
            skFitSpline(sketch, "E4326", {"points": [v(-15.22, 13.56) * mm, v(-15.16, 13.37) * mm, v(-15.2, 13.2) * mm, v(-15.31, 13.04) * mm]});
            skFitSpline(sketch, "E4327", {"points": [v(-15.31, 13.04) * mm, v(-15.57, 12.69) * mm, v(-15.82, 12.33) * mm, v(-16.08, 11.97) * mm]});
            skFitSpline(sketch, "E4328", {"points": [v(-16.08, 11.97) * mm, v(-16.16, 11.85) * mm, v(-16.24, 11.74) * mm, v(-16.3, 11.58) * mm]});
            skFitSpline(sketch, "E4329", {"points": [v(-16.3, 11.58) * mm, v(-16.11, 11.65) * mm, v(-15.92, 11.71) * mm, v(-15.73, 11.78) * mm]});
            skFitSpline(sketch, "E4330", {"points": [v(-15.73, 11.78) * mm, v(-15.56, 11.85) * mm, v(-15.4, 11.92) * mm, v(-15.22, 11.98) * mm]});
            skFitSpline(sketch, "E4331", {"points": [v(-15.22, 11.98) * mm, v(-14.72, 12.17) * mm, v(-14.22, 12.36) * mm, v(-13.71, 12.54) * mm]});
            skFitSpline(sketch, "E4332", {"points": [v(-13.71, 12.54) * mm, v(-13.62, 12.57) * mm, v(-13.57, 12.62) * mm, v(-13.54, 12.71) * mm]});
            skFitSpline(sketch, "E4333", {"points": [v(-13.54, 12.71) * mm, v(-13.32, 13.29) * mm, v(-13.1, 13.86) * mm, v(-12.89, 14.44) * mm]});
            skFitSpline(sketch, "E4334", {"points": [v(-12.89, 14.44) * mm, v(-12.73, 14.86) * mm, v(-12.6, 15.3) * mm, v(-12.45, 15.73) * mm]});
            skFitSpline(sketch, "E4335", {"points": [v(-12.45, 15.73) * mm, v(-12.43, 15.78) * mm, v(-12.4, 15.83) * mm, v(-12.38, 15.88) * mm]});
            skFitSpline(sketch, "E4336", {"points": [v(-12.38, 15.88) * mm, v(-12.26, 16.13) * mm, v(-12, 16.24) * mm, v(-11.77, 16.15) * mm]});
            skFitSpline(sketch, "E4337", {"points": [v(-11.77, 16.15) * mm, v(-11.52, 16.05) * mm, v(-11.4, 15.82) * mm, v(-11.48, 15.55) * mm]});
            skFitSpline(sketch, "E4338", {"points": [v(-11.48, 15.55) * mm, v(-11.53, 15.35) * mm, v(-11.6, 15.16) * mm, v(-11.66, 14.98) * mm]});
            skFitSpline(sketch, "E4339", {"points": [v(-11.66, 14.98) * mm, v(-11.86, 14.39) * mm, v(-12.07, 13.8) * mm, v(-12.28, 13.22) * mm]});
            skFitSpline(sketch, "E4340", {"points": [v(-12.28, 13.22) * mm, v(-12.3, 13.18) * mm, v(-12.3, 13.14) * mm, v(-12.33, 13.08) * mm]});
            skFitSpline(sketch, "E4341", {"points": [v(-12.33, 13.08) * mm, v(-12.27, 13.1) * mm, v(-12.23, 13.1) * mm, v(-12.19, 13.1) * mm]});
            skFitSpline(sketch, "E4342", {"points": [v(-12.19, 13.1) * mm, v(-11.75, 13.27) * mm, v(-11.3, 13.44) * mm, v(-10.87, 13.6) * mm]});
            skFitSpline(sketch, "E4343", {"points": [v(-10.87, 13.6) * mm, v(-10.53, 13.71) * mm, v(-10.18, 13.82) * mm, v(-9.84, 13.92) * mm]});
            skFitSpline(sketch, "E4344", {"points": [v(-9.84, 13.92) * mm, v(-9.57, 14) * mm, v(-9.33, 13.86) * mm, v(-9.24, 13.62) * mm]});
            skFitSpline(sketch, "E4345", {"points": [v(-9.24, 13.62) * mm, v(-9.15, 13.37) * mm, v(-9.26, 13.12) * mm, v(-9.52, 13) * mm]});
            skFitSpline(sketch, "E4346", {"points": [v(-9.52, 13) * mm, v(-9.76, 12.9) * mm, v(-10, 12.85) * mm, v(-10.25, 12.76) * mm]});
            skFitSpline(sketch, "E4347", {"points": [v(-10.25, 12.76) * mm, v(-10.8, 12.56) * mm, v(-11.36, 12.36) * mm, v(-11.9, 12.16) * mm]});
            skFitSpline(sketch, "E4348", {"points": [v(-11.9, 12.16) * mm, v(-12.16, 12.07) * mm, v(-12.41, 11.96) * mm, v(-12.67, 11.86) * mm]});
            skFitSpline(sketch, "E4349", {"points": [v(-12.67, 11.86) * mm, v(-12.75, 11.83) * mm, v(-12.82, 11.79) * mm, v(-12.85, 11.7) * mm]});
            skFitSpline(sketch, "E4350", {"points": [v(-12.85, 11.7) * mm, v(-13.14, 10.9) * mm, v(-13.44, 10.1) * mm, v(-13.73, 9.31) * mm]});
            skFitSpline(sketch, "E4351", {"points": [v(-13.73, 9.31) * mm, v(-13.76, 9.25) * mm, v(-13.77, 9.18) * mm, v(-13.8, 9.07) * mm]});
            skFitSpline(sketch, "E4352", {"points": [v(-13.8, 9.07) * mm, v(-13.72, 9.12) * mm, v(-13.66, 9.15) * mm, v(-13.6, 9.19) * mm]});
            skFitSpline(sketch, "E4353", {"points": [v(-13.6, 9.19) * mm, v(-13.21, 9.46) * mm, v(-12.82, 9.74) * mm, v(-12.43, 10.02) * mm]});
            skFitSpline(sketch, "E4354", {"points": [v(-12.43, 10.02) * mm, v(-12.2, 10.2) * mm, v(-12, 10.25) * mm, v(-11.7, 10.12) * mm]});
            skFitSpline(sketch, "E4355", {"points": [v(-11.7, 10.12) * mm, v(-11.4, 10) * mm, v(-11.06, 9.95) * mm, v(-10.74, 9.86) * mm]});
            skFitSpline(sketch, "E4356", {"points": [v(-10.74, 9.86) * mm, v(-10.35, 9.74) * mm, v(-9.96, 9.62) * mm, v(-9.58, 9.48) * mm]});
            skFitSpline(sketch, "E4357", {"points": [v(-9.58, 9.48) * mm, v(-9.36, 9.4) * mm, v(-9.23, 9.17) * mm, v(-9.25, 8.97) * mm]});
            skFitSpline(sketch, "E4358", {"points": [v(-9.25, 8.97) * mm, v(-9.27, 8.76) * mm, v(-9.4, 8.58) * mm, v(-9.61, 8.54) * mm]});
            skFitSpline(sketch, "E4359", {"points": [v(-9.61, 8.54) * mm, v(-9.7, 8.52) * mm, v(-9.83, 8.52) * mm, v(-9.91, 8.56) * mm]});
            skFitSpline(sketch, "E4360", {"points": [v(-9.91, 8.56) * mm, v(-10.48, 8.8) * mm, v(-11.08, 8.93) * mm, v(-11.67, 9.1) * mm]});
            skFitSpline(sketch, "E4361", {"points": [v(-11.67, 9.1) * mm, v(-11.86, 9.16) * mm, v(-12.01, 9.14) * mm, v(-12.18, 9.01) * mm]});
            skFitSpline(sketch, "E4362", {"points": [v(-12.18, 9.01) * mm, v(-12.67, 8.65) * mm, v(-13.17, 8.3) * mm, v(-13.67, 7.96) * mm]});
            skFitSpline(sketch, "E4363", {"points": [v(-13.67, 7.96) * mm, v(-13.73, 7.91) * mm, v(-13.8, 7.87) * mm, v(-13.88, 7.8) * mm]});
            skFitSpline(sketch, "E4364", {"points": [v(-13.88, 7.8) * mm, v(-13.79, 7.76) * mm, v(-13.72, 7.73) * mm, v(-13.65, 7.7) * mm]});
            skFitSpline(sketch, "E4365", {"points": [v(-13.65, 7.7) * mm, v(-13.11, 7.44) * mm, v(-12.58, 7.2) * mm, v(-12.05, 6.93) * mm]});
            skFitSpline(sketch, "E4366", {"points": [v(-12.05, 6.93) * mm, v(-11.85, 6.84) * mm, v(-11.77, 6.67) * mm, v(-11.8, 6.46) * mm]});
            skFitSpline(sketch, "E4367", {"points": [v(-11.8, 6.46) * mm, v(-11.8, 6.39) * mm, v(-11.83, 6.32) * mm, v(-11.84, 6.24) * mm]});
            skFitSpline(sketch, "E4368", {"points": [v(-11.84, 6.24) * mm, v(-11.82, 6.23) * mm, v(-11.8, 6.21) * mm, v(-11.77, 6.2) * mm]});
            skFitSpline(sketch, "E4369", {"points": [v(-11.77, 6.2) * mm, v(-11.5, 6.04) * mm, v(-11.42, 5.83) * mm, v(-11.53, 5.53) * mm]});
            skFitSpline(sketch, "E4370", {"points": [v(-11.53, 5.53) * mm, v(-11.74, 4.94) * mm, v(-11.95, 4.36) * mm, v(-12.16, 3.77) * mm]});
            skFitSpline(sketch, "E4371", {"points": [v(-12.16, 3.77) * mm, v(-12.16, 3.76) * mm, v(-12.16, 3.74) * mm, v(-12.15, 3.7) * mm]});
            skFitSpline(sketch, "E4372", {"points": [v(-12.15, 3.7) * mm, v(-12, 3.73) * mm, v(-11.86, 3.75) * mm, v(-11.7, 3.77) * mm]});
            skFitSpline(sketch, "E4373", {"points": [v(-11.7, 3.77) * mm, v(-11.16, 3.87) * mm, v(-10.6, 3.97) * mm, v(-10.06, 4.05) * mm]});
            skFitSpline(sketch, "E4374", {"points": [v(-10.06, 4.05) * mm, v(-9.9, 4.08) * mm, v(-9.8, 4.15) * mm, v(-9.74, 4.27) * mm]});
            skFitSpline(sketch, "E4375", {"points": [v(-9.74, 4.27) * mm, v(-9.44, 4.82) * mm, v(-9.08, 5.33) * mm, v(-8.86, 5.92) * mm]});
            skFitSpline(sketch, "E4376", {"points": [v(-8.86, 5.92) * mm, v(-8.8, 6.1) * mm, v(-8.67, 6.23) * mm, v(-8.47, 6.26) * mm]});
            skFitSpline(sketch, "E4377", {"points": [v(-8.47, 6.26) * mm, v(-8.11, 6.3) * mm, v(-7.86, 6) * mm, v(-7.93, 5.65) * mm]});
            skFitSpline(sketch, "E4378", {"points": [v(-7.93, 5.65) * mm, v(-7.94, 5.6) * mm, v(-7.94, 5.57) * mm, v(-7.96, 5.53) * mm]});
            skFitSpline(sketch, "E4379", {"points": [v(-7.96, 5.53) * mm, v(-8.1, 5.24) * mm, v(-8.22, 4.95) * mm, v(-8.37, 4.67) * mm]});
            skFitSpline(sketch, "E4380", {"points": [v(-8.37, 4.67) * mm, v(-8.56, 4.33) * mm, v(-8.77, 4.01) * mm, v(-8.96, 3.68) * mm]});
            skFitSpline(sketch, "E4381", {"points": [v(-8.96, 3.68) * mm, v(-8.98, 3.65) * mm, v(-9, 3.61) * mm, v(-9.02, 3.58) * mm]});
            skFitSpline(sketch, "E4382", {"points": [v(-9.02, 3.58) * mm, v(-9.09, 3.3) * mm, v(-9.28, 3.2) * mm, v(-9.54, 3.16) * mm]});
            skFitSpline(sketch, "E4383", {"points": [v(-9.54, 3.16) * mm, v(-10.05, 3.08) * mm, v(-10.56, 2.99) * mm, v(-11.08, 2.9) * mm]});
            skFitSpline(sketch, "E4384", {"points": [v(-11.08, 2.9) * mm, v(-11.11, 2.9) * mm, v(-11.15, 2.88) * mm, v(-11.2, 2.83) * mm]});
            skFitSpline(sketch, "E4385", {"points": [v(-11.2, 2.83) * mm, v(-11.03, 2.75) * mm, v(-10.86, 2.66) * mm, v(-10.7, 2.58) * mm]});
            skFitSpline(sketch, "E4386", {"points": [v(-10.7, 2.58) * mm, v(-10.48, 2.48) * mm, v(-10.26, 2.39) * mm, v(-10.04, 2.3) * mm]});
            skFitSpline(sketch, "E4387", {"points": [v(-10.04, 2.3) * mm, v(-9.6, 2.09) * mm, v(-9.15, 1.89) * mm, v(-8.71, 1.68) * mm]});
            skFitSpline(sketch, "E4388", {"points": [v(-8.71, 1.68) * mm, v(-8.62, 1.64) * mm, v(-8.55, 1.64) * mm, v(-8.46, 1.68) * mm]});
            skFitSpline(sketch, "E4389", {"points": [v(-8.46, 1.68) * mm, v(-7.9, 1.93) * mm, v(-7.35, 2.17) * mm, v(-6.8, 2.43) * mm]});
            skFitSpline(sketch, "E4390", {"points": [v(-6.8, 2.43) * mm, v(-6.39, 2.63) * mm, v(-5.97, 2.84) * mm, v(-5.56, 3.04) * mm]});
            skFitSpline(sketch, "E4391", {"points": [v(-5.56, 3.04) * mm, v(-5.5, 3.07) * mm, v(-5.43, 3.1) * mm, v(-5.36, 3.12) * mm]});
            skFitSpline(sketch, "E4392", {"points": [v(-5.36, 3.12) * mm, v(-5.12, 3.19) * mm, v(-4.88, 3.07) * mm, v(-4.78, 2.85) * mm]});
            skFitSpline(sketch, "E4393", {"points": [v(-4.78, 2.85) * mm, v(-4.68, 2.63) * mm, v(-4.76, 2.38) * mm, v(-4.97, 2.25) * mm]});
            skFitSpline(sketch, "E4394", {"points": [v(-4.97, 2.25) * mm, v(-5.05, 2.2) * mm, v(-5.14, 2.16) * mm, v(-5.22, 2.12) * mm]});
            skFitSpline(sketch, "E4395", {"points": [v(-5.22, 2.12) * mm, v(-5.88, 1.8) * mm, v(-6.53, 1.49) * mm, v(-7.19, 1.17) * mm]});
            skFitSpline(sketch, "E4396", {"points": [v(-7.19, 1.17) * mm, v(-7.24, 1.15) * mm, v(-7.28, 1.12) * mm, v(-7.36, 1.09) * mm]});
            skFitSpline(sketch, "E4397", {"points": [v(-7.36, 1.09) * mm, v(-7.3, 1.05) * mm, v(-7.26, 1.02) * mm, v(-7.22, 1) * mm]});
            skFitSpline(sketch, "E4398", {"points": [v(-7.22, 1) * mm, v(-6.79, 0.8) * mm, v(-6.35, 0.6) * mm, v(-5.92, 0.4) * mm]});
            skFitSpline(sketch, "E4399", {"points": [v(-5.92, 0.4) * mm, v(-5.6, 0.25) * mm, v(-5.3, 0.09) * mm, v(-5, -0.08) * mm]});
            skFitSpline(sketch, "E4400", {"points": [v(-5, -0.08) * mm, v(-4.76, -0.21) * mm, v(-4.67, -0.48) * mm, v(-4.78, -0.71) * mm]});
            skFitSpline(sketch, "E4401", {"points": [v(-4.78, -0.71) * mm, v(-4.9, -0.95) * mm, v(-5.16, -1.05) * mm, v(-5.41, -0.95) * mm]});
            skFitSpline(sketch, "E4402", {"points": [v(-5.41, -0.95) * mm, v(-5.61, -0.87) * mm, v(-5.8, -0.76) * mm, v(-6, -0.67) * mm]});
            skFitSpline(sketch, "E4403", {"points": [v(-6, -0.67) * mm, v(-6.66, -0.35) * mm, v(-7.32, -0.04) * mm, v(-7.99, 0.26) * mm]});
            skFitSpline(sketch, "E4404", {"points": [v(-7.99, 0.26) * mm, v(-8.18, 0.35) * mm, v(-8.37, 0.48) * mm, v(-8.56, 0.49) * mm]});
            skFitSpline(sketch, "E4405", {"points": [v(-8.56, 0.49) * mm, v(-8.75, 0.49) * mm, v(-8.94, 0.36) * mm, v(-9.13, 0.27) * mm]});
            skFitSpline(sketch, "E4406", {"points": [v(-9.13, 0.27) * mm, v(-9.4, 0.15) * mm, v(-9.68, 0.02) * mm, v(-9.96, -0.1) * mm]});
            skFitSpline(sketch, "E4407", {"points": [v(-9.96, -0.1) * mm, v(-10.33, -0.27) * mm, v(-10.7, -0.44) * mm, v(-11.07, -0.61) * mm]});
            skFitSpline(sketch, "E4408", {"points": [v(-11.07, -0.61) * mm, v(-11.12, -0.64) * mm, v(-11.16, -0.67) * mm, v(-11.25, -0.72) * mm]});
            skFitSpline(sketch, "E4409", {"points": [v(-11.25, -0.72) * mm, v(-10.8, -0.8) * mm, v(-10.4, -0.87) * mm, v(-10, -0.94) * mm]});
            skFitSpline(sketch, "E4410", {"points": [v(-10, -0.94) * mm, v(-9.8, -0.97) * mm, v(-9.6, -1) * mm, v(-9.41, -1.04) * mm]});
            skFitSpline(sketch, "E4411", {"points": [v(-9.41, -1.04) * mm, v(-9.24, -1.07) * mm, v(-9.13, -1.17) * mm, v(-9.05, -1.32) * mm]});
            skFitSpline(sketch, "E4412", {"points": [v(-9.05, -1.32) * mm, v(-8.89, -1.63) * mm, v(-8.71, -1.94) * mm, v(-8.55, -2.25) * mm]});
            skFitSpline(sketch, "E4413", {"points": [v(-8.55, -2.25) * mm, v(-8.35, -2.62) * mm, v(-8.15, -3) * mm, v(-7.96, -3.37) * mm]});
            skFitSpline(sketch, "E4414", {"points": [v(-7.96, -3.37) * mm, v(-7.9, -3.5) * mm, v(-7.89, -3.63) * mm, v(-7.94, -3.77) * mm]});
            skFitSpline(sketch, "E4415", {"points": [v(-7.94, -3.77) * mm, v(-8, -3.96) * mm, v(-8.13, -4.08) * mm, v(-8.33, -4.1) * mm]});
            skFitSpline(sketch, "E4416", {"points": [v(-8.33, -4.1) * mm, v(-8.54, -4.13) * mm, v(-8.71, -4.06) * mm, v(-8.82, -3.87) * mm]});
            skFitSpline(sketch, "E4417", {"points": [v(-8.82, -3.87) * mm, v(-8.86, -3.8) * mm, v(-8.88, -3.74) * mm, v(-8.9, -3.67) * mm]});
            skFitSpline(sketch, "E4418", {"points": [v(-8.9, -3.67) * mm, v(-9.11, -3.12) * mm, v(-9.46, -2.65) * mm, v(-9.73, -2.14) * mm]});
            skFitSpline(sketch, "E4419", {"points": [v(-9.73, -2.14) * mm, v(-9.8, -2.02) * mm, v(-9.87, -1.94) * mm, v(-10.02, -1.91) * mm]});
            skFitSpline(sketch, "E4420", {"points": [v(-10.02, -1.91) * mm, v(-10.7, -1.8) * mm, v(-11.36, -1.68) * mm, v(-12.03, -1.57) * mm]});
            skFitSpline(sketch, "E4421", {"points": [v(-12.03, -1.57) * mm, v(-12.07, -1.56) * mm, v(-12.1, -1.56) * mm, v(-12.16, -1.56) * mm]});
            skFitSpline(sketch, "E4422", {"points": [v(-12.16, -1.56) * mm, v(-12.14, -1.63) * mm, v(-12.13, -1.7) * mm, v(-12.1, -1.75) * mm]});
            skFitSpline(sketch, "E4423", {"points": [v(-12.1, -1.75) * mm, v(-11.9, -2.3) * mm, v(-11.7, -2.86) * mm, v(-11.51, -3.42) * mm]});
            skFitSpline(sketch, "E4424", {"points": [v(-11.51, -3.42) * mm, v(-11.42, -3.7) * mm, v(-11.5, -3.91) * mm, v(-11.76, -4.04) * mm]});
            skFitSpline(sketch, "E4425", {"points": [v(-11.76, -4.04) * mm, v(-11.79, -4.06) * mm, v(-11.82, -4.07) * mm, v(-11.85, -4.09) * mm]});
            skFitSpline(sketch, "E4426", {"points": [v(-11.85, -4.09) * mm, v(-11.83, -4.14) * mm, v(-11.81, -4.19) * mm, v(-11.8, -4.23) * mm]});
            skFitSpline(sketch, "E4427", {"points": [v(-11.8, -4.23) * mm, v(-11.75, -4.49) * mm, v(-11.85, -4.7) * mm, v(-12.08, -4.8) * mm]});
            skFitSpline(sketch, "E4428", {"points": [v(-12.08, -4.8) * mm, v(-12.65, -5.07) * mm, v(-13.22, -5.34) * mm, v(-13.8, -5.6) * mm]});
            skFitSpline(sketch, "E4429", {"points": [v(-13.8, -5.6) * mm, v(-13.82, -5.62) * mm, v(-13.83, -5.64) * mm, v(-13.86, -5.66) * mm]});
            skFitSpline(sketch, "E4430", {"points": [v(-13.86, -5.66) * mm, v(-13.8, -5.71) * mm, v(-13.74, -5.76) * mm, v(-13.67, -5.8) * mm]});
            skFitSpline(sketch, "E4431", {"points": [v(-13.67, -5.8) * mm, v(-13.16, -6.16) * mm, v(-12.65, -6.52) * mm, v(-12.15, -6.89) * mm]});
            skFitSpline(sketch, "E4432", {"points": [v(-12.15, -6.89) * mm, v(-12.01, -6.99) * mm, v(-11.88, -7.02) * mm, v(-11.73, -6.97) * mm]});
            skFitSpline(sketch, "E4433", {"points": [v(-11.73, -6.97) * mm, v(-11.14, -6.79) * mm, v(-10.53, -6.68) * mm, v(-9.97, -6.43) * mm]});
            skFitSpline(sketch, "E4434", {"points": [v(-9.97, -6.43) * mm, v(-9.67, -6.3) * mm, v(-9.4, -6.4) * mm, v(-9.29, -6.67) * mm]});
            skFitSpline(sketch, "E4435", {"points": [v(-9.29, -6.67) * mm, v(-9.18, -6.93) * mm, v(-9.3, -7.22) * mm, v(-9.6, -7.33) * mm]});
            skFitSpline(sketch, "E4436", {"points": [v(-9.6, -7.33) * mm, v(-9.93, -7.47) * mm, v(-10.28, -7.58) * mm, v(-10.63, -7.69) * mm]});
            skFitSpline(sketch, "E4437", {"points": [v(-10.63, -7.69) * mm, v(-11.04, -7.81) * mm, v(-11.44, -7.92) * mm, v(-11.85, -8.03) * mm]});
            skFitSpline(sketch, "E4438", {"points": [v(-11.85, -8.03) * mm, v(-12.04, -8.1) * mm, v(-12.2, -8.03) * mm, v(-12.37, -7.92) * mm]});
            skFitSpline(sketch, "E4439", {"points": [v(-12.37, -7.92) * mm, v(-12.72, -7.67) * mm, v(-13.07, -7.42) * mm, v(-13.42, -7.17) * mm]});
            skFitSpline(sketch, "E4440", {"points": [v(-13.42, -7.17) * mm, v(-13.53, -7.09) * mm, v(-13.65, -7) * mm, v(-13.77, -6.93) * mm]});
            skFitSpline(sketch, "E4441", {"points": [v(-13.77, -6.93) * mm, v(-13.78, -6.94) * mm, v(-13.8, -6.94) * mm, v(-13.8, -6.95) * mm]});
            skSolve(sketch);
        }
        {
            var Q0;
            Q0=makeQuery(id+"F0.imprint","IMPRINT",FACE,{"disambiguationData":[TD([[makeQuery(id+"F0.imprint","IMPRINT",EDGE,{"derivedFrom":sQuery(id+"F0.wireOp",EDGE,"E678")}),-1.0]])]});
            var Q1;
            Q1=makeQuery(id+"F0.imprint","IMPRINT",FACE,{"disambiguationData":[TD([[makeQuery(id+"F0.imprint","IMPRINT",EDGE,{"derivedFrom":sQuery(id+"F0.wireOp",EDGE,"E2128")}),-1.0]])]});
            var Q2;
            Q2=makeQuery(id+"F0.imprint","IMPRINT",FACE,{"disambiguationData":[TD([[makeQuery(id+"F0.imprint","IMPRINT",EDGE,{"derivedFrom":sQuery(id+"F0.wireOp",EDGE,"E3714")}),-1.0]])]});
            var Q3;
            Q3=makeQuery(id+"F0.imprint","IMPRINT",FACE,{"disambiguationData":[TD([[makeQuery(id+"F0.imprint","IMPRINT",EDGE,{"derivedFrom":sQuery(id+"F0.wireOp",EDGE,"E0")}),-1.0]])]});
            var Q4;
            Q4=makeQuery(id+"F0.imprint","IMPRINT",FACE,{"disambiguationData":[TD([[makeQuery(id+"F0.imprint","IMPRINT",EDGE,{"derivedFrom":sQuery(id+"F0.wireOp",EDGE,"E2845")}),-1.0]])]});
            var Q5;
            {var subQ4=sQuery(id+"F0.wireOp",EDGE,"E1458");Q5=makeQuery(id+"F0.imprint","IMPRINT",FACE,{"disambiguationData":[TD([[makeQuery(id+"F0.imprint","IMPRINT",EDGE,{"derivedFrom":subQ4}),-1.0]])]});}
            extrude(context, id + "F1", {"entities" : qUnion([Q0, Q1, Q2, Q3, Q4, Q5]), "depth" : 0.8 * mm});
        }
    });
